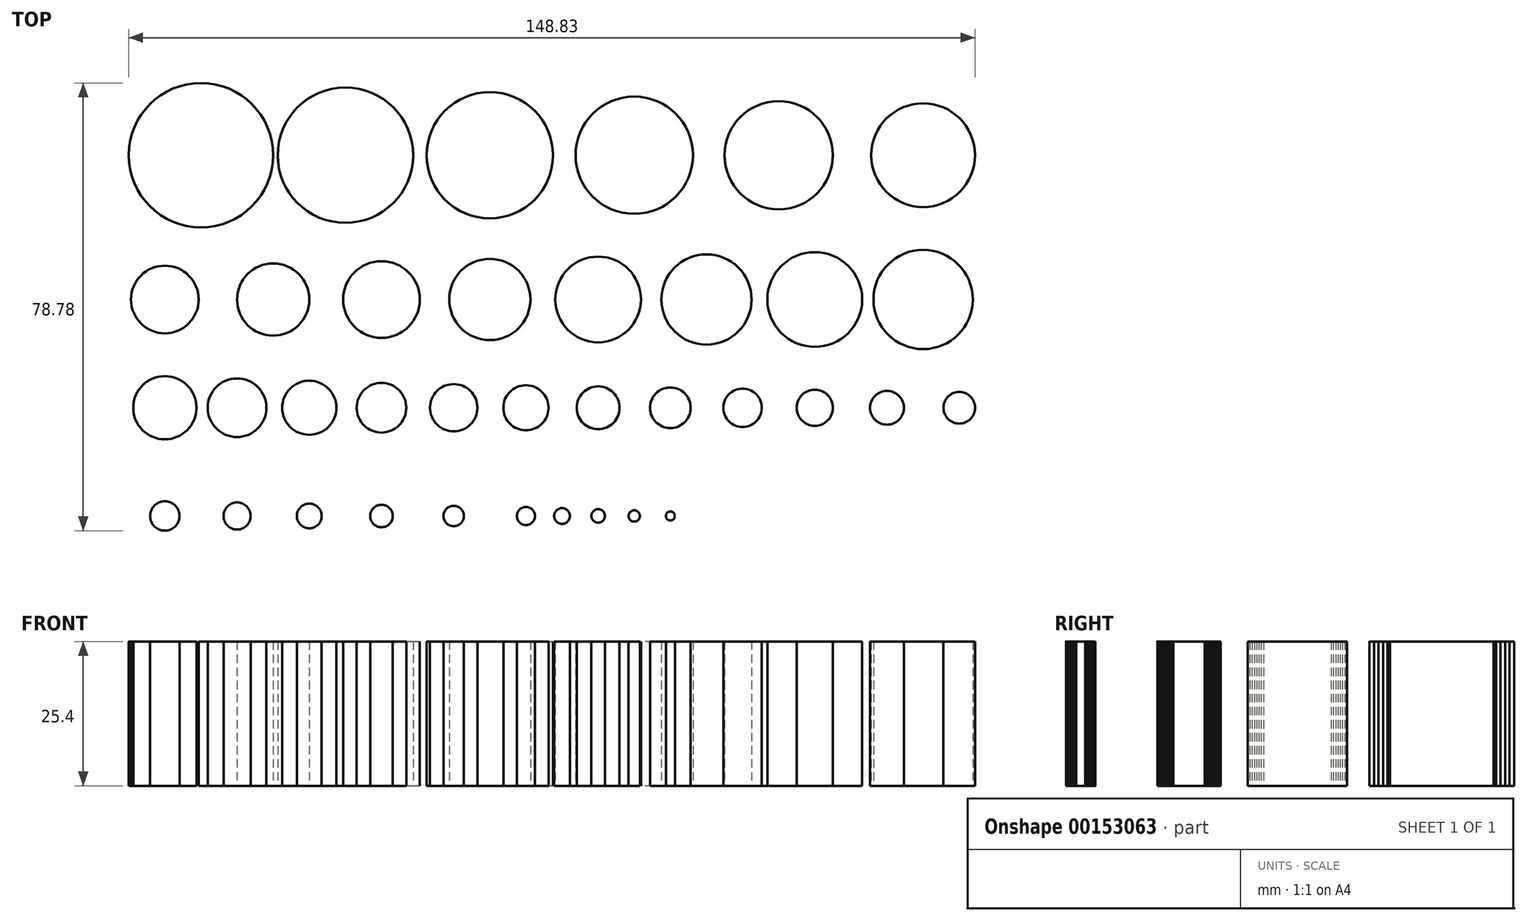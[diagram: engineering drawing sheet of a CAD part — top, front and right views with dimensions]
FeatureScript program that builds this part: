
annotation { "Feature Type Name" : "Feature", "Feature Type Description" : "" }
export const myFeature = defineFeature(function(context is Context, id is Id, definition is map)
    precondition{}
    {
        {
            var Q0;
            Q0=qCreatedBy(makeId("Top.planeOp"),FACE);
            var sketch = newSketch(context, id + "F0", { "sketchPlane" : qUnion([Q0])});
            skLineSegment(sketch, "E0", {"start": v(0, 82.73) * mm, "end": v(0, -103.9) * mm});
            skLineSegment(sketch, "E1.1.0.0", {"start": v(6.35, 82.73) * mm, "end": v(6.35, -103.9) * mm});
            skLineSegment(sketch, "E1.2.0.0", {"start": v(12.7, 82.73) * mm, "end": v(12.7, -103.9) * mm});
            skLineSegment(sketch, "E1.3.0.0", {"start": v(19.05, 82.73) * mm, "end": v(19.05, -103.9) * mm});
            skLineSegment(sketch, "E1.4.0.0", {"start": v(25.4, 82.73) * mm, "end": v(25.4, -103.9) * mm});
            skLineSegment(sketch, "E1.5.0.0", {"start": v(31.75, 82.73) * mm, "end": v(31.75, -103.9) * mm});
            skLineSegment(sketch, "E1.direction1", {"start": v(0, -103.9) * mm, "end": v(6.35, -103.9) * mm, "construction": true});
            skLineSegment(sketch, "E2.MirrorCS", {"start": v(63.5, 82.73) * mm, "end": v(63.5, -103.9) * mm});
            skLineSegment(sketch, "E3.MirrorCS", {"start": v(57.15, 82.73) * mm, "end": v(57.15, -103.9) * mm});
            skLineSegment(sketch, "E4.MirrorCS", {"start": v(50.8, 82.73) * mm, "end": v(50.8, -103.9) * mm});
            skLineSegment(sketch, "E5.MirrorCS", {"start": v(44.45, 82.73) * mm, "end": v(44.45, -103.9) * mm});
            skLineSegment(sketch, "E6.MirrorCS", {"start": v(38.1, 82.73) * mm, "end": v(38.1, -103.9) * mm});
            skLineSegment(sketch, "E7.MirrorCS", {"start": v(-6.35, 82.73) * mm, "end": v(-6.35, -103.9) * mm});
            skLineSegment(sketch, "E8.MirrorCS", {"start": v(-12.7, 82.73) * mm, "end": v(-12.7, -103.9) * mm});
            skLineSegment(sketch, "E9.MirrorCS", {"start": v(-19.05, 82.73) * mm, "end": v(-19.05, -103.9) * mm});
            skLineSegment(sketch, "E10.MirrorCS", {"start": v(-25.4, 82.73) * mm, "end": v(-25.4, -103.9) * mm});
            skLineSegment(sketch, "E11.MirrorCS", {"start": v(-31.75, 82.73) * mm, "end": v(-31.75, -103.9) * mm});
            skLineSegment(sketch, "E12.MirrorCS", {"start": v(-38.1, 82.73) * mm, "end": v(-38.1, -103.9) * mm});
            skLineSegment(sketch, "E13.MirrorCS", {"start": v(-44.45, 82.73) * mm, "end": v(-44.45, -103.9) * mm});
            skLineSegment(sketch, "E14.MirrorCS", {"start": v(-50.8, 82.73) * mm, "end": v(-50.8, -103.9) * mm});
            skLineSegment(sketch, "E15.MirrorCS", {"start": v(-57.15, 82.73) * mm, "end": v(-57.15, -103.9) * mm});
            skLineSegment(sketch, "E16.MirrorCS", {"start": v(-63.5, 82.73) * mm, "end": v(-63.5, -103.9) * mm});
            skLineSegment(sketch, "E17.MirrorCS", {"start": v(69.85, 82.73) * mm, "end": v(69.85, -103.9) * mm});
            skLineSegment(sketch, "E18.MirrorCS", {"start": v(76.2, 82.73) * mm, "end": v(76.2, -103.9) * mm});
            skLineSegment(sketch, "E19.MirrorCS", {"start": v(-69.85, 82.73) * mm, "end": v(-69.85, -103.9) * mm});
            skLineSegment(sketch, "E20.MirrorCS", {"start": v(-76.2, 82.73) * mm, "end": v(-76.2, -103.9) * mm});
            skLineSegment(sketch, "E21", {"start": v(-128.57, -86.78) * mm, "end": v(191.02, -86.78) * mm});
            skLineSegment(sketch, "E22.0.1.0", {"start": v(-128.57, -80.43) * mm, "end": v(191.02, -80.43) * mm});
            skLineSegment(sketch, "E22.0.2.0", {"start": v(-128.57, -74.08) * mm, "end": v(191.02, -74.08) * mm});
            skLineSegment(sketch, "E22.0.3.0", {"start": v(-128.57, -67.73) * mm, "end": v(191.02, -67.73) * mm});
            skLineSegment(sketch, "E22.0.4.0", {"start": v(-128.57, -61.38) * mm, "end": v(191.02, -61.38) * mm});
            skLineSegment(sketch, "E22.0.5.0", {"start": v(-128.57, -55.03) * mm, "end": v(191.02, -55.03) * mm});
            skLineSegment(sketch, "E22.0.6.0", {"start": v(-128.57, -48.68) * mm, "end": v(191.02, -48.68) * mm});
            skLineSegment(sketch, "E22.0.7.0", {"start": v(-128.57, -42.33) * mm, "end": v(191.02, -42.33) * mm});
            skLineSegment(sketch, "E22.0.8.0", {"start": v(-128.57, -35.98) * mm, "end": v(191.02, -35.98) * mm});
            skLineSegment(sketch, "E22.0.9.0", {"start": v(-128.57, -29.63) * mm, "end": v(191.02, -29.63) * mm});
            skLineSegment(sketch, "E22.0.10.0", {"start": v(-128.57, -23.28) * mm, "end": v(191.02, -23.28) * mm});
            skLineSegment(sketch, "E22.0.11.0", {"start": v(-128.57, -16.93) * mm, "end": v(191.02, -16.93) * mm});
            skLineSegment(sketch, "E22.0.12.0", {"start": v(-128.57, -10.58) * mm, "end": v(191.02, -10.58) * mm});
            skLineSegment(sketch, "E22.0.13.0", {"start": v(-128.57, -4.23) * mm, "end": v(191.02, -4.23) * mm});
            skLineSegment(sketch, "E22.0.14.0", {"start": v(-128.57, 2.12) * mm, "end": v(191.02, 2.12) * mm});
            skLineSegment(sketch, "E22.direction1", {"start": v(-128.57, -86.78) * mm, "end": v(-103.17, -86.78) * mm, "construction": true});
            skLineSegment(sketch, "E22.direction2", {"start": v(-128.57, -86.78) * mm, "end": v(-128.57, -80.43) * mm, "construction": true});
            skLineSegment(sketch, "E23.MirrorCS", {"start": v(-128.57, 27.52) * mm, "end": v(191.02, 27.52) * mm});
            skLineSegment(sketch, "E24.MirrorCS", {"start": v(-128.57, 21.17) * mm, "end": v(191.02, 21.17) * mm});
            skLineSegment(sketch, "E25.MirrorCS", {"start": v(-128.57, 78.32) * mm, "end": v(191.02, 78.32) * mm});
            skLineSegment(sketch, "E26.MirrorCS", {"start": v(-128.57, 71.97) * mm, "end": v(191.02, 71.97) * mm});
            skLineSegment(sketch, "E27.MirrorCS", {"start": v(-128.57, 65.62) * mm, "end": v(191.02, 65.62) * mm});
            skLineSegment(sketch, "E28.MirrorCS", {"start": v(-128.57, 59.27) * mm, "end": v(191.02, 59.27) * mm});
            skLineSegment(sketch, "E29.MirrorCS", {"start": v(-128.57, 52.92) * mm, "end": v(191.02, 52.92) * mm});
            skLineSegment(sketch, "E30.MirrorCS", {"start": v(-128.57, 46.57) * mm, "end": v(191.02, 46.57) * mm});
            skLineSegment(sketch, "E31.MirrorCS", {"start": v(-128.57, 40.22) * mm, "end": v(191.02, 40.22) * mm});
            skLineSegment(sketch, "E32.MirrorCS", {"start": v(-128.57, 33.87) * mm, "end": v(191.02, 33.87) * mm});
            skLineSegment(sketch, "E33.MirrorCS", {"start": v(-128.57, 8.47) * mm, "end": v(191.02, 8.47) * mm});
            skLineSegment(sketch, "E34.MirrorCS", {"start": v(-128.57, 14.82) * mm, "end": v(191.02, 14.82) * mm});
            skSolve(sketch);
        }
        {
            var Q0;
            Q0=qCreatedBy(makeId("Top.planeOp"),FACE);
            var sketch = newSketch(context, id + "F1", { "sketchPlane" : qUnion([Q0])});
            skPoint(sketch, "E35", {"position": v(-57.15, 71.97) * mm});
            skPoint(sketch, "E36.1.0.0", {"position": v(-50.8, 71.97) * mm});
            skPoint(sketch, "E36.2.0.0", {"position": v(-44.45, 71.97) * mm});
            skPoint(sketch, "E36.3.0.0", {"position": v(-38.1, 71.97) * mm});
            skPoint(sketch, "E36.4.0.0", {"position": v(-31.75, 71.97) * mm});
            skPoint(sketch, "E36.5.0.0", {"position": v(-25.4, 71.97) * mm});
            skPoint(sketch, "E36.6.0.0", {"position": v(-19.05, 71.97) * mm});
            skPoint(sketch, "E36.7.0.0", {"position": v(-12.7, 71.97) * mm});
            skPoint(sketch, "E36.8.0.0", {"position": v(-6.35, 71.97) * mm});
            skPoint(sketch, "E36.9.0.0", {"position": v(0, 71.97) * mm});
            skPoint(sketch, "E37.1.0.0", {"position": v(-63.5, 71.97) * mm});
            skPoint(sketch, "E37.2.0.0", {"position": v(-69.85, 71.97) * mm});
            skPoint(sketch, "E37.3.0.0", {"position": v(-76.2, 71.97) * mm});
            skLineSegment(sketch, "E37.direction1", {"start": v(-57.15, 71.97) * mm, "end": v(-63.5, 71.97) * mm, "construction": true});
            skPoint(sketch, "E38.0.1.0", {"position": v(-76.2, 65.62) * mm});
            skPoint(sketch, "E38.0.2.0", {"position": v(-76.2, 59.27) * mm});
            skPoint(sketch, "E38.0.3.0", {"position": v(-76.2, 52.92) * mm});
            skPoint(sketch, "E38.0.4.0", {"position": v(-76.2, 46.57) * mm});
            skPoint(sketch, "E38.0.5.0", {"position": v(-76.2, 40.22) * mm});
            skPoint(sketch, "E38.0.6.0", {"position": v(-76.2, 33.87) * mm});
            skPoint(sketch, "E38.0.7.0", {"position": v(-76.2, 27.52) * mm});
            skPoint(sketch, "E38.0.8.0", {"position": v(-76.2, 21.17) * mm});
            skPoint(sketch, "E38.0.9.0", {"position": v(-76.2, 14.82) * mm});
            skPoint(sketch, "E38.0.10.0", {"position": v(-76.2, 8.47) * mm});
            skPoint(sketch, "E38.0.11.0", {"position": v(-76.2, 2.12) * mm});
            skPoint(sketch, "E38.0.12.0", {"position": v(-76.2, -4.23) * mm});
            skPoint(sketch, "E38.0.13.0", {"position": v(-76.2, -10.58) * mm});
            skPoint(sketch, "E38.0.14.0", {"position": v(-76.2, -16.93) * mm});
            skPoint(sketch, "E38.0.15.0", {"position": v(-76.2, -23.28) * mm});
            skPoint(sketch, "E38.0.16.0", {"position": v(-76.2, -29.63) * mm});
            skPoint(sketch, "E38.0.17.0", {"position": v(-76.2, -35.98) * mm});
            skPoint(sketch, "E38.0.18.0", {"position": v(-76.2, -42.33) * mm});
            skPoint(sketch, "E38.0.19.0", {"position": v(-76.2, -48.68) * mm});
            skPoint(sketch, "E38.0.20.0", {"position": v(-76.2, -55.03) * mm});
            skPoint(sketch, "E38.0.21.0", {"position": v(-76.2, -61.38) * mm});
            skPoint(sketch, "E38.0.22.0", {"position": v(-76.2, -67.73) * mm});
            skPoint(sketch, "E38.0.23.0", {"position": v(-76.2, -74.08) * mm});
            skPoint(sketch, "E38.0.24.0", {"position": v(-76.2, -80.43) * mm});
            skPoint(sketch, "E38.0.25.0", {"position": v(-76.2, -86.78) * mm});
            skPoint(sketch, "E38.0.26.0", {"position": v(-76.2, -93.13) * mm});
            skPoint(sketch, "E38.0.27.0", {"position": v(-76.2, -99.48) * mm});
            skPoint(sketch, "E38.0.28.0", {"position": v(-76.2, -105.83) * mm});
            skPoint(sketch, "E38.0.29.0", {"position": v(-76.2, -112.18) * mm});
            skPoint(sketch, "E38.0.30.0", {"position": v(-76.2, -118.53) * mm});
            skPoint(sketch, "E38.0.31.0", {"position": v(-76.2, -124.88) * mm});
            skPoint(sketch, "E38.0.32.0", {"position": v(-76.2, -131.23) * mm});
            skPoint(sketch, "E38.0.33.0", {"position": v(-76.2, -137.58) * mm});
            skPoint(sketch, "E38.0.34.0", {"position": v(-76.2, -143.93) * mm});
            skPoint(sketch, "E38.0.35.0", {"position": v(-76.2, -150.28) * mm});
            skPoint(sketch, "E38.0.36.0", {"position": v(-76.2, -156.63) * mm});
            skPoint(sketch, "E38.0.37.0", {"position": v(-76.2, -162.98) * mm});
            skPoint(sketch, "E38.0.38.0", {"position": v(-76.2, -169.33) * mm});
            skPoint(sketch, "E38.0.39.0", {"position": v(-76.2, -175.68) * mm});
            skPoint(sketch, "E38.0.40.0", {"position": v(-76.2, -182.03) * mm});
            skPoint(sketch, "E38.0.41.0", {"position": v(-76.2, -188.38) * mm});
            skPoint(sketch, "E38.0.42.0", {"position": v(-76.2, -194.73) * mm});
            skPoint(sketch, "E38.0.43.0", {"position": v(-76.2, -201.08) * mm});
            skPoint(sketch, "E38.0.44.0", {"position": v(-76.2, -207.43) * mm});
            skPoint(sketch, "E38.0.45.0", {"position": v(-76.2, -213.78) * mm});
            skPoint(sketch, "E38.0.46.0", {"position": v(-76.2, -220.13) * mm});
            skPoint(sketch, "E38.0.47.0", {"position": v(-76.2, -226.48) * mm});
            skPoint(sketch, "E38.0.48.0", {"position": v(-76.2, -232.83) * mm});
            skPoint(sketch, "E38.0.49.0", {"position": v(-76.2, -239.18) * mm});
            skPoint(sketch, "E38.0.50.0", {"position": v(-76.2, -245.53) * mm});
            skPoint(sketch, "E38.0.51.0", {"position": v(-76.2, -251.88) * mm});
            skPoint(sketch, "E38.0.52.0", {"position": v(-76.2, -258.23) * mm});
            skPoint(sketch, "E38.0.53.0", {"position": v(-76.2, -264.58) * mm});
            skPoint(sketch, "E38.0.54.0", {"position": v(-76.2, -270.93) * mm});
            skPoint(sketch, "E38.0.55.0", {"position": v(-76.2, -277.28) * mm});
            skPoint(sketch, "E38.0.56.0", {"position": v(-76.2, -283.63) * mm});
            skPoint(sketch, "E38.0.57.0", {"position": v(-76.2, -289.98) * mm});
            skPoint(sketch, "E38.0.58.0", {"position": v(-76.2, -296.33) * mm});
            skPoint(sketch, "E38.0.59.0", {"position": v(-76.2, -302.68) * mm});
            skPoint(sketch, "E38.0.60.0", {"position": v(-76.2, -309.03) * mm});
            skPoint(sketch, "E38.0.61.0", {"position": v(-76.2, -315.38) * mm});
            skPoint(sketch, "E38.0.62.0", {"position": v(-76.2, -321.73) * mm});
            skPoint(sketch, "E38.0.63.0", {"position": v(-76.2, -328.08) * mm});
            skPoint(sketch, "E38.0.64.0", {"position": v(-76.2, -334.43) * mm});
            skPoint(sketch, "E38.0.65.0", {"position": v(-76.2, -340.78) * mm});
            skPoint(sketch, "E38.0.66.0", {"position": v(-76.2, -347.13) * mm});
            skPoint(sketch, "E38.0.67.0", {"position": v(-76.2, -353.48) * mm});
            skPoint(sketch, "E38.0.68.0", {"position": v(-76.2, -359.83) * mm});
            skPoint(sketch, "E38.0.69.0", {"position": v(-76.2, -366.18) * mm});
            skPoint(sketch, "E38.0.70.0", {"position": v(-76.2, -372.53) * mm});
            skPoint(sketch, "E38.0.71.0", {"position": v(-76.2, -378.88) * mm});
            skPoint(sketch, "E38.0.72.0", {"position": v(-76.2, -385.23) * mm});
            skPoint(sketch, "E38.0.73.0", {"position": v(-76.2, -391.58) * mm});
            skPoint(sketch, "E38.0.74.0", {"position": v(-76.2, -397.93) * mm});
            skPoint(sketch, "E38.0.75.0", {"position": v(-76.2, -404.28) * mm});
            skPoint(sketch, "E38.0.76.0", {"position": v(-76.2, -410.63) * mm});
            skPoint(sketch, "E38.0.77.0", {"position": v(-76.2, -416.98) * mm});
            skPoint(sketch, "E38.0.78.0", {"position": v(-76.2, -423.33) * mm});
            skPoint(sketch, "E38.0.79.0", {"position": v(-76.2, -429.68) * mm});
            skPoint(sketch, "E38.0.80.0", {"position": v(-76.2, -436.03) * mm});
            skPoint(sketch, "E38.0.81.0", {"position": v(-76.2, -442.38) * mm});
            skPoint(sketch, "E38.0.82.0", {"position": v(-76.2, -448.73) * mm});
            skPoint(sketch, "E38.0.83.0", {"position": v(-76.2, -455.08) * mm});
            skPoint(sketch, "E38.0.84.0", {"position": v(-76.2, -461.43) * mm});
            skPoint(sketch, "E38.0.85.0", {"position": v(-76.2, -467.78) * mm});
            skPoint(sketch, "E38.0.86.0", {"position": v(-76.2, -474.13) * mm});
            skPoint(sketch, "E38.0.87.0", {"position": v(-76.2, -480.48) * mm});
            skPoint(sketch, "E38.0.88.0", {"position": v(-76.2, -486.83) * mm});
            skPoint(sketch, "E38.0.89.0", {"position": v(-76.2, -493.18) * mm});
            skPoint(sketch, "E38.0.90.0", {"position": v(-76.2, -499.53) * mm});
            skPoint(sketch, "E38.0.91.0", {"position": v(-76.2, -505.88) * mm});
            skPoint(sketch, "E38.0.92.0", {"position": v(-76.2, -512.23) * mm});
            skPoint(sketch, "E38.0.93.0", {"position": v(-76.2, -518.58) * mm});
            skPoint(sketch, "E38.0.94.0", {"position": v(-76.2, -524.93) * mm});
            skPoint(sketch, "E38.0.95.0", {"position": v(-76.2, -531.28) * mm});
            skPoint(sketch, "E38.0.96.0", {"position": v(-76.2, -537.63) * mm});
            skPoint(sketch, "E38.0.97.0", {"position": v(-76.2, -543.98) * mm});
            skPoint(sketch, "E38.0.98.0", {"position": v(-76.2, -550.33) * mm});
            skPoint(sketch, "E38.0.99.0", {"position": v(-76.2, -556.68) * mm});
            skPoint(sketch, "E38.1.1.0", {"position": v(-69.85, 65.62) * mm});
            skPoint(sketch, "E38.1.2.0", {"position": v(-69.85, 59.27) * mm});
            skPoint(sketch, "E38.1.3.0", {"position": v(-69.85, 52.92) * mm});
            skPoint(sketch, "E38.1.4.0", {"position": v(-69.85, 46.57) * mm});
            skPoint(sketch, "E38.1.5.0", {"position": v(-69.85, 40.22) * mm});
            skPoint(sketch, "E38.1.6.0", {"position": v(-69.85, 33.87) * mm});
            skPoint(sketch, "E38.1.7.0", {"position": v(-69.85, 27.52) * mm});
            skPoint(sketch, "E38.1.8.0", {"position": v(-69.85, 21.17) * mm});
            skPoint(sketch, "E38.1.9.0", {"position": v(-69.85, 14.82) * mm});
            skPoint(sketch, "E38.1.10.0", {"position": v(-69.85, 8.47) * mm});
            skPoint(sketch, "E38.1.11.0", {"position": v(-69.85, 2.12) * mm});
            skPoint(sketch, "E38.1.12.0", {"position": v(-69.85, -4.23) * mm});
            skPoint(sketch, "E38.1.13.0", {"position": v(-69.85, -10.58) * mm});
            skPoint(sketch, "E38.1.14.0", {"position": v(-69.85, -16.93) * mm});
            skPoint(sketch, "E38.1.15.0", {"position": v(-69.85, -23.28) * mm});
            skPoint(sketch, "E38.1.16.0", {"position": v(-69.85, -29.63) * mm});
            skPoint(sketch, "E38.1.17.0", {"position": v(-69.85, -35.98) * mm});
            skPoint(sketch, "E38.1.18.0", {"position": v(-69.85, -42.33) * mm});
            skPoint(sketch, "E38.1.19.0", {"position": v(-69.85, -48.68) * mm});
            skPoint(sketch, "E38.1.20.0", {"position": v(-69.85, -55.03) * mm});
            skPoint(sketch, "E38.1.21.0", {"position": v(-69.85, -61.38) * mm});
            skPoint(sketch, "E38.1.22.0", {"position": v(-69.85, -67.73) * mm});
            skPoint(sketch, "E38.1.23.0", {"position": v(-69.85, -74.08) * mm});
            skPoint(sketch, "E38.1.24.0", {"position": v(-69.85, -80.43) * mm});
            skPoint(sketch, "E38.1.25.0", {"position": v(-69.85, -86.78) * mm});
            skPoint(sketch, "E38.1.26.0", {"position": v(-69.85, -93.13) * mm});
            skPoint(sketch, "E38.1.27.0", {"position": v(-69.85, -99.48) * mm});
            skPoint(sketch, "E38.1.28.0", {"position": v(-69.85, -105.83) * mm});
            skPoint(sketch, "E38.1.29.0", {"position": v(-69.85, -112.18) * mm});
            skPoint(sketch, "E38.1.30.0", {"position": v(-69.85, -118.53) * mm});
            skPoint(sketch, "E38.1.31.0", {"position": v(-69.85, -124.88) * mm});
            skPoint(sketch, "E38.1.32.0", {"position": v(-69.85, -131.23) * mm});
            skPoint(sketch, "E38.1.33.0", {"position": v(-69.85, -137.58) * mm});
            skPoint(sketch, "E38.1.34.0", {"position": v(-69.85, -143.93) * mm});
            skPoint(sketch, "E38.1.35.0", {"position": v(-69.85, -150.28) * mm});
            skPoint(sketch, "E38.1.36.0", {"position": v(-69.85, -156.63) * mm});
            skPoint(sketch, "E38.1.37.0", {"position": v(-69.85, -162.98) * mm});
            skPoint(sketch, "E38.1.38.0", {"position": v(-69.85, -169.33) * mm});
            skPoint(sketch, "E38.1.39.0", {"position": v(-69.85, -175.68) * mm});
            skPoint(sketch, "E38.1.40.0", {"position": v(-69.85, -182.03) * mm});
            skPoint(sketch, "E38.1.41.0", {"position": v(-69.85, -188.38) * mm});
            skPoint(sketch, "E38.1.42.0", {"position": v(-69.85, -194.73) * mm});
            skPoint(sketch, "E38.1.43.0", {"position": v(-69.85, -201.08) * mm});
            skPoint(sketch, "E38.1.44.0", {"position": v(-69.85, -207.43) * mm});
            skPoint(sketch, "E38.1.45.0", {"position": v(-69.85, -213.78) * mm});
            skPoint(sketch, "E38.1.46.0", {"position": v(-69.85, -220.13) * mm});
            skPoint(sketch, "E38.1.47.0", {"position": v(-69.85, -226.48) * mm});
            skPoint(sketch, "E38.1.48.0", {"position": v(-69.85, -232.83) * mm});
            skPoint(sketch, "E38.1.49.0", {"position": v(-69.85, -239.18) * mm});
            skPoint(sketch, "E38.1.50.0", {"position": v(-69.85, -245.53) * mm});
            skPoint(sketch, "E38.1.51.0", {"position": v(-69.85, -251.88) * mm});
            skPoint(sketch, "E38.1.52.0", {"position": v(-69.85, -258.23) * mm});
            skPoint(sketch, "E38.1.53.0", {"position": v(-69.85, -264.58) * mm});
            skPoint(sketch, "E38.1.54.0", {"position": v(-69.85, -270.93) * mm});
            skPoint(sketch, "E38.1.55.0", {"position": v(-69.85, -277.28) * mm});
            skPoint(sketch, "E38.1.56.0", {"position": v(-69.85, -283.63) * mm});
            skPoint(sketch, "E38.1.57.0", {"position": v(-69.85, -289.98) * mm});
            skPoint(sketch, "E38.1.58.0", {"position": v(-69.85, -296.33) * mm});
            skPoint(sketch, "E38.1.59.0", {"position": v(-69.85, -302.68) * mm});
            skPoint(sketch, "E38.1.60.0", {"position": v(-69.85, -309.03) * mm});
            skPoint(sketch, "E38.1.61.0", {"position": v(-69.85, -315.38) * mm});
            skPoint(sketch, "E38.1.62.0", {"position": v(-69.85, -321.73) * mm});
            skPoint(sketch, "E38.1.63.0", {"position": v(-69.85, -328.08) * mm});
            skPoint(sketch, "E38.1.64.0", {"position": v(-69.85, -334.43) * mm});
            skPoint(sketch, "E38.1.65.0", {"position": v(-69.85, -340.78) * mm});
            skPoint(sketch, "E38.1.66.0", {"position": v(-69.85, -347.13) * mm});
            skPoint(sketch, "E38.1.67.0", {"position": v(-69.85, -353.48) * mm});
            skPoint(sketch, "E38.1.68.0", {"position": v(-69.85, -359.83) * mm});
            skPoint(sketch, "E38.1.69.0", {"position": v(-69.85, -366.18) * mm});
            skPoint(sketch, "E38.1.70.0", {"position": v(-69.85, -372.53) * mm});
            skPoint(sketch, "E38.1.71.0", {"position": v(-69.85, -378.88) * mm});
            skPoint(sketch, "E38.1.72.0", {"position": v(-69.85, -385.23) * mm});
            skPoint(sketch, "E38.1.73.0", {"position": v(-69.85, -391.58) * mm});
            skPoint(sketch, "E38.1.74.0", {"position": v(-69.85, -397.93) * mm});
            skPoint(sketch, "E38.1.75.0", {"position": v(-69.85, -404.28) * mm});
            skPoint(sketch, "E38.1.76.0", {"position": v(-69.85, -410.63) * mm});
            skPoint(sketch, "E38.1.77.0", {"position": v(-69.85, -416.98) * mm});
            skPoint(sketch, "E38.1.78.0", {"position": v(-69.85, -423.33) * mm});
            skPoint(sketch, "E38.1.79.0", {"position": v(-69.85, -429.68) * mm});
            skPoint(sketch, "E38.1.80.0", {"position": v(-69.85, -436.03) * mm});
            skPoint(sketch, "E38.1.81.0", {"position": v(-69.85, -442.38) * mm});
            skPoint(sketch, "E38.1.82.0", {"position": v(-69.85, -448.73) * mm});
            skPoint(sketch, "E38.1.83.0", {"position": v(-69.85, -455.08) * mm});
            skPoint(sketch, "E38.1.84.0", {"position": v(-69.85, -461.43) * mm});
            skPoint(sketch, "E38.1.85.0", {"position": v(-69.85, -467.78) * mm});
            skPoint(sketch, "E38.1.86.0", {"position": v(-69.85, -474.13) * mm});
            skPoint(sketch, "E38.1.87.0", {"position": v(-69.85, -480.48) * mm});
            skPoint(sketch, "E38.1.88.0", {"position": v(-69.85, -486.83) * mm});
            skPoint(sketch, "E38.1.89.0", {"position": v(-69.85, -493.18) * mm});
            skPoint(sketch, "E38.1.90.0", {"position": v(-69.85, -499.53) * mm});
            skPoint(sketch, "E38.1.91.0", {"position": v(-69.85, -505.88) * mm});
            skPoint(sketch, "E38.1.92.0", {"position": v(-69.85, -512.23) * mm});
            skPoint(sketch, "E38.1.93.0", {"position": v(-69.85, -518.58) * mm});
            skPoint(sketch, "E38.1.94.0", {"position": v(-69.85, -524.93) * mm});
            skPoint(sketch, "E38.1.95.0", {"position": v(-69.85, -531.28) * mm});
            skPoint(sketch, "E38.1.96.0", {"position": v(-69.85, -537.63) * mm});
            skPoint(sketch, "E38.1.97.0", {"position": v(-69.85, -543.98) * mm});
            skPoint(sketch, "E38.1.98.0", {"position": v(-69.85, -550.33) * mm});
            skPoint(sketch, "E38.1.99.0", {"position": v(-69.85, -556.68) * mm});
            skPoint(sketch, "E38.2.1.0", {"position": v(-63.5, 65.62) * mm});
            skPoint(sketch, "E38.2.2.0", {"position": v(-63.5, 59.27) * mm});
            skPoint(sketch, "E38.2.3.0", {"position": v(-63.5, 52.92) * mm});
            skPoint(sketch, "E38.2.4.0", {"position": v(-63.5, 46.57) * mm});
            skPoint(sketch, "E38.2.5.0", {"position": v(-63.5, 40.22) * mm});
            skPoint(sketch, "E38.2.6.0", {"position": v(-63.5, 33.87) * mm});
            skPoint(sketch, "E38.2.7.0", {"position": v(-63.5, 27.52) * mm});
            skPoint(sketch, "E38.2.8.0", {"position": v(-63.5, 21.17) * mm});
            skPoint(sketch, "E38.2.9.0", {"position": v(-63.5, 14.82) * mm});
            skPoint(sketch, "E38.2.10.0", {"position": v(-63.5, 8.47) * mm});
            skPoint(sketch, "E38.2.11.0", {"position": v(-63.5, 2.12) * mm});
            skPoint(sketch, "E38.2.12.0", {"position": v(-63.5, -4.23) * mm});
            skPoint(sketch, "E38.2.13.0", {"position": v(-63.5, -10.58) * mm});
            skPoint(sketch, "E38.2.14.0", {"position": v(-63.5, -16.93) * mm});
            skPoint(sketch, "E38.2.15.0", {"position": v(-63.5, -23.28) * mm});
            skPoint(sketch, "E38.2.16.0", {"position": v(-63.5, -29.63) * mm});
            skPoint(sketch, "E38.2.17.0", {"position": v(-63.5, -35.98) * mm});
            skPoint(sketch, "E38.2.18.0", {"position": v(-63.5, -42.33) * mm});
            skPoint(sketch, "E38.2.19.0", {"position": v(-63.5, -48.68) * mm});
            skPoint(sketch, "E38.2.20.0", {"position": v(-63.5, -55.03) * mm});
            skPoint(sketch, "E38.2.21.0", {"position": v(-63.5, -61.38) * mm});
            skPoint(sketch, "E38.2.22.0", {"position": v(-63.5, -67.73) * mm});
            skPoint(sketch, "E38.2.23.0", {"position": v(-63.5, -74.08) * mm});
            skPoint(sketch, "E38.2.24.0", {"position": v(-63.5, -80.43) * mm});
            skPoint(sketch, "E38.2.25.0", {"position": v(-63.5, -86.78) * mm});
            skPoint(sketch, "E38.2.26.0", {"position": v(-63.5, -93.13) * mm});
            skPoint(sketch, "E38.2.27.0", {"position": v(-63.5, -99.48) * mm});
            skPoint(sketch, "E38.2.28.0", {"position": v(-63.5, -105.83) * mm});
            skPoint(sketch, "E38.2.29.0", {"position": v(-63.5, -112.18) * mm});
            skPoint(sketch, "E38.2.30.0", {"position": v(-63.5, -118.53) * mm});
            skPoint(sketch, "E38.2.31.0", {"position": v(-63.5, -124.88) * mm});
            skPoint(sketch, "E38.2.32.0", {"position": v(-63.5, -131.23) * mm});
            skPoint(sketch, "E38.2.33.0", {"position": v(-63.5, -137.58) * mm});
            skPoint(sketch, "E38.2.34.0", {"position": v(-63.5, -143.93) * mm});
            skPoint(sketch, "E38.2.35.0", {"position": v(-63.5, -150.28) * mm});
            skPoint(sketch, "E38.2.36.0", {"position": v(-63.5, -156.63) * mm});
            skPoint(sketch, "E38.2.37.0", {"position": v(-63.5, -162.98) * mm});
            skPoint(sketch, "E38.2.38.0", {"position": v(-63.5, -169.33) * mm});
            skPoint(sketch, "E38.2.39.0", {"position": v(-63.5, -175.68) * mm});
            skPoint(sketch, "E38.2.40.0", {"position": v(-63.5, -182.03) * mm});
            skPoint(sketch, "E38.2.41.0", {"position": v(-63.5, -188.38) * mm});
            skPoint(sketch, "E38.2.42.0", {"position": v(-63.5, -194.73) * mm});
            skPoint(sketch, "E38.2.43.0", {"position": v(-63.5, -201.08) * mm});
            skPoint(sketch, "E38.2.44.0", {"position": v(-63.5, -207.43) * mm});
            skPoint(sketch, "E38.2.45.0", {"position": v(-63.5, -213.78) * mm});
            skPoint(sketch, "E38.2.46.0", {"position": v(-63.5, -220.13) * mm});
            skPoint(sketch, "E38.2.47.0", {"position": v(-63.5, -226.48) * mm});
            skPoint(sketch, "E38.2.48.0", {"position": v(-63.5, -232.83) * mm});
            skPoint(sketch, "E38.2.49.0", {"position": v(-63.5, -239.18) * mm});
            skPoint(sketch, "E38.2.50.0", {"position": v(-63.5, -245.53) * mm});
            skPoint(sketch, "E38.2.51.0", {"position": v(-63.5, -251.88) * mm});
            skPoint(sketch, "E38.2.52.0", {"position": v(-63.5, -258.23) * mm});
            skPoint(sketch, "E38.2.53.0", {"position": v(-63.5, -264.58) * mm});
            skPoint(sketch, "E38.2.54.0", {"position": v(-63.5, -270.93) * mm});
            skPoint(sketch, "E38.2.55.0", {"position": v(-63.5, -277.28) * mm});
            skPoint(sketch, "E38.2.56.0", {"position": v(-63.5, -283.63) * mm});
            skPoint(sketch, "E38.2.57.0", {"position": v(-63.5, -289.98) * mm});
            skPoint(sketch, "E38.2.58.0", {"position": v(-63.5, -296.33) * mm});
            skPoint(sketch, "E38.2.59.0", {"position": v(-63.5, -302.68) * mm});
            skPoint(sketch, "E38.2.60.0", {"position": v(-63.5, -309.03) * mm});
            skPoint(sketch, "E38.2.61.0", {"position": v(-63.5, -315.38) * mm});
            skPoint(sketch, "E38.2.62.0", {"position": v(-63.5, -321.73) * mm});
            skPoint(sketch, "E38.2.63.0", {"position": v(-63.5, -328.08) * mm});
            skPoint(sketch, "E38.2.64.0", {"position": v(-63.5, -334.43) * mm});
            skPoint(sketch, "E38.2.65.0", {"position": v(-63.5, -340.78) * mm});
            skPoint(sketch, "E38.2.66.0", {"position": v(-63.5, -347.13) * mm});
            skPoint(sketch, "E38.2.67.0", {"position": v(-63.5, -353.48) * mm});
            skPoint(sketch, "E38.2.68.0", {"position": v(-63.5, -359.83) * mm});
            skPoint(sketch, "E38.2.69.0", {"position": v(-63.5, -366.18) * mm});
            skPoint(sketch, "E38.2.70.0", {"position": v(-63.5, -372.53) * mm});
            skPoint(sketch, "E38.2.71.0", {"position": v(-63.5, -378.88) * mm});
            skPoint(sketch, "E38.2.72.0", {"position": v(-63.5, -385.23) * mm});
            skPoint(sketch, "E38.2.73.0", {"position": v(-63.5, -391.58) * mm});
            skPoint(sketch, "E38.2.74.0", {"position": v(-63.5, -397.93) * mm});
            skPoint(sketch, "E38.2.75.0", {"position": v(-63.5, -404.28) * mm});
            skPoint(sketch, "E38.2.76.0", {"position": v(-63.5, -410.63) * mm});
            skPoint(sketch, "E38.2.77.0", {"position": v(-63.5, -416.98) * mm});
            skPoint(sketch, "E38.2.78.0", {"position": v(-63.5, -423.33) * mm});
            skPoint(sketch, "E38.2.79.0", {"position": v(-63.5, -429.68) * mm});
            skPoint(sketch, "E38.2.80.0", {"position": v(-63.5, -436.03) * mm});
            skPoint(sketch, "E38.2.81.0", {"position": v(-63.5, -442.38) * mm});
            skPoint(sketch, "E38.2.82.0", {"position": v(-63.5, -448.73) * mm});
            skPoint(sketch, "E38.2.83.0", {"position": v(-63.5, -455.08) * mm});
            skPoint(sketch, "E38.2.84.0", {"position": v(-63.5, -461.43) * mm});
            skPoint(sketch, "E38.2.85.0", {"position": v(-63.5, -467.78) * mm});
            skPoint(sketch, "E38.2.86.0", {"position": v(-63.5, -474.13) * mm});
            skPoint(sketch, "E38.2.87.0", {"position": v(-63.5, -480.48) * mm});
            skPoint(sketch, "E38.2.88.0", {"position": v(-63.5, -486.83) * mm});
            skPoint(sketch, "E38.2.89.0", {"position": v(-63.5, -493.18) * mm});
            skPoint(sketch, "E38.2.90.0", {"position": v(-63.5, -499.53) * mm});
            skPoint(sketch, "E38.2.91.0", {"position": v(-63.5, -505.88) * mm});
            skPoint(sketch, "E38.2.92.0", {"position": v(-63.5, -512.23) * mm});
            skPoint(sketch, "E38.2.93.0", {"position": v(-63.5, -518.58) * mm});
            skPoint(sketch, "E38.2.94.0", {"position": v(-63.5, -524.93) * mm});
            skPoint(sketch, "E38.2.95.0", {"position": v(-63.5, -531.28) * mm});
            skPoint(sketch, "E38.2.96.0", {"position": v(-63.5, -537.63) * mm});
            skPoint(sketch, "E38.2.97.0", {"position": v(-63.5, -543.98) * mm});
            skPoint(sketch, "E38.2.98.0", {"position": v(-63.5, -550.33) * mm});
            skPoint(sketch, "E38.2.99.0", {"position": v(-63.5, -556.68) * mm});
            skPoint(sketch, "E38.3.1.0", {"position": v(-57.15, 65.62) * mm});
            skPoint(sketch, "E38.3.2.0", {"position": v(-57.15, 59.27) * mm});
            skPoint(sketch, "E38.3.3.0", {"position": v(-57.15, 52.92) * mm});
            skPoint(sketch, "E38.3.4.0", {"position": v(-57.15, 46.57) * mm});
            skPoint(sketch, "E38.3.5.0", {"position": v(-57.15, 40.22) * mm});
            skPoint(sketch, "E38.3.6.0", {"position": v(-57.15, 33.87) * mm});
            skPoint(sketch, "E38.3.7.0", {"position": v(-57.15, 27.52) * mm});
            skPoint(sketch, "E38.3.8.0", {"position": v(-57.15, 21.17) * mm});
            skPoint(sketch, "E38.3.9.0", {"position": v(-57.15, 14.82) * mm});
            skPoint(sketch, "E38.3.10.0", {"position": v(-57.15, 8.47) * mm});
            skPoint(sketch, "E38.3.11.0", {"position": v(-57.15, 2.12) * mm});
            skPoint(sketch, "E38.3.12.0", {"position": v(-57.15, -4.23) * mm});
            skPoint(sketch, "E38.3.13.0", {"position": v(-57.15, -10.58) * mm});
            skPoint(sketch, "E38.3.14.0", {"position": v(-57.15, -16.93) * mm});
            skPoint(sketch, "E38.3.15.0", {"position": v(-57.15, -23.28) * mm});
            skPoint(sketch, "E38.3.16.0", {"position": v(-57.15, -29.63) * mm});
            skPoint(sketch, "E38.3.17.0", {"position": v(-57.15, -35.98) * mm});
            skPoint(sketch, "E38.3.18.0", {"position": v(-57.15, -42.33) * mm});
            skPoint(sketch, "E38.3.19.0", {"position": v(-57.15, -48.68) * mm});
            skPoint(sketch, "E38.3.20.0", {"position": v(-57.15, -55.03) * mm});
            skPoint(sketch, "E38.3.21.0", {"position": v(-57.15, -61.38) * mm});
            skPoint(sketch, "E38.3.22.0", {"position": v(-57.15, -67.73) * mm});
            skPoint(sketch, "E38.3.23.0", {"position": v(-57.15, -74.08) * mm});
            skPoint(sketch, "E38.3.24.0", {"position": v(-57.15, -80.43) * mm});
            skPoint(sketch, "E38.3.25.0", {"position": v(-57.15, -86.78) * mm});
            skPoint(sketch, "E38.3.26.0", {"position": v(-57.15, -93.13) * mm});
            skPoint(sketch, "E38.3.27.0", {"position": v(-57.15, -99.48) * mm});
            skPoint(sketch, "E38.3.28.0", {"position": v(-57.15, -105.83) * mm});
            skPoint(sketch, "E38.3.29.0", {"position": v(-57.15, -112.18) * mm});
            skPoint(sketch, "E38.3.30.0", {"position": v(-57.15, -118.53) * mm});
            skPoint(sketch, "E38.3.31.0", {"position": v(-57.15, -124.88) * mm});
            skPoint(sketch, "E38.3.32.0", {"position": v(-57.15, -131.23) * mm});
            skPoint(sketch, "E38.3.33.0", {"position": v(-57.15, -137.58) * mm});
            skPoint(sketch, "E38.3.34.0", {"position": v(-57.15, -143.93) * mm});
            skPoint(sketch, "E38.3.35.0", {"position": v(-57.15, -150.28) * mm});
            skPoint(sketch, "E38.3.36.0", {"position": v(-57.15, -156.63) * mm});
            skPoint(sketch, "E38.3.37.0", {"position": v(-57.15, -162.98) * mm});
            skPoint(sketch, "E38.3.38.0", {"position": v(-57.15, -169.33) * mm});
            skPoint(sketch, "E38.3.39.0", {"position": v(-57.15, -175.68) * mm});
            skPoint(sketch, "E38.3.40.0", {"position": v(-57.15, -182.03) * mm});
            skPoint(sketch, "E38.3.41.0", {"position": v(-57.15, -188.38) * mm});
            skPoint(sketch, "E38.3.42.0", {"position": v(-57.15, -194.73) * mm});
            skPoint(sketch, "E38.3.43.0", {"position": v(-57.15, -201.08) * mm});
            skPoint(sketch, "E38.3.44.0", {"position": v(-57.15, -207.43) * mm});
            skPoint(sketch, "E38.3.45.0", {"position": v(-57.15, -213.78) * mm});
            skPoint(sketch, "E38.3.46.0", {"position": v(-57.15, -220.13) * mm});
            skPoint(sketch, "E38.3.47.0", {"position": v(-57.15, -226.48) * mm});
            skPoint(sketch, "E38.3.48.0", {"position": v(-57.15, -232.83) * mm});
            skPoint(sketch, "E38.3.49.0", {"position": v(-57.15, -239.18) * mm});
            skPoint(sketch, "E38.3.50.0", {"position": v(-57.15, -245.53) * mm});
            skPoint(sketch, "E38.3.51.0", {"position": v(-57.15, -251.88) * mm});
            skPoint(sketch, "E38.3.52.0", {"position": v(-57.15, -258.23) * mm});
            skPoint(sketch, "E38.3.53.0", {"position": v(-57.15, -264.58) * mm});
            skPoint(sketch, "E38.3.54.0", {"position": v(-57.15, -270.93) * mm});
            skPoint(sketch, "E38.3.55.0", {"position": v(-57.15, -277.28) * mm});
            skPoint(sketch, "E38.3.56.0", {"position": v(-57.15, -283.63) * mm});
            skPoint(sketch, "E38.3.57.0", {"position": v(-57.15, -289.98) * mm});
            skPoint(sketch, "E38.3.58.0", {"position": v(-57.15, -296.33) * mm});
            skPoint(sketch, "E38.3.59.0", {"position": v(-57.15, -302.68) * mm});
            skPoint(sketch, "E38.3.60.0", {"position": v(-57.15, -309.03) * mm});
            skPoint(sketch, "E38.3.61.0", {"position": v(-57.15, -315.38) * mm});
            skPoint(sketch, "E38.3.62.0", {"position": v(-57.15, -321.73) * mm});
            skPoint(sketch, "E38.3.63.0", {"position": v(-57.15, -328.08) * mm});
            skPoint(sketch, "E38.3.64.0", {"position": v(-57.15, -334.43) * mm});
            skPoint(sketch, "E38.3.65.0", {"position": v(-57.15, -340.78) * mm});
            skPoint(sketch, "E38.3.66.0", {"position": v(-57.15, -347.13) * mm});
            skPoint(sketch, "E38.3.67.0", {"position": v(-57.15, -353.48) * mm});
            skPoint(sketch, "E38.3.68.0", {"position": v(-57.15, -359.83) * mm});
            skPoint(sketch, "E38.3.69.0", {"position": v(-57.15, -366.18) * mm});
            skPoint(sketch, "E38.3.70.0", {"position": v(-57.15, -372.53) * mm});
            skPoint(sketch, "E38.3.71.0", {"position": v(-57.15, -378.88) * mm});
            skPoint(sketch, "E38.3.72.0", {"position": v(-57.15, -385.23) * mm});
            skPoint(sketch, "E38.3.73.0", {"position": v(-57.15, -391.58) * mm});
            skPoint(sketch, "E38.3.74.0", {"position": v(-57.15, -397.93) * mm});
            skPoint(sketch, "E38.3.75.0", {"position": v(-57.15, -404.28) * mm});
            skPoint(sketch, "E38.3.76.0", {"position": v(-57.15, -410.63) * mm});
            skPoint(sketch, "E38.3.77.0", {"position": v(-57.15, -416.98) * mm});
            skPoint(sketch, "E38.3.78.0", {"position": v(-57.15, -423.33) * mm});
            skPoint(sketch, "E38.3.79.0", {"position": v(-57.15, -429.68) * mm});
            skPoint(sketch, "E38.3.80.0", {"position": v(-57.15, -436.03) * mm});
            skPoint(sketch, "E38.3.81.0", {"position": v(-57.15, -442.38) * mm});
            skPoint(sketch, "E38.3.82.0", {"position": v(-57.15, -448.73) * mm});
            skPoint(sketch, "E38.3.83.0", {"position": v(-57.15, -455.08) * mm});
            skPoint(sketch, "E38.3.84.0", {"position": v(-57.15, -461.43) * mm});
            skPoint(sketch, "E38.3.85.0", {"position": v(-57.15, -467.78) * mm});
            skPoint(sketch, "E38.3.86.0", {"position": v(-57.15, -474.13) * mm});
            skPoint(sketch, "E38.3.87.0", {"position": v(-57.15, -480.48) * mm});
            skPoint(sketch, "E38.3.88.0", {"position": v(-57.15, -486.83) * mm});
            skPoint(sketch, "E38.3.89.0", {"position": v(-57.15, -493.18) * mm});
            skPoint(sketch, "E38.3.90.0", {"position": v(-57.15, -499.53) * mm});
            skPoint(sketch, "E38.3.91.0", {"position": v(-57.15, -505.88) * mm});
            skPoint(sketch, "E38.3.92.0", {"position": v(-57.15, -512.23) * mm});
            skPoint(sketch, "E38.3.93.0", {"position": v(-57.15, -518.58) * mm});
            skPoint(sketch, "E38.3.94.0", {"position": v(-57.15, -524.93) * mm});
            skPoint(sketch, "E38.3.95.0", {"position": v(-57.15, -531.28) * mm});
            skPoint(sketch, "E38.3.96.0", {"position": v(-57.15, -537.63) * mm});
            skPoint(sketch, "E38.3.97.0", {"position": v(-57.15, -543.98) * mm});
            skPoint(sketch, "E38.3.98.0", {"position": v(-57.15, -550.33) * mm});
            skPoint(sketch, "E38.3.99.0", {"position": v(-57.15, -556.68) * mm});
            skPoint(sketch, "E38.4.1.0", {"position": v(-50.8, 65.62) * mm});
            skPoint(sketch, "E38.4.2.0", {"position": v(-50.8, 59.27) * mm});
            skPoint(sketch, "E38.4.3.0", {"position": v(-50.8, 52.92) * mm});
            skPoint(sketch, "E38.4.4.0", {"position": v(-50.8, 46.57) * mm});
            skPoint(sketch, "E38.4.5.0", {"position": v(-50.8, 40.22) * mm});
            skPoint(sketch, "E38.4.6.0", {"position": v(-50.8, 33.87) * mm});
            skPoint(sketch, "E38.4.7.0", {"position": v(-50.8, 27.52) * mm});
            skPoint(sketch, "E38.4.8.0", {"position": v(-50.8, 21.17) * mm});
            skPoint(sketch, "E38.4.9.0", {"position": v(-50.8, 14.82) * mm});
            skPoint(sketch, "E38.4.10.0", {"position": v(-50.8, 8.47) * mm});
            skPoint(sketch, "E38.4.11.0", {"position": v(-50.8, 2.12) * mm});
            skPoint(sketch, "E38.4.12.0", {"position": v(-50.8, -4.23) * mm});
            skPoint(sketch, "E38.4.13.0", {"position": v(-50.8, -10.58) * mm});
            skPoint(sketch, "E38.4.14.0", {"position": v(-50.8, -16.93) * mm});
            skPoint(sketch, "E38.4.15.0", {"position": v(-50.8, -23.28) * mm});
            skPoint(sketch, "E38.4.16.0", {"position": v(-50.8, -29.63) * mm});
            skPoint(sketch, "E38.4.17.0", {"position": v(-50.8, -35.98) * mm});
            skPoint(sketch, "E38.4.18.0", {"position": v(-50.8, -42.33) * mm});
            skPoint(sketch, "E38.4.19.0", {"position": v(-50.8, -48.68) * mm});
            skPoint(sketch, "E38.4.20.0", {"position": v(-50.8, -55.03) * mm});
            skPoint(sketch, "E38.4.21.0", {"position": v(-50.8, -61.38) * mm});
            skPoint(sketch, "E38.4.22.0", {"position": v(-50.8, -67.73) * mm});
            skPoint(sketch, "E38.4.23.0", {"position": v(-50.8, -74.08) * mm});
            skPoint(sketch, "E38.4.24.0", {"position": v(-50.8, -80.43) * mm});
            skPoint(sketch, "E38.4.25.0", {"position": v(-50.8, -86.78) * mm});
            skPoint(sketch, "E38.4.26.0", {"position": v(-50.8, -93.13) * mm});
            skPoint(sketch, "E38.4.27.0", {"position": v(-50.8, -99.48) * mm});
            skPoint(sketch, "E38.4.28.0", {"position": v(-50.8, -105.83) * mm});
            skPoint(sketch, "E38.4.29.0", {"position": v(-50.8, -112.18) * mm});
            skPoint(sketch, "E38.4.30.0", {"position": v(-50.8, -118.53) * mm});
            skPoint(sketch, "E38.4.31.0", {"position": v(-50.8, -124.88) * mm});
            skPoint(sketch, "E38.4.32.0", {"position": v(-50.8, -131.23) * mm});
            skPoint(sketch, "E38.4.33.0", {"position": v(-50.8, -137.58) * mm});
            skPoint(sketch, "E38.4.34.0", {"position": v(-50.8, -143.93) * mm});
            skPoint(sketch, "E38.4.35.0", {"position": v(-50.8, -150.28) * mm});
            skPoint(sketch, "E38.4.36.0", {"position": v(-50.8, -156.63) * mm});
            skPoint(sketch, "E38.4.37.0", {"position": v(-50.8, -162.98) * mm});
            skPoint(sketch, "E38.4.38.0", {"position": v(-50.8, -169.33) * mm});
            skPoint(sketch, "E38.4.39.0", {"position": v(-50.8, -175.68) * mm});
            skPoint(sketch, "E38.4.40.0", {"position": v(-50.8, -182.03) * mm});
            skPoint(sketch, "E38.4.41.0", {"position": v(-50.8, -188.38) * mm});
            skPoint(sketch, "E38.4.42.0", {"position": v(-50.8, -194.73) * mm});
            skPoint(sketch, "E38.4.43.0", {"position": v(-50.8, -201.08) * mm});
            skPoint(sketch, "E38.4.44.0", {"position": v(-50.8, -207.43) * mm});
            skPoint(sketch, "E38.4.45.0", {"position": v(-50.8, -213.78) * mm});
            skPoint(sketch, "E38.4.46.0", {"position": v(-50.8, -220.13) * mm});
            skPoint(sketch, "E38.4.47.0", {"position": v(-50.8, -226.48) * mm});
            skPoint(sketch, "E38.4.48.0", {"position": v(-50.8, -232.83) * mm});
            skPoint(sketch, "E38.4.49.0", {"position": v(-50.8, -239.18) * mm});
            skPoint(sketch, "E38.4.50.0", {"position": v(-50.8, -245.53) * mm});
            skPoint(sketch, "E38.4.51.0", {"position": v(-50.8, -251.88) * mm});
            skPoint(sketch, "E38.4.52.0", {"position": v(-50.8, -258.23) * mm});
            skPoint(sketch, "E38.4.53.0", {"position": v(-50.8, -264.58) * mm});
            skPoint(sketch, "E38.4.54.0", {"position": v(-50.8, -270.93) * mm});
            skPoint(sketch, "E38.4.55.0", {"position": v(-50.8, -277.28) * mm});
            skPoint(sketch, "E38.4.56.0", {"position": v(-50.8, -283.63) * mm});
            skPoint(sketch, "E38.4.57.0", {"position": v(-50.8, -289.98) * mm});
            skPoint(sketch, "E38.4.58.0", {"position": v(-50.8, -296.33) * mm});
            skPoint(sketch, "E38.4.59.0", {"position": v(-50.8, -302.68) * mm});
            skPoint(sketch, "E38.4.60.0", {"position": v(-50.8, -309.03) * mm});
            skPoint(sketch, "E38.4.61.0", {"position": v(-50.8, -315.38) * mm});
            skPoint(sketch, "E38.4.62.0", {"position": v(-50.8, -321.73) * mm});
            skPoint(sketch, "E38.4.63.0", {"position": v(-50.8, -328.08) * mm});
            skPoint(sketch, "E38.4.64.0", {"position": v(-50.8, -334.43) * mm});
            skPoint(sketch, "E38.4.65.0", {"position": v(-50.8, -340.78) * mm});
            skPoint(sketch, "E38.4.66.0", {"position": v(-50.8, -347.13) * mm});
            skPoint(sketch, "E38.4.67.0", {"position": v(-50.8, -353.48) * mm});
            skPoint(sketch, "E38.4.68.0", {"position": v(-50.8, -359.83) * mm});
            skPoint(sketch, "E38.4.69.0", {"position": v(-50.8, -366.18) * mm});
            skPoint(sketch, "E38.4.70.0", {"position": v(-50.8, -372.53) * mm});
            skPoint(sketch, "E38.4.71.0", {"position": v(-50.8, -378.88) * mm});
            skPoint(sketch, "E38.4.72.0", {"position": v(-50.8, -385.23) * mm});
            skPoint(sketch, "E38.4.73.0", {"position": v(-50.8, -391.58) * mm});
            skPoint(sketch, "E38.4.74.0", {"position": v(-50.8, -397.93) * mm});
            skPoint(sketch, "E38.4.75.0", {"position": v(-50.8, -404.28) * mm});
            skPoint(sketch, "E38.4.76.0", {"position": v(-50.8, -410.63) * mm});
            skPoint(sketch, "E38.4.77.0", {"position": v(-50.8, -416.98) * mm});
            skPoint(sketch, "E38.4.78.0", {"position": v(-50.8, -423.33) * mm});
            skPoint(sketch, "E38.4.79.0", {"position": v(-50.8, -429.68) * mm});
            skPoint(sketch, "E38.4.80.0", {"position": v(-50.8, -436.03) * mm});
            skPoint(sketch, "E38.4.81.0", {"position": v(-50.8, -442.38) * mm});
            skPoint(sketch, "E38.4.82.0", {"position": v(-50.8, -448.73) * mm});
            skPoint(sketch, "E38.4.83.0", {"position": v(-50.8, -455.08) * mm});
            skPoint(sketch, "E38.4.84.0", {"position": v(-50.8, -461.43) * mm});
            skPoint(sketch, "E38.4.85.0", {"position": v(-50.8, -467.78) * mm});
            skPoint(sketch, "E38.4.86.0", {"position": v(-50.8, -474.13) * mm});
            skPoint(sketch, "E38.4.87.0", {"position": v(-50.8, -480.48) * mm});
            skPoint(sketch, "E38.4.88.0", {"position": v(-50.8, -486.83) * mm});
            skPoint(sketch, "E38.4.89.0", {"position": v(-50.8, -493.18) * mm});
            skPoint(sketch, "E38.4.90.0", {"position": v(-50.8, -499.53) * mm});
            skPoint(sketch, "E38.4.91.0", {"position": v(-50.8, -505.88) * mm});
            skPoint(sketch, "E38.4.92.0", {"position": v(-50.8, -512.23) * mm});
            skPoint(sketch, "E38.4.93.0", {"position": v(-50.8, -518.58) * mm});
            skPoint(sketch, "E38.4.94.0", {"position": v(-50.8, -524.93) * mm});
            skPoint(sketch, "E38.4.95.0", {"position": v(-50.8, -531.28) * mm});
            skPoint(sketch, "E38.4.96.0", {"position": v(-50.8, -537.63) * mm});
            skPoint(sketch, "E38.4.97.0", {"position": v(-50.8, -543.98) * mm});
            skPoint(sketch, "E38.4.98.0", {"position": v(-50.8, -550.33) * mm});
            skPoint(sketch, "E38.4.99.0", {"position": v(-50.8, -556.68) * mm});
            skPoint(sketch, "E38.5.1.0", {"position": v(-44.45, 65.62) * mm});
            skPoint(sketch, "E38.5.2.0", {"position": v(-44.45, 59.27) * mm});
            skPoint(sketch, "E38.5.3.0", {"position": v(-44.45, 52.92) * mm});
            skPoint(sketch, "E38.5.4.0", {"position": v(-44.45, 46.57) * mm});
            skPoint(sketch, "E38.5.5.0", {"position": v(-44.45, 40.22) * mm});
            skPoint(sketch, "E38.5.6.0", {"position": v(-44.45, 33.87) * mm});
            skPoint(sketch, "E38.5.7.0", {"position": v(-44.45, 27.52) * mm});
            skPoint(sketch, "E38.5.8.0", {"position": v(-44.45, 21.17) * mm});
            skPoint(sketch, "E38.5.9.0", {"position": v(-44.45, 14.82) * mm});
            skPoint(sketch, "E38.5.10.0", {"position": v(-44.45, 8.47) * mm});
            skPoint(sketch, "E38.5.11.0", {"position": v(-44.45, 2.12) * mm});
            skPoint(sketch, "E38.5.12.0", {"position": v(-44.45, -4.23) * mm});
            skPoint(sketch, "E38.5.13.0", {"position": v(-44.45, -10.58) * mm});
            skPoint(sketch, "E38.5.14.0", {"position": v(-44.45, -16.93) * mm});
            skPoint(sketch, "E38.5.15.0", {"position": v(-44.45, -23.28) * mm});
            skPoint(sketch, "E38.5.16.0", {"position": v(-44.45, -29.63) * mm});
            skPoint(sketch, "E38.5.17.0", {"position": v(-44.45, -35.98) * mm});
            skPoint(sketch, "E38.5.18.0", {"position": v(-44.45, -42.33) * mm});
            skPoint(sketch, "E38.5.19.0", {"position": v(-44.45, -48.68) * mm});
            skPoint(sketch, "E38.5.20.0", {"position": v(-44.45, -55.03) * mm});
            skPoint(sketch, "E38.5.21.0", {"position": v(-44.45, -61.38) * mm});
            skPoint(sketch, "E38.5.22.0", {"position": v(-44.45, -67.73) * mm});
            skPoint(sketch, "E38.5.23.0", {"position": v(-44.45, -74.08) * mm});
            skPoint(sketch, "E38.5.24.0", {"position": v(-44.45, -80.43) * mm});
            skPoint(sketch, "E38.5.25.0", {"position": v(-44.45, -86.78) * mm});
            skPoint(sketch, "E38.5.26.0", {"position": v(-44.45, -93.13) * mm});
            skPoint(sketch, "E38.5.27.0", {"position": v(-44.45, -99.48) * mm});
            skPoint(sketch, "E38.5.28.0", {"position": v(-44.45, -105.83) * mm});
            skPoint(sketch, "E38.5.29.0", {"position": v(-44.45, -112.18) * mm});
            skPoint(sketch, "E38.5.30.0", {"position": v(-44.45, -118.53) * mm});
            skPoint(sketch, "E38.5.31.0", {"position": v(-44.45, -124.88) * mm});
            skPoint(sketch, "E38.5.32.0", {"position": v(-44.45, -131.23) * mm});
            skPoint(sketch, "E38.5.33.0", {"position": v(-44.45, -137.58) * mm});
            skPoint(sketch, "E38.5.34.0", {"position": v(-44.45, -143.93) * mm});
            skPoint(sketch, "E38.5.35.0", {"position": v(-44.45, -150.28) * mm});
            skPoint(sketch, "E38.5.36.0", {"position": v(-44.45, -156.63) * mm});
            skPoint(sketch, "E38.5.37.0", {"position": v(-44.45, -162.98) * mm});
            skPoint(sketch, "E38.5.38.0", {"position": v(-44.45, -169.33) * mm});
            skPoint(sketch, "E38.5.39.0", {"position": v(-44.45, -175.68) * mm});
            skPoint(sketch, "E38.5.40.0", {"position": v(-44.45, -182.03) * mm});
            skPoint(sketch, "E38.5.41.0", {"position": v(-44.45, -188.38) * mm});
            skPoint(sketch, "E38.5.42.0", {"position": v(-44.45, -194.73) * mm});
            skPoint(sketch, "E38.5.43.0", {"position": v(-44.45, -201.08) * mm});
            skPoint(sketch, "E38.5.44.0", {"position": v(-44.45, -207.43) * mm});
            skPoint(sketch, "E38.5.45.0", {"position": v(-44.45, -213.78) * mm});
            skPoint(sketch, "E38.5.46.0", {"position": v(-44.45, -220.13) * mm});
            skPoint(sketch, "E38.5.47.0", {"position": v(-44.45, -226.48) * mm});
            skPoint(sketch, "E38.5.48.0", {"position": v(-44.45, -232.83) * mm});
            skPoint(sketch, "E38.5.49.0", {"position": v(-44.45, -239.18) * mm});
            skPoint(sketch, "E38.5.50.0", {"position": v(-44.45, -245.53) * mm});
            skPoint(sketch, "E38.5.51.0", {"position": v(-44.45, -251.88) * mm});
            skPoint(sketch, "E38.5.52.0", {"position": v(-44.45, -258.23) * mm});
            skPoint(sketch, "E38.5.53.0", {"position": v(-44.45, -264.58) * mm});
            skPoint(sketch, "E38.5.54.0", {"position": v(-44.45, -270.93) * mm});
            skPoint(sketch, "E38.5.55.0", {"position": v(-44.45, -277.28) * mm});
            skPoint(sketch, "E38.5.56.0", {"position": v(-44.45, -283.63) * mm});
            skPoint(sketch, "E38.5.57.0", {"position": v(-44.45, -289.98) * mm});
            skPoint(sketch, "E38.5.58.0", {"position": v(-44.45, -296.33) * mm});
            skPoint(sketch, "E38.5.59.0", {"position": v(-44.45, -302.68) * mm});
            skPoint(sketch, "E38.5.60.0", {"position": v(-44.45, -309.03) * mm});
            skPoint(sketch, "E38.5.61.0", {"position": v(-44.45, -315.38) * mm});
            skPoint(sketch, "E38.5.62.0", {"position": v(-44.45, -321.73) * mm});
            skPoint(sketch, "E38.5.63.0", {"position": v(-44.45, -328.08) * mm});
            skPoint(sketch, "E38.5.64.0", {"position": v(-44.45, -334.43) * mm});
            skPoint(sketch, "E38.5.65.0", {"position": v(-44.45, -340.78) * mm});
            skPoint(sketch, "E38.5.66.0", {"position": v(-44.45, -347.13) * mm});
            skPoint(sketch, "E38.5.67.0", {"position": v(-44.45, -353.48) * mm});
            skPoint(sketch, "E38.5.68.0", {"position": v(-44.45, -359.83) * mm});
            skPoint(sketch, "E38.5.69.0", {"position": v(-44.45, -366.18) * mm});
            skPoint(sketch, "E38.5.70.0", {"position": v(-44.45, -372.53) * mm});
            skPoint(sketch, "E38.5.71.0", {"position": v(-44.45, -378.88) * mm});
            skPoint(sketch, "E38.5.72.0", {"position": v(-44.45, -385.23) * mm});
            skPoint(sketch, "E38.5.73.0", {"position": v(-44.45, -391.58) * mm});
            skPoint(sketch, "E38.5.74.0", {"position": v(-44.45, -397.93) * mm});
            skPoint(sketch, "E38.5.75.0", {"position": v(-44.45, -404.28) * mm});
            skPoint(sketch, "E38.5.76.0", {"position": v(-44.45, -410.63) * mm});
            skPoint(sketch, "E38.5.77.0", {"position": v(-44.45, -416.98) * mm});
            skPoint(sketch, "E38.5.78.0", {"position": v(-44.45, -423.33) * mm});
            skPoint(sketch, "E38.5.79.0", {"position": v(-44.45, -429.68) * mm});
            skPoint(sketch, "E38.5.80.0", {"position": v(-44.45, -436.03) * mm});
            skPoint(sketch, "E38.5.81.0", {"position": v(-44.45, -442.38) * mm});
            skPoint(sketch, "E38.5.82.0", {"position": v(-44.45, -448.73) * mm});
            skPoint(sketch, "E38.5.83.0", {"position": v(-44.45, -455.08) * mm});
            skPoint(sketch, "E38.5.84.0", {"position": v(-44.45, -461.43) * mm});
            skPoint(sketch, "E38.5.85.0", {"position": v(-44.45, -467.78) * mm});
            skPoint(sketch, "E38.5.86.0", {"position": v(-44.45, -474.13) * mm});
            skPoint(sketch, "E38.5.87.0", {"position": v(-44.45, -480.48) * mm});
            skPoint(sketch, "E38.5.88.0", {"position": v(-44.45, -486.83) * mm});
            skPoint(sketch, "E38.5.89.0", {"position": v(-44.45, -493.18) * mm});
            skPoint(sketch, "E38.5.90.0", {"position": v(-44.45, -499.53) * mm});
            skPoint(sketch, "E38.5.91.0", {"position": v(-44.45, -505.88) * mm});
            skPoint(sketch, "E38.5.92.0", {"position": v(-44.45, -512.23) * mm});
            skPoint(sketch, "E38.5.93.0", {"position": v(-44.45, -518.58) * mm});
            skPoint(sketch, "E38.5.94.0", {"position": v(-44.45, -524.93) * mm});
            skPoint(sketch, "E38.5.95.0", {"position": v(-44.45, -531.28) * mm});
            skPoint(sketch, "E38.5.96.0", {"position": v(-44.45, -537.63) * mm});
            skPoint(sketch, "E38.5.97.0", {"position": v(-44.45, -543.98) * mm});
            skPoint(sketch, "E38.5.98.0", {"position": v(-44.45, -550.33) * mm});
            skPoint(sketch, "E38.5.99.0", {"position": v(-44.45, -556.68) * mm});
            skPoint(sketch, "E38.6.1.0", {"position": v(-38.1, 65.62) * mm});
            skPoint(sketch, "E38.6.2.0", {"position": v(-38.1, 59.27) * mm});
            skPoint(sketch, "E38.6.3.0", {"position": v(-38.1, 52.92) * mm});
            skPoint(sketch, "E38.6.4.0", {"position": v(-38.1, 46.57) * mm});
            skPoint(sketch, "E38.6.5.0", {"position": v(-38.1, 40.22) * mm});
            skPoint(sketch, "E38.6.6.0", {"position": v(-38.1, 33.87) * mm});
            skPoint(sketch, "E38.6.7.0", {"position": v(-38.1, 27.52) * mm});
            skPoint(sketch, "E38.6.8.0", {"position": v(-38.1, 21.17) * mm});
            skPoint(sketch, "E38.6.9.0", {"position": v(-38.1, 14.82) * mm});
            skPoint(sketch, "E38.6.10.0", {"position": v(-38.1, 8.47) * mm});
            skPoint(sketch, "E38.6.11.0", {"position": v(-38.1, 2.12) * mm});
            skPoint(sketch, "E38.6.12.0", {"position": v(-38.1, -4.23) * mm});
            skPoint(sketch, "E38.6.13.0", {"position": v(-38.1, -10.58) * mm});
            skPoint(sketch, "E38.6.14.0", {"position": v(-38.1, -16.93) * mm});
            skPoint(sketch, "E38.6.15.0", {"position": v(-38.1, -23.28) * mm});
            skPoint(sketch, "E38.6.16.0", {"position": v(-38.1, -29.63) * mm});
            skPoint(sketch, "E38.6.17.0", {"position": v(-38.1, -35.98) * mm});
            skPoint(sketch, "E38.6.18.0", {"position": v(-38.1, -42.33) * mm});
            skPoint(sketch, "E38.6.19.0", {"position": v(-38.1, -48.68) * mm});
            skPoint(sketch, "E38.6.20.0", {"position": v(-38.1, -55.03) * mm});
            skPoint(sketch, "E38.6.21.0", {"position": v(-38.1, -61.38) * mm});
            skPoint(sketch, "E38.6.22.0", {"position": v(-38.1, -67.73) * mm});
            skPoint(sketch, "E38.6.23.0", {"position": v(-38.1, -74.08) * mm});
            skPoint(sketch, "E38.6.24.0", {"position": v(-38.1, -80.43) * mm});
            skPoint(sketch, "E38.6.25.0", {"position": v(-38.1, -86.78) * mm});
            skPoint(sketch, "E38.6.26.0", {"position": v(-38.1, -93.13) * mm});
            skPoint(sketch, "E38.6.27.0", {"position": v(-38.1, -99.48) * mm});
            skPoint(sketch, "E38.6.28.0", {"position": v(-38.1, -105.83) * mm});
            skPoint(sketch, "E38.6.29.0", {"position": v(-38.1, -112.18) * mm});
            skPoint(sketch, "E38.6.30.0", {"position": v(-38.1, -118.53) * mm});
            skPoint(sketch, "E38.6.31.0", {"position": v(-38.1, -124.88) * mm});
            skPoint(sketch, "E38.6.32.0", {"position": v(-38.1, -131.23) * mm});
            skPoint(sketch, "E38.6.33.0", {"position": v(-38.1, -137.58) * mm});
            skPoint(sketch, "E38.6.34.0", {"position": v(-38.1, -143.93) * mm});
            skPoint(sketch, "E38.6.35.0", {"position": v(-38.1, -150.28) * mm});
            skPoint(sketch, "E38.6.36.0", {"position": v(-38.1, -156.63) * mm});
            skPoint(sketch, "E38.6.37.0", {"position": v(-38.1, -162.98) * mm});
            skPoint(sketch, "E38.6.38.0", {"position": v(-38.1, -169.33) * mm});
            skPoint(sketch, "E38.6.39.0", {"position": v(-38.1, -175.68) * mm});
            skPoint(sketch, "E38.6.40.0", {"position": v(-38.1, -182.03) * mm});
            skPoint(sketch, "E38.6.41.0", {"position": v(-38.1, -188.38) * mm});
            skPoint(sketch, "E38.6.42.0", {"position": v(-38.1, -194.73) * mm});
            skPoint(sketch, "E38.6.43.0", {"position": v(-38.1, -201.08) * mm});
            skPoint(sketch, "E38.6.44.0", {"position": v(-38.1, -207.43) * mm});
            skPoint(sketch, "E38.6.45.0", {"position": v(-38.1, -213.78) * mm});
            skPoint(sketch, "E38.6.46.0", {"position": v(-38.1, -220.13) * mm});
            skPoint(sketch, "E38.6.47.0", {"position": v(-38.1, -226.48) * mm});
            skPoint(sketch, "E38.6.48.0", {"position": v(-38.1, -232.83) * mm});
            skPoint(sketch, "E38.6.49.0", {"position": v(-38.1, -239.18) * mm});
            skPoint(sketch, "E38.6.50.0", {"position": v(-38.1, -245.53) * mm});
            skPoint(sketch, "E38.6.51.0", {"position": v(-38.1, -251.88) * mm});
            skPoint(sketch, "E38.6.52.0", {"position": v(-38.1, -258.23) * mm});
            skPoint(sketch, "E38.6.53.0", {"position": v(-38.1, -264.58) * mm});
            skPoint(sketch, "E38.6.54.0", {"position": v(-38.1, -270.93) * mm});
            skPoint(sketch, "E38.6.55.0", {"position": v(-38.1, -277.28) * mm});
            skPoint(sketch, "E38.6.56.0", {"position": v(-38.1, -283.63) * mm});
            skPoint(sketch, "E38.6.57.0", {"position": v(-38.1, -289.98) * mm});
            skPoint(sketch, "E38.6.58.0", {"position": v(-38.1, -296.33) * mm});
            skPoint(sketch, "E38.6.59.0", {"position": v(-38.1, -302.68) * mm});
            skPoint(sketch, "E38.6.60.0", {"position": v(-38.1, -309.03) * mm});
            skPoint(sketch, "E38.6.61.0", {"position": v(-38.1, -315.38) * mm});
            skPoint(sketch, "E38.6.62.0", {"position": v(-38.1, -321.73) * mm});
            skPoint(sketch, "E38.6.63.0", {"position": v(-38.1, -328.08) * mm});
            skPoint(sketch, "E38.6.64.0", {"position": v(-38.1, -334.43) * mm});
            skPoint(sketch, "E38.6.65.0", {"position": v(-38.1, -340.78) * mm});
            skPoint(sketch, "E38.6.66.0", {"position": v(-38.1, -347.13) * mm});
            skPoint(sketch, "E38.6.67.0", {"position": v(-38.1, -353.48) * mm});
            skPoint(sketch, "E38.6.68.0", {"position": v(-38.1, -359.83) * mm});
            skPoint(sketch, "E38.6.69.0", {"position": v(-38.1, -366.18) * mm});
            skPoint(sketch, "E38.6.70.0", {"position": v(-38.1, -372.53) * mm});
            skPoint(sketch, "E38.6.71.0", {"position": v(-38.1, -378.88) * mm});
            skPoint(sketch, "E38.6.72.0", {"position": v(-38.1, -385.23) * mm});
            skPoint(sketch, "E38.6.73.0", {"position": v(-38.1, -391.58) * mm});
            skPoint(sketch, "E38.6.74.0", {"position": v(-38.1, -397.93) * mm});
            skPoint(sketch, "E38.6.75.0", {"position": v(-38.1, -404.28) * mm});
            skPoint(sketch, "E38.6.76.0", {"position": v(-38.1, -410.63) * mm});
            skPoint(sketch, "E38.6.77.0", {"position": v(-38.1, -416.98) * mm});
            skPoint(sketch, "E38.6.78.0", {"position": v(-38.1, -423.33) * mm});
            skPoint(sketch, "E38.6.79.0", {"position": v(-38.1, -429.68) * mm});
            skPoint(sketch, "E38.6.80.0", {"position": v(-38.1, -436.03) * mm});
            skPoint(sketch, "E38.6.81.0", {"position": v(-38.1, -442.38) * mm});
            skPoint(sketch, "E38.6.82.0", {"position": v(-38.1, -448.73) * mm});
            skPoint(sketch, "E38.6.83.0", {"position": v(-38.1, -455.08) * mm});
            skPoint(sketch, "E38.6.84.0", {"position": v(-38.1, -461.43) * mm});
            skPoint(sketch, "E38.6.85.0", {"position": v(-38.1, -467.78) * mm});
            skPoint(sketch, "E38.6.86.0", {"position": v(-38.1, -474.13) * mm});
            skPoint(sketch, "E38.6.87.0", {"position": v(-38.1, -480.48) * mm});
            skPoint(sketch, "E38.6.88.0", {"position": v(-38.1, -486.83) * mm});
            skPoint(sketch, "E38.6.89.0", {"position": v(-38.1, -493.18) * mm});
            skPoint(sketch, "E38.6.90.0", {"position": v(-38.1, -499.53) * mm});
            skPoint(sketch, "E38.6.91.0", {"position": v(-38.1, -505.88) * mm});
            skPoint(sketch, "E38.6.92.0", {"position": v(-38.1, -512.23) * mm});
            skPoint(sketch, "E38.6.93.0", {"position": v(-38.1, -518.58) * mm});
            skPoint(sketch, "E38.6.94.0", {"position": v(-38.1, -524.93) * mm});
            skPoint(sketch, "E38.6.95.0", {"position": v(-38.1, -531.28) * mm});
            skPoint(sketch, "E38.6.96.0", {"position": v(-38.1, -537.63) * mm});
            skPoint(sketch, "E38.6.97.0", {"position": v(-38.1, -543.98) * mm});
            skPoint(sketch, "E38.6.98.0", {"position": v(-38.1, -550.33) * mm});
            skPoint(sketch, "E38.6.99.0", {"position": v(-38.1, -556.68) * mm});
            skPoint(sketch, "E38.7.1.0", {"position": v(-31.75, 65.62) * mm});
            skPoint(sketch, "E38.7.2.0", {"position": v(-31.75, 59.27) * mm});
            skPoint(sketch, "E38.7.3.0", {"position": v(-31.75, 52.92) * mm});
            skPoint(sketch, "E38.7.4.0", {"position": v(-31.75, 46.57) * mm});
            skPoint(sketch, "E38.7.5.0", {"position": v(-31.75, 40.22) * mm});
            skPoint(sketch, "E38.7.6.0", {"position": v(-31.75, 33.87) * mm});
            skPoint(sketch, "E38.7.7.0", {"position": v(-31.75, 27.52) * mm});
            skPoint(sketch, "E38.7.8.0", {"position": v(-31.75, 21.17) * mm});
            skPoint(sketch, "E38.7.9.0", {"position": v(-31.75, 14.82) * mm});
            skPoint(sketch, "E38.7.10.0", {"position": v(-31.75, 8.47) * mm});
            skPoint(sketch, "E38.7.11.0", {"position": v(-31.75, 2.12) * mm});
            skPoint(sketch, "E38.7.12.0", {"position": v(-31.75, -4.23) * mm});
            skPoint(sketch, "E38.7.13.0", {"position": v(-31.75, -10.58) * mm});
            skPoint(sketch, "E38.7.14.0", {"position": v(-31.75, -16.93) * mm});
            skPoint(sketch, "E38.7.15.0", {"position": v(-31.75, -23.28) * mm});
            skPoint(sketch, "E38.7.16.0", {"position": v(-31.75, -29.63) * mm});
            skPoint(sketch, "E38.7.17.0", {"position": v(-31.75, -35.98) * mm});
            skPoint(sketch, "E38.7.18.0", {"position": v(-31.75, -42.33) * mm});
            skPoint(sketch, "E38.7.19.0", {"position": v(-31.75, -48.68) * mm});
            skPoint(sketch, "E38.7.20.0", {"position": v(-31.75, -55.03) * mm});
            skPoint(sketch, "E38.7.21.0", {"position": v(-31.75, -61.38) * mm});
            skPoint(sketch, "E38.7.22.0", {"position": v(-31.75, -67.73) * mm});
            skPoint(sketch, "E38.7.23.0", {"position": v(-31.75, -74.08) * mm});
            skPoint(sketch, "E38.7.24.0", {"position": v(-31.75, -80.43) * mm});
            skPoint(sketch, "E38.7.25.0", {"position": v(-31.75, -86.78) * mm});
            skPoint(sketch, "E38.7.26.0", {"position": v(-31.75, -93.13) * mm});
            skPoint(sketch, "E38.7.27.0", {"position": v(-31.75, -99.48) * mm});
            skPoint(sketch, "E38.7.28.0", {"position": v(-31.75, -105.83) * mm});
            skPoint(sketch, "E38.7.29.0", {"position": v(-31.75, -112.18) * mm});
            skPoint(sketch, "E38.7.30.0", {"position": v(-31.75, -118.53) * mm});
            skPoint(sketch, "E38.7.31.0", {"position": v(-31.75, -124.88) * mm});
            skPoint(sketch, "E38.7.32.0", {"position": v(-31.75, -131.23) * mm});
            skPoint(sketch, "E38.7.33.0", {"position": v(-31.75, -137.58) * mm});
            skPoint(sketch, "E38.7.34.0", {"position": v(-31.75, -143.93) * mm});
            skPoint(sketch, "E38.7.35.0", {"position": v(-31.75, -150.28) * mm});
            skPoint(sketch, "E38.7.36.0", {"position": v(-31.75, -156.63) * mm});
            skPoint(sketch, "E38.7.37.0", {"position": v(-31.75, -162.98) * mm});
            skPoint(sketch, "E38.7.38.0", {"position": v(-31.75, -169.33) * mm});
            skPoint(sketch, "E38.7.39.0", {"position": v(-31.75, -175.68) * mm});
            skPoint(sketch, "E38.7.40.0", {"position": v(-31.75, -182.03) * mm});
            skPoint(sketch, "E38.7.41.0", {"position": v(-31.75, -188.38) * mm});
            skPoint(sketch, "E38.7.42.0", {"position": v(-31.75, -194.73) * mm});
            skPoint(sketch, "E38.7.43.0", {"position": v(-31.75, -201.08) * mm});
            skPoint(sketch, "E38.7.44.0", {"position": v(-31.75, -207.43) * mm});
            skPoint(sketch, "E38.7.45.0", {"position": v(-31.75, -213.78) * mm});
            skPoint(sketch, "E38.7.46.0", {"position": v(-31.75, -220.13) * mm});
            skPoint(sketch, "E38.7.47.0", {"position": v(-31.75, -226.48) * mm});
            skPoint(sketch, "E38.7.48.0", {"position": v(-31.75, -232.83) * mm});
            skPoint(sketch, "E38.7.49.0", {"position": v(-31.75, -239.18) * mm});
            skPoint(sketch, "E38.7.50.0", {"position": v(-31.75, -245.53) * mm});
            skPoint(sketch, "E38.7.51.0", {"position": v(-31.75, -251.88) * mm});
            skPoint(sketch, "E38.7.52.0", {"position": v(-31.75, -258.23) * mm});
            skPoint(sketch, "E38.7.53.0", {"position": v(-31.75, -264.58) * mm});
            skPoint(sketch, "E38.7.54.0", {"position": v(-31.75, -270.93) * mm});
            skPoint(sketch, "E38.7.55.0", {"position": v(-31.75, -277.28) * mm});
            skPoint(sketch, "E38.7.56.0", {"position": v(-31.75, -283.63) * mm});
            skPoint(sketch, "E38.7.57.0", {"position": v(-31.75, -289.98) * mm});
            skPoint(sketch, "E38.7.58.0", {"position": v(-31.75, -296.33) * mm});
            skPoint(sketch, "E38.7.59.0", {"position": v(-31.75, -302.68) * mm});
            skPoint(sketch, "E38.7.60.0", {"position": v(-31.75, -309.03) * mm});
            skPoint(sketch, "E38.7.61.0", {"position": v(-31.75, -315.38) * mm});
            skPoint(sketch, "E38.7.62.0", {"position": v(-31.75, -321.73) * mm});
            skPoint(sketch, "E38.7.63.0", {"position": v(-31.75, -328.08) * mm});
            skPoint(sketch, "E38.7.64.0", {"position": v(-31.75, -334.43) * mm});
            skPoint(sketch, "E38.7.65.0", {"position": v(-31.75, -340.78) * mm});
            skPoint(sketch, "E38.7.66.0", {"position": v(-31.75, -347.13) * mm});
            skPoint(sketch, "E38.7.67.0", {"position": v(-31.75, -353.48) * mm});
            skPoint(sketch, "E38.7.68.0", {"position": v(-31.75, -359.83) * mm});
            skPoint(sketch, "E38.7.69.0", {"position": v(-31.75, -366.18) * mm});
            skPoint(sketch, "E38.7.70.0", {"position": v(-31.75, -372.53) * mm});
            skPoint(sketch, "E38.7.71.0", {"position": v(-31.75, -378.88) * mm});
            skPoint(sketch, "E38.7.72.0", {"position": v(-31.75, -385.23) * mm});
            skPoint(sketch, "E38.7.73.0", {"position": v(-31.75, -391.58) * mm});
            skPoint(sketch, "E38.7.74.0", {"position": v(-31.75, -397.93) * mm});
            skPoint(sketch, "E38.7.75.0", {"position": v(-31.75, -404.28) * mm});
            skPoint(sketch, "E38.7.76.0", {"position": v(-31.75, -410.63) * mm});
            skPoint(sketch, "E38.7.77.0", {"position": v(-31.75, -416.98) * mm});
            skPoint(sketch, "E38.7.78.0", {"position": v(-31.75, -423.33) * mm});
            skPoint(sketch, "E38.7.79.0", {"position": v(-31.75, -429.68) * mm});
            skPoint(sketch, "E38.7.80.0", {"position": v(-31.75, -436.03) * mm});
            skPoint(sketch, "E38.7.81.0", {"position": v(-31.75, -442.38) * mm});
            skPoint(sketch, "E38.7.82.0", {"position": v(-31.75, -448.73) * mm});
            skPoint(sketch, "E38.7.83.0", {"position": v(-31.75, -455.08) * mm});
            skPoint(sketch, "E38.7.84.0", {"position": v(-31.75, -461.43) * mm});
            skPoint(sketch, "E38.7.85.0", {"position": v(-31.75, -467.78) * mm});
            skPoint(sketch, "E38.7.86.0", {"position": v(-31.75, -474.13) * mm});
            skPoint(sketch, "E38.7.87.0", {"position": v(-31.75, -480.48) * mm});
            skPoint(sketch, "E38.7.88.0", {"position": v(-31.75, -486.83) * mm});
            skPoint(sketch, "E38.7.89.0", {"position": v(-31.75, -493.18) * mm});
            skPoint(sketch, "E38.7.90.0", {"position": v(-31.75, -499.53) * mm});
            skPoint(sketch, "E38.7.91.0", {"position": v(-31.75, -505.88) * mm});
            skPoint(sketch, "E38.7.92.0", {"position": v(-31.75, -512.23) * mm});
            skPoint(sketch, "E38.7.93.0", {"position": v(-31.75, -518.58) * mm});
            skPoint(sketch, "E38.7.94.0", {"position": v(-31.75, -524.93) * mm});
            skPoint(sketch, "E38.7.95.0", {"position": v(-31.75, -531.28) * mm});
            skPoint(sketch, "E38.7.96.0", {"position": v(-31.75, -537.63) * mm});
            skPoint(sketch, "E38.7.97.0", {"position": v(-31.75, -543.98) * mm});
            skPoint(sketch, "E38.7.98.0", {"position": v(-31.75, -550.33) * mm});
            skPoint(sketch, "E38.7.99.0", {"position": v(-31.75, -556.68) * mm});
            skPoint(sketch, "E38.8.1.0", {"position": v(-25.4, 65.62) * mm});
            skPoint(sketch, "E38.8.2.0", {"position": v(-25.4, 59.27) * mm});
            skPoint(sketch, "E38.8.3.0", {"position": v(-25.4, 52.92) * mm});
            skPoint(sketch, "E38.8.4.0", {"position": v(-25.4, 46.57) * mm});
            skPoint(sketch, "E38.8.5.0", {"position": v(-25.4, 40.22) * mm});
            skPoint(sketch, "E38.8.6.0", {"position": v(-25.4, 33.87) * mm});
            skPoint(sketch, "E38.8.7.0", {"position": v(-25.4, 27.52) * mm});
            skPoint(sketch, "E38.8.8.0", {"position": v(-25.4, 21.17) * mm});
            skPoint(sketch, "E38.8.9.0", {"position": v(-25.4, 14.82) * mm});
            skPoint(sketch, "E38.8.10.0", {"position": v(-25.4, 8.47) * mm});
            skPoint(sketch, "E38.8.11.0", {"position": v(-25.4, 2.12) * mm});
            skPoint(sketch, "E38.8.12.0", {"position": v(-25.4, -4.23) * mm});
            skPoint(sketch, "E38.8.13.0", {"position": v(-25.4, -10.58) * mm});
            skPoint(sketch, "E38.8.14.0", {"position": v(-25.4, -16.93) * mm});
            skPoint(sketch, "E38.8.15.0", {"position": v(-25.4, -23.28) * mm});
            skPoint(sketch, "E38.8.16.0", {"position": v(-25.4, -29.63) * mm});
            skPoint(sketch, "E38.8.17.0", {"position": v(-25.4, -35.98) * mm});
            skPoint(sketch, "E38.8.18.0", {"position": v(-25.4, -42.33) * mm});
            skPoint(sketch, "E38.8.19.0", {"position": v(-25.4, -48.68) * mm});
            skPoint(sketch, "E38.8.20.0", {"position": v(-25.4, -55.03) * mm});
            skPoint(sketch, "E38.8.21.0", {"position": v(-25.4, -61.38) * mm});
            skPoint(sketch, "E38.8.22.0", {"position": v(-25.4, -67.73) * mm});
            skPoint(sketch, "E38.8.23.0", {"position": v(-25.4, -74.08) * mm});
            skPoint(sketch, "E38.8.24.0", {"position": v(-25.4, -80.43) * mm});
            skPoint(sketch, "E38.8.25.0", {"position": v(-25.4, -86.78) * mm});
            skPoint(sketch, "E38.8.26.0", {"position": v(-25.4, -93.13) * mm});
            skPoint(sketch, "E38.8.27.0", {"position": v(-25.4, -99.48) * mm});
            skPoint(sketch, "E38.8.28.0", {"position": v(-25.4, -105.83) * mm});
            skPoint(sketch, "E38.8.29.0", {"position": v(-25.4, -112.18) * mm});
            skPoint(sketch, "E38.8.30.0", {"position": v(-25.4, -118.53) * mm});
            skPoint(sketch, "E38.8.31.0", {"position": v(-25.4, -124.88) * mm});
            skPoint(sketch, "E38.8.32.0", {"position": v(-25.4, -131.23) * mm});
            skPoint(sketch, "E38.8.33.0", {"position": v(-25.4, -137.58) * mm});
            skPoint(sketch, "E38.8.34.0", {"position": v(-25.4, -143.93) * mm});
            skPoint(sketch, "E38.8.35.0", {"position": v(-25.4, -150.28) * mm});
            skPoint(sketch, "E38.8.36.0", {"position": v(-25.4, -156.63) * mm});
            skPoint(sketch, "E38.8.37.0", {"position": v(-25.4, -162.98) * mm});
            skPoint(sketch, "E38.8.38.0", {"position": v(-25.4, -169.33) * mm});
            skPoint(sketch, "E38.8.39.0", {"position": v(-25.4, -175.68) * mm});
            skPoint(sketch, "E38.8.40.0", {"position": v(-25.4, -182.03) * mm});
            skPoint(sketch, "E38.8.41.0", {"position": v(-25.4, -188.38) * mm});
            skPoint(sketch, "E38.8.42.0", {"position": v(-25.4, -194.73) * mm});
            skPoint(sketch, "E38.8.43.0", {"position": v(-25.4, -201.08) * mm});
            skPoint(sketch, "E38.8.44.0", {"position": v(-25.4, -207.43) * mm});
            skPoint(sketch, "E38.8.45.0", {"position": v(-25.4, -213.78) * mm});
            skPoint(sketch, "E38.8.46.0", {"position": v(-25.4, -220.13) * mm});
            skPoint(sketch, "E38.8.47.0", {"position": v(-25.4, -226.48) * mm});
            skPoint(sketch, "E38.8.48.0", {"position": v(-25.4, -232.83) * mm});
            skPoint(sketch, "E38.8.49.0", {"position": v(-25.4, -239.18) * mm});
            skPoint(sketch, "E38.8.50.0", {"position": v(-25.4, -245.53) * mm});
            skPoint(sketch, "E38.8.51.0", {"position": v(-25.4, -251.88) * mm});
            skPoint(sketch, "E38.8.52.0", {"position": v(-25.4, -258.23) * mm});
            skPoint(sketch, "E38.8.53.0", {"position": v(-25.4, -264.58) * mm});
            skPoint(sketch, "E38.8.54.0", {"position": v(-25.4, -270.93) * mm});
            skPoint(sketch, "E38.8.55.0", {"position": v(-25.4, -277.28) * mm});
            skPoint(sketch, "E38.8.56.0", {"position": v(-25.4, -283.63) * mm});
            skPoint(sketch, "E38.8.57.0", {"position": v(-25.4, -289.98) * mm});
            skPoint(sketch, "E38.8.58.0", {"position": v(-25.4, -296.33) * mm});
            skPoint(sketch, "E38.8.59.0", {"position": v(-25.4, -302.68) * mm});
            skPoint(sketch, "E38.8.60.0", {"position": v(-25.4, -309.03) * mm});
            skPoint(sketch, "E38.8.61.0", {"position": v(-25.4, -315.38) * mm});
            skPoint(sketch, "E38.8.62.0", {"position": v(-25.4, -321.73) * mm});
            skPoint(sketch, "E38.8.63.0", {"position": v(-25.4, -328.08) * mm});
            skPoint(sketch, "E38.8.64.0", {"position": v(-25.4, -334.43) * mm});
            skPoint(sketch, "E38.8.65.0", {"position": v(-25.4, -340.78) * mm});
            skPoint(sketch, "E38.8.66.0", {"position": v(-25.4, -347.13) * mm});
            skPoint(sketch, "E38.8.67.0", {"position": v(-25.4, -353.48) * mm});
            skPoint(sketch, "E38.8.68.0", {"position": v(-25.4, -359.83) * mm});
            skPoint(sketch, "E38.8.69.0", {"position": v(-25.4, -366.18) * mm});
            skPoint(sketch, "E38.8.70.0", {"position": v(-25.4, -372.53) * mm});
            skPoint(sketch, "E38.8.71.0", {"position": v(-25.4, -378.88) * mm});
            skPoint(sketch, "E38.8.72.0", {"position": v(-25.4, -385.23) * mm});
            skPoint(sketch, "E38.8.73.0", {"position": v(-25.4, -391.58) * mm});
            skPoint(sketch, "E38.8.74.0", {"position": v(-25.4, -397.93) * mm});
            skPoint(sketch, "E38.8.75.0", {"position": v(-25.4, -404.28) * mm});
            skPoint(sketch, "E38.8.76.0", {"position": v(-25.4, -410.63) * mm});
            skPoint(sketch, "E38.8.77.0", {"position": v(-25.4, -416.98) * mm});
            skPoint(sketch, "E38.8.78.0", {"position": v(-25.4, -423.33) * mm});
            skPoint(sketch, "E38.8.79.0", {"position": v(-25.4, -429.68) * mm});
            skPoint(sketch, "E38.8.80.0", {"position": v(-25.4, -436.03) * mm});
            skPoint(sketch, "E38.8.81.0", {"position": v(-25.4, -442.38) * mm});
            skPoint(sketch, "E38.8.82.0", {"position": v(-25.4, -448.73) * mm});
            skPoint(sketch, "E38.8.83.0", {"position": v(-25.4, -455.08) * mm});
            skPoint(sketch, "E38.8.84.0", {"position": v(-25.4, -461.43) * mm});
            skPoint(sketch, "E38.8.85.0", {"position": v(-25.4, -467.78) * mm});
            skPoint(sketch, "E38.8.86.0", {"position": v(-25.4, -474.13) * mm});
            skPoint(sketch, "E38.8.87.0", {"position": v(-25.4, -480.48) * mm});
            skPoint(sketch, "E38.8.88.0", {"position": v(-25.4, -486.83) * mm});
            skPoint(sketch, "E38.8.89.0", {"position": v(-25.4, -493.18) * mm});
            skPoint(sketch, "E38.8.90.0", {"position": v(-25.4, -499.53) * mm});
            skPoint(sketch, "E38.8.91.0", {"position": v(-25.4, -505.88) * mm});
            skPoint(sketch, "E38.8.92.0", {"position": v(-25.4, -512.23) * mm});
            skPoint(sketch, "E38.8.93.0", {"position": v(-25.4, -518.58) * mm});
            skPoint(sketch, "E38.8.94.0", {"position": v(-25.4, -524.93) * mm});
            skPoint(sketch, "E38.8.95.0", {"position": v(-25.4, -531.28) * mm});
            skPoint(sketch, "E38.8.96.0", {"position": v(-25.4, -537.63) * mm});
            skPoint(sketch, "E38.8.97.0", {"position": v(-25.4, -543.98) * mm});
            skPoint(sketch, "E38.8.98.0", {"position": v(-25.4, -550.33) * mm});
            skPoint(sketch, "E38.8.99.0", {"position": v(-25.4, -556.68) * mm});
            skPoint(sketch, "E38.9.1.0", {"position": v(-19.05, 65.62) * mm});
            skPoint(sketch, "E38.9.2.0", {"position": v(-19.05, 59.27) * mm});
            skPoint(sketch, "E38.9.3.0", {"position": v(-19.05, 52.92) * mm});
            skPoint(sketch, "E38.9.4.0", {"position": v(-19.05, 46.57) * mm});
            skPoint(sketch, "E38.9.5.0", {"position": v(-19.05, 40.22) * mm});
            skPoint(sketch, "E38.9.6.0", {"position": v(-19.05, 33.87) * mm});
            skPoint(sketch, "E38.9.7.0", {"position": v(-19.05, 27.52) * mm});
            skPoint(sketch, "E38.9.8.0", {"position": v(-19.05, 21.17) * mm});
            skPoint(sketch, "E38.9.9.0", {"position": v(-19.05, 14.82) * mm});
            skPoint(sketch, "E38.9.10.0", {"position": v(-19.05, 8.47) * mm});
            skPoint(sketch, "E38.9.11.0", {"position": v(-19.05, 2.12) * mm});
            skPoint(sketch, "E38.9.12.0", {"position": v(-19.05, -4.23) * mm});
            skPoint(sketch, "E38.9.13.0", {"position": v(-19.05, -10.58) * mm});
            skPoint(sketch, "E38.9.14.0", {"position": v(-19.05, -16.93) * mm});
            skPoint(sketch, "E38.9.15.0", {"position": v(-19.05, -23.28) * mm});
            skPoint(sketch, "E38.9.16.0", {"position": v(-19.05, -29.63) * mm});
            skPoint(sketch, "E38.9.17.0", {"position": v(-19.05, -35.98) * mm});
            skPoint(sketch, "E38.9.18.0", {"position": v(-19.05, -42.33) * mm});
            skPoint(sketch, "E38.9.19.0", {"position": v(-19.05, -48.68) * mm});
            skPoint(sketch, "E38.9.20.0", {"position": v(-19.05, -55.03) * mm});
            skPoint(sketch, "E38.9.21.0", {"position": v(-19.05, -61.38) * mm});
            skPoint(sketch, "E38.9.22.0", {"position": v(-19.05, -67.73) * mm});
            skPoint(sketch, "E38.9.23.0", {"position": v(-19.05, -74.08) * mm});
            skPoint(sketch, "E38.9.24.0", {"position": v(-19.05, -80.43) * mm});
            skPoint(sketch, "E38.9.25.0", {"position": v(-19.05, -86.78) * mm});
            skPoint(sketch, "E38.9.26.0", {"position": v(-19.05, -93.13) * mm});
            skPoint(sketch, "E38.9.27.0", {"position": v(-19.05, -99.48) * mm});
            skPoint(sketch, "E38.9.28.0", {"position": v(-19.05, -105.83) * mm});
            skPoint(sketch, "E38.9.29.0", {"position": v(-19.05, -112.18) * mm});
            skPoint(sketch, "E38.9.30.0", {"position": v(-19.05, -118.53) * mm});
            skPoint(sketch, "E38.9.31.0", {"position": v(-19.05, -124.88) * mm});
            skPoint(sketch, "E38.9.32.0", {"position": v(-19.05, -131.23) * mm});
            skPoint(sketch, "E38.9.33.0", {"position": v(-19.05, -137.58) * mm});
            skPoint(sketch, "E38.9.34.0", {"position": v(-19.05, -143.93) * mm});
            skPoint(sketch, "E38.9.35.0", {"position": v(-19.05, -150.28) * mm});
            skPoint(sketch, "E38.9.36.0", {"position": v(-19.05, -156.63) * mm});
            skPoint(sketch, "E38.9.37.0", {"position": v(-19.05, -162.98) * mm});
            skPoint(sketch, "E38.9.38.0", {"position": v(-19.05, -169.33) * mm});
            skPoint(sketch, "E38.9.39.0", {"position": v(-19.05, -175.68) * mm});
            skPoint(sketch, "E38.9.40.0", {"position": v(-19.05, -182.03) * mm});
            skPoint(sketch, "E38.9.41.0", {"position": v(-19.05, -188.38) * mm});
            skPoint(sketch, "E38.9.42.0", {"position": v(-19.05, -194.73) * mm});
            skPoint(sketch, "E38.9.43.0", {"position": v(-19.05, -201.08) * mm});
            skPoint(sketch, "E38.9.44.0", {"position": v(-19.05, -207.43) * mm});
            skPoint(sketch, "E38.9.45.0", {"position": v(-19.05, -213.78) * mm});
            skPoint(sketch, "E38.9.46.0", {"position": v(-19.05, -220.13) * mm});
            skPoint(sketch, "E38.9.47.0", {"position": v(-19.05, -226.48) * mm});
            skPoint(sketch, "E38.9.48.0", {"position": v(-19.05, -232.83) * mm});
            skPoint(sketch, "E38.9.49.0", {"position": v(-19.05, -239.18) * mm});
            skPoint(sketch, "E38.9.50.0", {"position": v(-19.05, -245.53) * mm});
            skPoint(sketch, "E38.9.51.0", {"position": v(-19.05, -251.88) * mm});
            skPoint(sketch, "E38.9.52.0", {"position": v(-19.05, -258.23) * mm});
            skPoint(sketch, "E38.9.53.0", {"position": v(-19.05, -264.58) * mm});
            skPoint(sketch, "E38.9.54.0", {"position": v(-19.05, -270.93) * mm});
            skPoint(sketch, "E38.9.55.0", {"position": v(-19.05, -277.28) * mm});
            skPoint(sketch, "E38.9.56.0", {"position": v(-19.05, -283.63) * mm});
            skPoint(sketch, "E38.9.57.0", {"position": v(-19.05, -289.98) * mm});
            skPoint(sketch, "E38.9.58.0", {"position": v(-19.05, -296.33) * mm});
            skPoint(sketch, "E38.9.59.0", {"position": v(-19.05, -302.68) * mm});
            skPoint(sketch, "E38.9.60.0", {"position": v(-19.05, -309.03) * mm});
            skPoint(sketch, "E38.9.61.0", {"position": v(-19.05, -315.38) * mm});
            skPoint(sketch, "E38.9.62.0", {"position": v(-19.05, -321.73) * mm});
            skPoint(sketch, "E38.9.63.0", {"position": v(-19.05, -328.08) * mm});
            skPoint(sketch, "E38.9.64.0", {"position": v(-19.05, -334.43) * mm});
            skPoint(sketch, "E38.9.65.0", {"position": v(-19.05, -340.78) * mm});
            skPoint(sketch, "E38.9.66.0", {"position": v(-19.05, -347.13) * mm});
            skPoint(sketch, "E38.9.67.0", {"position": v(-19.05, -353.48) * mm});
            skPoint(sketch, "E38.9.68.0", {"position": v(-19.05, -359.83) * mm});
            skPoint(sketch, "E38.9.69.0", {"position": v(-19.05, -366.18) * mm});
            skPoint(sketch, "E38.9.70.0", {"position": v(-19.05, -372.53) * mm});
            skPoint(sketch, "E38.9.71.0", {"position": v(-19.05, -378.88) * mm});
            skPoint(sketch, "E38.9.72.0", {"position": v(-19.05, -385.23) * mm});
            skPoint(sketch, "E38.9.73.0", {"position": v(-19.05, -391.58) * mm});
            skPoint(sketch, "E38.9.74.0", {"position": v(-19.05, -397.93) * mm});
            skPoint(sketch, "E38.9.75.0", {"position": v(-19.05, -404.28) * mm});
            skPoint(sketch, "E38.9.76.0", {"position": v(-19.05, -410.63) * mm});
            skPoint(sketch, "E38.9.77.0", {"position": v(-19.05, -416.98) * mm});
            skPoint(sketch, "E38.9.78.0", {"position": v(-19.05, -423.33) * mm});
            skPoint(sketch, "E38.9.79.0", {"position": v(-19.05, -429.68) * mm});
            skPoint(sketch, "E38.9.80.0", {"position": v(-19.05, -436.03) * mm});
            skPoint(sketch, "E38.9.81.0", {"position": v(-19.05, -442.38) * mm});
            skPoint(sketch, "E38.9.82.0", {"position": v(-19.05, -448.73) * mm});
            skPoint(sketch, "E38.9.83.0", {"position": v(-19.05, -455.08) * mm});
            skPoint(sketch, "E38.9.84.0", {"position": v(-19.05, -461.43) * mm});
            skPoint(sketch, "E38.9.85.0", {"position": v(-19.05, -467.78) * mm});
            skPoint(sketch, "E38.9.86.0", {"position": v(-19.05, -474.13) * mm});
            skPoint(sketch, "E38.9.87.0", {"position": v(-19.05, -480.48) * mm});
            skPoint(sketch, "E38.9.88.0", {"position": v(-19.05, -486.83) * mm});
            skPoint(sketch, "E38.9.89.0", {"position": v(-19.05, -493.18) * mm});
            skPoint(sketch, "E38.9.90.0", {"position": v(-19.05, -499.53) * mm});
            skPoint(sketch, "E38.9.91.0", {"position": v(-19.05, -505.88) * mm});
            skPoint(sketch, "E38.9.92.0", {"position": v(-19.05, -512.23) * mm});
            skPoint(sketch, "E38.9.93.0", {"position": v(-19.05, -518.58) * mm});
            skPoint(sketch, "E38.9.94.0", {"position": v(-19.05, -524.93) * mm});
            skPoint(sketch, "E38.9.95.0", {"position": v(-19.05, -531.28) * mm});
            skPoint(sketch, "E38.9.96.0", {"position": v(-19.05, -537.63) * mm});
            skPoint(sketch, "E38.9.97.0", {"position": v(-19.05, -543.98) * mm});
            skPoint(sketch, "E38.9.98.0", {"position": v(-19.05, -550.33) * mm});
            skPoint(sketch, "E38.9.99.0", {"position": v(-19.05, -556.68) * mm});
            skPoint(sketch, "E38.10.1.0", {"position": v(-12.7, 65.62) * mm});
            skPoint(sketch, "E38.10.2.0", {"position": v(-12.7, 59.27) * mm});
            skPoint(sketch, "E38.10.3.0", {"position": v(-12.7, 52.92) * mm});
            skPoint(sketch, "E38.10.4.0", {"position": v(-12.7, 46.57) * mm});
            skPoint(sketch, "E38.10.5.0", {"position": v(-12.7, 40.22) * mm});
            skPoint(sketch, "E38.10.6.0", {"position": v(-12.7, 33.87) * mm});
            skPoint(sketch, "E38.10.7.0", {"position": v(-12.7, 27.52) * mm});
            skPoint(sketch, "E38.10.8.0", {"position": v(-12.7, 21.17) * mm});
            skPoint(sketch, "E38.10.9.0", {"position": v(-12.7, 14.82) * mm});
            skPoint(sketch, "E38.10.10.0", {"position": v(-12.7, 8.47) * mm});
            skPoint(sketch, "E38.10.11.0", {"position": v(-12.7, 2.12) * mm});
            skPoint(sketch, "E38.10.12.0", {"position": v(-12.7, -4.23) * mm});
            skPoint(sketch, "E38.10.13.0", {"position": v(-12.7, -10.58) * mm});
            skPoint(sketch, "E38.10.14.0", {"position": v(-12.7, -16.93) * mm});
            skPoint(sketch, "E38.10.15.0", {"position": v(-12.7, -23.28) * mm});
            skPoint(sketch, "E38.10.16.0", {"position": v(-12.7, -29.63) * mm});
            skPoint(sketch, "E38.10.17.0", {"position": v(-12.7, -35.98) * mm});
            skPoint(sketch, "E38.10.18.0", {"position": v(-12.7, -42.33) * mm});
            skPoint(sketch, "E38.10.19.0", {"position": v(-12.7, -48.68) * mm});
            skPoint(sketch, "E38.10.20.0", {"position": v(-12.7, -55.03) * mm});
            skPoint(sketch, "E38.10.21.0", {"position": v(-12.7, -61.38) * mm});
            skPoint(sketch, "E38.10.22.0", {"position": v(-12.7, -67.73) * mm});
            skPoint(sketch, "E38.10.23.0", {"position": v(-12.7, -74.08) * mm});
            skPoint(sketch, "E38.10.24.0", {"position": v(-12.7, -80.43) * mm});
            skPoint(sketch, "E38.10.25.0", {"position": v(-12.7, -86.78) * mm});
            skPoint(sketch, "E38.10.26.0", {"position": v(-12.7, -93.13) * mm});
            skPoint(sketch, "E38.10.27.0", {"position": v(-12.7, -99.48) * mm});
            skPoint(sketch, "E38.10.28.0", {"position": v(-12.7, -105.83) * mm});
            skPoint(sketch, "E38.10.29.0", {"position": v(-12.7, -112.18) * mm});
            skPoint(sketch, "E38.10.30.0", {"position": v(-12.7, -118.53) * mm});
            skPoint(sketch, "E38.10.31.0", {"position": v(-12.7, -124.88) * mm});
            skPoint(sketch, "E38.10.32.0", {"position": v(-12.7, -131.23) * mm});
            skPoint(sketch, "E38.10.33.0", {"position": v(-12.7, -137.58) * mm});
            skPoint(sketch, "E38.10.34.0", {"position": v(-12.7, -143.93) * mm});
            skPoint(sketch, "E38.10.35.0", {"position": v(-12.7, -150.28) * mm});
            skPoint(sketch, "E38.10.36.0", {"position": v(-12.7, -156.63) * mm});
            skPoint(sketch, "E38.10.37.0", {"position": v(-12.7, -162.98) * mm});
            skPoint(sketch, "E38.10.38.0", {"position": v(-12.7, -169.33) * mm});
            skPoint(sketch, "E38.10.39.0", {"position": v(-12.7, -175.68) * mm});
            skPoint(sketch, "E38.10.40.0", {"position": v(-12.7, -182.03) * mm});
            skPoint(sketch, "E38.10.41.0", {"position": v(-12.7, -188.38) * mm});
            skPoint(sketch, "E38.10.42.0", {"position": v(-12.7, -194.73) * mm});
            skPoint(sketch, "E38.10.43.0", {"position": v(-12.7, -201.08) * mm});
            skPoint(sketch, "E38.10.44.0", {"position": v(-12.7, -207.43) * mm});
            skPoint(sketch, "E38.10.45.0", {"position": v(-12.7, -213.78) * mm});
            skPoint(sketch, "E38.10.46.0", {"position": v(-12.7, -220.13) * mm});
            skPoint(sketch, "E38.10.47.0", {"position": v(-12.7, -226.48) * mm});
            skPoint(sketch, "E38.10.48.0", {"position": v(-12.7, -232.83) * mm});
            skPoint(sketch, "E38.10.49.0", {"position": v(-12.7, -239.18) * mm});
            skPoint(sketch, "E38.10.50.0", {"position": v(-12.7, -245.53) * mm});
            skPoint(sketch, "E38.10.51.0", {"position": v(-12.7, -251.88) * mm});
            skPoint(sketch, "E38.10.52.0", {"position": v(-12.7, -258.23) * mm});
            skPoint(sketch, "E38.10.53.0", {"position": v(-12.7, -264.58) * mm});
            skPoint(sketch, "E38.10.54.0", {"position": v(-12.7, -270.93) * mm});
            skPoint(sketch, "E38.10.55.0", {"position": v(-12.7, -277.28) * mm});
            skPoint(sketch, "E38.10.56.0", {"position": v(-12.7, -283.63) * mm});
            skPoint(sketch, "E38.10.57.0", {"position": v(-12.7, -289.98) * mm});
            skPoint(sketch, "E38.10.58.0", {"position": v(-12.7, -296.33) * mm});
            skPoint(sketch, "E38.10.59.0", {"position": v(-12.7, -302.68) * mm});
            skPoint(sketch, "E38.10.60.0", {"position": v(-12.7, -309.03) * mm});
            skPoint(sketch, "E38.10.61.0", {"position": v(-12.7, -315.38) * mm});
            skPoint(sketch, "E38.10.62.0", {"position": v(-12.7, -321.73) * mm});
            skPoint(sketch, "E38.10.63.0", {"position": v(-12.7, -328.08) * mm});
            skPoint(sketch, "E38.10.64.0", {"position": v(-12.7, -334.43) * mm});
            skPoint(sketch, "E38.10.65.0", {"position": v(-12.7, -340.78) * mm});
            skPoint(sketch, "E38.10.66.0", {"position": v(-12.7, -347.13) * mm});
            skPoint(sketch, "E38.10.67.0", {"position": v(-12.7, -353.48) * mm});
            skPoint(sketch, "E38.10.68.0", {"position": v(-12.7, -359.83) * mm});
            skPoint(sketch, "E38.10.69.0", {"position": v(-12.7, -366.18) * mm});
            skPoint(sketch, "E38.10.70.0", {"position": v(-12.7, -372.53) * mm});
            skPoint(sketch, "E38.10.71.0", {"position": v(-12.7, -378.88) * mm});
            skPoint(sketch, "E38.10.72.0", {"position": v(-12.7, -385.23) * mm});
            skPoint(sketch, "E38.10.73.0", {"position": v(-12.7, -391.58) * mm});
            skPoint(sketch, "E38.10.74.0", {"position": v(-12.7, -397.93) * mm});
            skPoint(sketch, "E38.10.75.0", {"position": v(-12.7, -404.28) * mm});
            skPoint(sketch, "E38.10.76.0", {"position": v(-12.7, -410.63) * mm});
            skPoint(sketch, "E38.10.77.0", {"position": v(-12.7, -416.98) * mm});
            skPoint(sketch, "E38.10.78.0", {"position": v(-12.7, -423.33) * mm});
            skPoint(sketch, "E38.10.79.0", {"position": v(-12.7, -429.68) * mm});
            skPoint(sketch, "E38.10.80.0", {"position": v(-12.7, -436.03) * mm});
            skPoint(sketch, "E38.10.81.0", {"position": v(-12.7, -442.38) * mm});
            skPoint(sketch, "E38.10.82.0", {"position": v(-12.7, -448.73) * mm});
            skPoint(sketch, "E38.10.83.0", {"position": v(-12.7, -455.08) * mm});
            skPoint(sketch, "E38.10.84.0", {"position": v(-12.7, -461.43) * mm});
            skPoint(sketch, "E38.10.85.0", {"position": v(-12.7, -467.78) * mm});
            skPoint(sketch, "E38.10.86.0", {"position": v(-12.7, -474.13) * mm});
            skPoint(sketch, "E38.10.87.0", {"position": v(-12.7, -480.48) * mm});
            skPoint(sketch, "E38.10.88.0", {"position": v(-12.7, -486.83) * mm});
            skPoint(sketch, "E38.10.89.0", {"position": v(-12.7, -493.18) * mm});
            skPoint(sketch, "E38.10.90.0", {"position": v(-12.7, -499.53) * mm});
            skPoint(sketch, "E38.10.91.0", {"position": v(-12.7, -505.88) * mm});
            skPoint(sketch, "E38.10.92.0", {"position": v(-12.7, -512.23) * mm});
            skPoint(sketch, "E38.10.93.0", {"position": v(-12.7, -518.58) * mm});
            skPoint(sketch, "E38.10.94.0", {"position": v(-12.7, -524.93) * mm});
            skPoint(sketch, "E38.10.95.0", {"position": v(-12.7, -531.28) * mm});
            skPoint(sketch, "E38.10.96.0", {"position": v(-12.7, -537.63) * mm});
            skPoint(sketch, "E38.10.97.0", {"position": v(-12.7, -543.98) * mm});
            skPoint(sketch, "E38.10.98.0", {"position": v(-12.7, -550.33) * mm});
            skPoint(sketch, "E38.10.99.0", {"position": v(-12.7, -556.68) * mm});
            skPoint(sketch, "E38.11.1.0", {"position": v(-6.35, 65.62) * mm});
            skPoint(sketch, "E38.11.2.0", {"position": v(-6.35, 59.27) * mm});
            skPoint(sketch, "E38.11.3.0", {"position": v(-6.35, 52.92) * mm});
            skPoint(sketch, "E38.11.4.0", {"position": v(-6.35, 46.57) * mm});
            skPoint(sketch, "E38.11.5.0", {"position": v(-6.35, 40.22) * mm});
            skPoint(sketch, "E38.11.6.0", {"position": v(-6.35, 33.87) * mm});
            skPoint(sketch, "E38.11.7.0", {"position": v(-6.35, 27.52) * mm});
            skPoint(sketch, "E38.11.8.0", {"position": v(-6.35, 21.17) * mm});
            skPoint(sketch, "E38.11.9.0", {"position": v(-6.35, 14.82) * mm});
            skPoint(sketch, "E38.11.10.0", {"position": v(-6.35, 8.47) * mm});
            skPoint(sketch, "E38.11.11.0", {"position": v(-6.35, 2.12) * mm});
            skPoint(sketch, "E38.11.12.0", {"position": v(-6.35, -4.23) * mm});
            skPoint(sketch, "E38.11.13.0", {"position": v(-6.35, -10.58) * mm});
            skPoint(sketch, "E38.11.14.0", {"position": v(-6.35, -16.93) * mm});
            skPoint(sketch, "E38.11.15.0", {"position": v(-6.35, -23.28) * mm});
            skPoint(sketch, "E38.11.16.0", {"position": v(-6.35, -29.63) * mm});
            skPoint(sketch, "E38.11.17.0", {"position": v(-6.35, -35.98) * mm});
            skPoint(sketch, "E38.11.18.0", {"position": v(-6.35, -42.33) * mm});
            skPoint(sketch, "E38.11.19.0", {"position": v(-6.35, -48.68) * mm});
            skPoint(sketch, "E38.11.20.0", {"position": v(-6.35, -55.03) * mm});
            skPoint(sketch, "E38.11.21.0", {"position": v(-6.35, -61.38) * mm});
            skPoint(sketch, "E38.11.22.0", {"position": v(-6.35, -67.73) * mm});
            skPoint(sketch, "E38.11.23.0", {"position": v(-6.35, -74.08) * mm});
            skPoint(sketch, "E38.11.24.0", {"position": v(-6.35, -80.43) * mm});
            skPoint(sketch, "E38.11.25.0", {"position": v(-6.35, -86.78) * mm});
            skPoint(sketch, "E38.11.26.0", {"position": v(-6.35, -93.13) * mm});
            skPoint(sketch, "E38.11.27.0", {"position": v(-6.35, -99.48) * mm});
            skPoint(sketch, "E38.11.28.0", {"position": v(-6.35, -105.83) * mm});
            skPoint(sketch, "E38.11.29.0", {"position": v(-6.35, -112.18) * mm});
            skPoint(sketch, "E38.11.30.0", {"position": v(-6.35, -118.53) * mm});
            skPoint(sketch, "E38.11.31.0", {"position": v(-6.35, -124.88) * mm});
            skPoint(sketch, "E38.11.32.0", {"position": v(-6.35, -131.23) * mm});
            skPoint(sketch, "E38.11.33.0", {"position": v(-6.35, -137.58) * mm});
            skPoint(sketch, "E38.11.34.0", {"position": v(-6.35, -143.93) * mm});
            skPoint(sketch, "E38.11.35.0", {"position": v(-6.35, -150.28) * mm});
            skPoint(sketch, "E38.11.36.0", {"position": v(-6.35, -156.63) * mm});
            skPoint(sketch, "E38.11.37.0", {"position": v(-6.35, -162.98) * mm});
            skPoint(sketch, "E38.11.38.0", {"position": v(-6.35, -169.33) * mm});
            skPoint(sketch, "E38.11.39.0", {"position": v(-6.35, -175.68) * mm});
            skPoint(sketch, "E38.11.40.0", {"position": v(-6.35, -182.03) * mm});
            skPoint(sketch, "E38.11.41.0", {"position": v(-6.35, -188.38) * mm});
            skPoint(sketch, "E38.11.42.0", {"position": v(-6.35, -194.73) * mm});
            skPoint(sketch, "E38.11.43.0", {"position": v(-6.35, -201.08) * mm});
            skPoint(sketch, "E38.11.44.0", {"position": v(-6.35, -207.43) * mm});
            skPoint(sketch, "E38.11.45.0", {"position": v(-6.35, -213.78) * mm});
            skPoint(sketch, "E38.11.46.0", {"position": v(-6.35, -220.13) * mm});
            skPoint(sketch, "E38.11.47.0", {"position": v(-6.35, -226.48) * mm});
            skPoint(sketch, "E38.11.48.0", {"position": v(-6.35, -232.83) * mm});
            skPoint(sketch, "E38.11.49.0", {"position": v(-6.35, -239.18) * mm});
            skPoint(sketch, "E38.11.50.0", {"position": v(-6.35, -245.53) * mm});
            skPoint(sketch, "E38.11.51.0", {"position": v(-6.35, -251.88) * mm});
            skPoint(sketch, "E38.11.52.0", {"position": v(-6.35, -258.23) * mm});
            skPoint(sketch, "E38.11.53.0", {"position": v(-6.35, -264.58) * mm});
            skPoint(sketch, "E38.11.54.0", {"position": v(-6.35, -270.93) * mm});
            skPoint(sketch, "E38.11.55.0", {"position": v(-6.35, -277.28) * mm});
            skPoint(sketch, "E38.11.56.0", {"position": v(-6.35, -283.63) * mm});
            skPoint(sketch, "E38.11.57.0", {"position": v(-6.35, -289.98) * mm});
            skPoint(sketch, "E38.11.58.0", {"position": v(-6.35, -296.33) * mm});
            skPoint(sketch, "E38.11.59.0", {"position": v(-6.35, -302.68) * mm});
            skPoint(sketch, "E38.11.60.0", {"position": v(-6.35, -309.03) * mm});
            skPoint(sketch, "E38.11.61.0", {"position": v(-6.35, -315.38) * mm});
            skPoint(sketch, "E38.11.62.0", {"position": v(-6.35, -321.73) * mm});
            skPoint(sketch, "E38.11.63.0", {"position": v(-6.35, -328.08) * mm});
            skPoint(sketch, "E38.11.64.0", {"position": v(-6.35, -334.43) * mm});
            skPoint(sketch, "E38.11.65.0", {"position": v(-6.35, -340.78) * mm});
            skPoint(sketch, "E38.11.66.0", {"position": v(-6.35, -347.13) * mm});
            skPoint(sketch, "E38.11.67.0", {"position": v(-6.35, -353.48) * mm});
            skPoint(sketch, "E38.11.68.0", {"position": v(-6.35, -359.83) * mm});
            skPoint(sketch, "E38.11.69.0", {"position": v(-6.35, -366.18) * mm});
            skPoint(sketch, "E38.11.70.0", {"position": v(-6.35, -372.53) * mm});
            skPoint(sketch, "E38.11.71.0", {"position": v(-6.35, -378.88) * mm});
            skPoint(sketch, "E38.11.72.0", {"position": v(-6.35, -385.23) * mm});
            skPoint(sketch, "E38.11.73.0", {"position": v(-6.35, -391.58) * mm});
            skPoint(sketch, "E38.11.74.0", {"position": v(-6.35, -397.93) * mm});
            skPoint(sketch, "E38.11.75.0", {"position": v(-6.35, -404.28) * mm});
            skPoint(sketch, "E38.11.76.0", {"position": v(-6.35, -410.63) * mm});
            skPoint(sketch, "E38.11.77.0", {"position": v(-6.35, -416.98) * mm});
            skPoint(sketch, "E38.11.78.0", {"position": v(-6.35, -423.33) * mm});
            skPoint(sketch, "E38.11.79.0", {"position": v(-6.35, -429.68) * mm});
            skPoint(sketch, "E38.11.80.0", {"position": v(-6.35, -436.03) * mm});
            skPoint(sketch, "E38.11.81.0", {"position": v(-6.35, -442.38) * mm});
            skPoint(sketch, "E38.11.82.0", {"position": v(-6.35, -448.73) * mm});
            skPoint(sketch, "E38.11.83.0", {"position": v(-6.35, -455.08) * mm});
            skPoint(sketch, "E38.11.84.0", {"position": v(-6.35, -461.43) * mm});
            skPoint(sketch, "E38.11.85.0", {"position": v(-6.35, -467.78) * mm});
            skPoint(sketch, "E38.11.86.0", {"position": v(-6.35, -474.13) * mm});
            skPoint(sketch, "E38.11.87.0", {"position": v(-6.35, -480.48) * mm});
            skPoint(sketch, "E38.11.88.0", {"position": v(-6.35, -486.83) * mm});
            skPoint(sketch, "E38.11.89.0", {"position": v(-6.35, -493.18) * mm});
            skPoint(sketch, "E38.11.90.0", {"position": v(-6.35, -499.53) * mm});
            skPoint(sketch, "E38.11.91.0", {"position": v(-6.35, -505.88) * mm});
            skPoint(sketch, "E38.11.92.0", {"position": v(-6.35, -512.23) * mm});
            skPoint(sketch, "E38.11.93.0", {"position": v(-6.35, -518.58) * mm});
            skPoint(sketch, "E38.11.94.0", {"position": v(-6.35, -524.93) * mm});
            skPoint(sketch, "E38.11.95.0", {"position": v(-6.35, -531.28) * mm});
            skPoint(sketch, "E38.11.96.0", {"position": v(-6.35, -537.63) * mm});
            skPoint(sketch, "E38.11.97.0", {"position": v(-6.35, -543.98) * mm});
            skPoint(sketch, "E38.11.98.0", {"position": v(-6.35, -550.33) * mm});
            skPoint(sketch, "E38.11.99.0", {"position": v(-6.35, -556.68) * mm});
            skPoint(sketch, "E38.12.1.0", {"position": v(0, 65.62) * mm});
            skPoint(sketch, "E38.12.2.0", {"position": v(0, 59.27) * mm});
            skPoint(sketch, "E38.12.3.0", {"position": v(0, 52.92) * mm});
            skPoint(sketch, "E38.12.4.0", {"position": v(0, 46.57) * mm});
            skPoint(sketch, "E38.12.5.0", {"position": v(0, 40.22) * mm});
            skPoint(sketch, "E38.12.6.0", {"position": v(0, 33.87) * mm});
            skPoint(sketch, "E38.12.7.0", {"position": v(0, 27.52) * mm});
            skPoint(sketch, "E38.12.8.0", {"position": v(0, 21.17) * mm});
            skPoint(sketch, "E38.12.9.0", {"position": v(0, 14.82) * mm});
            skPoint(sketch, "E38.12.10.0", {"position": v(0, 8.47) * mm});
            skPoint(sketch, "E38.12.11.0", {"position": v(0, 2.12) * mm});
            skPoint(sketch, "E38.12.12.0", {"position": v(0, -4.23) * mm});
            skPoint(sketch, "E38.12.13.0", {"position": v(0, -10.58) * mm});
            skPoint(sketch, "E38.12.14.0", {"position": v(0, -16.93) * mm});
            skPoint(sketch, "E38.12.15.0", {"position": v(0, -23.28) * mm});
            skPoint(sketch, "E38.12.16.0", {"position": v(0, -29.63) * mm});
            skPoint(sketch, "E38.12.17.0", {"position": v(0, -35.98) * mm});
            skPoint(sketch, "E38.12.18.0", {"position": v(0, -42.33) * mm});
            skPoint(sketch, "E38.12.19.0", {"position": v(0, -48.68) * mm});
            skPoint(sketch, "E38.12.20.0", {"position": v(0, -55.03) * mm});
            skPoint(sketch, "E38.12.21.0", {"position": v(0, -61.38) * mm});
            skPoint(sketch, "E38.12.22.0", {"position": v(0, -67.73) * mm});
            skPoint(sketch, "E38.12.23.0", {"position": v(0, -74.08) * mm});
            skPoint(sketch, "E38.12.24.0", {"position": v(0, -80.43) * mm});
            skPoint(sketch, "E38.12.25.0", {"position": v(0, -86.78) * mm});
            skPoint(sketch, "E38.12.26.0", {"position": v(0, -93.13) * mm});
            skPoint(sketch, "E38.12.27.0", {"position": v(0, -99.48) * mm});
            skPoint(sketch, "E38.12.28.0", {"position": v(0, -105.83) * mm});
            skPoint(sketch, "E38.12.29.0", {"position": v(0, -112.18) * mm});
            skPoint(sketch, "E38.12.30.0", {"position": v(0, -118.53) * mm});
            skPoint(sketch, "E38.12.31.0", {"position": v(0, -124.88) * mm});
            skPoint(sketch, "E38.12.32.0", {"position": v(0, -131.23) * mm});
            skPoint(sketch, "E38.12.33.0", {"position": v(0, -137.58) * mm});
            skPoint(sketch, "E38.12.34.0", {"position": v(0, -143.93) * mm});
            skPoint(sketch, "E38.12.35.0", {"position": v(0, -150.28) * mm});
            skPoint(sketch, "E38.12.36.0", {"position": v(0, -156.63) * mm});
            skPoint(sketch, "E38.12.37.0", {"position": v(0, -162.98) * mm});
            skPoint(sketch, "E38.12.38.0", {"position": v(0, -169.33) * mm});
            skPoint(sketch, "E38.12.39.0", {"position": v(0, -175.68) * mm});
            skPoint(sketch, "E38.12.40.0", {"position": v(0, -182.03) * mm});
            skPoint(sketch, "E38.12.41.0", {"position": v(0, -188.38) * mm});
            skPoint(sketch, "E38.12.42.0", {"position": v(0, -194.73) * mm});
            skPoint(sketch, "E38.12.43.0", {"position": v(0, -201.08) * mm});
            skPoint(sketch, "E38.12.44.0", {"position": v(0, -207.43) * mm});
            skPoint(sketch, "E38.12.45.0", {"position": v(0, -213.78) * mm});
            skPoint(sketch, "E38.12.46.0", {"position": v(0, -220.13) * mm});
            skPoint(sketch, "E38.12.47.0", {"position": v(0, -226.48) * mm});
            skPoint(sketch, "E38.12.48.0", {"position": v(0, -232.83) * mm});
            skPoint(sketch, "E38.12.49.0", {"position": v(0, -239.18) * mm});
            skPoint(sketch, "E38.12.50.0", {"position": v(0, -245.53) * mm});
            skPoint(sketch, "E38.12.51.0", {"position": v(0, -251.88) * mm});
            skPoint(sketch, "E38.12.52.0", {"position": v(0, -258.23) * mm});
            skPoint(sketch, "E38.12.53.0", {"position": v(0, -264.58) * mm});
            skPoint(sketch, "E38.12.54.0", {"position": v(0, -270.93) * mm});
            skPoint(sketch, "E38.12.55.0", {"position": v(0, -277.28) * mm});
            skPoint(sketch, "E38.12.56.0", {"position": v(0, -283.63) * mm});
            skPoint(sketch, "E38.12.57.0", {"position": v(0, -289.98) * mm});
            skPoint(sketch, "E38.12.58.0", {"position": v(0, -296.33) * mm});
            skPoint(sketch, "E38.12.59.0", {"position": v(0, -302.68) * mm});
            skPoint(sketch, "E38.12.60.0", {"position": v(0, -309.03) * mm});
            skPoint(sketch, "E38.12.61.0", {"position": v(0, -315.38) * mm});
            skPoint(sketch, "E38.12.62.0", {"position": v(0, -321.73) * mm});
            skPoint(sketch, "E38.12.63.0", {"position": v(0, -328.08) * mm});
            skPoint(sketch, "E38.12.64.0", {"position": v(0, -334.43) * mm});
            skPoint(sketch, "E38.12.65.0", {"position": v(0, -340.78) * mm});
            skPoint(sketch, "E38.12.66.0", {"position": v(0, -347.13) * mm});
            skPoint(sketch, "E38.12.67.0", {"position": v(0, -353.48) * mm});
            skPoint(sketch, "E38.12.68.0", {"position": v(0, -359.83) * mm});
            skPoint(sketch, "E38.12.69.0", {"position": v(0, -366.18) * mm});
            skPoint(sketch, "E38.12.70.0", {"position": v(0, -372.53) * mm});
            skPoint(sketch, "E38.12.71.0", {"position": v(0, -378.88) * mm});
            skPoint(sketch, "E38.12.72.0", {"position": v(0, -385.23) * mm});
            skPoint(sketch, "E38.12.73.0", {"position": v(0, -391.58) * mm});
            skPoint(sketch, "E38.12.74.0", {"position": v(0, -397.93) * mm});
            skPoint(sketch, "E38.12.75.0", {"position": v(0, -404.28) * mm});
            skPoint(sketch, "E38.12.76.0", {"position": v(0, -410.63) * mm});
            skPoint(sketch, "E38.12.77.0", {"position": v(0, -416.98) * mm});
            skPoint(sketch, "E38.12.78.0", {"position": v(0, -423.33) * mm});
            skPoint(sketch, "E38.12.79.0", {"position": v(0, -429.68) * mm});
            skPoint(sketch, "E38.12.80.0", {"position": v(0, -436.03) * mm});
            skPoint(sketch, "E38.12.81.0", {"position": v(0, -442.38) * mm});
            skPoint(sketch, "E38.12.82.0", {"position": v(0, -448.73) * mm});
            skPoint(sketch, "E38.12.83.0", {"position": v(0, -455.08) * mm});
            skPoint(sketch, "E38.12.84.0", {"position": v(0, -461.43) * mm});
            skPoint(sketch, "E38.12.85.0", {"position": v(0, -467.78) * mm});
            skPoint(sketch, "E38.12.86.0", {"position": v(0, -474.13) * mm});
            skPoint(sketch, "E38.12.87.0", {"position": v(0, -480.48) * mm});
            skPoint(sketch, "E38.12.88.0", {"position": v(0, -486.83) * mm});
            skPoint(sketch, "E38.12.89.0", {"position": v(0, -493.18) * mm});
            skPoint(sketch, "E38.12.90.0", {"position": v(0, -499.53) * mm});
            skPoint(sketch, "E38.12.91.0", {"position": v(0, -505.88) * mm});
            skPoint(sketch, "E38.12.92.0", {"position": v(0, -512.23) * mm});
            skPoint(sketch, "E38.12.93.0", {"position": v(0, -518.58) * mm});
            skPoint(sketch, "E38.12.94.0", {"position": v(0, -524.93) * mm});
            skPoint(sketch, "E38.12.95.0", {"position": v(0, -531.28) * mm});
            skPoint(sketch, "E38.12.96.0", {"position": v(0, -537.63) * mm});
            skPoint(sketch, "E38.12.97.0", {"position": v(0, -543.98) * mm});
            skPoint(sketch, "E38.12.98.0", {"position": v(0, -550.33) * mm});
            skPoint(sketch, "E38.12.99.0", {"position": v(0, -556.68) * mm});
            skPoint(sketch, "E38.13.0.0", {"position": v(6.35, 71.97) * mm});
            skPoint(sketch, "E38.13.1.0", {"position": v(6.35, 65.62) * mm});
            skPoint(sketch, "E38.13.2.0", {"position": v(6.35, 59.27) * mm});
            skPoint(sketch, "E38.13.3.0", {"position": v(6.35, 52.92) * mm});
            skPoint(sketch, "E38.13.4.0", {"position": v(6.35, 46.57) * mm});
            skPoint(sketch, "E38.13.5.0", {"position": v(6.35, 40.22) * mm});
            skPoint(sketch, "E38.13.6.0", {"position": v(6.35, 33.87) * mm});
            skPoint(sketch, "E38.13.7.0", {"position": v(6.35, 27.52) * mm});
            skPoint(sketch, "E38.13.8.0", {"position": v(6.35, 21.17) * mm});
            skPoint(sketch, "E38.13.9.0", {"position": v(6.35, 14.82) * mm});
            skPoint(sketch, "E38.13.10.0", {"position": v(6.35, 8.47) * mm});
            skPoint(sketch, "E38.13.11.0", {"position": v(6.35, 2.12) * mm});
            skPoint(sketch, "E38.13.12.0", {"position": v(6.35, -4.23) * mm});
            skPoint(sketch, "E38.13.13.0", {"position": v(6.35, -10.58) * mm});
            skPoint(sketch, "E38.13.14.0", {"position": v(6.35, -16.93) * mm});
            skPoint(sketch, "E38.13.15.0", {"position": v(6.35, -23.28) * mm});
            skPoint(sketch, "E38.13.16.0", {"position": v(6.35, -29.63) * mm});
            skPoint(sketch, "E38.13.17.0", {"position": v(6.35, -35.98) * mm});
            skPoint(sketch, "E38.13.18.0", {"position": v(6.35, -42.33) * mm});
            skPoint(sketch, "E38.13.19.0", {"position": v(6.35, -48.68) * mm});
            skPoint(sketch, "E38.13.20.0", {"position": v(6.35, -55.03) * mm});
            skPoint(sketch, "E38.13.21.0", {"position": v(6.35, -61.38) * mm});
            skPoint(sketch, "E38.13.22.0", {"position": v(6.35, -67.73) * mm});
            skPoint(sketch, "E38.13.23.0", {"position": v(6.35, -74.08) * mm});
            skPoint(sketch, "E38.13.24.0", {"position": v(6.35, -80.43) * mm});
            skPoint(sketch, "E38.13.25.0", {"position": v(6.35, -86.78) * mm});
            skPoint(sketch, "E38.13.26.0", {"position": v(6.35, -93.13) * mm});
            skPoint(sketch, "E38.13.27.0", {"position": v(6.35, -99.48) * mm});
            skPoint(sketch, "E38.13.28.0", {"position": v(6.35, -105.83) * mm});
            skPoint(sketch, "E38.13.29.0", {"position": v(6.35, -112.18) * mm});
            skPoint(sketch, "E38.13.30.0", {"position": v(6.35, -118.53) * mm});
            skPoint(sketch, "E38.13.31.0", {"position": v(6.35, -124.88) * mm});
            skPoint(sketch, "E38.13.32.0", {"position": v(6.35, -131.23) * mm});
            skPoint(sketch, "E38.13.33.0", {"position": v(6.35, -137.58) * mm});
            skPoint(sketch, "E38.13.34.0", {"position": v(6.35, -143.93) * mm});
            skPoint(sketch, "E38.13.35.0", {"position": v(6.35, -150.28) * mm});
            skPoint(sketch, "E38.13.36.0", {"position": v(6.35, -156.63) * mm});
            skPoint(sketch, "E38.13.37.0", {"position": v(6.35, -162.98) * mm});
            skPoint(sketch, "E38.13.38.0", {"position": v(6.35, -169.33) * mm});
            skPoint(sketch, "E38.13.39.0", {"position": v(6.35, -175.68) * mm});
            skPoint(sketch, "E38.13.40.0", {"position": v(6.35, -182.03) * mm});
            skPoint(sketch, "E38.13.41.0", {"position": v(6.35, -188.38) * mm});
            skPoint(sketch, "E38.13.42.0", {"position": v(6.35, -194.73) * mm});
            skPoint(sketch, "E38.13.43.0", {"position": v(6.35, -201.08) * mm});
            skPoint(sketch, "E38.13.44.0", {"position": v(6.35, -207.43) * mm});
            skPoint(sketch, "E38.13.45.0", {"position": v(6.35, -213.78) * mm});
            skPoint(sketch, "E38.13.46.0", {"position": v(6.35, -220.13) * mm});
            skPoint(sketch, "E38.13.47.0", {"position": v(6.35, -226.48) * mm});
            skPoint(sketch, "E38.13.48.0", {"position": v(6.35, -232.83) * mm});
            skPoint(sketch, "E38.13.49.0", {"position": v(6.35, -239.18) * mm});
            skPoint(sketch, "E38.13.50.0", {"position": v(6.35, -245.53) * mm});
            skPoint(sketch, "E38.13.51.0", {"position": v(6.35, -251.88) * mm});
            skPoint(sketch, "E38.13.52.0", {"position": v(6.35, -258.23) * mm});
            skPoint(sketch, "E38.13.53.0", {"position": v(6.35, -264.58) * mm});
            skPoint(sketch, "E38.13.54.0", {"position": v(6.35, -270.93) * mm});
            skPoint(sketch, "E38.13.55.0", {"position": v(6.35, -277.28) * mm});
            skPoint(sketch, "E38.13.56.0", {"position": v(6.35, -283.63) * mm});
            skPoint(sketch, "E38.13.57.0", {"position": v(6.35, -289.98) * mm});
            skPoint(sketch, "E38.13.58.0", {"position": v(6.35, -296.33) * mm});
            skPoint(sketch, "E38.13.59.0", {"position": v(6.35, -302.68) * mm});
            skPoint(sketch, "E38.13.60.0", {"position": v(6.35, -309.03) * mm});
            skPoint(sketch, "E38.13.61.0", {"position": v(6.35, -315.38) * mm});
            skPoint(sketch, "E38.13.62.0", {"position": v(6.35, -321.73) * mm});
            skPoint(sketch, "E38.13.63.0", {"position": v(6.35, -328.08) * mm});
            skPoint(sketch, "E38.13.64.0", {"position": v(6.35, -334.43) * mm});
            skPoint(sketch, "E38.13.65.0", {"position": v(6.35, -340.78) * mm});
            skPoint(sketch, "E38.13.66.0", {"position": v(6.35, -347.13) * mm});
            skPoint(sketch, "E38.13.67.0", {"position": v(6.35, -353.48) * mm});
            skPoint(sketch, "E38.13.68.0", {"position": v(6.35, -359.83) * mm});
            skPoint(sketch, "E38.13.69.0", {"position": v(6.35, -366.18) * mm});
            skPoint(sketch, "E38.13.70.0", {"position": v(6.35, -372.53) * mm});
            skPoint(sketch, "E38.13.71.0", {"position": v(6.35, -378.88) * mm});
            skPoint(sketch, "E38.13.72.0", {"position": v(6.35, -385.23) * mm});
            skPoint(sketch, "E38.13.73.0", {"position": v(6.35, -391.58) * mm});
            skPoint(sketch, "E38.13.74.0", {"position": v(6.35, -397.93) * mm});
            skPoint(sketch, "E38.13.75.0", {"position": v(6.35, -404.28) * mm});
            skPoint(sketch, "E38.13.76.0", {"position": v(6.35, -410.63) * mm});
            skPoint(sketch, "E38.13.77.0", {"position": v(6.35, -416.98) * mm});
            skPoint(sketch, "E38.13.78.0", {"position": v(6.35, -423.33) * mm});
            skPoint(sketch, "E38.13.79.0", {"position": v(6.35, -429.68) * mm});
            skPoint(sketch, "E38.13.80.0", {"position": v(6.35, -436.03) * mm});
            skPoint(sketch, "E38.13.81.0", {"position": v(6.35, -442.38) * mm});
            skPoint(sketch, "E38.13.82.0", {"position": v(6.35, -448.73) * mm});
            skPoint(sketch, "E38.13.83.0", {"position": v(6.35, -455.08) * mm});
            skPoint(sketch, "E38.13.84.0", {"position": v(6.35, -461.43) * mm});
            skPoint(sketch, "E38.13.85.0", {"position": v(6.35, -467.78) * mm});
            skPoint(sketch, "E38.13.86.0", {"position": v(6.35, -474.13) * mm});
            skPoint(sketch, "E38.13.87.0", {"position": v(6.35, -480.48) * mm});
            skPoint(sketch, "E38.13.88.0", {"position": v(6.35, -486.83) * mm});
            skPoint(sketch, "E38.13.89.0", {"position": v(6.35, -493.18) * mm});
            skPoint(sketch, "E38.13.90.0", {"position": v(6.35, -499.53) * mm});
            skPoint(sketch, "E38.13.91.0", {"position": v(6.35, -505.88) * mm});
            skPoint(sketch, "E38.13.92.0", {"position": v(6.35, -512.23) * mm});
            skPoint(sketch, "E38.13.93.0", {"position": v(6.35, -518.58) * mm});
            skPoint(sketch, "E38.13.94.0", {"position": v(6.35, -524.93) * mm});
            skPoint(sketch, "E38.13.95.0", {"position": v(6.35, -531.28) * mm});
            skPoint(sketch, "E38.13.96.0", {"position": v(6.35, -537.63) * mm});
            skPoint(sketch, "E38.13.97.0", {"position": v(6.35, -543.98) * mm});
            skPoint(sketch, "E38.13.98.0", {"position": v(6.35, -550.33) * mm});
            skPoint(sketch, "E38.13.99.0", {"position": v(6.35, -556.68) * mm});
            skPoint(sketch, "E38.14.0.0", {"position": v(12.7, 71.97) * mm});
            skPoint(sketch, "E38.14.1.0", {"position": v(12.7, 65.62) * mm});
            skPoint(sketch, "E38.14.2.0", {"position": v(12.7, 59.27) * mm});
            skPoint(sketch, "E38.14.3.0", {"position": v(12.7, 52.92) * mm});
            skPoint(sketch, "E38.14.4.0", {"position": v(12.7, 46.57) * mm});
            skPoint(sketch, "E38.14.5.0", {"position": v(12.7, 40.22) * mm});
            skPoint(sketch, "E38.14.6.0", {"position": v(12.7, 33.87) * mm});
            skPoint(sketch, "E38.14.7.0", {"position": v(12.7, 27.52) * mm});
            skPoint(sketch, "E38.14.8.0", {"position": v(12.7, 21.17) * mm});
            skPoint(sketch, "E38.14.9.0", {"position": v(12.7, 14.82) * mm});
            skPoint(sketch, "E38.14.10.0", {"position": v(12.7, 8.47) * mm});
            skPoint(sketch, "E38.14.11.0", {"position": v(12.7, 2.12) * mm});
            skPoint(sketch, "E38.14.12.0", {"position": v(12.7, -4.23) * mm});
            skPoint(sketch, "E38.14.13.0", {"position": v(12.7, -10.58) * mm});
            skPoint(sketch, "E38.14.14.0", {"position": v(12.7, -16.93) * mm});
            skPoint(sketch, "E38.14.15.0", {"position": v(12.7, -23.28) * mm});
            skPoint(sketch, "E38.14.16.0", {"position": v(12.7, -29.63) * mm});
            skPoint(sketch, "E38.14.17.0", {"position": v(12.7, -35.98) * mm});
            skPoint(sketch, "E38.14.18.0", {"position": v(12.7, -42.33) * mm});
            skPoint(sketch, "E38.14.19.0", {"position": v(12.7, -48.68) * mm});
            skPoint(sketch, "E38.14.20.0", {"position": v(12.7, -55.03) * mm});
            skPoint(sketch, "E38.14.21.0", {"position": v(12.7, -61.38) * mm});
            skPoint(sketch, "E38.14.22.0", {"position": v(12.7, -67.73) * mm});
            skPoint(sketch, "E38.14.23.0", {"position": v(12.7, -74.08) * mm});
            skPoint(sketch, "E38.14.24.0", {"position": v(12.7, -80.43) * mm});
            skPoint(sketch, "E38.14.25.0", {"position": v(12.7, -86.78) * mm});
            skPoint(sketch, "E38.14.26.0", {"position": v(12.7, -93.13) * mm});
            skPoint(sketch, "E38.14.27.0", {"position": v(12.7, -99.48) * mm});
            skPoint(sketch, "E38.14.28.0", {"position": v(12.7, -105.83) * mm});
            skPoint(sketch, "E38.14.29.0", {"position": v(12.7, -112.18) * mm});
            skPoint(sketch, "E38.14.30.0", {"position": v(12.7, -118.53) * mm});
            skPoint(sketch, "E38.14.31.0", {"position": v(12.7, -124.88) * mm});
            skPoint(sketch, "E38.14.32.0", {"position": v(12.7, -131.23) * mm});
            skPoint(sketch, "E38.14.33.0", {"position": v(12.7, -137.58) * mm});
            skPoint(sketch, "E38.14.34.0", {"position": v(12.7, -143.93) * mm});
            skPoint(sketch, "E38.14.35.0", {"position": v(12.7, -150.28) * mm});
            skPoint(sketch, "E38.14.36.0", {"position": v(12.7, -156.63) * mm});
            skPoint(sketch, "E38.14.37.0", {"position": v(12.7, -162.98) * mm});
            skPoint(sketch, "E38.14.38.0", {"position": v(12.7, -169.33) * mm});
            skPoint(sketch, "E38.14.39.0", {"position": v(12.7, -175.68) * mm});
            skPoint(sketch, "E38.14.40.0", {"position": v(12.7, -182.03) * mm});
            skPoint(sketch, "E38.14.41.0", {"position": v(12.7, -188.38) * mm});
            skPoint(sketch, "E38.14.42.0", {"position": v(12.7, -194.73) * mm});
            skPoint(sketch, "E38.14.43.0", {"position": v(12.7, -201.08) * mm});
            skPoint(sketch, "E38.14.44.0", {"position": v(12.7, -207.43) * mm});
            skPoint(sketch, "E38.14.45.0", {"position": v(12.7, -213.78) * mm});
            skPoint(sketch, "E38.14.46.0", {"position": v(12.7, -220.13) * mm});
            skPoint(sketch, "E38.14.47.0", {"position": v(12.7, -226.48) * mm});
            skPoint(sketch, "E38.14.48.0", {"position": v(12.7, -232.83) * mm});
            skPoint(sketch, "E38.14.49.0", {"position": v(12.7, -239.18) * mm});
            skPoint(sketch, "E38.14.50.0", {"position": v(12.7, -245.53) * mm});
            skPoint(sketch, "E38.14.51.0", {"position": v(12.7, -251.88) * mm});
            skPoint(sketch, "E38.14.52.0", {"position": v(12.7, -258.23) * mm});
            skPoint(sketch, "E38.14.53.0", {"position": v(12.7, -264.58) * mm});
            skPoint(sketch, "E38.14.54.0", {"position": v(12.7, -270.93) * mm});
            skPoint(sketch, "E38.14.55.0", {"position": v(12.7, -277.28) * mm});
            skPoint(sketch, "E38.14.56.0", {"position": v(12.7, -283.63) * mm});
            skPoint(sketch, "E38.14.57.0", {"position": v(12.7, -289.98) * mm});
            skPoint(sketch, "E38.14.58.0", {"position": v(12.7, -296.33) * mm});
            skPoint(sketch, "E38.14.59.0", {"position": v(12.7, -302.68) * mm});
            skPoint(sketch, "E38.14.60.0", {"position": v(12.7, -309.03) * mm});
            skPoint(sketch, "E38.14.61.0", {"position": v(12.7, -315.38) * mm});
            skPoint(sketch, "E38.14.62.0", {"position": v(12.7, -321.73) * mm});
            skPoint(sketch, "E38.14.63.0", {"position": v(12.7, -328.08) * mm});
            skPoint(sketch, "E38.14.64.0", {"position": v(12.7, -334.43) * mm});
            skPoint(sketch, "E38.14.65.0", {"position": v(12.7, -340.78) * mm});
            skPoint(sketch, "E38.14.66.0", {"position": v(12.7, -347.13) * mm});
            skPoint(sketch, "E38.14.67.0", {"position": v(12.7, -353.48) * mm});
            skPoint(sketch, "E38.14.68.0", {"position": v(12.7, -359.83) * mm});
            skPoint(sketch, "E38.14.69.0", {"position": v(12.7, -366.18) * mm});
            skPoint(sketch, "E38.14.70.0", {"position": v(12.7, -372.53) * mm});
            skPoint(sketch, "E38.14.71.0", {"position": v(12.7, -378.88) * mm});
            skPoint(sketch, "E38.14.72.0", {"position": v(12.7, -385.23) * mm});
            skPoint(sketch, "E38.14.73.0", {"position": v(12.7, -391.58) * mm});
            skPoint(sketch, "E38.14.74.0", {"position": v(12.7, -397.93) * mm});
            skPoint(sketch, "E38.14.75.0", {"position": v(12.7, -404.28) * mm});
            skPoint(sketch, "E38.14.76.0", {"position": v(12.7, -410.63) * mm});
            skPoint(sketch, "E38.14.77.0", {"position": v(12.7, -416.98) * mm});
            skPoint(sketch, "E38.14.78.0", {"position": v(12.7, -423.33) * mm});
            skPoint(sketch, "E38.14.79.0", {"position": v(12.7, -429.68) * mm});
            skPoint(sketch, "E38.14.80.0", {"position": v(12.7, -436.03) * mm});
            skPoint(sketch, "E38.14.81.0", {"position": v(12.7, -442.38) * mm});
            skPoint(sketch, "E38.14.82.0", {"position": v(12.7, -448.73) * mm});
            skPoint(sketch, "E38.14.83.0", {"position": v(12.7, -455.08) * mm});
            skPoint(sketch, "E38.14.84.0", {"position": v(12.7, -461.43) * mm});
            skPoint(sketch, "E38.14.85.0", {"position": v(12.7, -467.78) * mm});
            skPoint(sketch, "E38.14.86.0", {"position": v(12.7, -474.13) * mm});
            skPoint(sketch, "E38.14.87.0", {"position": v(12.7, -480.48) * mm});
            skPoint(sketch, "E38.14.88.0", {"position": v(12.7, -486.83) * mm});
            skPoint(sketch, "E38.14.89.0", {"position": v(12.7, -493.18) * mm});
            skPoint(sketch, "E38.14.90.0", {"position": v(12.7, -499.53) * mm});
            skPoint(sketch, "E38.14.91.0", {"position": v(12.7, -505.88) * mm});
            skPoint(sketch, "E38.14.92.0", {"position": v(12.7, -512.23) * mm});
            skPoint(sketch, "E38.14.93.0", {"position": v(12.7, -518.58) * mm});
            skPoint(sketch, "E38.14.94.0", {"position": v(12.7, -524.93) * mm});
            skPoint(sketch, "E38.14.95.0", {"position": v(12.7, -531.28) * mm});
            skPoint(sketch, "E38.14.96.0", {"position": v(12.7, -537.63) * mm});
            skPoint(sketch, "E38.14.97.0", {"position": v(12.7, -543.98) * mm});
            skPoint(sketch, "E38.14.98.0", {"position": v(12.7, -550.33) * mm});
            skPoint(sketch, "E38.14.99.0", {"position": v(12.7, -556.68) * mm});
            skPoint(sketch, "E38.15.0.0", {"position": v(19.05, 71.97) * mm});
            skPoint(sketch, "E38.15.1.0", {"position": v(19.05, 65.62) * mm});
            skPoint(sketch, "E38.15.2.0", {"position": v(19.05, 59.27) * mm});
            skPoint(sketch, "E38.15.3.0", {"position": v(19.05, 52.92) * mm});
            skPoint(sketch, "E38.15.4.0", {"position": v(19.05, 46.57) * mm});
            skPoint(sketch, "E38.15.5.0", {"position": v(19.05, 40.22) * mm});
            skPoint(sketch, "E38.15.6.0", {"position": v(19.05, 33.87) * mm});
            skPoint(sketch, "E38.15.7.0", {"position": v(19.05, 27.52) * mm});
            skPoint(sketch, "E38.15.8.0", {"position": v(19.05, 21.17) * mm});
            skPoint(sketch, "E38.15.9.0", {"position": v(19.05, 14.82) * mm});
            skPoint(sketch, "E38.15.10.0", {"position": v(19.05, 8.47) * mm});
            skPoint(sketch, "E38.15.11.0", {"position": v(19.05, 2.12) * mm});
            skPoint(sketch, "E38.15.12.0", {"position": v(19.05, -4.23) * mm});
            skPoint(sketch, "E38.15.13.0", {"position": v(19.05, -10.58) * mm});
            skPoint(sketch, "E38.15.14.0", {"position": v(19.05, -16.93) * mm});
            skPoint(sketch, "E38.15.15.0", {"position": v(19.05, -23.28) * mm});
            skPoint(sketch, "E38.15.16.0", {"position": v(19.05, -29.63) * mm});
            skPoint(sketch, "E38.15.17.0", {"position": v(19.05, -35.98) * mm});
            skPoint(sketch, "E38.15.18.0", {"position": v(19.05, -42.33) * mm});
            skPoint(sketch, "E38.15.19.0", {"position": v(19.05, -48.68) * mm});
            skPoint(sketch, "E38.15.20.0", {"position": v(19.05, -55.03) * mm});
            skPoint(sketch, "E38.15.21.0", {"position": v(19.05, -61.38) * mm});
            skPoint(sketch, "E38.15.22.0", {"position": v(19.05, -67.73) * mm});
            skPoint(sketch, "E38.15.23.0", {"position": v(19.05, -74.08) * mm});
            skPoint(sketch, "E38.15.24.0", {"position": v(19.05, -80.43) * mm});
            skPoint(sketch, "E38.15.25.0", {"position": v(19.05, -86.78) * mm});
            skPoint(sketch, "E38.15.26.0", {"position": v(19.05, -93.13) * mm});
            skPoint(sketch, "E38.15.27.0", {"position": v(19.05, -99.48) * mm});
            skPoint(sketch, "E38.15.28.0", {"position": v(19.05, -105.83) * mm});
            skPoint(sketch, "E38.15.29.0", {"position": v(19.05, -112.18) * mm});
            skPoint(sketch, "E38.15.30.0", {"position": v(19.05, -118.53) * mm});
            skPoint(sketch, "E38.15.31.0", {"position": v(19.05, -124.88) * mm});
            skPoint(sketch, "E38.15.32.0", {"position": v(19.05, -131.23) * mm});
            skPoint(sketch, "E38.15.33.0", {"position": v(19.05, -137.58) * mm});
            skPoint(sketch, "E38.15.34.0", {"position": v(19.05, -143.93) * mm});
            skPoint(sketch, "E38.15.35.0", {"position": v(19.05, -150.28) * mm});
            skPoint(sketch, "E38.15.36.0", {"position": v(19.05, -156.63) * mm});
            skPoint(sketch, "E38.15.37.0", {"position": v(19.05, -162.98) * mm});
            skPoint(sketch, "E38.15.38.0", {"position": v(19.05, -169.33) * mm});
            skPoint(sketch, "E38.15.39.0", {"position": v(19.05, -175.68) * mm});
            skPoint(sketch, "E38.15.40.0", {"position": v(19.05, -182.03) * mm});
            skPoint(sketch, "E38.15.41.0", {"position": v(19.05, -188.38) * mm});
            skPoint(sketch, "E38.15.42.0", {"position": v(19.05, -194.73) * mm});
            skPoint(sketch, "E38.15.43.0", {"position": v(19.05, -201.08) * mm});
            skPoint(sketch, "E38.15.44.0", {"position": v(19.05, -207.43) * mm});
            skPoint(sketch, "E38.15.45.0", {"position": v(19.05, -213.78) * mm});
            skPoint(sketch, "E38.15.46.0", {"position": v(19.05, -220.13) * mm});
            skPoint(sketch, "E38.15.47.0", {"position": v(19.05, -226.48) * mm});
            skPoint(sketch, "E38.15.48.0", {"position": v(19.05, -232.83) * mm});
            skPoint(sketch, "E38.15.49.0", {"position": v(19.05, -239.18) * mm});
            skPoint(sketch, "E38.15.50.0", {"position": v(19.05, -245.53) * mm});
            skPoint(sketch, "E38.15.51.0", {"position": v(19.05, -251.88) * mm});
            skPoint(sketch, "E38.15.52.0", {"position": v(19.05, -258.23) * mm});
            skPoint(sketch, "E38.15.53.0", {"position": v(19.05, -264.58) * mm});
            skPoint(sketch, "E38.15.54.0", {"position": v(19.05, -270.93) * mm});
            skPoint(sketch, "E38.15.55.0", {"position": v(19.05, -277.28) * mm});
            skPoint(sketch, "E38.15.56.0", {"position": v(19.05, -283.63) * mm});
            skPoint(sketch, "E38.15.57.0", {"position": v(19.05, -289.98) * mm});
            skPoint(sketch, "E38.15.58.0", {"position": v(19.05, -296.33) * mm});
            skPoint(sketch, "E38.15.59.0", {"position": v(19.05, -302.68) * mm});
            skPoint(sketch, "E38.15.60.0", {"position": v(19.05, -309.03) * mm});
            skPoint(sketch, "E38.15.61.0", {"position": v(19.05, -315.38) * mm});
            skPoint(sketch, "E38.15.62.0", {"position": v(19.05, -321.73) * mm});
            skPoint(sketch, "E38.15.63.0", {"position": v(19.05, -328.08) * mm});
            skPoint(sketch, "E38.15.64.0", {"position": v(19.05, -334.43) * mm});
            skPoint(sketch, "E38.15.65.0", {"position": v(19.05, -340.78) * mm});
            skPoint(sketch, "E38.15.66.0", {"position": v(19.05, -347.13) * mm});
            skPoint(sketch, "E38.15.67.0", {"position": v(19.05, -353.48) * mm});
            skPoint(sketch, "E38.15.68.0", {"position": v(19.05, -359.83) * mm});
            skPoint(sketch, "E38.15.69.0", {"position": v(19.05, -366.18) * mm});
            skPoint(sketch, "E38.15.70.0", {"position": v(19.05, -372.53) * mm});
            skPoint(sketch, "E38.15.71.0", {"position": v(19.05, -378.88) * mm});
            skPoint(sketch, "E38.15.72.0", {"position": v(19.05, -385.23) * mm});
            skPoint(sketch, "E38.15.73.0", {"position": v(19.05, -391.58) * mm});
            skPoint(sketch, "E38.15.74.0", {"position": v(19.05, -397.93) * mm});
            skPoint(sketch, "E38.15.75.0", {"position": v(19.05, -404.28) * mm});
            skPoint(sketch, "E38.15.76.0", {"position": v(19.05, -410.63) * mm});
            skPoint(sketch, "E38.15.77.0", {"position": v(19.05, -416.98) * mm});
            skPoint(sketch, "E38.15.78.0", {"position": v(19.05, -423.33) * mm});
            skPoint(sketch, "E38.15.79.0", {"position": v(19.05, -429.68) * mm});
            skPoint(sketch, "E38.15.80.0", {"position": v(19.05, -436.03) * mm});
            skPoint(sketch, "E38.15.81.0", {"position": v(19.05, -442.38) * mm});
            skPoint(sketch, "E38.15.82.0", {"position": v(19.05, -448.73) * mm});
            skPoint(sketch, "E38.15.83.0", {"position": v(19.05, -455.08) * mm});
            skPoint(sketch, "E38.15.84.0", {"position": v(19.05, -461.43) * mm});
            skPoint(sketch, "E38.15.85.0", {"position": v(19.05, -467.78) * mm});
            skPoint(sketch, "E38.15.86.0", {"position": v(19.05, -474.13) * mm});
            skPoint(sketch, "E38.15.87.0", {"position": v(19.05, -480.48) * mm});
            skPoint(sketch, "E38.15.88.0", {"position": v(19.05, -486.83) * mm});
            skPoint(sketch, "E38.15.89.0", {"position": v(19.05, -493.18) * mm});
            skPoint(sketch, "E38.15.90.0", {"position": v(19.05, -499.53) * mm});
            skPoint(sketch, "E38.15.91.0", {"position": v(19.05, -505.88) * mm});
            skPoint(sketch, "E38.15.92.0", {"position": v(19.05, -512.23) * mm});
            skPoint(sketch, "E38.15.93.0", {"position": v(19.05, -518.58) * mm});
            skPoint(sketch, "E38.15.94.0", {"position": v(19.05, -524.93) * mm});
            skPoint(sketch, "E38.15.95.0", {"position": v(19.05, -531.28) * mm});
            skPoint(sketch, "E38.15.96.0", {"position": v(19.05, -537.63) * mm});
            skPoint(sketch, "E38.15.97.0", {"position": v(19.05, -543.98) * mm});
            skPoint(sketch, "E38.15.98.0", {"position": v(19.05, -550.33) * mm});
            skPoint(sketch, "E38.15.99.0", {"position": v(19.05, -556.68) * mm});
            skPoint(sketch, "E38.16.0.0", {"position": v(25.4, 71.97) * mm});
            skPoint(sketch, "E38.16.1.0", {"position": v(25.4, 65.62) * mm});
            skPoint(sketch, "E38.16.2.0", {"position": v(25.4, 59.27) * mm});
            skPoint(sketch, "E38.16.3.0", {"position": v(25.4, 52.92) * mm});
            skPoint(sketch, "E38.16.4.0", {"position": v(25.4, 46.57) * mm});
            skPoint(sketch, "E38.16.5.0", {"position": v(25.4, 40.22) * mm});
            skPoint(sketch, "E38.16.6.0", {"position": v(25.4, 33.87) * mm});
            skPoint(sketch, "E38.16.7.0", {"position": v(25.4, 27.52) * mm});
            skPoint(sketch, "E38.16.8.0", {"position": v(25.4, 21.17) * mm});
            skPoint(sketch, "E38.16.9.0", {"position": v(25.4, 14.82) * mm});
            skPoint(sketch, "E38.16.10.0", {"position": v(25.4, 8.47) * mm});
            skPoint(sketch, "E38.16.11.0", {"position": v(25.4, 2.12) * mm});
            skPoint(sketch, "E38.16.12.0", {"position": v(25.4, -4.23) * mm});
            skPoint(sketch, "E38.16.13.0", {"position": v(25.4, -10.58) * mm});
            skPoint(sketch, "E38.16.14.0", {"position": v(25.4, -16.93) * mm});
            skPoint(sketch, "E38.16.15.0", {"position": v(25.4, -23.28) * mm});
            skPoint(sketch, "E38.16.16.0", {"position": v(25.4, -29.63) * mm});
            skPoint(sketch, "E38.16.17.0", {"position": v(25.4, -35.98) * mm});
            skPoint(sketch, "E38.16.18.0", {"position": v(25.4, -42.33) * mm});
            skPoint(sketch, "E38.16.19.0", {"position": v(25.4, -48.68) * mm});
            skPoint(sketch, "E38.16.20.0", {"position": v(25.4, -55.03) * mm});
            skPoint(sketch, "E38.16.21.0", {"position": v(25.4, -61.38) * mm});
            skPoint(sketch, "E38.16.22.0", {"position": v(25.4, -67.73) * mm});
            skPoint(sketch, "E38.16.23.0", {"position": v(25.4, -74.08) * mm});
            skPoint(sketch, "E38.16.24.0", {"position": v(25.4, -80.43) * mm});
            skPoint(sketch, "E38.16.25.0", {"position": v(25.4, -86.78) * mm});
            skPoint(sketch, "E38.16.26.0", {"position": v(25.4, -93.13) * mm});
            skPoint(sketch, "E38.16.27.0", {"position": v(25.4, -99.48) * mm});
            skPoint(sketch, "E38.16.28.0", {"position": v(25.4, -105.83) * mm});
            skPoint(sketch, "E38.16.29.0", {"position": v(25.4, -112.18) * mm});
            skPoint(sketch, "E38.16.30.0", {"position": v(25.4, -118.53) * mm});
            skPoint(sketch, "E38.16.31.0", {"position": v(25.4, -124.88) * mm});
            skPoint(sketch, "E38.16.32.0", {"position": v(25.4, -131.23) * mm});
            skPoint(sketch, "E38.16.33.0", {"position": v(25.4, -137.58) * mm});
            skPoint(sketch, "E38.16.34.0", {"position": v(25.4, -143.93) * mm});
            skPoint(sketch, "E38.16.35.0", {"position": v(25.4, -150.28) * mm});
            skPoint(sketch, "E38.16.36.0", {"position": v(25.4, -156.63) * mm});
            skPoint(sketch, "E38.16.37.0", {"position": v(25.4, -162.98) * mm});
            skPoint(sketch, "E38.16.38.0", {"position": v(25.4, -169.33) * mm});
            skPoint(sketch, "E38.16.39.0", {"position": v(25.4, -175.68) * mm});
            skPoint(sketch, "E38.16.40.0", {"position": v(25.4, -182.03) * mm});
            skPoint(sketch, "E38.16.41.0", {"position": v(25.4, -188.38) * mm});
            skPoint(sketch, "E38.16.42.0", {"position": v(25.4, -194.73) * mm});
            skPoint(sketch, "E38.16.43.0", {"position": v(25.4, -201.08) * mm});
            skPoint(sketch, "E38.16.44.0", {"position": v(25.4, -207.43) * mm});
            skPoint(sketch, "E38.16.45.0", {"position": v(25.4, -213.78) * mm});
            skPoint(sketch, "E38.16.46.0", {"position": v(25.4, -220.13) * mm});
            skPoint(sketch, "E38.16.47.0", {"position": v(25.4, -226.48) * mm});
            skPoint(sketch, "E38.16.48.0", {"position": v(25.4, -232.83) * mm});
            skPoint(sketch, "E38.16.49.0", {"position": v(25.4, -239.18) * mm});
            skPoint(sketch, "E38.16.50.0", {"position": v(25.4, -245.53) * mm});
            skPoint(sketch, "E38.16.51.0", {"position": v(25.4, -251.88) * mm});
            skPoint(sketch, "E38.16.52.0", {"position": v(25.4, -258.23) * mm});
            skPoint(sketch, "E38.16.53.0", {"position": v(25.4, -264.58) * mm});
            skPoint(sketch, "E38.16.54.0", {"position": v(25.4, -270.93) * mm});
            skPoint(sketch, "E38.16.55.0", {"position": v(25.4, -277.28) * mm});
            skPoint(sketch, "E38.16.56.0", {"position": v(25.4, -283.63) * mm});
            skPoint(sketch, "E38.16.57.0", {"position": v(25.4, -289.98) * mm});
            skPoint(sketch, "E38.16.58.0", {"position": v(25.4, -296.33) * mm});
            skPoint(sketch, "E38.16.59.0", {"position": v(25.4, -302.68) * mm});
            skPoint(sketch, "E38.16.60.0", {"position": v(25.4, -309.03) * mm});
            skPoint(sketch, "E38.16.61.0", {"position": v(25.4, -315.38) * mm});
            skPoint(sketch, "E38.16.62.0", {"position": v(25.4, -321.73) * mm});
            skPoint(sketch, "E38.16.63.0", {"position": v(25.4, -328.08) * mm});
            skPoint(sketch, "E38.16.64.0", {"position": v(25.4, -334.43) * mm});
            skPoint(sketch, "E38.16.65.0", {"position": v(25.4, -340.78) * mm});
            skPoint(sketch, "E38.16.66.0", {"position": v(25.4, -347.13) * mm});
            skPoint(sketch, "E38.16.67.0", {"position": v(25.4, -353.48) * mm});
            skPoint(sketch, "E38.16.68.0", {"position": v(25.4, -359.83) * mm});
            skPoint(sketch, "E38.16.69.0", {"position": v(25.4, -366.18) * mm});
            skPoint(sketch, "E38.16.70.0", {"position": v(25.4, -372.53) * mm});
            skPoint(sketch, "E38.16.71.0", {"position": v(25.4, -378.88) * mm});
            skPoint(sketch, "E38.16.72.0", {"position": v(25.4, -385.23) * mm});
            skPoint(sketch, "E38.16.73.0", {"position": v(25.4, -391.58) * mm});
            skPoint(sketch, "E38.16.74.0", {"position": v(25.4, -397.93) * mm});
            skPoint(sketch, "E38.16.75.0", {"position": v(25.4, -404.28) * mm});
            skPoint(sketch, "E38.16.76.0", {"position": v(25.4, -410.63) * mm});
            skPoint(sketch, "E38.16.77.0", {"position": v(25.4, -416.98) * mm});
            skPoint(sketch, "E38.16.78.0", {"position": v(25.4, -423.33) * mm});
            skPoint(sketch, "E38.16.79.0", {"position": v(25.4, -429.68) * mm});
            skPoint(sketch, "E38.16.80.0", {"position": v(25.4, -436.03) * mm});
            skPoint(sketch, "E38.16.81.0", {"position": v(25.4, -442.38) * mm});
            skPoint(sketch, "E38.16.82.0", {"position": v(25.4, -448.73) * mm});
            skPoint(sketch, "E38.16.83.0", {"position": v(25.4, -455.08) * mm});
            skPoint(sketch, "E38.16.84.0", {"position": v(25.4, -461.43) * mm});
            skPoint(sketch, "E38.16.85.0", {"position": v(25.4, -467.78) * mm});
            skPoint(sketch, "E38.16.86.0", {"position": v(25.4, -474.13) * mm});
            skPoint(sketch, "E38.16.87.0", {"position": v(25.4, -480.48) * mm});
            skPoint(sketch, "E38.16.88.0", {"position": v(25.4, -486.83) * mm});
            skPoint(sketch, "E38.16.89.0", {"position": v(25.4, -493.18) * mm});
            skPoint(sketch, "E38.16.90.0", {"position": v(25.4, -499.53) * mm});
            skPoint(sketch, "E38.16.91.0", {"position": v(25.4, -505.88) * mm});
            skPoint(sketch, "E38.16.92.0", {"position": v(25.4, -512.23) * mm});
            skPoint(sketch, "E38.16.93.0", {"position": v(25.4, -518.58) * mm});
            skPoint(sketch, "E38.16.94.0", {"position": v(25.4, -524.93) * mm});
            skPoint(sketch, "E38.16.95.0", {"position": v(25.4, -531.28) * mm});
            skPoint(sketch, "E38.16.96.0", {"position": v(25.4, -537.63) * mm});
            skPoint(sketch, "E38.16.97.0", {"position": v(25.4, -543.98) * mm});
            skPoint(sketch, "E38.16.98.0", {"position": v(25.4, -550.33) * mm});
            skPoint(sketch, "E38.16.99.0", {"position": v(25.4, -556.68) * mm});
            skPoint(sketch, "E38.17.0.0", {"position": v(31.75, 71.97) * mm});
            skPoint(sketch, "E38.17.1.0", {"position": v(31.75, 65.62) * mm});
            skPoint(sketch, "E38.17.2.0", {"position": v(31.75, 59.27) * mm});
            skPoint(sketch, "E38.17.3.0", {"position": v(31.75, 52.92) * mm});
            skPoint(sketch, "E38.17.4.0", {"position": v(31.75, 46.57) * mm});
            skPoint(sketch, "E38.17.5.0", {"position": v(31.75, 40.22) * mm});
            skPoint(sketch, "E38.17.6.0", {"position": v(31.75, 33.87) * mm});
            skPoint(sketch, "E38.17.7.0", {"position": v(31.75, 27.52) * mm});
            skPoint(sketch, "E38.17.8.0", {"position": v(31.75, 21.17) * mm});
            skPoint(sketch, "E38.17.9.0", {"position": v(31.75, 14.82) * mm});
            skPoint(sketch, "E38.17.10.0", {"position": v(31.75, 8.47) * mm});
            skPoint(sketch, "E38.17.11.0", {"position": v(31.75, 2.12) * mm});
            skPoint(sketch, "E38.17.12.0", {"position": v(31.75, -4.23) * mm});
            skPoint(sketch, "E38.17.13.0", {"position": v(31.75, -10.58) * mm});
            skPoint(sketch, "E38.17.14.0", {"position": v(31.75, -16.93) * mm});
            skPoint(sketch, "E38.17.15.0", {"position": v(31.75, -23.28) * mm});
            skPoint(sketch, "E38.17.16.0", {"position": v(31.75, -29.63) * mm});
            skPoint(sketch, "E38.17.17.0", {"position": v(31.75, -35.98) * mm});
            skPoint(sketch, "E38.17.18.0", {"position": v(31.75, -42.33) * mm});
            skPoint(sketch, "E38.17.19.0", {"position": v(31.75, -48.68) * mm});
            skPoint(sketch, "E38.17.20.0", {"position": v(31.75, -55.03) * mm});
            skPoint(sketch, "E38.17.21.0", {"position": v(31.75, -61.38) * mm});
            skPoint(sketch, "E38.17.22.0", {"position": v(31.75, -67.73) * mm});
            skPoint(sketch, "E38.17.23.0", {"position": v(31.75, -74.08) * mm});
            skPoint(sketch, "E38.17.24.0", {"position": v(31.75, -80.43) * mm});
            skPoint(sketch, "E38.17.25.0", {"position": v(31.75, -86.78) * mm});
            skPoint(sketch, "E38.17.26.0", {"position": v(31.75, -93.13) * mm});
            skPoint(sketch, "E38.17.27.0", {"position": v(31.75, -99.48) * mm});
            skPoint(sketch, "E38.17.28.0", {"position": v(31.75, -105.83) * mm});
            skPoint(sketch, "E38.17.29.0", {"position": v(31.75, -112.18) * mm});
            skPoint(sketch, "E38.17.30.0", {"position": v(31.75, -118.53) * mm});
            skPoint(sketch, "E38.17.31.0", {"position": v(31.75, -124.88) * mm});
            skPoint(sketch, "E38.17.32.0", {"position": v(31.75, -131.23) * mm});
            skPoint(sketch, "E38.17.33.0", {"position": v(31.75, -137.58) * mm});
            skPoint(sketch, "E38.17.34.0", {"position": v(31.75, -143.93) * mm});
            skPoint(sketch, "E38.17.35.0", {"position": v(31.75, -150.28) * mm});
            skPoint(sketch, "E38.17.36.0", {"position": v(31.75, -156.63) * mm});
            skPoint(sketch, "E38.17.37.0", {"position": v(31.75, -162.98) * mm});
            skPoint(sketch, "E38.17.38.0", {"position": v(31.75, -169.33) * mm});
            skPoint(sketch, "E38.17.39.0", {"position": v(31.75, -175.68) * mm});
            skPoint(sketch, "E38.17.40.0", {"position": v(31.75, -182.03) * mm});
            skPoint(sketch, "E38.17.41.0", {"position": v(31.75, -188.38) * mm});
            skPoint(sketch, "E38.17.42.0", {"position": v(31.75, -194.73) * mm});
            skPoint(sketch, "E38.17.43.0", {"position": v(31.75, -201.08) * mm});
            skPoint(sketch, "E38.17.44.0", {"position": v(31.75, -207.43) * mm});
            skPoint(sketch, "E38.17.45.0", {"position": v(31.75, -213.78) * mm});
            skPoint(sketch, "E38.17.46.0", {"position": v(31.75, -220.13) * mm});
            skPoint(sketch, "E38.17.47.0", {"position": v(31.75, -226.48) * mm});
            skPoint(sketch, "E38.17.48.0", {"position": v(31.75, -232.83) * mm});
            skPoint(sketch, "E38.17.49.0", {"position": v(31.75, -239.18) * mm});
            skPoint(sketch, "E38.17.50.0", {"position": v(31.75, -245.53) * mm});
            skPoint(sketch, "E38.17.51.0", {"position": v(31.75, -251.88) * mm});
            skPoint(sketch, "E38.17.52.0", {"position": v(31.75, -258.23) * mm});
            skPoint(sketch, "E38.17.53.0", {"position": v(31.75, -264.58) * mm});
            skPoint(sketch, "E38.17.54.0", {"position": v(31.75, -270.93) * mm});
            skPoint(sketch, "E38.17.55.0", {"position": v(31.75, -277.28) * mm});
            skPoint(sketch, "E38.17.56.0", {"position": v(31.75, -283.63) * mm});
            skPoint(sketch, "E38.17.57.0", {"position": v(31.75, -289.98) * mm});
            skPoint(sketch, "E38.17.58.0", {"position": v(31.75, -296.33) * mm});
            skPoint(sketch, "E38.17.59.0", {"position": v(31.75, -302.68) * mm});
            skPoint(sketch, "E38.17.60.0", {"position": v(31.75, -309.03) * mm});
            skPoint(sketch, "E38.17.61.0", {"position": v(31.75, -315.38) * mm});
            skPoint(sketch, "E38.17.62.0", {"position": v(31.75, -321.73) * mm});
            skPoint(sketch, "E38.17.63.0", {"position": v(31.75, -328.08) * mm});
            skPoint(sketch, "E38.17.64.0", {"position": v(31.75, -334.43) * mm});
            skPoint(sketch, "E38.17.65.0", {"position": v(31.75, -340.78) * mm});
            skPoint(sketch, "E38.17.66.0", {"position": v(31.75, -347.13) * mm});
            skPoint(sketch, "E38.17.67.0", {"position": v(31.75, -353.48) * mm});
            skPoint(sketch, "E38.17.68.0", {"position": v(31.75, -359.83) * mm});
            skPoint(sketch, "E38.17.69.0", {"position": v(31.75, -366.18) * mm});
            skPoint(sketch, "E38.17.70.0", {"position": v(31.75, -372.53) * mm});
            skPoint(sketch, "E38.17.71.0", {"position": v(31.75, -378.88) * mm});
            skPoint(sketch, "E38.17.72.0", {"position": v(31.75, -385.23) * mm});
            skPoint(sketch, "E38.17.73.0", {"position": v(31.75, -391.58) * mm});
            skPoint(sketch, "E38.17.74.0", {"position": v(31.75, -397.93) * mm});
            skPoint(sketch, "E38.17.75.0", {"position": v(31.75, -404.28) * mm});
            skPoint(sketch, "E38.17.76.0", {"position": v(31.75, -410.63) * mm});
            skPoint(sketch, "E38.17.77.0", {"position": v(31.75, -416.98) * mm});
            skPoint(sketch, "E38.17.78.0", {"position": v(31.75, -423.33) * mm});
            skPoint(sketch, "E38.17.79.0", {"position": v(31.75, -429.68) * mm});
            skPoint(sketch, "E38.17.80.0", {"position": v(31.75, -436.03) * mm});
            skPoint(sketch, "E38.17.81.0", {"position": v(31.75, -442.38) * mm});
            skPoint(sketch, "E38.17.82.0", {"position": v(31.75, -448.73) * mm});
            skPoint(sketch, "E38.17.83.0", {"position": v(31.75, -455.08) * mm});
            skPoint(sketch, "E38.17.84.0", {"position": v(31.75, -461.43) * mm});
            skPoint(sketch, "E38.17.85.0", {"position": v(31.75, -467.78) * mm});
            skPoint(sketch, "E38.17.86.0", {"position": v(31.75, -474.13) * mm});
            skPoint(sketch, "E38.17.87.0", {"position": v(31.75, -480.48) * mm});
            skPoint(sketch, "E38.17.88.0", {"position": v(31.75, -486.83) * mm});
            skPoint(sketch, "E38.17.89.0", {"position": v(31.75, -493.18) * mm});
            skPoint(sketch, "E38.17.90.0", {"position": v(31.75, -499.53) * mm});
            skPoint(sketch, "E38.17.91.0", {"position": v(31.75, -505.88) * mm});
            skPoint(sketch, "E38.17.92.0", {"position": v(31.75, -512.23) * mm});
            skPoint(sketch, "E38.17.93.0", {"position": v(31.75, -518.58) * mm});
            skPoint(sketch, "E38.17.94.0", {"position": v(31.75, -524.93) * mm});
            skPoint(sketch, "E38.17.95.0", {"position": v(31.75, -531.28) * mm});
            skPoint(sketch, "E38.17.96.0", {"position": v(31.75, -537.63) * mm});
            skPoint(sketch, "E38.17.97.0", {"position": v(31.75, -543.98) * mm});
            skPoint(sketch, "E38.17.98.0", {"position": v(31.75, -550.33) * mm});
            skPoint(sketch, "E38.17.99.0", {"position": v(31.75, -556.68) * mm});
            skPoint(sketch, "E38.18.0.0", {"position": v(38.1, 71.97) * mm});
            skPoint(sketch, "E38.18.1.0", {"position": v(38.1, 65.62) * mm});
            skPoint(sketch, "E38.18.2.0", {"position": v(38.1, 59.27) * mm});
            skPoint(sketch, "E38.18.3.0", {"position": v(38.1, 52.92) * mm});
            skPoint(sketch, "E38.18.4.0", {"position": v(38.1, 46.57) * mm});
            skPoint(sketch, "E38.18.5.0", {"position": v(38.1, 40.22) * mm});
            skPoint(sketch, "E38.18.6.0", {"position": v(38.1, 33.87) * mm});
            skPoint(sketch, "E38.18.7.0", {"position": v(38.1, 27.52) * mm});
            skPoint(sketch, "E38.18.8.0", {"position": v(38.1, 21.17) * mm});
            skPoint(sketch, "E38.18.9.0", {"position": v(38.1, 14.82) * mm});
            skPoint(sketch, "E38.18.10.0", {"position": v(38.1, 8.47) * mm});
            skPoint(sketch, "E38.18.11.0", {"position": v(38.1, 2.12) * mm});
            skPoint(sketch, "E38.18.12.0", {"position": v(38.1, -4.23) * mm});
            skPoint(sketch, "E38.18.13.0", {"position": v(38.1, -10.58) * mm});
            skPoint(sketch, "E38.18.14.0", {"position": v(38.1, -16.93) * mm});
            skPoint(sketch, "E38.18.15.0", {"position": v(38.1, -23.28) * mm});
            skPoint(sketch, "E38.18.16.0", {"position": v(38.1, -29.63) * mm});
            skPoint(sketch, "E38.18.17.0", {"position": v(38.1, -35.98) * mm});
            skPoint(sketch, "E38.18.18.0", {"position": v(38.1, -42.33) * mm});
            skPoint(sketch, "E38.18.19.0", {"position": v(38.1, -48.68) * mm});
            skPoint(sketch, "E38.18.20.0", {"position": v(38.1, -55.03) * mm});
            skPoint(sketch, "E38.18.21.0", {"position": v(38.1, -61.38) * mm});
            skPoint(sketch, "E38.18.22.0", {"position": v(38.1, -67.73) * mm});
            skPoint(sketch, "E38.18.23.0", {"position": v(38.1, -74.08) * mm});
            skPoint(sketch, "E38.18.24.0", {"position": v(38.1, -80.43) * mm});
            skPoint(sketch, "E38.18.25.0", {"position": v(38.1, -86.78) * mm});
            skPoint(sketch, "E38.18.26.0", {"position": v(38.1, -93.13) * mm});
            skPoint(sketch, "E38.18.27.0", {"position": v(38.1, -99.48) * mm});
            skPoint(sketch, "E38.18.28.0", {"position": v(38.1, -105.83) * mm});
            skPoint(sketch, "E38.18.29.0", {"position": v(38.1, -112.18) * mm});
            skPoint(sketch, "E38.18.30.0", {"position": v(38.1, -118.53) * mm});
            skPoint(sketch, "E38.18.31.0", {"position": v(38.1, -124.88) * mm});
            skPoint(sketch, "E38.18.32.0", {"position": v(38.1, -131.23) * mm});
            skPoint(sketch, "E38.18.33.0", {"position": v(38.1, -137.58) * mm});
            skPoint(sketch, "E38.18.34.0", {"position": v(38.1, -143.93) * mm});
            skPoint(sketch, "E38.18.35.0", {"position": v(38.1, -150.28) * mm});
            skPoint(sketch, "E38.18.36.0", {"position": v(38.1, -156.63) * mm});
            skPoint(sketch, "E38.18.37.0", {"position": v(38.1, -162.98) * mm});
            skPoint(sketch, "E38.18.38.0", {"position": v(38.1, -169.33) * mm});
            skPoint(sketch, "E38.18.39.0", {"position": v(38.1, -175.68) * mm});
            skPoint(sketch, "E38.18.40.0", {"position": v(38.1, -182.03) * mm});
            skPoint(sketch, "E38.18.41.0", {"position": v(38.1, -188.38) * mm});
            skPoint(sketch, "E38.18.42.0", {"position": v(38.1, -194.73) * mm});
            skPoint(sketch, "E38.18.43.0", {"position": v(38.1, -201.08) * mm});
            skPoint(sketch, "E38.18.44.0", {"position": v(38.1, -207.43) * mm});
            skPoint(sketch, "E38.18.45.0", {"position": v(38.1, -213.78) * mm});
            skPoint(sketch, "E38.18.46.0", {"position": v(38.1, -220.13) * mm});
            skPoint(sketch, "E38.18.47.0", {"position": v(38.1, -226.48) * mm});
            skPoint(sketch, "E38.18.48.0", {"position": v(38.1, -232.83) * mm});
            skPoint(sketch, "E38.18.49.0", {"position": v(38.1, -239.18) * mm});
            skPoint(sketch, "E38.18.50.0", {"position": v(38.1, -245.53) * mm});
            skPoint(sketch, "E38.18.51.0", {"position": v(38.1, -251.88) * mm});
            skPoint(sketch, "E38.18.52.0", {"position": v(38.1, -258.23) * mm});
            skPoint(sketch, "E38.18.53.0", {"position": v(38.1, -264.58) * mm});
            skPoint(sketch, "E38.18.54.0", {"position": v(38.1, -270.93) * mm});
            skPoint(sketch, "E38.18.55.0", {"position": v(38.1, -277.28) * mm});
            skPoint(sketch, "E38.18.56.0", {"position": v(38.1, -283.63) * mm});
            skPoint(sketch, "E38.18.57.0", {"position": v(38.1, -289.98) * mm});
            skPoint(sketch, "E38.18.58.0", {"position": v(38.1, -296.33) * mm});
            skPoint(sketch, "E38.18.59.0", {"position": v(38.1, -302.68) * mm});
            skPoint(sketch, "E38.18.60.0", {"position": v(38.1, -309.03) * mm});
            skPoint(sketch, "E38.18.61.0", {"position": v(38.1, -315.38) * mm});
            skPoint(sketch, "E38.18.62.0", {"position": v(38.1, -321.73) * mm});
            skPoint(sketch, "E38.18.63.0", {"position": v(38.1, -328.08) * mm});
            skPoint(sketch, "E38.18.64.0", {"position": v(38.1, -334.43) * mm});
            skPoint(sketch, "E38.18.65.0", {"position": v(38.1, -340.78) * mm});
            skPoint(sketch, "E38.18.66.0", {"position": v(38.1, -347.13) * mm});
            skPoint(sketch, "E38.18.67.0", {"position": v(38.1, -353.48) * mm});
            skPoint(sketch, "E38.18.68.0", {"position": v(38.1, -359.83) * mm});
            skPoint(sketch, "E38.18.69.0", {"position": v(38.1, -366.18) * mm});
            skPoint(sketch, "E38.18.70.0", {"position": v(38.1, -372.53) * mm});
            skPoint(sketch, "E38.18.71.0", {"position": v(38.1, -378.88) * mm});
            skPoint(sketch, "E38.18.72.0", {"position": v(38.1, -385.23) * mm});
            skPoint(sketch, "E38.18.73.0", {"position": v(38.1, -391.58) * mm});
            skPoint(sketch, "E38.18.74.0", {"position": v(38.1, -397.93) * mm});
            skPoint(sketch, "E38.18.75.0", {"position": v(38.1, -404.28) * mm});
            skPoint(sketch, "E38.18.76.0", {"position": v(38.1, -410.63) * mm});
            skPoint(sketch, "E38.18.77.0", {"position": v(38.1, -416.98) * mm});
            skPoint(sketch, "E38.18.78.0", {"position": v(38.1, -423.33) * mm});
            skPoint(sketch, "E38.18.79.0", {"position": v(38.1, -429.68) * mm});
            skPoint(sketch, "E38.18.80.0", {"position": v(38.1, -436.03) * mm});
            skPoint(sketch, "E38.18.81.0", {"position": v(38.1, -442.38) * mm});
            skPoint(sketch, "E38.18.82.0", {"position": v(38.1, -448.73) * mm});
            skPoint(sketch, "E38.18.83.0", {"position": v(38.1, -455.08) * mm});
            skPoint(sketch, "E38.18.84.0", {"position": v(38.1, -461.43) * mm});
            skPoint(sketch, "E38.18.85.0", {"position": v(38.1, -467.78) * mm});
            skPoint(sketch, "E38.18.86.0", {"position": v(38.1, -474.13) * mm});
            skPoint(sketch, "E38.18.87.0", {"position": v(38.1, -480.48) * mm});
            skPoint(sketch, "E38.18.88.0", {"position": v(38.1, -486.83) * mm});
            skPoint(sketch, "E38.18.89.0", {"position": v(38.1, -493.18) * mm});
            skPoint(sketch, "E38.18.90.0", {"position": v(38.1, -499.53) * mm});
            skPoint(sketch, "E38.18.91.0", {"position": v(38.1, -505.88) * mm});
            skPoint(sketch, "E38.18.92.0", {"position": v(38.1, -512.23) * mm});
            skPoint(sketch, "E38.18.93.0", {"position": v(38.1, -518.58) * mm});
            skPoint(sketch, "E38.18.94.0", {"position": v(38.1, -524.93) * mm});
            skPoint(sketch, "E38.18.95.0", {"position": v(38.1, -531.28) * mm});
            skPoint(sketch, "E38.18.96.0", {"position": v(38.1, -537.63) * mm});
            skPoint(sketch, "E38.18.97.0", {"position": v(38.1, -543.98) * mm});
            skPoint(sketch, "E38.18.98.0", {"position": v(38.1, -550.33) * mm});
            skPoint(sketch, "E38.18.99.0", {"position": v(38.1, -556.68) * mm});
            skPoint(sketch, "E38.19.0.0", {"position": v(44.45, 71.97) * mm});
            skPoint(sketch, "E38.19.1.0", {"position": v(44.45, 65.62) * mm});
            skPoint(sketch, "E38.19.2.0", {"position": v(44.45, 59.27) * mm});
            skPoint(sketch, "E38.19.3.0", {"position": v(44.45, 52.92) * mm});
            skPoint(sketch, "E38.19.4.0", {"position": v(44.45, 46.57) * mm});
            skPoint(sketch, "E38.19.5.0", {"position": v(44.45, 40.22) * mm});
            skPoint(sketch, "E38.19.6.0", {"position": v(44.45, 33.87) * mm});
            skPoint(sketch, "E38.19.7.0", {"position": v(44.45, 27.52) * mm});
            skPoint(sketch, "E38.19.8.0", {"position": v(44.45, 21.17) * mm});
            skPoint(sketch, "E38.19.9.0", {"position": v(44.45, 14.82) * mm});
            skPoint(sketch, "E38.19.10.0", {"position": v(44.45, 8.47) * mm});
            skPoint(sketch, "E38.19.11.0", {"position": v(44.45, 2.12) * mm});
            skPoint(sketch, "E38.19.12.0", {"position": v(44.45, -4.23) * mm});
            skPoint(sketch, "E38.19.13.0", {"position": v(44.45, -10.58) * mm});
            skPoint(sketch, "E38.19.14.0", {"position": v(44.45, -16.93) * mm});
            skPoint(sketch, "E38.19.15.0", {"position": v(44.45, -23.28) * mm});
            skPoint(sketch, "E38.19.16.0", {"position": v(44.45, -29.63) * mm});
            skPoint(sketch, "E38.19.17.0", {"position": v(44.45, -35.98) * mm});
            skPoint(sketch, "E38.19.18.0", {"position": v(44.45, -42.33) * mm});
            skPoint(sketch, "E38.19.19.0", {"position": v(44.45, -48.68) * mm});
            skPoint(sketch, "E38.19.20.0", {"position": v(44.45, -55.03) * mm});
            skPoint(sketch, "E38.19.21.0", {"position": v(44.45, -61.38) * mm});
            skPoint(sketch, "E38.19.22.0", {"position": v(44.45, -67.73) * mm});
            skPoint(sketch, "E38.19.23.0", {"position": v(44.45, -74.08) * mm});
            skPoint(sketch, "E38.19.24.0", {"position": v(44.45, -80.43) * mm});
            skPoint(sketch, "E38.19.25.0", {"position": v(44.45, -86.78) * mm});
            skPoint(sketch, "E38.19.26.0", {"position": v(44.45, -93.13) * mm});
            skPoint(sketch, "E38.19.27.0", {"position": v(44.45, -99.48) * mm});
            skPoint(sketch, "E38.19.28.0", {"position": v(44.45, -105.83) * mm});
            skPoint(sketch, "E38.19.29.0", {"position": v(44.45, -112.18) * mm});
            skPoint(sketch, "E38.19.30.0", {"position": v(44.45, -118.53) * mm});
            skPoint(sketch, "E38.19.31.0", {"position": v(44.45, -124.88) * mm});
            skPoint(sketch, "E38.19.32.0", {"position": v(44.45, -131.23) * mm});
            skPoint(sketch, "E38.19.33.0", {"position": v(44.45, -137.58) * mm});
            skPoint(sketch, "E38.19.34.0", {"position": v(44.45, -143.93) * mm});
            skPoint(sketch, "E38.19.35.0", {"position": v(44.45, -150.28) * mm});
            skPoint(sketch, "E38.19.36.0", {"position": v(44.45, -156.63) * mm});
            skPoint(sketch, "E38.19.37.0", {"position": v(44.45, -162.98) * mm});
            skPoint(sketch, "E38.19.38.0", {"position": v(44.45, -169.33) * mm});
            skPoint(sketch, "E38.19.39.0", {"position": v(44.45, -175.68) * mm});
            skPoint(sketch, "E38.19.40.0", {"position": v(44.45, -182.03) * mm});
            skPoint(sketch, "E38.19.41.0", {"position": v(44.45, -188.38) * mm});
            skPoint(sketch, "E38.19.42.0", {"position": v(44.45, -194.73) * mm});
            skPoint(sketch, "E38.19.43.0", {"position": v(44.45, -201.08) * mm});
            skPoint(sketch, "E38.19.44.0", {"position": v(44.45, -207.43) * mm});
            skPoint(sketch, "E38.19.45.0", {"position": v(44.45, -213.78) * mm});
            skPoint(sketch, "E38.19.46.0", {"position": v(44.45, -220.13) * mm});
            skPoint(sketch, "E38.19.47.0", {"position": v(44.45, -226.48) * mm});
            skPoint(sketch, "E38.19.48.0", {"position": v(44.45, -232.83) * mm});
            skPoint(sketch, "E38.19.49.0", {"position": v(44.45, -239.18) * mm});
            skPoint(sketch, "E38.19.50.0", {"position": v(44.45, -245.53) * mm});
            skPoint(sketch, "E38.19.51.0", {"position": v(44.45, -251.88) * mm});
            skPoint(sketch, "E38.19.52.0", {"position": v(44.45, -258.23) * mm});
            skPoint(sketch, "E38.19.53.0", {"position": v(44.45, -264.58) * mm});
            skPoint(sketch, "E38.19.54.0", {"position": v(44.45, -270.93) * mm});
            skPoint(sketch, "E38.19.55.0", {"position": v(44.45, -277.28) * mm});
            skPoint(sketch, "E38.19.56.0", {"position": v(44.45, -283.63) * mm});
            skPoint(sketch, "E38.19.57.0", {"position": v(44.45, -289.98) * mm});
            skPoint(sketch, "E38.19.58.0", {"position": v(44.45, -296.33) * mm});
            skPoint(sketch, "E38.19.59.0", {"position": v(44.45, -302.68) * mm});
            skPoint(sketch, "E38.19.60.0", {"position": v(44.45, -309.03) * mm});
            skPoint(sketch, "E38.19.61.0", {"position": v(44.45, -315.38) * mm});
            skPoint(sketch, "E38.19.62.0", {"position": v(44.45, -321.73) * mm});
            skPoint(sketch, "E38.19.63.0", {"position": v(44.45, -328.08) * mm});
            skPoint(sketch, "E38.19.64.0", {"position": v(44.45, -334.43) * mm});
            skPoint(sketch, "E38.19.65.0", {"position": v(44.45, -340.78) * mm});
            skPoint(sketch, "E38.19.66.0", {"position": v(44.45, -347.13) * mm});
            skPoint(sketch, "E38.19.67.0", {"position": v(44.45, -353.48) * mm});
            skPoint(sketch, "E38.19.68.0", {"position": v(44.45, -359.83) * mm});
            skPoint(sketch, "E38.19.69.0", {"position": v(44.45, -366.18) * mm});
            skPoint(sketch, "E38.19.70.0", {"position": v(44.45, -372.53) * mm});
            skPoint(sketch, "E38.19.71.0", {"position": v(44.45, -378.88) * mm});
            skPoint(sketch, "E38.19.72.0", {"position": v(44.45, -385.23) * mm});
            skPoint(sketch, "E38.19.73.0", {"position": v(44.45, -391.58) * mm});
            skPoint(sketch, "E38.19.74.0", {"position": v(44.45, -397.93) * mm});
            skPoint(sketch, "E38.19.75.0", {"position": v(44.45, -404.28) * mm});
            skPoint(sketch, "E38.19.76.0", {"position": v(44.45, -410.63) * mm});
            skPoint(sketch, "E38.19.77.0", {"position": v(44.45, -416.98) * mm});
            skPoint(sketch, "E38.19.78.0", {"position": v(44.45, -423.33) * mm});
            skPoint(sketch, "E38.19.79.0", {"position": v(44.45, -429.68) * mm});
            skPoint(sketch, "E38.19.80.0", {"position": v(44.45, -436.03) * mm});
            skPoint(sketch, "E38.19.81.0", {"position": v(44.45, -442.38) * mm});
            skPoint(sketch, "E38.19.82.0", {"position": v(44.45, -448.73) * mm});
            skPoint(sketch, "E38.19.83.0", {"position": v(44.45, -455.08) * mm});
            skPoint(sketch, "E38.19.84.0", {"position": v(44.45, -461.43) * mm});
            skPoint(sketch, "E38.19.85.0", {"position": v(44.45, -467.78) * mm});
            skPoint(sketch, "E38.19.86.0", {"position": v(44.45, -474.13) * mm});
            skPoint(sketch, "E38.19.87.0", {"position": v(44.45, -480.48) * mm});
            skPoint(sketch, "E38.19.88.0", {"position": v(44.45, -486.83) * mm});
            skPoint(sketch, "E38.19.89.0", {"position": v(44.45, -493.18) * mm});
            skPoint(sketch, "E38.19.90.0", {"position": v(44.45, -499.53) * mm});
            skPoint(sketch, "E38.19.91.0", {"position": v(44.45, -505.88) * mm});
            skPoint(sketch, "E38.19.92.0", {"position": v(44.45, -512.23) * mm});
            skPoint(sketch, "E38.19.93.0", {"position": v(44.45, -518.58) * mm});
            skPoint(sketch, "E38.19.94.0", {"position": v(44.45, -524.93) * mm});
            skPoint(sketch, "E38.19.95.0", {"position": v(44.45, -531.28) * mm});
            skPoint(sketch, "E38.19.96.0", {"position": v(44.45, -537.63) * mm});
            skPoint(sketch, "E38.19.97.0", {"position": v(44.45, -543.98) * mm});
            skPoint(sketch, "E38.19.98.0", {"position": v(44.45, -550.33) * mm});
            skPoint(sketch, "E38.19.99.0", {"position": v(44.45, -556.68) * mm});
            skPoint(sketch, "E38.20.0.0", {"position": v(50.8, 71.97) * mm});
            skPoint(sketch, "E38.20.1.0", {"position": v(50.8, 65.62) * mm});
            skPoint(sketch, "E38.20.2.0", {"position": v(50.8, 59.27) * mm});
            skPoint(sketch, "E38.20.3.0", {"position": v(50.8, 52.92) * mm});
            skPoint(sketch, "E38.20.4.0", {"position": v(50.8, 46.57) * mm});
            skPoint(sketch, "E38.20.5.0", {"position": v(50.8, 40.22) * mm});
            skPoint(sketch, "E38.20.6.0", {"position": v(50.8, 33.87) * mm});
            skPoint(sketch, "E38.20.7.0", {"position": v(50.8, 27.52) * mm});
            skPoint(sketch, "E38.20.8.0", {"position": v(50.8, 21.17) * mm});
            skPoint(sketch, "E38.20.9.0", {"position": v(50.8, 14.82) * mm});
            skPoint(sketch, "E38.20.10.0", {"position": v(50.8, 8.47) * mm});
            skPoint(sketch, "E38.20.11.0", {"position": v(50.8, 2.12) * mm});
            skPoint(sketch, "E38.20.12.0", {"position": v(50.8, -4.23) * mm});
            skPoint(sketch, "E38.20.13.0", {"position": v(50.8, -10.58) * mm});
            skPoint(sketch, "E38.20.14.0", {"position": v(50.8, -16.93) * mm});
            skPoint(sketch, "E38.20.15.0", {"position": v(50.8, -23.28) * mm});
            skPoint(sketch, "E38.20.16.0", {"position": v(50.8, -29.63) * mm});
            skPoint(sketch, "E38.20.17.0", {"position": v(50.8, -35.98) * mm});
            skPoint(sketch, "E38.20.18.0", {"position": v(50.8, -42.33) * mm});
            skPoint(sketch, "E38.20.19.0", {"position": v(50.8, -48.68) * mm});
            skPoint(sketch, "E38.20.20.0", {"position": v(50.8, -55.03) * mm});
            skPoint(sketch, "E38.20.21.0", {"position": v(50.8, -61.38) * mm});
            skPoint(sketch, "E38.20.22.0", {"position": v(50.8, -67.73) * mm});
            skPoint(sketch, "E38.20.23.0", {"position": v(50.8, -74.08) * mm});
            skPoint(sketch, "E38.20.24.0", {"position": v(50.8, -80.43) * mm});
            skPoint(sketch, "E38.20.25.0", {"position": v(50.8, -86.78) * mm});
            skPoint(sketch, "E38.20.26.0", {"position": v(50.8, -93.13) * mm});
            skPoint(sketch, "E38.20.27.0", {"position": v(50.8, -99.48) * mm});
            skPoint(sketch, "E38.20.28.0", {"position": v(50.8, -105.83) * mm});
            skPoint(sketch, "E38.20.29.0", {"position": v(50.8, -112.18) * mm});
            skPoint(sketch, "E38.20.30.0", {"position": v(50.8, -118.53) * mm});
            skPoint(sketch, "E38.20.31.0", {"position": v(50.8, -124.88) * mm});
            skPoint(sketch, "E38.20.32.0", {"position": v(50.8, -131.23) * mm});
            skPoint(sketch, "E38.20.33.0", {"position": v(50.8, -137.58) * mm});
            skPoint(sketch, "E38.20.34.0", {"position": v(50.8, -143.93) * mm});
            skPoint(sketch, "E38.20.35.0", {"position": v(50.8, -150.28) * mm});
            skPoint(sketch, "E38.20.36.0", {"position": v(50.8, -156.63) * mm});
            skPoint(sketch, "E38.20.37.0", {"position": v(50.8, -162.98) * mm});
            skPoint(sketch, "E38.20.38.0", {"position": v(50.8, -169.33) * mm});
            skPoint(sketch, "E38.20.39.0", {"position": v(50.8, -175.68) * mm});
            skPoint(sketch, "E38.20.40.0", {"position": v(50.8, -182.03) * mm});
            skPoint(sketch, "E38.20.41.0", {"position": v(50.8, -188.38) * mm});
            skPoint(sketch, "E38.20.42.0", {"position": v(50.8, -194.73) * mm});
            skPoint(sketch, "E38.20.43.0", {"position": v(50.8, -201.08) * mm});
            skPoint(sketch, "E38.20.44.0", {"position": v(50.8, -207.43) * mm});
            skPoint(sketch, "E38.20.45.0", {"position": v(50.8, -213.78) * mm});
            skPoint(sketch, "E38.20.46.0", {"position": v(50.8, -220.13) * mm});
            skPoint(sketch, "E38.20.47.0", {"position": v(50.8, -226.48) * mm});
            skPoint(sketch, "E38.20.48.0", {"position": v(50.8, -232.83) * mm});
            skPoint(sketch, "E38.20.49.0", {"position": v(50.8, -239.18) * mm});
            skPoint(sketch, "E38.20.50.0", {"position": v(50.8, -245.53) * mm});
            skPoint(sketch, "E38.20.51.0", {"position": v(50.8, -251.88) * mm});
            skPoint(sketch, "E38.20.52.0", {"position": v(50.8, -258.23) * mm});
            skPoint(sketch, "E38.20.53.0", {"position": v(50.8, -264.58) * mm});
            skPoint(sketch, "E38.20.54.0", {"position": v(50.8, -270.93) * mm});
            skPoint(sketch, "E38.20.55.0", {"position": v(50.8, -277.28) * mm});
            skPoint(sketch, "E38.20.56.0", {"position": v(50.8, -283.63) * mm});
            skPoint(sketch, "E38.20.57.0", {"position": v(50.8, -289.98) * mm});
            skPoint(sketch, "E38.20.58.0", {"position": v(50.8, -296.33) * mm});
            skPoint(sketch, "E38.20.59.0", {"position": v(50.8, -302.68) * mm});
            skPoint(sketch, "E38.20.60.0", {"position": v(50.8, -309.03) * mm});
            skPoint(sketch, "E38.20.61.0", {"position": v(50.8, -315.38) * mm});
            skPoint(sketch, "E38.20.62.0", {"position": v(50.8, -321.73) * mm});
            skPoint(sketch, "E38.20.63.0", {"position": v(50.8, -328.08) * mm});
            skPoint(sketch, "E38.20.64.0", {"position": v(50.8, -334.43) * mm});
            skPoint(sketch, "E38.20.65.0", {"position": v(50.8, -340.78) * mm});
            skPoint(sketch, "E38.20.66.0", {"position": v(50.8, -347.13) * mm});
            skPoint(sketch, "E38.20.67.0", {"position": v(50.8, -353.48) * mm});
            skPoint(sketch, "E38.20.68.0", {"position": v(50.8, -359.83) * mm});
            skPoint(sketch, "E38.20.69.0", {"position": v(50.8, -366.18) * mm});
            skPoint(sketch, "E38.20.70.0", {"position": v(50.8, -372.53) * mm});
            skPoint(sketch, "E38.20.71.0", {"position": v(50.8, -378.88) * mm});
            skPoint(sketch, "E38.20.72.0", {"position": v(50.8, -385.23) * mm});
            skPoint(sketch, "E38.20.73.0", {"position": v(50.8, -391.58) * mm});
            skPoint(sketch, "E38.20.74.0", {"position": v(50.8, -397.93) * mm});
            skPoint(sketch, "E38.20.75.0", {"position": v(50.8, -404.28) * mm});
            skPoint(sketch, "E38.20.76.0", {"position": v(50.8, -410.63) * mm});
            skPoint(sketch, "E38.20.77.0", {"position": v(50.8, -416.98) * mm});
            skPoint(sketch, "E38.20.78.0", {"position": v(50.8, -423.33) * mm});
            skPoint(sketch, "E38.20.79.0", {"position": v(50.8, -429.68) * mm});
            skPoint(sketch, "E38.20.80.0", {"position": v(50.8, -436.03) * mm});
            skPoint(sketch, "E38.20.81.0", {"position": v(50.8, -442.38) * mm});
            skPoint(sketch, "E38.20.82.0", {"position": v(50.8, -448.73) * mm});
            skPoint(sketch, "E38.20.83.0", {"position": v(50.8, -455.08) * mm});
            skPoint(sketch, "E38.20.84.0", {"position": v(50.8, -461.43) * mm});
            skPoint(sketch, "E38.20.85.0", {"position": v(50.8, -467.78) * mm});
            skPoint(sketch, "E38.20.86.0", {"position": v(50.8, -474.13) * mm});
            skPoint(sketch, "E38.20.87.0", {"position": v(50.8, -480.48) * mm});
            skPoint(sketch, "E38.20.88.0", {"position": v(50.8, -486.83) * mm});
            skPoint(sketch, "E38.20.89.0", {"position": v(50.8, -493.18) * mm});
            skPoint(sketch, "E38.20.90.0", {"position": v(50.8, -499.53) * mm});
            skPoint(sketch, "E38.20.91.0", {"position": v(50.8, -505.88) * mm});
            skPoint(sketch, "E38.20.92.0", {"position": v(50.8, -512.23) * mm});
            skPoint(sketch, "E38.20.93.0", {"position": v(50.8, -518.58) * mm});
            skPoint(sketch, "E38.20.94.0", {"position": v(50.8, -524.93) * mm});
            skPoint(sketch, "E38.20.95.0", {"position": v(50.8, -531.28) * mm});
            skPoint(sketch, "E38.20.96.0", {"position": v(50.8, -537.63) * mm});
            skPoint(sketch, "E38.20.97.0", {"position": v(50.8, -543.98) * mm});
            skPoint(sketch, "E38.20.98.0", {"position": v(50.8, -550.33) * mm});
            skPoint(sketch, "E38.20.99.0", {"position": v(50.8, -556.68) * mm});
            skPoint(sketch, "E38.21.0.0", {"position": v(57.15, 71.97) * mm});
            skPoint(sketch, "E38.21.1.0", {"position": v(57.15, 65.62) * mm});
            skPoint(sketch, "E38.21.2.0", {"position": v(57.15, 59.27) * mm});
            skPoint(sketch, "E38.21.3.0", {"position": v(57.15, 52.92) * mm});
            skPoint(sketch, "E38.21.4.0", {"position": v(57.15, 46.57) * mm});
            skPoint(sketch, "E38.21.5.0", {"position": v(57.15, 40.22) * mm});
            skPoint(sketch, "E38.21.6.0", {"position": v(57.15, 33.87) * mm});
            skPoint(sketch, "E38.21.7.0", {"position": v(57.15, 27.52) * mm});
            skPoint(sketch, "E38.21.8.0", {"position": v(57.15, 21.17) * mm});
            skPoint(sketch, "E38.21.9.0", {"position": v(57.15, 14.82) * mm});
            skPoint(sketch, "E38.21.10.0", {"position": v(57.15, 8.47) * mm});
            skPoint(sketch, "E38.21.11.0", {"position": v(57.15, 2.12) * mm});
            skPoint(sketch, "E38.21.12.0", {"position": v(57.15, -4.23) * mm});
            skPoint(sketch, "E38.21.13.0", {"position": v(57.15, -10.58) * mm});
            skPoint(sketch, "E38.21.14.0", {"position": v(57.15, -16.93) * mm});
            skPoint(sketch, "E38.21.15.0", {"position": v(57.15, -23.28) * mm});
            skPoint(sketch, "E38.21.16.0", {"position": v(57.15, -29.63) * mm});
            skPoint(sketch, "E38.21.17.0", {"position": v(57.15, -35.98) * mm});
            skPoint(sketch, "E38.21.18.0", {"position": v(57.15, -42.33) * mm});
            skPoint(sketch, "E38.21.19.0", {"position": v(57.15, -48.68) * mm});
            skPoint(sketch, "E38.21.20.0", {"position": v(57.15, -55.03) * mm});
            skPoint(sketch, "E38.21.21.0", {"position": v(57.15, -61.38) * mm});
            skPoint(sketch, "E38.21.22.0", {"position": v(57.15, -67.73) * mm});
            skPoint(sketch, "E38.21.23.0", {"position": v(57.15, -74.08) * mm});
            skPoint(sketch, "E38.21.24.0", {"position": v(57.15, -80.43) * mm});
            skPoint(sketch, "E38.21.25.0", {"position": v(57.15, -86.78) * mm});
            skPoint(sketch, "E38.21.26.0", {"position": v(57.15, -93.13) * mm});
            skPoint(sketch, "E38.21.27.0", {"position": v(57.15, -99.48) * mm});
            skPoint(sketch, "E38.21.28.0", {"position": v(57.15, -105.83) * mm});
            skPoint(sketch, "E38.21.29.0", {"position": v(57.15, -112.18) * mm});
            skPoint(sketch, "E38.21.30.0", {"position": v(57.15, -118.53) * mm});
            skPoint(sketch, "E38.21.31.0", {"position": v(57.15, -124.88) * mm});
            skPoint(sketch, "E38.21.32.0", {"position": v(57.15, -131.23) * mm});
            skPoint(sketch, "E38.21.33.0", {"position": v(57.15, -137.58) * mm});
            skPoint(sketch, "E38.21.34.0", {"position": v(57.15, -143.93) * mm});
            skPoint(sketch, "E38.21.35.0", {"position": v(57.15, -150.28) * mm});
            skPoint(sketch, "E38.21.36.0", {"position": v(57.15, -156.63) * mm});
            skPoint(sketch, "E38.21.37.0", {"position": v(57.15, -162.98) * mm});
            skPoint(sketch, "E38.21.38.0", {"position": v(57.15, -169.33) * mm});
            skPoint(sketch, "E38.21.39.0", {"position": v(57.15, -175.68) * mm});
            skPoint(sketch, "E38.21.40.0", {"position": v(57.15, -182.03) * mm});
            skPoint(sketch, "E38.21.41.0", {"position": v(57.15, -188.38) * mm});
            skPoint(sketch, "E38.21.42.0", {"position": v(57.15, -194.73) * mm});
            skPoint(sketch, "E38.21.43.0", {"position": v(57.15, -201.08) * mm});
            skPoint(sketch, "E38.21.44.0", {"position": v(57.15, -207.43) * mm});
            skPoint(sketch, "E38.21.45.0", {"position": v(57.15, -213.78) * mm});
            skPoint(sketch, "E38.21.46.0", {"position": v(57.15, -220.13) * mm});
            skPoint(sketch, "E38.21.47.0", {"position": v(57.15, -226.48) * mm});
            skPoint(sketch, "E38.21.48.0", {"position": v(57.15, -232.83) * mm});
            skPoint(sketch, "E38.21.49.0", {"position": v(57.15, -239.18) * mm});
            skPoint(sketch, "E38.21.50.0", {"position": v(57.15, -245.53) * mm});
            skPoint(sketch, "E38.21.51.0", {"position": v(57.15, -251.88) * mm});
            skPoint(sketch, "E38.21.52.0", {"position": v(57.15, -258.23) * mm});
            skPoint(sketch, "E38.21.53.0", {"position": v(57.15, -264.58) * mm});
            skPoint(sketch, "E38.21.54.0", {"position": v(57.15, -270.93) * mm});
            skPoint(sketch, "E38.21.55.0", {"position": v(57.15, -277.28) * mm});
            skPoint(sketch, "E38.21.56.0", {"position": v(57.15, -283.63) * mm});
            skPoint(sketch, "E38.21.57.0", {"position": v(57.15, -289.98) * mm});
            skPoint(sketch, "E38.21.58.0", {"position": v(57.15, -296.33) * mm});
            skPoint(sketch, "E38.21.59.0", {"position": v(57.15, -302.68) * mm});
            skPoint(sketch, "E38.21.60.0", {"position": v(57.15, -309.03) * mm});
            skPoint(sketch, "E38.21.61.0", {"position": v(57.15, -315.38) * mm});
            skPoint(sketch, "E38.21.62.0", {"position": v(57.15, -321.73) * mm});
            skPoint(sketch, "E38.21.63.0", {"position": v(57.15, -328.08) * mm});
            skPoint(sketch, "E38.21.64.0", {"position": v(57.15, -334.43) * mm});
            skPoint(sketch, "E38.21.65.0", {"position": v(57.15, -340.78) * mm});
            skPoint(sketch, "E38.21.66.0", {"position": v(57.15, -347.13) * mm});
            skPoint(sketch, "E38.21.67.0", {"position": v(57.15, -353.48) * mm});
            skPoint(sketch, "E38.21.68.0", {"position": v(57.15, -359.83) * mm});
            skPoint(sketch, "E38.21.69.0", {"position": v(57.15, -366.18) * mm});
            skPoint(sketch, "E38.21.70.0", {"position": v(57.15, -372.53) * mm});
            skPoint(sketch, "E38.21.71.0", {"position": v(57.15, -378.88) * mm});
            skPoint(sketch, "E38.21.72.0", {"position": v(57.15, -385.23) * mm});
            skPoint(sketch, "E38.21.73.0", {"position": v(57.15, -391.58) * mm});
            skPoint(sketch, "E38.21.74.0", {"position": v(57.15, -397.93) * mm});
            skPoint(sketch, "E38.21.75.0", {"position": v(57.15, -404.28) * mm});
            skPoint(sketch, "E38.21.76.0", {"position": v(57.15, -410.63) * mm});
            skPoint(sketch, "E38.21.77.0", {"position": v(57.15, -416.98) * mm});
            skPoint(sketch, "E38.21.78.0", {"position": v(57.15, -423.33) * mm});
            skPoint(sketch, "E38.21.79.0", {"position": v(57.15, -429.68) * mm});
            skPoint(sketch, "E38.21.80.0", {"position": v(57.15, -436.03) * mm});
            skPoint(sketch, "E38.21.81.0", {"position": v(57.15, -442.38) * mm});
            skPoint(sketch, "E38.21.82.0", {"position": v(57.15, -448.73) * mm});
            skPoint(sketch, "E38.21.83.0", {"position": v(57.15, -455.08) * mm});
            skPoint(sketch, "E38.21.84.0", {"position": v(57.15, -461.43) * mm});
            skPoint(sketch, "E38.21.85.0", {"position": v(57.15, -467.78) * mm});
            skPoint(sketch, "E38.21.86.0", {"position": v(57.15, -474.13) * mm});
            skPoint(sketch, "E38.21.87.0", {"position": v(57.15, -480.48) * mm});
            skPoint(sketch, "E38.21.88.0", {"position": v(57.15, -486.83) * mm});
            skPoint(sketch, "E38.21.89.0", {"position": v(57.15, -493.18) * mm});
            skPoint(sketch, "E38.21.90.0", {"position": v(57.15, -499.53) * mm});
            skPoint(sketch, "E38.21.91.0", {"position": v(57.15, -505.88) * mm});
            skPoint(sketch, "E38.21.92.0", {"position": v(57.15, -512.23) * mm});
            skPoint(sketch, "E38.21.93.0", {"position": v(57.15, -518.58) * mm});
            skPoint(sketch, "E38.21.94.0", {"position": v(57.15, -524.93) * mm});
            skPoint(sketch, "E38.21.95.0", {"position": v(57.15, -531.28) * mm});
            skPoint(sketch, "E38.21.96.0", {"position": v(57.15, -537.63) * mm});
            skPoint(sketch, "E38.21.97.0", {"position": v(57.15, -543.98) * mm});
            skPoint(sketch, "E38.21.98.0", {"position": v(57.15, -550.33) * mm});
            skPoint(sketch, "E38.21.99.0", {"position": v(57.15, -556.68) * mm});
            skPoint(sketch, "E38.22.0.0", {"position": v(63.5, 71.97) * mm});
            skPoint(sketch, "E38.22.1.0", {"position": v(63.5, 65.62) * mm});
            skPoint(sketch, "E38.22.2.0", {"position": v(63.5, 59.27) * mm});
            skPoint(sketch, "E38.22.3.0", {"position": v(63.5, 52.92) * mm});
            skPoint(sketch, "E38.22.4.0", {"position": v(63.5, 46.57) * mm});
            skPoint(sketch, "E38.22.5.0", {"position": v(63.5, 40.22) * mm});
            skPoint(sketch, "E38.22.6.0", {"position": v(63.5, 33.87) * mm});
            skPoint(sketch, "E38.22.7.0", {"position": v(63.5, 27.52) * mm});
            skPoint(sketch, "E38.22.8.0", {"position": v(63.5, 21.17) * mm});
            skPoint(sketch, "E38.22.9.0", {"position": v(63.5, 14.82) * mm});
            skPoint(sketch, "E38.22.10.0", {"position": v(63.5, 8.47) * mm});
            skPoint(sketch, "E38.22.11.0", {"position": v(63.5, 2.12) * mm});
            skPoint(sketch, "E38.22.12.0", {"position": v(63.5, -4.23) * mm});
            skPoint(sketch, "E38.22.13.0", {"position": v(63.5, -10.58) * mm});
            skPoint(sketch, "E38.22.14.0", {"position": v(63.5, -16.93) * mm});
            skPoint(sketch, "E38.22.15.0", {"position": v(63.5, -23.28) * mm});
            skPoint(sketch, "E38.22.16.0", {"position": v(63.5, -29.63) * mm});
            skPoint(sketch, "E38.22.17.0", {"position": v(63.5, -35.98) * mm});
            skPoint(sketch, "E38.22.18.0", {"position": v(63.5, -42.33) * mm});
            skPoint(sketch, "E38.22.19.0", {"position": v(63.5, -48.68) * mm});
            skPoint(sketch, "E38.22.20.0", {"position": v(63.5, -55.03) * mm});
            skPoint(sketch, "E38.22.21.0", {"position": v(63.5, -61.38) * mm});
            skPoint(sketch, "E38.22.22.0", {"position": v(63.5, -67.73) * mm});
            skPoint(sketch, "E38.22.23.0", {"position": v(63.5, -74.08) * mm});
            skPoint(sketch, "E38.22.24.0", {"position": v(63.5, -80.43) * mm});
            skPoint(sketch, "E38.22.25.0", {"position": v(63.5, -86.78) * mm});
            skPoint(sketch, "E38.22.26.0", {"position": v(63.5, -93.13) * mm});
            skPoint(sketch, "E38.22.27.0", {"position": v(63.5, -99.48) * mm});
            skPoint(sketch, "E38.22.28.0", {"position": v(63.5, -105.83) * mm});
            skPoint(sketch, "E38.22.29.0", {"position": v(63.5, -112.18) * mm});
            skPoint(sketch, "E38.22.30.0", {"position": v(63.5, -118.53) * mm});
            skPoint(sketch, "E38.22.31.0", {"position": v(63.5, -124.88) * mm});
            skPoint(sketch, "E38.22.32.0", {"position": v(63.5, -131.23) * mm});
            skPoint(sketch, "E38.22.33.0", {"position": v(63.5, -137.58) * mm});
            skPoint(sketch, "E38.22.34.0", {"position": v(63.5, -143.93) * mm});
            skPoint(sketch, "E38.22.35.0", {"position": v(63.5, -150.28) * mm});
            skPoint(sketch, "E38.22.36.0", {"position": v(63.5, -156.63) * mm});
            skPoint(sketch, "E38.22.37.0", {"position": v(63.5, -162.98) * mm});
            skPoint(sketch, "E38.22.38.0", {"position": v(63.5, -169.33) * mm});
            skPoint(sketch, "E38.22.39.0", {"position": v(63.5, -175.68) * mm});
            skPoint(sketch, "E38.22.40.0", {"position": v(63.5, -182.03) * mm});
            skPoint(sketch, "E38.22.41.0", {"position": v(63.5, -188.38) * mm});
            skPoint(sketch, "E38.22.42.0", {"position": v(63.5, -194.73) * mm});
            skPoint(sketch, "E38.22.43.0", {"position": v(63.5, -201.08) * mm});
            skPoint(sketch, "E38.22.44.0", {"position": v(63.5, -207.43) * mm});
            skPoint(sketch, "E38.22.45.0", {"position": v(63.5, -213.78) * mm});
            skPoint(sketch, "E38.22.46.0", {"position": v(63.5, -220.13) * mm});
            skPoint(sketch, "E38.22.47.0", {"position": v(63.5, -226.48) * mm});
            skPoint(sketch, "E38.22.48.0", {"position": v(63.5, -232.83) * mm});
            skPoint(sketch, "E38.22.49.0", {"position": v(63.5, -239.18) * mm});
            skPoint(sketch, "E38.22.50.0", {"position": v(63.5, -245.53) * mm});
            skPoint(sketch, "E38.22.51.0", {"position": v(63.5, -251.88) * mm});
            skPoint(sketch, "E38.22.52.0", {"position": v(63.5, -258.23) * mm});
            skPoint(sketch, "E38.22.53.0", {"position": v(63.5, -264.58) * mm});
            skPoint(sketch, "E38.22.54.0", {"position": v(63.5, -270.93) * mm});
            skPoint(sketch, "E38.22.55.0", {"position": v(63.5, -277.28) * mm});
            skPoint(sketch, "E38.22.56.0", {"position": v(63.5, -283.63) * mm});
            skPoint(sketch, "E38.22.57.0", {"position": v(63.5, -289.98) * mm});
            skPoint(sketch, "E38.22.58.0", {"position": v(63.5, -296.33) * mm});
            skPoint(sketch, "E38.22.59.0", {"position": v(63.5, -302.68) * mm});
            skPoint(sketch, "E38.22.60.0", {"position": v(63.5, -309.03) * mm});
            skPoint(sketch, "E38.22.61.0", {"position": v(63.5, -315.38) * mm});
            skPoint(sketch, "E38.22.62.0", {"position": v(63.5, -321.73) * mm});
            skPoint(sketch, "E38.22.63.0", {"position": v(63.5, -328.08) * mm});
            skPoint(sketch, "E38.22.64.0", {"position": v(63.5, -334.43) * mm});
            skPoint(sketch, "E38.22.65.0", {"position": v(63.5, -340.78) * mm});
            skPoint(sketch, "E38.22.66.0", {"position": v(63.5, -347.13) * mm});
            skPoint(sketch, "E38.22.67.0", {"position": v(63.5, -353.48) * mm});
            skPoint(sketch, "E38.22.68.0", {"position": v(63.5, -359.83) * mm});
            skPoint(sketch, "E38.22.69.0", {"position": v(63.5, -366.18) * mm});
            skPoint(sketch, "E38.22.70.0", {"position": v(63.5, -372.53) * mm});
            skPoint(sketch, "E38.22.71.0", {"position": v(63.5, -378.88) * mm});
            skPoint(sketch, "E38.22.72.0", {"position": v(63.5, -385.23) * mm});
            skPoint(sketch, "E38.22.73.0", {"position": v(63.5, -391.58) * mm});
            skPoint(sketch, "E38.22.74.0", {"position": v(63.5, -397.93) * mm});
            skPoint(sketch, "E38.22.75.0", {"position": v(63.5, -404.28) * mm});
            skPoint(sketch, "E38.22.76.0", {"position": v(63.5, -410.63) * mm});
            skPoint(sketch, "E38.22.77.0", {"position": v(63.5, -416.98) * mm});
            skPoint(sketch, "E38.22.78.0", {"position": v(63.5, -423.33) * mm});
            skPoint(sketch, "E38.22.79.0", {"position": v(63.5, -429.68) * mm});
            skPoint(sketch, "E38.22.80.0", {"position": v(63.5, -436.03) * mm});
            skPoint(sketch, "E38.22.81.0", {"position": v(63.5, -442.38) * mm});
            skPoint(sketch, "E38.22.82.0", {"position": v(63.5, -448.73) * mm});
            skPoint(sketch, "E38.22.83.0", {"position": v(63.5, -455.08) * mm});
            skPoint(sketch, "E38.22.84.0", {"position": v(63.5, -461.43) * mm});
            skPoint(sketch, "E38.22.85.0", {"position": v(63.5, -467.78) * mm});
            skPoint(sketch, "E38.22.86.0", {"position": v(63.5, -474.13) * mm});
            skPoint(sketch, "E38.22.87.0", {"position": v(63.5, -480.48) * mm});
            skPoint(sketch, "E38.22.88.0", {"position": v(63.5, -486.83) * mm});
            skPoint(sketch, "E38.22.89.0", {"position": v(63.5, -493.18) * mm});
            skPoint(sketch, "E38.22.90.0", {"position": v(63.5, -499.53) * mm});
            skPoint(sketch, "E38.22.91.0", {"position": v(63.5, -505.88) * mm});
            skPoint(sketch, "E38.22.92.0", {"position": v(63.5, -512.23) * mm});
            skPoint(sketch, "E38.22.93.0", {"position": v(63.5, -518.58) * mm});
            skPoint(sketch, "E38.22.94.0", {"position": v(63.5, -524.93) * mm});
            skPoint(sketch, "E38.22.95.0", {"position": v(63.5, -531.28) * mm});
            skPoint(sketch, "E38.22.96.0", {"position": v(63.5, -537.63) * mm});
            skPoint(sketch, "E38.22.97.0", {"position": v(63.5, -543.98) * mm});
            skPoint(sketch, "E38.22.98.0", {"position": v(63.5, -550.33) * mm});
            skPoint(sketch, "E38.22.99.0", {"position": v(63.5, -556.68) * mm});
            skPoint(sketch, "E38.23.0.0", {"position": v(69.85, 71.97) * mm});
            skPoint(sketch, "E38.23.1.0", {"position": v(69.85, 65.62) * mm});
            skPoint(sketch, "E38.23.2.0", {"position": v(69.85, 59.27) * mm});
            skPoint(sketch, "E38.23.3.0", {"position": v(69.85, 52.92) * mm});
            skPoint(sketch, "E38.23.4.0", {"position": v(69.85, 46.57) * mm});
            skPoint(sketch, "E38.23.5.0", {"position": v(69.85, 40.22) * mm});
            skPoint(sketch, "E38.23.6.0", {"position": v(69.85, 33.87) * mm});
            skPoint(sketch, "E38.23.7.0", {"position": v(69.85, 27.52) * mm});
            skPoint(sketch, "E38.23.8.0", {"position": v(69.85, 21.17) * mm});
            skPoint(sketch, "E38.23.9.0", {"position": v(69.85, 14.82) * mm});
            skPoint(sketch, "E38.23.10.0", {"position": v(69.85, 8.47) * mm});
            skPoint(sketch, "E38.23.11.0", {"position": v(69.85, 2.12) * mm});
            skPoint(sketch, "E38.23.12.0", {"position": v(69.85, -4.23) * mm});
            skPoint(sketch, "E38.23.13.0", {"position": v(69.85, -10.58) * mm});
            skPoint(sketch, "E38.23.14.0", {"position": v(69.85, -16.93) * mm});
            skPoint(sketch, "E38.23.15.0", {"position": v(69.85, -23.28) * mm});
            skPoint(sketch, "E38.23.16.0", {"position": v(69.85, -29.63) * mm});
            skPoint(sketch, "E38.23.17.0", {"position": v(69.85, -35.98) * mm});
            skPoint(sketch, "E38.23.18.0", {"position": v(69.85, -42.33) * mm});
            skPoint(sketch, "E38.23.19.0", {"position": v(69.85, -48.68) * mm});
            skPoint(sketch, "E38.23.20.0", {"position": v(69.85, -55.03) * mm});
            skPoint(sketch, "E38.23.21.0", {"position": v(69.85, -61.38) * mm});
            skPoint(sketch, "E38.23.22.0", {"position": v(69.85, -67.73) * mm});
            skPoint(sketch, "E38.23.23.0", {"position": v(69.85, -74.08) * mm});
            skPoint(sketch, "E38.23.24.0", {"position": v(69.85, -80.43) * mm});
            skPoint(sketch, "E38.23.25.0", {"position": v(69.85, -86.78) * mm});
            skPoint(sketch, "E38.23.26.0", {"position": v(69.85, -93.13) * mm});
            skPoint(sketch, "E38.23.27.0", {"position": v(69.85, -99.48) * mm});
            skPoint(sketch, "E38.23.28.0", {"position": v(69.85, -105.83) * mm});
            skPoint(sketch, "E38.23.29.0", {"position": v(69.85, -112.18) * mm});
            skPoint(sketch, "E38.23.30.0", {"position": v(69.85, -118.53) * mm});
            skPoint(sketch, "E38.23.31.0", {"position": v(69.85, -124.88) * mm});
            skPoint(sketch, "E38.23.32.0", {"position": v(69.85, -131.23) * mm});
            skPoint(sketch, "E38.23.33.0", {"position": v(69.85, -137.58) * mm});
            skPoint(sketch, "E38.23.34.0", {"position": v(69.85, -143.93) * mm});
            skPoint(sketch, "E38.23.35.0", {"position": v(69.85, -150.28) * mm});
            skPoint(sketch, "E38.23.36.0", {"position": v(69.85, -156.63) * mm});
            skPoint(sketch, "E38.23.37.0", {"position": v(69.85, -162.98) * mm});
            skPoint(sketch, "E38.23.38.0", {"position": v(69.85, -169.33) * mm});
            skPoint(sketch, "E38.23.39.0", {"position": v(69.85, -175.68) * mm});
            skPoint(sketch, "E38.23.40.0", {"position": v(69.85, -182.03) * mm});
            skPoint(sketch, "E38.23.41.0", {"position": v(69.85, -188.38) * mm});
            skPoint(sketch, "E38.23.42.0", {"position": v(69.85, -194.73) * mm});
            skPoint(sketch, "E38.23.43.0", {"position": v(69.85, -201.08) * mm});
            skPoint(sketch, "E38.23.44.0", {"position": v(69.85, -207.43) * mm});
            skPoint(sketch, "E38.23.45.0", {"position": v(69.85, -213.78) * mm});
            skPoint(sketch, "E38.23.46.0", {"position": v(69.85, -220.13) * mm});
            skPoint(sketch, "E38.23.47.0", {"position": v(69.85, -226.48) * mm});
            skPoint(sketch, "E38.23.48.0", {"position": v(69.85, -232.83) * mm});
            skPoint(sketch, "E38.23.49.0", {"position": v(69.85, -239.18) * mm});
            skPoint(sketch, "E38.23.50.0", {"position": v(69.85, -245.53) * mm});
            skPoint(sketch, "E38.23.51.0", {"position": v(69.85, -251.88) * mm});
            skPoint(sketch, "E38.23.52.0", {"position": v(69.85, -258.23) * mm});
            skPoint(sketch, "E38.23.53.0", {"position": v(69.85, -264.58) * mm});
            skPoint(sketch, "E38.23.54.0", {"position": v(69.85, -270.93) * mm});
            skPoint(sketch, "E38.23.55.0", {"position": v(69.85, -277.28) * mm});
            skPoint(sketch, "E38.23.56.0", {"position": v(69.85, -283.63) * mm});
            skPoint(sketch, "E38.23.57.0", {"position": v(69.85, -289.98) * mm});
            skPoint(sketch, "E38.23.58.0", {"position": v(69.85, -296.33) * mm});
            skPoint(sketch, "E38.23.59.0", {"position": v(69.85, -302.68) * mm});
            skPoint(sketch, "E38.23.60.0", {"position": v(69.85, -309.03) * mm});
            skPoint(sketch, "E38.23.61.0", {"position": v(69.85, -315.38) * mm});
            skPoint(sketch, "E38.23.62.0", {"position": v(69.85, -321.73) * mm});
            skPoint(sketch, "E38.23.63.0", {"position": v(69.85, -328.08) * mm});
            skPoint(sketch, "E38.23.64.0", {"position": v(69.85, -334.43) * mm});
            skPoint(sketch, "E38.23.65.0", {"position": v(69.85, -340.78) * mm});
            skPoint(sketch, "E38.23.66.0", {"position": v(69.85, -347.13) * mm});
            skPoint(sketch, "E38.23.67.0", {"position": v(69.85, -353.48) * mm});
            skPoint(sketch, "E38.23.68.0", {"position": v(69.85, -359.83) * mm});
            skPoint(sketch, "E38.23.69.0", {"position": v(69.85, -366.18) * mm});
            skPoint(sketch, "E38.23.70.0", {"position": v(69.85, -372.53) * mm});
            skPoint(sketch, "E38.23.71.0", {"position": v(69.85, -378.88) * mm});
            skPoint(sketch, "E38.23.72.0", {"position": v(69.85, -385.23) * mm});
            skPoint(sketch, "E38.23.73.0", {"position": v(69.85, -391.58) * mm});
            skPoint(sketch, "E38.23.74.0", {"position": v(69.85, -397.93) * mm});
            skPoint(sketch, "E38.23.75.0", {"position": v(69.85, -404.28) * mm});
            skPoint(sketch, "E38.23.76.0", {"position": v(69.85, -410.63) * mm});
            skPoint(sketch, "E38.23.77.0", {"position": v(69.85, -416.98) * mm});
            skPoint(sketch, "E38.23.78.0", {"position": v(69.85, -423.33) * mm});
            skPoint(sketch, "E38.23.79.0", {"position": v(69.85, -429.68) * mm});
            skPoint(sketch, "E38.23.80.0", {"position": v(69.85, -436.03) * mm});
            skPoint(sketch, "E38.23.81.0", {"position": v(69.85, -442.38) * mm});
            skPoint(sketch, "E38.23.82.0", {"position": v(69.85, -448.73) * mm});
            skPoint(sketch, "E38.23.83.0", {"position": v(69.85, -455.08) * mm});
            skPoint(sketch, "E38.23.84.0", {"position": v(69.85, -461.43) * mm});
            skPoint(sketch, "E38.23.85.0", {"position": v(69.85, -467.78) * mm});
            skPoint(sketch, "E38.23.86.0", {"position": v(69.85, -474.13) * mm});
            skPoint(sketch, "E38.23.87.0", {"position": v(69.85, -480.48) * mm});
            skPoint(sketch, "E38.23.88.0", {"position": v(69.85, -486.83) * mm});
            skPoint(sketch, "E38.23.89.0", {"position": v(69.85, -493.18) * mm});
            skPoint(sketch, "E38.23.90.0", {"position": v(69.85, -499.53) * mm});
            skPoint(sketch, "E38.23.91.0", {"position": v(69.85, -505.88) * mm});
            skPoint(sketch, "E38.23.92.0", {"position": v(69.85, -512.23) * mm});
            skPoint(sketch, "E38.23.93.0", {"position": v(69.85, -518.58) * mm});
            skPoint(sketch, "E38.23.94.0", {"position": v(69.85, -524.93) * mm});
            skPoint(sketch, "E38.23.95.0", {"position": v(69.85, -531.28) * mm});
            skPoint(sketch, "E38.23.96.0", {"position": v(69.85, -537.63) * mm});
            skPoint(sketch, "E38.23.97.0", {"position": v(69.85, -543.98) * mm});
            skPoint(sketch, "E38.23.98.0", {"position": v(69.85, -550.33) * mm});
            skPoint(sketch, "E38.23.99.0", {"position": v(69.85, -556.68) * mm});
            skPoint(sketch, "E38.24.0.0", {"position": v(76.2, 71.97) * mm});
            skPoint(sketch, "E38.24.1.0", {"position": v(76.2, 65.62) * mm});
            skPoint(sketch, "E38.24.2.0", {"position": v(76.2, 59.27) * mm});
            skPoint(sketch, "E38.24.3.0", {"position": v(76.2, 52.92) * mm});
            skPoint(sketch, "E38.24.4.0", {"position": v(76.2, 46.57) * mm});
            skPoint(sketch, "E38.24.5.0", {"position": v(76.2, 40.22) * mm});
            skPoint(sketch, "E38.24.6.0", {"position": v(76.2, 33.87) * mm});
            skPoint(sketch, "E38.24.7.0", {"position": v(76.2, 27.52) * mm});
            skPoint(sketch, "E38.24.8.0", {"position": v(76.2, 21.17) * mm});
            skPoint(sketch, "E38.24.9.0", {"position": v(76.2, 14.82) * mm});
            skPoint(sketch, "E38.24.10.0", {"position": v(76.2, 8.47) * mm});
            skPoint(sketch, "E38.24.11.0", {"position": v(76.2, 2.12) * mm});
            skPoint(sketch, "E38.24.12.0", {"position": v(76.2, -4.23) * mm});
            skPoint(sketch, "E38.24.13.0", {"position": v(76.2, -10.58) * mm});
            skPoint(sketch, "E38.24.14.0", {"position": v(76.2, -16.93) * mm});
            skPoint(sketch, "E38.24.15.0", {"position": v(76.2, -23.28) * mm});
            skPoint(sketch, "E38.24.16.0", {"position": v(76.2, -29.63) * mm});
            skPoint(sketch, "E38.24.17.0", {"position": v(76.2, -35.98) * mm});
            skPoint(sketch, "E38.24.18.0", {"position": v(76.2, -42.33) * mm});
            skPoint(sketch, "E38.24.19.0", {"position": v(76.2, -48.68) * mm});
            skPoint(sketch, "E38.24.20.0", {"position": v(76.2, -55.03) * mm});
            skPoint(sketch, "E38.24.21.0", {"position": v(76.2, -61.38) * mm});
            skPoint(sketch, "E38.24.22.0", {"position": v(76.2, -67.73) * mm});
            skPoint(sketch, "E38.24.23.0", {"position": v(76.2, -74.08) * mm});
            skPoint(sketch, "E38.24.24.0", {"position": v(76.2, -80.43) * mm});
            skPoint(sketch, "E38.24.25.0", {"position": v(76.2, -86.78) * mm});
            skPoint(sketch, "E38.24.26.0", {"position": v(76.2, -93.13) * mm});
            skPoint(sketch, "E38.24.27.0", {"position": v(76.2, -99.48) * mm});
            skPoint(sketch, "E38.24.28.0", {"position": v(76.2, -105.83) * mm});
            skPoint(sketch, "E38.24.29.0", {"position": v(76.2, -112.18) * mm});
            skPoint(sketch, "E38.24.30.0", {"position": v(76.2, -118.53) * mm});
            skPoint(sketch, "E38.24.31.0", {"position": v(76.2, -124.88) * mm});
            skPoint(sketch, "E38.24.32.0", {"position": v(76.2, -131.23) * mm});
            skPoint(sketch, "E38.24.33.0", {"position": v(76.2, -137.58) * mm});
            skPoint(sketch, "E38.24.34.0", {"position": v(76.2, -143.93) * mm});
            skPoint(sketch, "E38.24.35.0", {"position": v(76.2, -150.28) * mm});
            skPoint(sketch, "E38.24.36.0", {"position": v(76.2, -156.63) * mm});
            skPoint(sketch, "E38.24.37.0", {"position": v(76.2, -162.98) * mm});
            skPoint(sketch, "E38.24.38.0", {"position": v(76.2, -169.33) * mm});
            skPoint(sketch, "E38.24.39.0", {"position": v(76.2, -175.68) * mm});
            skPoint(sketch, "E38.24.40.0", {"position": v(76.2, -182.03) * mm});
            skPoint(sketch, "E38.24.41.0", {"position": v(76.2, -188.38) * mm});
            skPoint(sketch, "E38.24.42.0", {"position": v(76.2, -194.73) * mm});
            skPoint(sketch, "E38.24.43.0", {"position": v(76.2, -201.08) * mm});
            skPoint(sketch, "E38.24.44.0", {"position": v(76.2, -207.43) * mm});
            skPoint(sketch, "E38.24.45.0", {"position": v(76.2, -213.78) * mm});
            skPoint(sketch, "E38.24.46.0", {"position": v(76.2, -220.13) * mm});
            skPoint(sketch, "E38.24.47.0", {"position": v(76.2, -226.48) * mm});
            skPoint(sketch, "E38.24.48.0", {"position": v(76.2, -232.83) * mm});
            skPoint(sketch, "E38.24.49.0", {"position": v(76.2, -239.18) * mm});
            skPoint(sketch, "E38.24.50.0", {"position": v(76.2, -245.53) * mm});
            skPoint(sketch, "E38.24.51.0", {"position": v(76.2, -251.88) * mm});
            skPoint(sketch, "E38.24.52.0", {"position": v(76.2, -258.23) * mm});
            skPoint(sketch, "E38.24.53.0", {"position": v(76.2, -264.58) * mm});
            skPoint(sketch, "E38.24.54.0", {"position": v(76.2, -270.93) * mm});
            skPoint(sketch, "E38.24.55.0", {"position": v(76.2, -277.28) * mm});
            skPoint(sketch, "E38.24.56.0", {"position": v(76.2, -283.63) * mm});
            skPoint(sketch, "E38.24.57.0", {"position": v(76.2, -289.98) * mm});
            skPoint(sketch, "E38.24.58.0", {"position": v(76.2, -296.33) * mm});
            skPoint(sketch, "E38.24.59.0", {"position": v(76.2, -302.68) * mm});
            skPoint(sketch, "E38.24.60.0", {"position": v(76.2, -309.03) * mm});
            skPoint(sketch, "E38.24.61.0", {"position": v(76.2, -315.38) * mm});
            skPoint(sketch, "E38.24.62.0", {"position": v(76.2, -321.73) * mm});
            skPoint(sketch, "E38.24.63.0", {"position": v(76.2, -328.08) * mm});
            skPoint(sketch, "E38.24.64.0", {"position": v(76.2, -334.43) * mm});
            skPoint(sketch, "E38.24.65.0", {"position": v(76.2, -340.78) * mm});
            skPoint(sketch, "E38.24.66.0", {"position": v(76.2, -347.13) * mm});
            skPoint(sketch, "E38.24.67.0", {"position": v(76.2, -353.48) * mm});
            skPoint(sketch, "E38.24.68.0", {"position": v(76.2, -359.83) * mm});
            skPoint(sketch, "E38.24.69.0", {"position": v(76.2, -366.18) * mm});
            skPoint(sketch, "E38.24.70.0", {"position": v(76.2, -372.53) * mm});
            skPoint(sketch, "E38.24.71.0", {"position": v(76.2, -378.88) * mm});
            skPoint(sketch, "E38.24.72.0", {"position": v(76.2, -385.23) * mm});
            skPoint(sketch, "E38.24.73.0", {"position": v(76.2, -391.58) * mm});
            skPoint(sketch, "E38.24.74.0", {"position": v(76.2, -397.93) * mm});
            skPoint(sketch, "E38.24.75.0", {"position": v(76.2, -404.28) * mm});
            skPoint(sketch, "E38.24.76.0", {"position": v(76.2, -410.63) * mm});
            skPoint(sketch, "E38.24.77.0", {"position": v(76.2, -416.98) * mm});
            skPoint(sketch, "E38.24.78.0", {"position": v(76.2, -423.33) * mm});
            skPoint(sketch, "E38.24.79.0", {"position": v(76.2, -429.68) * mm});
            skPoint(sketch, "E38.24.80.0", {"position": v(76.2, -436.03) * mm});
            skPoint(sketch, "E38.24.81.0", {"position": v(76.2, -442.38) * mm});
            skPoint(sketch, "E38.24.82.0", {"position": v(76.2, -448.73) * mm});
            skPoint(sketch, "E38.24.83.0", {"position": v(76.2, -455.08) * mm});
            skPoint(sketch, "E38.24.84.0", {"position": v(76.2, -461.43) * mm});
            skPoint(sketch, "E38.24.85.0", {"position": v(76.2, -467.78) * mm});
            skPoint(sketch, "E38.24.86.0", {"position": v(76.2, -474.13) * mm});
            skPoint(sketch, "E38.24.87.0", {"position": v(76.2, -480.48) * mm});
            skPoint(sketch, "E38.24.88.0", {"position": v(76.2, -486.83) * mm});
            skPoint(sketch, "E38.24.89.0", {"position": v(76.2, -493.18) * mm});
            skPoint(sketch, "E38.24.90.0", {"position": v(76.2, -499.53) * mm});
            skPoint(sketch, "E38.24.91.0", {"position": v(76.2, -505.88) * mm});
            skPoint(sketch, "E38.24.92.0", {"position": v(76.2, -512.23) * mm});
            skPoint(sketch, "E38.24.93.0", {"position": v(76.2, -518.58) * mm});
            skPoint(sketch, "E38.24.94.0", {"position": v(76.2, -524.93) * mm});
            skPoint(sketch, "E38.24.95.0", {"position": v(76.2, -531.28) * mm});
            skPoint(sketch, "E38.24.96.0", {"position": v(76.2, -537.63) * mm});
            skPoint(sketch, "E38.24.97.0", {"position": v(76.2, -543.98) * mm});
            skPoint(sketch, "E38.24.98.0", {"position": v(76.2, -550.33) * mm});
            skPoint(sketch, "E38.24.99.0", {"position": v(76.2, -556.68) * mm});
            skPoint(sketch, "E38.25.0.0", {"position": v(82.55, 71.97) * mm});
            skPoint(sketch, "E38.25.1.0", {"position": v(82.55, 65.62) * mm});
            skPoint(sketch, "E38.25.2.0", {"position": v(82.55, 59.27) * mm});
            skPoint(sketch, "E38.25.3.0", {"position": v(82.55, 52.92) * mm});
            skPoint(sketch, "E38.25.4.0", {"position": v(82.55, 46.57) * mm});
            skPoint(sketch, "E38.25.5.0", {"position": v(82.55, 40.22) * mm});
            skPoint(sketch, "E38.25.6.0", {"position": v(82.55, 33.87) * mm});
            skPoint(sketch, "E38.25.7.0", {"position": v(82.55, 27.52) * mm});
            skPoint(sketch, "E38.25.8.0", {"position": v(82.55, 21.17) * mm});
            skPoint(sketch, "E38.25.9.0", {"position": v(82.55, 14.82) * mm});
            skPoint(sketch, "E38.25.10.0", {"position": v(82.55, 8.47) * mm});
            skPoint(sketch, "E38.25.11.0", {"position": v(82.55, 2.12) * mm});
            skPoint(sketch, "E38.25.12.0", {"position": v(82.55, -4.23) * mm});
            skPoint(sketch, "E38.25.13.0", {"position": v(82.55, -10.58) * mm});
            skPoint(sketch, "E38.25.14.0", {"position": v(82.55, -16.93) * mm});
            skPoint(sketch, "E38.25.15.0", {"position": v(82.55, -23.28) * mm});
            skPoint(sketch, "E38.25.16.0", {"position": v(82.55, -29.63) * mm});
            skPoint(sketch, "E38.25.17.0", {"position": v(82.55, -35.98) * mm});
            skPoint(sketch, "E38.25.18.0", {"position": v(82.55, -42.33) * mm});
            skPoint(sketch, "E38.25.19.0", {"position": v(82.55, -48.68) * mm});
            skPoint(sketch, "E38.25.20.0", {"position": v(82.55, -55.03) * mm});
            skPoint(sketch, "E38.25.21.0", {"position": v(82.55, -61.38) * mm});
            skPoint(sketch, "E38.25.22.0", {"position": v(82.55, -67.73) * mm});
            skPoint(sketch, "E38.25.23.0", {"position": v(82.55, -74.08) * mm});
            skPoint(sketch, "E38.25.24.0", {"position": v(82.55, -80.43) * mm});
            skPoint(sketch, "E38.25.25.0", {"position": v(82.55, -86.78) * mm});
            skPoint(sketch, "E38.25.26.0", {"position": v(82.55, -93.13) * mm});
            skPoint(sketch, "E38.25.27.0", {"position": v(82.55, -99.48) * mm});
            skPoint(sketch, "E38.25.28.0", {"position": v(82.55, -105.83) * mm});
            skPoint(sketch, "E38.25.29.0", {"position": v(82.55, -112.18) * mm});
            skPoint(sketch, "E38.25.30.0", {"position": v(82.55, -118.53) * mm});
            skPoint(sketch, "E38.25.31.0", {"position": v(82.55, -124.88) * mm});
            skPoint(sketch, "E38.25.32.0", {"position": v(82.55, -131.23) * mm});
            skPoint(sketch, "E38.25.33.0", {"position": v(82.55, -137.58) * mm});
            skPoint(sketch, "E38.25.34.0", {"position": v(82.55, -143.93) * mm});
            skPoint(sketch, "E38.25.35.0", {"position": v(82.55, -150.28) * mm});
            skPoint(sketch, "E38.25.36.0", {"position": v(82.55, -156.63) * mm});
            skPoint(sketch, "E38.25.37.0", {"position": v(82.55, -162.98) * mm});
            skPoint(sketch, "E38.25.38.0", {"position": v(82.55, -169.33) * mm});
            skPoint(sketch, "E38.25.39.0", {"position": v(82.55, -175.68) * mm});
            skPoint(sketch, "E38.25.40.0", {"position": v(82.55, -182.03) * mm});
            skPoint(sketch, "E38.25.41.0", {"position": v(82.55, -188.38) * mm});
            skPoint(sketch, "E38.25.42.0", {"position": v(82.55, -194.73) * mm});
            skPoint(sketch, "E38.25.43.0", {"position": v(82.55, -201.08) * mm});
            skPoint(sketch, "E38.25.44.0", {"position": v(82.55, -207.43) * mm});
            skPoint(sketch, "E38.25.45.0", {"position": v(82.55, -213.78) * mm});
            skPoint(sketch, "E38.25.46.0", {"position": v(82.55, -220.13) * mm});
            skPoint(sketch, "E38.25.47.0", {"position": v(82.55, -226.48) * mm});
            skPoint(sketch, "E38.25.48.0", {"position": v(82.55, -232.83) * mm});
            skPoint(sketch, "E38.25.49.0", {"position": v(82.55, -239.18) * mm});
            skPoint(sketch, "E38.25.50.0", {"position": v(82.55, -245.53) * mm});
            skPoint(sketch, "E38.25.51.0", {"position": v(82.55, -251.88) * mm});
            skPoint(sketch, "E38.25.52.0", {"position": v(82.55, -258.23) * mm});
            skPoint(sketch, "E38.25.53.0", {"position": v(82.55, -264.58) * mm});
            skPoint(sketch, "E38.25.54.0", {"position": v(82.55, -270.93) * mm});
            skPoint(sketch, "E38.25.55.0", {"position": v(82.55, -277.28) * mm});
            skPoint(sketch, "E38.25.56.0", {"position": v(82.55, -283.63) * mm});
            skPoint(sketch, "E38.25.57.0", {"position": v(82.55, -289.98) * mm});
            skPoint(sketch, "E38.25.58.0", {"position": v(82.55, -296.33) * mm});
            skPoint(sketch, "E38.25.59.0", {"position": v(82.55, -302.68) * mm});
            skPoint(sketch, "E38.25.60.0", {"position": v(82.55, -309.03) * mm});
            skPoint(sketch, "E38.25.61.0", {"position": v(82.55, -315.38) * mm});
            skPoint(sketch, "E38.25.62.0", {"position": v(82.55, -321.73) * mm});
            skPoint(sketch, "E38.25.63.0", {"position": v(82.55, -328.08) * mm});
            skPoint(sketch, "E38.25.64.0", {"position": v(82.55, -334.43) * mm});
            skPoint(sketch, "E38.25.65.0", {"position": v(82.55, -340.78) * mm});
            skPoint(sketch, "E38.25.66.0", {"position": v(82.55, -347.13) * mm});
            skPoint(sketch, "E38.25.67.0", {"position": v(82.55, -353.48) * mm});
            skPoint(sketch, "E38.25.68.0", {"position": v(82.55, -359.83) * mm});
            skPoint(sketch, "E38.25.69.0", {"position": v(82.55, -366.18) * mm});
            skPoint(sketch, "E38.25.70.0", {"position": v(82.55, -372.53) * mm});
            skPoint(sketch, "E38.25.71.0", {"position": v(82.55, -378.88) * mm});
            skPoint(sketch, "E38.25.72.0", {"position": v(82.55, -385.23) * mm});
            skPoint(sketch, "E38.25.73.0", {"position": v(82.55, -391.58) * mm});
            skPoint(sketch, "E38.25.74.0", {"position": v(82.55, -397.93) * mm});
            skPoint(sketch, "E38.25.75.0", {"position": v(82.55, -404.28) * mm});
            skPoint(sketch, "E38.25.76.0", {"position": v(82.55, -410.63) * mm});
            skPoint(sketch, "E38.25.77.0", {"position": v(82.55, -416.98) * mm});
            skPoint(sketch, "E38.25.78.0", {"position": v(82.55, -423.33) * mm});
            skPoint(sketch, "E38.25.79.0", {"position": v(82.55, -429.68) * mm});
            skPoint(sketch, "E38.25.80.0", {"position": v(82.55, -436.03) * mm});
            skPoint(sketch, "E38.25.81.0", {"position": v(82.55, -442.38) * mm});
            skPoint(sketch, "E38.25.82.0", {"position": v(82.55, -448.73) * mm});
            skPoint(sketch, "E38.25.83.0", {"position": v(82.55, -455.08) * mm});
            skPoint(sketch, "E38.25.84.0", {"position": v(82.55, -461.43) * mm});
            skPoint(sketch, "E38.25.85.0", {"position": v(82.55, -467.78) * mm});
            skPoint(sketch, "E38.25.86.0", {"position": v(82.55, -474.13) * mm});
            skPoint(sketch, "E38.25.87.0", {"position": v(82.55, -480.48) * mm});
            skPoint(sketch, "E38.25.88.0", {"position": v(82.55, -486.83) * mm});
            skPoint(sketch, "E38.25.89.0", {"position": v(82.55, -493.18) * mm});
            skPoint(sketch, "E38.25.90.0", {"position": v(82.55, -499.53) * mm});
            skPoint(sketch, "E38.25.91.0", {"position": v(82.55, -505.88) * mm});
            skPoint(sketch, "E38.25.92.0", {"position": v(82.55, -512.23) * mm});
            skPoint(sketch, "E38.25.93.0", {"position": v(82.55, -518.58) * mm});
            skPoint(sketch, "E38.25.94.0", {"position": v(82.55, -524.93) * mm});
            skPoint(sketch, "E38.25.95.0", {"position": v(82.55, -531.28) * mm});
            skPoint(sketch, "E38.25.96.0", {"position": v(82.55, -537.63) * mm});
            skPoint(sketch, "E38.25.97.0", {"position": v(82.55, -543.98) * mm});
            skPoint(sketch, "E38.25.98.0", {"position": v(82.55, -550.33) * mm});
            skPoint(sketch, "E38.25.99.0", {"position": v(82.55, -556.68) * mm});
            skPoint(sketch, "E38.26.0.0", {"position": v(88.9, 71.97) * mm});
            skPoint(sketch, "E38.26.1.0", {"position": v(88.9, 65.62) * mm});
            skPoint(sketch, "E38.26.2.0", {"position": v(88.9, 59.27) * mm});
            skPoint(sketch, "E38.26.3.0", {"position": v(88.9, 52.92) * mm});
            skPoint(sketch, "E38.26.4.0", {"position": v(88.9, 46.57) * mm});
            skPoint(sketch, "E38.26.5.0", {"position": v(88.9, 40.22) * mm});
            skPoint(sketch, "E38.26.6.0", {"position": v(88.9, 33.87) * mm});
            skPoint(sketch, "E38.26.7.0", {"position": v(88.9, 27.52) * mm});
            skPoint(sketch, "E38.26.8.0", {"position": v(88.9, 21.17) * mm});
            skPoint(sketch, "E38.26.9.0", {"position": v(88.9, 14.82) * mm});
            skPoint(sketch, "E38.26.10.0", {"position": v(88.9, 8.47) * mm});
            skPoint(sketch, "E38.26.11.0", {"position": v(88.9, 2.12) * mm});
            skPoint(sketch, "E38.26.12.0", {"position": v(88.9, -4.23) * mm});
            skPoint(sketch, "E38.26.13.0", {"position": v(88.9, -10.58) * mm});
            skPoint(sketch, "E38.26.14.0", {"position": v(88.9, -16.93) * mm});
            skPoint(sketch, "E38.26.15.0", {"position": v(88.9, -23.28) * mm});
            skPoint(sketch, "E38.26.16.0", {"position": v(88.9, -29.63) * mm});
            skPoint(sketch, "E38.26.17.0", {"position": v(88.9, -35.98) * mm});
            skPoint(sketch, "E38.26.18.0", {"position": v(88.9, -42.33) * mm});
            skPoint(sketch, "E38.26.19.0", {"position": v(88.9, -48.68) * mm});
            skPoint(sketch, "E38.26.20.0", {"position": v(88.9, -55.03) * mm});
            skPoint(sketch, "E38.26.21.0", {"position": v(88.9, -61.38) * mm});
            skPoint(sketch, "E38.26.22.0", {"position": v(88.9, -67.73) * mm});
            skPoint(sketch, "E38.26.23.0", {"position": v(88.9, -74.08) * mm});
            skPoint(sketch, "E38.26.24.0", {"position": v(88.9, -80.43) * mm});
            skPoint(sketch, "E38.26.25.0", {"position": v(88.9, -86.78) * mm});
            skPoint(sketch, "E38.26.26.0", {"position": v(88.9, -93.13) * mm});
            skPoint(sketch, "E38.26.27.0", {"position": v(88.9, -99.48) * mm});
            skPoint(sketch, "E38.26.28.0", {"position": v(88.9, -105.83) * mm});
            skPoint(sketch, "E38.26.29.0", {"position": v(88.9, -112.18) * mm});
            skPoint(sketch, "E38.26.30.0", {"position": v(88.9, -118.53) * mm});
            skPoint(sketch, "E38.26.31.0", {"position": v(88.9, -124.88) * mm});
            skPoint(sketch, "E38.26.32.0", {"position": v(88.9, -131.23) * mm});
            skPoint(sketch, "E38.26.33.0", {"position": v(88.9, -137.58) * mm});
            skPoint(sketch, "E38.26.34.0", {"position": v(88.9, -143.93) * mm});
            skPoint(sketch, "E38.26.35.0", {"position": v(88.9, -150.28) * mm});
            skPoint(sketch, "E38.26.36.0", {"position": v(88.9, -156.63) * mm});
            skPoint(sketch, "E38.26.37.0", {"position": v(88.9, -162.98) * mm});
            skPoint(sketch, "E38.26.38.0", {"position": v(88.9, -169.33) * mm});
            skPoint(sketch, "E38.26.39.0", {"position": v(88.9, -175.68) * mm});
            skPoint(sketch, "E38.26.40.0", {"position": v(88.9, -182.03) * mm});
            skPoint(sketch, "E38.26.41.0", {"position": v(88.9, -188.38) * mm});
            skPoint(sketch, "E38.26.42.0", {"position": v(88.9, -194.73) * mm});
            skPoint(sketch, "E38.26.43.0", {"position": v(88.9, -201.08) * mm});
            skPoint(sketch, "E38.26.44.0", {"position": v(88.9, -207.43) * mm});
            skPoint(sketch, "E38.26.45.0", {"position": v(88.9, -213.78) * mm});
            skPoint(sketch, "E38.26.46.0", {"position": v(88.9, -220.13) * mm});
            skPoint(sketch, "E38.26.47.0", {"position": v(88.9, -226.48) * mm});
            skPoint(sketch, "E38.26.48.0", {"position": v(88.9, -232.83) * mm});
            skPoint(sketch, "E38.26.49.0", {"position": v(88.9, -239.18) * mm});
            skPoint(sketch, "E38.26.50.0", {"position": v(88.9, -245.53) * mm});
            skPoint(sketch, "E38.26.51.0", {"position": v(88.9, -251.88) * mm});
            skPoint(sketch, "E38.26.52.0", {"position": v(88.9, -258.23) * mm});
            skPoint(sketch, "E38.26.53.0", {"position": v(88.9, -264.58) * mm});
            skPoint(sketch, "E38.26.54.0", {"position": v(88.9, -270.93) * mm});
            skPoint(sketch, "E38.26.55.0", {"position": v(88.9, -277.28) * mm});
            skPoint(sketch, "E38.26.56.0", {"position": v(88.9, -283.63) * mm});
            skPoint(sketch, "E38.26.57.0", {"position": v(88.9, -289.98) * mm});
            skPoint(sketch, "E38.26.58.0", {"position": v(88.9, -296.33) * mm});
            skPoint(sketch, "E38.26.59.0", {"position": v(88.9, -302.68) * mm});
            skPoint(sketch, "E38.26.60.0", {"position": v(88.9, -309.03) * mm});
            skPoint(sketch, "E38.26.61.0", {"position": v(88.9, -315.38) * mm});
            skPoint(sketch, "E38.26.62.0", {"position": v(88.9, -321.73) * mm});
            skPoint(sketch, "E38.26.63.0", {"position": v(88.9, -328.08) * mm});
            skPoint(sketch, "E38.26.64.0", {"position": v(88.9, -334.43) * mm});
            skPoint(sketch, "E38.26.65.0", {"position": v(88.9, -340.78) * mm});
            skPoint(sketch, "E38.26.66.0", {"position": v(88.9, -347.13) * mm});
            skPoint(sketch, "E38.26.67.0", {"position": v(88.9, -353.48) * mm});
            skPoint(sketch, "E38.26.68.0", {"position": v(88.9, -359.83) * mm});
            skPoint(sketch, "E38.26.69.0", {"position": v(88.9, -366.18) * mm});
            skPoint(sketch, "E38.26.70.0", {"position": v(88.9, -372.53) * mm});
            skPoint(sketch, "E38.26.71.0", {"position": v(88.9, -378.88) * mm});
            skPoint(sketch, "E38.26.72.0", {"position": v(88.9, -385.23) * mm});
            skPoint(sketch, "E38.26.73.0", {"position": v(88.9, -391.58) * mm});
            skPoint(sketch, "E38.26.74.0", {"position": v(88.9, -397.93) * mm});
            skPoint(sketch, "E38.26.75.0", {"position": v(88.9, -404.28) * mm});
            skPoint(sketch, "E38.26.76.0", {"position": v(88.9, -410.63) * mm});
            skPoint(sketch, "E38.26.77.0", {"position": v(88.9, -416.98) * mm});
            skPoint(sketch, "E38.26.78.0", {"position": v(88.9, -423.33) * mm});
            skPoint(sketch, "E38.26.79.0", {"position": v(88.9, -429.68) * mm});
            skPoint(sketch, "E38.26.80.0", {"position": v(88.9, -436.03) * mm});
            skPoint(sketch, "E38.26.81.0", {"position": v(88.9, -442.38) * mm});
            skPoint(sketch, "E38.26.82.0", {"position": v(88.9, -448.73) * mm});
            skPoint(sketch, "E38.26.83.0", {"position": v(88.9, -455.08) * mm});
            skPoint(sketch, "E38.26.84.0", {"position": v(88.9, -461.43) * mm});
            skPoint(sketch, "E38.26.85.0", {"position": v(88.9, -467.78) * mm});
            skPoint(sketch, "E38.26.86.0", {"position": v(88.9, -474.13) * mm});
            skPoint(sketch, "E38.26.87.0", {"position": v(88.9, -480.48) * mm});
            skPoint(sketch, "E38.26.88.0", {"position": v(88.9, -486.83) * mm});
            skPoint(sketch, "E38.26.89.0", {"position": v(88.9, -493.18) * mm});
            skPoint(sketch, "E38.26.90.0", {"position": v(88.9, -499.53) * mm});
            skPoint(sketch, "E38.26.91.0", {"position": v(88.9, -505.88) * mm});
            skPoint(sketch, "E38.26.92.0", {"position": v(88.9, -512.23) * mm});
            skPoint(sketch, "E38.26.93.0", {"position": v(88.9, -518.58) * mm});
            skPoint(sketch, "E38.26.94.0", {"position": v(88.9, -524.93) * mm});
            skPoint(sketch, "E38.26.95.0", {"position": v(88.9, -531.28) * mm});
            skPoint(sketch, "E38.26.96.0", {"position": v(88.9, -537.63) * mm});
            skPoint(sketch, "E38.26.97.0", {"position": v(88.9, -543.98) * mm});
            skPoint(sketch, "E38.26.98.0", {"position": v(88.9, -550.33) * mm});
            skPoint(sketch, "E38.26.99.0", {"position": v(88.9, -556.68) * mm});
            skPoint(sketch, "E38.27.0.0", {"position": v(95.25, 71.97) * mm});
            skPoint(sketch, "E38.27.1.0", {"position": v(95.25, 65.62) * mm});
            skPoint(sketch, "E38.27.2.0", {"position": v(95.25, 59.27) * mm});
            skPoint(sketch, "E38.27.3.0", {"position": v(95.25, 52.92) * mm});
            skPoint(sketch, "E38.27.4.0", {"position": v(95.25, 46.57) * mm});
            skPoint(sketch, "E38.27.5.0", {"position": v(95.25, 40.22) * mm});
            skPoint(sketch, "E38.27.6.0", {"position": v(95.25, 33.87) * mm});
            skPoint(sketch, "E38.27.7.0", {"position": v(95.25, 27.52) * mm});
            skPoint(sketch, "E38.27.8.0", {"position": v(95.25, 21.17) * mm});
            skPoint(sketch, "E38.27.9.0", {"position": v(95.25, 14.82) * mm});
            skPoint(sketch, "E38.27.10.0", {"position": v(95.25, 8.47) * mm});
            skPoint(sketch, "E38.27.11.0", {"position": v(95.25, 2.12) * mm});
            skPoint(sketch, "E38.27.12.0", {"position": v(95.25, -4.23) * mm});
            skPoint(sketch, "E38.27.13.0", {"position": v(95.25, -10.58) * mm});
            skPoint(sketch, "E38.27.14.0", {"position": v(95.25, -16.93) * mm});
            skPoint(sketch, "E38.27.15.0", {"position": v(95.25, -23.28) * mm});
            skPoint(sketch, "E38.27.16.0", {"position": v(95.25, -29.63) * mm});
            skPoint(sketch, "E38.27.17.0", {"position": v(95.25, -35.98) * mm});
            skPoint(sketch, "E38.27.18.0", {"position": v(95.25, -42.33) * mm});
            skPoint(sketch, "E38.27.19.0", {"position": v(95.25, -48.68) * mm});
            skPoint(sketch, "E38.27.20.0", {"position": v(95.25, -55.03) * mm});
            skPoint(sketch, "E38.27.21.0", {"position": v(95.25, -61.38) * mm});
            skPoint(sketch, "E38.27.22.0", {"position": v(95.25, -67.73) * mm});
            skPoint(sketch, "E38.27.23.0", {"position": v(95.25, -74.08) * mm});
            skPoint(sketch, "E38.27.24.0", {"position": v(95.25, -80.43) * mm});
            skPoint(sketch, "E38.27.25.0", {"position": v(95.25, -86.78) * mm});
            skPoint(sketch, "E38.27.26.0", {"position": v(95.25, -93.13) * mm});
            skPoint(sketch, "E38.27.27.0", {"position": v(95.25, -99.48) * mm});
            skPoint(sketch, "E38.27.28.0", {"position": v(95.25, -105.83) * mm});
            skPoint(sketch, "E38.27.29.0", {"position": v(95.25, -112.18) * mm});
            skPoint(sketch, "E38.27.30.0", {"position": v(95.25, -118.53) * mm});
            skPoint(sketch, "E38.27.31.0", {"position": v(95.25, -124.88) * mm});
            skPoint(sketch, "E38.27.32.0", {"position": v(95.25, -131.23) * mm});
            skPoint(sketch, "E38.27.33.0", {"position": v(95.25, -137.58) * mm});
            skPoint(sketch, "E38.27.34.0", {"position": v(95.25, -143.93) * mm});
            skPoint(sketch, "E38.27.35.0", {"position": v(95.25, -150.28) * mm});
            skPoint(sketch, "E38.27.36.0", {"position": v(95.25, -156.63) * mm});
            skPoint(sketch, "E38.27.37.0", {"position": v(95.25, -162.98) * mm});
            skPoint(sketch, "E38.27.38.0", {"position": v(95.25, -169.33) * mm});
            skPoint(sketch, "E38.27.39.0", {"position": v(95.25, -175.68) * mm});
            skPoint(sketch, "E38.27.40.0", {"position": v(95.25, -182.03) * mm});
            skPoint(sketch, "E38.27.41.0", {"position": v(95.25, -188.38) * mm});
            skPoint(sketch, "E38.27.42.0", {"position": v(95.25, -194.73) * mm});
            skPoint(sketch, "E38.27.43.0", {"position": v(95.25, -201.08) * mm});
            skPoint(sketch, "E38.27.44.0", {"position": v(95.25, -207.43) * mm});
            skPoint(sketch, "E38.27.45.0", {"position": v(95.25, -213.78) * mm});
            skPoint(sketch, "E38.27.46.0", {"position": v(95.25, -220.13) * mm});
            skPoint(sketch, "E38.27.47.0", {"position": v(95.25, -226.48) * mm});
            skPoint(sketch, "E38.27.48.0", {"position": v(95.25, -232.83) * mm});
            skPoint(sketch, "E38.27.49.0", {"position": v(95.25, -239.18) * mm});
            skPoint(sketch, "E38.27.50.0", {"position": v(95.25, -245.53) * mm});
            skPoint(sketch, "E38.27.51.0", {"position": v(95.25, -251.88) * mm});
            skPoint(sketch, "E38.27.52.0", {"position": v(95.25, -258.23) * mm});
            skPoint(sketch, "E38.27.53.0", {"position": v(95.25, -264.58) * mm});
            skPoint(sketch, "E38.27.54.0", {"position": v(95.25, -270.93) * mm});
            skPoint(sketch, "E38.27.55.0", {"position": v(95.25, -277.28) * mm});
            skPoint(sketch, "E38.27.56.0", {"position": v(95.25, -283.63) * mm});
            skPoint(sketch, "E38.27.57.0", {"position": v(95.25, -289.98) * mm});
            skPoint(sketch, "E38.27.58.0", {"position": v(95.25, -296.33) * mm});
            skPoint(sketch, "E38.27.59.0", {"position": v(95.25, -302.68) * mm});
            skPoint(sketch, "E38.27.60.0", {"position": v(95.25, -309.03) * mm});
            skPoint(sketch, "E38.27.61.0", {"position": v(95.25, -315.38) * mm});
            skPoint(sketch, "E38.27.62.0", {"position": v(95.25, -321.73) * mm});
            skPoint(sketch, "E38.27.63.0", {"position": v(95.25, -328.08) * mm});
            skPoint(sketch, "E38.27.64.0", {"position": v(95.25, -334.43) * mm});
            skPoint(sketch, "E38.27.65.0", {"position": v(95.25, -340.78) * mm});
            skPoint(sketch, "E38.27.66.0", {"position": v(95.25, -347.13) * mm});
            skPoint(sketch, "E38.27.67.0", {"position": v(95.25, -353.48) * mm});
            skPoint(sketch, "E38.27.68.0", {"position": v(95.25, -359.83) * mm});
            skPoint(sketch, "E38.27.69.0", {"position": v(95.25, -366.18) * mm});
            skPoint(sketch, "E38.27.70.0", {"position": v(95.25, -372.53) * mm});
            skPoint(sketch, "E38.27.71.0", {"position": v(95.25, -378.88) * mm});
            skPoint(sketch, "E38.27.72.0", {"position": v(95.25, -385.23) * mm});
            skPoint(sketch, "E38.27.73.0", {"position": v(95.25, -391.58) * mm});
            skPoint(sketch, "E38.27.74.0", {"position": v(95.25, -397.93) * mm});
            skPoint(sketch, "E38.27.75.0", {"position": v(95.25, -404.28) * mm});
            skPoint(sketch, "E38.27.76.0", {"position": v(95.25, -410.63) * mm});
            skPoint(sketch, "E38.27.77.0", {"position": v(95.25, -416.98) * mm});
            skPoint(sketch, "E38.27.78.0", {"position": v(95.25, -423.33) * mm});
            skPoint(sketch, "E38.27.79.0", {"position": v(95.25, -429.68) * mm});
            skPoint(sketch, "E38.27.80.0", {"position": v(95.25, -436.03) * mm});
            skPoint(sketch, "E38.27.81.0", {"position": v(95.25, -442.38) * mm});
            skPoint(sketch, "E38.27.82.0", {"position": v(95.25, -448.73) * mm});
            skPoint(sketch, "E38.27.83.0", {"position": v(95.25, -455.08) * mm});
            skPoint(sketch, "E38.27.84.0", {"position": v(95.25, -461.43) * mm});
            skPoint(sketch, "E38.27.85.0", {"position": v(95.25, -467.78) * mm});
            skPoint(sketch, "E38.27.86.0", {"position": v(95.25, -474.13) * mm});
            skPoint(sketch, "E38.27.87.0", {"position": v(95.25, -480.48) * mm});
            skPoint(sketch, "E38.27.88.0", {"position": v(95.25, -486.83) * mm});
            skPoint(sketch, "E38.27.89.0", {"position": v(95.25, -493.18) * mm});
            skPoint(sketch, "E38.27.90.0", {"position": v(95.25, -499.53) * mm});
            skPoint(sketch, "E38.27.91.0", {"position": v(95.25, -505.88) * mm});
            skPoint(sketch, "E38.27.92.0", {"position": v(95.25, -512.23) * mm});
            skPoint(sketch, "E38.27.93.0", {"position": v(95.25, -518.58) * mm});
            skPoint(sketch, "E38.27.94.0", {"position": v(95.25, -524.93) * mm});
            skPoint(sketch, "E38.27.95.0", {"position": v(95.25, -531.28) * mm});
            skPoint(sketch, "E38.27.96.0", {"position": v(95.25, -537.63) * mm});
            skPoint(sketch, "E38.27.97.0", {"position": v(95.25, -543.98) * mm});
            skPoint(sketch, "E38.27.98.0", {"position": v(95.25, -550.33) * mm});
            skPoint(sketch, "E38.27.99.0", {"position": v(95.25, -556.68) * mm});
            skPoint(sketch, "E38.28.0.0", {"position": v(101.6, 71.97) * mm});
            skPoint(sketch, "E38.28.1.0", {"position": v(101.6, 65.62) * mm});
            skPoint(sketch, "E38.28.2.0", {"position": v(101.6, 59.27) * mm});
            skPoint(sketch, "E38.28.3.0", {"position": v(101.6, 52.92) * mm});
            skPoint(sketch, "E38.28.4.0", {"position": v(101.6, 46.57) * mm});
            skPoint(sketch, "E38.28.5.0", {"position": v(101.6, 40.22) * mm});
            skPoint(sketch, "E38.28.6.0", {"position": v(101.6, 33.87) * mm});
            skPoint(sketch, "E38.28.7.0", {"position": v(101.6, 27.52) * mm});
            skPoint(sketch, "E38.28.8.0", {"position": v(101.6, 21.17) * mm});
            skPoint(sketch, "E38.28.9.0", {"position": v(101.6, 14.82) * mm});
            skPoint(sketch, "E38.28.10.0", {"position": v(101.6, 8.47) * mm});
            skPoint(sketch, "E38.28.11.0", {"position": v(101.6, 2.12) * mm});
            skPoint(sketch, "E38.28.12.0", {"position": v(101.6, -4.23) * mm});
            skPoint(sketch, "E38.28.13.0", {"position": v(101.6, -10.58) * mm});
            skPoint(sketch, "E38.28.14.0", {"position": v(101.6, -16.93) * mm});
            skPoint(sketch, "E38.28.15.0", {"position": v(101.6, -23.28) * mm});
            skPoint(sketch, "E38.28.16.0", {"position": v(101.6, -29.63) * mm});
            skPoint(sketch, "E38.28.17.0", {"position": v(101.6, -35.98) * mm});
            skPoint(sketch, "E38.28.18.0", {"position": v(101.6, -42.33) * mm});
            skPoint(sketch, "E38.28.19.0", {"position": v(101.6, -48.68) * mm});
            skPoint(sketch, "E38.28.20.0", {"position": v(101.6, -55.03) * mm});
            skPoint(sketch, "E38.28.21.0", {"position": v(101.6, -61.38) * mm});
            skPoint(sketch, "E38.28.22.0", {"position": v(101.6, -67.73) * mm});
            skPoint(sketch, "E38.28.23.0", {"position": v(101.6, -74.08) * mm});
            skPoint(sketch, "E38.28.24.0", {"position": v(101.6, -80.43) * mm});
            skPoint(sketch, "E38.28.25.0", {"position": v(101.6, -86.78) * mm});
            skPoint(sketch, "E38.28.26.0", {"position": v(101.6, -93.13) * mm});
            skPoint(sketch, "E38.28.27.0", {"position": v(101.6, -99.48) * mm});
            skPoint(sketch, "E38.28.28.0", {"position": v(101.6, -105.83) * mm});
            skPoint(sketch, "E38.28.29.0", {"position": v(101.6, -112.18) * mm});
            skPoint(sketch, "E38.28.30.0", {"position": v(101.6, -118.53) * mm});
            skPoint(sketch, "E38.28.31.0", {"position": v(101.6, -124.88) * mm});
            skPoint(sketch, "E38.28.32.0", {"position": v(101.6, -131.23) * mm});
            skPoint(sketch, "E38.28.33.0", {"position": v(101.6, -137.58) * mm});
            skPoint(sketch, "E38.28.34.0", {"position": v(101.6, -143.93) * mm});
            skPoint(sketch, "E38.28.35.0", {"position": v(101.6, -150.28) * mm});
            skPoint(sketch, "E38.28.36.0", {"position": v(101.6, -156.63) * mm});
            skPoint(sketch, "E38.28.37.0", {"position": v(101.6, -162.98) * mm});
            skPoint(sketch, "E38.28.38.0", {"position": v(101.6, -169.33) * mm});
            skPoint(sketch, "E38.28.39.0", {"position": v(101.6, -175.68) * mm});
            skPoint(sketch, "E38.28.40.0", {"position": v(101.6, -182.03) * mm});
            skPoint(sketch, "E38.28.41.0", {"position": v(101.6, -188.38) * mm});
            skPoint(sketch, "E38.28.42.0", {"position": v(101.6, -194.73) * mm});
            skPoint(sketch, "E38.28.43.0", {"position": v(101.6, -201.08) * mm});
            skPoint(sketch, "E38.28.44.0", {"position": v(101.6, -207.43) * mm});
            skPoint(sketch, "E38.28.45.0", {"position": v(101.6, -213.78) * mm});
            skPoint(sketch, "E38.28.46.0", {"position": v(101.6, -220.13) * mm});
            skPoint(sketch, "E38.28.47.0", {"position": v(101.6, -226.48) * mm});
            skPoint(sketch, "E38.28.48.0", {"position": v(101.6, -232.83) * mm});
            skPoint(sketch, "E38.28.49.0", {"position": v(101.6, -239.18) * mm});
            skPoint(sketch, "E38.28.50.0", {"position": v(101.6, -245.53) * mm});
            skPoint(sketch, "E38.28.51.0", {"position": v(101.6, -251.88) * mm});
            skPoint(sketch, "E38.28.52.0", {"position": v(101.6, -258.23) * mm});
            skPoint(sketch, "E38.28.53.0", {"position": v(101.6, -264.58) * mm});
            skPoint(sketch, "E38.28.54.0", {"position": v(101.6, -270.93) * mm});
            skPoint(sketch, "E38.28.55.0", {"position": v(101.6, -277.28) * mm});
            skPoint(sketch, "E38.28.56.0", {"position": v(101.6, -283.63) * mm});
            skPoint(sketch, "E38.28.57.0", {"position": v(101.6, -289.98) * mm});
            skPoint(sketch, "E38.28.58.0", {"position": v(101.6, -296.33) * mm});
            skPoint(sketch, "E38.28.59.0", {"position": v(101.6, -302.68) * mm});
            skPoint(sketch, "E38.28.60.0", {"position": v(101.6, -309.03) * mm});
            skPoint(sketch, "E38.28.61.0", {"position": v(101.6, -315.38) * mm});
            skPoint(sketch, "E38.28.62.0", {"position": v(101.6, -321.73) * mm});
            skPoint(sketch, "E38.28.63.0", {"position": v(101.6, -328.08) * mm});
            skPoint(sketch, "E38.28.64.0", {"position": v(101.6, -334.43) * mm});
            skPoint(sketch, "E38.28.65.0", {"position": v(101.6, -340.78) * mm});
            skPoint(sketch, "E38.28.66.0", {"position": v(101.6, -347.13) * mm});
            skPoint(sketch, "E38.28.67.0", {"position": v(101.6, -353.48) * mm});
            skPoint(sketch, "E38.28.68.0", {"position": v(101.6, -359.83) * mm});
            skPoint(sketch, "E38.28.69.0", {"position": v(101.6, -366.18) * mm});
            skPoint(sketch, "E38.28.70.0", {"position": v(101.6, -372.53) * mm});
            skPoint(sketch, "E38.28.71.0", {"position": v(101.6, -378.88) * mm});
            skPoint(sketch, "E38.28.72.0", {"position": v(101.6, -385.23) * mm});
            skPoint(sketch, "E38.28.73.0", {"position": v(101.6, -391.58) * mm});
            skPoint(sketch, "E38.28.74.0", {"position": v(101.6, -397.93) * mm});
            skPoint(sketch, "E38.28.75.0", {"position": v(101.6, -404.28) * mm});
            skPoint(sketch, "E38.28.76.0", {"position": v(101.6, -410.63) * mm});
            skPoint(sketch, "E38.28.77.0", {"position": v(101.6, -416.98) * mm});
            skPoint(sketch, "E38.28.78.0", {"position": v(101.6, -423.33) * mm});
            skPoint(sketch, "E38.28.79.0", {"position": v(101.6, -429.68) * mm});
            skPoint(sketch, "E38.28.80.0", {"position": v(101.6, -436.03) * mm});
            skPoint(sketch, "E38.28.81.0", {"position": v(101.6, -442.38) * mm});
            skPoint(sketch, "E38.28.82.0", {"position": v(101.6, -448.73) * mm});
            skPoint(sketch, "E38.28.83.0", {"position": v(101.6, -455.08) * mm});
            skPoint(sketch, "E38.28.84.0", {"position": v(101.6, -461.43) * mm});
            skPoint(sketch, "E38.28.85.0", {"position": v(101.6, -467.78) * mm});
            skPoint(sketch, "E38.28.86.0", {"position": v(101.6, -474.13) * mm});
            skPoint(sketch, "E38.28.87.0", {"position": v(101.6, -480.48) * mm});
            skPoint(sketch, "E38.28.88.0", {"position": v(101.6, -486.83) * mm});
            skPoint(sketch, "E38.28.89.0", {"position": v(101.6, -493.18) * mm});
            skPoint(sketch, "E38.28.90.0", {"position": v(101.6, -499.53) * mm});
            skPoint(sketch, "E38.28.91.0", {"position": v(101.6, -505.88) * mm});
            skPoint(sketch, "E38.28.92.0", {"position": v(101.6, -512.23) * mm});
            skPoint(sketch, "E38.28.93.0", {"position": v(101.6, -518.58) * mm});
            skPoint(sketch, "E38.28.94.0", {"position": v(101.6, -524.93) * mm});
            skPoint(sketch, "E38.28.95.0", {"position": v(101.6, -531.28) * mm});
            skPoint(sketch, "E38.28.96.0", {"position": v(101.6, -537.63) * mm});
            skPoint(sketch, "E38.28.97.0", {"position": v(101.6, -543.98) * mm});
            skPoint(sketch, "E38.28.98.0", {"position": v(101.6, -550.33) * mm});
            skPoint(sketch, "E38.28.99.0", {"position": v(101.6, -556.68) * mm});
            skPoint(sketch, "E38.29.0.0", {"position": v(107.95, 71.97) * mm});
            skPoint(sketch, "E38.29.1.0", {"position": v(107.95, 65.62) * mm});
            skPoint(sketch, "E38.29.2.0", {"position": v(107.95, 59.27) * mm});
            skPoint(sketch, "E38.29.3.0", {"position": v(107.95, 52.92) * mm});
            skPoint(sketch, "E38.29.4.0", {"position": v(107.95, 46.57) * mm});
            skPoint(sketch, "E38.29.5.0", {"position": v(107.95, 40.22) * mm});
            skPoint(sketch, "E38.29.6.0", {"position": v(107.95, 33.87) * mm});
            skPoint(sketch, "E38.29.7.0", {"position": v(107.95, 27.52) * mm});
            skPoint(sketch, "E38.29.8.0", {"position": v(107.95, 21.17) * mm});
            skPoint(sketch, "E38.29.9.0", {"position": v(107.95, 14.82) * mm});
            skPoint(sketch, "E38.29.10.0", {"position": v(107.95, 8.47) * mm});
            skPoint(sketch, "E38.29.11.0", {"position": v(107.95, 2.12) * mm});
            skPoint(sketch, "E38.29.12.0", {"position": v(107.95, -4.23) * mm});
            skPoint(sketch, "E38.29.13.0", {"position": v(107.95, -10.58) * mm});
            skPoint(sketch, "E38.29.14.0", {"position": v(107.95, -16.93) * mm});
            skPoint(sketch, "E38.29.15.0", {"position": v(107.95, -23.28) * mm});
            skPoint(sketch, "E38.29.16.0", {"position": v(107.95, -29.63) * mm});
            skPoint(sketch, "E38.29.17.0", {"position": v(107.95, -35.98) * mm});
            skPoint(sketch, "E38.29.18.0", {"position": v(107.95, -42.33) * mm});
            skPoint(sketch, "E38.29.19.0", {"position": v(107.95, -48.68) * mm});
            skPoint(sketch, "E38.29.20.0", {"position": v(107.95, -55.03) * mm});
            skPoint(sketch, "E38.29.21.0", {"position": v(107.95, -61.38) * mm});
            skPoint(sketch, "E38.29.22.0", {"position": v(107.95, -67.73) * mm});
            skPoint(sketch, "E38.29.23.0", {"position": v(107.95, -74.08) * mm});
            skPoint(sketch, "E38.29.24.0", {"position": v(107.95, -80.43) * mm});
            skPoint(sketch, "E38.29.25.0", {"position": v(107.95, -86.78) * mm});
            skPoint(sketch, "E38.29.26.0", {"position": v(107.95, -93.13) * mm});
            skPoint(sketch, "E38.29.27.0", {"position": v(107.95, -99.48) * mm});
            skPoint(sketch, "E38.29.28.0", {"position": v(107.95, -105.83) * mm});
            skPoint(sketch, "E38.29.29.0", {"position": v(107.95, -112.18) * mm});
            skPoint(sketch, "E38.29.30.0", {"position": v(107.95, -118.53) * mm});
            skPoint(sketch, "E38.29.31.0", {"position": v(107.95, -124.88) * mm});
            skPoint(sketch, "E38.29.32.0", {"position": v(107.95, -131.23) * mm});
            skPoint(sketch, "E38.29.33.0", {"position": v(107.95, -137.58) * mm});
            skPoint(sketch, "E38.29.34.0", {"position": v(107.95, -143.93) * mm});
            skPoint(sketch, "E38.29.35.0", {"position": v(107.95, -150.28) * mm});
            skPoint(sketch, "E38.29.36.0", {"position": v(107.95, -156.63) * mm});
            skPoint(sketch, "E38.29.37.0", {"position": v(107.95, -162.98) * mm});
            skPoint(sketch, "E38.29.38.0", {"position": v(107.95, -169.33) * mm});
            skPoint(sketch, "E38.29.39.0", {"position": v(107.95, -175.68) * mm});
            skPoint(sketch, "E38.29.40.0", {"position": v(107.95, -182.03) * mm});
            skPoint(sketch, "E38.29.41.0", {"position": v(107.95, -188.38) * mm});
            skPoint(sketch, "E38.29.42.0", {"position": v(107.95, -194.73) * mm});
            skPoint(sketch, "E38.29.43.0", {"position": v(107.95, -201.08) * mm});
            skPoint(sketch, "E38.29.44.0", {"position": v(107.95, -207.43) * mm});
            skPoint(sketch, "E38.29.45.0", {"position": v(107.95, -213.78) * mm});
            skPoint(sketch, "E38.29.46.0", {"position": v(107.95, -220.13) * mm});
            skPoint(sketch, "E38.29.47.0", {"position": v(107.95, -226.48) * mm});
            skPoint(sketch, "E38.29.48.0", {"position": v(107.95, -232.83) * mm});
            skPoint(sketch, "E38.29.49.0", {"position": v(107.95, -239.18) * mm});
            skPoint(sketch, "E38.29.50.0", {"position": v(107.95, -245.53) * mm});
            skPoint(sketch, "E38.29.51.0", {"position": v(107.95, -251.88) * mm});
            skPoint(sketch, "E38.29.52.0", {"position": v(107.95, -258.23) * mm});
            skPoint(sketch, "E38.29.53.0", {"position": v(107.95, -264.58) * mm});
            skPoint(sketch, "E38.29.54.0", {"position": v(107.95, -270.93) * mm});
            skPoint(sketch, "E38.29.55.0", {"position": v(107.95, -277.28) * mm});
            skPoint(sketch, "E38.29.56.0", {"position": v(107.95, -283.63) * mm});
            skPoint(sketch, "E38.29.57.0", {"position": v(107.95, -289.98) * mm});
            skPoint(sketch, "E38.29.58.0", {"position": v(107.95, -296.33) * mm});
            skPoint(sketch, "E38.29.59.0", {"position": v(107.95, -302.68) * mm});
            skPoint(sketch, "E38.29.60.0", {"position": v(107.95, -309.03) * mm});
            skPoint(sketch, "E38.29.61.0", {"position": v(107.95, -315.38) * mm});
            skPoint(sketch, "E38.29.62.0", {"position": v(107.95, -321.73) * mm});
            skPoint(sketch, "E38.29.63.0", {"position": v(107.95, -328.08) * mm});
            skPoint(sketch, "E38.29.64.0", {"position": v(107.95, -334.43) * mm});
            skPoint(sketch, "E38.29.65.0", {"position": v(107.95, -340.78) * mm});
            skPoint(sketch, "E38.29.66.0", {"position": v(107.95, -347.13) * mm});
            skPoint(sketch, "E38.29.67.0", {"position": v(107.95, -353.48) * mm});
            skPoint(sketch, "E38.29.68.0", {"position": v(107.95, -359.83) * mm});
            skPoint(sketch, "E38.29.69.0", {"position": v(107.95, -366.18) * mm});
            skPoint(sketch, "E38.29.70.0", {"position": v(107.95, -372.53) * mm});
            skPoint(sketch, "E38.29.71.0", {"position": v(107.95, -378.88) * mm});
            skPoint(sketch, "E38.29.72.0", {"position": v(107.95, -385.23) * mm});
            skPoint(sketch, "E38.29.73.0", {"position": v(107.95, -391.58) * mm});
            skPoint(sketch, "E38.29.74.0", {"position": v(107.95, -397.93) * mm});
            skPoint(sketch, "E38.29.75.0", {"position": v(107.95, -404.28) * mm});
            skPoint(sketch, "E38.29.76.0", {"position": v(107.95, -410.63) * mm});
            skPoint(sketch, "E38.29.77.0", {"position": v(107.95, -416.98) * mm});
            skPoint(sketch, "E38.29.78.0", {"position": v(107.95, -423.33) * mm});
            skPoint(sketch, "E38.29.79.0", {"position": v(107.95, -429.68) * mm});
            skPoint(sketch, "E38.29.80.0", {"position": v(107.95, -436.03) * mm});
            skPoint(sketch, "E38.29.81.0", {"position": v(107.95, -442.38) * mm});
            skPoint(sketch, "E38.29.82.0", {"position": v(107.95, -448.73) * mm});
            skPoint(sketch, "E38.29.83.0", {"position": v(107.95, -455.08) * mm});
            skPoint(sketch, "E38.29.84.0", {"position": v(107.95, -461.43) * mm});
            skPoint(sketch, "E38.29.85.0", {"position": v(107.95, -467.78) * mm});
            skPoint(sketch, "E38.29.86.0", {"position": v(107.95, -474.13) * mm});
            skPoint(sketch, "E38.29.87.0", {"position": v(107.95, -480.48) * mm});
            skPoint(sketch, "E38.29.88.0", {"position": v(107.95, -486.83) * mm});
            skPoint(sketch, "E38.29.89.0", {"position": v(107.95, -493.18) * mm});
            skPoint(sketch, "E38.29.90.0", {"position": v(107.95, -499.53) * mm});
            skPoint(sketch, "E38.29.91.0", {"position": v(107.95, -505.88) * mm});
            skPoint(sketch, "E38.29.92.0", {"position": v(107.95, -512.23) * mm});
            skPoint(sketch, "E38.29.93.0", {"position": v(107.95, -518.58) * mm});
            skPoint(sketch, "E38.29.94.0", {"position": v(107.95, -524.93) * mm});
            skPoint(sketch, "E38.29.95.0", {"position": v(107.95, -531.28) * mm});
            skPoint(sketch, "E38.29.96.0", {"position": v(107.95, -537.63) * mm});
            skPoint(sketch, "E38.29.97.0", {"position": v(107.95, -543.98) * mm});
            skPoint(sketch, "E38.29.98.0", {"position": v(107.95, -550.33) * mm});
            skPoint(sketch, "E38.29.99.0", {"position": v(107.95, -556.68) * mm});
            skPoint(sketch, "E38.30.0.0", {"position": v(114.3, 71.97) * mm});
            skPoint(sketch, "E38.30.1.0", {"position": v(114.3, 65.62) * mm});
            skPoint(sketch, "E38.30.2.0", {"position": v(114.3, 59.27) * mm});
            skPoint(sketch, "E38.30.3.0", {"position": v(114.3, 52.92) * mm});
            skPoint(sketch, "E38.30.4.0", {"position": v(114.3, 46.57) * mm});
            skPoint(sketch, "E38.30.5.0", {"position": v(114.3, 40.22) * mm});
            skPoint(sketch, "E38.30.6.0", {"position": v(114.3, 33.87) * mm});
            skPoint(sketch, "E38.30.7.0", {"position": v(114.3, 27.52) * mm});
            skPoint(sketch, "E38.30.8.0", {"position": v(114.3, 21.17) * mm});
            skPoint(sketch, "E38.30.9.0", {"position": v(114.3, 14.82) * mm});
            skPoint(sketch, "E38.30.10.0", {"position": v(114.3, 8.47) * mm});
            skPoint(sketch, "E38.30.11.0", {"position": v(114.3, 2.12) * mm});
            skPoint(sketch, "E38.30.12.0", {"position": v(114.3, -4.23) * mm});
            skPoint(sketch, "E38.30.13.0", {"position": v(114.3, -10.58) * mm});
            skPoint(sketch, "E38.30.14.0", {"position": v(114.3, -16.93) * mm});
            skPoint(sketch, "E38.30.15.0", {"position": v(114.3, -23.28) * mm});
            skPoint(sketch, "E38.30.16.0", {"position": v(114.3, -29.63) * mm});
            skPoint(sketch, "E38.30.17.0", {"position": v(114.3, -35.98) * mm});
            skPoint(sketch, "E38.30.18.0", {"position": v(114.3, -42.33) * mm});
            skPoint(sketch, "E38.30.19.0", {"position": v(114.3, -48.68) * mm});
            skPoint(sketch, "E38.30.20.0", {"position": v(114.3, -55.03) * mm});
            skPoint(sketch, "E38.30.21.0", {"position": v(114.3, -61.38) * mm});
            skPoint(sketch, "E38.30.22.0", {"position": v(114.3, -67.73) * mm});
            skPoint(sketch, "E38.30.23.0", {"position": v(114.3, -74.08) * mm});
            skPoint(sketch, "E38.30.24.0", {"position": v(114.3, -80.43) * mm});
            skPoint(sketch, "E38.30.25.0", {"position": v(114.3, -86.78) * mm});
            skPoint(sketch, "E38.30.26.0", {"position": v(114.3, -93.13) * mm});
            skPoint(sketch, "E38.30.27.0", {"position": v(114.3, -99.48) * mm});
            skPoint(sketch, "E38.30.28.0", {"position": v(114.3, -105.83) * mm});
            skPoint(sketch, "E38.30.29.0", {"position": v(114.3, -112.18) * mm});
            skPoint(sketch, "E38.30.30.0", {"position": v(114.3, -118.53) * mm});
            skPoint(sketch, "E38.30.31.0", {"position": v(114.3, -124.88) * mm});
            skPoint(sketch, "E38.30.32.0", {"position": v(114.3, -131.23) * mm});
            skPoint(sketch, "E38.30.33.0", {"position": v(114.3, -137.58) * mm});
            skPoint(sketch, "E38.30.34.0", {"position": v(114.3, -143.93) * mm});
            skPoint(sketch, "E38.30.35.0", {"position": v(114.3, -150.28) * mm});
            skPoint(sketch, "E38.30.36.0", {"position": v(114.3, -156.63) * mm});
            skPoint(sketch, "E38.30.37.0", {"position": v(114.3, -162.98) * mm});
            skPoint(sketch, "E38.30.38.0", {"position": v(114.3, -169.33) * mm});
            skPoint(sketch, "E38.30.39.0", {"position": v(114.3, -175.68) * mm});
            skPoint(sketch, "E38.30.40.0", {"position": v(114.3, -182.03) * mm});
            skPoint(sketch, "E38.30.41.0", {"position": v(114.3, -188.38) * mm});
            skPoint(sketch, "E38.30.42.0", {"position": v(114.3, -194.73) * mm});
            skPoint(sketch, "E38.30.43.0", {"position": v(114.3, -201.08) * mm});
            skPoint(sketch, "E38.30.44.0", {"position": v(114.3, -207.43) * mm});
            skPoint(sketch, "E38.30.45.0", {"position": v(114.3, -213.78) * mm});
            skPoint(sketch, "E38.30.46.0", {"position": v(114.3, -220.13) * mm});
            skPoint(sketch, "E38.30.47.0", {"position": v(114.3, -226.48) * mm});
            skPoint(sketch, "E38.30.48.0", {"position": v(114.3, -232.83) * mm});
            skPoint(sketch, "E38.30.49.0", {"position": v(114.3, -239.18) * mm});
            skPoint(sketch, "E38.30.50.0", {"position": v(114.3, -245.53) * mm});
            skPoint(sketch, "E38.30.51.0", {"position": v(114.3, -251.88) * mm});
            skPoint(sketch, "E38.30.52.0", {"position": v(114.3, -258.23) * mm});
            skPoint(sketch, "E38.30.53.0", {"position": v(114.3, -264.58) * mm});
            skPoint(sketch, "E38.30.54.0", {"position": v(114.3, -270.93) * mm});
            skPoint(sketch, "E38.30.55.0", {"position": v(114.3, -277.28) * mm});
            skPoint(sketch, "E38.30.56.0", {"position": v(114.3, -283.63) * mm});
            skPoint(sketch, "E38.30.57.0", {"position": v(114.3, -289.98) * mm});
            skPoint(sketch, "E38.30.58.0", {"position": v(114.3, -296.33) * mm});
            skPoint(sketch, "E38.30.59.0", {"position": v(114.3, -302.68) * mm});
            skPoint(sketch, "E38.30.60.0", {"position": v(114.3, -309.03) * mm});
            skPoint(sketch, "E38.30.61.0", {"position": v(114.3, -315.38) * mm});
            skPoint(sketch, "E38.30.62.0", {"position": v(114.3, -321.73) * mm});
            skPoint(sketch, "E38.30.63.0", {"position": v(114.3, -328.08) * mm});
            skPoint(sketch, "E38.30.64.0", {"position": v(114.3, -334.43) * mm});
            skPoint(sketch, "E38.30.65.0", {"position": v(114.3, -340.78) * mm});
            skPoint(sketch, "E38.30.66.0", {"position": v(114.3, -347.13) * mm});
            skPoint(sketch, "E38.30.67.0", {"position": v(114.3, -353.48) * mm});
            skPoint(sketch, "E38.30.68.0", {"position": v(114.3, -359.83) * mm});
            skPoint(sketch, "E38.30.69.0", {"position": v(114.3, -366.18) * mm});
            skPoint(sketch, "E38.30.70.0", {"position": v(114.3, -372.53) * mm});
            skPoint(sketch, "E38.30.71.0", {"position": v(114.3, -378.88) * mm});
            skPoint(sketch, "E38.30.72.0", {"position": v(114.3, -385.23) * mm});
            skPoint(sketch, "E38.30.73.0", {"position": v(114.3, -391.58) * mm});
            skPoint(sketch, "E38.30.74.0", {"position": v(114.3, -397.93) * mm});
            skPoint(sketch, "E38.30.75.0", {"position": v(114.3, -404.28) * mm});
            skPoint(sketch, "E38.30.76.0", {"position": v(114.3, -410.63) * mm});
            skPoint(sketch, "E38.30.77.0", {"position": v(114.3, -416.98) * mm});
            skPoint(sketch, "E38.30.78.0", {"position": v(114.3, -423.33) * mm});
            skPoint(sketch, "E38.30.79.0", {"position": v(114.3, -429.68) * mm});
            skPoint(sketch, "E38.30.80.0", {"position": v(114.3, -436.03) * mm});
            skPoint(sketch, "E38.30.81.0", {"position": v(114.3, -442.38) * mm});
            skPoint(sketch, "E38.30.82.0", {"position": v(114.3, -448.73) * mm});
            skPoint(sketch, "E38.30.83.0", {"position": v(114.3, -455.08) * mm});
            skPoint(sketch, "E38.30.84.0", {"position": v(114.3, -461.43) * mm});
            skPoint(sketch, "E38.30.85.0", {"position": v(114.3, -467.78) * mm});
            skPoint(sketch, "E38.30.86.0", {"position": v(114.3, -474.13) * mm});
            skPoint(sketch, "E38.30.87.0", {"position": v(114.3, -480.48) * mm});
            skPoint(sketch, "E38.30.88.0", {"position": v(114.3, -486.83) * mm});
            skPoint(sketch, "E38.30.89.0", {"position": v(114.3, -493.18) * mm});
            skPoint(sketch, "E38.30.90.0", {"position": v(114.3, -499.53) * mm});
            skPoint(sketch, "E38.30.91.0", {"position": v(114.3, -505.88) * mm});
            skPoint(sketch, "E38.30.92.0", {"position": v(114.3, -512.23) * mm});
            skPoint(sketch, "E38.30.93.0", {"position": v(114.3, -518.58) * mm});
            skPoint(sketch, "E38.30.94.0", {"position": v(114.3, -524.93) * mm});
            skPoint(sketch, "E38.30.95.0", {"position": v(114.3, -531.28) * mm});
            skPoint(sketch, "E38.30.96.0", {"position": v(114.3, -537.63) * mm});
            skPoint(sketch, "E38.30.97.0", {"position": v(114.3, -543.98) * mm});
            skPoint(sketch, "E38.30.98.0", {"position": v(114.3, -550.33) * mm});
            skPoint(sketch, "E38.30.99.0", {"position": v(114.3, -556.68) * mm});
            skPoint(sketch, "E38.31.0.0", {"position": v(120.65, 71.97) * mm});
            skPoint(sketch, "E38.31.1.0", {"position": v(120.65, 65.62) * mm});
            skPoint(sketch, "E38.31.2.0", {"position": v(120.65, 59.27) * mm});
            skPoint(sketch, "E38.31.3.0", {"position": v(120.65, 52.92) * mm});
            skPoint(sketch, "E38.31.4.0", {"position": v(120.65, 46.57) * mm});
            skPoint(sketch, "E38.31.5.0", {"position": v(120.65, 40.22) * mm});
            skPoint(sketch, "E38.31.6.0", {"position": v(120.65, 33.87) * mm});
            skPoint(sketch, "E38.31.7.0", {"position": v(120.65, 27.52) * mm});
            skPoint(sketch, "E38.31.8.0", {"position": v(120.65, 21.17) * mm});
            skPoint(sketch, "E38.31.9.0", {"position": v(120.65, 14.82) * mm});
            skPoint(sketch, "E38.31.10.0", {"position": v(120.65, 8.47) * mm});
            skPoint(sketch, "E38.31.11.0", {"position": v(120.65, 2.12) * mm});
            skPoint(sketch, "E38.31.12.0", {"position": v(120.65, -4.23) * mm});
            skPoint(sketch, "E38.31.13.0", {"position": v(120.65, -10.58) * mm});
            skPoint(sketch, "E38.31.14.0", {"position": v(120.65, -16.93) * mm});
            skPoint(sketch, "E38.31.15.0", {"position": v(120.65, -23.28) * mm});
            skPoint(sketch, "E38.31.16.0", {"position": v(120.65, -29.63) * mm});
            skPoint(sketch, "E38.31.17.0", {"position": v(120.65, -35.98) * mm});
            skPoint(sketch, "E38.31.18.0", {"position": v(120.65, -42.33) * mm});
            skPoint(sketch, "E38.31.19.0", {"position": v(120.65, -48.68) * mm});
            skPoint(sketch, "E38.31.20.0", {"position": v(120.65, -55.03) * mm});
            skPoint(sketch, "E38.31.21.0", {"position": v(120.65, -61.38) * mm});
            skPoint(sketch, "E38.31.22.0", {"position": v(120.65, -67.73) * mm});
            skPoint(sketch, "E38.31.23.0", {"position": v(120.65, -74.08) * mm});
            skPoint(sketch, "E38.31.24.0", {"position": v(120.65, -80.43) * mm});
            skPoint(sketch, "E38.31.25.0", {"position": v(120.65, -86.78) * mm});
            skPoint(sketch, "E38.31.26.0", {"position": v(120.65, -93.13) * mm});
            skPoint(sketch, "E38.31.27.0", {"position": v(120.65, -99.48) * mm});
            skPoint(sketch, "E38.31.28.0", {"position": v(120.65, -105.83) * mm});
            skPoint(sketch, "E38.31.29.0", {"position": v(120.65, -112.18) * mm});
            skPoint(sketch, "E38.31.30.0", {"position": v(120.65, -118.53) * mm});
            skPoint(sketch, "E38.31.31.0", {"position": v(120.65, -124.88) * mm});
            skPoint(sketch, "E38.31.32.0", {"position": v(120.65, -131.23) * mm});
            skPoint(sketch, "E38.31.33.0", {"position": v(120.65, -137.58) * mm});
            skPoint(sketch, "E38.31.34.0", {"position": v(120.65, -143.93) * mm});
            skPoint(sketch, "E38.31.35.0", {"position": v(120.65, -150.28) * mm});
            skPoint(sketch, "E38.31.36.0", {"position": v(120.65, -156.63) * mm});
            skPoint(sketch, "E38.31.37.0", {"position": v(120.65, -162.98) * mm});
            skPoint(sketch, "E38.31.38.0", {"position": v(120.65, -169.33) * mm});
            skPoint(sketch, "E38.31.39.0", {"position": v(120.65, -175.68) * mm});
            skPoint(sketch, "E38.31.40.0", {"position": v(120.65, -182.03) * mm});
            skPoint(sketch, "E38.31.41.0", {"position": v(120.65, -188.38) * mm});
            skPoint(sketch, "E38.31.42.0", {"position": v(120.65, -194.73) * mm});
            skPoint(sketch, "E38.31.43.0", {"position": v(120.65, -201.08) * mm});
            skPoint(sketch, "E38.31.44.0", {"position": v(120.65, -207.43) * mm});
            skPoint(sketch, "E38.31.45.0", {"position": v(120.65, -213.78) * mm});
            skPoint(sketch, "E38.31.46.0", {"position": v(120.65, -220.13) * mm});
            skPoint(sketch, "E38.31.47.0", {"position": v(120.65, -226.48) * mm});
            skPoint(sketch, "E38.31.48.0", {"position": v(120.65, -232.83) * mm});
            skPoint(sketch, "E38.31.49.0", {"position": v(120.65, -239.18) * mm});
            skPoint(sketch, "E38.31.50.0", {"position": v(120.65, -245.53) * mm});
            skPoint(sketch, "E38.31.51.0", {"position": v(120.65, -251.88) * mm});
            skPoint(sketch, "E38.31.52.0", {"position": v(120.65, -258.23) * mm});
            skPoint(sketch, "E38.31.53.0", {"position": v(120.65, -264.58) * mm});
            skPoint(sketch, "E38.31.54.0", {"position": v(120.65, -270.93) * mm});
            skPoint(sketch, "E38.31.55.0", {"position": v(120.65, -277.28) * mm});
            skPoint(sketch, "E38.31.56.0", {"position": v(120.65, -283.63) * mm});
            skPoint(sketch, "E38.31.57.0", {"position": v(120.65, -289.98) * mm});
            skPoint(sketch, "E38.31.58.0", {"position": v(120.65, -296.33) * mm});
            skPoint(sketch, "E38.31.59.0", {"position": v(120.65, -302.68) * mm});
            skPoint(sketch, "E38.31.60.0", {"position": v(120.65, -309.03) * mm});
            skPoint(sketch, "E38.31.61.0", {"position": v(120.65, -315.38) * mm});
            skPoint(sketch, "E38.31.62.0", {"position": v(120.65, -321.73) * mm});
            skPoint(sketch, "E38.31.63.0", {"position": v(120.65, -328.08) * mm});
            skPoint(sketch, "E38.31.64.0", {"position": v(120.65, -334.43) * mm});
            skPoint(sketch, "E38.31.65.0", {"position": v(120.65, -340.78) * mm});
            skPoint(sketch, "E38.31.66.0", {"position": v(120.65, -347.13) * mm});
            skPoint(sketch, "E38.31.67.0", {"position": v(120.65, -353.48) * mm});
            skPoint(sketch, "E38.31.68.0", {"position": v(120.65, -359.83) * mm});
            skPoint(sketch, "E38.31.69.0", {"position": v(120.65, -366.18) * mm});
            skPoint(sketch, "E38.31.70.0", {"position": v(120.65, -372.53) * mm});
            skPoint(sketch, "E38.31.71.0", {"position": v(120.65, -378.88) * mm});
            skPoint(sketch, "E38.31.72.0", {"position": v(120.65, -385.23) * mm});
            skPoint(sketch, "E38.31.73.0", {"position": v(120.65, -391.58) * mm});
            skPoint(sketch, "E38.31.74.0", {"position": v(120.65, -397.93) * mm});
            skPoint(sketch, "E38.31.75.0", {"position": v(120.65, -404.28) * mm});
            skPoint(sketch, "E38.31.76.0", {"position": v(120.65, -410.63) * mm});
            skPoint(sketch, "E38.31.77.0", {"position": v(120.65, -416.98) * mm});
            skPoint(sketch, "E38.31.78.0", {"position": v(120.65, -423.33) * mm});
            skPoint(sketch, "E38.31.79.0", {"position": v(120.65, -429.68) * mm});
            skPoint(sketch, "E38.31.80.0", {"position": v(120.65, -436.03) * mm});
            skPoint(sketch, "E38.31.81.0", {"position": v(120.65, -442.38) * mm});
            skPoint(sketch, "E38.31.82.0", {"position": v(120.65, -448.73) * mm});
            skPoint(sketch, "E38.31.83.0", {"position": v(120.65, -455.08) * mm});
            skPoint(sketch, "E38.31.84.0", {"position": v(120.65, -461.43) * mm});
            skPoint(sketch, "E38.31.85.0", {"position": v(120.65, -467.78) * mm});
            skPoint(sketch, "E38.31.86.0", {"position": v(120.65, -474.13) * mm});
            skPoint(sketch, "E38.31.87.0", {"position": v(120.65, -480.48) * mm});
            skPoint(sketch, "E38.31.88.0", {"position": v(120.65, -486.83) * mm});
            skPoint(sketch, "E38.31.89.0", {"position": v(120.65, -493.18) * mm});
            skPoint(sketch, "E38.31.90.0", {"position": v(120.65, -499.53) * mm});
            skPoint(sketch, "E38.31.91.0", {"position": v(120.65, -505.88) * mm});
            skPoint(sketch, "E38.31.92.0", {"position": v(120.65, -512.23) * mm});
            skPoint(sketch, "E38.31.93.0", {"position": v(120.65, -518.58) * mm});
            skPoint(sketch, "E38.31.94.0", {"position": v(120.65, -524.93) * mm});
            skPoint(sketch, "E38.31.95.0", {"position": v(120.65, -531.28) * mm});
            skPoint(sketch, "E38.31.96.0", {"position": v(120.65, -537.63) * mm});
            skPoint(sketch, "E38.31.97.0", {"position": v(120.65, -543.98) * mm});
            skPoint(sketch, "E38.31.98.0", {"position": v(120.65, -550.33) * mm});
            skPoint(sketch, "E38.31.99.0", {"position": v(120.65, -556.68) * mm});
            skPoint(sketch, "E38.32.0.0", {"position": v(127, 71.97) * mm});
            skPoint(sketch, "E38.32.1.0", {"position": v(127, 65.62) * mm});
            skPoint(sketch, "E38.32.2.0", {"position": v(127, 59.27) * mm});
            skPoint(sketch, "E38.32.3.0", {"position": v(127, 52.92) * mm});
            skPoint(sketch, "E38.32.4.0", {"position": v(127, 46.57) * mm});
            skPoint(sketch, "E38.32.5.0", {"position": v(127, 40.22) * mm});
            skPoint(sketch, "E38.32.6.0", {"position": v(127, 33.87) * mm});
            skPoint(sketch, "E38.32.7.0", {"position": v(127, 27.52) * mm});
            skPoint(sketch, "E38.32.8.0", {"position": v(127, 21.17) * mm});
            skPoint(sketch, "E38.32.9.0", {"position": v(127, 14.82) * mm});
            skPoint(sketch, "E38.32.10.0", {"position": v(127, 8.47) * mm});
            skPoint(sketch, "E38.32.11.0", {"position": v(127, 2.12) * mm});
            skPoint(sketch, "E38.32.12.0", {"position": v(127, -4.23) * mm});
            skPoint(sketch, "E38.32.13.0", {"position": v(127, -10.58) * mm});
            skPoint(sketch, "E38.32.14.0", {"position": v(127, -16.93) * mm});
            skPoint(sketch, "E38.32.15.0", {"position": v(127, -23.28) * mm});
            skPoint(sketch, "E38.32.16.0", {"position": v(127, -29.63) * mm});
            skPoint(sketch, "E38.32.17.0", {"position": v(127, -35.98) * mm});
            skPoint(sketch, "E38.32.18.0", {"position": v(127, -42.33) * mm});
            skPoint(sketch, "E38.32.19.0", {"position": v(127, -48.68) * mm});
            skPoint(sketch, "E38.32.20.0", {"position": v(127, -55.03) * mm});
            skPoint(sketch, "E38.32.21.0", {"position": v(127, -61.38) * mm});
            skPoint(sketch, "E38.32.22.0", {"position": v(127, -67.73) * mm});
            skPoint(sketch, "E38.32.23.0", {"position": v(127, -74.08) * mm});
            skPoint(sketch, "E38.32.24.0", {"position": v(127, -80.43) * mm});
            skPoint(sketch, "E38.32.25.0", {"position": v(127, -86.78) * mm});
            skPoint(sketch, "E38.32.26.0", {"position": v(127, -93.13) * mm});
            skPoint(sketch, "E38.32.27.0", {"position": v(127, -99.48) * mm});
            skPoint(sketch, "E38.32.28.0", {"position": v(127, -105.83) * mm});
            skPoint(sketch, "E38.32.29.0", {"position": v(127, -112.18) * mm});
            skPoint(sketch, "E38.32.30.0", {"position": v(127, -118.53) * mm});
            skPoint(sketch, "E38.32.31.0", {"position": v(127, -124.88) * mm});
            skPoint(sketch, "E38.32.32.0", {"position": v(127, -131.23) * mm});
            skPoint(sketch, "E38.32.33.0", {"position": v(127, -137.58) * mm});
            skPoint(sketch, "E38.32.34.0", {"position": v(127, -143.93) * mm});
            skPoint(sketch, "E38.32.35.0", {"position": v(127, -150.28) * mm});
            skPoint(sketch, "E38.32.36.0", {"position": v(127, -156.63) * mm});
            skPoint(sketch, "E38.32.37.0", {"position": v(127, -162.98) * mm});
            skPoint(sketch, "E38.32.38.0", {"position": v(127, -169.33) * mm});
            skPoint(sketch, "E38.32.39.0", {"position": v(127, -175.68) * mm});
            skPoint(sketch, "E38.32.40.0", {"position": v(127, -182.03) * mm});
            skPoint(sketch, "E38.32.41.0", {"position": v(127, -188.38) * mm});
            skPoint(sketch, "E38.32.42.0", {"position": v(127, -194.73) * mm});
            skPoint(sketch, "E38.32.43.0", {"position": v(127, -201.08) * mm});
            skPoint(sketch, "E38.32.44.0", {"position": v(127, -207.43) * mm});
            skPoint(sketch, "E38.32.45.0", {"position": v(127, -213.78) * mm});
            skPoint(sketch, "E38.32.46.0", {"position": v(127, -220.13) * mm});
            skPoint(sketch, "E38.32.47.0", {"position": v(127, -226.48) * mm});
            skPoint(sketch, "E38.32.48.0", {"position": v(127, -232.83) * mm});
            skPoint(sketch, "E38.32.49.0", {"position": v(127, -239.18) * mm});
            skPoint(sketch, "E38.32.50.0", {"position": v(127, -245.53) * mm});
            skPoint(sketch, "E38.32.51.0", {"position": v(127, -251.88) * mm});
            skPoint(sketch, "E38.32.52.0", {"position": v(127, -258.23) * mm});
            skPoint(sketch, "E38.32.53.0", {"position": v(127, -264.58) * mm});
            skPoint(sketch, "E38.32.54.0", {"position": v(127, -270.93) * mm});
            skPoint(sketch, "E38.32.55.0", {"position": v(127, -277.28) * mm});
            skPoint(sketch, "E38.32.56.0", {"position": v(127, -283.63) * mm});
            skPoint(sketch, "E38.32.57.0", {"position": v(127, -289.98) * mm});
            skPoint(sketch, "E38.32.58.0", {"position": v(127, -296.33) * mm});
            skPoint(sketch, "E38.32.59.0", {"position": v(127, -302.68) * mm});
            skPoint(sketch, "E38.32.60.0", {"position": v(127, -309.03) * mm});
            skPoint(sketch, "E38.32.61.0", {"position": v(127, -315.38) * mm});
            skPoint(sketch, "E38.32.62.0", {"position": v(127, -321.73) * mm});
            skPoint(sketch, "E38.32.63.0", {"position": v(127, -328.08) * mm});
            skPoint(sketch, "E38.32.64.0", {"position": v(127, -334.43) * mm});
            skPoint(sketch, "E38.32.65.0", {"position": v(127, -340.78) * mm});
            skPoint(sketch, "E38.32.66.0", {"position": v(127, -347.13) * mm});
            skPoint(sketch, "E38.32.67.0", {"position": v(127, -353.48) * mm});
            skPoint(sketch, "E38.32.68.0", {"position": v(127, -359.83) * mm});
            skPoint(sketch, "E38.32.69.0", {"position": v(127, -366.18) * mm});
            skPoint(sketch, "E38.32.70.0", {"position": v(127, -372.53) * mm});
            skPoint(sketch, "E38.32.71.0", {"position": v(127, -378.88) * mm});
            skPoint(sketch, "E38.32.72.0", {"position": v(127, -385.23) * mm});
            skPoint(sketch, "E38.32.73.0", {"position": v(127, -391.58) * mm});
            skPoint(sketch, "E38.32.74.0", {"position": v(127, -397.93) * mm});
            skPoint(sketch, "E38.32.75.0", {"position": v(127, -404.28) * mm});
            skPoint(sketch, "E38.32.76.0", {"position": v(127, -410.63) * mm});
            skPoint(sketch, "E38.32.77.0", {"position": v(127, -416.98) * mm});
            skPoint(sketch, "E38.32.78.0", {"position": v(127, -423.33) * mm});
            skPoint(sketch, "E38.32.79.0", {"position": v(127, -429.68) * mm});
            skPoint(sketch, "E38.32.80.0", {"position": v(127, -436.03) * mm});
            skPoint(sketch, "E38.32.81.0", {"position": v(127, -442.38) * mm});
            skPoint(sketch, "E38.32.82.0", {"position": v(127, -448.73) * mm});
            skPoint(sketch, "E38.32.83.0", {"position": v(127, -455.08) * mm});
            skPoint(sketch, "E38.32.84.0", {"position": v(127, -461.43) * mm});
            skPoint(sketch, "E38.32.85.0", {"position": v(127, -467.78) * mm});
            skPoint(sketch, "E38.32.86.0", {"position": v(127, -474.13) * mm});
            skPoint(sketch, "E38.32.87.0", {"position": v(127, -480.48) * mm});
            skPoint(sketch, "E38.32.88.0", {"position": v(127, -486.83) * mm});
            skPoint(sketch, "E38.32.89.0", {"position": v(127, -493.18) * mm});
            skPoint(sketch, "E38.32.90.0", {"position": v(127, -499.53) * mm});
            skPoint(sketch, "E38.32.91.0", {"position": v(127, -505.88) * mm});
            skPoint(sketch, "E38.32.92.0", {"position": v(127, -512.23) * mm});
            skPoint(sketch, "E38.32.93.0", {"position": v(127, -518.58) * mm});
            skPoint(sketch, "E38.32.94.0", {"position": v(127, -524.93) * mm});
            skPoint(sketch, "E38.32.95.0", {"position": v(127, -531.28) * mm});
            skPoint(sketch, "E38.32.96.0", {"position": v(127, -537.63) * mm});
            skPoint(sketch, "E38.32.97.0", {"position": v(127, -543.98) * mm});
            skPoint(sketch, "E38.32.98.0", {"position": v(127, -550.33) * mm});
            skPoint(sketch, "E38.32.99.0", {"position": v(127, -556.68) * mm});
            skPoint(sketch, "E38.33.0.0", {"position": v(133.35, 71.97) * mm});
            skPoint(sketch, "E38.33.1.0", {"position": v(133.35, 65.62) * mm});
            skPoint(sketch, "E38.33.2.0", {"position": v(133.35, 59.27) * mm});
            skPoint(sketch, "E38.33.3.0", {"position": v(133.35, 52.92) * mm});
            skPoint(sketch, "E38.33.4.0", {"position": v(133.35, 46.57) * mm});
            skPoint(sketch, "E38.33.5.0", {"position": v(133.35, 40.22) * mm});
            skPoint(sketch, "E38.33.6.0", {"position": v(133.35, 33.87) * mm});
            skPoint(sketch, "E38.33.7.0", {"position": v(133.35, 27.52) * mm});
            skPoint(sketch, "E38.33.8.0", {"position": v(133.35, 21.17) * mm});
            skPoint(sketch, "E38.33.9.0", {"position": v(133.35, 14.82) * mm});
            skPoint(sketch, "E38.33.10.0", {"position": v(133.35, 8.47) * mm});
            skPoint(sketch, "E38.33.11.0", {"position": v(133.35, 2.12) * mm});
            skPoint(sketch, "E38.33.12.0", {"position": v(133.35, -4.23) * mm});
            skPoint(sketch, "E38.33.13.0", {"position": v(133.35, -10.58) * mm});
            skPoint(sketch, "E38.33.14.0", {"position": v(133.35, -16.93) * mm});
            skPoint(sketch, "E38.33.15.0", {"position": v(133.35, -23.28) * mm});
            skPoint(sketch, "E38.33.16.0", {"position": v(133.35, -29.63) * mm});
            skPoint(sketch, "E38.33.17.0", {"position": v(133.35, -35.98) * mm});
            skPoint(sketch, "E38.33.18.0", {"position": v(133.35, -42.33) * mm});
            skPoint(sketch, "E38.33.19.0", {"position": v(133.35, -48.68) * mm});
            skPoint(sketch, "E38.33.20.0", {"position": v(133.35, -55.03) * mm});
            skPoint(sketch, "E38.33.21.0", {"position": v(133.35, -61.38) * mm});
            skPoint(sketch, "E38.33.22.0", {"position": v(133.35, -67.73) * mm});
            skPoint(sketch, "E38.33.23.0", {"position": v(133.35, -74.08) * mm});
            skPoint(sketch, "E38.33.24.0", {"position": v(133.35, -80.43) * mm});
            skPoint(sketch, "E38.33.25.0", {"position": v(133.35, -86.78) * mm});
            skPoint(sketch, "E38.33.26.0", {"position": v(133.35, -93.13) * mm});
            skPoint(sketch, "E38.33.27.0", {"position": v(133.35, -99.48) * mm});
            skPoint(sketch, "E38.33.28.0", {"position": v(133.35, -105.83) * mm});
            skPoint(sketch, "E38.33.29.0", {"position": v(133.35, -112.18) * mm});
            skPoint(sketch, "E38.33.30.0", {"position": v(133.35, -118.53) * mm});
            skPoint(sketch, "E38.33.31.0", {"position": v(133.35, -124.88) * mm});
            skPoint(sketch, "E38.33.32.0", {"position": v(133.35, -131.23) * mm});
            skPoint(sketch, "E38.33.33.0", {"position": v(133.35, -137.58) * mm});
            skPoint(sketch, "E38.33.34.0", {"position": v(133.35, -143.93) * mm});
            skPoint(sketch, "E38.33.35.0", {"position": v(133.35, -150.28) * mm});
            skPoint(sketch, "E38.33.36.0", {"position": v(133.35, -156.63) * mm});
            skPoint(sketch, "E38.33.37.0", {"position": v(133.35, -162.98) * mm});
            skPoint(sketch, "E38.33.38.0", {"position": v(133.35, -169.33) * mm});
            skPoint(sketch, "E38.33.39.0", {"position": v(133.35, -175.68) * mm});
            skPoint(sketch, "E38.33.40.0", {"position": v(133.35, -182.03) * mm});
            skPoint(sketch, "E38.33.41.0", {"position": v(133.35, -188.38) * mm});
            skPoint(sketch, "E38.33.42.0", {"position": v(133.35, -194.73) * mm});
            skPoint(sketch, "E38.33.43.0", {"position": v(133.35, -201.08) * mm});
            skPoint(sketch, "E38.33.44.0", {"position": v(133.35, -207.43) * mm});
            skPoint(sketch, "E38.33.45.0", {"position": v(133.35, -213.78) * mm});
            skPoint(sketch, "E38.33.46.0", {"position": v(133.35, -220.13) * mm});
            skPoint(sketch, "E38.33.47.0", {"position": v(133.35, -226.48) * mm});
            skPoint(sketch, "E38.33.48.0", {"position": v(133.35, -232.83) * mm});
            skPoint(sketch, "E38.33.49.0", {"position": v(133.35, -239.18) * mm});
            skPoint(sketch, "E38.33.50.0", {"position": v(133.35, -245.53) * mm});
            skPoint(sketch, "E38.33.51.0", {"position": v(133.35, -251.88) * mm});
            skPoint(sketch, "E38.33.52.0", {"position": v(133.35, -258.23) * mm});
            skPoint(sketch, "E38.33.53.0", {"position": v(133.35, -264.58) * mm});
            skPoint(sketch, "E38.33.54.0", {"position": v(133.35, -270.93) * mm});
            skPoint(sketch, "E38.33.55.0", {"position": v(133.35, -277.28) * mm});
            skPoint(sketch, "E38.33.56.0", {"position": v(133.35, -283.63) * mm});
            skPoint(sketch, "E38.33.57.0", {"position": v(133.35, -289.98) * mm});
            skPoint(sketch, "E38.33.58.0", {"position": v(133.35, -296.33) * mm});
            skPoint(sketch, "E38.33.59.0", {"position": v(133.35, -302.68) * mm});
            skPoint(sketch, "E38.33.60.0", {"position": v(133.35, -309.03) * mm});
            skPoint(sketch, "E38.33.61.0", {"position": v(133.35, -315.38) * mm});
            skPoint(sketch, "E38.33.62.0", {"position": v(133.35, -321.73) * mm});
            skPoint(sketch, "E38.33.63.0", {"position": v(133.35, -328.08) * mm});
            skPoint(sketch, "E38.33.64.0", {"position": v(133.35, -334.43) * mm});
            skPoint(sketch, "E38.33.65.0", {"position": v(133.35, -340.78) * mm});
            skPoint(sketch, "E38.33.66.0", {"position": v(133.35, -347.13) * mm});
            skPoint(sketch, "E38.33.67.0", {"position": v(133.35, -353.48) * mm});
            skPoint(sketch, "E38.33.68.0", {"position": v(133.35, -359.83) * mm});
            skPoint(sketch, "E38.33.69.0", {"position": v(133.35, -366.18) * mm});
            skPoint(sketch, "E38.33.70.0", {"position": v(133.35, -372.53) * mm});
            skPoint(sketch, "E38.33.71.0", {"position": v(133.35, -378.88) * mm});
            skPoint(sketch, "E38.33.72.0", {"position": v(133.35, -385.23) * mm});
            skPoint(sketch, "E38.33.73.0", {"position": v(133.35, -391.58) * mm});
            skPoint(sketch, "E38.33.74.0", {"position": v(133.35, -397.93) * mm});
            skPoint(sketch, "E38.33.75.0", {"position": v(133.35, -404.28) * mm});
            skPoint(sketch, "E38.33.76.0", {"position": v(133.35, -410.63) * mm});
            skPoint(sketch, "E38.33.77.0", {"position": v(133.35, -416.98) * mm});
            skPoint(sketch, "E38.33.78.0", {"position": v(133.35, -423.33) * mm});
            skPoint(sketch, "E38.33.79.0", {"position": v(133.35, -429.68) * mm});
            skPoint(sketch, "E38.33.80.0", {"position": v(133.35, -436.03) * mm});
            skPoint(sketch, "E38.33.81.0", {"position": v(133.35, -442.38) * mm});
            skPoint(sketch, "E38.33.82.0", {"position": v(133.35, -448.73) * mm});
            skPoint(sketch, "E38.33.83.0", {"position": v(133.35, -455.08) * mm});
            skPoint(sketch, "E38.33.84.0", {"position": v(133.35, -461.43) * mm});
            skPoint(sketch, "E38.33.85.0", {"position": v(133.35, -467.78) * mm});
            skPoint(sketch, "E38.33.86.0", {"position": v(133.35, -474.13) * mm});
            skPoint(sketch, "E38.33.87.0", {"position": v(133.35, -480.48) * mm});
            skPoint(sketch, "E38.33.88.0", {"position": v(133.35, -486.83) * mm});
            skPoint(sketch, "E38.33.89.0", {"position": v(133.35, -493.18) * mm});
            skPoint(sketch, "E38.33.90.0", {"position": v(133.35, -499.53) * mm});
            skPoint(sketch, "E38.33.91.0", {"position": v(133.35, -505.88) * mm});
            skPoint(sketch, "E38.33.92.0", {"position": v(133.35, -512.23) * mm});
            skPoint(sketch, "E38.33.93.0", {"position": v(133.35, -518.58) * mm});
            skPoint(sketch, "E38.33.94.0", {"position": v(133.35, -524.93) * mm});
            skPoint(sketch, "E38.33.95.0", {"position": v(133.35, -531.28) * mm});
            skPoint(sketch, "E38.33.96.0", {"position": v(133.35, -537.63) * mm});
            skPoint(sketch, "E38.33.97.0", {"position": v(133.35, -543.98) * mm});
            skPoint(sketch, "E38.33.98.0", {"position": v(133.35, -550.33) * mm});
            skPoint(sketch, "E38.33.99.0", {"position": v(133.35, -556.68) * mm});
            skPoint(sketch, "E38.34.0.0", {"position": v(139.7, 71.97) * mm});
            skPoint(sketch, "E38.34.1.0", {"position": v(139.7, 65.62) * mm});
            skPoint(sketch, "E38.34.2.0", {"position": v(139.7, 59.27) * mm});
            skPoint(sketch, "E38.34.3.0", {"position": v(139.7, 52.92) * mm});
            skPoint(sketch, "E38.34.4.0", {"position": v(139.7, 46.57) * mm});
            skPoint(sketch, "E38.34.5.0", {"position": v(139.7, 40.22) * mm});
            skPoint(sketch, "E38.34.6.0", {"position": v(139.7, 33.87) * mm});
            skPoint(sketch, "E38.34.7.0", {"position": v(139.7, 27.52) * mm});
            skPoint(sketch, "E38.34.8.0", {"position": v(139.7, 21.17) * mm});
            skPoint(sketch, "E38.34.9.0", {"position": v(139.7, 14.82) * mm});
            skPoint(sketch, "E38.34.10.0", {"position": v(139.7, 8.47) * mm});
            skPoint(sketch, "E38.34.11.0", {"position": v(139.7, 2.12) * mm});
            skPoint(sketch, "E38.34.12.0", {"position": v(139.7, -4.23) * mm});
            skPoint(sketch, "E38.34.13.0", {"position": v(139.7, -10.58) * mm});
            skPoint(sketch, "E38.34.14.0", {"position": v(139.7, -16.93) * mm});
            skPoint(sketch, "E38.34.15.0", {"position": v(139.7, -23.28) * mm});
            skPoint(sketch, "E38.34.16.0", {"position": v(139.7, -29.63) * mm});
            skPoint(sketch, "E38.34.17.0", {"position": v(139.7, -35.98) * mm});
            skPoint(sketch, "E38.34.18.0", {"position": v(139.7, -42.33) * mm});
            skPoint(sketch, "E38.34.19.0", {"position": v(139.7, -48.68) * mm});
            skPoint(sketch, "E38.34.20.0", {"position": v(139.7, -55.03) * mm});
            skPoint(sketch, "E38.34.21.0", {"position": v(139.7, -61.38) * mm});
            skPoint(sketch, "E38.34.22.0", {"position": v(139.7, -67.73) * mm});
            skPoint(sketch, "E38.34.23.0", {"position": v(139.7, -74.08) * mm});
            skPoint(sketch, "E38.34.24.0", {"position": v(139.7, -80.43) * mm});
            skPoint(sketch, "E38.34.25.0", {"position": v(139.7, -86.78) * mm});
            skPoint(sketch, "E38.34.26.0", {"position": v(139.7, -93.13) * mm});
            skPoint(sketch, "E38.34.27.0", {"position": v(139.7, -99.48) * mm});
            skPoint(sketch, "E38.34.28.0", {"position": v(139.7, -105.83) * mm});
            skPoint(sketch, "E38.34.29.0", {"position": v(139.7, -112.18) * mm});
            skPoint(sketch, "E38.34.30.0", {"position": v(139.7, -118.53) * mm});
            skPoint(sketch, "E38.34.31.0", {"position": v(139.7, -124.88) * mm});
            skPoint(sketch, "E38.34.32.0", {"position": v(139.7, -131.23) * mm});
            skPoint(sketch, "E38.34.33.0", {"position": v(139.7, -137.58) * mm});
            skPoint(sketch, "E38.34.34.0", {"position": v(139.7, -143.93) * mm});
            skPoint(sketch, "E38.34.35.0", {"position": v(139.7, -150.28) * mm});
            skPoint(sketch, "E38.34.36.0", {"position": v(139.7, -156.63) * mm});
            skPoint(sketch, "E38.34.37.0", {"position": v(139.7, -162.98) * mm});
            skPoint(sketch, "E38.34.38.0", {"position": v(139.7, -169.33) * mm});
            skPoint(sketch, "E38.34.39.0", {"position": v(139.7, -175.68) * mm});
            skPoint(sketch, "E38.34.40.0", {"position": v(139.7, -182.03) * mm});
            skPoint(sketch, "E38.34.41.0", {"position": v(139.7, -188.38) * mm});
            skPoint(sketch, "E38.34.42.0", {"position": v(139.7, -194.73) * mm});
            skPoint(sketch, "E38.34.43.0", {"position": v(139.7, -201.08) * mm});
            skPoint(sketch, "E38.34.44.0", {"position": v(139.7, -207.43) * mm});
            skPoint(sketch, "E38.34.45.0", {"position": v(139.7, -213.78) * mm});
            skPoint(sketch, "E38.34.46.0", {"position": v(139.7, -220.13) * mm});
            skPoint(sketch, "E38.34.47.0", {"position": v(139.7, -226.48) * mm});
            skPoint(sketch, "E38.34.48.0", {"position": v(139.7, -232.83) * mm});
            skPoint(sketch, "E38.34.49.0", {"position": v(139.7, -239.18) * mm});
            skPoint(sketch, "E38.34.50.0", {"position": v(139.7, -245.53) * mm});
            skPoint(sketch, "E38.34.51.0", {"position": v(139.7, -251.88) * mm});
            skPoint(sketch, "E38.34.52.0", {"position": v(139.7, -258.23) * mm});
            skPoint(sketch, "E38.34.53.0", {"position": v(139.7, -264.58) * mm});
            skPoint(sketch, "E38.34.54.0", {"position": v(139.7, -270.93) * mm});
            skPoint(sketch, "E38.34.55.0", {"position": v(139.7, -277.28) * mm});
            skPoint(sketch, "E38.34.56.0", {"position": v(139.7, -283.63) * mm});
            skPoint(sketch, "E38.34.57.0", {"position": v(139.7, -289.98) * mm});
            skPoint(sketch, "E38.34.58.0", {"position": v(139.7, -296.33) * mm});
            skPoint(sketch, "E38.34.59.0", {"position": v(139.7, -302.68) * mm});
            skPoint(sketch, "E38.34.60.0", {"position": v(139.7, -309.03) * mm});
            skPoint(sketch, "E38.34.61.0", {"position": v(139.7, -315.38) * mm});
            skPoint(sketch, "E38.34.62.0", {"position": v(139.7, -321.73) * mm});
            skPoint(sketch, "E38.34.63.0", {"position": v(139.7, -328.08) * mm});
            skPoint(sketch, "E38.34.64.0", {"position": v(139.7, -334.43) * mm});
            skPoint(sketch, "E38.34.65.0", {"position": v(139.7, -340.78) * mm});
            skPoint(sketch, "E38.34.66.0", {"position": v(139.7, -347.13) * mm});
            skPoint(sketch, "E38.34.67.0", {"position": v(139.7, -353.48) * mm});
            skPoint(sketch, "E38.34.68.0", {"position": v(139.7, -359.83) * mm});
            skPoint(sketch, "E38.34.69.0", {"position": v(139.7, -366.18) * mm});
            skPoint(sketch, "E38.34.70.0", {"position": v(139.7, -372.53) * mm});
            skPoint(sketch, "E38.34.71.0", {"position": v(139.7, -378.88) * mm});
            skPoint(sketch, "E38.34.72.0", {"position": v(139.7, -385.23) * mm});
            skPoint(sketch, "E38.34.73.0", {"position": v(139.7, -391.58) * mm});
            skPoint(sketch, "E38.34.74.0", {"position": v(139.7, -397.93) * mm});
            skPoint(sketch, "E38.34.75.0", {"position": v(139.7, -404.28) * mm});
            skPoint(sketch, "E38.34.76.0", {"position": v(139.7, -410.63) * mm});
            skPoint(sketch, "E38.34.77.0", {"position": v(139.7, -416.98) * mm});
            skPoint(sketch, "E38.34.78.0", {"position": v(139.7, -423.33) * mm});
            skPoint(sketch, "E38.34.79.0", {"position": v(139.7, -429.68) * mm});
            skPoint(sketch, "E38.34.80.0", {"position": v(139.7, -436.03) * mm});
            skPoint(sketch, "E38.34.81.0", {"position": v(139.7, -442.38) * mm});
            skPoint(sketch, "E38.34.82.0", {"position": v(139.7, -448.73) * mm});
            skPoint(sketch, "E38.34.83.0", {"position": v(139.7, -455.08) * mm});
            skPoint(sketch, "E38.34.84.0", {"position": v(139.7, -461.43) * mm});
            skPoint(sketch, "E38.34.85.0", {"position": v(139.7, -467.78) * mm});
            skPoint(sketch, "E38.34.86.0", {"position": v(139.7, -474.13) * mm});
            skPoint(sketch, "E38.34.87.0", {"position": v(139.7, -480.48) * mm});
            skPoint(sketch, "E38.34.88.0", {"position": v(139.7, -486.83) * mm});
            skPoint(sketch, "E38.34.89.0", {"position": v(139.7, -493.18) * mm});
            skPoint(sketch, "E38.34.90.0", {"position": v(139.7, -499.53) * mm});
            skPoint(sketch, "E38.34.91.0", {"position": v(139.7, -505.88) * mm});
            skPoint(sketch, "E38.34.92.0", {"position": v(139.7, -512.23) * mm});
            skPoint(sketch, "E38.34.93.0", {"position": v(139.7, -518.58) * mm});
            skPoint(sketch, "E38.34.94.0", {"position": v(139.7, -524.93) * mm});
            skPoint(sketch, "E38.34.95.0", {"position": v(139.7, -531.28) * mm});
            skPoint(sketch, "E38.34.96.0", {"position": v(139.7, -537.63) * mm});
            skPoint(sketch, "E38.34.97.0", {"position": v(139.7, -543.98) * mm});
            skPoint(sketch, "E38.34.98.0", {"position": v(139.7, -550.33) * mm});
            skPoint(sketch, "E38.34.99.0", {"position": v(139.7, -556.68) * mm});
            skPoint(sketch, "E38.35.0.0", {"position": v(146.05, 71.97) * mm});
            skPoint(sketch, "E38.35.1.0", {"position": v(146.05, 65.62) * mm});
            skPoint(sketch, "E38.35.2.0", {"position": v(146.05, 59.27) * mm});
            skPoint(sketch, "E38.35.3.0", {"position": v(146.05, 52.92) * mm});
            skPoint(sketch, "E38.35.4.0", {"position": v(146.05, 46.57) * mm});
            skPoint(sketch, "E38.35.5.0", {"position": v(146.05, 40.22) * mm});
            skPoint(sketch, "E38.35.6.0", {"position": v(146.05, 33.87) * mm});
            skPoint(sketch, "E38.35.7.0", {"position": v(146.05, 27.52) * mm});
            skPoint(sketch, "E38.35.8.0", {"position": v(146.05, 21.17) * mm});
            skPoint(sketch, "E38.35.9.0", {"position": v(146.05, 14.82) * mm});
            skPoint(sketch, "E38.35.10.0", {"position": v(146.05, 8.47) * mm});
            skPoint(sketch, "E38.35.11.0", {"position": v(146.05, 2.12) * mm});
            skPoint(sketch, "E38.35.12.0", {"position": v(146.05, -4.23) * mm});
            skPoint(sketch, "E38.35.13.0", {"position": v(146.05, -10.58) * mm});
            skPoint(sketch, "E38.35.14.0", {"position": v(146.05, -16.93) * mm});
            skPoint(sketch, "E38.35.15.0", {"position": v(146.05, -23.28) * mm});
            skPoint(sketch, "E38.35.16.0", {"position": v(146.05, -29.63) * mm});
            skPoint(sketch, "E38.35.17.0", {"position": v(146.05, -35.98) * mm});
            skPoint(sketch, "E38.35.18.0", {"position": v(146.05, -42.33) * mm});
            skPoint(sketch, "E38.35.19.0", {"position": v(146.05, -48.68) * mm});
            skPoint(sketch, "E38.35.20.0", {"position": v(146.05, -55.03) * mm});
            skPoint(sketch, "E38.35.21.0", {"position": v(146.05, -61.38) * mm});
            skPoint(sketch, "E38.35.22.0", {"position": v(146.05, -67.73) * mm});
            skPoint(sketch, "E38.35.23.0", {"position": v(146.05, -74.08) * mm});
            skPoint(sketch, "E38.35.24.0", {"position": v(146.05, -80.43) * mm});
            skPoint(sketch, "E38.35.25.0", {"position": v(146.05, -86.78) * mm});
            skPoint(sketch, "E38.35.26.0", {"position": v(146.05, -93.13) * mm});
            skPoint(sketch, "E38.35.27.0", {"position": v(146.05, -99.48) * mm});
            skPoint(sketch, "E38.35.28.0", {"position": v(146.05, -105.83) * mm});
            skPoint(sketch, "E38.35.29.0", {"position": v(146.05, -112.18) * mm});
            skPoint(sketch, "E38.35.30.0", {"position": v(146.05, -118.53) * mm});
            skPoint(sketch, "E38.35.31.0", {"position": v(146.05, -124.88) * mm});
            skPoint(sketch, "E38.35.32.0", {"position": v(146.05, -131.23) * mm});
            skPoint(sketch, "E38.35.33.0", {"position": v(146.05, -137.58) * mm});
            skPoint(sketch, "E38.35.34.0", {"position": v(146.05, -143.93) * mm});
            skPoint(sketch, "E38.35.35.0", {"position": v(146.05, -150.28) * mm});
            skPoint(sketch, "E38.35.36.0", {"position": v(146.05, -156.63) * mm});
            skPoint(sketch, "E38.35.37.0", {"position": v(146.05, -162.98) * mm});
            skPoint(sketch, "E38.35.38.0", {"position": v(146.05, -169.33) * mm});
            skPoint(sketch, "E38.35.39.0", {"position": v(146.05, -175.68) * mm});
            skPoint(sketch, "E38.35.40.0", {"position": v(146.05, -182.03) * mm});
            skPoint(sketch, "E38.35.41.0", {"position": v(146.05, -188.38) * mm});
            skPoint(sketch, "E38.35.42.0", {"position": v(146.05, -194.73) * mm});
            skPoint(sketch, "E38.35.43.0", {"position": v(146.05, -201.08) * mm});
            skPoint(sketch, "E38.35.44.0", {"position": v(146.05, -207.43) * mm});
            skPoint(sketch, "E38.35.45.0", {"position": v(146.05, -213.78) * mm});
            skPoint(sketch, "E38.35.46.0", {"position": v(146.05, -220.13) * mm});
            skPoint(sketch, "E38.35.47.0", {"position": v(146.05, -226.48) * mm});
            skPoint(sketch, "E38.35.48.0", {"position": v(146.05, -232.83) * mm});
            skPoint(sketch, "E38.35.49.0", {"position": v(146.05, -239.18) * mm});
            skPoint(sketch, "E38.35.50.0", {"position": v(146.05, -245.53) * mm});
            skPoint(sketch, "E38.35.51.0", {"position": v(146.05, -251.88) * mm});
            skPoint(sketch, "E38.35.52.0", {"position": v(146.05, -258.23) * mm});
            skPoint(sketch, "E38.35.53.0", {"position": v(146.05, -264.58) * mm});
            skPoint(sketch, "E38.35.54.0", {"position": v(146.05, -270.93) * mm});
            skPoint(sketch, "E38.35.55.0", {"position": v(146.05, -277.28) * mm});
            skPoint(sketch, "E38.35.56.0", {"position": v(146.05, -283.63) * mm});
            skPoint(sketch, "E38.35.57.0", {"position": v(146.05, -289.98) * mm});
            skPoint(sketch, "E38.35.58.0", {"position": v(146.05, -296.33) * mm});
            skPoint(sketch, "E38.35.59.0", {"position": v(146.05, -302.68) * mm});
            skPoint(sketch, "E38.35.60.0", {"position": v(146.05, -309.03) * mm});
            skPoint(sketch, "E38.35.61.0", {"position": v(146.05, -315.38) * mm});
            skPoint(sketch, "E38.35.62.0", {"position": v(146.05, -321.73) * mm});
            skPoint(sketch, "E38.35.63.0", {"position": v(146.05, -328.08) * mm});
            skPoint(sketch, "E38.35.64.0", {"position": v(146.05, -334.43) * mm});
            skPoint(sketch, "E38.35.65.0", {"position": v(146.05, -340.78) * mm});
            skPoint(sketch, "E38.35.66.0", {"position": v(146.05, -347.13) * mm});
            skPoint(sketch, "E38.35.67.0", {"position": v(146.05, -353.48) * mm});
            skPoint(sketch, "E38.35.68.0", {"position": v(146.05, -359.83) * mm});
            skPoint(sketch, "E38.35.69.0", {"position": v(146.05, -366.18) * mm});
            skPoint(sketch, "E38.35.70.0", {"position": v(146.05, -372.53) * mm});
            skPoint(sketch, "E38.35.71.0", {"position": v(146.05, -378.88) * mm});
            skPoint(sketch, "E38.35.72.0", {"position": v(146.05, -385.23) * mm});
            skPoint(sketch, "E38.35.73.0", {"position": v(146.05, -391.58) * mm});
            skPoint(sketch, "E38.35.74.0", {"position": v(146.05, -397.93) * mm});
            skPoint(sketch, "E38.35.75.0", {"position": v(146.05, -404.28) * mm});
            skPoint(sketch, "E38.35.76.0", {"position": v(146.05, -410.63) * mm});
            skPoint(sketch, "E38.35.77.0", {"position": v(146.05, -416.98) * mm});
            skPoint(sketch, "E38.35.78.0", {"position": v(146.05, -423.33) * mm});
            skPoint(sketch, "E38.35.79.0", {"position": v(146.05, -429.68) * mm});
            skPoint(sketch, "E38.35.80.0", {"position": v(146.05, -436.03) * mm});
            skPoint(sketch, "E38.35.81.0", {"position": v(146.05, -442.38) * mm});
            skPoint(sketch, "E38.35.82.0", {"position": v(146.05, -448.73) * mm});
            skPoint(sketch, "E38.35.83.0", {"position": v(146.05, -455.08) * mm});
            skPoint(sketch, "E38.35.84.0", {"position": v(146.05, -461.43) * mm});
            skPoint(sketch, "E38.35.85.0", {"position": v(146.05, -467.78) * mm});
            skPoint(sketch, "E38.35.86.0", {"position": v(146.05, -474.13) * mm});
            skPoint(sketch, "E38.35.87.0", {"position": v(146.05, -480.48) * mm});
            skPoint(sketch, "E38.35.88.0", {"position": v(146.05, -486.83) * mm});
            skPoint(sketch, "E38.35.89.0", {"position": v(146.05, -493.18) * mm});
            skPoint(sketch, "E38.35.90.0", {"position": v(146.05, -499.53) * mm});
            skPoint(sketch, "E38.35.91.0", {"position": v(146.05, -505.88) * mm});
            skPoint(sketch, "E38.35.92.0", {"position": v(146.05, -512.23) * mm});
            skPoint(sketch, "E38.35.93.0", {"position": v(146.05, -518.58) * mm});
            skPoint(sketch, "E38.35.94.0", {"position": v(146.05, -524.93) * mm});
            skPoint(sketch, "E38.35.95.0", {"position": v(146.05, -531.28) * mm});
            skPoint(sketch, "E38.35.96.0", {"position": v(146.05, -537.63) * mm});
            skPoint(sketch, "E38.35.97.0", {"position": v(146.05, -543.98) * mm});
            skPoint(sketch, "E38.35.98.0", {"position": v(146.05, -550.33) * mm});
            skPoint(sketch, "E38.35.99.0", {"position": v(146.05, -556.68) * mm});
            skPoint(sketch, "E38.36.0.0", {"position": v(152.4, 71.97) * mm});
            skPoint(sketch, "E38.36.1.0", {"position": v(152.4, 65.62) * mm});
            skPoint(sketch, "E38.36.2.0", {"position": v(152.4, 59.27) * mm});
            skPoint(sketch, "E38.36.3.0", {"position": v(152.4, 52.92) * mm});
            skPoint(sketch, "E38.36.4.0", {"position": v(152.4, 46.57) * mm});
            skPoint(sketch, "E38.36.5.0", {"position": v(152.4, 40.22) * mm});
            skPoint(sketch, "E38.36.6.0", {"position": v(152.4, 33.87) * mm});
            skPoint(sketch, "E38.36.7.0", {"position": v(152.4, 27.52) * mm});
            skPoint(sketch, "E38.36.8.0", {"position": v(152.4, 21.17) * mm});
            skPoint(sketch, "E38.36.9.0", {"position": v(152.4, 14.82) * mm});
            skPoint(sketch, "E38.36.10.0", {"position": v(152.4, 8.47) * mm});
            skPoint(sketch, "E38.36.11.0", {"position": v(152.4, 2.12) * mm});
            skPoint(sketch, "E38.36.12.0", {"position": v(152.4, -4.23) * mm});
            skPoint(sketch, "E38.36.13.0", {"position": v(152.4, -10.58) * mm});
            skPoint(sketch, "E38.36.14.0", {"position": v(152.4, -16.93) * mm});
            skPoint(sketch, "E38.36.15.0", {"position": v(152.4, -23.28) * mm});
            skPoint(sketch, "E38.36.16.0", {"position": v(152.4, -29.63) * mm});
            skPoint(sketch, "E38.36.17.0", {"position": v(152.4, -35.98) * mm});
            skPoint(sketch, "E38.36.18.0", {"position": v(152.4, -42.33) * mm});
            skPoint(sketch, "E38.36.19.0", {"position": v(152.4, -48.68) * mm});
            skPoint(sketch, "E38.36.20.0", {"position": v(152.4, -55.03) * mm});
            skPoint(sketch, "E38.36.21.0", {"position": v(152.4, -61.38) * mm});
            skPoint(sketch, "E38.36.22.0", {"position": v(152.4, -67.73) * mm});
            skPoint(sketch, "E38.36.23.0", {"position": v(152.4, -74.08) * mm});
            skPoint(sketch, "E38.36.24.0", {"position": v(152.4, -80.43) * mm});
            skPoint(sketch, "E38.36.25.0", {"position": v(152.4, -86.78) * mm});
            skPoint(sketch, "E38.36.26.0", {"position": v(152.4, -93.13) * mm});
            skPoint(sketch, "E38.36.27.0", {"position": v(152.4, -99.48) * mm});
            skPoint(sketch, "E38.36.28.0", {"position": v(152.4, -105.83) * mm});
            skPoint(sketch, "E38.36.29.0", {"position": v(152.4, -112.18) * mm});
            skPoint(sketch, "E38.36.30.0", {"position": v(152.4, -118.53) * mm});
            skPoint(sketch, "E38.36.31.0", {"position": v(152.4, -124.88) * mm});
            skPoint(sketch, "E38.36.32.0", {"position": v(152.4, -131.23) * mm});
            skPoint(sketch, "E38.36.33.0", {"position": v(152.4, -137.58) * mm});
            skPoint(sketch, "E38.36.34.0", {"position": v(152.4, -143.93) * mm});
            skPoint(sketch, "E38.36.35.0", {"position": v(152.4, -150.28) * mm});
            skPoint(sketch, "E38.36.36.0", {"position": v(152.4, -156.63) * mm});
            skPoint(sketch, "E38.36.37.0", {"position": v(152.4, -162.98) * mm});
            skPoint(sketch, "E38.36.38.0", {"position": v(152.4, -169.33) * mm});
            skPoint(sketch, "E38.36.39.0", {"position": v(152.4, -175.68) * mm});
            skPoint(sketch, "E38.36.40.0", {"position": v(152.4, -182.03) * mm});
            skPoint(sketch, "E38.36.41.0", {"position": v(152.4, -188.38) * mm});
            skPoint(sketch, "E38.36.42.0", {"position": v(152.4, -194.73) * mm});
            skPoint(sketch, "E38.36.43.0", {"position": v(152.4, -201.08) * mm});
            skPoint(sketch, "E38.36.44.0", {"position": v(152.4, -207.43) * mm});
            skPoint(sketch, "E38.36.45.0", {"position": v(152.4, -213.78) * mm});
            skPoint(sketch, "E38.36.46.0", {"position": v(152.4, -220.13) * mm});
            skPoint(sketch, "E38.36.47.0", {"position": v(152.4, -226.48) * mm});
            skPoint(sketch, "E38.36.48.0", {"position": v(152.4, -232.83) * mm});
            skPoint(sketch, "E38.36.49.0", {"position": v(152.4, -239.18) * mm});
            skPoint(sketch, "E38.36.50.0", {"position": v(152.4, -245.53) * mm});
            skPoint(sketch, "E38.36.51.0", {"position": v(152.4, -251.88) * mm});
            skPoint(sketch, "E38.36.52.0", {"position": v(152.4, -258.23) * mm});
            skPoint(sketch, "E38.36.53.0", {"position": v(152.4, -264.58) * mm});
            skPoint(sketch, "E38.36.54.0", {"position": v(152.4, -270.93) * mm});
            skPoint(sketch, "E38.36.55.0", {"position": v(152.4, -277.28) * mm});
            skPoint(sketch, "E38.36.56.0", {"position": v(152.4, -283.63) * mm});
            skPoint(sketch, "E38.36.57.0", {"position": v(152.4, -289.98) * mm});
            skPoint(sketch, "E38.36.58.0", {"position": v(152.4, -296.33) * mm});
            skPoint(sketch, "E38.36.59.0", {"position": v(152.4, -302.68) * mm});
            skPoint(sketch, "E38.36.60.0", {"position": v(152.4, -309.03) * mm});
            skPoint(sketch, "E38.36.61.0", {"position": v(152.4, -315.38) * mm});
            skPoint(sketch, "E38.36.62.0", {"position": v(152.4, -321.73) * mm});
            skPoint(sketch, "E38.36.63.0", {"position": v(152.4, -328.08) * mm});
            skPoint(sketch, "E38.36.64.0", {"position": v(152.4, -334.43) * mm});
            skPoint(sketch, "E38.36.65.0", {"position": v(152.4, -340.78) * mm});
            skPoint(sketch, "E38.36.66.0", {"position": v(152.4, -347.13) * mm});
            skPoint(sketch, "E38.36.67.0", {"position": v(152.4, -353.48) * mm});
            skPoint(sketch, "E38.36.68.0", {"position": v(152.4, -359.83) * mm});
            skPoint(sketch, "E38.36.69.0", {"position": v(152.4, -366.18) * mm});
            skPoint(sketch, "E38.36.70.0", {"position": v(152.4, -372.53) * mm});
            skPoint(sketch, "E38.36.71.0", {"position": v(152.4, -378.88) * mm});
            skPoint(sketch, "E38.36.72.0", {"position": v(152.4, -385.23) * mm});
            skPoint(sketch, "E38.36.73.0", {"position": v(152.4, -391.58) * mm});
            skPoint(sketch, "E38.36.74.0", {"position": v(152.4, -397.93) * mm});
            skPoint(sketch, "E38.36.75.0", {"position": v(152.4, -404.28) * mm});
            skPoint(sketch, "E38.36.76.0", {"position": v(152.4, -410.63) * mm});
            skPoint(sketch, "E38.36.77.0", {"position": v(152.4, -416.98) * mm});
            skPoint(sketch, "E38.36.78.0", {"position": v(152.4, -423.33) * mm});
            skPoint(sketch, "E38.36.79.0", {"position": v(152.4, -429.68) * mm});
            skPoint(sketch, "E38.36.80.0", {"position": v(152.4, -436.03) * mm});
            skPoint(sketch, "E38.36.81.0", {"position": v(152.4, -442.38) * mm});
            skPoint(sketch, "E38.36.82.0", {"position": v(152.4, -448.73) * mm});
            skPoint(sketch, "E38.36.83.0", {"position": v(152.4, -455.08) * mm});
            skPoint(sketch, "E38.36.84.0", {"position": v(152.4, -461.43) * mm});
            skPoint(sketch, "E38.36.85.0", {"position": v(152.4, -467.78) * mm});
            skPoint(sketch, "E38.36.86.0", {"position": v(152.4, -474.13) * mm});
            skPoint(sketch, "E38.36.87.0", {"position": v(152.4, -480.48) * mm});
            skPoint(sketch, "E38.36.88.0", {"position": v(152.4, -486.83) * mm});
            skPoint(sketch, "E38.36.89.0", {"position": v(152.4, -493.18) * mm});
            skPoint(sketch, "E38.36.90.0", {"position": v(152.4, -499.53) * mm});
            skPoint(sketch, "E38.36.91.0", {"position": v(152.4, -505.88) * mm});
            skPoint(sketch, "E38.36.92.0", {"position": v(152.4, -512.23) * mm});
            skPoint(sketch, "E38.36.93.0", {"position": v(152.4, -518.58) * mm});
            skPoint(sketch, "E38.36.94.0", {"position": v(152.4, -524.93) * mm});
            skPoint(sketch, "E38.36.95.0", {"position": v(152.4, -531.28) * mm});
            skPoint(sketch, "E38.36.96.0", {"position": v(152.4, -537.63) * mm});
            skPoint(sketch, "E38.36.97.0", {"position": v(152.4, -543.98) * mm});
            skPoint(sketch, "E38.36.98.0", {"position": v(152.4, -550.33) * mm});
            skPoint(sketch, "E38.36.99.0", {"position": v(152.4, -556.68) * mm});
            skPoint(sketch, "E38.37.0.0", {"position": v(158.75, 71.97) * mm});
            skPoint(sketch, "E38.37.1.0", {"position": v(158.75, 65.62) * mm});
            skPoint(sketch, "E38.37.2.0", {"position": v(158.75, 59.27) * mm});
            skPoint(sketch, "E38.37.3.0", {"position": v(158.75, 52.92) * mm});
            skPoint(sketch, "E38.37.4.0", {"position": v(158.75, 46.57) * mm});
            skPoint(sketch, "E38.37.5.0", {"position": v(158.75, 40.22) * mm});
            skPoint(sketch, "E38.37.6.0", {"position": v(158.75, 33.87) * mm});
            skPoint(sketch, "E38.37.7.0", {"position": v(158.75, 27.52) * mm});
            skPoint(sketch, "E38.37.8.0", {"position": v(158.75, 21.17) * mm});
            skPoint(sketch, "E38.37.9.0", {"position": v(158.75, 14.82) * mm});
            skPoint(sketch, "E38.37.10.0", {"position": v(158.75, 8.47) * mm});
            skPoint(sketch, "E38.37.11.0", {"position": v(158.75, 2.12) * mm});
            skPoint(sketch, "E38.37.12.0", {"position": v(158.75, -4.23) * mm});
            skPoint(sketch, "E38.37.13.0", {"position": v(158.75, -10.58) * mm});
            skPoint(sketch, "E38.37.14.0", {"position": v(158.75, -16.93) * mm});
            skPoint(sketch, "E38.37.15.0", {"position": v(158.75, -23.28) * mm});
            skPoint(sketch, "E38.37.16.0", {"position": v(158.75, -29.63) * mm});
            skPoint(sketch, "E38.37.17.0", {"position": v(158.75, -35.98) * mm});
            skPoint(sketch, "E38.37.18.0", {"position": v(158.75, -42.33) * mm});
            skPoint(sketch, "E38.37.19.0", {"position": v(158.75, -48.68) * mm});
            skPoint(sketch, "E38.37.20.0", {"position": v(158.75, -55.03) * mm});
            skPoint(sketch, "E38.37.21.0", {"position": v(158.75, -61.38) * mm});
            skPoint(sketch, "E38.37.22.0", {"position": v(158.75, -67.73) * mm});
            skPoint(sketch, "E38.37.23.0", {"position": v(158.75, -74.08) * mm});
            skPoint(sketch, "E38.37.24.0", {"position": v(158.75, -80.43) * mm});
            skPoint(sketch, "E38.37.25.0", {"position": v(158.75, -86.78) * mm});
            skPoint(sketch, "E38.37.26.0", {"position": v(158.75, -93.13) * mm});
            skPoint(sketch, "E38.37.27.0", {"position": v(158.75, -99.48) * mm});
            skPoint(sketch, "E38.37.28.0", {"position": v(158.75, -105.83) * mm});
            skPoint(sketch, "E38.37.29.0", {"position": v(158.75, -112.18) * mm});
            skPoint(sketch, "E38.37.30.0", {"position": v(158.75, -118.53) * mm});
            skPoint(sketch, "E38.37.31.0", {"position": v(158.75, -124.88) * mm});
            skPoint(sketch, "E38.37.32.0", {"position": v(158.75, -131.23) * mm});
            skPoint(sketch, "E38.37.33.0", {"position": v(158.75, -137.58) * mm});
            skPoint(sketch, "E38.37.34.0", {"position": v(158.75, -143.93) * mm});
            skPoint(sketch, "E38.37.35.0", {"position": v(158.75, -150.28) * mm});
            skPoint(sketch, "E38.37.36.0", {"position": v(158.75, -156.63) * mm});
            skPoint(sketch, "E38.37.37.0", {"position": v(158.75, -162.98) * mm});
            skPoint(sketch, "E38.37.38.0", {"position": v(158.75, -169.33) * mm});
            skPoint(sketch, "E38.37.39.0", {"position": v(158.75, -175.68) * mm});
            skPoint(sketch, "E38.37.40.0", {"position": v(158.75, -182.03) * mm});
            skPoint(sketch, "E38.37.41.0", {"position": v(158.75, -188.38) * mm});
            skPoint(sketch, "E38.37.42.0", {"position": v(158.75, -194.73) * mm});
            skPoint(sketch, "E38.37.43.0", {"position": v(158.75, -201.08) * mm});
            skPoint(sketch, "E38.37.44.0", {"position": v(158.75, -207.43) * mm});
            skPoint(sketch, "E38.37.45.0", {"position": v(158.75, -213.78) * mm});
            skPoint(sketch, "E38.37.46.0", {"position": v(158.75, -220.13) * mm});
            skPoint(sketch, "E38.37.47.0", {"position": v(158.75, -226.48) * mm});
            skPoint(sketch, "E38.37.48.0", {"position": v(158.75, -232.83) * mm});
            skPoint(sketch, "E38.37.49.0", {"position": v(158.75, -239.18) * mm});
            skPoint(sketch, "E38.37.50.0", {"position": v(158.75, -245.53) * mm});
            skPoint(sketch, "E38.37.51.0", {"position": v(158.75, -251.88) * mm});
            skPoint(sketch, "E38.37.52.0", {"position": v(158.75, -258.23) * mm});
            skPoint(sketch, "E38.37.53.0", {"position": v(158.75, -264.58) * mm});
            skPoint(sketch, "E38.37.54.0", {"position": v(158.75, -270.93) * mm});
            skPoint(sketch, "E38.37.55.0", {"position": v(158.75, -277.28) * mm});
            skPoint(sketch, "E38.37.56.0", {"position": v(158.75, -283.63) * mm});
            skPoint(sketch, "E38.37.57.0", {"position": v(158.75, -289.98) * mm});
            skPoint(sketch, "E38.37.58.0", {"position": v(158.75, -296.33) * mm});
            skPoint(sketch, "E38.37.59.0", {"position": v(158.75, -302.68) * mm});
            skPoint(sketch, "E38.37.60.0", {"position": v(158.75, -309.03) * mm});
            skPoint(sketch, "E38.37.61.0", {"position": v(158.75, -315.38) * mm});
            skPoint(sketch, "E38.37.62.0", {"position": v(158.75, -321.73) * mm});
            skPoint(sketch, "E38.37.63.0", {"position": v(158.75, -328.08) * mm});
            skPoint(sketch, "E38.37.64.0", {"position": v(158.75, -334.43) * mm});
            skPoint(sketch, "E38.37.65.0", {"position": v(158.75, -340.78) * mm});
            skPoint(sketch, "E38.37.66.0", {"position": v(158.75, -347.13) * mm});
            skPoint(sketch, "E38.37.67.0", {"position": v(158.75, -353.48) * mm});
            skPoint(sketch, "E38.37.68.0", {"position": v(158.75, -359.83) * mm});
            skPoint(sketch, "E38.37.69.0", {"position": v(158.75, -366.18) * mm});
            skPoint(sketch, "E38.37.70.0", {"position": v(158.75, -372.53) * mm});
            skPoint(sketch, "E38.37.71.0", {"position": v(158.75, -378.88) * mm});
            skPoint(sketch, "E38.37.72.0", {"position": v(158.75, -385.23) * mm});
            skPoint(sketch, "E38.37.73.0", {"position": v(158.75, -391.58) * mm});
            skPoint(sketch, "E38.37.74.0", {"position": v(158.75, -397.93) * mm});
            skPoint(sketch, "E38.37.75.0", {"position": v(158.75, -404.28) * mm});
            skPoint(sketch, "E38.37.76.0", {"position": v(158.75, -410.63) * mm});
            skPoint(sketch, "E38.37.77.0", {"position": v(158.75, -416.98) * mm});
            skPoint(sketch, "E38.37.78.0", {"position": v(158.75, -423.33) * mm});
            skPoint(sketch, "E38.37.79.0", {"position": v(158.75, -429.68) * mm});
            skPoint(sketch, "E38.37.80.0", {"position": v(158.75, -436.03) * mm});
            skPoint(sketch, "E38.37.81.0", {"position": v(158.75, -442.38) * mm});
            skPoint(sketch, "E38.37.82.0", {"position": v(158.75, -448.73) * mm});
            skPoint(sketch, "E38.37.83.0", {"position": v(158.75, -455.08) * mm});
            skPoint(sketch, "E38.37.84.0", {"position": v(158.75, -461.43) * mm});
            skPoint(sketch, "E38.37.85.0", {"position": v(158.75, -467.78) * mm});
            skPoint(sketch, "E38.37.86.0", {"position": v(158.75, -474.13) * mm});
            skPoint(sketch, "E38.37.87.0", {"position": v(158.75, -480.48) * mm});
            skPoint(sketch, "E38.37.88.0", {"position": v(158.75, -486.83) * mm});
            skPoint(sketch, "E38.37.89.0", {"position": v(158.75, -493.18) * mm});
            skPoint(sketch, "E38.37.90.0", {"position": v(158.75, -499.53) * mm});
            skPoint(sketch, "E38.37.91.0", {"position": v(158.75, -505.88) * mm});
            skPoint(sketch, "E38.37.92.0", {"position": v(158.75, -512.23) * mm});
            skPoint(sketch, "E38.37.93.0", {"position": v(158.75, -518.58) * mm});
            skPoint(sketch, "E38.37.94.0", {"position": v(158.75, -524.93) * mm});
            skPoint(sketch, "E38.37.95.0", {"position": v(158.75, -531.28) * mm});
            skPoint(sketch, "E38.37.96.0", {"position": v(158.75, -537.63) * mm});
            skPoint(sketch, "E38.37.97.0", {"position": v(158.75, -543.98) * mm});
            skPoint(sketch, "E38.37.98.0", {"position": v(158.75, -550.33) * mm});
            skPoint(sketch, "E38.37.99.0", {"position": v(158.75, -556.68) * mm});
            skPoint(sketch, "E38.38.0.0", {"position": v(165.1, 71.97) * mm});
            skPoint(sketch, "E38.38.1.0", {"position": v(165.1, 65.62) * mm});
            skPoint(sketch, "E38.38.2.0", {"position": v(165.1, 59.27) * mm});
            skPoint(sketch, "E38.38.3.0", {"position": v(165.1, 52.92) * mm});
            skPoint(sketch, "E38.38.4.0", {"position": v(165.1, 46.57) * mm});
            skPoint(sketch, "E38.38.5.0", {"position": v(165.1, 40.22) * mm});
            skPoint(sketch, "E38.38.6.0", {"position": v(165.1, 33.87) * mm});
            skPoint(sketch, "E38.38.7.0", {"position": v(165.1, 27.52) * mm});
            skPoint(sketch, "E38.38.8.0", {"position": v(165.1, 21.17) * mm});
            skPoint(sketch, "E38.38.9.0", {"position": v(165.1, 14.82) * mm});
            skPoint(sketch, "E38.38.10.0", {"position": v(165.1, 8.47) * mm});
            skPoint(sketch, "E38.38.11.0", {"position": v(165.1, 2.12) * mm});
            skPoint(sketch, "E38.38.12.0", {"position": v(165.1, -4.23) * mm});
            skPoint(sketch, "E38.38.13.0", {"position": v(165.1, -10.58) * mm});
            skPoint(sketch, "E38.38.14.0", {"position": v(165.1, -16.93) * mm});
            skPoint(sketch, "E38.38.15.0", {"position": v(165.1, -23.28) * mm});
            skPoint(sketch, "E38.38.16.0", {"position": v(165.1, -29.63) * mm});
            skPoint(sketch, "E38.38.17.0", {"position": v(165.1, -35.98) * mm});
            skPoint(sketch, "E38.38.18.0", {"position": v(165.1, -42.33) * mm});
            skPoint(sketch, "E38.38.19.0", {"position": v(165.1, -48.68) * mm});
            skPoint(sketch, "E38.38.20.0", {"position": v(165.1, -55.03) * mm});
            skPoint(sketch, "E38.38.21.0", {"position": v(165.1, -61.38) * mm});
            skPoint(sketch, "E38.38.22.0", {"position": v(165.1, -67.73) * mm});
            skPoint(sketch, "E38.38.23.0", {"position": v(165.1, -74.08) * mm});
            skPoint(sketch, "E38.38.24.0", {"position": v(165.1, -80.43) * mm});
            skPoint(sketch, "E38.38.25.0", {"position": v(165.1, -86.78) * mm});
            skPoint(sketch, "E38.38.26.0", {"position": v(165.1, -93.13) * mm});
            skPoint(sketch, "E38.38.27.0", {"position": v(165.1, -99.48) * mm});
            skPoint(sketch, "E38.38.28.0", {"position": v(165.1, -105.83) * mm});
            skPoint(sketch, "E38.38.29.0", {"position": v(165.1, -112.18) * mm});
            skPoint(sketch, "E38.38.30.0", {"position": v(165.1, -118.53) * mm});
            skPoint(sketch, "E38.38.31.0", {"position": v(165.1, -124.88) * mm});
            skPoint(sketch, "E38.38.32.0", {"position": v(165.1, -131.23) * mm});
            skPoint(sketch, "E38.38.33.0", {"position": v(165.1, -137.58) * mm});
            skPoint(sketch, "E38.38.34.0", {"position": v(165.1, -143.93) * mm});
            skPoint(sketch, "E38.38.35.0", {"position": v(165.1, -150.28) * mm});
            skPoint(sketch, "E38.38.36.0", {"position": v(165.1, -156.63) * mm});
            skPoint(sketch, "E38.38.37.0", {"position": v(165.1, -162.98) * mm});
            skPoint(sketch, "E38.38.38.0", {"position": v(165.1, -169.33) * mm});
            skPoint(sketch, "E38.38.39.0", {"position": v(165.1, -175.68) * mm});
            skPoint(sketch, "E38.38.40.0", {"position": v(165.1, -182.03) * mm});
            skPoint(sketch, "E38.38.41.0", {"position": v(165.1, -188.38) * mm});
            skPoint(sketch, "E38.38.42.0", {"position": v(165.1, -194.73) * mm});
            skPoint(sketch, "E38.38.43.0", {"position": v(165.1, -201.08) * mm});
            skPoint(sketch, "E38.38.44.0", {"position": v(165.1, -207.43) * mm});
            skPoint(sketch, "E38.38.45.0", {"position": v(165.1, -213.78) * mm});
            skPoint(sketch, "E38.38.46.0", {"position": v(165.1, -220.13) * mm});
            skPoint(sketch, "E38.38.47.0", {"position": v(165.1, -226.48) * mm});
            skPoint(sketch, "E38.38.48.0", {"position": v(165.1, -232.83) * mm});
            skPoint(sketch, "E38.38.49.0", {"position": v(165.1, -239.18) * mm});
            skPoint(sketch, "E38.38.50.0", {"position": v(165.1, -245.53) * mm});
            skPoint(sketch, "E38.38.51.0", {"position": v(165.1, -251.88) * mm});
            skPoint(sketch, "E38.38.52.0", {"position": v(165.1, -258.23) * mm});
            skPoint(sketch, "E38.38.53.0", {"position": v(165.1, -264.58) * mm});
            skPoint(sketch, "E38.38.54.0", {"position": v(165.1, -270.93) * mm});
            skPoint(sketch, "E38.38.55.0", {"position": v(165.1, -277.28) * mm});
            skPoint(sketch, "E38.38.56.0", {"position": v(165.1, -283.63) * mm});
            skPoint(sketch, "E38.38.57.0", {"position": v(165.1, -289.98) * mm});
            skPoint(sketch, "E38.38.58.0", {"position": v(165.1, -296.33) * mm});
            skPoint(sketch, "E38.38.59.0", {"position": v(165.1, -302.68) * mm});
            skPoint(sketch, "E38.38.60.0", {"position": v(165.1, -309.03) * mm});
            skPoint(sketch, "E38.38.61.0", {"position": v(165.1, -315.38) * mm});
            skPoint(sketch, "E38.38.62.0", {"position": v(165.1, -321.73) * mm});
            skPoint(sketch, "E38.38.63.0", {"position": v(165.1, -328.08) * mm});
            skPoint(sketch, "E38.38.64.0", {"position": v(165.1, -334.43) * mm});
            skPoint(sketch, "E38.38.65.0", {"position": v(165.1, -340.78) * mm});
            skPoint(sketch, "E38.38.66.0", {"position": v(165.1, -347.13) * mm});
            skPoint(sketch, "E38.38.67.0", {"position": v(165.1, -353.48) * mm});
            skPoint(sketch, "E38.38.68.0", {"position": v(165.1, -359.83) * mm});
            skPoint(sketch, "E38.38.69.0", {"position": v(165.1, -366.18) * mm});
            skPoint(sketch, "E38.38.70.0", {"position": v(165.1, -372.53) * mm});
            skPoint(sketch, "E38.38.71.0", {"position": v(165.1, -378.88) * mm});
            skPoint(sketch, "E38.38.72.0", {"position": v(165.1, -385.23) * mm});
            skPoint(sketch, "E38.38.73.0", {"position": v(165.1, -391.58) * mm});
            skPoint(sketch, "E38.38.74.0", {"position": v(165.1, -397.93) * mm});
            skPoint(sketch, "E38.38.75.0", {"position": v(165.1, -404.28) * mm});
            skPoint(sketch, "E38.38.76.0", {"position": v(165.1, -410.63) * mm});
            skPoint(sketch, "E38.38.77.0", {"position": v(165.1, -416.98) * mm});
            skPoint(sketch, "E38.38.78.0", {"position": v(165.1, -423.33) * mm});
            skPoint(sketch, "E38.38.79.0", {"position": v(165.1, -429.68) * mm});
            skPoint(sketch, "E38.38.80.0", {"position": v(165.1, -436.03) * mm});
            skPoint(sketch, "E38.38.81.0", {"position": v(165.1, -442.38) * mm});
            skPoint(sketch, "E38.38.82.0", {"position": v(165.1, -448.73) * mm});
            skPoint(sketch, "E38.38.83.0", {"position": v(165.1, -455.08) * mm});
            skPoint(sketch, "E38.38.84.0", {"position": v(165.1, -461.43) * mm});
            skPoint(sketch, "E38.38.85.0", {"position": v(165.1, -467.78) * mm});
            skPoint(sketch, "E38.38.86.0", {"position": v(165.1, -474.13) * mm});
            skPoint(sketch, "E38.38.87.0", {"position": v(165.1, -480.48) * mm});
            skPoint(sketch, "E38.38.88.0", {"position": v(165.1, -486.83) * mm});
            skPoint(sketch, "E38.38.89.0", {"position": v(165.1, -493.18) * mm});
            skPoint(sketch, "E38.38.90.0", {"position": v(165.1, -499.53) * mm});
            skPoint(sketch, "E38.38.91.0", {"position": v(165.1, -505.88) * mm});
            skPoint(sketch, "E38.38.92.0", {"position": v(165.1, -512.23) * mm});
            skPoint(sketch, "E38.38.93.0", {"position": v(165.1, -518.58) * mm});
            skPoint(sketch, "E38.38.94.0", {"position": v(165.1, -524.93) * mm});
            skPoint(sketch, "E38.38.95.0", {"position": v(165.1, -531.28) * mm});
            skPoint(sketch, "E38.38.96.0", {"position": v(165.1, -537.63) * mm});
            skPoint(sketch, "E38.38.97.0", {"position": v(165.1, -543.98) * mm});
            skPoint(sketch, "E38.38.98.0", {"position": v(165.1, -550.33) * mm});
            skPoint(sketch, "E38.38.99.0", {"position": v(165.1, -556.68) * mm});
            skPoint(sketch, "E38.39.0.0", {"position": v(171.45, 71.97) * mm});
            skPoint(sketch, "E38.39.1.0", {"position": v(171.45, 65.62) * mm});
            skPoint(sketch, "E38.39.2.0", {"position": v(171.45, 59.27) * mm});
            skPoint(sketch, "E38.39.3.0", {"position": v(171.45, 52.92) * mm});
            skPoint(sketch, "E38.39.4.0", {"position": v(171.45, 46.57) * mm});
            skPoint(sketch, "E38.39.5.0", {"position": v(171.45, 40.22) * mm});
            skPoint(sketch, "E38.39.6.0", {"position": v(171.45, 33.87) * mm});
            skPoint(sketch, "E38.39.7.0", {"position": v(171.45, 27.52) * mm});
            skPoint(sketch, "E38.39.8.0", {"position": v(171.45, 21.17) * mm});
            skPoint(sketch, "E38.39.9.0", {"position": v(171.45, 14.82) * mm});
            skPoint(sketch, "E38.39.10.0", {"position": v(171.45, 8.47) * mm});
            skPoint(sketch, "E38.39.11.0", {"position": v(171.45, 2.12) * mm});
            skPoint(sketch, "E38.39.12.0", {"position": v(171.45, -4.23) * mm});
            skPoint(sketch, "E38.39.13.0", {"position": v(171.45, -10.58) * mm});
            skPoint(sketch, "E38.39.14.0", {"position": v(171.45, -16.93) * mm});
            skPoint(sketch, "E38.39.15.0", {"position": v(171.45, -23.28) * mm});
            skPoint(sketch, "E38.39.16.0", {"position": v(171.45, -29.63) * mm});
            skPoint(sketch, "E38.39.17.0", {"position": v(171.45, -35.98) * mm});
            skPoint(sketch, "E38.39.18.0", {"position": v(171.45, -42.33) * mm});
            skPoint(sketch, "E38.39.19.0", {"position": v(171.45, -48.68) * mm});
            skPoint(sketch, "E38.39.20.0", {"position": v(171.45, -55.03) * mm});
            skPoint(sketch, "E38.39.21.0", {"position": v(171.45, -61.38) * mm});
            skPoint(sketch, "E38.39.22.0", {"position": v(171.45, -67.73) * mm});
            skPoint(sketch, "E38.39.23.0", {"position": v(171.45, -74.08) * mm});
            skPoint(sketch, "E38.39.24.0", {"position": v(171.45, -80.43) * mm});
            skPoint(sketch, "E38.39.25.0", {"position": v(171.45, -86.78) * mm});
            skPoint(sketch, "E38.39.26.0", {"position": v(171.45, -93.13) * mm});
            skPoint(sketch, "E38.39.27.0", {"position": v(171.45, -99.48) * mm});
            skPoint(sketch, "E38.39.28.0", {"position": v(171.45, -105.83) * mm});
            skPoint(sketch, "E38.39.29.0", {"position": v(171.45, -112.18) * mm});
            skPoint(sketch, "E38.39.30.0", {"position": v(171.45, -118.53) * mm});
            skPoint(sketch, "E38.39.31.0", {"position": v(171.45, -124.88) * mm});
            skPoint(sketch, "E38.39.32.0", {"position": v(171.45, -131.23) * mm});
            skPoint(sketch, "E38.39.33.0", {"position": v(171.45, -137.58) * mm});
            skPoint(sketch, "E38.39.34.0", {"position": v(171.45, -143.93) * mm});
            skPoint(sketch, "E38.39.35.0", {"position": v(171.45, -150.28) * mm});
            skPoint(sketch, "E38.39.36.0", {"position": v(171.45, -156.63) * mm});
            skPoint(sketch, "E38.39.37.0", {"position": v(171.45, -162.98) * mm});
            skPoint(sketch, "E38.39.38.0", {"position": v(171.45, -169.33) * mm});
            skPoint(sketch, "E38.39.39.0", {"position": v(171.45, -175.68) * mm});
            skPoint(sketch, "E38.39.40.0", {"position": v(171.45, -182.03) * mm});
            skPoint(sketch, "E38.39.41.0", {"position": v(171.45, -188.38) * mm});
            skPoint(sketch, "E38.39.42.0", {"position": v(171.45, -194.73) * mm});
            skPoint(sketch, "E38.39.43.0", {"position": v(171.45, -201.08) * mm});
            skPoint(sketch, "E38.39.44.0", {"position": v(171.45, -207.43) * mm});
            skPoint(sketch, "E38.39.45.0", {"position": v(171.45, -213.78) * mm});
            skPoint(sketch, "E38.39.46.0", {"position": v(171.45, -220.13) * mm});
            skPoint(sketch, "E38.39.47.0", {"position": v(171.45, -226.48) * mm});
            skPoint(sketch, "E38.39.48.0", {"position": v(171.45, -232.83) * mm});
            skPoint(sketch, "E38.39.49.0", {"position": v(171.45, -239.18) * mm});
            skPoint(sketch, "E38.39.50.0", {"position": v(171.45, -245.53) * mm});
            skPoint(sketch, "E38.39.51.0", {"position": v(171.45, -251.88) * mm});
            skPoint(sketch, "E38.39.52.0", {"position": v(171.45, -258.23) * mm});
            skPoint(sketch, "E38.39.53.0", {"position": v(171.45, -264.58) * mm});
            skPoint(sketch, "E38.39.54.0", {"position": v(171.45, -270.93) * mm});
            skPoint(sketch, "E38.39.55.0", {"position": v(171.45, -277.28) * mm});
            skPoint(sketch, "E38.39.56.0", {"position": v(171.45, -283.63) * mm});
            skPoint(sketch, "E38.39.57.0", {"position": v(171.45, -289.98) * mm});
            skPoint(sketch, "E38.39.58.0", {"position": v(171.45, -296.33) * mm});
            skPoint(sketch, "E38.39.59.0", {"position": v(171.45, -302.68) * mm});
            skPoint(sketch, "E38.39.60.0", {"position": v(171.45, -309.03) * mm});
            skPoint(sketch, "E38.39.61.0", {"position": v(171.45, -315.38) * mm});
            skPoint(sketch, "E38.39.62.0", {"position": v(171.45, -321.73) * mm});
            skPoint(sketch, "E38.39.63.0", {"position": v(171.45, -328.08) * mm});
            skPoint(sketch, "E38.39.64.0", {"position": v(171.45, -334.43) * mm});
            skPoint(sketch, "E38.39.65.0", {"position": v(171.45, -340.78) * mm});
            skPoint(sketch, "E38.39.66.0", {"position": v(171.45, -347.13) * mm});
            skPoint(sketch, "E38.39.67.0", {"position": v(171.45, -353.48) * mm});
            skPoint(sketch, "E38.39.68.0", {"position": v(171.45, -359.83) * mm});
            skPoint(sketch, "E38.39.69.0", {"position": v(171.45, -366.18) * mm});
            skPoint(sketch, "E38.39.70.0", {"position": v(171.45, -372.53) * mm});
            skPoint(sketch, "E38.39.71.0", {"position": v(171.45, -378.88) * mm});
            skPoint(sketch, "E38.39.72.0", {"position": v(171.45, -385.23) * mm});
            skPoint(sketch, "E38.39.73.0", {"position": v(171.45, -391.58) * mm});
            skPoint(sketch, "E38.39.74.0", {"position": v(171.45, -397.93) * mm});
            skPoint(sketch, "E38.39.75.0", {"position": v(171.45, -404.28) * mm});
            skPoint(sketch, "E38.39.76.0", {"position": v(171.45, -410.63) * mm});
            skPoint(sketch, "E38.39.77.0", {"position": v(171.45, -416.98) * mm});
            skPoint(sketch, "E38.39.78.0", {"position": v(171.45, -423.33) * mm});
            skPoint(sketch, "E38.39.79.0", {"position": v(171.45, -429.68) * mm});
            skPoint(sketch, "E38.39.80.0", {"position": v(171.45, -436.03) * mm});
            skPoint(sketch, "E38.39.81.0", {"position": v(171.45, -442.38) * mm});
            skPoint(sketch, "E38.39.82.0", {"position": v(171.45, -448.73) * mm});
            skPoint(sketch, "E38.39.83.0", {"position": v(171.45, -455.08) * mm});
            skPoint(sketch, "E38.39.84.0", {"position": v(171.45, -461.43) * mm});
            skPoint(sketch, "E38.39.85.0", {"position": v(171.45, -467.78) * mm});
            skPoint(sketch, "E38.39.86.0", {"position": v(171.45, -474.13) * mm});
            skPoint(sketch, "E38.39.87.0", {"position": v(171.45, -480.48) * mm});
            skPoint(sketch, "E38.39.88.0", {"position": v(171.45, -486.83) * mm});
            skPoint(sketch, "E38.39.89.0", {"position": v(171.45, -493.18) * mm});
            skPoint(sketch, "E38.39.90.0", {"position": v(171.45, -499.53) * mm});
            skPoint(sketch, "E38.39.91.0", {"position": v(171.45, -505.88) * mm});
            skPoint(sketch, "E38.39.92.0", {"position": v(171.45, -512.23) * mm});
            skPoint(sketch, "E38.39.93.0", {"position": v(171.45, -518.58) * mm});
            skPoint(sketch, "E38.39.94.0", {"position": v(171.45, -524.93) * mm});
            skPoint(sketch, "E38.39.95.0", {"position": v(171.45, -531.28) * mm});
            skPoint(sketch, "E38.39.96.0", {"position": v(171.45, -537.63) * mm});
            skPoint(sketch, "E38.39.97.0", {"position": v(171.45, -543.98) * mm});
            skPoint(sketch, "E38.39.98.0", {"position": v(171.45, -550.33) * mm});
            skPoint(sketch, "E38.39.99.0", {"position": v(171.45, -556.68) * mm});
            skPoint(sketch, "E38.40.0.0", {"position": v(177.8, 71.97) * mm});
            skPoint(sketch, "E38.40.1.0", {"position": v(177.8, 65.62) * mm});
            skPoint(sketch, "E38.40.2.0", {"position": v(177.8, 59.27) * mm});
            skPoint(sketch, "E38.40.3.0", {"position": v(177.8, 52.92) * mm});
            skPoint(sketch, "E38.40.4.0", {"position": v(177.8, 46.57) * mm});
            skPoint(sketch, "E38.40.5.0", {"position": v(177.8, 40.22) * mm});
            skPoint(sketch, "E38.40.6.0", {"position": v(177.8, 33.87) * mm});
            skPoint(sketch, "E38.40.7.0", {"position": v(177.8, 27.52) * mm});
            skPoint(sketch, "E38.40.8.0", {"position": v(177.8, 21.17) * mm});
            skPoint(sketch, "E38.40.9.0", {"position": v(177.8, 14.82) * mm});
            skPoint(sketch, "E38.40.10.0", {"position": v(177.8, 8.47) * mm});
            skPoint(sketch, "E38.40.11.0", {"position": v(177.8, 2.12) * mm});
            skPoint(sketch, "E38.40.12.0", {"position": v(177.8, -4.23) * mm});
            skPoint(sketch, "E38.40.13.0", {"position": v(177.8, -10.58) * mm});
            skPoint(sketch, "E38.40.14.0", {"position": v(177.8, -16.93) * mm});
            skPoint(sketch, "E38.40.15.0", {"position": v(177.8, -23.28) * mm});
            skPoint(sketch, "E38.40.16.0", {"position": v(177.8, -29.63) * mm});
            skPoint(sketch, "E38.40.17.0", {"position": v(177.8, -35.98) * mm});
            skPoint(sketch, "E38.40.18.0", {"position": v(177.8, -42.33) * mm});
            skPoint(sketch, "E38.40.19.0", {"position": v(177.8, -48.68) * mm});
            skPoint(sketch, "E38.40.20.0", {"position": v(177.8, -55.03) * mm});
            skPoint(sketch, "E38.40.21.0", {"position": v(177.8, -61.38) * mm});
            skPoint(sketch, "E38.40.22.0", {"position": v(177.8, -67.73) * mm});
            skPoint(sketch, "E38.40.23.0", {"position": v(177.8, -74.08) * mm});
            skPoint(sketch, "E38.40.24.0", {"position": v(177.8, -80.43) * mm});
            skPoint(sketch, "E38.40.25.0", {"position": v(177.8, -86.78) * mm});
            skPoint(sketch, "E38.40.26.0", {"position": v(177.8, -93.13) * mm});
            skPoint(sketch, "E38.40.27.0", {"position": v(177.8, -99.48) * mm});
            skPoint(sketch, "E38.40.28.0", {"position": v(177.8, -105.83) * mm});
            skPoint(sketch, "E38.40.29.0", {"position": v(177.8, -112.18) * mm});
            skPoint(sketch, "E38.40.30.0", {"position": v(177.8, -118.53) * mm});
            skPoint(sketch, "E38.40.31.0", {"position": v(177.8, -124.88) * mm});
            skPoint(sketch, "E38.40.32.0", {"position": v(177.8, -131.23) * mm});
            skPoint(sketch, "E38.40.33.0", {"position": v(177.8, -137.58) * mm});
            skPoint(sketch, "E38.40.34.0", {"position": v(177.8, -143.93) * mm});
            skPoint(sketch, "E38.40.35.0", {"position": v(177.8, -150.28) * mm});
            skPoint(sketch, "E38.40.36.0", {"position": v(177.8, -156.63) * mm});
            skPoint(sketch, "E38.40.37.0", {"position": v(177.8, -162.98) * mm});
            skPoint(sketch, "E38.40.38.0", {"position": v(177.8, -169.33) * mm});
            skPoint(sketch, "E38.40.39.0", {"position": v(177.8, -175.68) * mm});
            skPoint(sketch, "E38.40.40.0", {"position": v(177.8, -182.03) * mm});
            skPoint(sketch, "E38.40.41.0", {"position": v(177.8, -188.38) * mm});
            skPoint(sketch, "E38.40.42.0", {"position": v(177.8, -194.73) * mm});
            skPoint(sketch, "E38.40.43.0", {"position": v(177.8, -201.08) * mm});
            skPoint(sketch, "E38.40.44.0", {"position": v(177.8, -207.43) * mm});
            skPoint(sketch, "E38.40.45.0", {"position": v(177.8, -213.78) * mm});
            skPoint(sketch, "E38.40.46.0", {"position": v(177.8, -220.13) * mm});
            skPoint(sketch, "E38.40.47.0", {"position": v(177.8, -226.48) * mm});
            skPoint(sketch, "E38.40.48.0", {"position": v(177.8, -232.83) * mm});
            skPoint(sketch, "E38.40.49.0", {"position": v(177.8, -239.18) * mm});
            skPoint(sketch, "E38.40.50.0", {"position": v(177.8, -245.53) * mm});
            skPoint(sketch, "E38.40.51.0", {"position": v(177.8, -251.88) * mm});
            skPoint(sketch, "E38.40.52.0", {"position": v(177.8, -258.23) * mm});
            skPoint(sketch, "E38.40.53.0", {"position": v(177.8, -264.58) * mm});
            skPoint(sketch, "E38.40.54.0", {"position": v(177.8, -270.93) * mm});
            skPoint(sketch, "E38.40.55.0", {"position": v(177.8, -277.28) * mm});
            skPoint(sketch, "E38.40.56.0", {"position": v(177.8, -283.63) * mm});
            skPoint(sketch, "E38.40.57.0", {"position": v(177.8, -289.98) * mm});
            skPoint(sketch, "E38.40.58.0", {"position": v(177.8, -296.33) * mm});
            skPoint(sketch, "E38.40.59.0", {"position": v(177.8, -302.68) * mm});
            skPoint(sketch, "E38.40.60.0", {"position": v(177.8, -309.03) * mm});
            skPoint(sketch, "E38.40.61.0", {"position": v(177.8, -315.38) * mm});
            skPoint(sketch, "E38.40.62.0", {"position": v(177.8, -321.73) * mm});
            skPoint(sketch, "E38.40.63.0", {"position": v(177.8, -328.08) * mm});
            skPoint(sketch, "E38.40.64.0", {"position": v(177.8, -334.43) * mm});
            skPoint(sketch, "E38.40.65.0", {"position": v(177.8, -340.78) * mm});
            skPoint(sketch, "E38.40.66.0", {"position": v(177.8, -347.13) * mm});
            skPoint(sketch, "E38.40.67.0", {"position": v(177.8, -353.48) * mm});
            skPoint(sketch, "E38.40.68.0", {"position": v(177.8, -359.83) * mm});
            skPoint(sketch, "E38.40.69.0", {"position": v(177.8, -366.18) * mm});
            skPoint(sketch, "E38.40.70.0", {"position": v(177.8, -372.53) * mm});
            skPoint(sketch, "E38.40.71.0", {"position": v(177.8, -378.88) * mm});
            skPoint(sketch, "E38.40.72.0", {"position": v(177.8, -385.23) * mm});
            skPoint(sketch, "E38.40.73.0", {"position": v(177.8, -391.58) * mm});
            skPoint(sketch, "E38.40.74.0", {"position": v(177.8, -397.93) * mm});
            skPoint(sketch, "E38.40.75.0", {"position": v(177.8, -404.28) * mm});
            skPoint(sketch, "E38.40.76.0", {"position": v(177.8, -410.63) * mm});
            skPoint(sketch, "E38.40.77.0", {"position": v(177.8, -416.98) * mm});
            skPoint(sketch, "E38.40.78.0", {"position": v(177.8, -423.33) * mm});
            skPoint(sketch, "E38.40.79.0", {"position": v(177.8, -429.68) * mm});
            skPoint(sketch, "E38.40.80.0", {"position": v(177.8, -436.03) * mm});
            skPoint(sketch, "E38.40.81.0", {"position": v(177.8, -442.38) * mm});
            skPoint(sketch, "E38.40.82.0", {"position": v(177.8, -448.73) * mm});
            skPoint(sketch, "E38.40.83.0", {"position": v(177.8, -455.08) * mm});
            skPoint(sketch, "E38.40.84.0", {"position": v(177.8, -461.43) * mm});
            skPoint(sketch, "E38.40.85.0", {"position": v(177.8, -467.78) * mm});
            skPoint(sketch, "E38.40.86.0", {"position": v(177.8, -474.13) * mm});
            skPoint(sketch, "E38.40.87.0", {"position": v(177.8, -480.48) * mm});
            skPoint(sketch, "E38.40.88.0", {"position": v(177.8, -486.83) * mm});
            skPoint(sketch, "E38.40.89.0", {"position": v(177.8, -493.18) * mm});
            skPoint(sketch, "E38.40.90.0", {"position": v(177.8, -499.53) * mm});
            skPoint(sketch, "E38.40.91.0", {"position": v(177.8, -505.88) * mm});
            skPoint(sketch, "E38.40.92.0", {"position": v(177.8, -512.23) * mm});
            skPoint(sketch, "E38.40.93.0", {"position": v(177.8, -518.58) * mm});
            skPoint(sketch, "E38.40.94.0", {"position": v(177.8, -524.93) * mm});
            skPoint(sketch, "E38.40.95.0", {"position": v(177.8, -531.28) * mm});
            skPoint(sketch, "E38.40.96.0", {"position": v(177.8, -537.63) * mm});
            skPoint(sketch, "E38.40.97.0", {"position": v(177.8, -543.98) * mm});
            skPoint(sketch, "E38.40.98.0", {"position": v(177.8, -550.33) * mm});
            skPoint(sketch, "E38.40.99.0", {"position": v(177.8, -556.68) * mm});
            skPoint(sketch, "E38.41.0.0", {"position": v(184.15, 71.97) * mm});
            skPoint(sketch, "E38.41.1.0", {"position": v(184.15, 65.62) * mm});
            skPoint(sketch, "E38.41.2.0", {"position": v(184.15, 59.27) * mm});
            skPoint(sketch, "E38.41.3.0", {"position": v(184.15, 52.92) * mm});
            skPoint(sketch, "E38.41.4.0", {"position": v(184.15, 46.57) * mm});
            skPoint(sketch, "E38.41.5.0", {"position": v(184.15, 40.22) * mm});
            skPoint(sketch, "E38.41.6.0", {"position": v(184.15, 33.87) * mm});
            skPoint(sketch, "E38.41.7.0", {"position": v(184.15, 27.52) * mm});
            skPoint(sketch, "E38.41.8.0", {"position": v(184.15, 21.17) * mm});
            skPoint(sketch, "E38.41.9.0", {"position": v(184.15, 14.82) * mm});
            skPoint(sketch, "E38.41.10.0", {"position": v(184.15, 8.47) * mm});
            skPoint(sketch, "E38.41.11.0", {"position": v(184.15, 2.12) * mm});
            skPoint(sketch, "E38.41.12.0", {"position": v(184.15, -4.23) * mm});
            skPoint(sketch, "E38.41.13.0", {"position": v(184.15, -10.58) * mm});
            skPoint(sketch, "E38.41.14.0", {"position": v(184.15, -16.93) * mm});
            skPoint(sketch, "E38.41.15.0", {"position": v(184.15, -23.28) * mm});
            skPoint(sketch, "E38.41.16.0", {"position": v(184.15, -29.63) * mm});
            skPoint(sketch, "E38.41.17.0", {"position": v(184.15, -35.98) * mm});
            skPoint(sketch, "E38.41.18.0", {"position": v(184.15, -42.33) * mm});
            skPoint(sketch, "E38.41.19.0", {"position": v(184.15, -48.68) * mm});
            skPoint(sketch, "E38.41.20.0", {"position": v(184.15, -55.03) * mm});
            skPoint(sketch, "E38.41.21.0", {"position": v(184.15, -61.38) * mm});
            skPoint(sketch, "E38.41.22.0", {"position": v(184.15, -67.73) * mm});
            skPoint(sketch, "E38.41.23.0", {"position": v(184.15, -74.08) * mm});
            skPoint(sketch, "E38.41.24.0", {"position": v(184.15, -80.43) * mm});
            skPoint(sketch, "E38.41.25.0", {"position": v(184.15, -86.78) * mm});
            skPoint(sketch, "E38.41.26.0", {"position": v(184.15, -93.13) * mm});
            skPoint(sketch, "E38.41.27.0", {"position": v(184.15, -99.48) * mm});
            skPoint(sketch, "E38.41.28.0", {"position": v(184.15, -105.83) * mm});
            skPoint(sketch, "E38.41.29.0", {"position": v(184.15, -112.18) * mm});
            skPoint(sketch, "E38.41.30.0", {"position": v(184.15, -118.53) * mm});
            skPoint(sketch, "E38.41.31.0", {"position": v(184.15, -124.88) * mm});
            skPoint(sketch, "E38.41.32.0", {"position": v(184.15, -131.23) * mm});
            skPoint(sketch, "E38.41.33.0", {"position": v(184.15, -137.58) * mm});
            skPoint(sketch, "E38.41.34.0", {"position": v(184.15, -143.93) * mm});
            skPoint(sketch, "E38.41.35.0", {"position": v(184.15, -150.28) * mm});
            skPoint(sketch, "E38.41.36.0", {"position": v(184.15, -156.63) * mm});
            skPoint(sketch, "E38.41.37.0", {"position": v(184.15, -162.98) * mm});
            skPoint(sketch, "E38.41.38.0", {"position": v(184.15, -169.33) * mm});
            skPoint(sketch, "E38.41.39.0", {"position": v(184.15, -175.68) * mm});
            skPoint(sketch, "E38.41.40.0", {"position": v(184.15, -182.03) * mm});
            skPoint(sketch, "E38.41.41.0", {"position": v(184.15, -188.38) * mm});
            skPoint(sketch, "E38.41.42.0", {"position": v(184.15, -194.73) * mm});
            skPoint(sketch, "E38.41.43.0", {"position": v(184.15, -201.08) * mm});
            skPoint(sketch, "E38.41.44.0", {"position": v(184.15, -207.43) * mm});
            skPoint(sketch, "E38.41.45.0", {"position": v(184.15, -213.78) * mm});
            skPoint(sketch, "E38.41.46.0", {"position": v(184.15, -220.13) * mm});
            skPoint(sketch, "E38.41.47.0", {"position": v(184.15, -226.48) * mm});
            skPoint(sketch, "E38.41.48.0", {"position": v(184.15, -232.83) * mm});
            skPoint(sketch, "E38.41.49.0", {"position": v(184.15, -239.18) * mm});
            skPoint(sketch, "E38.41.50.0", {"position": v(184.15, -245.53) * mm});
            skPoint(sketch, "E38.41.51.0", {"position": v(184.15, -251.88) * mm});
            skPoint(sketch, "E38.41.52.0", {"position": v(184.15, -258.23) * mm});
            skPoint(sketch, "E38.41.53.0", {"position": v(184.15, -264.58) * mm});
            skPoint(sketch, "E38.41.54.0", {"position": v(184.15, -270.93) * mm});
            skPoint(sketch, "E38.41.55.0", {"position": v(184.15, -277.28) * mm});
            skPoint(sketch, "E38.41.56.0", {"position": v(184.15, -283.63) * mm});
            skPoint(sketch, "E38.41.57.0", {"position": v(184.15, -289.98) * mm});
            skPoint(sketch, "E38.41.58.0", {"position": v(184.15, -296.33) * mm});
            skPoint(sketch, "E38.41.59.0", {"position": v(184.15, -302.68) * mm});
            skPoint(sketch, "E38.41.60.0", {"position": v(184.15, -309.03) * mm});
            skPoint(sketch, "E38.41.61.0", {"position": v(184.15, -315.38) * mm});
            skPoint(sketch, "E38.41.62.0", {"position": v(184.15, -321.73) * mm});
            skPoint(sketch, "E38.41.63.0", {"position": v(184.15, -328.08) * mm});
            skPoint(sketch, "E38.41.64.0", {"position": v(184.15, -334.43) * mm});
            skPoint(sketch, "E38.41.65.0", {"position": v(184.15, -340.78) * mm});
            skPoint(sketch, "E38.41.66.0", {"position": v(184.15, -347.13) * mm});
            skPoint(sketch, "E38.41.67.0", {"position": v(184.15, -353.48) * mm});
            skPoint(sketch, "E38.41.68.0", {"position": v(184.15, -359.83) * mm});
            skPoint(sketch, "E38.41.69.0", {"position": v(184.15, -366.18) * mm});
            skPoint(sketch, "E38.41.70.0", {"position": v(184.15, -372.53) * mm});
            skPoint(sketch, "E38.41.71.0", {"position": v(184.15, -378.88) * mm});
            skPoint(sketch, "E38.41.72.0", {"position": v(184.15, -385.23) * mm});
            skPoint(sketch, "E38.41.73.0", {"position": v(184.15, -391.58) * mm});
            skPoint(sketch, "E38.41.74.0", {"position": v(184.15, -397.93) * mm});
            skPoint(sketch, "E38.41.75.0", {"position": v(184.15, -404.28) * mm});
            skPoint(sketch, "E38.41.76.0", {"position": v(184.15, -410.63) * mm});
            skPoint(sketch, "E38.41.77.0", {"position": v(184.15, -416.98) * mm});
            skPoint(sketch, "E38.41.78.0", {"position": v(184.15, -423.33) * mm});
            skPoint(sketch, "E38.41.79.0", {"position": v(184.15, -429.68) * mm});
            skPoint(sketch, "E38.41.80.0", {"position": v(184.15, -436.03) * mm});
            skPoint(sketch, "E38.41.81.0", {"position": v(184.15, -442.38) * mm});
            skPoint(sketch, "E38.41.82.0", {"position": v(184.15, -448.73) * mm});
            skPoint(sketch, "E38.41.83.0", {"position": v(184.15, -455.08) * mm});
            skPoint(sketch, "E38.41.84.0", {"position": v(184.15, -461.43) * mm});
            skPoint(sketch, "E38.41.85.0", {"position": v(184.15, -467.78) * mm});
            skPoint(sketch, "E38.41.86.0", {"position": v(184.15, -474.13) * mm});
            skPoint(sketch, "E38.41.87.0", {"position": v(184.15, -480.48) * mm});
            skPoint(sketch, "E38.41.88.0", {"position": v(184.15, -486.83) * mm});
            skPoint(sketch, "E38.41.89.0", {"position": v(184.15, -493.18) * mm});
            skPoint(sketch, "E38.41.90.0", {"position": v(184.15, -499.53) * mm});
            skPoint(sketch, "E38.41.91.0", {"position": v(184.15, -505.88) * mm});
            skPoint(sketch, "E38.41.92.0", {"position": v(184.15, -512.23) * mm});
            skPoint(sketch, "E38.41.93.0", {"position": v(184.15, -518.58) * mm});
            skPoint(sketch, "E38.41.94.0", {"position": v(184.15, -524.93) * mm});
            skPoint(sketch, "E38.41.95.0", {"position": v(184.15, -531.28) * mm});
            skPoint(sketch, "E38.41.96.0", {"position": v(184.15, -537.63) * mm});
            skPoint(sketch, "E38.41.97.0", {"position": v(184.15, -543.98) * mm});
            skPoint(sketch, "E38.41.98.0", {"position": v(184.15, -550.33) * mm});
            skPoint(sketch, "E38.41.99.0", {"position": v(184.15, -556.68) * mm});
            skPoint(sketch, "E38.42.0.0", {"position": v(190.5, 71.97) * mm});
            skPoint(sketch, "E38.42.1.0", {"position": v(190.5, 65.62) * mm});
            skPoint(sketch, "E38.42.2.0", {"position": v(190.5, 59.27) * mm});
            skPoint(sketch, "E38.42.3.0", {"position": v(190.5, 52.92) * mm});
            skPoint(sketch, "E38.42.4.0", {"position": v(190.5, 46.57) * mm});
            skPoint(sketch, "E38.42.5.0", {"position": v(190.5, 40.22) * mm});
            skPoint(sketch, "E38.42.6.0", {"position": v(190.5, 33.87) * mm});
            skPoint(sketch, "E38.42.7.0", {"position": v(190.5, 27.52) * mm});
            skPoint(sketch, "E38.42.8.0", {"position": v(190.5, 21.17) * mm});
            skPoint(sketch, "E38.42.9.0", {"position": v(190.5, 14.82) * mm});
            skPoint(sketch, "E38.42.10.0", {"position": v(190.5, 8.47) * mm});
            skPoint(sketch, "E38.42.11.0", {"position": v(190.5, 2.12) * mm});
            skPoint(sketch, "E38.42.12.0", {"position": v(190.5, -4.23) * mm});
            skPoint(sketch, "E38.42.13.0", {"position": v(190.5, -10.58) * mm});
            skPoint(sketch, "E38.42.14.0", {"position": v(190.5, -16.93) * mm});
            skPoint(sketch, "E38.42.15.0", {"position": v(190.5, -23.28) * mm});
            skPoint(sketch, "E38.42.16.0", {"position": v(190.5, -29.63) * mm});
            skPoint(sketch, "E38.42.17.0", {"position": v(190.5, -35.98) * mm});
            skPoint(sketch, "E38.42.18.0", {"position": v(190.5, -42.33) * mm});
            skPoint(sketch, "E38.42.19.0", {"position": v(190.5, -48.68) * mm});
            skPoint(sketch, "E38.42.20.0", {"position": v(190.5, -55.03) * mm});
            skPoint(sketch, "E38.42.21.0", {"position": v(190.5, -61.38) * mm});
            skPoint(sketch, "E38.42.22.0", {"position": v(190.5, -67.73) * mm});
            skPoint(sketch, "E38.42.23.0", {"position": v(190.5, -74.08) * mm});
            skPoint(sketch, "E38.42.24.0", {"position": v(190.5, -80.43) * mm});
            skPoint(sketch, "E38.42.25.0", {"position": v(190.5, -86.78) * mm});
            skPoint(sketch, "E38.42.26.0", {"position": v(190.5, -93.13) * mm});
            skPoint(sketch, "E38.42.27.0", {"position": v(190.5, -99.48) * mm});
            skPoint(sketch, "E38.42.28.0", {"position": v(190.5, -105.83) * mm});
            skPoint(sketch, "E38.42.29.0", {"position": v(190.5, -112.18) * mm});
            skPoint(sketch, "E38.42.30.0", {"position": v(190.5, -118.53) * mm});
            skPoint(sketch, "E38.42.31.0", {"position": v(190.5, -124.88) * mm});
            skPoint(sketch, "E38.42.32.0", {"position": v(190.5, -131.23) * mm});
            skPoint(sketch, "E38.42.33.0", {"position": v(190.5, -137.58) * mm});
            skPoint(sketch, "E38.42.34.0", {"position": v(190.5, -143.93) * mm});
            skPoint(sketch, "E38.42.35.0", {"position": v(190.5, -150.28) * mm});
            skPoint(sketch, "E38.42.36.0", {"position": v(190.5, -156.63) * mm});
            skPoint(sketch, "E38.42.37.0", {"position": v(190.5, -162.98) * mm});
            skPoint(sketch, "E38.42.38.0", {"position": v(190.5, -169.33) * mm});
            skPoint(sketch, "E38.42.39.0", {"position": v(190.5, -175.68) * mm});
            skPoint(sketch, "E38.42.40.0", {"position": v(190.5, -182.03) * mm});
            skPoint(sketch, "E38.42.41.0", {"position": v(190.5, -188.38) * mm});
            skPoint(sketch, "E38.42.42.0", {"position": v(190.5, -194.73) * mm});
            skPoint(sketch, "E38.42.43.0", {"position": v(190.5, -201.08) * mm});
            skPoint(sketch, "E38.42.44.0", {"position": v(190.5, -207.43) * mm});
            skPoint(sketch, "E38.42.45.0", {"position": v(190.5, -213.78) * mm});
            skPoint(sketch, "E38.42.46.0", {"position": v(190.5, -220.13) * mm});
            skPoint(sketch, "E38.42.47.0", {"position": v(190.5, -226.48) * mm});
            skPoint(sketch, "E38.42.48.0", {"position": v(190.5, -232.83) * mm});
            skPoint(sketch, "E38.42.49.0", {"position": v(190.5, -239.18) * mm});
            skPoint(sketch, "E38.42.50.0", {"position": v(190.5, -245.53) * mm});
            skPoint(sketch, "E38.42.51.0", {"position": v(190.5, -251.88) * mm});
            skPoint(sketch, "E38.42.52.0", {"position": v(190.5, -258.23) * mm});
            skPoint(sketch, "E38.42.53.0", {"position": v(190.5, -264.58) * mm});
            skPoint(sketch, "E38.42.54.0", {"position": v(190.5, -270.93) * mm});
            skPoint(sketch, "E38.42.55.0", {"position": v(190.5, -277.28) * mm});
            skPoint(sketch, "E38.42.56.0", {"position": v(190.5, -283.63) * mm});
            skPoint(sketch, "E38.42.57.0", {"position": v(190.5, -289.98) * mm});
            skPoint(sketch, "E38.42.58.0", {"position": v(190.5, -296.33) * mm});
            skPoint(sketch, "E38.42.59.0", {"position": v(190.5, -302.68) * mm});
            skPoint(sketch, "E38.42.60.0", {"position": v(190.5, -309.03) * mm});
            skPoint(sketch, "E38.42.61.0", {"position": v(190.5, -315.38) * mm});
            skPoint(sketch, "E38.42.62.0", {"position": v(190.5, -321.73) * mm});
            skPoint(sketch, "E38.42.63.0", {"position": v(190.5, -328.08) * mm});
            skPoint(sketch, "E38.42.64.0", {"position": v(190.5, -334.43) * mm});
            skPoint(sketch, "E38.42.65.0", {"position": v(190.5, -340.78) * mm});
            skPoint(sketch, "E38.42.66.0", {"position": v(190.5, -347.13) * mm});
            skPoint(sketch, "E38.42.67.0", {"position": v(190.5, -353.48) * mm});
            skPoint(sketch, "E38.42.68.0", {"position": v(190.5, -359.83) * mm});
            skPoint(sketch, "E38.42.69.0", {"position": v(190.5, -366.18) * mm});
            skPoint(sketch, "E38.42.70.0", {"position": v(190.5, -372.53) * mm});
            skPoint(sketch, "E38.42.71.0", {"position": v(190.5, -378.88) * mm});
            skPoint(sketch, "E38.42.72.0", {"position": v(190.5, -385.23) * mm});
            skPoint(sketch, "E38.42.73.0", {"position": v(190.5, -391.58) * mm});
            skPoint(sketch, "E38.42.74.0", {"position": v(190.5, -397.93) * mm});
            skPoint(sketch, "E38.42.75.0", {"position": v(190.5, -404.28) * mm});
            skPoint(sketch, "E38.42.76.0", {"position": v(190.5, -410.63) * mm});
            skPoint(sketch, "E38.42.77.0", {"position": v(190.5, -416.98) * mm});
            skPoint(sketch, "E38.42.78.0", {"position": v(190.5, -423.33) * mm});
            skPoint(sketch, "E38.42.79.0", {"position": v(190.5, -429.68) * mm});
            skPoint(sketch, "E38.42.80.0", {"position": v(190.5, -436.03) * mm});
            skPoint(sketch, "E38.42.81.0", {"position": v(190.5, -442.38) * mm});
            skPoint(sketch, "E38.42.82.0", {"position": v(190.5, -448.73) * mm});
            skPoint(sketch, "E38.42.83.0", {"position": v(190.5, -455.08) * mm});
            skPoint(sketch, "E38.42.84.0", {"position": v(190.5, -461.43) * mm});
            skPoint(sketch, "E38.42.85.0", {"position": v(190.5, -467.78) * mm});
            skPoint(sketch, "E38.42.86.0", {"position": v(190.5, -474.13) * mm});
            skPoint(sketch, "E38.42.87.0", {"position": v(190.5, -480.48) * mm});
            skPoint(sketch, "E38.42.88.0", {"position": v(190.5, -486.83) * mm});
            skPoint(sketch, "E38.42.89.0", {"position": v(190.5, -493.18) * mm});
            skPoint(sketch, "E38.42.90.0", {"position": v(190.5, -499.53) * mm});
            skPoint(sketch, "E38.42.91.0", {"position": v(190.5, -505.88) * mm});
            skPoint(sketch, "E38.42.92.0", {"position": v(190.5, -512.23) * mm});
            skPoint(sketch, "E38.42.93.0", {"position": v(190.5, -518.58) * mm});
            skPoint(sketch, "E38.42.94.0", {"position": v(190.5, -524.93) * mm});
            skPoint(sketch, "E38.42.95.0", {"position": v(190.5, -531.28) * mm});
            skPoint(sketch, "E38.42.96.0", {"position": v(190.5, -537.63) * mm});
            skPoint(sketch, "E38.42.97.0", {"position": v(190.5, -543.98) * mm});
            skPoint(sketch, "E38.42.98.0", {"position": v(190.5, -550.33) * mm});
            skPoint(sketch, "E38.42.99.0", {"position": v(190.5, -556.68) * mm});
            skPoint(sketch, "E38.43.0.0", {"position": v(196.85, 71.97) * mm});
            skPoint(sketch, "E38.43.1.0", {"position": v(196.85, 65.62) * mm});
            skPoint(sketch, "E38.43.2.0", {"position": v(196.85, 59.27) * mm});
            skPoint(sketch, "E38.43.3.0", {"position": v(196.85, 52.92) * mm});
            skPoint(sketch, "E38.43.4.0", {"position": v(196.85, 46.57) * mm});
            skPoint(sketch, "E38.43.5.0", {"position": v(196.85, 40.22) * mm});
            skPoint(sketch, "E38.43.6.0", {"position": v(196.85, 33.87) * mm});
            skPoint(sketch, "E38.43.7.0", {"position": v(196.85, 27.52) * mm});
            skPoint(sketch, "E38.43.8.0", {"position": v(196.85, 21.17) * mm});
            skPoint(sketch, "E38.43.9.0", {"position": v(196.85, 14.82) * mm});
            skPoint(sketch, "E38.43.10.0", {"position": v(196.85, 8.47) * mm});
            skPoint(sketch, "E38.43.11.0", {"position": v(196.85, 2.12) * mm});
            skPoint(sketch, "E38.43.12.0", {"position": v(196.85, -4.23) * mm});
            skPoint(sketch, "E38.43.13.0", {"position": v(196.85, -10.58) * mm});
            skPoint(sketch, "E38.43.14.0", {"position": v(196.85, -16.93) * mm});
            skPoint(sketch, "E38.43.15.0", {"position": v(196.85, -23.28) * mm});
            skPoint(sketch, "E38.43.16.0", {"position": v(196.85, -29.63) * mm});
            skPoint(sketch, "E38.43.17.0", {"position": v(196.85, -35.98) * mm});
            skPoint(sketch, "E38.43.18.0", {"position": v(196.85, -42.33) * mm});
            skPoint(sketch, "E38.43.19.0", {"position": v(196.85, -48.68) * mm});
            skPoint(sketch, "E38.43.20.0", {"position": v(196.85, -55.03) * mm});
            skPoint(sketch, "E38.43.21.0", {"position": v(196.85, -61.38) * mm});
            skPoint(sketch, "E38.43.22.0", {"position": v(196.85, -67.73) * mm});
            skPoint(sketch, "E38.43.23.0", {"position": v(196.85, -74.08) * mm});
            skPoint(sketch, "E38.43.24.0", {"position": v(196.85, -80.43) * mm});
            skPoint(sketch, "E38.43.25.0", {"position": v(196.85, -86.78) * mm});
            skPoint(sketch, "E38.43.26.0", {"position": v(196.85, -93.13) * mm});
            skPoint(sketch, "E38.43.27.0", {"position": v(196.85, -99.48) * mm});
            skPoint(sketch, "E38.43.28.0", {"position": v(196.85, -105.83) * mm});
            skPoint(sketch, "E38.43.29.0", {"position": v(196.85, -112.18) * mm});
            skPoint(sketch, "E38.43.30.0", {"position": v(196.85, -118.53) * mm});
            skPoint(sketch, "E38.43.31.0", {"position": v(196.85, -124.88) * mm});
            skPoint(sketch, "E38.43.32.0", {"position": v(196.85, -131.23) * mm});
            skPoint(sketch, "E38.43.33.0", {"position": v(196.85, -137.58) * mm});
            skPoint(sketch, "E38.43.34.0", {"position": v(196.85, -143.93) * mm});
            skPoint(sketch, "E38.43.35.0", {"position": v(196.85, -150.28) * mm});
            skPoint(sketch, "E38.43.36.0", {"position": v(196.85, -156.63) * mm});
            skPoint(sketch, "E38.43.37.0", {"position": v(196.85, -162.98) * mm});
            skPoint(sketch, "E38.43.38.0", {"position": v(196.85, -169.33) * mm});
            skPoint(sketch, "E38.43.39.0", {"position": v(196.85, -175.68) * mm});
            skPoint(sketch, "E38.43.40.0", {"position": v(196.85, -182.03) * mm});
            skPoint(sketch, "E38.43.41.0", {"position": v(196.85, -188.38) * mm});
            skPoint(sketch, "E38.43.42.0", {"position": v(196.85, -194.73) * mm});
            skPoint(sketch, "E38.43.43.0", {"position": v(196.85, -201.08) * mm});
            skPoint(sketch, "E38.43.44.0", {"position": v(196.85, -207.43) * mm});
            skPoint(sketch, "E38.43.45.0", {"position": v(196.85, -213.78) * mm});
            skPoint(sketch, "E38.43.46.0", {"position": v(196.85, -220.13) * mm});
            skPoint(sketch, "E38.43.47.0", {"position": v(196.85, -226.48) * mm});
            skPoint(sketch, "E38.43.48.0", {"position": v(196.85, -232.83) * mm});
            skPoint(sketch, "E38.43.49.0", {"position": v(196.85, -239.18) * mm});
            skPoint(sketch, "E38.43.50.0", {"position": v(196.85, -245.53) * mm});
            skPoint(sketch, "E38.43.51.0", {"position": v(196.85, -251.88) * mm});
            skPoint(sketch, "E38.43.52.0", {"position": v(196.85, -258.23) * mm});
            skPoint(sketch, "E38.43.53.0", {"position": v(196.85, -264.58) * mm});
            skPoint(sketch, "E38.43.54.0", {"position": v(196.85, -270.93) * mm});
            skPoint(sketch, "E38.43.55.0", {"position": v(196.85, -277.28) * mm});
            skPoint(sketch, "E38.43.56.0", {"position": v(196.85, -283.63) * mm});
            skPoint(sketch, "E38.43.57.0", {"position": v(196.85, -289.98) * mm});
            skPoint(sketch, "E38.43.58.0", {"position": v(196.85, -296.33) * mm});
            skPoint(sketch, "E38.43.59.0", {"position": v(196.85, -302.68) * mm});
            skPoint(sketch, "E38.43.60.0", {"position": v(196.85, -309.03) * mm});
            skPoint(sketch, "E38.43.61.0", {"position": v(196.85, -315.38) * mm});
            skPoint(sketch, "E38.43.62.0", {"position": v(196.85, -321.73) * mm});
            skPoint(sketch, "E38.43.63.0", {"position": v(196.85, -328.08) * mm});
            skPoint(sketch, "E38.43.64.0", {"position": v(196.85, -334.43) * mm});
            skPoint(sketch, "E38.43.65.0", {"position": v(196.85, -340.78) * mm});
            skPoint(sketch, "E38.43.66.0", {"position": v(196.85, -347.13) * mm});
            skPoint(sketch, "E38.43.67.0", {"position": v(196.85, -353.48) * mm});
            skPoint(sketch, "E38.43.68.0", {"position": v(196.85, -359.83) * mm});
            skPoint(sketch, "E38.43.69.0", {"position": v(196.85, -366.18) * mm});
            skPoint(sketch, "E38.43.70.0", {"position": v(196.85, -372.53) * mm});
            skPoint(sketch, "E38.43.71.0", {"position": v(196.85, -378.88) * mm});
            skPoint(sketch, "E38.43.72.0", {"position": v(196.85, -385.23) * mm});
            skPoint(sketch, "E38.43.73.0", {"position": v(196.85, -391.58) * mm});
            skPoint(sketch, "E38.43.74.0", {"position": v(196.85, -397.93) * mm});
            skPoint(sketch, "E38.43.75.0", {"position": v(196.85, -404.28) * mm});
            skPoint(sketch, "E38.43.76.0", {"position": v(196.85, -410.63) * mm});
            skPoint(sketch, "E38.43.77.0", {"position": v(196.85, -416.98) * mm});
            skPoint(sketch, "E38.43.78.0", {"position": v(196.85, -423.33) * mm});
            skPoint(sketch, "E38.43.79.0", {"position": v(196.85, -429.68) * mm});
            skPoint(sketch, "E38.43.80.0", {"position": v(196.85, -436.03) * mm});
            skPoint(sketch, "E38.43.81.0", {"position": v(196.85, -442.38) * mm});
            skPoint(sketch, "E38.43.82.0", {"position": v(196.85, -448.73) * mm});
            skPoint(sketch, "E38.43.83.0", {"position": v(196.85, -455.08) * mm});
            skPoint(sketch, "E38.43.84.0", {"position": v(196.85, -461.43) * mm});
            skPoint(sketch, "E38.43.85.0", {"position": v(196.85, -467.78) * mm});
            skPoint(sketch, "E38.43.86.0", {"position": v(196.85, -474.13) * mm});
            skPoint(sketch, "E38.43.87.0", {"position": v(196.85, -480.48) * mm});
            skPoint(sketch, "E38.43.88.0", {"position": v(196.85, -486.83) * mm});
            skPoint(sketch, "E38.43.89.0", {"position": v(196.85, -493.18) * mm});
            skPoint(sketch, "E38.43.90.0", {"position": v(196.85, -499.53) * mm});
            skPoint(sketch, "E38.43.91.0", {"position": v(196.85, -505.88) * mm});
            skPoint(sketch, "E38.43.92.0", {"position": v(196.85, -512.23) * mm});
            skPoint(sketch, "E38.43.93.0", {"position": v(196.85, -518.58) * mm});
            skPoint(sketch, "E38.43.94.0", {"position": v(196.85, -524.93) * mm});
            skPoint(sketch, "E38.43.95.0", {"position": v(196.85, -531.28) * mm});
            skPoint(sketch, "E38.43.96.0", {"position": v(196.85, -537.63) * mm});
            skPoint(sketch, "E38.43.97.0", {"position": v(196.85, -543.98) * mm});
            skPoint(sketch, "E38.43.98.0", {"position": v(196.85, -550.33) * mm});
            skPoint(sketch, "E38.43.99.0", {"position": v(196.85, -556.68) * mm});
            skPoint(sketch, "E38.44.0.0", {"position": v(203.2, 71.97) * mm});
            skPoint(sketch, "E38.44.1.0", {"position": v(203.2, 65.62) * mm});
            skPoint(sketch, "E38.44.2.0", {"position": v(203.2, 59.27) * mm});
            skPoint(sketch, "E38.44.3.0", {"position": v(203.2, 52.92) * mm});
            skPoint(sketch, "E38.44.4.0", {"position": v(203.2, 46.57) * mm});
            skPoint(sketch, "E38.44.5.0", {"position": v(203.2, 40.22) * mm});
            skPoint(sketch, "E38.44.6.0", {"position": v(203.2, 33.87) * mm});
            skPoint(sketch, "E38.44.7.0", {"position": v(203.2, 27.52) * mm});
            skPoint(sketch, "E38.44.8.0", {"position": v(203.2, 21.17) * mm});
            skPoint(sketch, "E38.44.9.0", {"position": v(203.2, 14.82) * mm});
            skPoint(sketch, "E38.44.10.0", {"position": v(203.2, 8.47) * mm});
            skPoint(sketch, "E38.44.11.0", {"position": v(203.2, 2.12) * mm});
            skPoint(sketch, "E38.44.12.0", {"position": v(203.2, -4.23) * mm});
            skPoint(sketch, "E38.44.13.0", {"position": v(203.2, -10.58) * mm});
            skPoint(sketch, "E38.44.14.0", {"position": v(203.2, -16.93) * mm});
            skPoint(sketch, "E38.44.15.0", {"position": v(203.2, -23.28) * mm});
            skPoint(sketch, "E38.44.16.0", {"position": v(203.2, -29.63) * mm});
            skPoint(sketch, "E38.44.17.0", {"position": v(203.2, -35.98) * mm});
            skPoint(sketch, "E38.44.18.0", {"position": v(203.2, -42.33) * mm});
            skPoint(sketch, "E38.44.19.0", {"position": v(203.2, -48.68) * mm});
            skPoint(sketch, "E38.44.20.0", {"position": v(203.2, -55.03) * mm});
            skPoint(sketch, "E38.44.21.0", {"position": v(203.2, -61.38) * mm});
            skPoint(sketch, "E38.44.22.0", {"position": v(203.2, -67.73) * mm});
            skPoint(sketch, "E38.44.23.0", {"position": v(203.2, -74.08) * mm});
            skPoint(sketch, "E38.44.24.0", {"position": v(203.2, -80.43) * mm});
            skPoint(sketch, "E38.44.25.0", {"position": v(203.2, -86.78) * mm});
            skPoint(sketch, "E38.44.26.0", {"position": v(203.2, -93.13) * mm});
            skPoint(sketch, "E38.44.27.0", {"position": v(203.2, -99.48) * mm});
            skPoint(sketch, "E38.44.28.0", {"position": v(203.2, -105.83) * mm});
            skPoint(sketch, "E38.44.29.0", {"position": v(203.2, -112.18) * mm});
            skPoint(sketch, "E38.44.30.0", {"position": v(203.2, -118.53) * mm});
            skPoint(sketch, "E38.44.31.0", {"position": v(203.2, -124.88) * mm});
            skPoint(sketch, "E38.44.32.0", {"position": v(203.2, -131.23) * mm});
            skPoint(sketch, "E38.44.33.0", {"position": v(203.2, -137.58) * mm});
            skPoint(sketch, "E38.44.34.0", {"position": v(203.2, -143.93) * mm});
            skPoint(sketch, "E38.44.35.0", {"position": v(203.2, -150.28) * mm});
            skPoint(sketch, "E38.44.36.0", {"position": v(203.2, -156.63) * mm});
            skPoint(sketch, "E38.44.37.0", {"position": v(203.2, -162.98) * mm});
            skPoint(sketch, "E38.44.38.0", {"position": v(203.2, -169.33) * mm});
            skPoint(sketch, "E38.44.39.0", {"position": v(203.2, -175.68) * mm});
            skPoint(sketch, "E38.44.40.0", {"position": v(203.2, -182.03) * mm});
            skPoint(sketch, "E38.44.41.0", {"position": v(203.2, -188.38) * mm});
            skPoint(sketch, "E38.44.42.0", {"position": v(203.2, -194.73) * mm});
            skPoint(sketch, "E38.44.43.0", {"position": v(203.2, -201.08) * mm});
            skPoint(sketch, "E38.44.44.0", {"position": v(203.2, -207.43) * mm});
            skPoint(sketch, "E38.44.45.0", {"position": v(203.2, -213.78) * mm});
            skPoint(sketch, "E38.44.46.0", {"position": v(203.2, -220.13) * mm});
            skPoint(sketch, "E38.44.47.0", {"position": v(203.2, -226.48) * mm});
            skPoint(sketch, "E38.44.48.0", {"position": v(203.2, -232.83) * mm});
            skPoint(sketch, "E38.44.49.0", {"position": v(203.2, -239.18) * mm});
            skPoint(sketch, "E38.44.50.0", {"position": v(203.2, -245.53) * mm});
            skPoint(sketch, "E38.44.51.0", {"position": v(203.2, -251.88) * mm});
            skPoint(sketch, "E38.44.52.0", {"position": v(203.2, -258.23) * mm});
            skPoint(sketch, "E38.44.53.0", {"position": v(203.2, -264.58) * mm});
            skPoint(sketch, "E38.44.54.0", {"position": v(203.2, -270.93) * mm});
            skPoint(sketch, "E38.44.55.0", {"position": v(203.2, -277.28) * mm});
            skPoint(sketch, "E38.44.56.0", {"position": v(203.2, -283.63) * mm});
            skPoint(sketch, "E38.44.57.0", {"position": v(203.2, -289.98) * mm});
            skPoint(sketch, "E38.44.58.0", {"position": v(203.2, -296.33) * mm});
            skPoint(sketch, "E38.44.59.0", {"position": v(203.2, -302.68) * mm});
            skPoint(sketch, "E38.44.60.0", {"position": v(203.2, -309.03) * mm});
            skPoint(sketch, "E38.44.61.0", {"position": v(203.2, -315.38) * mm});
            skPoint(sketch, "E38.44.62.0", {"position": v(203.2, -321.73) * mm});
            skPoint(sketch, "E38.44.63.0", {"position": v(203.2, -328.08) * mm});
            skPoint(sketch, "E38.44.64.0", {"position": v(203.2, -334.43) * mm});
            skPoint(sketch, "E38.44.65.0", {"position": v(203.2, -340.78) * mm});
            skPoint(sketch, "E38.44.66.0", {"position": v(203.2, -347.13) * mm});
            skPoint(sketch, "E38.44.67.0", {"position": v(203.2, -353.48) * mm});
            skPoint(sketch, "E38.44.68.0", {"position": v(203.2, -359.83) * mm});
            skPoint(sketch, "E38.44.69.0", {"position": v(203.2, -366.18) * mm});
            skPoint(sketch, "E38.44.70.0", {"position": v(203.2, -372.53) * mm});
            skPoint(sketch, "E38.44.71.0", {"position": v(203.2, -378.88) * mm});
            skPoint(sketch, "E38.44.72.0", {"position": v(203.2, -385.23) * mm});
            skPoint(sketch, "E38.44.73.0", {"position": v(203.2, -391.58) * mm});
            skPoint(sketch, "E38.44.74.0", {"position": v(203.2, -397.93) * mm});
            skPoint(sketch, "E38.44.75.0", {"position": v(203.2, -404.28) * mm});
            skPoint(sketch, "E38.44.76.0", {"position": v(203.2, -410.63) * mm});
            skPoint(sketch, "E38.44.77.0", {"position": v(203.2, -416.98) * mm});
            skPoint(sketch, "E38.44.78.0", {"position": v(203.2, -423.33) * mm});
            skPoint(sketch, "E38.44.79.0", {"position": v(203.2, -429.68) * mm});
            skPoint(sketch, "E38.44.80.0", {"position": v(203.2, -436.03) * mm});
            skPoint(sketch, "E38.44.81.0", {"position": v(203.2, -442.38) * mm});
            skPoint(sketch, "E38.44.82.0", {"position": v(203.2, -448.73) * mm});
            skPoint(sketch, "E38.44.83.0", {"position": v(203.2, -455.08) * mm});
            skPoint(sketch, "E38.44.84.0", {"position": v(203.2, -461.43) * mm});
            skPoint(sketch, "E38.44.85.0", {"position": v(203.2, -467.78) * mm});
            skPoint(sketch, "E38.44.86.0", {"position": v(203.2, -474.13) * mm});
            skPoint(sketch, "E38.44.87.0", {"position": v(203.2, -480.48) * mm});
            skPoint(sketch, "E38.44.88.0", {"position": v(203.2, -486.83) * mm});
            skPoint(sketch, "E38.44.89.0", {"position": v(203.2, -493.18) * mm});
            skPoint(sketch, "E38.44.90.0", {"position": v(203.2, -499.53) * mm});
            skPoint(sketch, "E38.44.91.0", {"position": v(203.2, -505.88) * mm});
            skPoint(sketch, "E38.44.92.0", {"position": v(203.2, -512.23) * mm});
            skPoint(sketch, "E38.44.93.0", {"position": v(203.2, -518.58) * mm});
            skPoint(sketch, "E38.44.94.0", {"position": v(203.2, -524.93) * mm});
            skPoint(sketch, "E38.44.95.0", {"position": v(203.2, -531.28) * mm});
            skPoint(sketch, "E38.44.96.0", {"position": v(203.2, -537.63) * mm});
            skPoint(sketch, "E38.44.97.0", {"position": v(203.2, -543.98) * mm});
            skPoint(sketch, "E38.44.98.0", {"position": v(203.2, -550.33) * mm});
            skPoint(sketch, "E38.44.99.0", {"position": v(203.2, -556.68) * mm});
            skPoint(sketch, "E38.45.0.0", {"position": v(209.55, 71.97) * mm});
            skPoint(sketch, "E38.45.1.0", {"position": v(209.55, 65.62) * mm});
            skPoint(sketch, "E38.45.2.0", {"position": v(209.55, 59.27) * mm});
            skPoint(sketch, "E38.45.3.0", {"position": v(209.55, 52.92) * mm});
            skPoint(sketch, "E38.45.4.0", {"position": v(209.55, 46.57) * mm});
            skPoint(sketch, "E38.45.5.0", {"position": v(209.55, 40.22) * mm});
            skPoint(sketch, "E38.45.6.0", {"position": v(209.55, 33.87) * mm});
            skPoint(sketch, "E38.45.7.0", {"position": v(209.55, 27.52) * mm});
            skPoint(sketch, "E38.45.8.0", {"position": v(209.55, 21.17) * mm});
            skPoint(sketch, "E38.45.9.0", {"position": v(209.55, 14.82) * mm});
            skPoint(sketch, "E38.45.10.0", {"position": v(209.55, 8.47) * mm});
            skPoint(sketch, "E38.45.11.0", {"position": v(209.55, 2.12) * mm});
            skPoint(sketch, "E38.45.12.0", {"position": v(209.55, -4.23) * mm});
            skPoint(sketch, "E38.45.13.0", {"position": v(209.55, -10.58) * mm});
            skPoint(sketch, "E38.45.14.0", {"position": v(209.55, -16.93) * mm});
            skPoint(sketch, "E38.45.15.0", {"position": v(209.55, -23.28) * mm});
            skPoint(sketch, "E38.45.16.0", {"position": v(209.55, -29.63) * mm});
            skPoint(sketch, "E38.45.17.0", {"position": v(209.55, -35.98) * mm});
            skPoint(sketch, "E38.45.18.0", {"position": v(209.55, -42.33) * mm});
            skPoint(sketch, "E38.45.19.0", {"position": v(209.55, -48.68) * mm});
            skPoint(sketch, "E38.45.20.0", {"position": v(209.55, -55.03) * mm});
            skPoint(sketch, "E38.45.21.0", {"position": v(209.55, -61.38) * mm});
            skPoint(sketch, "E38.45.22.0", {"position": v(209.55, -67.73) * mm});
            skPoint(sketch, "E38.45.23.0", {"position": v(209.55, -74.08) * mm});
            skPoint(sketch, "E38.45.24.0", {"position": v(209.55, -80.43) * mm});
            skPoint(sketch, "E38.45.25.0", {"position": v(209.55, -86.78) * mm});
            skPoint(sketch, "E38.45.26.0", {"position": v(209.55, -93.13) * mm});
            skPoint(sketch, "E38.45.27.0", {"position": v(209.55, -99.48) * mm});
            skPoint(sketch, "E38.45.28.0", {"position": v(209.55, -105.83) * mm});
            skPoint(sketch, "E38.45.29.0", {"position": v(209.55, -112.18) * mm});
            skPoint(sketch, "E38.45.30.0", {"position": v(209.55, -118.53) * mm});
            skPoint(sketch, "E38.45.31.0", {"position": v(209.55, -124.88) * mm});
            skPoint(sketch, "E38.45.32.0", {"position": v(209.55, -131.23) * mm});
            skPoint(sketch, "E38.45.33.0", {"position": v(209.55, -137.58) * mm});
            skPoint(sketch, "E38.45.34.0", {"position": v(209.55, -143.93) * mm});
            skPoint(sketch, "E38.45.35.0", {"position": v(209.55, -150.28) * mm});
            skPoint(sketch, "E38.45.36.0", {"position": v(209.55, -156.63) * mm});
            skPoint(sketch, "E38.45.37.0", {"position": v(209.55, -162.98) * mm});
            skPoint(sketch, "E38.45.38.0", {"position": v(209.55, -169.33) * mm});
            skPoint(sketch, "E38.45.39.0", {"position": v(209.55, -175.68) * mm});
            skPoint(sketch, "E38.45.40.0", {"position": v(209.55, -182.03) * mm});
            skPoint(sketch, "E38.45.41.0", {"position": v(209.55, -188.38) * mm});
            skPoint(sketch, "E38.45.42.0", {"position": v(209.55, -194.73) * mm});
            skPoint(sketch, "E38.45.43.0", {"position": v(209.55, -201.08) * mm});
            skPoint(sketch, "E38.45.44.0", {"position": v(209.55, -207.43) * mm});
            skPoint(sketch, "E38.45.45.0", {"position": v(209.55, -213.78) * mm});
            skPoint(sketch, "E38.45.46.0", {"position": v(209.55, -220.13) * mm});
            skPoint(sketch, "E38.45.47.0", {"position": v(209.55, -226.48) * mm});
            skPoint(sketch, "E38.45.48.0", {"position": v(209.55, -232.83) * mm});
            skPoint(sketch, "E38.45.49.0", {"position": v(209.55, -239.18) * mm});
            skPoint(sketch, "E38.45.50.0", {"position": v(209.55, -245.53) * mm});
            skPoint(sketch, "E38.45.51.0", {"position": v(209.55, -251.88) * mm});
            skPoint(sketch, "E38.45.52.0", {"position": v(209.55, -258.23) * mm});
            skPoint(sketch, "E38.45.53.0", {"position": v(209.55, -264.58) * mm});
            skPoint(sketch, "E38.45.54.0", {"position": v(209.55, -270.93) * mm});
            skPoint(sketch, "E38.45.55.0", {"position": v(209.55, -277.28) * mm});
            skPoint(sketch, "E38.45.56.0", {"position": v(209.55, -283.63) * mm});
            skPoint(sketch, "E38.45.57.0", {"position": v(209.55, -289.98) * mm});
            skPoint(sketch, "E38.45.58.0", {"position": v(209.55, -296.33) * mm});
            skPoint(sketch, "E38.45.59.0", {"position": v(209.55, -302.68) * mm});
            skPoint(sketch, "E38.45.60.0", {"position": v(209.55, -309.03) * mm});
            skPoint(sketch, "E38.45.61.0", {"position": v(209.55, -315.38) * mm});
            skPoint(sketch, "E38.45.62.0", {"position": v(209.55, -321.73) * mm});
            skPoint(sketch, "E38.45.63.0", {"position": v(209.55, -328.08) * mm});
            skPoint(sketch, "E38.45.64.0", {"position": v(209.55, -334.43) * mm});
            skPoint(sketch, "E38.45.65.0", {"position": v(209.55, -340.78) * mm});
            skPoint(sketch, "E38.45.66.0", {"position": v(209.55, -347.13) * mm});
            skPoint(sketch, "E38.45.67.0", {"position": v(209.55, -353.48) * mm});
            skPoint(sketch, "E38.45.68.0", {"position": v(209.55, -359.83) * mm});
            skPoint(sketch, "E38.45.69.0", {"position": v(209.55, -366.18) * mm});
            skPoint(sketch, "E38.45.70.0", {"position": v(209.55, -372.53) * mm});
            skPoint(sketch, "E38.45.71.0", {"position": v(209.55, -378.88) * mm});
            skPoint(sketch, "E38.45.72.0", {"position": v(209.55, -385.23) * mm});
            skPoint(sketch, "E38.45.73.0", {"position": v(209.55, -391.58) * mm});
            skPoint(sketch, "E38.45.74.0", {"position": v(209.55, -397.93) * mm});
            skPoint(sketch, "E38.45.75.0", {"position": v(209.55, -404.28) * mm});
            skPoint(sketch, "E38.45.76.0", {"position": v(209.55, -410.63) * mm});
            skPoint(sketch, "E38.45.77.0", {"position": v(209.55, -416.98) * mm});
            skPoint(sketch, "E38.45.78.0", {"position": v(209.55, -423.33) * mm});
            skPoint(sketch, "E38.45.79.0", {"position": v(209.55, -429.68) * mm});
            skPoint(sketch, "E38.45.80.0", {"position": v(209.55, -436.03) * mm});
            skPoint(sketch, "E38.45.81.0", {"position": v(209.55, -442.38) * mm});
            skPoint(sketch, "E38.45.82.0", {"position": v(209.55, -448.73) * mm});
            skPoint(sketch, "E38.45.83.0", {"position": v(209.55, -455.08) * mm});
            skPoint(sketch, "E38.45.84.0", {"position": v(209.55, -461.43) * mm});
            skPoint(sketch, "E38.45.85.0", {"position": v(209.55, -467.78) * mm});
            skPoint(sketch, "E38.45.86.0", {"position": v(209.55, -474.13) * mm});
            skPoint(sketch, "E38.45.87.0", {"position": v(209.55, -480.48) * mm});
            skPoint(sketch, "E38.45.88.0", {"position": v(209.55, -486.83) * mm});
            skPoint(sketch, "E38.45.89.0", {"position": v(209.55, -493.18) * mm});
            skPoint(sketch, "E38.45.90.0", {"position": v(209.55, -499.53) * mm});
            skPoint(sketch, "E38.45.91.0", {"position": v(209.55, -505.88) * mm});
            skPoint(sketch, "E38.45.92.0", {"position": v(209.55, -512.23) * mm});
            skPoint(sketch, "E38.45.93.0", {"position": v(209.55, -518.58) * mm});
            skPoint(sketch, "E38.45.94.0", {"position": v(209.55, -524.93) * mm});
            skPoint(sketch, "E38.45.95.0", {"position": v(209.55, -531.28) * mm});
            skPoint(sketch, "E38.45.96.0", {"position": v(209.55, -537.63) * mm});
            skPoint(sketch, "E38.45.97.0", {"position": v(209.55, -543.98) * mm});
            skPoint(sketch, "E38.45.98.0", {"position": v(209.55, -550.33) * mm});
            skPoint(sketch, "E38.45.99.0", {"position": v(209.55, -556.68) * mm});
            skPoint(sketch, "E38.46.0.0", {"position": v(215.9, 71.97) * mm});
            skPoint(sketch, "E38.46.1.0", {"position": v(215.9, 65.62) * mm});
            skPoint(sketch, "E38.46.2.0", {"position": v(215.9, 59.27) * mm});
            skPoint(sketch, "E38.46.3.0", {"position": v(215.9, 52.92) * mm});
            skPoint(sketch, "E38.46.4.0", {"position": v(215.9, 46.57) * mm});
            skPoint(sketch, "E38.46.5.0", {"position": v(215.9, 40.22) * mm});
            skPoint(sketch, "E38.46.6.0", {"position": v(215.9, 33.87) * mm});
            skPoint(sketch, "E38.46.7.0", {"position": v(215.9, 27.52) * mm});
            skPoint(sketch, "E38.46.8.0", {"position": v(215.9, 21.17) * mm});
            skPoint(sketch, "E38.46.9.0", {"position": v(215.9, 14.82) * mm});
            skPoint(sketch, "E38.46.10.0", {"position": v(215.9, 8.47) * mm});
            skPoint(sketch, "E38.46.11.0", {"position": v(215.9, 2.12) * mm});
            skPoint(sketch, "E38.46.12.0", {"position": v(215.9, -4.23) * mm});
            skPoint(sketch, "E38.46.13.0", {"position": v(215.9, -10.58) * mm});
            skPoint(sketch, "E38.46.14.0", {"position": v(215.9, -16.93) * mm});
            skPoint(sketch, "E38.46.15.0", {"position": v(215.9, -23.28) * mm});
            skPoint(sketch, "E38.46.16.0", {"position": v(215.9, -29.63) * mm});
            skPoint(sketch, "E38.46.17.0", {"position": v(215.9, -35.98) * mm});
            skPoint(sketch, "E38.46.18.0", {"position": v(215.9, -42.33) * mm});
            skPoint(sketch, "E38.46.19.0", {"position": v(215.9, -48.68) * mm});
            skPoint(sketch, "E38.46.20.0", {"position": v(215.9, -55.03) * mm});
            skPoint(sketch, "E38.46.21.0", {"position": v(215.9, -61.38) * mm});
            skPoint(sketch, "E38.46.22.0", {"position": v(215.9, -67.73) * mm});
            skPoint(sketch, "E38.46.23.0", {"position": v(215.9, -74.08) * mm});
            skPoint(sketch, "E38.46.24.0", {"position": v(215.9, -80.43) * mm});
            skPoint(sketch, "E38.46.25.0", {"position": v(215.9, -86.78) * mm});
            skPoint(sketch, "E38.46.26.0", {"position": v(215.9, -93.13) * mm});
            skPoint(sketch, "E38.46.27.0", {"position": v(215.9, -99.48) * mm});
            skPoint(sketch, "E38.46.28.0", {"position": v(215.9, -105.83) * mm});
            skPoint(sketch, "E38.46.29.0", {"position": v(215.9, -112.18) * mm});
            skPoint(sketch, "E38.46.30.0", {"position": v(215.9, -118.53) * mm});
            skPoint(sketch, "E38.46.31.0", {"position": v(215.9, -124.88) * mm});
            skPoint(sketch, "E38.46.32.0", {"position": v(215.9, -131.23) * mm});
            skPoint(sketch, "E38.46.33.0", {"position": v(215.9, -137.58) * mm});
            skPoint(sketch, "E38.46.34.0", {"position": v(215.9, -143.93) * mm});
            skPoint(sketch, "E38.46.35.0", {"position": v(215.9, -150.28) * mm});
            skPoint(sketch, "E38.46.36.0", {"position": v(215.9, -156.63) * mm});
            skPoint(sketch, "E38.46.37.0", {"position": v(215.9, -162.98) * mm});
            skPoint(sketch, "E38.46.38.0", {"position": v(215.9, -169.33) * mm});
            skPoint(sketch, "E38.46.39.0", {"position": v(215.9, -175.68) * mm});
            skPoint(sketch, "E38.46.40.0", {"position": v(215.9, -182.03) * mm});
            skPoint(sketch, "E38.46.41.0", {"position": v(215.9, -188.38) * mm});
            skPoint(sketch, "E38.46.42.0", {"position": v(215.9, -194.73) * mm});
            skPoint(sketch, "E38.46.43.0", {"position": v(215.9, -201.08) * mm});
            skPoint(sketch, "E38.46.44.0", {"position": v(215.9, -207.43) * mm});
            skPoint(sketch, "E38.46.45.0", {"position": v(215.9, -213.78) * mm});
            skPoint(sketch, "E38.46.46.0", {"position": v(215.9, -220.13) * mm});
            skPoint(sketch, "E38.46.47.0", {"position": v(215.9, -226.48) * mm});
            skPoint(sketch, "E38.46.48.0", {"position": v(215.9, -232.83) * mm});
            skPoint(sketch, "E38.46.49.0", {"position": v(215.9, -239.18) * mm});
            skPoint(sketch, "E38.46.50.0", {"position": v(215.9, -245.53) * mm});
            skPoint(sketch, "E38.46.51.0", {"position": v(215.9, -251.88) * mm});
            skPoint(sketch, "E38.46.52.0", {"position": v(215.9, -258.23) * mm});
            skPoint(sketch, "E38.46.53.0", {"position": v(215.9, -264.58) * mm});
            skPoint(sketch, "E38.46.54.0", {"position": v(215.9, -270.93) * mm});
            skPoint(sketch, "E38.46.55.0", {"position": v(215.9, -277.28) * mm});
            skPoint(sketch, "E38.46.56.0", {"position": v(215.9, -283.63) * mm});
            skPoint(sketch, "E38.46.57.0", {"position": v(215.9, -289.98) * mm});
            skPoint(sketch, "E38.46.58.0", {"position": v(215.9, -296.33) * mm});
            skPoint(sketch, "E38.46.59.0", {"position": v(215.9, -302.68) * mm});
            skPoint(sketch, "E38.46.60.0", {"position": v(215.9, -309.03) * mm});
            skPoint(sketch, "E38.46.61.0", {"position": v(215.9, -315.38) * mm});
            skPoint(sketch, "E38.46.62.0", {"position": v(215.9, -321.73) * mm});
            skPoint(sketch, "E38.46.63.0", {"position": v(215.9, -328.08) * mm});
            skPoint(sketch, "E38.46.64.0", {"position": v(215.9, -334.43) * mm});
            skPoint(sketch, "E38.46.65.0", {"position": v(215.9, -340.78) * mm});
            skPoint(sketch, "E38.46.66.0", {"position": v(215.9, -347.13) * mm});
            skPoint(sketch, "E38.46.67.0", {"position": v(215.9, -353.48) * mm});
            skPoint(sketch, "E38.46.68.0", {"position": v(215.9, -359.83) * mm});
            skPoint(sketch, "E38.46.69.0", {"position": v(215.9, -366.18) * mm});
            skPoint(sketch, "E38.46.70.0", {"position": v(215.9, -372.53) * mm});
            skPoint(sketch, "E38.46.71.0", {"position": v(215.9, -378.88) * mm});
            skPoint(sketch, "E38.46.72.0", {"position": v(215.9, -385.23) * mm});
            skPoint(sketch, "E38.46.73.0", {"position": v(215.9, -391.58) * mm});
            skPoint(sketch, "E38.46.74.0", {"position": v(215.9, -397.93) * mm});
            skPoint(sketch, "E38.46.75.0", {"position": v(215.9, -404.28) * mm});
            skPoint(sketch, "E38.46.76.0", {"position": v(215.9, -410.63) * mm});
            skPoint(sketch, "E38.46.77.0", {"position": v(215.9, -416.98) * mm});
            skPoint(sketch, "E38.46.78.0", {"position": v(215.9, -423.33) * mm});
            skPoint(sketch, "E38.46.79.0", {"position": v(215.9, -429.68) * mm});
            skPoint(sketch, "E38.46.80.0", {"position": v(215.9, -436.03) * mm});
            skPoint(sketch, "E38.46.81.0", {"position": v(215.9, -442.38) * mm});
            skPoint(sketch, "E38.46.82.0", {"position": v(215.9, -448.73) * mm});
            skPoint(sketch, "E38.46.83.0", {"position": v(215.9, -455.08) * mm});
            skPoint(sketch, "E38.46.84.0", {"position": v(215.9, -461.43) * mm});
            skPoint(sketch, "E38.46.85.0", {"position": v(215.9, -467.78) * mm});
            skPoint(sketch, "E38.46.86.0", {"position": v(215.9, -474.13) * mm});
            skPoint(sketch, "E38.46.87.0", {"position": v(215.9, -480.48) * mm});
            skPoint(sketch, "E38.46.88.0", {"position": v(215.9, -486.83) * mm});
            skPoint(sketch, "E38.46.89.0", {"position": v(215.9, -493.18) * mm});
            skPoint(sketch, "E38.46.90.0", {"position": v(215.9, -499.53) * mm});
            skPoint(sketch, "E38.46.91.0", {"position": v(215.9, -505.88) * mm});
            skPoint(sketch, "E38.46.92.0", {"position": v(215.9, -512.23) * mm});
            skPoint(sketch, "E38.46.93.0", {"position": v(215.9, -518.58) * mm});
            skPoint(sketch, "E38.46.94.0", {"position": v(215.9, -524.93) * mm});
            skPoint(sketch, "E38.46.95.0", {"position": v(215.9, -531.28) * mm});
            skPoint(sketch, "E38.46.96.0", {"position": v(215.9, -537.63) * mm});
            skPoint(sketch, "E38.46.97.0", {"position": v(215.9, -543.98) * mm});
            skPoint(sketch, "E38.46.98.0", {"position": v(215.9, -550.33) * mm});
            skPoint(sketch, "E38.46.99.0", {"position": v(215.9, -556.68) * mm});
            skPoint(sketch, "E38.47.0.0", {"position": v(222.25, 71.97) * mm});
            skPoint(sketch, "E38.47.1.0", {"position": v(222.25, 65.62) * mm});
            skPoint(sketch, "E38.47.2.0", {"position": v(222.25, 59.27) * mm});
            skPoint(sketch, "E38.47.3.0", {"position": v(222.25, 52.92) * mm});
            skPoint(sketch, "E38.47.4.0", {"position": v(222.25, 46.57) * mm});
            skPoint(sketch, "E38.47.5.0", {"position": v(222.25, 40.22) * mm});
            skPoint(sketch, "E38.47.6.0", {"position": v(222.25, 33.87) * mm});
            skPoint(sketch, "E38.47.7.0", {"position": v(222.25, 27.52) * mm});
            skPoint(sketch, "E38.47.8.0", {"position": v(222.25, 21.17) * mm});
            skPoint(sketch, "E38.47.9.0", {"position": v(222.25, 14.82) * mm});
            skPoint(sketch, "E38.47.10.0", {"position": v(222.25, 8.47) * mm});
            skPoint(sketch, "E38.47.11.0", {"position": v(222.25, 2.12) * mm});
            skPoint(sketch, "E38.47.12.0", {"position": v(222.25, -4.23) * mm});
            skPoint(sketch, "E38.47.13.0", {"position": v(222.25, -10.58) * mm});
            skPoint(sketch, "E38.47.14.0", {"position": v(222.25, -16.93) * mm});
            skPoint(sketch, "E38.47.15.0", {"position": v(222.25, -23.28) * mm});
            skPoint(sketch, "E38.47.16.0", {"position": v(222.25, -29.63) * mm});
            skPoint(sketch, "E38.47.17.0", {"position": v(222.25, -35.98) * mm});
            skPoint(sketch, "E38.47.18.0", {"position": v(222.25, -42.33) * mm});
            skPoint(sketch, "E38.47.19.0", {"position": v(222.25, -48.68) * mm});
            skPoint(sketch, "E38.47.20.0", {"position": v(222.25, -55.03) * mm});
            skPoint(sketch, "E38.47.21.0", {"position": v(222.25, -61.38) * mm});
            skPoint(sketch, "E38.47.22.0", {"position": v(222.25, -67.73) * mm});
            skPoint(sketch, "E38.47.23.0", {"position": v(222.25, -74.08) * mm});
            skPoint(sketch, "E38.47.24.0", {"position": v(222.25, -80.43) * mm});
            skPoint(sketch, "E38.47.25.0", {"position": v(222.25, -86.78) * mm});
            skPoint(sketch, "E38.47.26.0", {"position": v(222.25, -93.13) * mm});
            skPoint(sketch, "E38.47.27.0", {"position": v(222.25, -99.48) * mm});
            skPoint(sketch, "E38.47.28.0", {"position": v(222.25, -105.83) * mm});
            skPoint(sketch, "E38.47.29.0", {"position": v(222.25, -112.18) * mm});
            skPoint(sketch, "E38.47.30.0", {"position": v(222.25, -118.53) * mm});
            skPoint(sketch, "E38.47.31.0", {"position": v(222.25, -124.88) * mm});
            skPoint(sketch, "E38.47.32.0", {"position": v(222.25, -131.23) * mm});
            skPoint(sketch, "E38.47.33.0", {"position": v(222.25, -137.58) * mm});
            skPoint(sketch, "E38.47.34.0", {"position": v(222.25, -143.93) * mm});
            skPoint(sketch, "E38.47.35.0", {"position": v(222.25, -150.28) * mm});
            skPoint(sketch, "E38.47.36.0", {"position": v(222.25, -156.63) * mm});
            skPoint(sketch, "E38.47.37.0", {"position": v(222.25, -162.98) * mm});
            skPoint(sketch, "E38.47.38.0", {"position": v(222.25, -169.33) * mm});
            skPoint(sketch, "E38.47.39.0", {"position": v(222.25, -175.68) * mm});
            skPoint(sketch, "E38.47.40.0", {"position": v(222.25, -182.03) * mm});
            skPoint(sketch, "E38.47.41.0", {"position": v(222.25, -188.38) * mm});
            skPoint(sketch, "E38.47.42.0", {"position": v(222.25, -194.73) * mm});
            skPoint(sketch, "E38.47.43.0", {"position": v(222.25, -201.08) * mm});
            skPoint(sketch, "E38.47.44.0", {"position": v(222.25, -207.43) * mm});
            skPoint(sketch, "E38.47.45.0", {"position": v(222.25, -213.78) * mm});
            skPoint(sketch, "E38.47.46.0", {"position": v(222.25, -220.13) * mm});
            skPoint(sketch, "E38.47.47.0", {"position": v(222.25, -226.48) * mm});
            skPoint(sketch, "E38.47.48.0", {"position": v(222.25, -232.83) * mm});
            skPoint(sketch, "E38.47.49.0", {"position": v(222.25, -239.18) * mm});
            skPoint(sketch, "E38.47.50.0", {"position": v(222.25, -245.53) * mm});
            skPoint(sketch, "E38.47.51.0", {"position": v(222.25, -251.88) * mm});
            skPoint(sketch, "E38.47.52.0", {"position": v(222.25, -258.23) * mm});
            skPoint(sketch, "E38.47.53.0", {"position": v(222.25, -264.58) * mm});
            skPoint(sketch, "E38.47.54.0", {"position": v(222.25, -270.93) * mm});
            skPoint(sketch, "E38.47.55.0", {"position": v(222.25, -277.28) * mm});
            skPoint(sketch, "E38.47.56.0", {"position": v(222.25, -283.63) * mm});
            skPoint(sketch, "E38.47.57.0", {"position": v(222.25, -289.98) * mm});
            skPoint(sketch, "E38.47.58.0", {"position": v(222.25, -296.33) * mm});
            skPoint(sketch, "E38.47.59.0", {"position": v(222.25, -302.68) * mm});
            skPoint(sketch, "E38.47.60.0", {"position": v(222.25, -309.03) * mm});
            skPoint(sketch, "E38.47.61.0", {"position": v(222.25, -315.38) * mm});
            skPoint(sketch, "E38.47.62.0", {"position": v(222.25, -321.73) * mm});
            skPoint(sketch, "E38.47.63.0", {"position": v(222.25, -328.08) * mm});
            skPoint(sketch, "E38.47.64.0", {"position": v(222.25, -334.43) * mm});
            skPoint(sketch, "E38.47.65.0", {"position": v(222.25, -340.78) * mm});
            skPoint(sketch, "E38.47.66.0", {"position": v(222.25, -347.13) * mm});
            skPoint(sketch, "E38.47.67.0", {"position": v(222.25, -353.48) * mm});
            skPoint(sketch, "E38.47.68.0", {"position": v(222.25, -359.83) * mm});
            skPoint(sketch, "E38.47.69.0", {"position": v(222.25, -366.18) * mm});
            skPoint(sketch, "E38.47.70.0", {"position": v(222.25, -372.53) * mm});
            skPoint(sketch, "E38.47.71.0", {"position": v(222.25, -378.88) * mm});
            skPoint(sketch, "E38.47.72.0", {"position": v(222.25, -385.23) * mm});
            skPoint(sketch, "E38.47.73.0", {"position": v(222.25, -391.58) * mm});
            skPoint(sketch, "E38.47.74.0", {"position": v(222.25, -397.93) * mm});
            skPoint(sketch, "E38.47.75.0", {"position": v(222.25, -404.28) * mm});
            skPoint(sketch, "E38.47.76.0", {"position": v(222.25, -410.63) * mm});
            skPoint(sketch, "E38.47.77.0", {"position": v(222.25, -416.98) * mm});
            skPoint(sketch, "E38.47.78.0", {"position": v(222.25, -423.33) * mm});
            skPoint(sketch, "E38.47.79.0", {"position": v(222.25, -429.68) * mm});
            skPoint(sketch, "E38.47.80.0", {"position": v(222.25, -436.03) * mm});
            skPoint(sketch, "E38.47.81.0", {"position": v(222.25, -442.38) * mm});
            skPoint(sketch, "E38.47.82.0", {"position": v(222.25, -448.73) * mm});
            skPoint(sketch, "E38.47.83.0", {"position": v(222.25, -455.08) * mm});
            skPoint(sketch, "E38.47.84.0", {"position": v(222.25, -461.43) * mm});
            skPoint(sketch, "E38.47.85.0", {"position": v(222.25, -467.78) * mm});
            skPoint(sketch, "E38.47.86.0", {"position": v(222.25, -474.13) * mm});
            skPoint(sketch, "E38.47.87.0", {"position": v(222.25, -480.48) * mm});
            skPoint(sketch, "E38.47.88.0", {"position": v(222.25, -486.83) * mm});
            skPoint(sketch, "E38.47.89.0", {"position": v(222.25, -493.18) * mm});
            skPoint(sketch, "E38.47.90.0", {"position": v(222.25, -499.53) * mm});
            skPoint(sketch, "E38.47.91.0", {"position": v(222.25, -505.88) * mm});
            skPoint(sketch, "E38.47.92.0", {"position": v(222.25, -512.23) * mm});
            skPoint(sketch, "E38.47.93.0", {"position": v(222.25, -518.58) * mm});
            skPoint(sketch, "E38.47.94.0", {"position": v(222.25, -524.93) * mm});
            skPoint(sketch, "E38.47.95.0", {"position": v(222.25, -531.28) * mm});
            skPoint(sketch, "E38.47.96.0", {"position": v(222.25, -537.63) * mm});
            skPoint(sketch, "E38.47.97.0", {"position": v(222.25, -543.98) * mm});
            skPoint(sketch, "E38.47.98.0", {"position": v(222.25, -550.33) * mm});
            skPoint(sketch, "E38.47.99.0", {"position": v(222.25, -556.68) * mm});
            skPoint(sketch, "E38.48.0.0", {"position": v(228.6, 71.97) * mm});
            skPoint(sketch, "E38.48.1.0", {"position": v(228.6, 65.62) * mm});
            skPoint(sketch, "E38.48.2.0", {"position": v(228.6, 59.27) * mm});
            skPoint(sketch, "E38.48.3.0", {"position": v(228.6, 52.92) * mm});
            skPoint(sketch, "E38.48.4.0", {"position": v(228.6, 46.57) * mm});
            skPoint(sketch, "E38.48.5.0", {"position": v(228.6, 40.22) * mm});
            skPoint(sketch, "E38.48.6.0", {"position": v(228.6, 33.87) * mm});
            skPoint(sketch, "E38.48.7.0", {"position": v(228.6, 27.52) * mm});
            skPoint(sketch, "E38.48.8.0", {"position": v(228.6, 21.17) * mm});
            skPoint(sketch, "E38.48.9.0", {"position": v(228.6, 14.82) * mm});
            skPoint(sketch, "E38.48.10.0", {"position": v(228.6, 8.47) * mm});
            skPoint(sketch, "E38.48.11.0", {"position": v(228.6, 2.12) * mm});
            skPoint(sketch, "E38.48.12.0", {"position": v(228.6, -4.23) * mm});
            skPoint(sketch, "E38.48.13.0", {"position": v(228.6, -10.58) * mm});
            skPoint(sketch, "E38.48.14.0", {"position": v(228.6, -16.93) * mm});
            skPoint(sketch, "E38.48.15.0", {"position": v(228.6, -23.28) * mm});
            skPoint(sketch, "E38.48.16.0", {"position": v(228.6, -29.63) * mm});
            skPoint(sketch, "E38.48.17.0", {"position": v(228.6, -35.98) * mm});
            skPoint(sketch, "E38.48.18.0", {"position": v(228.6, -42.33) * mm});
            skPoint(sketch, "E38.48.19.0", {"position": v(228.6, -48.68) * mm});
            skPoint(sketch, "E38.48.20.0", {"position": v(228.6, -55.03) * mm});
            skPoint(sketch, "E38.48.21.0", {"position": v(228.6, -61.38) * mm});
            skPoint(sketch, "E38.48.22.0", {"position": v(228.6, -67.73) * mm});
            skPoint(sketch, "E38.48.23.0", {"position": v(228.6, -74.08) * mm});
            skPoint(sketch, "E38.48.24.0", {"position": v(228.6, -80.43) * mm});
            skPoint(sketch, "E38.48.25.0", {"position": v(228.6, -86.78) * mm});
            skPoint(sketch, "E38.48.26.0", {"position": v(228.6, -93.13) * mm});
            skPoint(sketch, "E38.48.27.0", {"position": v(228.6, -99.48) * mm});
            skPoint(sketch, "E38.48.28.0", {"position": v(228.6, -105.83) * mm});
            skPoint(sketch, "E38.48.29.0", {"position": v(228.6, -112.18) * mm});
            skPoint(sketch, "E38.48.30.0", {"position": v(228.6, -118.53) * mm});
            skPoint(sketch, "E38.48.31.0", {"position": v(228.6, -124.88) * mm});
            skPoint(sketch, "E38.48.32.0", {"position": v(228.6, -131.23) * mm});
            skPoint(sketch, "E38.48.33.0", {"position": v(228.6, -137.58) * mm});
            skPoint(sketch, "E38.48.34.0", {"position": v(228.6, -143.93) * mm});
            skPoint(sketch, "E38.48.35.0", {"position": v(228.6, -150.28) * mm});
            skPoint(sketch, "E38.48.36.0", {"position": v(228.6, -156.63) * mm});
            skPoint(sketch, "E38.48.37.0", {"position": v(228.6, -162.98) * mm});
            skPoint(sketch, "E38.48.38.0", {"position": v(228.6, -169.33) * mm});
            skPoint(sketch, "E38.48.39.0", {"position": v(228.6, -175.68) * mm});
            skPoint(sketch, "E38.48.40.0", {"position": v(228.6, -182.03) * mm});
            skPoint(sketch, "E38.48.41.0", {"position": v(228.6, -188.38) * mm});
            skPoint(sketch, "E38.48.42.0", {"position": v(228.6, -194.73) * mm});
            skPoint(sketch, "E38.48.43.0", {"position": v(228.6, -201.08) * mm});
            skPoint(sketch, "E38.48.44.0", {"position": v(228.6, -207.43) * mm});
            skPoint(sketch, "E38.48.45.0", {"position": v(228.6, -213.78) * mm});
            skPoint(sketch, "E38.48.46.0", {"position": v(228.6, -220.13) * mm});
            skPoint(sketch, "E38.48.47.0", {"position": v(228.6, -226.48) * mm});
            skPoint(sketch, "E38.48.48.0", {"position": v(228.6, -232.83) * mm});
            skPoint(sketch, "E38.48.49.0", {"position": v(228.6, -239.18) * mm});
            skPoint(sketch, "E38.48.50.0", {"position": v(228.6, -245.53) * mm});
            skPoint(sketch, "E38.48.51.0", {"position": v(228.6, -251.88) * mm});
            skPoint(sketch, "E38.48.52.0", {"position": v(228.6, -258.23) * mm});
            skPoint(sketch, "E38.48.53.0", {"position": v(228.6, -264.58) * mm});
            skPoint(sketch, "E38.48.54.0", {"position": v(228.6, -270.93) * mm});
            skPoint(sketch, "E38.48.55.0", {"position": v(228.6, -277.28) * mm});
            skPoint(sketch, "E38.48.56.0", {"position": v(228.6, -283.63) * mm});
            skPoint(sketch, "E38.48.57.0", {"position": v(228.6, -289.98) * mm});
            skPoint(sketch, "E38.48.58.0", {"position": v(228.6, -296.33) * mm});
            skPoint(sketch, "E38.48.59.0", {"position": v(228.6, -302.68) * mm});
            skPoint(sketch, "E38.48.60.0", {"position": v(228.6, -309.03) * mm});
            skPoint(sketch, "E38.48.61.0", {"position": v(228.6, -315.38) * mm});
            skPoint(sketch, "E38.48.62.0", {"position": v(228.6, -321.73) * mm});
            skPoint(sketch, "E38.48.63.0", {"position": v(228.6, -328.08) * mm});
            skPoint(sketch, "E38.48.64.0", {"position": v(228.6, -334.43) * mm});
            skPoint(sketch, "E38.48.65.0", {"position": v(228.6, -340.78) * mm});
            skPoint(sketch, "E38.48.66.0", {"position": v(228.6, -347.13) * mm});
            skPoint(sketch, "E38.48.67.0", {"position": v(228.6, -353.48) * mm});
            skPoint(sketch, "E38.48.68.0", {"position": v(228.6, -359.83) * mm});
            skPoint(sketch, "E38.48.69.0", {"position": v(228.6, -366.18) * mm});
            skPoint(sketch, "E38.48.70.0", {"position": v(228.6, -372.53) * mm});
            skPoint(sketch, "E38.48.71.0", {"position": v(228.6, -378.88) * mm});
            skPoint(sketch, "E38.48.72.0", {"position": v(228.6, -385.23) * mm});
            skPoint(sketch, "E38.48.73.0", {"position": v(228.6, -391.58) * mm});
            skPoint(sketch, "E38.48.74.0", {"position": v(228.6, -397.93) * mm});
            skPoint(sketch, "E38.48.75.0", {"position": v(228.6, -404.28) * mm});
            skPoint(sketch, "E38.48.76.0", {"position": v(228.6, -410.63) * mm});
            skPoint(sketch, "E38.48.77.0", {"position": v(228.6, -416.98) * mm});
            skPoint(sketch, "E38.48.78.0", {"position": v(228.6, -423.33) * mm});
            skPoint(sketch, "E38.48.79.0", {"position": v(228.6, -429.68) * mm});
            skPoint(sketch, "E38.48.80.0", {"position": v(228.6, -436.03) * mm});
            skPoint(sketch, "E38.48.81.0", {"position": v(228.6, -442.38) * mm});
            skPoint(sketch, "E38.48.82.0", {"position": v(228.6, -448.73) * mm});
            skPoint(sketch, "E38.48.83.0", {"position": v(228.6, -455.08) * mm});
            skPoint(sketch, "E38.48.84.0", {"position": v(228.6, -461.43) * mm});
            skPoint(sketch, "E38.48.85.0", {"position": v(228.6, -467.78) * mm});
            skPoint(sketch, "E38.48.86.0", {"position": v(228.6, -474.13) * mm});
            skPoint(sketch, "E38.48.87.0", {"position": v(228.6, -480.48) * mm});
            skPoint(sketch, "E38.48.88.0", {"position": v(228.6, -486.83) * mm});
            skPoint(sketch, "E38.48.89.0", {"position": v(228.6, -493.18) * mm});
            skPoint(sketch, "E38.48.90.0", {"position": v(228.6, -499.53) * mm});
            skPoint(sketch, "E38.48.91.0", {"position": v(228.6, -505.88) * mm});
            skPoint(sketch, "E38.48.92.0", {"position": v(228.6, -512.23) * mm});
            skPoint(sketch, "E38.48.93.0", {"position": v(228.6, -518.58) * mm});
            skPoint(sketch, "E38.48.94.0", {"position": v(228.6, -524.93) * mm});
            skPoint(sketch, "E38.48.95.0", {"position": v(228.6, -531.28) * mm});
            skPoint(sketch, "E38.48.96.0", {"position": v(228.6, -537.63) * mm});
            skPoint(sketch, "E38.48.97.0", {"position": v(228.6, -543.98) * mm});
            skPoint(sketch, "E38.48.98.0", {"position": v(228.6, -550.33) * mm});
            skPoint(sketch, "E38.48.99.0", {"position": v(228.6, -556.68) * mm});
            skPoint(sketch, "E38.49.0.0", {"position": v(234.95, 71.97) * mm});
            skPoint(sketch, "E38.49.1.0", {"position": v(234.95, 65.62) * mm});
            skPoint(sketch, "E38.49.2.0", {"position": v(234.95, 59.27) * mm});
            skPoint(sketch, "E38.49.3.0", {"position": v(234.95, 52.92) * mm});
            skPoint(sketch, "E38.49.4.0", {"position": v(234.95, 46.57) * mm});
            skPoint(sketch, "E38.49.5.0", {"position": v(234.95, 40.22) * mm});
            skPoint(sketch, "E38.49.6.0", {"position": v(234.95, 33.87) * mm});
            skPoint(sketch, "E38.49.7.0", {"position": v(234.95, 27.52) * mm});
            skPoint(sketch, "E38.49.8.0", {"position": v(234.95, 21.17) * mm});
            skPoint(sketch, "E38.49.9.0", {"position": v(234.95, 14.82) * mm});
            skPoint(sketch, "E38.49.10.0", {"position": v(234.95, 8.47) * mm});
            skPoint(sketch, "E38.49.11.0", {"position": v(234.95, 2.12) * mm});
            skPoint(sketch, "E38.49.12.0", {"position": v(234.95, -4.23) * mm});
            skPoint(sketch, "E38.49.13.0", {"position": v(234.95, -10.58) * mm});
            skPoint(sketch, "E38.49.14.0", {"position": v(234.95, -16.93) * mm});
            skPoint(sketch, "E38.49.15.0", {"position": v(234.95, -23.28) * mm});
            skPoint(sketch, "E38.49.16.0", {"position": v(234.95, -29.63) * mm});
            skPoint(sketch, "E38.49.17.0", {"position": v(234.95, -35.98) * mm});
            skPoint(sketch, "E38.49.18.0", {"position": v(234.95, -42.33) * mm});
            skPoint(sketch, "E38.49.19.0", {"position": v(234.95, -48.68) * mm});
            skPoint(sketch, "E38.49.20.0", {"position": v(234.95, -55.03) * mm});
            skPoint(sketch, "E38.49.21.0", {"position": v(234.95, -61.38) * mm});
            skPoint(sketch, "E38.49.22.0", {"position": v(234.95, -67.73) * mm});
            skPoint(sketch, "E38.49.23.0", {"position": v(234.95, -74.08) * mm});
            skPoint(sketch, "E38.49.24.0", {"position": v(234.95, -80.43) * mm});
            skPoint(sketch, "E38.49.25.0", {"position": v(234.95, -86.78) * mm});
            skPoint(sketch, "E38.49.26.0", {"position": v(234.95, -93.13) * mm});
            skPoint(sketch, "E38.49.27.0", {"position": v(234.95, -99.48) * mm});
            skPoint(sketch, "E38.49.28.0", {"position": v(234.95, -105.83) * mm});
            skPoint(sketch, "E38.49.29.0", {"position": v(234.95, -112.18) * mm});
            skPoint(sketch, "E38.49.30.0", {"position": v(234.95, -118.53) * mm});
            skPoint(sketch, "E38.49.31.0", {"position": v(234.95, -124.88) * mm});
            skPoint(sketch, "E38.49.32.0", {"position": v(234.95, -131.23) * mm});
            skPoint(sketch, "E38.49.33.0", {"position": v(234.95, -137.58) * mm});
            skPoint(sketch, "E38.49.34.0", {"position": v(234.95, -143.93) * mm});
            skPoint(sketch, "E38.49.35.0", {"position": v(234.95, -150.28) * mm});
            skPoint(sketch, "E38.49.36.0", {"position": v(234.95, -156.63) * mm});
            skPoint(sketch, "E38.49.37.0", {"position": v(234.95, -162.98) * mm});
            skPoint(sketch, "E38.49.38.0", {"position": v(234.95, -169.33) * mm});
            skPoint(sketch, "E38.49.39.0", {"position": v(234.95, -175.68) * mm});
            skPoint(sketch, "E38.49.40.0", {"position": v(234.95, -182.03) * mm});
            skPoint(sketch, "E38.49.41.0", {"position": v(234.95, -188.38) * mm});
            skPoint(sketch, "E38.49.42.0", {"position": v(234.95, -194.73) * mm});
            skPoint(sketch, "E38.49.43.0", {"position": v(234.95, -201.08) * mm});
            skPoint(sketch, "E38.49.44.0", {"position": v(234.95, -207.43) * mm});
            skPoint(sketch, "E38.49.45.0", {"position": v(234.95, -213.78) * mm});
            skPoint(sketch, "E38.49.46.0", {"position": v(234.95, -220.13) * mm});
            skPoint(sketch, "E38.49.47.0", {"position": v(234.95, -226.48) * mm});
            skPoint(sketch, "E38.49.48.0", {"position": v(234.95, -232.83) * mm});
            skPoint(sketch, "E38.49.49.0", {"position": v(234.95, -239.18) * mm});
            skPoint(sketch, "E38.49.50.0", {"position": v(234.95, -245.53) * mm});
            skPoint(sketch, "E38.49.51.0", {"position": v(234.95, -251.88) * mm});
            skPoint(sketch, "E38.49.52.0", {"position": v(234.95, -258.23) * mm});
            skPoint(sketch, "E38.49.53.0", {"position": v(234.95, -264.58) * mm});
            skPoint(sketch, "E38.49.54.0", {"position": v(234.95, -270.93) * mm});
            skPoint(sketch, "E38.49.55.0", {"position": v(234.95, -277.28) * mm});
            skPoint(sketch, "E38.49.56.0", {"position": v(234.95, -283.63) * mm});
            skPoint(sketch, "E38.49.57.0", {"position": v(234.95, -289.98) * mm});
            skPoint(sketch, "E38.49.58.0", {"position": v(234.95, -296.33) * mm});
            skPoint(sketch, "E38.49.59.0", {"position": v(234.95, -302.68) * mm});
            skPoint(sketch, "E38.49.60.0", {"position": v(234.95, -309.03) * mm});
            skPoint(sketch, "E38.49.61.0", {"position": v(234.95, -315.38) * mm});
            skPoint(sketch, "E38.49.62.0", {"position": v(234.95, -321.73) * mm});
            skPoint(sketch, "E38.49.63.0", {"position": v(234.95, -328.08) * mm});
            skPoint(sketch, "E38.49.64.0", {"position": v(234.95, -334.43) * mm});
            skPoint(sketch, "E38.49.65.0", {"position": v(234.95, -340.78) * mm});
            skPoint(sketch, "E38.49.66.0", {"position": v(234.95, -347.13) * mm});
            skPoint(sketch, "E38.49.67.0", {"position": v(234.95, -353.48) * mm});
            skPoint(sketch, "E38.49.68.0", {"position": v(234.95, -359.83) * mm});
            skPoint(sketch, "E38.49.69.0", {"position": v(234.95, -366.18) * mm});
            skPoint(sketch, "E38.49.70.0", {"position": v(234.95, -372.53) * mm});
            skPoint(sketch, "E38.49.71.0", {"position": v(234.95, -378.88) * mm});
            skPoint(sketch, "E38.49.72.0", {"position": v(234.95, -385.23) * mm});
            skPoint(sketch, "E38.49.73.0", {"position": v(234.95, -391.58) * mm});
            skPoint(sketch, "E38.49.74.0", {"position": v(234.95, -397.93) * mm});
            skPoint(sketch, "E38.49.75.0", {"position": v(234.95, -404.28) * mm});
            skPoint(sketch, "E38.49.76.0", {"position": v(234.95, -410.63) * mm});
            skPoint(sketch, "E38.49.77.0", {"position": v(234.95, -416.98) * mm});
            skPoint(sketch, "E38.49.78.0", {"position": v(234.95, -423.33) * mm});
            skPoint(sketch, "E38.49.79.0", {"position": v(234.95, -429.68) * mm});
            skPoint(sketch, "E38.49.80.0", {"position": v(234.95, -436.03) * mm});
            skPoint(sketch, "E38.49.81.0", {"position": v(234.95, -442.38) * mm});
            skPoint(sketch, "E38.49.82.0", {"position": v(234.95, -448.73) * mm});
            skPoint(sketch, "E38.49.83.0", {"position": v(234.95, -455.08) * mm});
            skPoint(sketch, "E38.49.84.0", {"position": v(234.95, -461.43) * mm});
            skPoint(sketch, "E38.49.85.0", {"position": v(234.95, -467.78) * mm});
            skPoint(sketch, "E38.49.86.0", {"position": v(234.95, -474.13) * mm});
            skPoint(sketch, "E38.49.87.0", {"position": v(234.95, -480.48) * mm});
            skPoint(sketch, "E38.49.88.0", {"position": v(234.95, -486.83) * mm});
            skPoint(sketch, "E38.49.89.0", {"position": v(234.95, -493.18) * mm});
            skPoint(sketch, "E38.49.90.0", {"position": v(234.95, -499.53) * mm});
            skPoint(sketch, "E38.49.91.0", {"position": v(234.95, -505.88) * mm});
            skPoint(sketch, "E38.49.92.0", {"position": v(234.95, -512.23) * mm});
            skPoint(sketch, "E38.49.93.0", {"position": v(234.95, -518.58) * mm});
            skPoint(sketch, "E38.49.94.0", {"position": v(234.95, -524.93) * mm});
            skPoint(sketch, "E38.49.95.0", {"position": v(234.95, -531.28) * mm});
            skPoint(sketch, "E38.49.96.0", {"position": v(234.95, -537.63) * mm});
            skPoint(sketch, "E38.49.97.0", {"position": v(234.95, -543.98) * mm});
            skPoint(sketch, "E38.49.98.0", {"position": v(234.95, -550.33) * mm});
            skPoint(sketch, "E38.49.99.0", {"position": v(234.95, -556.68) * mm});
            skPoint(sketch, "E38.50.0.0", {"position": v(241.3, 71.97) * mm});
            skPoint(sketch, "E38.50.1.0", {"position": v(241.3, 65.62) * mm});
            skPoint(sketch, "E38.50.2.0", {"position": v(241.3, 59.27) * mm});
            skPoint(sketch, "E38.50.3.0", {"position": v(241.3, 52.92) * mm});
            skPoint(sketch, "E38.50.4.0", {"position": v(241.3, 46.57) * mm});
            skPoint(sketch, "E38.50.5.0", {"position": v(241.3, 40.22) * mm});
            skPoint(sketch, "E38.50.6.0", {"position": v(241.3, 33.87) * mm});
            skPoint(sketch, "E38.50.7.0", {"position": v(241.3, 27.52) * mm});
            skPoint(sketch, "E38.50.8.0", {"position": v(241.3, 21.17) * mm});
            skPoint(sketch, "E38.50.9.0", {"position": v(241.3, 14.82) * mm});
            skPoint(sketch, "E38.50.10.0", {"position": v(241.3, 8.47) * mm});
            skPoint(sketch, "E38.50.11.0", {"position": v(241.3, 2.12) * mm});
            skPoint(sketch, "E38.50.12.0", {"position": v(241.3, -4.23) * mm});
            skPoint(sketch, "E38.50.13.0", {"position": v(241.3, -10.58) * mm});
            skPoint(sketch, "E38.50.14.0", {"position": v(241.3, -16.93) * mm});
            skPoint(sketch, "E38.50.15.0", {"position": v(241.3, -23.28) * mm});
            skPoint(sketch, "E38.50.16.0", {"position": v(241.3, -29.63) * mm});
            skPoint(sketch, "E38.50.17.0", {"position": v(241.3, -35.98) * mm});
            skPoint(sketch, "E38.50.18.0", {"position": v(241.3, -42.33) * mm});
            skPoint(sketch, "E38.50.19.0", {"position": v(241.3, -48.68) * mm});
            skPoint(sketch, "E38.50.20.0", {"position": v(241.3, -55.03) * mm});
            skPoint(sketch, "E38.50.21.0", {"position": v(241.3, -61.38) * mm});
            skPoint(sketch, "E38.50.22.0", {"position": v(241.3, -67.73) * mm});
            skPoint(sketch, "E38.50.23.0", {"position": v(241.3, -74.08) * mm});
            skPoint(sketch, "E38.50.24.0", {"position": v(241.3, -80.43) * mm});
            skPoint(sketch, "E38.50.25.0", {"position": v(241.3, -86.78) * mm});
            skPoint(sketch, "E38.50.26.0", {"position": v(241.3, -93.13) * mm});
            skPoint(sketch, "E38.50.27.0", {"position": v(241.3, -99.48) * mm});
            skPoint(sketch, "E38.50.28.0", {"position": v(241.3, -105.83) * mm});
            skPoint(sketch, "E38.50.29.0", {"position": v(241.3, -112.18) * mm});
            skPoint(sketch, "E38.50.30.0", {"position": v(241.3, -118.53) * mm});
            skPoint(sketch, "E38.50.31.0", {"position": v(241.3, -124.88) * mm});
            skPoint(sketch, "E38.50.32.0", {"position": v(241.3, -131.23) * mm});
            skPoint(sketch, "E38.50.33.0", {"position": v(241.3, -137.58) * mm});
            skPoint(sketch, "E38.50.34.0", {"position": v(241.3, -143.93) * mm});
            skPoint(sketch, "E38.50.35.0", {"position": v(241.3, -150.28) * mm});
            skPoint(sketch, "E38.50.36.0", {"position": v(241.3, -156.63) * mm});
            skPoint(sketch, "E38.50.37.0", {"position": v(241.3, -162.98) * mm});
            skPoint(sketch, "E38.50.38.0", {"position": v(241.3, -169.33) * mm});
            skPoint(sketch, "E38.50.39.0", {"position": v(241.3, -175.68) * mm});
            skPoint(sketch, "E38.50.40.0", {"position": v(241.3, -182.03) * mm});
            skPoint(sketch, "E38.50.41.0", {"position": v(241.3, -188.38) * mm});
            skPoint(sketch, "E38.50.42.0", {"position": v(241.3, -194.73) * mm});
            skPoint(sketch, "E38.50.43.0", {"position": v(241.3, -201.08) * mm});
            skPoint(sketch, "E38.50.44.0", {"position": v(241.3, -207.43) * mm});
            skPoint(sketch, "E38.50.45.0", {"position": v(241.3, -213.78) * mm});
            skPoint(sketch, "E38.50.46.0", {"position": v(241.3, -220.13) * mm});
            skPoint(sketch, "E38.50.47.0", {"position": v(241.3, -226.48) * mm});
            skPoint(sketch, "E38.50.48.0", {"position": v(241.3, -232.83) * mm});
            skPoint(sketch, "E38.50.49.0", {"position": v(241.3, -239.18) * mm});
            skPoint(sketch, "E38.50.50.0", {"position": v(241.3, -245.53) * mm});
            skPoint(sketch, "E38.50.51.0", {"position": v(241.3, -251.88) * mm});
            skPoint(sketch, "E38.50.52.0", {"position": v(241.3, -258.23) * mm});
            skPoint(sketch, "E38.50.53.0", {"position": v(241.3, -264.58) * mm});
            skPoint(sketch, "E38.50.54.0", {"position": v(241.3, -270.93) * mm});
            skPoint(sketch, "E38.50.55.0", {"position": v(241.3, -277.28) * mm});
            skPoint(sketch, "E38.50.56.0", {"position": v(241.3, -283.63) * mm});
            skPoint(sketch, "E38.50.57.0", {"position": v(241.3, -289.98) * mm});
            skPoint(sketch, "E38.50.58.0", {"position": v(241.3, -296.33) * mm});
            skPoint(sketch, "E38.50.59.0", {"position": v(241.3, -302.68) * mm});
            skPoint(sketch, "E38.50.60.0", {"position": v(241.3, -309.03) * mm});
            skPoint(sketch, "E38.50.61.0", {"position": v(241.3, -315.38) * mm});
            skPoint(sketch, "E38.50.62.0", {"position": v(241.3, -321.73) * mm});
            skPoint(sketch, "E38.50.63.0", {"position": v(241.3, -328.08) * mm});
            skPoint(sketch, "E38.50.64.0", {"position": v(241.3, -334.43) * mm});
            skPoint(sketch, "E38.50.65.0", {"position": v(241.3, -340.78) * mm});
            skPoint(sketch, "E38.50.66.0", {"position": v(241.3, -347.13) * mm});
            skPoint(sketch, "E38.50.67.0", {"position": v(241.3, -353.48) * mm});
            skPoint(sketch, "E38.50.68.0", {"position": v(241.3, -359.83) * mm});
            skPoint(sketch, "E38.50.69.0", {"position": v(241.3, -366.18) * mm});
            skPoint(sketch, "E38.50.70.0", {"position": v(241.3, -372.53) * mm});
            skPoint(sketch, "E38.50.71.0", {"position": v(241.3, -378.88) * mm});
            skPoint(sketch, "E38.50.72.0", {"position": v(241.3, -385.23) * mm});
            skPoint(sketch, "E38.50.73.0", {"position": v(241.3, -391.58) * mm});
            skPoint(sketch, "E38.50.74.0", {"position": v(241.3, -397.93) * mm});
            skPoint(sketch, "E38.50.75.0", {"position": v(241.3, -404.28) * mm});
            skPoint(sketch, "E38.50.76.0", {"position": v(241.3, -410.63) * mm});
            skPoint(sketch, "E38.50.77.0", {"position": v(241.3, -416.98) * mm});
            skPoint(sketch, "E38.50.78.0", {"position": v(241.3, -423.33) * mm});
            skPoint(sketch, "E38.50.79.0", {"position": v(241.3, -429.68) * mm});
            skPoint(sketch, "E38.50.80.0", {"position": v(241.3, -436.03) * mm});
            skPoint(sketch, "E38.50.81.0", {"position": v(241.3, -442.38) * mm});
            skPoint(sketch, "E38.50.82.0", {"position": v(241.3, -448.73) * mm});
            skPoint(sketch, "E38.50.83.0", {"position": v(241.3, -455.08) * mm});
            skPoint(sketch, "E38.50.84.0", {"position": v(241.3, -461.43) * mm});
            skPoint(sketch, "E38.50.85.0", {"position": v(241.3, -467.78) * mm});
            skPoint(sketch, "E38.50.86.0", {"position": v(241.3, -474.13) * mm});
            skPoint(sketch, "E38.50.87.0", {"position": v(241.3, -480.48) * mm});
            skPoint(sketch, "E38.50.88.0", {"position": v(241.3, -486.83) * mm});
            skPoint(sketch, "E38.50.89.0", {"position": v(241.3, -493.18) * mm});
            skPoint(sketch, "E38.50.90.0", {"position": v(241.3, -499.53) * mm});
            skPoint(sketch, "E38.50.91.0", {"position": v(241.3, -505.88) * mm});
            skPoint(sketch, "E38.50.92.0", {"position": v(241.3, -512.23) * mm});
            skPoint(sketch, "E38.50.93.0", {"position": v(241.3, -518.58) * mm});
            skPoint(sketch, "E38.50.94.0", {"position": v(241.3, -524.93) * mm});
            skPoint(sketch, "E38.50.95.0", {"position": v(241.3, -531.28) * mm});
            skPoint(sketch, "E38.50.96.0", {"position": v(241.3, -537.63) * mm});
            skPoint(sketch, "E38.50.97.0", {"position": v(241.3, -543.98) * mm});
            skPoint(sketch, "E38.50.98.0", {"position": v(241.3, -550.33) * mm});
            skPoint(sketch, "E38.50.99.0", {"position": v(241.3, -556.68) * mm});
            skPoint(sketch, "E38.51.0.0", {"position": v(247.65, 71.97) * mm});
            skPoint(sketch, "E38.51.1.0", {"position": v(247.65, 65.62) * mm});
            skPoint(sketch, "E38.51.2.0", {"position": v(247.65, 59.27) * mm});
            skPoint(sketch, "E38.51.3.0", {"position": v(247.65, 52.92) * mm});
            skPoint(sketch, "E38.51.4.0", {"position": v(247.65, 46.57) * mm});
            skPoint(sketch, "E38.51.5.0", {"position": v(247.65, 40.22) * mm});
            skPoint(sketch, "E38.51.6.0", {"position": v(247.65, 33.87) * mm});
            skPoint(sketch, "E38.51.7.0", {"position": v(247.65, 27.52) * mm});
            skPoint(sketch, "E38.51.8.0", {"position": v(247.65, 21.17) * mm});
            skPoint(sketch, "E38.51.9.0", {"position": v(247.65, 14.82) * mm});
            skPoint(sketch, "E38.51.10.0", {"position": v(247.65, 8.47) * mm});
            skPoint(sketch, "E38.51.11.0", {"position": v(247.65, 2.12) * mm});
            skPoint(sketch, "E38.51.12.0", {"position": v(247.65, -4.23) * mm});
            skPoint(sketch, "E38.51.13.0", {"position": v(247.65, -10.58) * mm});
            skPoint(sketch, "E38.51.14.0", {"position": v(247.65, -16.93) * mm});
            skPoint(sketch, "E38.51.15.0", {"position": v(247.65, -23.28) * mm});
            skPoint(sketch, "E38.51.16.0", {"position": v(247.65, -29.63) * mm});
            skPoint(sketch, "E38.51.17.0", {"position": v(247.65, -35.98) * mm});
            skPoint(sketch, "E38.51.18.0", {"position": v(247.65, -42.33) * mm});
            skPoint(sketch, "E38.51.19.0", {"position": v(247.65, -48.68) * mm});
            skPoint(sketch, "E38.51.20.0", {"position": v(247.65, -55.03) * mm});
            skPoint(sketch, "E38.51.21.0", {"position": v(247.65, -61.38) * mm});
            skPoint(sketch, "E38.51.22.0", {"position": v(247.65, -67.73) * mm});
            skPoint(sketch, "E38.51.23.0", {"position": v(247.65, -74.08) * mm});
            skPoint(sketch, "E38.51.24.0", {"position": v(247.65, -80.43) * mm});
            skPoint(sketch, "E38.51.25.0", {"position": v(247.65, -86.78) * mm});
            skPoint(sketch, "E38.51.26.0", {"position": v(247.65, -93.13) * mm});
            skPoint(sketch, "E38.51.27.0", {"position": v(247.65, -99.48) * mm});
            skPoint(sketch, "E38.51.28.0", {"position": v(247.65, -105.83) * mm});
            skPoint(sketch, "E38.51.29.0", {"position": v(247.65, -112.18) * mm});
            skPoint(sketch, "E38.51.30.0", {"position": v(247.65, -118.53) * mm});
            skPoint(sketch, "E38.51.31.0", {"position": v(247.65, -124.88) * mm});
            skPoint(sketch, "E38.51.32.0", {"position": v(247.65, -131.23) * mm});
            skPoint(sketch, "E38.51.33.0", {"position": v(247.65, -137.58) * mm});
            skPoint(sketch, "E38.51.34.0", {"position": v(247.65, -143.93) * mm});
            skPoint(sketch, "E38.51.35.0", {"position": v(247.65, -150.28) * mm});
            skPoint(sketch, "E38.51.36.0", {"position": v(247.65, -156.63) * mm});
            skPoint(sketch, "E38.51.37.0", {"position": v(247.65, -162.98) * mm});
            skPoint(sketch, "E38.51.38.0", {"position": v(247.65, -169.33) * mm});
            skPoint(sketch, "E38.51.39.0", {"position": v(247.65, -175.68) * mm});
            skPoint(sketch, "E38.51.40.0", {"position": v(247.65, -182.03) * mm});
            skPoint(sketch, "E38.51.41.0", {"position": v(247.65, -188.38) * mm});
            skPoint(sketch, "E38.51.42.0", {"position": v(247.65, -194.73) * mm});
            skPoint(sketch, "E38.51.43.0", {"position": v(247.65, -201.08) * mm});
            skPoint(sketch, "E38.51.44.0", {"position": v(247.65, -207.43) * mm});
            skPoint(sketch, "E38.51.45.0", {"position": v(247.65, -213.78) * mm});
            skPoint(sketch, "E38.51.46.0", {"position": v(247.65, -220.13) * mm});
            skPoint(sketch, "E38.51.47.0", {"position": v(247.65, -226.48) * mm});
            skPoint(sketch, "E38.51.48.0", {"position": v(247.65, -232.83) * mm});
            skPoint(sketch, "E38.51.49.0", {"position": v(247.65, -239.18) * mm});
            skPoint(sketch, "E38.51.50.0", {"position": v(247.65, -245.53) * mm});
            skPoint(sketch, "E38.51.51.0", {"position": v(247.65, -251.88) * mm});
            skPoint(sketch, "E38.51.52.0", {"position": v(247.65, -258.23) * mm});
            skPoint(sketch, "E38.51.53.0", {"position": v(247.65, -264.58) * mm});
            skPoint(sketch, "E38.51.54.0", {"position": v(247.65, -270.93) * mm});
            skPoint(sketch, "E38.51.55.0", {"position": v(247.65, -277.28) * mm});
            skPoint(sketch, "E38.51.56.0", {"position": v(247.65, -283.63) * mm});
            skPoint(sketch, "E38.51.57.0", {"position": v(247.65, -289.98) * mm});
            skPoint(sketch, "E38.51.58.0", {"position": v(247.65, -296.33) * mm});
            skPoint(sketch, "E38.51.59.0", {"position": v(247.65, -302.68) * mm});
            skPoint(sketch, "E38.51.60.0", {"position": v(247.65, -309.03) * mm});
            skPoint(sketch, "E38.51.61.0", {"position": v(247.65, -315.38) * mm});
            skPoint(sketch, "E38.51.62.0", {"position": v(247.65, -321.73) * mm});
            skPoint(sketch, "E38.51.63.0", {"position": v(247.65, -328.08) * mm});
            skPoint(sketch, "E38.51.64.0", {"position": v(247.65, -334.43) * mm});
            skPoint(sketch, "E38.51.65.0", {"position": v(247.65, -340.78) * mm});
            skPoint(sketch, "E38.51.66.0", {"position": v(247.65, -347.13) * mm});
            skPoint(sketch, "E38.51.67.0", {"position": v(247.65, -353.48) * mm});
            skPoint(sketch, "E38.51.68.0", {"position": v(247.65, -359.83) * mm});
            skPoint(sketch, "E38.51.69.0", {"position": v(247.65, -366.18) * mm});
            skPoint(sketch, "E38.51.70.0", {"position": v(247.65, -372.53) * mm});
            skPoint(sketch, "E38.51.71.0", {"position": v(247.65, -378.88) * mm});
            skPoint(sketch, "E38.51.72.0", {"position": v(247.65, -385.23) * mm});
            skPoint(sketch, "E38.51.73.0", {"position": v(247.65, -391.58) * mm});
            skPoint(sketch, "E38.51.74.0", {"position": v(247.65, -397.93) * mm});
            skPoint(sketch, "E38.51.75.0", {"position": v(247.65, -404.28) * mm});
            skPoint(sketch, "E38.51.76.0", {"position": v(247.65, -410.63) * mm});
            skPoint(sketch, "E38.51.77.0", {"position": v(247.65, -416.98) * mm});
            skPoint(sketch, "E38.51.78.0", {"position": v(247.65, -423.33) * mm});
            skPoint(sketch, "E38.51.79.0", {"position": v(247.65, -429.68) * mm});
            skPoint(sketch, "E38.51.80.0", {"position": v(247.65, -436.03) * mm});
            skPoint(sketch, "E38.51.81.0", {"position": v(247.65, -442.38) * mm});
            skPoint(sketch, "E38.51.82.0", {"position": v(247.65, -448.73) * mm});
            skPoint(sketch, "E38.51.83.0", {"position": v(247.65, -455.08) * mm});
            skPoint(sketch, "E38.51.84.0", {"position": v(247.65, -461.43) * mm});
            skPoint(sketch, "E38.51.85.0", {"position": v(247.65, -467.78) * mm});
            skPoint(sketch, "E38.51.86.0", {"position": v(247.65, -474.13) * mm});
            skPoint(sketch, "E38.51.87.0", {"position": v(247.65, -480.48) * mm});
            skPoint(sketch, "E38.51.88.0", {"position": v(247.65, -486.83) * mm});
            skPoint(sketch, "E38.51.89.0", {"position": v(247.65, -493.18) * mm});
            skPoint(sketch, "E38.51.90.0", {"position": v(247.65, -499.53) * mm});
            skPoint(sketch, "E38.51.91.0", {"position": v(247.65, -505.88) * mm});
            skPoint(sketch, "E38.51.92.0", {"position": v(247.65, -512.23) * mm});
            skPoint(sketch, "E38.51.93.0", {"position": v(247.65, -518.58) * mm});
            skPoint(sketch, "E38.51.94.0", {"position": v(247.65, -524.93) * mm});
            skPoint(sketch, "E38.51.95.0", {"position": v(247.65, -531.28) * mm});
            skPoint(sketch, "E38.51.96.0", {"position": v(247.65, -537.63) * mm});
            skPoint(sketch, "E38.51.97.0", {"position": v(247.65, -543.98) * mm});
            skPoint(sketch, "E38.51.98.0", {"position": v(247.65, -550.33) * mm});
            skPoint(sketch, "E38.51.99.0", {"position": v(247.65, -556.68) * mm});
            skPoint(sketch, "E38.52.0.0", {"position": v(254, 71.97) * mm});
            skPoint(sketch, "E38.52.1.0", {"position": v(254, 65.62) * mm});
            skPoint(sketch, "E38.52.2.0", {"position": v(254, 59.27) * mm});
            skPoint(sketch, "E38.52.3.0", {"position": v(254, 52.92) * mm});
            skPoint(sketch, "E38.52.4.0", {"position": v(254, 46.57) * mm});
            skPoint(sketch, "E38.52.5.0", {"position": v(254, 40.22) * mm});
            skPoint(sketch, "E38.52.6.0", {"position": v(254, 33.87) * mm});
            skPoint(sketch, "E38.52.7.0", {"position": v(254, 27.52) * mm});
            skPoint(sketch, "E38.52.8.0", {"position": v(254, 21.17) * mm});
            skPoint(sketch, "E38.52.9.0", {"position": v(254, 14.82) * mm});
            skPoint(sketch, "E38.52.10.0", {"position": v(254, 8.47) * mm});
            skPoint(sketch, "E38.52.11.0", {"position": v(254, 2.12) * mm});
            skPoint(sketch, "E38.52.12.0", {"position": v(254, -4.23) * mm});
            skPoint(sketch, "E38.52.13.0", {"position": v(254, -10.58) * mm});
            skPoint(sketch, "E38.52.14.0", {"position": v(254, -16.93) * mm});
            skPoint(sketch, "E38.52.15.0", {"position": v(254, -23.28) * mm});
            skPoint(sketch, "E38.52.16.0", {"position": v(254, -29.63) * mm});
            skPoint(sketch, "E38.52.17.0", {"position": v(254, -35.98) * mm});
            skPoint(sketch, "E38.52.18.0", {"position": v(254, -42.33) * mm});
            skPoint(sketch, "E38.52.19.0", {"position": v(254, -48.68) * mm});
            skPoint(sketch, "E38.52.20.0", {"position": v(254, -55.03) * mm});
            skPoint(sketch, "E38.52.21.0", {"position": v(254, -61.38) * mm});
            skPoint(sketch, "E38.52.22.0", {"position": v(254, -67.73) * mm});
            skPoint(sketch, "E38.52.23.0", {"position": v(254, -74.08) * mm});
            skPoint(sketch, "E38.52.24.0", {"position": v(254, -80.43) * mm});
            skPoint(sketch, "E38.52.25.0", {"position": v(254, -86.78) * mm});
            skPoint(sketch, "E38.52.26.0", {"position": v(254, -93.13) * mm});
            skPoint(sketch, "E38.52.27.0", {"position": v(254, -99.48) * mm});
            skPoint(sketch, "E38.52.28.0", {"position": v(254, -105.83) * mm});
            skPoint(sketch, "E38.52.29.0", {"position": v(254, -112.18) * mm});
            skPoint(sketch, "E38.52.30.0", {"position": v(254, -118.53) * mm});
            skPoint(sketch, "E38.52.31.0", {"position": v(254, -124.88) * mm});
            skPoint(sketch, "E38.52.32.0", {"position": v(254, -131.23) * mm});
            skPoint(sketch, "E38.52.33.0", {"position": v(254, -137.58) * mm});
            skPoint(sketch, "E38.52.34.0", {"position": v(254, -143.93) * mm});
            skPoint(sketch, "E38.52.35.0", {"position": v(254, -150.28) * mm});
            skPoint(sketch, "E38.52.36.0", {"position": v(254, -156.63) * mm});
            skPoint(sketch, "E38.52.37.0", {"position": v(254, -162.98) * mm});
            skPoint(sketch, "E38.52.38.0", {"position": v(254, -169.33) * mm});
            skPoint(sketch, "E38.52.39.0", {"position": v(254, -175.68) * mm});
            skPoint(sketch, "E38.52.40.0", {"position": v(254, -182.03) * mm});
            skPoint(sketch, "E38.52.41.0", {"position": v(254, -188.38) * mm});
            skPoint(sketch, "E38.52.42.0", {"position": v(254, -194.73) * mm});
            skPoint(sketch, "E38.52.43.0", {"position": v(254, -201.08) * mm});
            skPoint(sketch, "E38.52.44.0", {"position": v(254, -207.43) * mm});
            skPoint(sketch, "E38.52.45.0", {"position": v(254, -213.78) * mm});
            skPoint(sketch, "E38.52.46.0", {"position": v(254, -220.13) * mm});
            skPoint(sketch, "E38.52.47.0", {"position": v(254, -226.48) * mm});
            skPoint(sketch, "E38.52.48.0", {"position": v(254, -232.83) * mm});
            skPoint(sketch, "E38.52.49.0", {"position": v(254, -239.18) * mm});
            skPoint(sketch, "E38.52.50.0", {"position": v(254, -245.53) * mm});
            skPoint(sketch, "E38.52.51.0", {"position": v(254, -251.88) * mm});
            skPoint(sketch, "E38.52.52.0", {"position": v(254, -258.23) * mm});
            skPoint(sketch, "E38.52.53.0", {"position": v(254, -264.58) * mm});
            skPoint(sketch, "E38.52.54.0", {"position": v(254, -270.93) * mm});
            skPoint(sketch, "E38.52.55.0", {"position": v(254, -277.28) * mm});
            skPoint(sketch, "E38.52.56.0", {"position": v(254, -283.63) * mm});
            skPoint(sketch, "E38.52.57.0", {"position": v(254, -289.98) * mm});
            skPoint(sketch, "E38.52.58.0", {"position": v(254, -296.33) * mm});
            skPoint(sketch, "E38.52.59.0", {"position": v(254, -302.68) * mm});
            skPoint(sketch, "E38.52.60.0", {"position": v(254, -309.03) * mm});
            skPoint(sketch, "E38.52.61.0", {"position": v(254, -315.38) * mm});
            skPoint(sketch, "E38.52.62.0", {"position": v(254, -321.73) * mm});
            skPoint(sketch, "E38.52.63.0", {"position": v(254, -328.08) * mm});
            skPoint(sketch, "E38.52.64.0", {"position": v(254, -334.43) * mm});
            skPoint(sketch, "E38.52.65.0", {"position": v(254, -340.78) * mm});
            skPoint(sketch, "E38.52.66.0", {"position": v(254, -347.13) * mm});
            skPoint(sketch, "E38.52.67.0", {"position": v(254, -353.48) * mm});
            skPoint(sketch, "E38.52.68.0", {"position": v(254, -359.83) * mm});
            skPoint(sketch, "E38.52.69.0", {"position": v(254, -366.18) * mm});
            skPoint(sketch, "E38.52.70.0", {"position": v(254, -372.53) * mm});
            skPoint(sketch, "E38.52.71.0", {"position": v(254, -378.88) * mm});
            skPoint(sketch, "E38.52.72.0", {"position": v(254, -385.23) * mm});
            skPoint(sketch, "E38.52.73.0", {"position": v(254, -391.58) * mm});
            skPoint(sketch, "E38.52.74.0", {"position": v(254, -397.93) * mm});
            skPoint(sketch, "E38.52.75.0", {"position": v(254, -404.28) * mm});
            skPoint(sketch, "E38.52.76.0", {"position": v(254, -410.63) * mm});
            skPoint(sketch, "E38.52.77.0", {"position": v(254, -416.98) * mm});
            skPoint(sketch, "E38.52.78.0", {"position": v(254, -423.33) * mm});
            skPoint(sketch, "E38.52.79.0", {"position": v(254, -429.68) * mm});
            skPoint(sketch, "E38.52.80.0", {"position": v(254, -436.03) * mm});
            skPoint(sketch, "E38.52.81.0", {"position": v(254, -442.38) * mm});
            skPoint(sketch, "E38.52.82.0", {"position": v(254, -448.73) * mm});
            skPoint(sketch, "E38.52.83.0", {"position": v(254, -455.08) * mm});
            skPoint(sketch, "E38.52.84.0", {"position": v(254, -461.43) * mm});
            skPoint(sketch, "E38.52.85.0", {"position": v(254, -467.78) * mm});
            skPoint(sketch, "E38.52.86.0", {"position": v(254, -474.13) * mm});
            skPoint(sketch, "E38.52.87.0", {"position": v(254, -480.48) * mm});
            skPoint(sketch, "E38.52.88.0", {"position": v(254, -486.83) * mm});
            skPoint(sketch, "E38.52.89.0", {"position": v(254, -493.18) * mm});
            skPoint(sketch, "E38.52.90.0", {"position": v(254, -499.53) * mm});
            skPoint(sketch, "E38.52.91.0", {"position": v(254, -505.88) * mm});
            skPoint(sketch, "E38.52.92.0", {"position": v(254, -512.23) * mm});
            skPoint(sketch, "E38.52.93.0", {"position": v(254, -518.58) * mm});
            skPoint(sketch, "E38.52.94.0", {"position": v(254, -524.93) * mm});
            skPoint(sketch, "E38.52.95.0", {"position": v(254, -531.28) * mm});
            skPoint(sketch, "E38.52.96.0", {"position": v(254, -537.63) * mm});
            skPoint(sketch, "E38.52.97.0", {"position": v(254, -543.98) * mm});
            skPoint(sketch, "E38.52.98.0", {"position": v(254, -550.33) * mm});
            skPoint(sketch, "E38.52.99.0", {"position": v(254, -556.68) * mm});
            skPoint(sketch, "E38.53.0.0", {"position": v(260.35, 71.97) * mm});
            skPoint(sketch, "E38.53.1.0", {"position": v(260.35, 65.62) * mm});
            skPoint(sketch, "E38.53.2.0", {"position": v(260.35, 59.27) * mm});
            skPoint(sketch, "E38.53.3.0", {"position": v(260.35, 52.92) * mm});
            skPoint(sketch, "E38.53.4.0", {"position": v(260.35, 46.57) * mm});
            skPoint(sketch, "E38.53.5.0", {"position": v(260.35, 40.22) * mm});
            skPoint(sketch, "E38.53.6.0", {"position": v(260.35, 33.87) * mm});
            skPoint(sketch, "E38.53.7.0", {"position": v(260.35, 27.52) * mm});
            skPoint(sketch, "E38.53.8.0", {"position": v(260.35, 21.17) * mm});
            skPoint(sketch, "E38.53.9.0", {"position": v(260.35, 14.82) * mm});
            skPoint(sketch, "E38.53.10.0", {"position": v(260.35, 8.47) * mm});
            skPoint(sketch, "E38.53.11.0", {"position": v(260.35, 2.12) * mm});
            skPoint(sketch, "E38.53.12.0", {"position": v(260.35, -4.23) * mm});
            skPoint(sketch, "E38.53.13.0", {"position": v(260.35, -10.58) * mm});
            skPoint(sketch, "E38.53.14.0", {"position": v(260.35, -16.93) * mm});
            skPoint(sketch, "E38.53.15.0", {"position": v(260.35, -23.28) * mm});
            skPoint(sketch, "E38.53.16.0", {"position": v(260.35, -29.63) * mm});
            skPoint(sketch, "E38.53.17.0", {"position": v(260.35, -35.98) * mm});
            skPoint(sketch, "E38.53.18.0", {"position": v(260.35, -42.33) * mm});
            skPoint(sketch, "E38.53.19.0", {"position": v(260.35, -48.68) * mm});
            skPoint(sketch, "E38.53.20.0", {"position": v(260.35, -55.03) * mm});
            skPoint(sketch, "E38.53.21.0", {"position": v(260.35, -61.38) * mm});
            skPoint(sketch, "E38.53.22.0", {"position": v(260.35, -67.73) * mm});
            skPoint(sketch, "E38.53.23.0", {"position": v(260.35, -74.08) * mm});
            skPoint(sketch, "E38.53.24.0", {"position": v(260.35, -80.43) * mm});
            skPoint(sketch, "E38.53.25.0", {"position": v(260.35, -86.78) * mm});
            skPoint(sketch, "E38.53.26.0", {"position": v(260.35, -93.13) * mm});
            skPoint(sketch, "E38.53.27.0", {"position": v(260.35, -99.48) * mm});
            skPoint(sketch, "E38.53.28.0", {"position": v(260.35, -105.83) * mm});
            skPoint(sketch, "E38.53.29.0", {"position": v(260.35, -112.18) * mm});
            skPoint(sketch, "E38.53.30.0", {"position": v(260.35, -118.53) * mm});
            skPoint(sketch, "E38.53.31.0", {"position": v(260.35, -124.88) * mm});
            skPoint(sketch, "E38.53.32.0", {"position": v(260.35, -131.23) * mm});
            skPoint(sketch, "E38.53.33.0", {"position": v(260.35, -137.58) * mm});
            skPoint(sketch, "E38.53.34.0", {"position": v(260.35, -143.93) * mm});
            skPoint(sketch, "E38.53.35.0", {"position": v(260.35, -150.28) * mm});
            skPoint(sketch, "E38.53.36.0", {"position": v(260.35, -156.63) * mm});
            skPoint(sketch, "E38.53.37.0", {"position": v(260.35, -162.98) * mm});
            skPoint(sketch, "E38.53.38.0", {"position": v(260.35, -169.33) * mm});
            skPoint(sketch, "E38.53.39.0", {"position": v(260.35, -175.68) * mm});
            skPoint(sketch, "E38.53.40.0", {"position": v(260.35, -182.03) * mm});
            skPoint(sketch, "E38.53.41.0", {"position": v(260.35, -188.38) * mm});
            skPoint(sketch, "E38.53.42.0", {"position": v(260.35, -194.73) * mm});
            skPoint(sketch, "E38.53.43.0", {"position": v(260.35, -201.08) * mm});
            skPoint(sketch, "E38.53.44.0", {"position": v(260.35, -207.43) * mm});
            skPoint(sketch, "E38.53.45.0", {"position": v(260.35, -213.78) * mm});
            skPoint(sketch, "E38.53.46.0", {"position": v(260.35, -220.13) * mm});
            skPoint(sketch, "E38.53.47.0", {"position": v(260.35, -226.48) * mm});
            skPoint(sketch, "E38.53.48.0", {"position": v(260.35, -232.83) * mm});
            skPoint(sketch, "E38.53.49.0", {"position": v(260.35, -239.18) * mm});
            skPoint(sketch, "E38.53.50.0", {"position": v(260.35, -245.53) * mm});
            skPoint(sketch, "E38.53.51.0", {"position": v(260.35, -251.88) * mm});
            skPoint(sketch, "E38.53.52.0", {"position": v(260.35, -258.23) * mm});
            skPoint(sketch, "E38.53.53.0", {"position": v(260.35, -264.58) * mm});
            skPoint(sketch, "E38.53.54.0", {"position": v(260.35, -270.93) * mm});
            skPoint(sketch, "E38.53.55.0", {"position": v(260.35, -277.28) * mm});
            skPoint(sketch, "E38.53.56.0", {"position": v(260.35, -283.63) * mm});
            skPoint(sketch, "E38.53.57.0", {"position": v(260.35, -289.98) * mm});
            skPoint(sketch, "E38.53.58.0", {"position": v(260.35, -296.33) * mm});
            skPoint(sketch, "E38.53.59.0", {"position": v(260.35, -302.68) * mm});
            skPoint(sketch, "E38.53.60.0", {"position": v(260.35, -309.03) * mm});
            skPoint(sketch, "E38.53.61.0", {"position": v(260.35, -315.38) * mm});
            skPoint(sketch, "E38.53.62.0", {"position": v(260.35, -321.73) * mm});
            skPoint(sketch, "E38.53.63.0", {"position": v(260.35, -328.08) * mm});
            skPoint(sketch, "E38.53.64.0", {"position": v(260.35, -334.43) * mm});
            skPoint(sketch, "E38.53.65.0", {"position": v(260.35, -340.78) * mm});
            skPoint(sketch, "E38.53.66.0", {"position": v(260.35, -347.13) * mm});
            skPoint(sketch, "E38.53.67.0", {"position": v(260.35, -353.48) * mm});
            skPoint(sketch, "E38.53.68.0", {"position": v(260.35, -359.83) * mm});
            skPoint(sketch, "E38.53.69.0", {"position": v(260.35, -366.18) * mm});
            skPoint(sketch, "E38.53.70.0", {"position": v(260.35, -372.53) * mm});
            skPoint(sketch, "E38.53.71.0", {"position": v(260.35, -378.88) * mm});
            skPoint(sketch, "E38.53.72.0", {"position": v(260.35, -385.23) * mm});
            skPoint(sketch, "E38.53.73.0", {"position": v(260.35, -391.58) * mm});
            skPoint(sketch, "E38.53.74.0", {"position": v(260.35, -397.93) * mm});
            skPoint(sketch, "E38.53.75.0", {"position": v(260.35, -404.28) * mm});
            skPoint(sketch, "E38.53.76.0", {"position": v(260.35, -410.63) * mm});
            skPoint(sketch, "E38.53.77.0", {"position": v(260.35, -416.98) * mm});
            skPoint(sketch, "E38.53.78.0", {"position": v(260.35, -423.33) * mm});
            skPoint(sketch, "E38.53.79.0", {"position": v(260.35, -429.68) * mm});
            skPoint(sketch, "E38.53.80.0", {"position": v(260.35, -436.03) * mm});
            skPoint(sketch, "E38.53.81.0", {"position": v(260.35, -442.38) * mm});
            skPoint(sketch, "E38.53.82.0", {"position": v(260.35, -448.73) * mm});
            skPoint(sketch, "E38.53.83.0", {"position": v(260.35, -455.08) * mm});
            skPoint(sketch, "E38.53.84.0", {"position": v(260.35, -461.43) * mm});
            skPoint(sketch, "E38.53.85.0", {"position": v(260.35, -467.78) * mm});
            skPoint(sketch, "E38.53.86.0", {"position": v(260.35, -474.13) * mm});
            skPoint(sketch, "E38.53.87.0", {"position": v(260.35, -480.48) * mm});
            skPoint(sketch, "E38.53.88.0", {"position": v(260.35, -486.83) * mm});
            skPoint(sketch, "E38.53.89.0", {"position": v(260.35, -493.18) * mm});
            skPoint(sketch, "E38.53.90.0", {"position": v(260.35, -499.53) * mm});
            skPoint(sketch, "E38.53.91.0", {"position": v(260.35, -505.88) * mm});
            skPoint(sketch, "E38.53.92.0", {"position": v(260.35, -512.23) * mm});
            skPoint(sketch, "E38.53.93.0", {"position": v(260.35, -518.58) * mm});
            skPoint(sketch, "E38.53.94.0", {"position": v(260.35, -524.93) * mm});
            skPoint(sketch, "E38.53.95.0", {"position": v(260.35, -531.28) * mm});
            skPoint(sketch, "E38.53.96.0", {"position": v(260.35, -537.63) * mm});
            skPoint(sketch, "E38.53.97.0", {"position": v(260.35, -543.98) * mm});
            skPoint(sketch, "E38.53.98.0", {"position": v(260.35, -550.33) * mm});
            skPoint(sketch, "E38.53.99.0", {"position": v(260.35, -556.68) * mm});
            skPoint(sketch, "E38.54.0.0", {"position": v(266.7, 71.97) * mm});
            skPoint(sketch, "E38.54.1.0", {"position": v(266.7, 65.62) * mm});
            skPoint(sketch, "E38.54.2.0", {"position": v(266.7, 59.27) * mm});
            skPoint(sketch, "E38.54.3.0", {"position": v(266.7, 52.92) * mm});
            skPoint(sketch, "E38.54.4.0", {"position": v(266.7, 46.57) * mm});
            skPoint(sketch, "E38.54.5.0", {"position": v(266.7, 40.22) * mm});
            skPoint(sketch, "E38.54.6.0", {"position": v(266.7, 33.87) * mm});
            skPoint(sketch, "E38.54.7.0", {"position": v(266.7, 27.52) * mm});
            skPoint(sketch, "E38.54.8.0", {"position": v(266.7, 21.17) * mm});
            skPoint(sketch, "E38.54.9.0", {"position": v(266.7, 14.82) * mm});
            skPoint(sketch, "E38.54.10.0", {"position": v(266.7, 8.47) * mm});
            skPoint(sketch, "E38.54.11.0", {"position": v(266.7, 2.12) * mm});
            skPoint(sketch, "E38.54.12.0", {"position": v(266.7, -4.23) * mm});
            skPoint(sketch, "E38.54.13.0", {"position": v(266.7, -10.58) * mm});
            skPoint(sketch, "E38.54.14.0", {"position": v(266.7, -16.93) * mm});
            skPoint(sketch, "E38.54.15.0", {"position": v(266.7, -23.28) * mm});
            skPoint(sketch, "E38.54.16.0", {"position": v(266.7, -29.63) * mm});
            skPoint(sketch, "E38.54.17.0", {"position": v(266.7, -35.98) * mm});
            skPoint(sketch, "E38.54.18.0", {"position": v(266.7, -42.33) * mm});
            skPoint(sketch, "E38.54.19.0", {"position": v(266.7, -48.68) * mm});
            skPoint(sketch, "E38.54.20.0", {"position": v(266.7, -55.03) * mm});
            skPoint(sketch, "E38.54.21.0", {"position": v(266.7, -61.38) * mm});
            skPoint(sketch, "E38.54.22.0", {"position": v(266.7, -67.73) * mm});
            skPoint(sketch, "E38.54.23.0", {"position": v(266.7, -74.08) * mm});
            skPoint(sketch, "E38.54.24.0", {"position": v(266.7, -80.43) * mm});
            skPoint(sketch, "E38.54.25.0", {"position": v(266.7, -86.78) * mm});
            skPoint(sketch, "E38.54.26.0", {"position": v(266.7, -93.13) * mm});
            skPoint(sketch, "E38.54.27.0", {"position": v(266.7, -99.48) * mm});
            skPoint(sketch, "E38.54.28.0", {"position": v(266.7, -105.83) * mm});
            skPoint(sketch, "E38.54.29.0", {"position": v(266.7, -112.18) * mm});
            skPoint(sketch, "E38.54.30.0", {"position": v(266.7, -118.53) * mm});
            skPoint(sketch, "E38.54.31.0", {"position": v(266.7, -124.88) * mm});
            skPoint(sketch, "E38.54.32.0", {"position": v(266.7, -131.23) * mm});
            skPoint(sketch, "E38.54.33.0", {"position": v(266.7, -137.58) * mm});
            skPoint(sketch, "E38.54.34.0", {"position": v(266.7, -143.93) * mm});
            skPoint(sketch, "E38.54.35.0", {"position": v(266.7, -150.28) * mm});
            skPoint(sketch, "E38.54.36.0", {"position": v(266.7, -156.63) * mm});
            skPoint(sketch, "E38.54.37.0", {"position": v(266.7, -162.98) * mm});
            skPoint(sketch, "E38.54.38.0", {"position": v(266.7, -169.33) * mm});
            skPoint(sketch, "E38.54.39.0", {"position": v(266.7, -175.68) * mm});
            skPoint(sketch, "E38.54.40.0", {"position": v(266.7, -182.03) * mm});
            skPoint(sketch, "E38.54.41.0", {"position": v(266.7, -188.38) * mm});
            skPoint(sketch, "E38.54.42.0", {"position": v(266.7, -194.73) * mm});
            skPoint(sketch, "E38.54.43.0", {"position": v(266.7, -201.08) * mm});
            skPoint(sketch, "E38.54.44.0", {"position": v(266.7, -207.43) * mm});
            skPoint(sketch, "E38.54.45.0", {"position": v(266.7, -213.78) * mm});
            skPoint(sketch, "E38.54.46.0", {"position": v(266.7, -220.13) * mm});
            skPoint(sketch, "E38.54.47.0", {"position": v(266.7, -226.48) * mm});
            skPoint(sketch, "E38.54.48.0", {"position": v(266.7, -232.83) * mm});
            skPoint(sketch, "E38.54.49.0", {"position": v(266.7, -239.18) * mm});
            skPoint(sketch, "E38.54.50.0", {"position": v(266.7, -245.53) * mm});
            skPoint(sketch, "E38.54.51.0", {"position": v(266.7, -251.88) * mm});
            skPoint(sketch, "E38.54.52.0", {"position": v(266.7, -258.23) * mm});
            skPoint(sketch, "E38.54.53.0", {"position": v(266.7, -264.58) * mm});
            skPoint(sketch, "E38.54.54.0", {"position": v(266.7, -270.93) * mm});
            skPoint(sketch, "E38.54.55.0", {"position": v(266.7, -277.28) * mm});
            skPoint(sketch, "E38.54.56.0", {"position": v(266.7, -283.63) * mm});
            skPoint(sketch, "E38.54.57.0", {"position": v(266.7, -289.98) * mm});
            skPoint(sketch, "E38.54.58.0", {"position": v(266.7, -296.33) * mm});
            skPoint(sketch, "E38.54.59.0", {"position": v(266.7, -302.68) * mm});
            skPoint(sketch, "E38.54.60.0", {"position": v(266.7, -309.03) * mm});
            skPoint(sketch, "E38.54.61.0", {"position": v(266.7, -315.38) * mm});
            skPoint(sketch, "E38.54.62.0", {"position": v(266.7, -321.73) * mm});
            skPoint(sketch, "E38.54.63.0", {"position": v(266.7, -328.08) * mm});
            skPoint(sketch, "E38.54.64.0", {"position": v(266.7, -334.43) * mm});
            skPoint(sketch, "E38.54.65.0", {"position": v(266.7, -340.78) * mm});
            skPoint(sketch, "E38.54.66.0", {"position": v(266.7, -347.13) * mm});
            skPoint(sketch, "E38.54.67.0", {"position": v(266.7, -353.48) * mm});
            skPoint(sketch, "E38.54.68.0", {"position": v(266.7, -359.83) * mm});
            skPoint(sketch, "E38.54.69.0", {"position": v(266.7, -366.18) * mm});
            skPoint(sketch, "E38.54.70.0", {"position": v(266.7, -372.53) * mm});
            skPoint(sketch, "E38.54.71.0", {"position": v(266.7, -378.88) * mm});
            skPoint(sketch, "E38.54.72.0", {"position": v(266.7, -385.23) * mm});
            skPoint(sketch, "E38.54.73.0", {"position": v(266.7, -391.58) * mm});
            skPoint(sketch, "E38.54.74.0", {"position": v(266.7, -397.93) * mm});
            skPoint(sketch, "E38.54.75.0", {"position": v(266.7, -404.28) * mm});
            skPoint(sketch, "E38.54.76.0", {"position": v(266.7, -410.63) * mm});
            skPoint(sketch, "E38.54.77.0", {"position": v(266.7, -416.98) * mm});
            skPoint(sketch, "E38.54.78.0", {"position": v(266.7, -423.33) * mm});
            skPoint(sketch, "E38.54.79.0", {"position": v(266.7, -429.68) * mm});
            skPoint(sketch, "E38.54.80.0", {"position": v(266.7, -436.03) * mm});
            skPoint(sketch, "E38.54.81.0", {"position": v(266.7, -442.38) * mm});
            skPoint(sketch, "E38.54.82.0", {"position": v(266.7, -448.73) * mm});
            skPoint(sketch, "E38.54.83.0", {"position": v(266.7, -455.08) * mm});
            skPoint(sketch, "E38.54.84.0", {"position": v(266.7, -461.43) * mm});
            skPoint(sketch, "E38.54.85.0", {"position": v(266.7, -467.78) * mm});
            skPoint(sketch, "E38.54.86.0", {"position": v(266.7, -474.13) * mm});
            skPoint(sketch, "E38.54.87.0", {"position": v(266.7, -480.48) * mm});
            skPoint(sketch, "E38.54.88.0", {"position": v(266.7, -486.83) * mm});
            skPoint(sketch, "E38.54.89.0", {"position": v(266.7, -493.18) * mm});
            skPoint(sketch, "E38.54.90.0", {"position": v(266.7, -499.53) * mm});
            skPoint(sketch, "E38.54.91.0", {"position": v(266.7, -505.88) * mm});
            skPoint(sketch, "E38.54.92.0", {"position": v(266.7, -512.23) * mm});
            skPoint(sketch, "E38.54.93.0", {"position": v(266.7, -518.58) * mm});
            skPoint(sketch, "E38.54.94.0", {"position": v(266.7, -524.93) * mm});
            skPoint(sketch, "E38.54.95.0", {"position": v(266.7, -531.28) * mm});
            skPoint(sketch, "E38.54.96.0", {"position": v(266.7, -537.63) * mm});
            skPoint(sketch, "E38.54.97.0", {"position": v(266.7, -543.98) * mm});
            skPoint(sketch, "E38.54.98.0", {"position": v(266.7, -550.33) * mm});
            skPoint(sketch, "E38.54.99.0", {"position": v(266.7, -556.68) * mm});
            skPoint(sketch, "E38.55.0.0", {"position": v(273.05, 71.97) * mm});
            skPoint(sketch, "E38.55.1.0", {"position": v(273.05, 65.62) * mm});
            skPoint(sketch, "E38.55.2.0", {"position": v(273.05, 59.27) * mm});
            skPoint(sketch, "E38.55.3.0", {"position": v(273.05, 52.92) * mm});
            skPoint(sketch, "E38.55.4.0", {"position": v(273.05, 46.57) * mm});
            skPoint(sketch, "E38.55.5.0", {"position": v(273.05, 40.22) * mm});
            skPoint(sketch, "E38.55.6.0", {"position": v(273.05, 33.87) * mm});
            skPoint(sketch, "E38.55.7.0", {"position": v(273.05, 27.52) * mm});
            skPoint(sketch, "E38.55.8.0", {"position": v(273.05, 21.17) * mm});
            skPoint(sketch, "E38.55.9.0", {"position": v(273.05, 14.82) * mm});
            skPoint(sketch, "E38.55.10.0", {"position": v(273.05, 8.47) * mm});
            skPoint(sketch, "E38.55.11.0", {"position": v(273.05, 2.12) * mm});
            skPoint(sketch, "E38.55.12.0", {"position": v(273.05, -4.23) * mm});
            skPoint(sketch, "E38.55.13.0", {"position": v(273.05, -10.58) * mm});
            skPoint(sketch, "E38.55.14.0", {"position": v(273.05, -16.93) * mm});
            skPoint(sketch, "E38.55.15.0", {"position": v(273.05, -23.28) * mm});
            skPoint(sketch, "E38.55.16.0", {"position": v(273.05, -29.63) * mm});
            skPoint(sketch, "E38.55.17.0", {"position": v(273.05, -35.98) * mm});
            skPoint(sketch, "E38.55.18.0", {"position": v(273.05, -42.33) * mm});
            skPoint(sketch, "E38.55.19.0", {"position": v(273.05, -48.68) * mm});
            skPoint(sketch, "E38.55.20.0", {"position": v(273.05, -55.03) * mm});
            skPoint(sketch, "E38.55.21.0", {"position": v(273.05, -61.38) * mm});
            skPoint(sketch, "E38.55.22.0", {"position": v(273.05, -67.73) * mm});
            skPoint(sketch, "E38.55.23.0", {"position": v(273.05, -74.08) * mm});
            skPoint(sketch, "E38.55.24.0", {"position": v(273.05, -80.43) * mm});
            skPoint(sketch, "E38.55.25.0", {"position": v(273.05, -86.78) * mm});
            skPoint(sketch, "E38.55.26.0", {"position": v(273.05, -93.13) * mm});
            skPoint(sketch, "E38.55.27.0", {"position": v(273.05, -99.48) * mm});
            skPoint(sketch, "E38.55.28.0", {"position": v(273.05, -105.83) * mm});
            skPoint(sketch, "E38.55.29.0", {"position": v(273.05, -112.18) * mm});
            skPoint(sketch, "E38.55.30.0", {"position": v(273.05, -118.53) * mm});
            skPoint(sketch, "E38.55.31.0", {"position": v(273.05, -124.88) * mm});
            skPoint(sketch, "E38.55.32.0", {"position": v(273.05, -131.23) * mm});
            skPoint(sketch, "E38.55.33.0", {"position": v(273.05, -137.58) * mm});
            skPoint(sketch, "E38.55.34.0", {"position": v(273.05, -143.93) * mm});
            skPoint(sketch, "E38.55.35.0", {"position": v(273.05, -150.28) * mm});
            skPoint(sketch, "E38.55.36.0", {"position": v(273.05, -156.63) * mm});
            skPoint(sketch, "E38.55.37.0", {"position": v(273.05, -162.98) * mm});
            skPoint(sketch, "E38.55.38.0", {"position": v(273.05, -169.33) * mm});
            skPoint(sketch, "E38.55.39.0", {"position": v(273.05, -175.68) * mm});
            skPoint(sketch, "E38.55.40.0", {"position": v(273.05, -182.03) * mm});
            skPoint(sketch, "E38.55.41.0", {"position": v(273.05, -188.38) * mm});
            skPoint(sketch, "E38.55.42.0", {"position": v(273.05, -194.73) * mm});
            skPoint(sketch, "E38.55.43.0", {"position": v(273.05, -201.08) * mm});
            skPoint(sketch, "E38.55.44.0", {"position": v(273.05, -207.43) * mm});
            skPoint(sketch, "E38.55.45.0", {"position": v(273.05, -213.78) * mm});
            skPoint(sketch, "E38.55.46.0", {"position": v(273.05, -220.13) * mm});
            skPoint(sketch, "E38.55.47.0", {"position": v(273.05, -226.48) * mm});
            skPoint(sketch, "E38.55.48.0", {"position": v(273.05, -232.83) * mm});
            skPoint(sketch, "E38.55.49.0", {"position": v(273.05, -239.18) * mm});
            skPoint(sketch, "E38.55.50.0", {"position": v(273.05, -245.53) * mm});
            skPoint(sketch, "E38.55.51.0", {"position": v(273.05, -251.88) * mm});
            skPoint(sketch, "E38.55.52.0", {"position": v(273.05, -258.23) * mm});
            skPoint(sketch, "E38.55.53.0", {"position": v(273.05, -264.58) * mm});
            skPoint(sketch, "E38.55.54.0", {"position": v(273.05, -270.93) * mm});
            skPoint(sketch, "E38.55.55.0", {"position": v(273.05, -277.28) * mm});
            skPoint(sketch, "E38.55.56.0", {"position": v(273.05, -283.63) * mm});
            skPoint(sketch, "E38.55.57.0", {"position": v(273.05, -289.98) * mm});
            skPoint(sketch, "E38.55.58.0", {"position": v(273.05, -296.33) * mm});
            skPoint(sketch, "E38.55.59.0", {"position": v(273.05, -302.68) * mm});
            skPoint(sketch, "E38.55.60.0", {"position": v(273.05, -309.03) * mm});
            skPoint(sketch, "E38.55.61.0", {"position": v(273.05, -315.38) * mm});
            skPoint(sketch, "E38.55.62.0", {"position": v(273.05, -321.73) * mm});
            skPoint(sketch, "E38.55.63.0", {"position": v(273.05, -328.08) * mm});
            skPoint(sketch, "E38.55.64.0", {"position": v(273.05, -334.43) * mm});
            skPoint(sketch, "E38.55.65.0", {"position": v(273.05, -340.78) * mm});
            skPoint(sketch, "E38.55.66.0", {"position": v(273.05, -347.13) * mm});
            skPoint(sketch, "E38.55.67.0", {"position": v(273.05, -353.48) * mm});
            skPoint(sketch, "E38.55.68.0", {"position": v(273.05, -359.83) * mm});
            skPoint(sketch, "E38.55.69.0", {"position": v(273.05, -366.18) * mm});
            skPoint(sketch, "E38.55.70.0", {"position": v(273.05, -372.53) * mm});
            skPoint(sketch, "E38.55.71.0", {"position": v(273.05, -378.88) * mm});
            skPoint(sketch, "E38.55.72.0", {"position": v(273.05, -385.23) * mm});
            skPoint(sketch, "E38.55.73.0", {"position": v(273.05, -391.58) * mm});
            skPoint(sketch, "E38.55.74.0", {"position": v(273.05, -397.93) * mm});
            skPoint(sketch, "E38.55.75.0", {"position": v(273.05, -404.28) * mm});
            skPoint(sketch, "E38.55.76.0", {"position": v(273.05, -410.63) * mm});
            skPoint(sketch, "E38.55.77.0", {"position": v(273.05, -416.98) * mm});
            skPoint(sketch, "E38.55.78.0", {"position": v(273.05, -423.33) * mm});
            skPoint(sketch, "E38.55.79.0", {"position": v(273.05, -429.68) * mm});
            skPoint(sketch, "E38.55.80.0", {"position": v(273.05, -436.03) * mm});
            skPoint(sketch, "E38.55.81.0", {"position": v(273.05, -442.38) * mm});
            skPoint(sketch, "E38.55.82.0", {"position": v(273.05, -448.73) * mm});
            skPoint(sketch, "E38.55.83.0", {"position": v(273.05, -455.08) * mm});
            skPoint(sketch, "E38.55.84.0", {"position": v(273.05, -461.43) * mm});
            skPoint(sketch, "E38.55.85.0", {"position": v(273.05, -467.78) * mm});
            skPoint(sketch, "E38.55.86.0", {"position": v(273.05, -474.13) * mm});
            skPoint(sketch, "E38.55.87.0", {"position": v(273.05, -480.48) * mm});
            skPoint(sketch, "E38.55.88.0", {"position": v(273.05, -486.83) * mm});
            skPoint(sketch, "E38.55.89.0", {"position": v(273.05, -493.18) * mm});
            skPoint(sketch, "E38.55.90.0", {"position": v(273.05, -499.53) * mm});
            skPoint(sketch, "E38.55.91.0", {"position": v(273.05, -505.88) * mm});
            skPoint(sketch, "E38.55.92.0", {"position": v(273.05, -512.23) * mm});
            skPoint(sketch, "E38.55.93.0", {"position": v(273.05, -518.58) * mm});
            skPoint(sketch, "E38.55.94.0", {"position": v(273.05, -524.93) * mm});
            skPoint(sketch, "E38.55.95.0", {"position": v(273.05, -531.28) * mm});
            skPoint(sketch, "E38.55.96.0", {"position": v(273.05, -537.63) * mm});
            skPoint(sketch, "E38.55.97.0", {"position": v(273.05, -543.98) * mm});
            skPoint(sketch, "E38.55.98.0", {"position": v(273.05, -550.33) * mm});
            skPoint(sketch, "E38.55.99.0", {"position": v(273.05, -556.68) * mm});
            skPoint(sketch, "E38.56.0.0", {"position": v(279.4, 71.97) * mm});
            skPoint(sketch, "E38.56.1.0", {"position": v(279.4, 65.62) * mm});
            skPoint(sketch, "E38.56.2.0", {"position": v(279.4, 59.27) * mm});
            skPoint(sketch, "E38.56.3.0", {"position": v(279.4, 52.92) * mm});
            skPoint(sketch, "E38.56.4.0", {"position": v(279.4, 46.57) * mm});
            skPoint(sketch, "E38.56.5.0", {"position": v(279.4, 40.22) * mm});
            skPoint(sketch, "E38.56.6.0", {"position": v(279.4, 33.87) * mm});
            skPoint(sketch, "E38.56.7.0", {"position": v(279.4, 27.52) * mm});
            skPoint(sketch, "E38.56.8.0", {"position": v(279.4, 21.17) * mm});
            skPoint(sketch, "E38.56.9.0", {"position": v(279.4, 14.82) * mm});
            skPoint(sketch, "E38.56.10.0", {"position": v(279.4, 8.47) * mm});
            skPoint(sketch, "E38.56.11.0", {"position": v(279.4, 2.12) * mm});
            skPoint(sketch, "E38.56.12.0", {"position": v(279.4, -4.23) * mm});
            skPoint(sketch, "E38.56.13.0", {"position": v(279.4, -10.58) * mm});
            skPoint(sketch, "E38.56.14.0", {"position": v(279.4, -16.93) * mm});
            skPoint(sketch, "E38.56.15.0", {"position": v(279.4, -23.28) * mm});
            skPoint(sketch, "E38.56.16.0", {"position": v(279.4, -29.63) * mm});
            skPoint(sketch, "E38.56.17.0", {"position": v(279.4, -35.98) * mm});
            skPoint(sketch, "E38.56.18.0", {"position": v(279.4, -42.33) * mm});
            skPoint(sketch, "E38.56.19.0", {"position": v(279.4, -48.68) * mm});
            skPoint(sketch, "E38.56.20.0", {"position": v(279.4, -55.03) * mm});
            skPoint(sketch, "E38.56.21.0", {"position": v(279.4, -61.38) * mm});
            skPoint(sketch, "E38.56.22.0", {"position": v(279.4, -67.73) * mm});
            skPoint(sketch, "E38.56.23.0", {"position": v(279.4, -74.08) * mm});
            skPoint(sketch, "E38.56.24.0", {"position": v(279.4, -80.43) * mm});
            skPoint(sketch, "E38.56.25.0", {"position": v(279.4, -86.78) * mm});
            skPoint(sketch, "E38.56.26.0", {"position": v(279.4, -93.13) * mm});
            skPoint(sketch, "E38.56.27.0", {"position": v(279.4, -99.48) * mm});
            skPoint(sketch, "E38.56.28.0", {"position": v(279.4, -105.83) * mm});
            skPoint(sketch, "E38.56.29.0", {"position": v(279.4, -112.18) * mm});
            skPoint(sketch, "E38.56.30.0", {"position": v(279.4, -118.53) * mm});
            skPoint(sketch, "E38.56.31.0", {"position": v(279.4, -124.88) * mm});
            skPoint(sketch, "E38.56.32.0", {"position": v(279.4, -131.23) * mm});
            skPoint(sketch, "E38.56.33.0", {"position": v(279.4, -137.58) * mm});
            skPoint(sketch, "E38.56.34.0", {"position": v(279.4, -143.93) * mm});
            skPoint(sketch, "E38.56.35.0", {"position": v(279.4, -150.28) * mm});
            skPoint(sketch, "E38.56.36.0", {"position": v(279.4, -156.63) * mm});
            skPoint(sketch, "E38.56.37.0", {"position": v(279.4, -162.98) * mm});
            skPoint(sketch, "E38.56.38.0", {"position": v(279.4, -169.33) * mm});
            skPoint(sketch, "E38.56.39.0", {"position": v(279.4, -175.68) * mm});
            skPoint(sketch, "E38.56.40.0", {"position": v(279.4, -182.03) * mm});
            skPoint(sketch, "E38.56.41.0", {"position": v(279.4, -188.38) * mm});
            skPoint(sketch, "E38.56.42.0", {"position": v(279.4, -194.73) * mm});
            skPoint(sketch, "E38.56.43.0", {"position": v(279.4, -201.08) * mm});
            skPoint(sketch, "E38.56.44.0", {"position": v(279.4, -207.43) * mm});
            skPoint(sketch, "E38.56.45.0", {"position": v(279.4, -213.78) * mm});
            skPoint(sketch, "E38.56.46.0", {"position": v(279.4, -220.13) * mm});
            skPoint(sketch, "E38.56.47.0", {"position": v(279.4, -226.48) * mm});
            skPoint(sketch, "E38.56.48.0", {"position": v(279.4, -232.83) * mm});
            skPoint(sketch, "E38.56.49.0", {"position": v(279.4, -239.18) * mm});
            skPoint(sketch, "E38.56.50.0", {"position": v(279.4, -245.53) * mm});
            skPoint(sketch, "E38.56.51.0", {"position": v(279.4, -251.88) * mm});
            skPoint(sketch, "E38.56.52.0", {"position": v(279.4, -258.23) * mm});
            skPoint(sketch, "E38.56.53.0", {"position": v(279.4, -264.58) * mm});
            skPoint(sketch, "E38.56.54.0", {"position": v(279.4, -270.93) * mm});
            skPoint(sketch, "E38.56.55.0", {"position": v(279.4, -277.28) * mm});
            skPoint(sketch, "E38.56.56.0", {"position": v(279.4, -283.63) * mm});
            skPoint(sketch, "E38.56.57.0", {"position": v(279.4, -289.98) * mm});
            skPoint(sketch, "E38.56.58.0", {"position": v(279.4, -296.33) * mm});
            skPoint(sketch, "E38.56.59.0", {"position": v(279.4, -302.68) * mm});
            skPoint(sketch, "E38.56.60.0", {"position": v(279.4, -309.03) * mm});
            skPoint(sketch, "E38.56.61.0", {"position": v(279.4, -315.38) * mm});
            skPoint(sketch, "E38.56.62.0", {"position": v(279.4, -321.73) * mm});
            skPoint(sketch, "E38.56.63.0", {"position": v(279.4, -328.08) * mm});
            skPoint(sketch, "E38.56.64.0", {"position": v(279.4, -334.43) * mm});
            skPoint(sketch, "E38.56.65.0", {"position": v(279.4, -340.78) * mm});
            skPoint(sketch, "E38.56.66.0", {"position": v(279.4, -347.13) * mm});
            skPoint(sketch, "E38.56.67.0", {"position": v(279.4, -353.48) * mm});
            skPoint(sketch, "E38.56.68.0", {"position": v(279.4, -359.83) * mm});
            skPoint(sketch, "E38.56.69.0", {"position": v(279.4, -366.18) * mm});
            skPoint(sketch, "E38.56.70.0", {"position": v(279.4, -372.53) * mm});
            skPoint(sketch, "E38.56.71.0", {"position": v(279.4, -378.88) * mm});
            skPoint(sketch, "E38.56.72.0", {"position": v(279.4, -385.23) * mm});
            skPoint(sketch, "E38.56.73.0", {"position": v(279.4, -391.58) * mm});
            skPoint(sketch, "E38.56.74.0", {"position": v(279.4, -397.93) * mm});
            skPoint(sketch, "E38.56.75.0", {"position": v(279.4, -404.28) * mm});
            skPoint(sketch, "E38.56.76.0", {"position": v(279.4, -410.63) * mm});
            skPoint(sketch, "E38.56.77.0", {"position": v(279.4, -416.98) * mm});
            skPoint(sketch, "E38.56.78.0", {"position": v(279.4, -423.33) * mm});
            skPoint(sketch, "E38.56.79.0", {"position": v(279.4, -429.68) * mm});
            skPoint(sketch, "E38.56.80.0", {"position": v(279.4, -436.03) * mm});
            skPoint(sketch, "E38.56.81.0", {"position": v(279.4, -442.38) * mm});
            skPoint(sketch, "E38.56.82.0", {"position": v(279.4, -448.73) * mm});
            skPoint(sketch, "E38.56.83.0", {"position": v(279.4, -455.08) * mm});
            skPoint(sketch, "E38.56.84.0", {"position": v(279.4, -461.43) * mm});
            skPoint(sketch, "E38.56.85.0", {"position": v(279.4, -467.78) * mm});
            skPoint(sketch, "E38.56.86.0", {"position": v(279.4, -474.13) * mm});
            skPoint(sketch, "E38.56.87.0", {"position": v(279.4, -480.48) * mm});
            skPoint(sketch, "E38.56.88.0", {"position": v(279.4, -486.83) * mm});
            skPoint(sketch, "E38.56.89.0", {"position": v(279.4, -493.18) * mm});
            skPoint(sketch, "E38.56.90.0", {"position": v(279.4, -499.53) * mm});
            skPoint(sketch, "E38.56.91.0", {"position": v(279.4, -505.88) * mm});
            skPoint(sketch, "E38.56.92.0", {"position": v(279.4, -512.23) * mm});
            skPoint(sketch, "E38.56.93.0", {"position": v(279.4, -518.58) * mm});
            skPoint(sketch, "E38.56.94.0", {"position": v(279.4, -524.93) * mm});
            skPoint(sketch, "E38.56.95.0", {"position": v(279.4, -531.28) * mm});
            skPoint(sketch, "E38.56.96.0", {"position": v(279.4, -537.63) * mm});
            skPoint(sketch, "E38.56.97.0", {"position": v(279.4, -543.98) * mm});
            skPoint(sketch, "E38.56.98.0", {"position": v(279.4, -550.33) * mm});
            skPoint(sketch, "E38.56.99.0", {"position": v(279.4, -556.68) * mm});
            skPoint(sketch, "E38.57.0.0", {"position": v(285.75, 71.97) * mm});
            skPoint(sketch, "E38.57.1.0", {"position": v(285.75, 65.62) * mm});
            skPoint(sketch, "E38.57.2.0", {"position": v(285.75, 59.27) * mm});
            skPoint(sketch, "E38.57.3.0", {"position": v(285.75, 52.92) * mm});
            skPoint(sketch, "E38.57.4.0", {"position": v(285.75, 46.57) * mm});
            skPoint(sketch, "E38.57.5.0", {"position": v(285.75, 40.22) * mm});
            skPoint(sketch, "E38.57.6.0", {"position": v(285.75, 33.87) * mm});
            skPoint(sketch, "E38.57.7.0", {"position": v(285.75, 27.52) * mm});
            skPoint(sketch, "E38.57.8.0", {"position": v(285.75, 21.17) * mm});
            skPoint(sketch, "E38.57.9.0", {"position": v(285.75, 14.82) * mm});
            skPoint(sketch, "E38.57.10.0", {"position": v(285.75, 8.47) * mm});
            skPoint(sketch, "E38.57.11.0", {"position": v(285.75, 2.12) * mm});
            skPoint(sketch, "E38.57.12.0", {"position": v(285.75, -4.23) * mm});
            skPoint(sketch, "E38.57.13.0", {"position": v(285.75, -10.58) * mm});
            skPoint(sketch, "E38.57.14.0", {"position": v(285.75, -16.93) * mm});
            skPoint(sketch, "E38.57.15.0", {"position": v(285.75, -23.28) * mm});
            skPoint(sketch, "E38.57.16.0", {"position": v(285.75, -29.63) * mm});
            skPoint(sketch, "E38.57.17.0", {"position": v(285.75, -35.98) * mm});
            skPoint(sketch, "E38.57.18.0", {"position": v(285.75, -42.33) * mm});
            skPoint(sketch, "E38.57.19.0", {"position": v(285.75, -48.68) * mm});
            skPoint(sketch, "E38.57.20.0", {"position": v(285.75, -55.03) * mm});
            skPoint(sketch, "E38.57.21.0", {"position": v(285.75, -61.38) * mm});
            skPoint(sketch, "E38.57.22.0", {"position": v(285.75, -67.73) * mm});
            skPoint(sketch, "E38.57.23.0", {"position": v(285.75, -74.08) * mm});
            skPoint(sketch, "E38.57.24.0", {"position": v(285.75, -80.43) * mm});
            skPoint(sketch, "E38.57.25.0", {"position": v(285.75, -86.78) * mm});
            skPoint(sketch, "E38.57.26.0", {"position": v(285.75, -93.13) * mm});
            skPoint(sketch, "E38.57.27.0", {"position": v(285.75, -99.48) * mm});
            skPoint(sketch, "E38.57.28.0", {"position": v(285.75, -105.83) * mm});
            skPoint(sketch, "E38.57.29.0", {"position": v(285.75, -112.18) * mm});
            skPoint(sketch, "E38.57.30.0", {"position": v(285.75, -118.53) * mm});
            skPoint(sketch, "E38.57.31.0", {"position": v(285.75, -124.88) * mm});
            skPoint(sketch, "E38.57.32.0", {"position": v(285.75, -131.23) * mm});
            skPoint(sketch, "E38.57.33.0", {"position": v(285.75, -137.58) * mm});
            skPoint(sketch, "E38.57.34.0", {"position": v(285.75, -143.93) * mm});
            skPoint(sketch, "E38.57.35.0", {"position": v(285.75, -150.28) * mm});
            skPoint(sketch, "E38.57.36.0", {"position": v(285.75, -156.63) * mm});
            skPoint(sketch, "E38.57.37.0", {"position": v(285.75, -162.98) * mm});
            skPoint(sketch, "E38.57.38.0", {"position": v(285.75, -169.33) * mm});
            skPoint(sketch, "E38.57.39.0", {"position": v(285.75, -175.68) * mm});
            skPoint(sketch, "E38.57.40.0", {"position": v(285.75, -182.03) * mm});
            skPoint(sketch, "E38.57.41.0", {"position": v(285.75, -188.38) * mm});
            skPoint(sketch, "E38.57.42.0", {"position": v(285.75, -194.73) * mm});
            skPoint(sketch, "E38.57.43.0", {"position": v(285.75, -201.08) * mm});
            skPoint(sketch, "E38.57.44.0", {"position": v(285.75, -207.43) * mm});
            skPoint(sketch, "E38.57.45.0", {"position": v(285.75, -213.78) * mm});
            skPoint(sketch, "E38.57.46.0", {"position": v(285.75, -220.13) * mm});
            skPoint(sketch, "E38.57.47.0", {"position": v(285.75, -226.48) * mm});
            skPoint(sketch, "E38.57.48.0", {"position": v(285.75, -232.83) * mm});
            skPoint(sketch, "E38.57.49.0", {"position": v(285.75, -239.18) * mm});
            skPoint(sketch, "E38.57.50.0", {"position": v(285.75, -245.53) * mm});
            skPoint(sketch, "E38.57.51.0", {"position": v(285.75, -251.88) * mm});
            skPoint(sketch, "E38.57.52.0", {"position": v(285.75, -258.23) * mm});
            skPoint(sketch, "E38.57.53.0", {"position": v(285.75, -264.58) * mm});
            skPoint(sketch, "E38.57.54.0", {"position": v(285.75, -270.93) * mm});
            skPoint(sketch, "E38.57.55.0", {"position": v(285.75, -277.28) * mm});
            skPoint(sketch, "E38.57.56.0", {"position": v(285.75, -283.63) * mm});
            skPoint(sketch, "E38.57.57.0", {"position": v(285.75, -289.98) * mm});
            skPoint(sketch, "E38.57.58.0", {"position": v(285.75, -296.33) * mm});
            skPoint(sketch, "E38.57.59.0", {"position": v(285.75, -302.68) * mm});
            skPoint(sketch, "E38.57.60.0", {"position": v(285.75, -309.03) * mm});
            skPoint(sketch, "E38.57.61.0", {"position": v(285.75, -315.38) * mm});
            skPoint(sketch, "E38.57.62.0", {"position": v(285.75, -321.73) * mm});
            skPoint(sketch, "E38.57.63.0", {"position": v(285.75, -328.08) * mm});
            skPoint(sketch, "E38.57.64.0", {"position": v(285.75, -334.43) * mm});
            skPoint(sketch, "E38.57.65.0", {"position": v(285.75, -340.78) * mm});
            skPoint(sketch, "E38.57.66.0", {"position": v(285.75, -347.13) * mm});
            skPoint(sketch, "E38.57.67.0", {"position": v(285.75, -353.48) * mm});
            skPoint(sketch, "E38.57.68.0", {"position": v(285.75, -359.83) * mm});
            skPoint(sketch, "E38.57.69.0", {"position": v(285.75, -366.18) * mm});
            skPoint(sketch, "E38.57.70.0", {"position": v(285.75, -372.53) * mm});
            skPoint(sketch, "E38.57.71.0", {"position": v(285.75, -378.88) * mm});
            skPoint(sketch, "E38.57.72.0", {"position": v(285.75, -385.23) * mm});
            skPoint(sketch, "E38.57.73.0", {"position": v(285.75, -391.58) * mm});
            skPoint(sketch, "E38.57.74.0", {"position": v(285.75, -397.93) * mm});
            skPoint(sketch, "E38.57.75.0", {"position": v(285.75, -404.28) * mm});
            skPoint(sketch, "E38.57.76.0", {"position": v(285.75, -410.63) * mm});
            skPoint(sketch, "E38.57.77.0", {"position": v(285.75, -416.98) * mm});
            skPoint(sketch, "E38.57.78.0", {"position": v(285.75, -423.33) * mm});
            skPoint(sketch, "E38.57.79.0", {"position": v(285.75, -429.68) * mm});
            skPoint(sketch, "E38.57.80.0", {"position": v(285.75, -436.03) * mm});
            skPoint(sketch, "E38.57.81.0", {"position": v(285.75, -442.38) * mm});
            skPoint(sketch, "E38.57.82.0", {"position": v(285.75, -448.73) * mm});
            skPoint(sketch, "E38.57.83.0", {"position": v(285.75, -455.08) * mm});
            skPoint(sketch, "E38.57.84.0", {"position": v(285.75, -461.43) * mm});
            skPoint(sketch, "E38.57.85.0", {"position": v(285.75, -467.78) * mm});
            skPoint(sketch, "E38.57.86.0", {"position": v(285.75, -474.13) * mm});
            skPoint(sketch, "E38.57.87.0", {"position": v(285.75, -480.48) * mm});
            skPoint(sketch, "E38.57.88.0", {"position": v(285.75, -486.83) * mm});
            skPoint(sketch, "E38.57.89.0", {"position": v(285.75, -493.18) * mm});
            skPoint(sketch, "E38.57.90.0", {"position": v(285.75, -499.53) * mm});
            skPoint(sketch, "E38.57.91.0", {"position": v(285.75, -505.88) * mm});
            skPoint(sketch, "E38.57.92.0", {"position": v(285.75, -512.23) * mm});
            skPoint(sketch, "E38.57.93.0", {"position": v(285.75, -518.58) * mm});
            skPoint(sketch, "E38.57.94.0", {"position": v(285.75, -524.93) * mm});
            skPoint(sketch, "E38.57.95.0", {"position": v(285.75, -531.28) * mm});
            skPoint(sketch, "E38.57.96.0", {"position": v(285.75, -537.63) * mm});
            skPoint(sketch, "E38.57.97.0", {"position": v(285.75, -543.98) * mm});
            skPoint(sketch, "E38.57.98.0", {"position": v(285.75, -550.33) * mm});
            skPoint(sketch, "E38.57.99.0", {"position": v(285.75, -556.68) * mm});
            skPoint(sketch, "E38.58.0.0", {"position": v(292.1, 71.97) * mm});
            skPoint(sketch, "E38.58.1.0", {"position": v(292.1, 65.62) * mm});
            skPoint(sketch, "E38.58.2.0", {"position": v(292.1, 59.27) * mm});
            skPoint(sketch, "E38.58.3.0", {"position": v(292.1, 52.92) * mm});
            skPoint(sketch, "E38.58.4.0", {"position": v(292.1, 46.57) * mm});
            skPoint(sketch, "E38.58.5.0", {"position": v(292.1, 40.22) * mm});
            skPoint(sketch, "E38.58.6.0", {"position": v(292.1, 33.87) * mm});
            skPoint(sketch, "E38.58.7.0", {"position": v(292.1, 27.52) * mm});
            skPoint(sketch, "E38.58.8.0", {"position": v(292.1, 21.17) * mm});
            skPoint(sketch, "E38.58.9.0", {"position": v(292.1, 14.82) * mm});
            skPoint(sketch, "E38.58.10.0", {"position": v(292.1, 8.47) * mm});
            skPoint(sketch, "E38.58.11.0", {"position": v(292.1, 2.12) * mm});
            skPoint(sketch, "E38.58.12.0", {"position": v(292.1, -4.23) * mm});
            skPoint(sketch, "E38.58.13.0", {"position": v(292.1, -10.58) * mm});
            skPoint(sketch, "E38.58.14.0", {"position": v(292.1, -16.93) * mm});
            skPoint(sketch, "E38.58.15.0", {"position": v(292.1, -23.28) * mm});
            skPoint(sketch, "E38.58.16.0", {"position": v(292.1, -29.63) * mm});
            skPoint(sketch, "E38.58.17.0", {"position": v(292.1, -35.98) * mm});
            skPoint(sketch, "E38.58.18.0", {"position": v(292.1, -42.33) * mm});
            skPoint(sketch, "E38.58.19.0", {"position": v(292.1, -48.68) * mm});
            skPoint(sketch, "E38.58.20.0", {"position": v(292.1, -55.03) * mm});
            skPoint(sketch, "E38.58.21.0", {"position": v(292.1, -61.38) * mm});
            skPoint(sketch, "E38.58.22.0", {"position": v(292.1, -67.73) * mm});
            skPoint(sketch, "E38.58.23.0", {"position": v(292.1, -74.08) * mm});
            skPoint(sketch, "E38.58.24.0", {"position": v(292.1, -80.43) * mm});
            skPoint(sketch, "E38.58.25.0", {"position": v(292.1, -86.78) * mm});
            skPoint(sketch, "E38.58.26.0", {"position": v(292.1, -93.13) * mm});
            skPoint(sketch, "E38.58.27.0", {"position": v(292.1, -99.48) * mm});
            skPoint(sketch, "E38.58.28.0", {"position": v(292.1, -105.83) * mm});
            skPoint(sketch, "E38.58.29.0", {"position": v(292.1, -112.18) * mm});
            skPoint(sketch, "E38.58.30.0", {"position": v(292.1, -118.53) * mm});
            skPoint(sketch, "E38.58.31.0", {"position": v(292.1, -124.88) * mm});
            skPoint(sketch, "E38.58.32.0", {"position": v(292.1, -131.23) * mm});
            skPoint(sketch, "E38.58.33.0", {"position": v(292.1, -137.58) * mm});
            skPoint(sketch, "E38.58.34.0", {"position": v(292.1, -143.93) * mm});
            skPoint(sketch, "E38.58.35.0", {"position": v(292.1, -150.28) * mm});
            skPoint(sketch, "E38.58.36.0", {"position": v(292.1, -156.63) * mm});
            skPoint(sketch, "E38.58.37.0", {"position": v(292.1, -162.98) * mm});
            skPoint(sketch, "E38.58.38.0", {"position": v(292.1, -169.33) * mm});
            skPoint(sketch, "E38.58.39.0", {"position": v(292.1, -175.68) * mm});
            skPoint(sketch, "E38.58.40.0", {"position": v(292.1, -182.03) * mm});
            skPoint(sketch, "E38.58.41.0", {"position": v(292.1, -188.38) * mm});
            skPoint(sketch, "E38.58.42.0", {"position": v(292.1, -194.73) * mm});
            skPoint(sketch, "E38.58.43.0", {"position": v(292.1, -201.08) * mm});
            skPoint(sketch, "E38.58.44.0", {"position": v(292.1, -207.43) * mm});
            skPoint(sketch, "E38.58.45.0", {"position": v(292.1, -213.78) * mm});
            skPoint(sketch, "E38.58.46.0", {"position": v(292.1, -220.13) * mm});
            skPoint(sketch, "E38.58.47.0", {"position": v(292.1, -226.48) * mm});
            skPoint(sketch, "E38.58.48.0", {"position": v(292.1, -232.83) * mm});
            skPoint(sketch, "E38.58.49.0", {"position": v(292.1, -239.18) * mm});
            skPoint(sketch, "E38.58.50.0", {"position": v(292.1, -245.53) * mm});
            skPoint(sketch, "E38.58.51.0", {"position": v(292.1, -251.88) * mm});
            skPoint(sketch, "E38.58.52.0", {"position": v(292.1, -258.23) * mm});
            skPoint(sketch, "E38.58.53.0", {"position": v(292.1, -264.58) * mm});
            skPoint(sketch, "E38.58.54.0", {"position": v(292.1, -270.93) * mm});
            skPoint(sketch, "E38.58.55.0", {"position": v(292.1, -277.28) * mm});
            skPoint(sketch, "E38.58.56.0", {"position": v(292.1, -283.63) * mm});
            skPoint(sketch, "E38.58.57.0", {"position": v(292.1, -289.98) * mm});
            skPoint(sketch, "E38.58.58.0", {"position": v(292.1, -296.33) * mm});
            skPoint(sketch, "E38.58.59.0", {"position": v(292.1, -302.68) * mm});
            skPoint(sketch, "E38.58.60.0", {"position": v(292.1, -309.03) * mm});
            skPoint(sketch, "E38.58.61.0", {"position": v(292.1, -315.38) * mm});
            skPoint(sketch, "E38.58.62.0", {"position": v(292.1, -321.73) * mm});
            skPoint(sketch, "E38.58.63.0", {"position": v(292.1, -328.08) * mm});
            skPoint(sketch, "E38.58.64.0", {"position": v(292.1, -334.43) * mm});
            skPoint(sketch, "E38.58.65.0", {"position": v(292.1, -340.78) * mm});
            skPoint(sketch, "E38.58.66.0", {"position": v(292.1, -347.13) * mm});
            skPoint(sketch, "E38.58.67.0", {"position": v(292.1, -353.48) * mm});
            skPoint(sketch, "E38.58.68.0", {"position": v(292.1, -359.83) * mm});
            skPoint(sketch, "E38.58.69.0", {"position": v(292.1, -366.18) * mm});
            skPoint(sketch, "E38.58.70.0", {"position": v(292.1, -372.53) * mm});
            skPoint(sketch, "E38.58.71.0", {"position": v(292.1, -378.88) * mm});
            skPoint(sketch, "E38.58.72.0", {"position": v(292.1, -385.23) * mm});
            skPoint(sketch, "E38.58.73.0", {"position": v(292.1, -391.58) * mm});
            skPoint(sketch, "E38.58.74.0", {"position": v(292.1, -397.93) * mm});
            skPoint(sketch, "E38.58.75.0", {"position": v(292.1, -404.28) * mm});
            skPoint(sketch, "E38.58.76.0", {"position": v(292.1, -410.63) * mm});
            skPoint(sketch, "E38.58.77.0", {"position": v(292.1, -416.98) * mm});
            skPoint(sketch, "E38.58.78.0", {"position": v(292.1, -423.33) * mm});
            skPoint(sketch, "E38.58.79.0", {"position": v(292.1, -429.68) * mm});
            skPoint(sketch, "E38.58.80.0", {"position": v(292.1, -436.03) * mm});
            skPoint(sketch, "E38.58.81.0", {"position": v(292.1, -442.38) * mm});
            skPoint(sketch, "E38.58.82.0", {"position": v(292.1, -448.73) * mm});
            skPoint(sketch, "E38.58.83.0", {"position": v(292.1, -455.08) * mm});
            skPoint(sketch, "E38.58.84.0", {"position": v(292.1, -461.43) * mm});
            skPoint(sketch, "E38.58.85.0", {"position": v(292.1, -467.78) * mm});
            skPoint(sketch, "E38.58.86.0", {"position": v(292.1, -474.13) * mm});
            skPoint(sketch, "E38.58.87.0", {"position": v(292.1, -480.48) * mm});
            skPoint(sketch, "E38.58.88.0", {"position": v(292.1, -486.83) * mm});
            skPoint(sketch, "E38.58.89.0", {"position": v(292.1, -493.18) * mm});
            skPoint(sketch, "E38.58.90.0", {"position": v(292.1, -499.53) * mm});
            skPoint(sketch, "E38.58.91.0", {"position": v(292.1, -505.88) * mm});
            skPoint(sketch, "E38.58.92.0", {"position": v(292.1, -512.23) * mm});
            skPoint(sketch, "E38.58.93.0", {"position": v(292.1, -518.58) * mm});
            skPoint(sketch, "E38.58.94.0", {"position": v(292.1, -524.93) * mm});
            skPoint(sketch, "E38.58.95.0", {"position": v(292.1, -531.28) * mm});
            skPoint(sketch, "E38.58.96.0", {"position": v(292.1, -537.63) * mm});
            skPoint(sketch, "E38.58.97.0", {"position": v(292.1, -543.98) * mm});
            skPoint(sketch, "E38.58.98.0", {"position": v(292.1, -550.33) * mm});
            skPoint(sketch, "E38.58.99.0", {"position": v(292.1, -556.68) * mm});
            skPoint(sketch, "E38.59.0.0", {"position": v(298.45, 71.97) * mm});
            skPoint(sketch, "E38.59.1.0", {"position": v(298.45, 65.62) * mm});
            skPoint(sketch, "E38.59.2.0", {"position": v(298.45, 59.27) * mm});
            skPoint(sketch, "E38.59.3.0", {"position": v(298.45, 52.92) * mm});
            skPoint(sketch, "E38.59.4.0", {"position": v(298.45, 46.57) * mm});
            skPoint(sketch, "E38.59.5.0", {"position": v(298.45, 40.22) * mm});
            skPoint(sketch, "E38.59.6.0", {"position": v(298.45, 33.87) * mm});
            skPoint(sketch, "E38.59.7.0", {"position": v(298.45, 27.52) * mm});
            skPoint(sketch, "E38.59.8.0", {"position": v(298.45, 21.17) * mm});
            skPoint(sketch, "E38.59.9.0", {"position": v(298.45, 14.82) * mm});
            skPoint(sketch, "E38.59.10.0", {"position": v(298.45, 8.47) * mm});
            skPoint(sketch, "E38.59.11.0", {"position": v(298.45, 2.12) * mm});
            skPoint(sketch, "E38.59.12.0", {"position": v(298.45, -4.23) * mm});
            skPoint(sketch, "E38.59.13.0", {"position": v(298.45, -10.58) * mm});
            skPoint(sketch, "E38.59.14.0", {"position": v(298.45, -16.93) * mm});
            skPoint(sketch, "E38.59.15.0", {"position": v(298.45, -23.28) * mm});
            skPoint(sketch, "E38.59.16.0", {"position": v(298.45, -29.63) * mm});
            skPoint(sketch, "E38.59.17.0", {"position": v(298.45, -35.98) * mm});
            skPoint(sketch, "E38.59.18.0", {"position": v(298.45, -42.33) * mm});
            skPoint(sketch, "E38.59.19.0", {"position": v(298.45, -48.68) * mm});
            skPoint(sketch, "E38.59.20.0", {"position": v(298.45, -55.03) * mm});
            skPoint(sketch, "E38.59.21.0", {"position": v(298.45, -61.38) * mm});
            skPoint(sketch, "E38.59.22.0", {"position": v(298.45, -67.73) * mm});
            skPoint(sketch, "E38.59.23.0", {"position": v(298.45, -74.08) * mm});
            skPoint(sketch, "E38.59.24.0", {"position": v(298.45, -80.43) * mm});
            skPoint(sketch, "E38.59.25.0", {"position": v(298.45, -86.78) * mm});
            skPoint(sketch, "E38.59.26.0", {"position": v(298.45, -93.13) * mm});
            skPoint(sketch, "E38.59.27.0", {"position": v(298.45, -99.48) * mm});
            skPoint(sketch, "E38.59.28.0", {"position": v(298.45, -105.83) * mm});
            skPoint(sketch, "E38.59.29.0", {"position": v(298.45, -112.18) * mm});
            skPoint(sketch, "E38.59.30.0", {"position": v(298.45, -118.53) * mm});
            skPoint(sketch, "E38.59.31.0", {"position": v(298.45, -124.88) * mm});
            skPoint(sketch, "E38.59.32.0", {"position": v(298.45, -131.23) * mm});
            skPoint(sketch, "E38.59.33.0", {"position": v(298.45, -137.58) * mm});
            skPoint(sketch, "E38.59.34.0", {"position": v(298.45, -143.93) * mm});
            skPoint(sketch, "E38.59.35.0", {"position": v(298.45, -150.28) * mm});
            skPoint(sketch, "E38.59.36.0", {"position": v(298.45, -156.63) * mm});
            skPoint(sketch, "E38.59.37.0", {"position": v(298.45, -162.98) * mm});
            skPoint(sketch, "E38.59.38.0", {"position": v(298.45, -169.33) * mm});
            skPoint(sketch, "E38.59.39.0", {"position": v(298.45, -175.68) * mm});
            skPoint(sketch, "E38.59.40.0", {"position": v(298.45, -182.03) * mm});
            skPoint(sketch, "E38.59.41.0", {"position": v(298.45, -188.38) * mm});
            skPoint(sketch, "E38.59.42.0", {"position": v(298.45, -194.73) * mm});
            skPoint(sketch, "E38.59.43.0", {"position": v(298.45, -201.08) * mm});
            skPoint(sketch, "E38.59.44.0", {"position": v(298.45, -207.43) * mm});
            skPoint(sketch, "E38.59.45.0", {"position": v(298.45, -213.78) * mm});
            skPoint(sketch, "E38.59.46.0", {"position": v(298.45, -220.13) * mm});
            skPoint(sketch, "E38.59.47.0", {"position": v(298.45, -226.48) * mm});
            skPoint(sketch, "E38.59.48.0", {"position": v(298.45, -232.83) * mm});
            skPoint(sketch, "E38.59.49.0", {"position": v(298.45, -239.18) * mm});
            skPoint(sketch, "E38.59.50.0", {"position": v(298.45, -245.53) * mm});
            skPoint(sketch, "E38.59.51.0", {"position": v(298.45, -251.88) * mm});
            skPoint(sketch, "E38.59.52.0", {"position": v(298.45, -258.23) * mm});
            skPoint(sketch, "E38.59.53.0", {"position": v(298.45, -264.58) * mm});
            skPoint(sketch, "E38.59.54.0", {"position": v(298.45, -270.93) * mm});
            skPoint(sketch, "E38.59.55.0", {"position": v(298.45, -277.28) * mm});
            skPoint(sketch, "E38.59.56.0", {"position": v(298.45, -283.63) * mm});
            skPoint(sketch, "E38.59.57.0", {"position": v(298.45, -289.98) * mm});
            skPoint(sketch, "E38.59.58.0", {"position": v(298.45, -296.33) * mm});
            skPoint(sketch, "E38.59.59.0", {"position": v(298.45, -302.68) * mm});
            skPoint(sketch, "E38.59.60.0", {"position": v(298.45, -309.03) * mm});
            skPoint(sketch, "E38.59.61.0", {"position": v(298.45, -315.38) * mm});
            skPoint(sketch, "E38.59.62.0", {"position": v(298.45, -321.73) * mm});
            skPoint(sketch, "E38.59.63.0", {"position": v(298.45, -328.08) * mm});
            skPoint(sketch, "E38.59.64.0", {"position": v(298.45, -334.43) * mm});
            skPoint(sketch, "E38.59.65.0", {"position": v(298.45, -340.78) * mm});
            skPoint(sketch, "E38.59.66.0", {"position": v(298.45, -347.13) * mm});
            skPoint(sketch, "E38.59.67.0", {"position": v(298.45, -353.48) * mm});
            skPoint(sketch, "E38.59.68.0", {"position": v(298.45, -359.83) * mm});
            skPoint(sketch, "E38.59.69.0", {"position": v(298.45, -366.18) * mm});
            skPoint(sketch, "E38.59.70.0", {"position": v(298.45, -372.53) * mm});
            skPoint(sketch, "E38.59.71.0", {"position": v(298.45, -378.88) * mm});
            skPoint(sketch, "E38.59.72.0", {"position": v(298.45, -385.23) * mm});
            skPoint(sketch, "E38.59.73.0", {"position": v(298.45, -391.58) * mm});
            skPoint(sketch, "E38.59.74.0", {"position": v(298.45, -397.93) * mm});
            skPoint(sketch, "E38.59.75.0", {"position": v(298.45, -404.28) * mm});
            skPoint(sketch, "E38.59.76.0", {"position": v(298.45, -410.63) * mm});
            skPoint(sketch, "E38.59.77.0", {"position": v(298.45, -416.98) * mm});
            skPoint(sketch, "E38.59.78.0", {"position": v(298.45, -423.33) * mm});
            skPoint(sketch, "E38.59.79.0", {"position": v(298.45, -429.68) * mm});
            skPoint(sketch, "E38.59.80.0", {"position": v(298.45, -436.03) * mm});
            skPoint(sketch, "E38.59.81.0", {"position": v(298.45, -442.38) * mm});
            skPoint(sketch, "E38.59.82.0", {"position": v(298.45, -448.73) * mm});
            skPoint(sketch, "E38.59.83.0", {"position": v(298.45, -455.08) * mm});
            skPoint(sketch, "E38.59.84.0", {"position": v(298.45, -461.43) * mm});
            skPoint(sketch, "E38.59.85.0", {"position": v(298.45, -467.78) * mm});
            skPoint(sketch, "E38.59.86.0", {"position": v(298.45, -474.13) * mm});
            skPoint(sketch, "E38.59.87.0", {"position": v(298.45, -480.48) * mm});
            skPoint(sketch, "E38.59.88.0", {"position": v(298.45, -486.83) * mm});
            skPoint(sketch, "E38.59.89.0", {"position": v(298.45, -493.18) * mm});
            skPoint(sketch, "E38.59.90.0", {"position": v(298.45, -499.53) * mm});
            skPoint(sketch, "E38.59.91.0", {"position": v(298.45, -505.88) * mm});
            skPoint(sketch, "E38.59.92.0", {"position": v(298.45, -512.23) * mm});
            skPoint(sketch, "E38.59.93.0", {"position": v(298.45, -518.58) * mm});
            skPoint(sketch, "E38.59.94.0", {"position": v(298.45, -524.93) * mm});
            skPoint(sketch, "E38.59.95.0", {"position": v(298.45, -531.28) * mm});
            skPoint(sketch, "E38.59.96.0", {"position": v(298.45, -537.63) * mm});
            skPoint(sketch, "E38.59.97.0", {"position": v(298.45, -543.98) * mm});
            skPoint(sketch, "E38.59.98.0", {"position": v(298.45, -550.33) * mm});
            skPoint(sketch, "E38.59.99.0", {"position": v(298.45, -556.68) * mm});
            skPoint(sketch, "E38.60.0.0", {"position": v(304.8, 71.97) * mm});
            skPoint(sketch, "E38.60.1.0", {"position": v(304.8, 65.62) * mm});
            skPoint(sketch, "E38.60.2.0", {"position": v(304.8, 59.27) * mm});
            skPoint(sketch, "E38.60.3.0", {"position": v(304.8, 52.92) * mm});
            skPoint(sketch, "E38.60.4.0", {"position": v(304.8, 46.57) * mm});
            skPoint(sketch, "E38.60.5.0", {"position": v(304.8, 40.22) * mm});
            skPoint(sketch, "E38.60.6.0", {"position": v(304.8, 33.87) * mm});
            skPoint(sketch, "E38.60.7.0", {"position": v(304.8, 27.52) * mm});
            skPoint(sketch, "E38.60.8.0", {"position": v(304.8, 21.17) * mm});
            skPoint(sketch, "E38.60.9.0", {"position": v(304.8, 14.82) * mm});
            skPoint(sketch, "E38.60.10.0", {"position": v(304.8, 8.47) * mm});
            skPoint(sketch, "E38.60.11.0", {"position": v(304.8, 2.12) * mm});
            skPoint(sketch, "E38.60.12.0", {"position": v(304.8, -4.23) * mm});
            skPoint(sketch, "E38.60.13.0", {"position": v(304.8, -10.58) * mm});
            skPoint(sketch, "E38.60.14.0", {"position": v(304.8, -16.93) * mm});
            skPoint(sketch, "E38.60.15.0", {"position": v(304.8, -23.28) * mm});
            skPoint(sketch, "E38.60.16.0", {"position": v(304.8, -29.63) * mm});
            skPoint(sketch, "E38.60.17.0", {"position": v(304.8, -35.98) * mm});
            skPoint(sketch, "E38.60.18.0", {"position": v(304.8, -42.33) * mm});
            skPoint(sketch, "E38.60.19.0", {"position": v(304.8, -48.68) * mm});
            skPoint(sketch, "E38.60.20.0", {"position": v(304.8, -55.03) * mm});
            skPoint(sketch, "E38.60.21.0", {"position": v(304.8, -61.38) * mm});
            skPoint(sketch, "E38.60.22.0", {"position": v(304.8, -67.73) * mm});
            skPoint(sketch, "E38.60.23.0", {"position": v(304.8, -74.08) * mm});
            skPoint(sketch, "E38.60.24.0", {"position": v(304.8, -80.43) * mm});
            skPoint(sketch, "E38.60.25.0", {"position": v(304.8, -86.78) * mm});
            skPoint(sketch, "E38.60.26.0", {"position": v(304.8, -93.13) * mm});
            skPoint(sketch, "E38.60.27.0", {"position": v(304.8, -99.48) * mm});
            skPoint(sketch, "E38.60.28.0", {"position": v(304.8, -105.83) * mm});
            skPoint(sketch, "E38.60.29.0", {"position": v(304.8, -112.18) * mm});
            skPoint(sketch, "E38.60.30.0", {"position": v(304.8, -118.53) * mm});
            skPoint(sketch, "E38.60.31.0", {"position": v(304.8, -124.88) * mm});
            skPoint(sketch, "E38.60.32.0", {"position": v(304.8, -131.23) * mm});
            skPoint(sketch, "E38.60.33.0", {"position": v(304.8, -137.58) * mm});
            skPoint(sketch, "E38.60.34.0", {"position": v(304.8, -143.93) * mm});
            skPoint(sketch, "E38.60.35.0", {"position": v(304.8, -150.28) * mm});
            skPoint(sketch, "E38.60.36.0", {"position": v(304.8, -156.63) * mm});
            skPoint(sketch, "E38.60.37.0", {"position": v(304.8, -162.98) * mm});
            skPoint(sketch, "E38.60.38.0", {"position": v(304.8, -169.33) * mm});
            skPoint(sketch, "E38.60.39.0", {"position": v(304.8, -175.68) * mm});
            skPoint(sketch, "E38.60.40.0", {"position": v(304.8, -182.03) * mm});
            skPoint(sketch, "E38.60.41.0", {"position": v(304.8, -188.38) * mm});
            skPoint(sketch, "E38.60.42.0", {"position": v(304.8, -194.73) * mm});
            skPoint(sketch, "E38.60.43.0", {"position": v(304.8, -201.08) * mm});
            skPoint(sketch, "E38.60.44.0", {"position": v(304.8, -207.43) * mm});
            skPoint(sketch, "E38.60.45.0", {"position": v(304.8, -213.78) * mm});
            skPoint(sketch, "E38.60.46.0", {"position": v(304.8, -220.13) * mm});
            skPoint(sketch, "E38.60.47.0", {"position": v(304.8, -226.48) * mm});
            skPoint(sketch, "E38.60.48.0", {"position": v(304.8, -232.83) * mm});
            skPoint(sketch, "E38.60.49.0", {"position": v(304.8, -239.18) * mm});
            skPoint(sketch, "E38.60.50.0", {"position": v(304.8, -245.53) * mm});
            skPoint(sketch, "E38.60.51.0", {"position": v(304.8, -251.88) * mm});
            skPoint(sketch, "E38.60.52.0", {"position": v(304.8, -258.23) * mm});
            skPoint(sketch, "E38.60.53.0", {"position": v(304.8, -264.58) * mm});
            skPoint(sketch, "E38.60.54.0", {"position": v(304.8, -270.93) * mm});
            skPoint(sketch, "E38.60.55.0", {"position": v(304.8, -277.28) * mm});
            skPoint(sketch, "E38.60.56.0", {"position": v(304.8, -283.63) * mm});
            skPoint(sketch, "E38.60.57.0", {"position": v(304.8, -289.98) * mm});
            skPoint(sketch, "E38.60.58.0", {"position": v(304.8, -296.33) * mm});
            skPoint(sketch, "E38.60.59.0", {"position": v(304.8, -302.68) * mm});
            skPoint(sketch, "E38.60.60.0", {"position": v(304.8, -309.03) * mm});
            skPoint(sketch, "E38.60.61.0", {"position": v(304.8, -315.38) * mm});
            skPoint(sketch, "E38.60.62.0", {"position": v(304.8, -321.73) * mm});
            skPoint(sketch, "E38.60.63.0", {"position": v(304.8, -328.08) * mm});
            skPoint(sketch, "E38.60.64.0", {"position": v(304.8, -334.43) * mm});
            skPoint(sketch, "E38.60.65.0", {"position": v(304.8, -340.78) * mm});
            skPoint(sketch, "E38.60.66.0", {"position": v(304.8, -347.13) * mm});
            skPoint(sketch, "E38.60.67.0", {"position": v(304.8, -353.48) * mm});
            skPoint(sketch, "E38.60.68.0", {"position": v(304.8, -359.83) * mm});
            skPoint(sketch, "E38.60.69.0", {"position": v(304.8, -366.18) * mm});
            skPoint(sketch, "E38.60.70.0", {"position": v(304.8, -372.53) * mm});
            skPoint(sketch, "E38.60.71.0", {"position": v(304.8, -378.88) * mm});
            skPoint(sketch, "E38.60.72.0", {"position": v(304.8, -385.23) * mm});
            skPoint(sketch, "E38.60.73.0", {"position": v(304.8, -391.58) * mm});
            skPoint(sketch, "E38.60.74.0", {"position": v(304.8, -397.93) * mm});
            skPoint(sketch, "E38.60.75.0", {"position": v(304.8, -404.28) * mm});
            skPoint(sketch, "E38.60.76.0", {"position": v(304.8, -410.63) * mm});
            skPoint(sketch, "E38.60.77.0", {"position": v(304.8, -416.98) * mm});
            skPoint(sketch, "E38.60.78.0", {"position": v(304.8, -423.33) * mm});
            skPoint(sketch, "E38.60.79.0", {"position": v(304.8, -429.68) * mm});
            skPoint(sketch, "E38.60.80.0", {"position": v(304.8, -436.03) * mm});
            skPoint(sketch, "E38.60.81.0", {"position": v(304.8, -442.38) * mm});
            skPoint(sketch, "E38.60.82.0", {"position": v(304.8, -448.73) * mm});
            skPoint(sketch, "E38.60.83.0", {"position": v(304.8, -455.08) * mm});
            skPoint(sketch, "E38.60.84.0", {"position": v(304.8, -461.43) * mm});
            skPoint(sketch, "E38.60.85.0", {"position": v(304.8, -467.78) * mm});
            skPoint(sketch, "E38.60.86.0", {"position": v(304.8, -474.13) * mm});
            skPoint(sketch, "E38.60.87.0", {"position": v(304.8, -480.48) * mm});
            skPoint(sketch, "E38.60.88.0", {"position": v(304.8, -486.83) * mm});
            skPoint(sketch, "E38.60.89.0", {"position": v(304.8, -493.18) * mm});
            skPoint(sketch, "E38.60.90.0", {"position": v(304.8, -499.53) * mm});
            skPoint(sketch, "E38.60.91.0", {"position": v(304.8, -505.88) * mm});
            skPoint(sketch, "E38.60.92.0", {"position": v(304.8, -512.23) * mm});
            skPoint(sketch, "E38.60.93.0", {"position": v(304.8, -518.58) * mm});
            skPoint(sketch, "E38.60.94.0", {"position": v(304.8, -524.93) * mm});
            skPoint(sketch, "E38.60.95.0", {"position": v(304.8, -531.28) * mm});
            skPoint(sketch, "E38.60.96.0", {"position": v(304.8, -537.63) * mm});
            skPoint(sketch, "E38.60.97.0", {"position": v(304.8, -543.98) * mm});
            skPoint(sketch, "E38.60.98.0", {"position": v(304.8, -550.33) * mm});
            skPoint(sketch, "E38.60.99.0", {"position": v(304.8, -556.68) * mm});
            skPoint(sketch, "E38.61.0.0", {"position": v(311.15, 71.97) * mm});
            skPoint(sketch, "E38.61.1.0", {"position": v(311.15, 65.62) * mm});
            skPoint(sketch, "E38.61.2.0", {"position": v(311.15, 59.27) * mm});
            skPoint(sketch, "E38.61.3.0", {"position": v(311.15, 52.92) * mm});
            skPoint(sketch, "E38.61.4.0", {"position": v(311.15, 46.57) * mm});
            skPoint(sketch, "E38.61.5.0", {"position": v(311.15, 40.22) * mm});
            skPoint(sketch, "E38.61.6.0", {"position": v(311.15, 33.87) * mm});
            skPoint(sketch, "E38.61.7.0", {"position": v(311.15, 27.52) * mm});
            skPoint(sketch, "E38.61.8.0", {"position": v(311.15, 21.17) * mm});
            skPoint(sketch, "E38.61.9.0", {"position": v(311.15, 14.82) * mm});
            skPoint(sketch, "E38.61.10.0", {"position": v(311.15, 8.47) * mm});
            skPoint(sketch, "E38.61.11.0", {"position": v(311.15, 2.12) * mm});
            skPoint(sketch, "E38.61.12.0", {"position": v(311.15, -4.23) * mm});
            skPoint(sketch, "E38.61.13.0", {"position": v(311.15, -10.58) * mm});
            skPoint(sketch, "E38.61.14.0", {"position": v(311.15, -16.93) * mm});
            skPoint(sketch, "E38.61.15.0", {"position": v(311.15, -23.28) * mm});
            skPoint(sketch, "E38.61.16.0", {"position": v(311.15, -29.63) * mm});
            skPoint(sketch, "E38.61.17.0", {"position": v(311.15, -35.98) * mm});
            skPoint(sketch, "E38.61.18.0", {"position": v(311.15, -42.33) * mm});
            skPoint(sketch, "E38.61.19.0", {"position": v(311.15, -48.68) * mm});
            skPoint(sketch, "E38.61.20.0", {"position": v(311.15, -55.03) * mm});
            skPoint(sketch, "E38.61.21.0", {"position": v(311.15, -61.38) * mm});
            skPoint(sketch, "E38.61.22.0", {"position": v(311.15, -67.73) * mm});
            skPoint(sketch, "E38.61.23.0", {"position": v(311.15, -74.08) * mm});
            skPoint(sketch, "E38.61.24.0", {"position": v(311.15, -80.43) * mm});
            skPoint(sketch, "E38.61.25.0", {"position": v(311.15, -86.78) * mm});
            skPoint(sketch, "E38.61.26.0", {"position": v(311.15, -93.13) * mm});
            skPoint(sketch, "E38.61.27.0", {"position": v(311.15, -99.48) * mm});
            skPoint(sketch, "E38.61.28.0", {"position": v(311.15, -105.83) * mm});
            skPoint(sketch, "E38.61.29.0", {"position": v(311.15, -112.18) * mm});
            skPoint(sketch, "E38.61.30.0", {"position": v(311.15, -118.53) * mm});
            skPoint(sketch, "E38.61.31.0", {"position": v(311.15, -124.88) * mm});
            skPoint(sketch, "E38.61.32.0", {"position": v(311.15, -131.23) * mm});
            skPoint(sketch, "E38.61.33.0", {"position": v(311.15, -137.58) * mm});
            skPoint(sketch, "E38.61.34.0", {"position": v(311.15, -143.93) * mm});
            skPoint(sketch, "E38.61.35.0", {"position": v(311.15, -150.28) * mm});
            skPoint(sketch, "E38.61.36.0", {"position": v(311.15, -156.63) * mm});
            skPoint(sketch, "E38.61.37.0", {"position": v(311.15, -162.98) * mm});
            skPoint(sketch, "E38.61.38.0", {"position": v(311.15, -169.33) * mm});
            skPoint(sketch, "E38.61.39.0", {"position": v(311.15, -175.68) * mm});
            skPoint(sketch, "E38.61.40.0", {"position": v(311.15, -182.03) * mm});
            skPoint(sketch, "E38.61.41.0", {"position": v(311.15, -188.38) * mm});
            skPoint(sketch, "E38.61.42.0", {"position": v(311.15, -194.73) * mm});
            skPoint(sketch, "E38.61.43.0", {"position": v(311.15, -201.08) * mm});
            skPoint(sketch, "E38.61.44.0", {"position": v(311.15, -207.43) * mm});
            skPoint(sketch, "E38.61.45.0", {"position": v(311.15, -213.78) * mm});
            skPoint(sketch, "E38.61.46.0", {"position": v(311.15, -220.13) * mm});
            skPoint(sketch, "E38.61.47.0", {"position": v(311.15, -226.48) * mm});
            skPoint(sketch, "E38.61.48.0", {"position": v(311.15, -232.83) * mm});
            skPoint(sketch, "E38.61.49.0", {"position": v(311.15, -239.18) * mm});
            skPoint(sketch, "E38.61.50.0", {"position": v(311.15, -245.53) * mm});
            skPoint(sketch, "E38.61.51.0", {"position": v(311.15, -251.88) * mm});
            skPoint(sketch, "E38.61.52.0", {"position": v(311.15, -258.23) * mm});
            skPoint(sketch, "E38.61.53.0", {"position": v(311.15, -264.58) * mm});
            skPoint(sketch, "E38.61.54.0", {"position": v(311.15, -270.93) * mm});
            skPoint(sketch, "E38.61.55.0", {"position": v(311.15, -277.28) * mm});
            skPoint(sketch, "E38.61.56.0", {"position": v(311.15, -283.63) * mm});
            skPoint(sketch, "E38.61.57.0", {"position": v(311.15, -289.98) * mm});
            skPoint(sketch, "E38.61.58.0", {"position": v(311.15, -296.33) * mm});
            skPoint(sketch, "E38.61.59.0", {"position": v(311.15, -302.68) * mm});
            skPoint(sketch, "E38.61.60.0", {"position": v(311.15, -309.03) * mm});
            skPoint(sketch, "E38.61.61.0", {"position": v(311.15, -315.38) * mm});
            skPoint(sketch, "E38.61.62.0", {"position": v(311.15, -321.73) * mm});
            skPoint(sketch, "E38.61.63.0", {"position": v(311.15, -328.08) * mm});
            skPoint(sketch, "E38.61.64.0", {"position": v(311.15, -334.43) * mm});
            skPoint(sketch, "E38.61.65.0", {"position": v(311.15, -340.78) * mm});
            skPoint(sketch, "E38.61.66.0", {"position": v(311.15, -347.13) * mm});
            skPoint(sketch, "E38.61.67.0", {"position": v(311.15, -353.48) * mm});
            skPoint(sketch, "E38.61.68.0", {"position": v(311.15, -359.83) * mm});
            skPoint(sketch, "E38.61.69.0", {"position": v(311.15, -366.18) * mm});
            skPoint(sketch, "E38.61.70.0", {"position": v(311.15, -372.53) * mm});
            skPoint(sketch, "E38.61.71.0", {"position": v(311.15, -378.88) * mm});
            skPoint(sketch, "E38.61.72.0", {"position": v(311.15, -385.23) * mm});
            skPoint(sketch, "E38.61.73.0", {"position": v(311.15, -391.58) * mm});
            skPoint(sketch, "E38.61.74.0", {"position": v(311.15, -397.93) * mm});
            skPoint(sketch, "E38.61.75.0", {"position": v(311.15, -404.28) * mm});
            skPoint(sketch, "E38.61.76.0", {"position": v(311.15, -410.63) * mm});
            skPoint(sketch, "E38.61.77.0", {"position": v(311.15, -416.98) * mm});
            skPoint(sketch, "E38.61.78.0", {"position": v(311.15, -423.33) * mm});
            skPoint(sketch, "E38.61.79.0", {"position": v(311.15, -429.68) * mm});
            skPoint(sketch, "E38.61.80.0", {"position": v(311.15, -436.03) * mm});
            skPoint(sketch, "E38.61.81.0", {"position": v(311.15, -442.38) * mm});
            skPoint(sketch, "E38.61.82.0", {"position": v(311.15, -448.73) * mm});
            skPoint(sketch, "E38.61.83.0", {"position": v(311.15, -455.08) * mm});
            skPoint(sketch, "E38.61.84.0", {"position": v(311.15, -461.43) * mm});
            skPoint(sketch, "E38.61.85.0", {"position": v(311.15, -467.78) * mm});
            skPoint(sketch, "E38.61.86.0", {"position": v(311.15, -474.13) * mm});
            skPoint(sketch, "E38.61.87.0", {"position": v(311.15, -480.48) * mm});
            skPoint(sketch, "E38.61.88.0", {"position": v(311.15, -486.83) * mm});
            skPoint(sketch, "E38.61.89.0", {"position": v(311.15, -493.18) * mm});
            skPoint(sketch, "E38.61.90.0", {"position": v(311.15, -499.53) * mm});
            skPoint(sketch, "E38.61.91.0", {"position": v(311.15, -505.88) * mm});
            skPoint(sketch, "E38.61.92.0", {"position": v(311.15, -512.23) * mm});
            skPoint(sketch, "E38.61.93.0", {"position": v(311.15, -518.58) * mm});
            skPoint(sketch, "E38.61.94.0", {"position": v(311.15, -524.93) * mm});
            skPoint(sketch, "E38.61.95.0", {"position": v(311.15, -531.28) * mm});
            skPoint(sketch, "E38.61.96.0", {"position": v(311.15, -537.63) * mm});
            skPoint(sketch, "E38.61.97.0", {"position": v(311.15, -543.98) * mm});
            skPoint(sketch, "E38.61.98.0", {"position": v(311.15, -550.33) * mm});
            skPoint(sketch, "E38.61.99.0", {"position": v(311.15, -556.68) * mm});
            skPoint(sketch, "E38.62.0.0", {"position": v(317.5, 71.97) * mm});
            skPoint(sketch, "E38.62.1.0", {"position": v(317.5, 65.62) * mm});
            skPoint(sketch, "E38.62.2.0", {"position": v(317.5, 59.27) * mm});
            skPoint(sketch, "E38.62.3.0", {"position": v(317.5, 52.92) * mm});
            skPoint(sketch, "E38.62.4.0", {"position": v(317.5, 46.57) * mm});
            skPoint(sketch, "E38.62.5.0", {"position": v(317.5, 40.22) * mm});
            skPoint(sketch, "E38.62.6.0", {"position": v(317.5, 33.87) * mm});
            skPoint(sketch, "E38.62.7.0", {"position": v(317.5, 27.52) * mm});
            skPoint(sketch, "E38.62.8.0", {"position": v(317.5, 21.17) * mm});
            skPoint(sketch, "E38.62.9.0", {"position": v(317.5, 14.82) * mm});
            skPoint(sketch, "E38.62.10.0", {"position": v(317.5, 8.47) * mm});
            skPoint(sketch, "E38.62.11.0", {"position": v(317.5, 2.12) * mm});
            skPoint(sketch, "E38.62.12.0", {"position": v(317.5, -4.23) * mm});
            skPoint(sketch, "E38.62.13.0", {"position": v(317.5, -10.58) * mm});
            skPoint(sketch, "E38.62.14.0", {"position": v(317.5, -16.93) * mm});
            skPoint(sketch, "E38.62.15.0", {"position": v(317.5, -23.28) * mm});
            skPoint(sketch, "E38.62.16.0", {"position": v(317.5, -29.63) * mm});
            skPoint(sketch, "E38.62.17.0", {"position": v(317.5, -35.98) * mm});
            skPoint(sketch, "E38.62.18.0", {"position": v(317.5, -42.33) * mm});
            skPoint(sketch, "E38.62.19.0", {"position": v(317.5, -48.68) * mm});
            skPoint(sketch, "E38.62.20.0", {"position": v(317.5, -55.03) * mm});
            skPoint(sketch, "E38.62.21.0", {"position": v(317.5, -61.38) * mm});
            skPoint(sketch, "E38.62.22.0", {"position": v(317.5, -67.73) * mm});
            skPoint(sketch, "E38.62.23.0", {"position": v(317.5, -74.08) * mm});
            skPoint(sketch, "E38.62.24.0", {"position": v(317.5, -80.43) * mm});
            skPoint(sketch, "E38.62.25.0", {"position": v(317.5, -86.78) * mm});
            skPoint(sketch, "E38.62.26.0", {"position": v(317.5, -93.13) * mm});
            skPoint(sketch, "E38.62.27.0", {"position": v(317.5, -99.48) * mm});
            skPoint(sketch, "E38.62.28.0", {"position": v(317.5, -105.83) * mm});
            skPoint(sketch, "E38.62.29.0", {"position": v(317.5, -112.18) * mm});
            skPoint(sketch, "E38.62.30.0", {"position": v(317.5, -118.53) * mm});
            skPoint(sketch, "E38.62.31.0", {"position": v(317.5, -124.88) * mm});
            skPoint(sketch, "E38.62.32.0", {"position": v(317.5, -131.23) * mm});
            skPoint(sketch, "E38.62.33.0", {"position": v(317.5, -137.58) * mm});
            skPoint(sketch, "E38.62.34.0", {"position": v(317.5, -143.93) * mm});
            skPoint(sketch, "E38.62.35.0", {"position": v(317.5, -150.28) * mm});
            skPoint(sketch, "E38.62.36.0", {"position": v(317.5, -156.63) * mm});
            skPoint(sketch, "E38.62.37.0", {"position": v(317.5, -162.98) * mm});
            skPoint(sketch, "E38.62.38.0", {"position": v(317.5, -169.33) * mm});
            skPoint(sketch, "E38.62.39.0", {"position": v(317.5, -175.68) * mm});
            skPoint(sketch, "E38.62.40.0", {"position": v(317.5, -182.03) * mm});
            skPoint(sketch, "E38.62.41.0", {"position": v(317.5, -188.38) * mm});
            skPoint(sketch, "E38.62.42.0", {"position": v(317.5, -194.73) * mm});
            skPoint(sketch, "E38.62.43.0", {"position": v(317.5, -201.08) * mm});
            skPoint(sketch, "E38.62.44.0", {"position": v(317.5, -207.43) * mm});
            skPoint(sketch, "E38.62.45.0", {"position": v(317.5, -213.78) * mm});
            skPoint(sketch, "E38.62.46.0", {"position": v(317.5, -220.13) * mm});
            skPoint(sketch, "E38.62.47.0", {"position": v(317.5, -226.48) * mm});
            skPoint(sketch, "E38.62.48.0", {"position": v(317.5, -232.83) * mm});
            skPoint(sketch, "E38.62.49.0", {"position": v(317.5, -239.18) * mm});
            skPoint(sketch, "E38.62.50.0", {"position": v(317.5, -245.53) * mm});
            skPoint(sketch, "E38.62.51.0", {"position": v(317.5, -251.88) * mm});
            skPoint(sketch, "E38.62.52.0", {"position": v(317.5, -258.23) * mm});
            skPoint(sketch, "E38.62.53.0", {"position": v(317.5, -264.58) * mm});
            skPoint(sketch, "E38.62.54.0", {"position": v(317.5, -270.93) * mm});
            skPoint(sketch, "E38.62.55.0", {"position": v(317.5, -277.28) * mm});
            skPoint(sketch, "E38.62.56.0", {"position": v(317.5, -283.63) * mm});
            skPoint(sketch, "E38.62.57.0", {"position": v(317.5, -289.98) * mm});
            skPoint(sketch, "E38.62.58.0", {"position": v(317.5, -296.33) * mm});
            skPoint(sketch, "E38.62.59.0", {"position": v(317.5, -302.68) * mm});
            skPoint(sketch, "E38.62.60.0", {"position": v(317.5, -309.03) * mm});
            skPoint(sketch, "E38.62.61.0", {"position": v(317.5, -315.38) * mm});
            skPoint(sketch, "E38.62.62.0", {"position": v(317.5, -321.73) * mm});
            skPoint(sketch, "E38.62.63.0", {"position": v(317.5, -328.08) * mm});
            skPoint(sketch, "E38.62.64.0", {"position": v(317.5, -334.43) * mm});
            skPoint(sketch, "E38.62.65.0", {"position": v(317.5, -340.78) * mm});
            skPoint(sketch, "E38.62.66.0", {"position": v(317.5, -347.13) * mm});
            skPoint(sketch, "E38.62.67.0", {"position": v(317.5, -353.48) * mm});
            skPoint(sketch, "E38.62.68.0", {"position": v(317.5, -359.83) * mm});
            skPoint(sketch, "E38.62.69.0", {"position": v(317.5, -366.18) * mm});
            skPoint(sketch, "E38.62.70.0", {"position": v(317.5, -372.53) * mm});
            skPoint(sketch, "E38.62.71.0", {"position": v(317.5, -378.88) * mm});
            skPoint(sketch, "E38.62.72.0", {"position": v(317.5, -385.23) * mm});
            skPoint(sketch, "E38.62.73.0", {"position": v(317.5, -391.58) * mm});
            skPoint(sketch, "E38.62.74.0", {"position": v(317.5, -397.93) * mm});
            skPoint(sketch, "E38.62.75.0", {"position": v(317.5, -404.28) * mm});
            skPoint(sketch, "E38.62.76.0", {"position": v(317.5, -410.63) * mm});
            skPoint(sketch, "E38.62.77.0", {"position": v(317.5, -416.98) * mm});
            skPoint(sketch, "E38.62.78.0", {"position": v(317.5, -423.33) * mm});
            skPoint(sketch, "E38.62.79.0", {"position": v(317.5, -429.68) * mm});
            skPoint(sketch, "E38.62.80.0", {"position": v(317.5, -436.03) * mm});
            skPoint(sketch, "E38.62.81.0", {"position": v(317.5, -442.38) * mm});
            skPoint(sketch, "E38.62.82.0", {"position": v(317.5, -448.73) * mm});
            skPoint(sketch, "E38.62.83.0", {"position": v(317.5, -455.08) * mm});
            skPoint(sketch, "E38.62.84.0", {"position": v(317.5, -461.43) * mm});
            skPoint(sketch, "E38.62.85.0", {"position": v(317.5, -467.78) * mm});
            skPoint(sketch, "E38.62.86.0", {"position": v(317.5, -474.13) * mm});
            skPoint(sketch, "E38.62.87.0", {"position": v(317.5, -480.48) * mm});
            skPoint(sketch, "E38.62.88.0", {"position": v(317.5, -486.83) * mm});
            skPoint(sketch, "E38.62.89.0", {"position": v(317.5, -493.18) * mm});
            skPoint(sketch, "E38.62.90.0", {"position": v(317.5, -499.53) * mm});
            skPoint(sketch, "E38.62.91.0", {"position": v(317.5, -505.88) * mm});
            skPoint(sketch, "E38.62.92.0", {"position": v(317.5, -512.23) * mm});
            skPoint(sketch, "E38.62.93.0", {"position": v(317.5, -518.58) * mm});
            skPoint(sketch, "E38.62.94.0", {"position": v(317.5, -524.93) * mm});
            skPoint(sketch, "E38.62.95.0", {"position": v(317.5, -531.28) * mm});
            skPoint(sketch, "E38.62.96.0", {"position": v(317.5, -537.63) * mm});
            skPoint(sketch, "E38.62.97.0", {"position": v(317.5, -543.98) * mm});
            skPoint(sketch, "E38.62.98.0", {"position": v(317.5, -550.33) * mm});
            skPoint(sketch, "E38.62.99.0", {"position": v(317.5, -556.68) * mm});
            skPoint(sketch, "E38.63.0.0", {"position": v(323.85, 71.97) * mm});
            skPoint(sketch, "E38.63.1.0", {"position": v(323.85, 65.62) * mm});
            skPoint(sketch, "E38.63.2.0", {"position": v(323.85, 59.27) * mm});
            skPoint(sketch, "E38.63.3.0", {"position": v(323.85, 52.92) * mm});
            skPoint(sketch, "E38.63.4.0", {"position": v(323.85, 46.57) * mm});
            skPoint(sketch, "E38.63.5.0", {"position": v(323.85, 40.22) * mm});
            skPoint(sketch, "E38.63.6.0", {"position": v(323.85, 33.87) * mm});
            skPoint(sketch, "E38.63.7.0", {"position": v(323.85, 27.52) * mm});
            skPoint(sketch, "E38.63.8.0", {"position": v(323.85, 21.17) * mm});
            skPoint(sketch, "E38.63.9.0", {"position": v(323.85, 14.82) * mm});
            skPoint(sketch, "E38.63.10.0", {"position": v(323.85, 8.47) * mm});
            skPoint(sketch, "E38.63.11.0", {"position": v(323.85, 2.12) * mm});
            skPoint(sketch, "E38.63.12.0", {"position": v(323.85, -4.23) * mm});
            skPoint(sketch, "E38.63.13.0", {"position": v(323.85, -10.58) * mm});
            skPoint(sketch, "E38.63.14.0", {"position": v(323.85, -16.93) * mm});
            skPoint(sketch, "E38.63.15.0", {"position": v(323.85, -23.28) * mm});
            skPoint(sketch, "E38.63.16.0", {"position": v(323.85, -29.63) * mm});
            skPoint(sketch, "E38.63.17.0", {"position": v(323.85, -35.98) * mm});
            skPoint(sketch, "E38.63.18.0", {"position": v(323.85, -42.33) * mm});
            skPoint(sketch, "E38.63.19.0", {"position": v(323.85, -48.68) * mm});
            skPoint(sketch, "E38.63.20.0", {"position": v(323.85, -55.03) * mm});
            skPoint(sketch, "E38.63.21.0", {"position": v(323.85, -61.38) * mm});
            skPoint(sketch, "E38.63.22.0", {"position": v(323.85, -67.73) * mm});
            skPoint(sketch, "E38.63.23.0", {"position": v(323.85, -74.08) * mm});
            skPoint(sketch, "E38.63.24.0", {"position": v(323.85, -80.43) * mm});
            skPoint(sketch, "E38.63.25.0", {"position": v(323.85, -86.78) * mm});
            skPoint(sketch, "E38.63.26.0", {"position": v(323.85, -93.13) * mm});
            skPoint(sketch, "E38.63.27.0", {"position": v(323.85, -99.48) * mm});
            skPoint(sketch, "E38.63.28.0", {"position": v(323.85, -105.83) * mm});
            skPoint(sketch, "E38.63.29.0", {"position": v(323.85, -112.18) * mm});
            skPoint(sketch, "E38.63.30.0", {"position": v(323.85, -118.53) * mm});
            skPoint(sketch, "E38.63.31.0", {"position": v(323.85, -124.88) * mm});
            skPoint(sketch, "E38.63.32.0", {"position": v(323.85, -131.23) * mm});
            skPoint(sketch, "E38.63.33.0", {"position": v(323.85, -137.58) * mm});
            skPoint(sketch, "E38.63.34.0", {"position": v(323.85, -143.93) * mm});
            skPoint(sketch, "E38.63.35.0", {"position": v(323.85, -150.28) * mm});
            skPoint(sketch, "E38.63.36.0", {"position": v(323.85, -156.63) * mm});
            skPoint(sketch, "E38.63.37.0", {"position": v(323.85, -162.98) * mm});
            skPoint(sketch, "E38.63.38.0", {"position": v(323.85, -169.33) * mm});
            skPoint(sketch, "E38.63.39.0", {"position": v(323.85, -175.68) * mm});
            skPoint(sketch, "E38.63.40.0", {"position": v(323.85, -182.03) * mm});
            skPoint(sketch, "E38.63.41.0", {"position": v(323.85, -188.38) * mm});
            skPoint(sketch, "E38.63.42.0", {"position": v(323.85, -194.73) * mm});
            skPoint(sketch, "E38.63.43.0", {"position": v(323.85, -201.08) * mm});
            skPoint(sketch, "E38.63.44.0", {"position": v(323.85, -207.43) * mm});
            skPoint(sketch, "E38.63.45.0", {"position": v(323.85, -213.78) * mm});
            skPoint(sketch, "E38.63.46.0", {"position": v(323.85, -220.13) * mm});
            skPoint(sketch, "E38.63.47.0", {"position": v(323.85, -226.48) * mm});
            skPoint(sketch, "E38.63.48.0", {"position": v(323.85, -232.83) * mm});
            skPoint(sketch, "E38.63.49.0", {"position": v(323.85, -239.18) * mm});
            skPoint(sketch, "E38.63.50.0", {"position": v(323.85, -245.53) * mm});
            skPoint(sketch, "E38.63.51.0", {"position": v(323.85, -251.88) * mm});
            skPoint(sketch, "E38.63.52.0", {"position": v(323.85, -258.23) * mm});
            skPoint(sketch, "E38.63.53.0", {"position": v(323.85, -264.58) * mm});
            skPoint(sketch, "E38.63.54.0", {"position": v(323.85, -270.93) * mm});
            skPoint(sketch, "E38.63.55.0", {"position": v(323.85, -277.28) * mm});
            skPoint(sketch, "E38.63.56.0", {"position": v(323.85, -283.63) * mm});
            skPoint(sketch, "E38.63.57.0", {"position": v(323.85, -289.98) * mm});
            skPoint(sketch, "E38.63.58.0", {"position": v(323.85, -296.33) * mm});
            skPoint(sketch, "E38.63.59.0", {"position": v(323.85, -302.68) * mm});
            skPoint(sketch, "E38.63.60.0", {"position": v(323.85, -309.03) * mm});
            skPoint(sketch, "E38.63.61.0", {"position": v(323.85, -315.38) * mm});
            skPoint(sketch, "E38.63.62.0", {"position": v(323.85, -321.73) * mm});
            skPoint(sketch, "E38.63.63.0", {"position": v(323.85, -328.08) * mm});
            skPoint(sketch, "E38.63.64.0", {"position": v(323.85, -334.43) * mm});
            skPoint(sketch, "E38.63.65.0", {"position": v(323.85, -340.78) * mm});
            skPoint(sketch, "E38.63.66.0", {"position": v(323.85, -347.13) * mm});
            skPoint(sketch, "E38.63.67.0", {"position": v(323.85, -353.48) * mm});
            skPoint(sketch, "E38.63.68.0", {"position": v(323.85, -359.83) * mm});
            skPoint(sketch, "E38.63.69.0", {"position": v(323.85, -366.18) * mm});
            skPoint(sketch, "E38.63.70.0", {"position": v(323.85, -372.53) * mm});
            skPoint(sketch, "E38.63.71.0", {"position": v(323.85, -378.88) * mm});
            skPoint(sketch, "E38.63.72.0", {"position": v(323.85, -385.23) * mm});
            skPoint(sketch, "E38.63.73.0", {"position": v(323.85, -391.58) * mm});
            skPoint(sketch, "E38.63.74.0", {"position": v(323.85, -397.93) * mm});
            skPoint(sketch, "E38.63.75.0", {"position": v(323.85, -404.28) * mm});
            skPoint(sketch, "E38.63.76.0", {"position": v(323.85, -410.63) * mm});
            skPoint(sketch, "E38.63.77.0", {"position": v(323.85, -416.98) * mm});
            skPoint(sketch, "E38.63.78.0", {"position": v(323.85, -423.33) * mm});
            skPoint(sketch, "E38.63.79.0", {"position": v(323.85, -429.68) * mm});
            skPoint(sketch, "E38.63.80.0", {"position": v(323.85, -436.03) * mm});
            skPoint(sketch, "E38.63.81.0", {"position": v(323.85, -442.38) * mm});
            skPoint(sketch, "E38.63.82.0", {"position": v(323.85, -448.73) * mm});
            skPoint(sketch, "E38.63.83.0", {"position": v(323.85, -455.08) * mm});
            skPoint(sketch, "E38.63.84.0", {"position": v(323.85, -461.43) * mm});
            skPoint(sketch, "E38.63.85.0", {"position": v(323.85, -467.78) * mm});
            skPoint(sketch, "E38.63.86.0", {"position": v(323.85, -474.13) * mm});
            skPoint(sketch, "E38.63.87.0", {"position": v(323.85, -480.48) * mm});
            skPoint(sketch, "E38.63.88.0", {"position": v(323.85, -486.83) * mm});
            skPoint(sketch, "E38.63.89.0", {"position": v(323.85, -493.18) * mm});
            skPoint(sketch, "E38.63.90.0", {"position": v(323.85, -499.53) * mm});
            skPoint(sketch, "E38.63.91.0", {"position": v(323.85, -505.88) * mm});
            skPoint(sketch, "E38.63.92.0", {"position": v(323.85, -512.23) * mm});
            skPoint(sketch, "E38.63.93.0", {"position": v(323.85, -518.58) * mm});
            skPoint(sketch, "E38.63.94.0", {"position": v(323.85, -524.93) * mm});
            skPoint(sketch, "E38.63.95.0", {"position": v(323.85, -531.28) * mm});
            skPoint(sketch, "E38.63.96.0", {"position": v(323.85, -537.63) * mm});
            skPoint(sketch, "E38.63.97.0", {"position": v(323.85, -543.98) * mm});
            skPoint(sketch, "E38.63.98.0", {"position": v(323.85, -550.33) * mm});
            skPoint(sketch, "E38.63.99.0", {"position": v(323.85, -556.68) * mm});
            skPoint(sketch, "E38.64.0.0", {"position": v(330.2, 71.97) * mm});
            skPoint(sketch, "E38.64.1.0", {"position": v(330.2, 65.62) * mm});
            skPoint(sketch, "E38.64.2.0", {"position": v(330.2, 59.27) * mm});
            skPoint(sketch, "E38.64.3.0", {"position": v(330.2, 52.92) * mm});
            skPoint(sketch, "E38.64.4.0", {"position": v(330.2, 46.57) * mm});
            skPoint(sketch, "E38.64.5.0", {"position": v(330.2, 40.22) * mm});
            skPoint(sketch, "E38.64.6.0", {"position": v(330.2, 33.87) * mm});
            skPoint(sketch, "E38.64.7.0", {"position": v(330.2, 27.52) * mm});
            skPoint(sketch, "E38.64.8.0", {"position": v(330.2, 21.17) * mm});
            skPoint(sketch, "E38.64.9.0", {"position": v(330.2, 14.82) * mm});
            skPoint(sketch, "E38.64.10.0", {"position": v(330.2, 8.47) * mm});
            skPoint(sketch, "E38.64.11.0", {"position": v(330.2, 2.12) * mm});
            skPoint(sketch, "E38.64.12.0", {"position": v(330.2, -4.23) * mm});
            skPoint(sketch, "E38.64.13.0", {"position": v(330.2, -10.58) * mm});
            skPoint(sketch, "E38.64.14.0", {"position": v(330.2, -16.93) * mm});
            skPoint(sketch, "E38.64.15.0", {"position": v(330.2, -23.28) * mm});
            skPoint(sketch, "E38.64.16.0", {"position": v(330.2, -29.63) * mm});
            skPoint(sketch, "E38.64.17.0", {"position": v(330.2, -35.98) * mm});
            skPoint(sketch, "E38.64.18.0", {"position": v(330.2, -42.33) * mm});
            skPoint(sketch, "E38.64.19.0", {"position": v(330.2, -48.68) * mm});
            skPoint(sketch, "E38.64.20.0", {"position": v(330.2, -55.03) * mm});
            skPoint(sketch, "E38.64.21.0", {"position": v(330.2, -61.38) * mm});
            skPoint(sketch, "E38.64.22.0", {"position": v(330.2, -67.73) * mm});
            skPoint(sketch, "E38.64.23.0", {"position": v(330.2, -74.08) * mm});
            skPoint(sketch, "E38.64.24.0", {"position": v(330.2, -80.43) * mm});
            skPoint(sketch, "E38.64.25.0", {"position": v(330.2, -86.78) * mm});
            skPoint(sketch, "E38.64.26.0", {"position": v(330.2, -93.13) * mm});
            skPoint(sketch, "E38.64.27.0", {"position": v(330.2, -99.48) * mm});
            skPoint(sketch, "E38.64.28.0", {"position": v(330.2, -105.83) * mm});
            skPoint(sketch, "E38.64.29.0", {"position": v(330.2, -112.18) * mm});
            skPoint(sketch, "E38.64.30.0", {"position": v(330.2, -118.53) * mm});
            skPoint(sketch, "E38.64.31.0", {"position": v(330.2, -124.88) * mm});
            skPoint(sketch, "E38.64.32.0", {"position": v(330.2, -131.23) * mm});
            skPoint(sketch, "E38.64.33.0", {"position": v(330.2, -137.58) * mm});
            skPoint(sketch, "E38.64.34.0", {"position": v(330.2, -143.93) * mm});
            skPoint(sketch, "E38.64.35.0", {"position": v(330.2, -150.28) * mm});
            skPoint(sketch, "E38.64.36.0", {"position": v(330.2, -156.63) * mm});
            skPoint(sketch, "E38.64.37.0", {"position": v(330.2, -162.98) * mm});
            skPoint(sketch, "E38.64.38.0", {"position": v(330.2, -169.33) * mm});
            skPoint(sketch, "E38.64.39.0", {"position": v(330.2, -175.68) * mm});
            skPoint(sketch, "E38.64.40.0", {"position": v(330.2, -182.03) * mm});
            skPoint(sketch, "E38.64.41.0", {"position": v(330.2, -188.38) * mm});
            skPoint(sketch, "E38.64.42.0", {"position": v(330.2, -194.73) * mm});
            skPoint(sketch, "E38.64.43.0", {"position": v(330.2, -201.08) * mm});
            skPoint(sketch, "E38.64.44.0", {"position": v(330.2, -207.43) * mm});
            skPoint(sketch, "E38.64.45.0", {"position": v(330.2, -213.78) * mm});
            skPoint(sketch, "E38.64.46.0", {"position": v(330.2, -220.13) * mm});
            skPoint(sketch, "E38.64.47.0", {"position": v(330.2, -226.48) * mm});
            skPoint(sketch, "E38.64.48.0", {"position": v(330.2, -232.83) * mm});
            skPoint(sketch, "E38.64.49.0", {"position": v(330.2, -239.18) * mm});
            skPoint(sketch, "E38.64.50.0", {"position": v(330.2, -245.53) * mm});
            skPoint(sketch, "E38.64.51.0", {"position": v(330.2, -251.88) * mm});
            skPoint(sketch, "E38.64.52.0", {"position": v(330.2, -258.23) * mm});
            skPoint(sketch, "E38.64.53.0", {"position": v(330.2, -264.58) * mm});
            skPoint(sketch, "E38.64.54.0", {"position": v(330.2, -270.93) * mm});
            skPoint(sketch, "E38.64.55.0", {"position": v(330.2, -277.28) * mm});
            skPoint(sketch, "E38.64.56.0", {"position": v(330.2, -283.63) * mm});
            skPoint(sketch, "E38.64.57.0", {"position": v(330.2, -289.98) * mm});
            skPoint(sketch, "E38.64.58.0", {"position": v(330.2, -296.33) * mm});
            skPoint(sketch, "E38.64.59.0", {"position": v(330.2, -302.68) * mm});
            skPoint(sketch, "E38.64.60.0", {"position": v(330.2, -309.03) * mm});
            skPoint(sketch, "E38.64.61.0", {"position": v(330.2, -315.38) * mm});
            skPoint(sketch, "E38.64.62.0", {"position": v(330.2, -321.73) * mm});
            skPoint(sketch, "E38.64.63.0", {"position": v(330.2, -328.08) * mm});
            skPoint(sketch, "E38.64.64.0", {"position": v(330.2, -334.43) * mm});
            skPoint(sketch, "E38.64.65.0", {"position": v(330.2, -340.78) * mm});
            skPoint(sketch, "E38.64.66.0", {"position": v(330.2, -347.13) * mm});
            skPoint(sketch, "E38.64.67.0", {"position": v(330.2, -353.48) * mm});
            skPoint(sketch, "E38.64.68.0", {"position": v(330.2, -359.83) * mm});
            skPoint(sketch, "E38.64.69.0", {"position": v(330.2, -366.18) * mm});
            skPoint(sketch, "E38.64.70.0", {"position": v(330.2, -372.53) * mm});
            skPoint(sketch, "E38.64.71.0", {"position": v(330.2, -378.88) * mm});
            skPoint(sketch, "E38.64.72.0", {"position": v(330.2, -385.23) * mm});
            skPoint(sketch, "E38.64.73.0", {"position": v(330.2, -391.58) * mm});
            skPoint(sketch, "E38.64.74.0", {"position": v(330.2, -397.93) * mm});
            skPoint(sketch, "E38.64.75.0", {"position": v(330.2, -404.28) * mm});
            skPoint(sketch, "E38.64.76.0", {"position": v(330.2, -410.63) * mm});
            skPoint(sketch, "E38.64.77.0", {"position": v(330.2, -416.98) * mm});
            skPoint(sketch, "E38.64.78.0", {"position": v(330.2, -423.33) * mm});
            skPoint(sketch, "E38.64.79.0", {"position": v(330.2, -429.68) * mm});
            skPoint(sketch, "E38.64.80.0", {"position": v(330.2, -436.03) * mm});
            skPoint(sketch, "E38.64.81.0", {"position": v(330.2, -442.38) * mm});
            skPoint(sketch, "E38.64.82.0", {"position": v(330.2, -448.73) * mm});
            skPoint(sketch, "E38.64.83.0", {"position": v(330.2, -455.08) * mm});
            skPoint(sketch, "E38.64.84.0", {"position": v(330.2, -461.43) * mm});
            skPoint(sketch, "E38.64.85.0", {"position": v(330.2, -467.78) * mm});
            skPoint(sketch, "E38.64.86.0", {"position": v(330.2, -474.13) * mm});
            skPoint(sketch, "E38.64.87.0", {"position": v(330.2, -480.48) * mm});
            skPoint(sketch, "E38.64.88.0", {"position": v(330.2, -486.83) * mm});
            skPoint(sketch, "E38.64.89.0", {"position": v(330.2, -493.18) * mm});
            skPoint(sketch, "E38.64.90.0", {"position": v(330.2, -499.53) * mm});
            skPoint(sketch, "E38.64.91.0", {"position": v(330.2, -505.88) * mm});
            skPoint(sketch, "E38.64.92.0", {"position": v(330.2, -512.23) * mm});
            skPoint(sketch, "E38.64.93.0", {"position": v(330.2, -518.58) * mm});
            skPoint(sketch, "E38.64.94.0", {"position": v(330.2, -524.93) * mm});
            skPoint(sketch, "E38.64.95.0", {"position": v(330.2, -531.28) * mm});
            skPoint(sketch, "E38.64.96.0", {"position": v(330.2, -537.63) * mm});
            skPoint(sketch, "E38.64.97.0", {"position": v(330.2, -543.98) * mm});
            skPoint(sketch, "E38.64.98.0", {"position": v(330.2, -550.33) * mm});
            skPoint(sketch, "E38.64.99.0", {"position": v(330.2, -556.68) * mm});
            skPoint(sketch, "E38.65.0.0", {"position": v(336.55, 71.97) * mm});
            skPoint(sketch, "E38.65.1.0", {"position": v(336.55, 65.62) * mm});
            skPoint(sketch, "E38.65.2.0", {"position": v(336.55, 59.27) * mm});
            skPoint(sketch, "E38.65.3.0", {"position": v(336.55, 52.92) * mm});
            skPoint(sketch, "E38.65.4.0", {"position": v(336.55, 46.57) * mm});
            skPoint(sketch, "E38.65.5.0", {"position": v(336.55, 40.22) * mm});
            skPoint(sketch, "E38.65.6.0", {"position": v(336.55, 33.87) * mm});
            skPoint(sketch, "E38.65.7.0", {"position": v(336.55, 27.52) * mm});
            skPoint(sketch, "E38.65.8.0", {"position": v(336.55, 21.17) * mm});
            skPoint(sketch, "E38.65.9.0", {"position": v(336.55, 14.82) * mm});
            skPoint(sketch, "E38.65.10.0", {"position": v(336.55, 8.47) * mm});
            skPoint(sketch, "E38.65.11.0", {"position": v(336.55, 2.12) * mm});
            skPoint(sketch, "E38.65.12.0", {"position": v(336.55, -4.23) * mm});
            skPoint(sketch, "E38.65.13.0", {"position": v(336.55, -10.58) * mm});
            skPoint(sketch, "E38.65.14.0", {"position": v(336.55, -16.93) * mm});
            skPoint(sketch, "E38.65.15.0", {"position": v(336.55, -23.28) * mm});
            skPoint(sketch, "E38.65.16.0", {"position": v(336.55, -29.63) * mm});
            skPoint(sketch, "E38.65.17.0", {"position": v(336.55, -35.98) * mm});
            skPoint(sketch, "E38.65.18.0", {"position": v(336.55, -42.33) * mm});
            skPoint(sketch, "E38.65.19.0", {"position": v(336.55, -48.68) * mm});
            skPoint(sketch, "E38.65.20.0", {"position": v(336.55, -55.03) * mm});
            skPoint(sketch, "E38.65.21.0", {"position": v(336.55, -61.38) * mm});
            skPoint(sketch, "E38.65.22.0", {"position": v(336.55, -67.73) * mm});
            skPoint(sketch, "E38.65.23.0", {"position": v(336.55, -74.08) * mm});
            skPoint(sketch, "E38.65.24.0", {"position": v(336.55, -80.43) * mm});
            skPoint(sketch, "E38.65.25.0", {"position": v(336.55, -86.78) * mm});
            skPoint(sketch, "E38.65.26.0", {"position": v(336.55, -93.13) * mm});
            skPoint(sketch, "E38.65.27.0", {"position": v(336.55, -99.48) * mm});
            skPoint(sketch, "E38.65.28.0", {"position": v(336.55, -105.83) * mm});
            skPoint(sketch, "E38.65.29.0", {"position": v(336.55, -112.18) * mm});
            skPoint(sketch, "E38.65.30.0", {"position": v(336.55, -118.53) * mm});
            skPoint(sketch, "E38.65.31.0", {"position": v(336.55, -124.88) * mm});
            skPoint(sketch, "E38.65.32.0", {"position": v(336.55, -131.23) * mm});
            skPoint(sketch, "E38.65.33.0", {"position": v(336.55, -137.58) * mm});
            skPoint(sketch, "E38.65.34.0", {"position": v(336.55, -143.93) * mm});
            skPoint(sketch, "E38.65.35.0", {"position": v(336.55, -150.28) * mm});
            skPoint(sketch, "E38.65.36.0", {"position": v(336.55, -156.63) * mm});
            skPoint(sketch, "E38.65.37.0", {"position": v(336.55, -162.98) * mm});
            skPoint(sketch, "E38.65.38.0", {"position": v(336.55, -169.33) * mm});
            skPoint(sketch, "E38.65.39.0", {"position": v(336.55, -175.68) * mm});
            skPoint(sketch, "E38.65.40.0", {"position": v(336.55, -182.03) * mm});
            skPoint(sketch, "E38.65.41.0", {"position": v(336.55, -188.38) * mm});
            skPoint(sketch, "E38.65.42.0", {"position": v(336.55, -194.73) * mm});
            skPoint(sketch, "E38.65.43.0", {"position": v(336.55, -201.08) * mm});
            skPoint(sketch, "E38.65.44.0", {"position": v(336.55, -207.43) * mm});
            skPoint(sketch, "E38.65.45.0", {"position": v(336.55, -213.78) * mm});
            skPoint(sketch, "E38.65.46.0", {"position": v(336.55, -220.13) * mm});
            skPoint(sketch, "E38.65.47.0", {"position": v(336.55, -226.48) * mm});
            skPoint(sketch, "E38.65.48.0", {"position": v(336.55, -232.83) * mm});
            skPoint(sketch, "E38.65.49.0", {"position": v(336.55, -239.18) * mm});
            skPoint(sketch, "E38.65.50.0", {"position": v(336.55, -245.53) * mm});
            skPoint(sketch, "E38.65.51.0", {"position": v(336.55, -251.88) * mm});
            skPoint(sketch, "E38.65.52.0", {"position": v(336.55, -258.23) * mm});
            skPoint(sketch, "E38.65.53.0", {"position": v(336.55, -264.58) * mm});
            skPoint(sketch, "E38.65.54.0", {"position": v(336.55, -270.93) * mm});
            skPoint(sketch, "E38.65.55.0", {"position": v(336.55, -277.28) * mm});
            skPoint(sketch, "E38.65.56.0", {"position": v(336.55, -283.63) * mm});
            skPoint(sketch, "E38.65.57.0", {"position": v(336.55, -289.98) * mm});
            skPoint(sketch, "E38.65.58.0", {"position": v(336.55, -296.33) * mm});
            skPoint(sketch, "E38.65.59.0", {"position": v(336.55, -302.68) * mm});
            skPoint(sketch, "E38.65.60.0", {"position": v(336.55, -309.03) * mm});
            skPoint(sketch, "E38.65.61.0", {"position": v(336.55, -315.38) * mm});
            skPoint(sketch, "E38.65.62.0", {"position": v(336.55, -321.73) * mm});
            skPoint(sketch, "E38.65.63.0", {"position": v(336.55, -328.08) * mm});
            skPoint(sketch, "E38.65.64.0", {"position": v(336.55, -334.43) * mm});
            skPoint(sketch, "E38.65.65.0", {"position": v(336.55, -340.78) * mm});
            skPoint(sketch, "E38.65.66.0", {"position": v(336.55, -347.13) * mm});
            skPoint(sketch, "E38.65.67.0", {"position": v(336.55, -353.48) * mm});
            skPoint(sketch, "E38.65.68.0", {"position": v(336.55, -359.83) * mm});
            skPoint(sketch, "E38.65.69.0", {"position": v(336.55, -366.18) * mm});
            skPoint(sketch, "E38.65.70.0", {"position": v(336.55, -372.53) * mm});
            skPoint(sketch, "E38.65.71.0", {"position": v(336.55, -378.88) * mm});
            skPoint(sketch, "E38.65.72.0", {"position": v(336.55, -385.23) * mm});
            skPoint(sketch, "E38.65.73.0", {"position": v(336.55, -391.58) * mm});
            skPoint(sketch, "E38.65.74.0", {"position": v(336.55, -397.93) * mm});
            skPoint(sketch, "E38.65.75.0", {"position": v(336.55, -404.28) * mm});
            skPoint(sketch, "E38.65.76.0", {"position": v(336.55, -410.63) * mm});
            skPoint(sketch, "E38.65.77.0", {"position": v(336.55, -416.98) * mm});
            skPoint(sketch, "E38.65.78.0", {"position": v(336.55, -423.33) * mm});
            skPoint(sketch, "E38.65.79.0", {"position": v(336.55, -429.68) * mm});
            skPoint(sketch, "E38.65.80.0", {"position": v(336.55, -436.03) * mm});
            skPoint(sketch, "E38.65.81.0", {"position": v(336.55, -442.38) * mm});
            skPoint(sketch, "E38.65.82.0", {"position": v(336.55, -448.73) * mm});
            skPoint(sketch, "E38.65.83.0", {"position": v(336.55, -455.08) * mm});
            skPoint(sketch, "E38.65.84.0", {"position": v(336.55, -461.43) * mm});
            skPoint(sketch, "E38.65.85.0", {"position": v(336.55, -467.78) * mm});
            skPoint(sketch, "E38.65.86.0", {"position": v(336.55, -474.13) * mm});
            skPoint(sketch, "E38.65.87.0", {"position": v(336.55, -480.48) * mm});
            skPoint(sketch, "E38.65.88.0", {"position": v(336.55, -486.83) * mm});
            skPoint(sketch, "E38.65.89.0", {"position": v(336.55, -493.18) * mm});
            skPoint(sketch, "E38.65.90.0", {"position": v(336.55, -499.53) * mm});
            skPoint(sketch, "E38.65.91.0", {"position": v(336.55, -505.88) * mm});
            skPoint(sketch, "E38.65.92.0", {"position": v(336.55, -512.23) * mm});
            skPoint(sketch, "E38.65.93.0", {"position": v(336.55, -518.58) * mm});
            skPoint(sketch, "E38.65.94.0", {"position": v(336.55, -524.93) * mm});
            skPoint(sketch, "E38.65.95.0", {"position": v(336.55, -531.28) * mm});
            skPoint(sketch, "E38.65.96.0", {"position": v(336.55, -537.63) * mm});
            skPoint(sketch, "E38.65.97.0", {"position": v(336.55, -543.98) * mm});
            skPoint(sketch, "E38.65.98.0", {"position": v(336.55, -550.33) * mm});
            skPoint(sketch, "E38.65.99.0", {"position": v(336.55, -556.68) * mm});
            skPoint(sketch, "E38.66.0.0", {"position": v(342.9, 71.97) * mm});
            skPoint(sketch, "E38.66.1.0", {"position": v(342.9, 65.62) * mm});
            skPoint(sketch, "E38.66.2.0", {"position": v(342.9, 59.27) * mm});
            skPoint(sketch, "E38.66.3.0", {"position": v(342.9, 52.92) * mm});
            skPoint(sketch, "E38.66.4.0", {"position": v(342.9, 46.57) * mm});
            skPoint(sketch, "E38.66.5.0", {"position": v(342.9, 40.22) * mm});
            skPoint(sketch, "E38.66.6.0", {"position": v(342.9, 33.87) * mm});
            skPoint(sketch, "E38.66.7.0", {"position": v(342.9, 27.52) * mm});
            skPoint(sketch, "E38.66.8.0", {"position": v(342.9, 21.17) * mm});
            skPoint(sketch, "E38.66.9.0", {"position": v(342.9, 14.82) * mm});
            skPoint(sketch, "E38.66.10.0", {"position": v(342.9, 8.47) * mm});
            skPoint(sketch, "E38.66.11.0", {"position": v(342.9, 2.12) * mm});
            skPoint(sketch, "E38.66.12.0", {"position": v(342.9, -4.23) * mm});
            skPoint(sketch, "E38.66.13.0", {"position": v(342.9, -10.58) * mm});
            skPoint(sketch, "E38.66.14.0", {"position": v(342.9, -16.93) * mm});
            skPoint(sketch, "E38.66.15.0", {"position": v(342.9, -23.28) * mm});
            skPoint(sketch, "E38.66.16.0", {"position": v(342.9, -29.63) * mm});
            skPoint(sketch, "E38.66.17.0", {"position": v(342.9, -35.98) * mm});
            skPoint(sketch, "E38.66.18.0", {"position": v(342.9, -42.33) * mm});
            skPoint(sketch, "E38.66.19.0", {"position": v(342.9, -48.68) * mm});
            skPoint(sketch, "E38.66.20.0", {"position": v(342.9, -55.03) * mm});
            skPoint(sketch, "E38.66.21.0", {"position": v(342.9, -61.38) * mm});
            skPoint(sketch, "E38.66.22.0", {"position": v(342.9, -67.73) * mm});
            skPoint(sketch, "E38.66.23.0", {"position": v(342.9, -74.08) * mm});
            skPoint(sketch, "E38.66.24.0", {"position": v(342.9, -80.43) * mm});
            skPoint(sketch, "E38.66.25.0", {"position": v(342.9, -86.78) * mm});
            skPoint(sketch, "E38.66.26.0", {"position": v(342.9, -93.13) * mm});
            skPoint(sketch, "E38.66.27.0", {"position": v(342.9, -99.48) * mm});
            skPoint(sketch, "E38.66.28.0", {"position": v(342.9, -105.83) * mm});
            skPoint(sketch, "E38.66.29.0", {"position": v(342.9, -112.18) * mm});
            skPoint(sketch, "E38.66.30.0", {"position": v(342.9, -118.53) * mm});
            skPoint(sketch, "E38.66.31.0", {"position": v(342.9, -124.88) * mm});
            skPoint(sketch, "E38.66.32.0", {"position": v(342.9, -131.23) * mm});
            skPoint(sketch, "E38.66.33.0", {"position": v(342.9, -137.58) * mm});
            skPoint(sketch, "E38.66.34.0", {"position": v(342.9, -143.93) * mm});
            skPoint(sketch, "E38.66.35.0", {"position": v(342.9, -150.28) * mm});
            skPoint(sketch, "E38.66.36.0", {"position": v(342.9, -156.63) * mm});
            skPoint(sketch, "E38.66.37.0", {"position": v(342.9, -162.98) * mm});
            skPoint(sketch, "E38.66.38.0", {"position": v(342.9, -169.33) * mm});
            skPoint(sketch, "E38.66.39.0", {"position": v(342.9, -175.68) * mm});
            skPoint(sketch, "E38.66.40.0", {"position": v(342.9, -182.03) * mm});
            skPoint(sketch, "E38.66.41.0", {"position": v(342.9, -188.38) * mm});
            skPoint(sketch, "E38.66.42.0", {"position": v(342.9, -194.73) * mm});
            skPoint(sketch, "E38.66.43.0", {"position": v(342.9, -201.08) * mm});
            skPoint(sketch, "E38.66.44.0", {"position": v(342.9, -207.43) * mm});
            skPoint(sketch, "E38.66.45.0", {"position": v(342.9, -213.78) * mm});
            skPoint(sketch, "E38.66.46.0", {"position": v(342.9, -220.13) * mm});
            skPoint(sketch, "E38.66.47.0", {"position": v(342.9, -226.48) * mm});
            skPoint(sketch, "E38.66.48.0", {"position": v(342.9, -232.83) * mm});
            skPoint(sketch, "E38.66.49.0", {"position": v(342.9, -239.18) * mm});
            skPoint(sketch, "E38.66.50.0", {"position": v(342.9, -245.53) * mm});
            skPoint(sketch, "E38.66.51.0", {"position": v(342.9, -251.88) * mm});
            skPoint(sketch, "E38.66.52.0", {"position": v(342.9, -258.23) * mm});
            skPoint(sketch, "E38.66.53.0", {"position": v(342.9, -264.58) * mm});
            skPoint(sketch, "E38.66.54.0", {"position": v(342.9, -270.93) * mm});
            skPoint(sketch, "E38.66.55.0", {"position": v(342.9, -277.28) * mm});
            skPoint(sketch, "E38.66.56.0", {"position": v(342.9, -283.63) * mm});
            skPoint(sketch, "E38.66.57.0", {"position": v(342.9, -289.98) * mm});
            skPoint(sketch, "E38.66.58.0", {"position": v(342.9, -296.33) * mm});
            skPoint(sketch, "E38.66.59.0", {"position": v(342.9, -302.68) * mm});
            skPoint(sketch, "E38.66.60.0", {"position": v(342.9, -309.03) * mm});
            skPoint(sketch, "E38.66.61.0", {"position": v(342.9, -315.38) * mm});
            skPoint(sketch, "E38.66.62.0", {"position": v(342.9, -321.73) * mm});
            skPoint(sketch, "E38.66.63.0", {"position": v(342.9, -328.08) * mm});
            skPoint(sketch, "E38.66.64.0", {"position": v(342.9, -334.43) * mm});
            skPoint(sketch, "E38.66.65.0", {"position": v(342.9, -340.78) * mm});
            skPoint(sketch, "E38.66.66.0", {"position": v(342.9, -347.13) * mm});
            skPoint(sketch, "E38.66.67.0", {"position": v(342.9, -353.48) * mm});
            skPoint(sketch, "E38.66.68.0", {"position": v(342.9, -359.83) * mm});
            skPoint(sketch, "E38.66.69.0", {"position": v(342.9, -366.18) * mm});
            skPoint(sketch, "E38.66.70.0", {"position": v(342.9, -372.53) * mm});
            skPoint(sketch, "E38.66.71.0", {"position": v(342.9, -378.88) * mm});
            skPoint(sketch, "E38.66.72.0", {"position": v(342.9, -385.23) * mm});
            skPoint(sketch, "E38.66.73.0", {"position": v(342.9, -391.58) * mm});
            skPoint(sketch, "E38.66.74.0", {"position": v(342.9, -397.93) * mm});
            skPoint(sketch, "E38.66.75.0", {"position": v(342.9, -404.28) * mm});
            skPoint(sketch, "E38.66.76.0", {"position": v(342.9, -410.63) * mm});
            skPoint(sketch, "E38.66.77.0", {"position": v(342.9, -416.98) * mm});
            skPoint(sketch, "E38.66.78.0", {"position": v(342.9, -423.33) * mm});
            skPoint(sketch, "E38.66.79.0", {"position": v(342.9, -429.68) * mm});
            skPoint(sketch, "E38.66.80.0", {"position": v(342.9, -436.03) * mm});
            skPoint(sketch, "E38.66.81.0", {"position": v(342.9, -442.38) * mm});
            skPoint(sketch, "E38.66.82.0", {"position": v(342.9, -448.73) * mm});
            skPoint(sketch, "E38.66.83.0", {"position": v(342.9, -455.08) * mm});
            skPoint(sketch, "E38.66.84.0", {"position": v(342.9, -461.43) * mm});
            skPoint(sketch, "E38.66.85.0", {"position": v(342.9, -467.78) * mm});
            skPoint(sketch, "E38.66.86.0", {"position": v(342.9, -474.13) * mm});
            skPoint(sketch, "E38.66.87.0", {"position": v(342.9, -480.48) * mm});
            skPoint(sketch, "E38.66.88.0", {"position": v(342.9, -486.83) * mm});
            skPoint(sketch, "E38.66.89.0", {"position": v(342.9, -493.18) * mm});
            skPoint(sketch, "E38.66.90.0", {"position": v(342.9, -499.53) * mm});
            skPoint(sketch, "E38.66.91.0", {"position": v(342.9, -505.88) * mm});
            skPoint(sketch, "E38.66.92.0", {"position": v(342.9, -512.23) * mm});
            skPoint(sketch, "E38.66.93.0", {"position": v(342.9, -518.58) * mm});
            skPoint(sketch, "E38.66.94.0", {"position": v(342.9, -524.93) * mm});
            skPoint(sketch, "E38.66.95.0", {"position": v(342.9, -531.28) * mm});
            skPoint(sketch, "E38.66.96.0", {"position": v(342.9, -537.63) * mm});
            skPoint(sketch, "E38.66.97.0", {"position": v(342.9, -543.98) * mm});
            skPoint(sketch, "E38.66.98.0", {"position": v(342.9, -550.33) * mm});
            skPoint(sketch, "E38.66.99.0", {"position": v(342.9, -556.68) * mm});
            skPoint(sketch, "E38.67.0.0", {"position": v(349.25, 71.97) * mm});
            skPoint(sketch, "E38.67.1.0", {"position": v(349.25, 65.62) * mm});
            skPoint(sketch, "E38.67.2.0", {"position": v(349.25, 59.27) * mm});
            skPoint(sketch, "E38.67.3.0", {"position": v(349.25, 52.92) * mm});
            skPoint(sketch, "E38.67.4.0", {"position": v(349.25, 46.57) * mm});
            skPoint(sketch, "E38.67.5.0", {"position": v(349.25, 40.22) * mm});
            skPoint(sketch, "E38.67.6.0", {"position": v(349.25, 33.87) * mm});
            skPoint(sketch, "E38.67.7.0", {"position": v(349.25, 27.52) * mm});
            skPoint(sketch, "E38.67.8.0", {"position": v(349.25, 21.17) * mm});
            skPoint(sketch, "E38.67.9.0", {"position": v(349.25, 14.82) * mm});
            skPoint(sketch, "E38.67.10.0", {"position": v(349.25, 8.47) * mm});
            skPoint(sketch, "E38.67.11.0", {"position": v(349.25, 2.12) * mm});
            skPoint(sketch, "E38.67.12.0", {"position": v(349.25, -4.23) * mm});
            skPoint(sketch, "E38.67.13.0", {"position": v(349.25, -10.58) * mm});
            skPoint(sketch, "E38.67.14.0", {"position": v(349.25, -16.93) * mm});
            skPoint(sketch, "E38.67.15.0", {"position": v(349.25, -23.28) * mm});
            skPoint(sketch, "E38.67.16.0", {"position": v(349.25, -29.63) * mm});
            skPoint(sketch, "E38.67.17.0", {"position": v(349.25, -35.98) * mm});
            skPoint(sketch, "E38.67.18.0", {"position": v(349.25, -42.33) * mm});
            skPoint(sketch, "E38.67.19.0", {"position": v(349.25, -48.68) * mm});
            skPoint(sketch, "E38.67.20.0", {"position": v(349.25, -55.03) * mm});
            skPoint(sketch, "E38.67.21.0", {"position": v(349.25, -61.38) * mm});
            skPoint(sketch, "E38.67.22.0", {"position": v(349.25, -67.73) * mm});
            skPoint(sketch, "E38.67.23.0", {"position": v(349.25, -74.08) * mm});
            skPoint(sketch, "E38.67.24.0", {"position": v(349.25, -80.43) * mm});
            skPoint(sketch, "E38.67.25.0", {"position": v(349.25, -86.78) * mm});
            skPoint(sketch, "E38.67.26.0", {"position": v(349.25, -93.13) * mm});
            skPoint(sketch, "E38.67.27.0", {"position": v(349.25, -99.48) * mm});
            skPoint(sketch, "E38.67.28.0", {"position": v(349.25, -105.83) * mm});
            skPoint(sketch, "E38.67.29.0", {"position": v(349.25, -112.18) * mm});
            skPoint(sketch, "E38.67.30.0", {"position": v(349.25, -118.53) * mm});
            skPoint(sketch, "E38.67.31.0", {"position": v(349.25, -124.88) * mm});
            skPoint(sketch, "E38.67.32.0", {"position": v(349.25, -131.23) * mm});
            skPoint(sketch, "E38.67.33.0", {"position": v(349.25, -137.58) * mm});
            skPoint(sketch, "E38.67.34.0", {"position": v(349.25, -143.93) * mm});
            skPoint(sketch, "E38.67.35.0", {"position": v(349.25, -150.28) * mm});
            skPoint(sketch, "E38.67.36.0", {"position": v(349.25, -156.63) * mm});
            skPoint(sketch, "E38.67.37.0", {"position": v(349.25, -162.98) * mm});
            skPoint(sketch, "E38.67.38.0", {"position": v(349.25, -169.33) * mm});
            skPoint(sketch, "E38.67.39.0", {"position": v(349.25, -175.68) * mm});
            skPoint(sketch, "E38.67.40.0", {"position": v(349.25, -182.03) * mm});
            skPoint(sketch, "E38.67.41.0", {"position": v(349.25, -188.38) * mm});
            skPoint(sketch, "E38.67.42.0", {"position": v(349.25, -194.73) * mm});
            skPoint(sketch, "E38.67.43.0", {"position": v(349.25, -201.08) * mm});
            skPoint(sketch, "E38.67.44.0", {"position": v(349.25, -207.43) * mm});
            skPoint(sketch, "E38.67.45.0", {"position": v(349.25, -213.78) * mm});
            skPoint(sketch, "E38.67.46.0", {"position": v(349.25, -220.13) * mm});
            skPoint(sketch, "E38.67.47.0", {"position": v(349.25, -226.48) * mm});
            skPoint(sketch, "E38.67.48.0", {"position": v(349.25, -232.83) * mm});
            skPoint(sketch, "E38.67.49.0", {"position": v(349.25, -239.18) * mm});
            skPoint(sketch, "E38.67.50.0", {"position": v(349.25, -245.53) * mm});
            skPoint(sketch, "E38.67.51.0", {"position": v(349.25, -251.88) * mm});
            skPoint(sketch, "E38.67.52.0", {"position": v(349.25, -258.23) * mm});
            skPoint(sketch, "E38.67.53.0", {"position": v(349.25, -264.58) * mm});
            skPoint(sketch, "E38.67.54.0", {"position": v(349.25, -270.93) * mm});
            skPoint(sketch, "E38.67.55.0", {"position": v(349.25, -277.28) * mm});
            skPoint(sketch, "E38.67.56.0", {"position": v(349.25, -283.63) * mm});
            skPoint(sketch, "E38.67.57.0", {"position": v(349.25, -289.98) * mm});
            skPoint(sketch, "E38.67.58.0", {"position": v(349.25, -296.33) * mm});
            skPoint(sketch, "E38.67.59.0", {"position": v(349.25, -302.68) * mm});
            skPoint(sketch, "E38.67.60.0", {"position": v(349.25, -309.03) * mm});
            skPoint(sketch, "E38.67.61.0", {"position": v(349.25, -315.38) * mm});
            skPoint(sketch, "E38.67.62.0", {"position": v(349.25, -321.73) * mm});
            skPoint(sketch, "E38.67.63.0", {"position": v(349.25, -328.08) * mm});
            skPoint(sketch, "E38.67.64.0", {"position": v(349.25, -334.43) * mm});
            skPoint(sketch, "E38.67.65.0", {"position": v(349.25, -340.78) * mm});
            skPoint(sketch, "E38.67.66.0", {"position": v(349.25, -347.13) * mm});
            skPoint(sketch, "E38.67.67.0", {"position": v(349.25, -353.48) * mm});
            skPoint(sketch, "E38.67.68.0", {"position": v(349.25, -359.83) * mm});
            skPoint(sketch, "E38.67.69.0", {"position": v(349.25, -366.18) * mm});
            skPoint(sketch, "E38.67.70.0", {"position": v(349.25, -372.53) * mm});
            skPoint(sketch, "E38.67.71.0", {"position": v(349.25, -378.88) * mm});
            skPoint(sketch, "E38.67.72.0", {"position": v(349.25, -385.23) * mm});
            skPoint(sketch, "E38.67.73.0", {"position": v(349.25, -391.58) * mm});
            skPoint(sketch, "E38.67.74.0", {"position": v(349.25, -397.93) * mm});
            skPoint(sketch, "E38.67.75.0", {"position": v(349.25, -404.28) * mm});
            skPoint(sketch, "E38.67.76.0", {"position": v(349.25, -410.63) * mm});
            skPoint(sketch, "E38.67.77.0", {"position": v(349.25, -416.98) * mm});
            skPoint(sketch, "E38.67.78.0", {"position": v(349.25, -423.33) * mm});
            skPoint(sketch, "E38.67.79.0", {"position": v(349.25, -429.68) * mm});
            skPoint(sketch, "E38.67.80.0", {"position": v(349.25, -436.03) * mm});
            skPoint(sketch, "E38.67.81.0", {"position": v(349.25, -442.38) * mm});
            skPoint(sketch, "E38.67.82.0", {"position": v(349.25, -448.73) * mm});
            skPoint(sketch, "E38.67.83.0", {"position": v(349.25, -455.08) * mm});
            skPoint(sketch, "E38.67.84.0", {"position": v(349.25, -461.43) * mm});
            skPoint(sketch, "E38.67.85.0", {"position": v(349.25, -467.78) * mm});
            skPoint(sketch, "E38.67.86.0", {"position": v(349.25, -474.13) * mm});
            skPoint(sketch, "E38.67.87.0", {"position": v(349.25, -480.48) * mm});
            skPoint(sketch, "E38.67.88.0", {"position": v(349.25, -486.83) * mm});
            skPoint(sketch, "E38.67.89.0", {"position": v(349.25, -493.18) * mm});
            skPoint(sketch, "E38.67.90.0", {"position": v(349.25, -499.53) * mm});
            skPoint(sketch, "E38.67.91.0", {"position": v(349.25, -505.88) * mm});
            skPoint(sketch, "E38.67.92.0", {"position": v(349.25, -512.23) * mm});
            skPoint(sketch, "E38.67.93.0", {"position": v(349.25, -518.58) * mm});
            skPoint(sketch, "E38.67.94.0", {"position": v(349.25, -524.93) * mm});
            skPoint(sketch, "E38.67.95.0", {"position": v(349.25, -531.28) * mm});
            skPoint(sketch, "E38.67.96.0", {"position": v(349.25, -537.63) * mm});
            skPoint(sketch, "E38.67.97.0", {"position": v(349.25, -543.98) * mm});
            skPoint(sketch, "E38.67.98.0", {"position": v(349.25, -550.33) * mm});
            skPoint(sketch, "E38.67.99.0", {"position": v(349.25, -556.68) * mm});
            skPoint(sketch, "E38.68.0.0", {"position": v(355.6, 71.97) * mm});
            skPoint(sketch, "E38.68.1.0", {"position": v(355.6, 65.62) * mm});
            skPoint(sketch, "E38.68.2.0", {"position": v(355.6, 59.27) * mm});
            skPoint(sketch, "E38.68.3.0", {"position": v(355.6, 52.92) * mm});
            skPoint(sketch, "E38.68.4.0", {"position": v(355.6, 46.57) * mm});
            skPoint(sketch, "E38.68.5.0", {"position": v(355.6, 40.22) * mm});
            skPoint(sketch, "E38.68.6.0", {"position": v(355.6, 33.87) * mm});
            skPoint(sketch, "E38.68.7.0", {"position": v(355.6, 27.52) * mm});
            skPoint(sketch, "E38.68.8.0", {"position": v(355.6, 21.17) * mm});
            skPoint(sketch, "E38.68.9.0", {"position": v(355.6, 14.82) * mm});
            skPoint(sketch, "E38.68.10.0", {"position": v(355.6, 8.47) * mm});
            skPoint(sketch, "E38.68.11.0", {"position": v(355.6, 2.12) * mm});
            skPoint(sketch, "E38.68.12.0", {"position": v(355.6, -4.23) * mm});
            skPoint(sketch, "E38.68.13.0", {"position": v(355.6, -10.58) * mm});
            skPoint(sketch, "E38.68.14.0", {"position": v(355.6, -16.93) * mm});
            skPoint(sketch, "E38.68.15.0", {"position": v(355.6, -23.28) * mm});
            skPoint(sketch, "E38.68.16.0", {"position": v(355.6, -29.63) * mm});
            skPoint(sketch, "E38.68.17.0", {"position": v(355.6, -35.98) * mm});
            skPoint(sketch, "E38.68.18.0", {"position": v(355.6, -42.33) * mm});
            skPoint(sketch, "E38.68.19.0", {"position": v(355.6, -48.68) * mm});
            skPoint(sketch, "E38.68.20.0", {"position": v(355.6, -55.03) * mm});
            skPoint(sketch, "E38.68.21.0", {"position": v(355.6, -61.38) * mm});
            skPoint(sketch, "E38.68.22.0", {"position": v(355.6, -67.73) * mm});
            skPoint(sketch, "E38.68.23.0", {"position": v(355.6, -74.08) * mm});
            skPoint(sketch, "E38.68.24.0", {"position": v(355.6, -80.43) * mm});
            skPoint(sketch, "E38.68.25.0", {"position": v(355.6, -86.78) * mm});
            skPoint(sketch, "E38.68.26.0", {"position": v(355.6, -93.13) * mm});
            skPoint(sketch, "E38.68.27.0", {"position": v(355.6, -99.48) * mm});
            skPoint(sketch, "E38.68.28.0", {"position": v(355.6, -105.83) * mm});
            skPoint(sketch, "E38.68.29.0", {"position": v(355.6, -112.18) * mm});
            skPoint(sketch, "E38.68.30.0", {"position": v(355.6, -118.53) * mm});
            skPoint(sketch, "E38.68.31.0", {"position": v(355.6, -124.88) * mm});
            skPoint(sketch, "E38.68.32.0", {"position": v(355.6, -131.23) * mm});
            skPoint(sketch, "E38.68.33.0", {"position": v(355.6, -137.58) * mm});
            skPoint(sketch, "E38.68.34.0", {"position": v(355.6, -143.93) * mm});
            skPoint(sketch, "E38.68.35.0", {"position": v(355.6, -150.28) * mm});
            skPoint(sketch, "E38.68.36.0", {"position": v(355.6, -156.63) * mm});
            skPoint(sketch, "E38.68.37.0", {"position": v(355.6, -162.98) * mm});
            skPoint(sketch, "E38.68.38.0", {"position": v(355.6, -169.33) * mm});
            skPoint(sketch, "E38.68.39.0", {"position": v(355.6, -175.68) * mm});
            skPoint(sketch, "E38.68.40.0", {"position": v(355.6, -182.03) * mm});
            skPoint(sketch, "E38.68.41.0", {"position": v(355.6, -188.38) * mm});
            skPoint(sketch, "E38.68.42.0", {"position": v(355.6, -194.73) * mm});
            skPoint(sketch, "E38.68.43.0", {"position": v(355.6, -201.08) * mm});
            skPoint(sketch, "E38.68.44.0", {"position": v(355.6, -207.43) * mm});
            skPoint(sketch, "E38.68.45.0", {"position": v(355.6, -213.78) * mm});
            skPoint(sketch, "E38.68.46.0", {"position": v(355.6, -220.13) * mm});
            skPoint(sketch, "E38.68.47.0", {"position": v(355.6, -226.48) * mm});
            skPoint(sketch, "E38.68.48.0", {"position": v(355.6, -232.83) * mm});
            skPoint(sketch, "E38.68.49.0", {"position": v(355.6, -239.18) * mm});
            skPoint(sketch, "E38.68.50.0", {"position": v(355.6, -245.53) * mm});
            skPoint(sketch, "E38.68.51.0", {"position": v(355.6, -251.88) * mm});
            skPoint(sketch, "E38.68.52.0", {"position": v(355.6, -258.23) * mm});
            skPoint(sketch, "E38.68.53.0", {"position": v(355.6, -264.58) * mm});
            skPoint(sketch, "E38.68.54.0", {"position": v(355.6, -270.93) * mm});
            skPoint(sketch, "E38.68.55.0", {"position": v(355.6, -277.28) * mm});
            skPoint(sketch, "E38.68.56.0", {"position": v(355.6, -283.63) * mm});
            skPoint(sketch, "E38.68.57.0", {"position": v(355.6, -289.98) * mm});
            skPoint(sketch, "E38.68.58.0", {"position": v(355.6, -296.33) * mm});
            skPoint(sketch, "E38.68.59.0", {"position": v(355.6, -302.68) * mm});
            skPoint(sketch, "E38.68.60.0", {"position": v(355.6, -309.03) * mm});
            skPoint(sketch, "E38.68.61.0", {"position": v(355.6, -315.38) * mm});
            skPoint(sketch, "E38.68.62.0", {"position": v(355.6, -321.73) * mm});
            skPoint(sketch, "E38.68.63.0", {"position": v(355.6, -328.08) * mm});
            skPoint(sketch, "E38.68.64.0", {"position": v(355.6, -334.43) * mm});
            skPoint(sketch, "E38.68.65.0", {"position": v(355.6, -340.78) * mm});
            skPoint(sketch, "E38.68.66.0", {"position": v(355.6, -347.13) * mm});
            skPoint(sketch, "E38.68.67.0", {"position": v(355.6, -353.48) * mm});
            skPoint(sketch, "E38.68.68.0", {"position": v(355.6, -359.83) * mm});
            skPoint(sketch, "E38.68.69.0", {"position": v(355.6, -366.18) * mm});
            skPoint(sketch, "E38.68.70.0", {"position": v(355.6, -372.53) * mm});
            skPoint(sketch, "E38.68.71.0", {"position": v(355.6, -378.88) * mm});
            skPoint(sketch, "E38.68.72.0", {"position": v(355.6, -385.23) * mm});
            skPoint(sketch, "E38.68.73.0", {"position": v(355.6, -391.58) * mm});
            skPoint(sketch, "E38.68.74.0", {"position": v(355.6, -397.93) * mm});
            skPoint(sketch, "E38.68.75.0", {"position": v(355.6, -404.28) * mm});
            skPoint(sketch, "E38.68.76.0", {"position": v(355.6, -410.63) * mm});
            skPoint(sketch, "E38.68.77.0", {"position": v(355.6, -416.98) * mm});
            skPoint(sketch, "E38.68.78.0", {"position": v(355.6, -423.33) * mm});
            skPoint(sketch, "E38.68.79.0", {"position": v(355.6, -429.68) * mm});
            skPoint(sketch, "E38.68.80.0", {"position": v(355.6, -436.03) * mm});
            skPoint(sketch, "E38.68.81.0", {"position": v(355.6, -442.38) * mm});
            skPoint(sketch, "E38.68.82.0", {"position": v(355.6, -448.73) * mm});
            skPoint(sketch, "E38.68.83.0", {"position": v(355.6, -455.08) * mm});
            skPoint(sketch, "E38.68.84.0", {"position": v(355.6, -461.43) * mm});
            skPoint(sketch, "E38.68.85.0", {"position": v(355.6, -467.78) * mm});
            skPoint(sketch, "E38.68.86.0", {"position": v(355.6, -474.13) * mm});
            skPoint(sketch, "E38.68.87.0", {"position": v(355.6, -480.48) * mm});
            skPoint(sketch, "E38.68.88.0", {"position": v(355.6, -486.83) * mm});
            skPoint(sketch, "E38.68.89.0", {"position": v(355.6, -493.18) * mm});
            skPoint(sketch, "E38.68.90.0", {"position": v(355.6, -499.53) * mm});
            skPoint(sketch, "E38.68.91.0", {"position": v(355.6, -505.88) * mm});
            skPoint(sketch, "E38.68.92.0", {"position": v(355.6, -512.23) * mm});
            skPoint(sketch, "E38.68.93.0", {"position": v(355.6, -518.58) * mm});
            skPoint(sketch, "E38.68.94.0", {"position": v(355.6, -524.93) * mm});
            skPoint(sketch, "E38.68.95.0", {"position": v(355.6, -531.28) * mm});
            skPoint(sketch, "E38.68.96.0", {"position": v(355.6, -537.63) * mm});
            skPoint(sketch, "E38.68.97.0", {"position": v(355.6, -543.98) * mm});
            skPoint(sketch, "E38.68.98.0", {"position": v(355.6, -550.33) * mm});
            skPoint(sketch, "E38.68.99.0", {"position": v(355.6, -556.68) * mm});
            skPoint(sketch, "E38.69.0.0", {"position": v(361.95, 71.97) * mm});
            skPoint(sketch, "E38.69.1.0", {"position": v(361.95, 65.62) * mm});
            skPoint(sketch, "E38.69.2.0", {"position": v(361.95, 59.27) * mm});
            skPoint(sketch, "E38.69.3.0", {"position": v(361.95, 52.92) * mm});
            skPoint(sketch, "E38.69.4.0", {"position": v(361.95, 46.57) * mm});
            skPoint(sketch, "E38.69.5.0", {"position": v(361.95, 40.22) * mm});
            skPoint(sketch, "E38.69.6.0", {"position": v(361.95, 33.87) * mm});
            skPoint(sketch, "E38.69.7.0", {"position": v(361.95, 27.52) * mm});
            skPoint(sketch, "E38.69.8.0", {"position": v(361.95, 21.17) * mm});
            skPoint(sketch, "E38.69.9.0", {"position": v(361.95, 14.82) * mm});
            skPoint(sketch, "E38.69.10.0", {"position": v(361.95, 8.47) * mm});
            skPoint(sketch, "E38.69.11.0", {"position": v(361.95, 2.12) * mm});
            skPoint(sketch, "E38.69.12.0", {"position": v(361.95, -4.23) * mm});
            skPoint(sketch, "E38.69.13.0", {"position": v(361.95, -10.58) * mm});
            skPoint(sketch, "E38.69.14.0", {"position": v(361.95, -16.93) * mm});
            skPoint(sketch, "E38.69.15.0", {"position": v(361.95, -23.28) * mm});
            skPoint(sketch, "E38.69.16.0", {"position": v(361.95, -29.63) * mm});
            skPoint(sketch, "E38.69.17.0", {"position": v(361.95, -35.98) * mm});
            skPoint(sketch, "E38.69.18.0", {"position": v(361.95, -42.33) * mm});
            skPoint(sketch, "E38.69.19.0", {"position": v(361.95, -48.68) * mm});
            skPoint(sketch, "E38.69.20.0", {"position": v(361.95, -55.03) * mm});
            skPoint(sketch, "E38.69.21.0", {"position": v(361.95, -61.38) * mm});
            skPoint(sketch, "E38.69.22.0", {"position": v(361.95, -67.73) * mm});
            skPoint(sketch, "E38.69.23.0", {"position": v(361.95, -74.08) * mm});
            skPoint(sketch, "E38.69.24.0", {"position": v(361.95, -80.43) * mm});
            skPoint(sketch, "E38.69.25.0", {"position": v(361.95, -86.78) * mm});
            skPoint(sketch, "E38.69.26.0", {"position": v(361.95, -93.13) * mm});
            skPoint(sketch, "E38.69.27.0", {"position": v(361.95, -99.48) * mm});
            skPoint(sketch, "E38.69.28.0", {"position": v(361.95, -105.83) * mm});
            skPoint(sketch, "E38.69.29.0", {"position": v(361.95, -112.18) * mm});
            skPoint(sketch, "E38.69.30.0", {"position": v(361.95, -118.53) * mm});
            skPoint(sketch, "E38.69.31.0", {"position": v(361.95, -124.88) * mm});
            skPoint(sketch, "E38.69.32.0", {"position": v(361.95, -131.23) * mm});
            skPoint(sketch, "E38.69.33.0", {"position": v(361.95, -137.58) * mm});
            skPoint(sketch, "E38.69.34.0", {"position": v(361.95, -143.93) * mm});
            skPoint(sketch, "E38.69.35.0", {"position": v(361.95, -150.28) * mm});
            skPoint(sketch, "E38.69.36.0", {"position": v(361.95, -156.63) * mm});
            skPoint(sketch, "E38.69.37.0", {"position": v(361.95, -162.98) * mm});
            skPoint(sketch, "E38.69.38.0", {"position": v(361.95, -169.33) * mm});
            skPoint(sketch, "E38.69.39.0", {"position": v(361.95, -175.68) * mm});
            skPoint(sketch, "E38.69.40.0", {"position": v(361.95, -182.03) * mm});
            skPoint(sketch, "E38.69.41.0", {"position": v(361.95, -188.38) * mm});
            skPoint(sketch, "E38.69.42.0", {"position": v(361.95, -194.73) * mm});
            skPoint(sketch, "E38.69.43.0", {"position": v(361.95, -201.08) * mm});
            skPoint(sketch, "E38.69.44.0", {"position": v(361.95, -207.43) * mm});
            skPoint(sketch, "E38.69.45.0", {"position": v(361.95, -213.78) * mm});
            skPoint(sketch, "E38.69.46.0", {"position": v(361.95, -220.13) * mm});
            skPoint(sketch, "E38.69.47.0", {"position": v(361.95, -226.48) * mm});
            skPoint(sketch, "E38.69.48.0", {"position": v(361.95, -232.83) * mm});
            skPoint(sketch, "E38.69.49.0", {"position": v(361.95, -239.18) * mm});
            skPoint(sketch, "E38.69.50.0", {"position": v(361.95, -245.53) * mm});
            skPoint(sketch, "E38.69.51.0", {"position": v(361.95, -251.88) * mm});
            skPoint(sketch, "E38.69.52.0", {"position": v(361.95, -258.23) * mm});
            skPoint(sketch, "E38.69.53.0", {"position": v(361.95, -264.58) * mm});
            skPoint(sketch, "E38.69.54.0", {"position": v(361.95, -270.93) * mm});
            skPoint(sketch, "E38.69.55.0", {"position": v(361.95, -277.28) * mm});
            skPoint(sketch, "E38.69.56.0", {"position": v(361.95, -283.63) * mm});
            skPoint(sketch, "E38.69.57.0", {"position": v(361.95, -289.98) * mm});
            skPoint(sketch, "E38.69.58.0", {"position": v(361.95, -296.33) * mm});
            skPoint(sketch, "E38.69.59.0", {"position": v(361.95, -302.68) * mm});
            skPoint(sketch, "E38.69.60.0", {"position": v(361.95, -309.03) * mm});
            skPoint(sketch, "E38.69.61.0", {"position": v(361.95, -315.38) * mm});
            skPoint(sketch, "E38.69.62.0", {"position": v(361.95, -321.73) * mm});
            skPoint(sketch, "E38.69.63.0", {"position": v(361.95, -328.08) * mm});
            skPoint(sketch, "E38.69.64.0", {"position": v(361.95, -334.43) * mm});
            skPoint(sketch, "E38.69.65.0", {"position": v(361.95, -340.78) * mm});
            skPoint(sketch, "E38.69.66.0", {"position": v(361.95, -347.13) * mm});
            skPoint(sketch, "E38.69.67.0", {"position": v(361.95, -353.48) * mm});
            skPoint(sketch, "E38.69.68.0", {"position": v(361.95, -359.83) * mm});
            skPoint(sketch, "E38.69.69.0", {"position": v(361.95, -366.18) * mm});
            skPoint(sketch, "E38.69.70.0", {"position": v(361.95, -372.53) * mm});
            skPoint(sketch, "E38.69.71.0", {"position": v(361.95, -378.88) * mm});
            skPoint(sketch, "E38.69.72.0", {"position": v(361.95, -385.23) * mm});
            skPoint(sketch, "E38.69.73.0", {"position": v(361.95, -391.58) * mm});
            skPoint(sketch, "E38.69.74.0", {"position": v(361.95, -397.93) * mm});
            skPoint(sketch, "E38.69.75.0", {"position": v(361.95, -404.28) * mm});
            skPoint(sketch, "E38.69.76.0", {"position": v(361.95, -410.63) * mm});
            skPoint(sketch, "E38.69.77.0", {"position": v(361.95, -416.98) * mm});
            skPoint(sketch, "E38.69.78.0", {"position": v(361.95, -423.33) * mm});
            skPoint(sketch, "E38.69.79.0", {"position": v(361.95, -429.68) * mm});
            skPoint(sketch, "E38.69.80.0", {"position": v(361.95, -436.03) * mm});
            skPoint(sketch, "E38.69.81.0", {"position": v(361.95, -442.38) * mm});
            skPoint(sketch, "E38.69.82.0", {"position": v(361.95, -448.73) * mm});
            skPoint(sketch, "E38.69.83.0", {"position": v(361.95, -455.08) * mm});
            skPoint(sketch, "E38.69.84.0", {"position": v(361.95, -461.43) * mm});
            skPoint(sketch, "E38.69.85.0", {"position": v(361.95, -467.78) * mm});
            skPoint(sketch, "E38.69.86.0", {"position": v(361.95, -474.13) * mm});
            skPoint(sketch, "E38.69.87.0", {"position": v(361.95, -480.48) * mm});
            skPoint(sketch, "E38.69.88.0", {"position": v(361.95, -486.83) * mm});
            skPoint(sketch, "E38.69.89.0", {"position": v(361.95, -493.18) * mm});
            skPoint(sketch, "E38.69.90.0", {"position": v(361.95, -499.53) * mm});
            skPoint(sketch, "E38.69.91.0", {"position": v(361.95, -505.88) * mm});
            skPoint(sketch, "E38.69.92.0", {"position": v(361.95, -512.23) * mm});
            skPoint(sketch, "E38.69.93.0", {"position": v(361.95, -518.58) * mm});
            skPoint(sketch, "E38.69.94.0", {"position": v(361.95, -524.93) * mm});
            skPoint(sketch, "E38.69.95.0", {"position": v(361.95, -531.28) * mm});
            skPoint(sketch, "E38.69.96.0", {"position": v(361.95, -537.63) * mm});
            skPoint(sketch, "E38.69.97.0", {"position": v(361.95, -543.98) * mm});
            skPoint(sketch, "E38.69.98.0", {"position": v(361.95, -550.33) * mm});
            skPoint(sketch, "E38.69.99.0", {"position": v(361.95, -556.68) * mm});
            skPoint(sketch, "E38.70.0.0", {"position": v(368.3, 71.97) * mm});
            skPoint(sketch, "E38.70.1.0", {"position": v(368.3, 65.62) * mm});
            skPoint(sketch, "E38.70.2.0", {"position": v(368.3, 59.27) * mm});
            skPoint(sketch, "E38.70.3.0", {"position": v(368.3, 52.92) * mm});
            skPoint(sketch, "E38.70.4.0", {"position": v(368.3, 46.57) * mm});
            skPoint(sketch, "E38.70.5.0", {"position": v(368.3, 40.22) * mm});
            skPoint(sketch, "E38.70.6.0", {"position": v(368.3, 33.87) * mm});
            skPoint(sketch, "E38.70.7.0", {"position": v(368.3, 27.52) * mm});
            skPoint(sketch, "E38.70.8.0", {"position": v(368.3, 21.17) * mm});
            skPoint(sketch, "E38.70.9.0", {"position": v(368.3, 14.82) * mm});
            skPoint(sketch, "E38.70.10.0", {"position": v(368.3, 8.47) * mm});
            skPoint(sketch, "E38.70.11.0", {"position": v(368.3, 2.12) * mm});
            skPoint(sketch, "E38.70.12.0", {"position": v(368.3, -4.23) * mm});
            skPoint(sketch, "E38.70.13.0", {"position": v(368.3, -10.58) * mm});
            skPoint(sketch, "E38.70.14.0", {"position": v(368.3, -16.93) * mm});
            skPoint(sketch, "E38.70.15.0", {"position": v(368.3, -23.28) * mm});
            skPoint(sketch, "E38.70.16.0", {"position": v(368.3, -29.63) * mm});
            skPoint(sketch, "E38.70.17.0", {"position": v(368.3, -35.98) * mm});
            skPoint(sketch, "E38.70.18.0", {"position": v(368.3, -42.33) * mm});
            skPoint(sketch, "E38.70.19.0", {"position": v(368.3, -48.68) * mm});
            skPoint(sketch, "E38.70.20.0", {"position": v(368.3, -55.03) * mm});
            skPoint(sketch, "E38.70.21.0", {"position": v(368.3, -61.38) * mm});
            skPoint(sketch, "E38.70.22.0", {"position": v(368.3, -67.73) * mm});
            skPoint(sketch, "E38.70.23.0", {"position": v(368.3, -74.08) * mm});
            skPoint(sketch, "E38.70.24.0", {"position": v(368.3, -80.43) * mm});
            skPoint(sketch, "E38.70.25.0", {"position": v(368.3, -86.78) * mm});
            skPoint(sketch, "E38.70.26.0", {"position": v(368.3, -93.13) * mm});
            skPoint(sketch, "E38.70.27.0", {"position": v(368.3, -99.48) * mm});
            skPoint(sketch, "E38.70.28.0", {"position": v(368.3, -105.83) * mm});
            skPoint(sketch, "E38.70.29.0", {"position": v(368.3, -112.18) * mm});
            skPoint(sketch, "E38.70.30.0", {"position": v(368.3, -118.53) * mm});
            skPoint(sketch, "E38.70.31.0", {"position": v(368.3, -124.88) * mm});
            skPoint(sketch, "E38.70.32.0", {"position": v(368.3, -131.23) * mm});
            skPoint(sketch, "E38.70.33.0", {"position": v(368.3, -137.58) * mm});
            skPoint(sketch, "E38.70.34.0", {"position": v(368.3, -143.93) * mm});
            skPoint(sketch, "E38.70.35.0", {"position": v(368.3, -150.28) * mm});
            skPoint(sketch, "E38.70.36.0", {"position": v(368.3, -156.63) * mm});
            skPoint(sketch, "E38.70.37.0", {"position": v(368.3, -162.98) * mm});
            skPoint(sketch, "E38.70.38.0", {"position": v(368.3, -169.33) * mm});
            skPoint(sketch, "E38.70.39.0", {"position": v(368.3, -175.68) * mm});
            skPoint(sketch, "E38.70.40.0", {"position": v(368.3, -182.03) * mm});
            skPoint(sketch, "E38.70.41.0", {"position": v(368.3, -188.38) * mm});
            skPoint(sketch, "E38.70.42.0", {"position": v(368.3, -194.73) * mm});
            skPoint(sketch, "E38.70.43.0", {"position": v(368.3, -201.08) * mm});
            skPoint(sketch, "E38.70.44.0", {"position": v(368.3, -207.43) * mm});
            skPoint(sketch, "E38.70.45.0", {"position": v(368.3, -213.78) * mm});
            skPoint(sketch, "E38.70.46.0", {"position": v(368.3, -220.13) * mm});
            skPoint(sketch, "E38.70.47.0", {"position": v(368.3, -226.48) * mm});
            skPoint(sketch, "E38.70.48.0", {"position": v(368.3, -232.83) * mm});
            skPoint(sketch, "E38.70.49.0", {"position": v(368.3, -239.18) * mm});
            skPoint(sketch, "E38.70.50.0", {"position": v(368.3, -245.53) * mm});
            skPoint(sketch, "E38.70.51.0", {"position": v(368.3, -251.88) * mm});
            skPoint(sketch, "E38.70.52.0", {"position": v(368.3, -258.23) * mm});
            skPoint(sketch, "E38.70.53.0", {"position": v(368.3, -264.58) * mm});
            skPoint(sketch, "E38.70.54.0", {"position": v(368.3, -270.93) * mm});
            skPoint(sketch, "E38.70.55.0", {"position": v(368.3, -277.28) * mm});
            skPoint(sketch, "E38.70.56.0", {"position": v(368.3, -283.63) * mm});
            skPoint(sketch, "E38.70.57.0", {"position": v(368.3, -289.98) * mm});
            skPoint(sketch, "E38.70.58.0", {"position": v(368.3, -296.33) * mm});
            skPoint(sketch, "E38.70.59.0", {"position": v(368.3, -302.68) * mm});
            skPoint(sketch, "E38.70.60.0", {"position": v(368.3, -309.03) * mm});
            skPoint(sketch, "E38.70.61.0", {"position": v(368.3, -315.38) * mm});
            skPoint(sketch, "E38.70.62.0", {"position": v(368.3, -321.73) * mm});
            skPoint(sketch, "E38.70.63.0", {"position": v(368.3, -328.08) * mm});
            skPoint(sketch, "E38.70.64.0", {"position": v(368.3, -334.43) * mm});
            skPoint(sketch, "E38.70.65.0", {"position": v(368.3, -340.78) * mm});
            skPoint(sketch, "E38.70.66.0", {"position": v(368.3, -347.13) * mm});
            skPoint(sketch, "E38.70.67.0", {"position": v(368.3, -353.48) * mm});
            skPoint(sketch, "E38.70.68.0", {"position": v(368.3, -359.83) * mm});
            skPoint(sketch, "E38.70.69.0", {"position": v(368.3, -366.18) * mm});
            skPoint(sketch, "E38.70.70.0", {"position": v(368.3, -372.53) * mm});
            skPoint(sketch, "E38.70.71.0", {"position": v(368.3, -378.88) * mm});
            skPoint(sketch, "E38.70.72.0", {"position": v(368.3, -385.23) * mm});
            skPoint(sketch, "E38.70.73.0", {"position": v(368.3, -391.58) * mm});
            skPoint(sketch, "E38.70.74.0", {"position": v(368.3, -397.93) * mm});
            skPoint(sketch, "E38.70.75.0", {"position": v(368.3, -404.28) * mm});
            skPoint(sketch, "E38.70.76.0", {"position": v(368.3, -410.63) * mm});
            skPoint(sketch, "E38.70.77.0", {"position": v(368.3, -416.98) * mm});
            skPoint(sketch, "E38.70.78.0", {"position": v(368.3, -423.33) * mm});
            skPoint(sketch, "E38.70.79.0", {"position": v(368.3, -429.68) * mm});
            skPoint(sketch, "E38.70.80.0", {"position": v(368.3, -436.03) * mm});
            skPoint(sketch, "E38.70.81.0", {"position": v(368.3, -442.38) * mm});
            skPoint(sketch, "E38.70.82.0", {"position": v(368.3, -448.73) * mm});
            skPoint(sketch, "E38.70.83.0", {"position": v(368.3, -455.08) * mm});
            skPoint(sketch, "E38.70.84.0", {"position": v(368.3, -461.43) * mm});
            skPoint(sketch, "E38.70.85.0", {"position": v(368.3, -467.78) * mm});
            skPoint(sketch, "E38.70.86.0", {"position": v(368.3, -474.13) * mm});
            skPoint(sketch, "E38.70.87.0", {"position": v(368.3, -480.48) * mm});
            skPoint(sketch, "E38.70.88.0", {"position": v(368.3, -486.83) * mm});
            skPoint(sketch, "E38.70.89.0", {"position": v(368.3, -493.18) * mm});
            skPoint(sketch, "E38.70.90.0", {"position": v(368.3, -499.53) * mm});
            skPoint(sketch, "E38.70.91.0", {"position": v(368.3, -505.88) * mm});
            skPoint(sketch, "E38.70.92.0", {"position": v(368.3, -512.23) * mm});
            skPoint(sketch, "E38.70.93.0", {"position": v(368.3, -518.58) * mm});
            skPoint(sketch, "E38.70.94.0", {"position": v(368.3, -524.93) * mm});
            skPoint(sketch, "E38.70.95.0", {"position": v(368.3, -531.28) * mm});
            skPoint(sketch, "E38.70.96.0", {"position": v(368.3, -537.63) * mm});
            skPoint(sketch, "E38.70.97.0", {"position": v(368.3, -543.98) * mm});
            skPoint(sketch, "E38.70.98.0", {"position": v(368.3, -550.33) * mm});
            skPoint(sketch, "E38.70.99.0", {"position": v(368.3, -556.68) * mm});
            skPoint(sketch, "E38.71.0.0", {"position": v(374.65, 71.97) * mm});
            skPoint(sketch, "E38.71.1.0", {"position": v(374.65, 65.62) * mm});
            skPoint(sketch, "E38.71.2.0", {"position": v(374.65, 59.27) * mm});
            skPoint(sketch, "E38.71.3.0", {"position": v(374.65, 52.92) * mm});
            skPoint(sketch, "E38.71.4.0", {"position": v(374.65, 46.57) * mm});
            skPoint(sketch, "E38.71.5.0", {"position": v(374.65, 40.22) * mm});
            skPoint(sketch, "E38.71.6.0", {"position": v(374.65, 33.87) * mm});
            skPoint(sketch, "E38.71.7.0", {"position": v(374.65, 27.52) * mm});
            skPoint(sketch, "E38.71.8.0", {"position": v(374.65, 21.17) * mm});
            skPoint(sketch, "E38.71.9.0", {"position": v(374.65, 14.82) * mm});
            skPoint(sketch, "E38.71.10.0", {"position": v(374.65, 8.47) * mm});
            skPoint(sketch, "E38.71.11.0", {"position": v(374.65, 2.12) * mm});
            skPoint(sketch, "E38.71.12.0", {"position": v(374.65, -4.23) * mm});
            skPoint(sketch, "E38.71.13.0", {"position": v(374.65, -10.58) * mm});
            skPoint(sketch, "E38.71.14.0", {"position": v(374.65, -16.93) * mm});
            skPoint(sketch, "E38.71.15.0", {"position": v(374.65, -23.28) * mm});
            skPoint(sketch, "E38.71.16.0", {"position": v(374.65, -29.63) * mm});
            skPoint(sketch, "E38.71.17.0", {"position": v(374.65, -35.98) * mm});
            skPoint(sketch, "E38.71.18.0", {"position": v(374.65, -42.33) * mm});
            skPoint(sketch, "E38.71.19.0", {"position": v(374.65, -48.68) * mm});
            skPoint(sketch, "E38.71.20.0", {"position": v(374.65, -55.03) * mm});
            skPoint(sketch, "E38.71.21.0", {"position": v(374.65, -61.38) * mm});
            skPoint(sketch, "E38.71.22.0", {"position": v(374.65, -67.73) * mm});
            skPoint(sketch, "E38.71.23.0", {"position": v(374.65, -74.08) * mm});
            skPoint(sketch, "E38.71.24.0", {"position": v(374.65, -80.43) * mm});
            skPoint(sketch, "E38.71.25.0", {"position": v(374.65, -86.78) * mm});
            skPoint(sketch, "E38.71.26.0", {"position": v(374.65, -93.13) * mm});
            skPoint(sketch, "E38.71.27.0", {"position": v(374.65, -99.48) * mm});
            skPoint(sketch, "E38.71.28.0", {"position": v(374.65, -105.83) * mm});
            skPoint(sketch, "E38.71.29.0", {"position": v(374.65, -112.18) * mm});
            skPoint(sketch, "E38.71.30.0", {"position": v(374.65, -118.53) * mm});
            skPoint(sketch, "E38.71.31.0", {"position": v(374.65, -124.88) * mm});
            skPoint(sketch, "E38.71.32.0", {"position": v(374.65, -131.23) * mm});
            skPoint(sketch, "E38.71.33.0", {"position": v(374.65, -137.58) * mm});
            skPoint(sketch, "E38.71.34.0", {"position": v(374.65, -143.93) * mm});
            skPoint(sketch, "E38.71.35.0", {"position": v(374.65, -150.28) * mm});
            skPoint(sketch, "E38.71.36.0", {"position": v(374.65, -156.63) * mm});
            skPoint(sketch, "E38.71.37.0", {"position": v(374.65, -162.98) * mm});
            skPoint(sketch, "E38.71.38.0", {"position": v(374.65, -169.33) * mm});
            skPoint(sketch, "E38.71.39.0", {"position": v(374.65, -175.68) * mm});
            skPoint(sketch, "E38.71.40.0", {"position": v(374.65, -182.03) * mm});
            skPoint(sketch, "E38.71.41.0", {"position": v(374.65, -188.38) * mm});
            skPoint(sketch, "E38.71.42.0", {"position": v(374.65, -194.73) * mm});
            skPoint(sketch, "E38.71.43.0", {"position": v(374.65, -201.08) * mm});
            skPoint(sketch, "E38.71.44.0", {"position": v(374.65, -207.43) * mm});
            skPoint(sketch, "E38.71.45.0", {"position": v(374.65, -213.78) * mm});
            skPoint(sketch, "E38.71.46.0", {"position": v(374.65, -220.13) * mm});
            skPoint(sketch, "E38.71.47.0", {"position": v(374.65, -226.48) * mm});
            skPoint(sketch, "E38.71.48.0", {"position": v(374.65, -232.83) * mm});
            skPoint(sketch, "E38.71.49.0", {"position": v(374.65, -239.18) * mm});
            skPoint(sketch, "E38.71.50.0", {"position": v(374.65, -245.53) * mm});
            skPoint(sketch, "E38.71.51.0", {"position": v(374.65, -251.88) * mm});
            skPoint(sketch, "E38.71.52.0", {"position": v(374.65, -258.23) * mm});
            skPoint(sketch, "E38.71.53.0", {"position": v(374.65, -264.58) * mm});
            skPoint(sketch, "E38.71.54.0", {"position": v(374.65, -270.93) * mm});
            skPoint(sketch, "E38.71.55.0", {"position": v(374.65, -277.28) * mm});
            skPoint(sketch, "E38.71.56.0", {"position": v(374.65, -283.63) * mm});
            skPoint(sketch, "E38.71.57.0", {"position": v(374.65, -289.98) * mm});
            skPoint(sketch, "E38.71.58.0", {"position": v(374.65, -296.33) * mm});
            skPoint(sketch, "E38.71.59.0", {"position": v(374.65, -302.68) * mm});
            skPoint(sketch, "E38.71.60.0", {"position": v(374.65, -309.03) * mm});
            skPoint(sketch, "E38.71.61.0", {"position": v(374.65, -315.38) * mm});
            skPoint(sketch, "E38.71.62.0", {"position": v(374.65, -321.73) * mm});
            skPoint(sketch, "E38.71.63.0", {"position": v(374.65, -328.08) * mm});
            skPoint(sketch, "E38.71.64.0", {"position": v(374.65, -334.43) * mm});
            skPoint(sketch, "E38.71.65.0", {"position": v(374.65, -340.78) * mm});
            skPoint(sketch, "E38.71.66.0", {"position": v(374.65, -347.13) * mm});
            skPoint(sketch, "E38.71.67.0", {"position": v(374.65, -353.48) * mm});
            skPoint(sketch, "E38.71.68.0", {"position": v(374.65, -359.83) * mm});
            skPoint(sketch, "E38.71.69.0", {"position": v(374.65, -366.18) * mm});
            skPoint(sketch, "E38.71.70.0", {"position": v(374.65, -372.53) * mm});
            skPoint(sketch, "E38.71.71.0", {"position": v(374.65, -378.88) * mm});
            skPoint(sketch, "E38.71.72.0", {"position": v(374.65, -385.23) * mm});
            skPoint(sketch, "E38.71.73.0", {"position": v(374.65, -391.58) * mm});
            skPoint(sketch, "E38.71.74.0", {"position": v(374.65, -397.93) * mm});
            skPoint(sketch, "E38.71.75.0", {"position": v(374.65, -404.28) * mm});
            skPoint(sketch, "E38.71.76.0", {"position": v(374.65, -410.63) * mm});
            skPoint(sketch, "E38.71.77.0", {"position": v(374.65, -416.98) * mm});
            skPoint(sketch, "E38.71.78.0", {"position": v(374.65, -423.33) * mm});
            skPoint(sketch, "E38.71.79.0", {"position": v(374.65, -429.68) * mm});
            skPoint(sketch, "E38.71.80.0", {"position": v(374.65, -436.03) * mm});
            skPoint(sketch, "E38.71.81.0", {"position": v(374.65, -442.38) * mm});
            skPoint(sketch, "E38.71.82.0", {"position": v(374.65, -448.73) * mm});
            skPoint(sketch, "E38.71.83.0", {"position": v(374.65, -455.08) * mm});
            skPoint(sketch, "E38.71.84.0", {"position": v(374.65, -461.43) * mm});
            skPoint(sketch, "E38.71.85.0", {"position": v(374.65, -467.78) * mm});
            skPoint(sketch, "E38.71.86.0", {"position": v(374.65, -474.13) * mm});
            skPoint(sketch, "E38.71.87.0", {"position": v(374.65, -480.48) * mm});
            skPoint(sketch, "E38.71.88.0", {"position": v(374.65, -486.83) * mm});
            skPoint(sketch, "E38.71.89.0", {"position": v(374.65, -493.18) * mm});
            skPoint(sketch, "E38.71.90.0", {"position": v(374.65, -499.53) * mm});
            skPoint(sketch, "E38.71.91.0", {"position": v(374.65, -505.88) * mm});
            skPoint(sketch, "E38.71.92.0", {"position": v(374.65, -512.23) * mm});
            skPoint(sketch, "E38.71.93.0", {"position": v(374.65, -518.58) * mm});
            skPoint(sketch, "E38.71.94.0", {"position": v(374.65, -524.93) * mm});
            skPoint(sketch, "E38.71.95.0", {"position": v(374.65, -531.28) * mm});
            skPoint(sketch, "E38.71.96.0", {"position": v(374.65, -537.63) * mm});
            skPoint(sketch, "E38.71.97.0", {"position": v(374.65, -543.98) * mm});
            skPoint(sketch, "E38.71.98.0", {"position": v(374.65, -550.33) * mm});
            skPoint(sketch, "E38.71.99.0", {"position": v(374.65, -556.68) * mm});
            skPoint(sketch, "E38.72.0.0", {"position": v(381, 71.97) * mm});
            skPoint(sketch, "E38.72.1.0", {"position": v(381, 65.62) * mm});
            skPoint(sketch, "E38.72.2.0", {"position": v(381, 59.27) * mm});
            skPoint(sketch, "E38.72.3.0", {"position": v(381, 52.92) * mm});
            skPoint(sketch, "E38.72.4.0", {"position": v(381, 46.57) * mm});
            skPoint(sketch, "E38.72.5.0", {"position": v(381, 40.22) * mm});
            skPoint(sketch, "E38.72.6.0", {"position": v(381, 33.87) * mm});
            skPoint(sketch, "E38.72.7.0", {"position": v(381, 27.52) * mm});
            skPoint(sketch, "E38.72.8.0", {"position": v(381, 21.17) * mm});
            skPoint(sketch, "E38.72.9.0", {"position": v(381, 14.82) * mm});
            skPoint(sketch, "E38.72.10.0", {"position": v(381, 8.47) * mm});
            skPoint(sketch, "E38.72.11.0", {"position": v(381, 2.12) * mm});
            skPoint(sketch, "E38.72.12.0", {"position": v(381, -4.23) * mm});
            skPoint(sketch, "E38.72.13.0", {"position": v(381, -10.58) * mm});
            skPoint(sketch, "E38.72.14.0", {"position": v(381, -16.93) * mm});
            skPoint(sketch, "E38.72.15.0", {"position": v(381, -23.28) * mm});
            skPoint(sketch, "E38.72.16.0", {"position": v(381, -29.63) * mm});
            skPoint(sketch, "E38.72.17.0", {"position": v(381, -35.98) * mm});
            skPoint(sketch, "E38.72.18.0", {"position": v(381, -42.33) * mm});
            skPoint(sketch, "E38.72.19.0", {"position": v(381, -48.68) * mm});
            skPoint(sketch, "E38.72.20.0", {"position": v(381, -55.03) * mm});
            skPoint(sketch, "E38.72.21.0", {"position": v(381, -61.38) * mm});
            skPoint(sketch, "E38.72.22.0", {"position": v(381, -67.73) * mm});
            skPoint(sketch, "E38.72.23.0", {"position": v(381, -74.08) * mm});
            skPoint(sketch, "E38.72.24.0", {"position": v(381, -80.43) * mm});
            skPoint(sketch, "E38.72.25.0", {"position": v(381, -86.78) * mm});
            skPoint(sketch, "E38.72.26.0", {"position": v(381, -93.13) * mm});
            skPoint(sketch, "E38.72.27.0", {"position": v(381, -99.48) * mm});
            skPoint(sketch, "E38.72.28.0", {"position": v(381, -105.83) * mm});
            skPoint(sketch, "E38.72.29.0", {"position": v(381, -112.18) * mm});
            skPoint(sketch, "E38.72.30.0", {"position": v(381, -118.53) * mm});
            skPoint(sketch, "E38.72.31.0", {"position": v(381, -124.88) * mm});
            skPoint(sketch, "E38.72.32.0", {"position": v(381, -131.23) * mm});
            skPoint(sketch, "E38.72.33.0", {"position": v(381, -137.58) * mm});
            skPoint(sketch, "E38.72.34.0", {"position": v(381, -143.93) * mm});
            skPoint(sketch, "E38.72.35.0", {"position": v(381, -150.28) * mm});
            skPoint(sketch, "E38.72.36.0", {"position": v(381, -156.63) * mm});
            skPoint(sketch, "E38.72.37.0", {"position": v(381, -162.98) * mm});
            skPoint(sketch, "E38.72.38.0", {"position": v(381, -169.33) * mm});
            skPoint(sketch, "E38.72.39.0", {"position": v(381, -175.68) * mm});
            skPoint(sketch, "E38.72.40.0", {"position": v(381, -182.03) * mm});
            skPoint(sketch, "E38.72.41.0", {"position": v(381, -188.38) * mm});
            skPoint(sketch, "E38.72.42.0", {"position": v(381, -194.73) * mm});
            skPoint(sketch, "E38.72.43.0", {"position": v(381, -201.08) * mm});
            skPoint(sketch, "E38.72.44.0", {"position": v(381, -207.43) * mm});
            skPoint(sketch, "E38.72.45.0", {"position": v(381, -213.78) * mm});
            skPoint(sketch, "E38.72.46.0", {"position": v(381, -220.13) * mm});
            skPoint(sketch, "E38.72.47.0", {"position": v(381, -226.48) * mm});
            skPoint(sketch, "E38.72.48.0", {"position": v(381, -232.83) * mm});
            skPoint(sketch, "E38.72.49.0", {"position": v(381, -239.18) * mm});
            skPoint(sketch, "E38.72.50.0", {"position": v(381, -245.53) * mm});
            skPoint(sketch, "E38.72.51.0", {"position": v(381, -251.88) * mm});
            skPoint(sketch, "E38.72.52.0", {"position": v(381, -258.23) * mm});
            skPoint(sketch, "E38.72.53.0", {"position": v(381, -264.58) * mm});
            skPoint(sketch, "E38.72.54.0", {"position": v(381, -270.93) * mm});
            skPoint(sketch, "E38.72.55.0", {"position": v(381, -277.28) * mm});
            skPoint(sketch, "E38.72.56.0", {"position": v(381, -283.63) * mm});
            skPoint(sketch, "E38.72.57.0", {"position": v(381, -289.98) * mm});
            skPoint(sketch, "E38.72.58.0", {"position": v(381, -296.33) * mm});
            skPoint(sketch, "E38.72.59.0", {"position": v(381, -302.68) * mm});
            skPoint(sketch, "E38.72.60.0", {"position": v(381, -309.03) * mm});
            skPoint(sketch, "E38.72.61.0", {"position": v(381, -315.38) * mm});
            skPoint(sketch, "E38.72.62.0", {"position": v(381, -321.73) * mm});
            skPoint(sketch, "E38.72.63.0", {"position": v(381, -328.08) * mm});
            skPoint(sketch, "E38.72.64.0", {"position": v(381, -334.43) * mm});
            skPoint(sketch, "E38.72.65.0", {"position": v(381, -340.78) * mm});
            skPoint(sketch, "E38.72.66.0", {"position": v(381, -347.13) * mm});
            skPoint(sketch, "E38.72.67.0", {"position": v(381, -353.48) * mm});
            skPoint(sketch, "E38.72.68.0", {"position": v(381, -359.83) * mm});
            skPoint(sketch, "E38.72.69.0", {"position": v(381, -366.18) * mm});
            skPoint(sketch, "E38.72.70.0", {"position": v(381, -372.53) * mm});
            skPoint(sketch, "E38.72.71.0", {"position": v(381, -378.88) * mm});
            skPoint(sketch, "E38.72.72.0", {"position": v(381, -385.23) * mm});
            skPoint(sketch, "E38.72.73.0", {"position": v(381, -391.58) * mm});
            skPoint(sketch, "E38.72.74.0", {"position": v(381, -397.93) * mm});
            skPoint(sketch, "E38.72.75.0", {"position": v(381, -404.28) * mm});
            skPoint(sketch, "E38.72.76.0", {"position": v(381, -410.63) * mm});
            skPoint(sketch, "E38.72.77.0", {"position": v(381, -416.98) * mm});
            skPoint(sketch, "E38.72.78.0", {"position": v(381, -423.33) * mm});
            skPoint(sketch, "E38.72.79.0", {"position": v(381, -429.68) * mm});
            skPoint(sketch, "E38.72.80.0", {"position": v(381, -436.03) * mm});
            skPoint(sketch, "E38.72.81.0", {"position": v(381, -442.38) * mm});
            skPoint(sketch, "E38.72.82.0", {"position": v(381, -448.73) * mm});
            skPoint(sketch, "E38.72.83.0", {"position": v(381, -455.08) * mm});
            skPoint(sketch, "E38.72.84.0", {"position": v(381, -461.43) * mm});
            skPoint(sketch, "E38.72.85.0", {"position": v(381, -467.78) * mm});
            skPoint(sketch, "E38.72.86.0", {"position": v(381, -474.13) * mm});
            skPoint(sketch, "E38.72.87.0", {"position": v(381, -480.48) * mm});
            skPoint(sketch, "E38.72.88.0", {"position": v(381, -486.83) * mm});
            skPoint(sketch, "E38.72.89.0", {"position": v(381, -493.18) * mm});
            skPoint(sketch, "E38.72.90.0", {"position": v(381, -499.53) * mm});
            skPoint(sketch, "E38.72.91.0", {"position": v(381, -505.88) * mm});
            skPoint(sketch, "E38.72.92.0", {"position": v(381, -512.23) * mm});
            skPoint(sketch, "E38.72.93.0", {"position": v(381, -518.58) * mm});
            skPoint(sketch, "E38.72.94.0", {"position": v(381, -524.93) * mm});
            skPoint(sketch, "E38.72.95.0", {"position": v(381, -531.28) * mm});
            skPoint(sketch, "E38.72.96.0", {"position": v(381, -537.63) * mm});
            skPoint(sketch, "E38.72.97.0", {"position": v(381, -543.98) * mm});
            skPoint(sketch, "E38.72.98.0", {"position": v(381, -550.33) * mm});
            skPoint(sketch, "E38.72.99.0", {"position": v(381, -556.68) * mm});
            skPoint(sketch, "E38.73.0.0", {"position": v(387.35, 71.97) * mm});
            skPoint(sketch, "E38.73.1.0", {"position": v(387.35, 65.62) * mm});
            skPoint(sketch, "E38.73.2.0", {"position": v(387.35, 59.27) * mm});
            skPoint(sketch, "E38.73.3.0", {"position": v(387.35, 52.92) * mm});
            skPoint(sketch, "E38.73.4.0", {"position": v(387.35, 46.57) * mm});
            skPoint(sketch, "E38.73.5.0", {"position": v(387.35, 40.22) * mm});
            skPoint(sketch, "E38.73.6.0", {"position": v(387.35, 33.87) * mm});
            skPoint(sketch, "E38.73.7.0", {"position": v(387.35, 27.52) * mm});
            skPoint(sketch, "E38.73.8.0", {"position": v(387.35, 21.17) * mm});
            skPoint(sketch, "E38.73.9.0", {"position": v(387.35, 14.82) * mm});
            skPoint(sketch, "E38.73.10.0", {"position": v(387.35, 8.47) * mm});
            skPoint(sketch, "E38.73.11.0", {"position": v(387.35, 2.12) * mm});
            skPoint(sketch, "E38.73.12.0", {"position": v(387.35, -4.23) * mm});
            skPoint(sketch, "E38.73.13.0", {"position": v(387.35, -10.58) * mm});
            skPoint(sketch, "E38.73.14.0", {"position": v(387.35, -16.93) * mm});
            skPoint(sketch, "E38.73.15.0", {"position": v(387.35, -23.28) * mm});
            skPoint(sketch, "E38.73.16.0", {"position": v(387.35, -29.63) * mm});
            skPoint(sketch, "E38.73.17.0", {"position": v(387.35, -35.98) * mm});
            skPoint(sketch, "E38.73.18.0", {"position": v(387.35, -42.33) * mm});
            skPoint(sketch, "E38.73.19.0", {"position": v(387.35, -48.68) * mm});
            skPoint(sketch, "E38.73.20.0", {"position": v(387.35, -55.03) * mm});
            skPoint(sketch, "E38.73.21.0", {"position": v(387.35, -61.38) * mm});
            skPoint(sketch, "E38.73.22.0", {"position": v(387.35, -67.73) * mm});
            skPoint(sketch, "E38.73.23.0", {"position": v(387.35, -74.08) * mm});
            skPoint(sketch, "E38.73.24.0", {"position": v(387.35, -80.43) * mm});
            skPoint(sketch, "E38.73.25.0", {"position": v(387.35, -86.78) * mm});
            skPoint(sketch, "E38.73.26.0", {"position": v(387.35, -93.13) * mm});
            skPoint(sketch, "E38.73.27.0", {"position": v(387.35, -99.48) * mm});
            skPoint(sketch, "E38.73.28.0", {"position": v(387.35, -105.83) * mm});
            skPoint(sketch, "E38.73.29.0", {"position": v(387.35, -112.18) * mm});
            skPoint(sketch, "E38.73.30.0", {"position": v(387.35, -118.53) * mm});
            skPoint(sketch, "E38.73.31.0", {"position": v(387.35, -124.88) * mm});
            skPoint(sketch, "E38.73.32.0", {"position": v(387.35, -131.23) * mm});
            skPoint(sketch, "E38.73.33.0", {"position": v(387.35, -137.58) * mm});
            skPoint(sketch, "E38.73.34.0", {"position": v(387.35, -143.93) * mm});
            skPoint(sketch, "E38.73.35.0", {"position": v(387.35, -150.28) * mm});
            skPoint(sketch, "E38.73.36.0", {"position": v(387.35, -156.63) * mm});
            skPoint(sketch, "E38.73.37.0", {"position": v(387.35, -162.98) * mm});
            skPoint(sketch, "E38.73.38.0", {"position": v(387.35, -169.33) * mm});
            skPoint(sketch, "E38.73.39.0", {"position": v(387.35, -175.68) * mm});
            skPoint(sketch, "E38.73.40.0", {"position": v(387.35, -182.03) * mm});
            skPoint(sketch, "E38.73.41.0", {"position": v(387.35, -188.38) * mm});
            skPoint(sketch, "E38.73.42.0", {"position": v(387.35, -194.73) * mm});
            skPoint(sketch, "E38.73.43.0", {"position": v(387.35, -201.08) * mm});
            skPoint(sketch, "E38.73.44.0", {"position": v(387.35, -207.43) * mm});
            skPoint(sketch, "E38.73.45.0", {"position": v(387.35, -213.78) * mm});
            skPoint(sketch, "E38.73.46.0", {"position": v(387.35, -220.13) * mm});
            skPoint(sketch, "E38.73.47.0", {"position": v(387.35, -226.48) * mm});
            skPoint(sketch, "E38.73.48.0", {"position": v(387.35, -232.83) * mm});
            skPoint(sketch, "E38.73.49.0", {"position": v(387.35, -239.18) * mm});
            skPoint(sketch, "E38.73.50.0", {"position": v(387.35, -245.53) * mm});
            skPoint(sketch, "E38.73.51.0", {"position": v(387.35, -251.88) * mm});
            skPoint(sketch, "E38.73.52.0", {"position": v(387.35, -258.23) * mm});
            skPoint(sketch, "E38.73.53.0", {"position": v(387.35, -264.58) * mm});
            skPoint(sketch, "E38.73.54.0", {"position": v(387.35, -270.93) * mm});
            skPoint(sketch, "E38.73.55.0", {"position": v(387.35, -277.28) * mm});
            skPoint(sketch, "E38.73.56.0", {"position": v(387.35, -283.63) * mm});
            skPoint(sketch, "E38.73.57.0", {"position": v(387.35, -289.98) * mm});
            skPoint(sketch, "E38.73.58.0", {"position": v(387.35, -296.33) * mm});
            skPoint(sketch, "E38.73.59.0", {"position": v(387.35, -302.68) * mm});
            skPoint(sketch, "E38.73.60.0", {"position": v(387.35, -309.03) * mm});
            skPoint(sketch, "E38.73.61.0", {"position": v(387.35, -315.38) * mm});
            skPoint(sketch, "E38.73.62.0", {"position": v(387.35, -321.73) * mm});
            skPoint(sketch, "E38.73.63.0", {"position": v(387.35, -328.08) * mm});
            skPoint(sketch, "E38.73.64.0", {"position": v(387.35, -334.43) * mm});
            skPoint(sketch, "E38.73.65.0", {"position": v(387.35, -340.78) * mm});
            skPoint(sketch, "E38.73.66.0", {"position": v(387.35, -347.13) * mm});
            skPoint(sketch, "E38.73.67.0", {"position": v(387.35, -353.48) * mm});
            skPoint(sketch, "E38.73.68.0", {"position": v(387.35, -359.83) * mm});
            skPoint(sketch, "E38.73.69.0", {"position": v(387.35, -366.18) * mm});
            skPoint(sketch, "E38.73.70.0", {"position": v(387.35, -372.53) * mm});
            skPoint(sketch, "E38.73.71.0", {"position": v(387.35, -378.88) * mm});
            skPoint(sketch, "E38.73.72.0", {"position": v(387.35, -385.23) * mm});
            skPoint(sketch, "E38.73.73.0", {"position": v(387.35, -391.58) * mm});
            skPoint(sketch, "E38.73.74.0", {"position": v(387.35, -397.93) * mm});
            skPoint(sketch, "E38.73.75.0", {"position": v(387.35, -404.28) * mm});
            skPoint(sketch, "E38.73.76.0", {"position": v(387.35, -410.63) * mm});
            skPoint(sketch, "E38.73.77.0", {"position": v(387.35, -416.98) * mm});
            skPoint(sketch, "E38.73.78.0", {"position": v(387.35, -423.33) * mm});
            skPoint(sketch, "E38.73.79.0", {"position": v(387.35, -429.68) * mm});
            skPoint(sketch, "E38.73.80.0", {"position": v(387.35, -436.03) * mm});
            skPoint(sketch, "E38.73.81.0", {"position": v(387.35, -442.38) * mm});
            skPoint(sketch, "E38.73.82.0", {"position": v(387.35, -448.73) * mm});
            skPoint(sketch, "E38.73.83.0", {"position": v(387.35, -455.08) * mm});
            skPoint(sketch, "E38.73.84.0", {"position": v(387.35, -461.43) * mm});
            skPoint(sketch, "E38.73.85.0", {"position": v(387.35, -467.78) * mm});
            skPoint(sketch, "E38.73.86.0", {"position": v(387.35, -474.13) * mm});
            skPoint(sketch, "E38.73.87.0", {"position": v(387.35, -480.48) * mm});
            skPoint(sketch, "E38.73.88.0", {"position": v(387.35, -486.83) * mm});
            skPoint(sketch, "E38.73.89.0", {"position": v(387.35, -493.18) * mm});
            skPoint(sketch, "E38.73.90.0", {"position": v(387.35, -499.53) * mm});
            skPoint(sketch, "E38.73.91.0", {"position": v(387.35, -505.88) * mm});
            skPoint(sketch, "E38.73.92.0", {"position": v(387.35, -512.23) * mm});
            skPoint(sketch, "E38.73.93.0", {"position": v(387.35, -518.58) * mm});
            skPoint(sketch, "E38.73.94.0", {"position": v(387.35, -524.93) * mm});
            skPoint(sketch, "E38.73.95.0", {"position": v(387.35, -531.28) * mm});
            skPoint(sketch, "E38.73.96.0", {"position": v(387.35, -537.63) * mm});
            skPoint(sketch, "E38.73.97.0", {"position": v(387.35, -543.98) * mm});
            skPoint(sketch, "E38.73.98.0", {"position": v(387.35, -550.33) * mm});
            skPoint(sketch, "E38.73.99.0", {"position": v(387.35, -556.68) * mm});
            skPoint(sketch, "E38.74.0.0", {"position": v(393.7, 71.97) * mm});
            skPoint(sketch, "E38.74.1.0", {"position": v(393.7, 65.62) * mm});
            skPoint(sketch, "E38.74.2.0", {"position": v(393.7, 59.27) * mm});
            skPoint(sketch, "E38.74.3.0", {"position": v(393.7, 52.92) * mm});
            skPoint(sketch, "E38.74.4.0", {"position": v(393.7, 46.57) * mm});
            skPoint(sketch, "E38.74.5.0", {"position": v(393.7, 40.22) * mm});
            skPoint(sketch, "E38.74.6.0", {"position": v(393.7, 33.87) * mm});
            skPoint(sketch, "E38.74.7.0", {"position": v(393.7, 27.52) * mm});
            skPoint(sketch, "E38.74.8.0", {"position": v(393.7, 21.17) * mm});
            skPoint(sketch, "E38.74.9.0", {"position": v(393.7, 14.82) * mm});
            skPoint(sketch, "E38.74.10.0", {"position": v(393.7, 8.47) * mm});
            skPoint(sketch, "E38.74.11.0", {"position": v(393.7, 2.12) * mm});
            skPoint(sketch, "E38.74.12.0", {"position": v(393.7, -4.23) * mm});
            skPoint(sketch, "E38.74.13.0", {"position": v(393.7, -10.58) * mm});
            skPoint(sketch, "E38.74.14.0", {"position": v(393.7, -16.93) * mm});
            skPoint(sketch, "E38.74.15.0", {"position": v(393.7, -23.28) * mm});
            skPoint(sketch, "E38.74.16.0", {"position": v(393.7, -29.63) * mm});
            skPoint(sketch, "E38.74.17.0", {"position": v(393.7, -35.98) * mm});
            skPoint(sketch, "E38.74.18.0", {"position": v(393.7, -42.33) * mm});
            skPoint(sketch, "E38.74.19.0", {"position": v(393.7, -48.68) * mm});
            skPoint(sketch, "E38.74.20.0", {"position": v(393.7, -55.03) * mm});
            skPoint(sketch, "E38.74.21.0", {"position": v(393.7, -61.38) * mm});
            skPoint(sketch, "E38.74.22.0", {"position": v(393.7, -67.73) * mm});
            skPoint(sketch, "E38.74.23.0", {"position": v(393.7, -74.08) * mm});
            skPoint(sketch, "E38.74.24.0", {"position": v(393.7, -80.43) * mm});
            skPoint(sketch, "E38.74.25.0", {"position": v(393.7, -86.78) * mm});
            skPoint(sketch, "E38.74.26.0", {"position": v(393.7, -93.13) * mm});
            skPoint(sketch, "E38.74.27.0", {"position": v(393.7, -99.48) * mm});
            skPoint(sketch, "E38.74.28.0", {"position": v(393.7, -105.83) * mm});
            skPoint(sketch, "E38.74.29.0", {"position": v(393.7, -112.18) * mm});
            skPoint(sketch, "E38.74.30.0", {"position": v(393.7, -118.53) * mm});
            skPoint(sketch, "E38.74.31.0", {"position": v(393.7, -124.88) * mm});
            skPoint(sketch, "E38.74.32.0", {"position": v(393.7, -131.23) * mm});
            skPoint(sketch, "E38.74.33.0", {"position": v(393.7, -137.58) * mm});
            skPoint(sketch, "E38.74.34.0", {"position": v(393.7, -143.93) * mm});
            skPoint(sketch, "E38.74.35.0", {"position": v(393.7, -150.28) * mm});
            skPoint(sketch, "E38.74.36.0", {"position": v(393.7, -156.63) * mm});
            skPoint(sketch, "E38.74.37.0", {"position": v(393.7, -162.98) * mm});
            skPoint(sketch, "E38.74.38.0", {"position": v(393.7, -169.33) * mm});
            skPoint(sketch, "E38.74.39.0", {"position": v(393.7, -175.68) * mm});
            skPoint(sketch, "E38.74.40.0", {"position": v(393.7, -182.03) * mm});
            skPoint(sketch, "E38.74.41.0", {"position": v(393.7, -188.38) * mm});
            skPoint(sketch, "E38.74.42.0", {"position": v(393.7, -194.73) * mm});
            skPoint(sketch, "E38.74.43.0", {"position": v(393.7, -201.08) * mm});
            skPoint(sketch, "E38.74.44.0", {"position": v(393.7, -207.43) * mm});
            skPoint(sketch, "E38.74.45.0", {"position": v(393.7, -213.78) * mm});
            skPoint(sketch, "E38.74.46.0", {"position": v(393.7, -220.13) * mm});
            skPoint(sketch, "E38.74.47.0", {"position": v(393.7, -226.48) * mm});
            skPoint(sketch, "E38.74.48.0", {"position": v(393.7, -232.83) * mm});
            skPoint(sketch, "E38.74.49.0", {"position": v(393.7, -239.18) * mm});
            skPoint(sketch, "E38.74.50.0", {"position": v(393.7, -245.53) * mm});
            skPoint(sketch, "E38.74.51.0", {"position": v(393.7, -251.88) * mm});
            skPoint(sketch, "E38.74.52.0", {"position": v(393.7, -258.23) * mm});
            skPoint(sketch, "E38.74.53.0", {"position": v(393.7, -264.58) * mm});
            skPoint(sketch, "E38.74.54.0", {"position": v(393.7, -270.93) * mm});
            skPoint(sketch, "E38.74.55.0", {"position": v(393.7, -277.28) * mm});
            skPoint(sketch, "E38.74.56.0", {"position": v(393.7, -283.63) * mm});
            skPoint(sketch, "E38.74.57.0", {"position": v(393.7, -289.98) * mm});
            skPoint(sketch, "E38.74.58.0", {"position": v(393.7, -296.33) * mm});
            skPoint(sketch, "E38.74.59.0", {"position": v(393.7, -302.68) * mm});
            skPoint(sketch, "E38.74.60.0", {"position": v(393.7, -309.03) * mm});
            skPoint(sketch, "E38.74.61.0", {"position": v(393.7, -315.38) * mm});
            skPoint(sketch, "E38.74.62.0", {"position": v(393.7, -321.73) * mm});
            skPoint(sketch, "E38.74.63.0", {"position": v(393.7, -328.08) * mm});
            skPoint(sketch, "E38.74.64.0", {"position": v(393.7, -334.43) * mm});
            skPoint(sketch, "E38.74.65.0", {"position": v(393.7, -340.78) * mm});
            skPoint(sketch, "E38.74.66.0", {"position": v(393.7, -347.13) * mm});
            skPoint(sketch, "E38.74.67.0", {"position": v(393.7, -353.48) * mm});
            skPoint(sketch, "E38.74.68.0", {"position": v(393.7, -359.83) * mm});
            skPoint(sketch, "E38.74.69.0", {"position": v(393.7, -366.18) * mm});
            skPoint(sketch, "E38.74.70.0", {"position": v(393.7, -372.53) * mm});
            skPoint(sketch, "E38.74.71.0", {"position": v(393.7, -378.88) * mm});
            skPoint(sketch, "E38.74.72.0", {"position": v(393.7, -385.23) * mm});
            skPoint(sketch, "E38.74.73.0", {"position": v(393.7, -391.58) * mm});
            skPoint(sketch, "E38.74.74.0", {"position": v(393.7, -397.93) * mm});
            skPoint(sketch, "E38.74.75.0", {"position": v(393.7, -404.28) * mm});
            skPoint(sketch, "E38.74.76.0", {"position": v(393.7, -410.63) * mm});
            skPoint(sketch, "E38.74.77.0", {"position": v(393.7, -416.98) * mm});
            skPoint(sketch, "E38.74.78.0", {"position": v(393.7, -423.33) * mm});
            skPoint(sketch, "E38.74.79.0", {"position": v(393.7, -429.68) * mm});
            skPoint(sketch, "E38.74.80.0", {"position": v(393.7, -436.03) * mm});
            skPoint(sketch, "E38.74.81.0", {"position": v(393.7, -442.38) * mm});
            skPoint(sketch, "E38.74.82.0", {"position": v(393.7, -448.73) * mm});
            skPoint(sketch, "E38.74.83.0", {"position": v(393.7, -455.08) * mm});
            skPoint(sketch, "E38.74.84.0", {"position": v(393.7, -461.43) * mm});
            skPoint(sketch, "E38.74.85.0", {"position": v(393.7, -467.78) * mm});
            skPoint(sketch, "E38.74.86.0", {"position": v(393.7, -474.13) * mm});
            skPoint(sketch, "E38.74.87.0", {"position": v(393.7, -480.48) * mm});
            skPoint(sketch, "E38.74.88.0", {"position": v(393.7, -486.83) * mm});
            skPoint(sketch, "E38.74.89.0", {"position": v(393.7, -493.18) * mm});
            skPoint(sketch, "E38.74.90.0", {"position": v(393.7, -499.53) * mm});
            skPoint(sketch, "E38.74.91.0", {"position": v(393.7, -505.88) * mm});
            skPoint(sketch, "E38.74.92.0", {"position": v(393.7, -512.23) * mm});
            skPoint(sketch, "E38.74.93.0", {"position": v(393.7, -518.58) * mm});
            skPoint(sketch, "E38.74.94.0", {"position": v(393.7, -524.93) * mm});
            skPoint(sketch, "E38.74.95.0", {"position": v(393.7, -531.28) * mm});
            skPoint(sketch, "E38.74.96.0", {"position": v(393.7, -537.63) * mm});
            skPoint(sketch, "E38.74.97.0", {"position": v(393.7, -543.98) * mm});
            skPoint(sketch, "E38.74.98.0", {"position": v(393.7, -550.33) * mm});
            skPoint(sketch, "E38.74.99.0", {"position": v(393.7, -556.68) * mm});
            skPoint(sketch, "E38.75.0.0", {"position": v(400.05, 71.97) * mm});
            skPoint(sketch, "E38.75.1.0", {"position": v(400.05, 65.62) * mm});
            skPoint(sketch, "E38.75.2.0", {"position": v(400.05, 59.27) * mm});
            skPoint(sketch, "E38.75.3.0", {"position": v(400.05, 52.92) * mm});
            skPoint(sketch, "E38.75.4.0", {"position": v(400.05, 46.57) * mm});
            skPoint(sketch, "E38.75.5.0", {"position": v(400.05, 40.22) * mm});
            skPoint(sketch, "E38.75.6.0", {"position": v(400.05, 33.87) * mm});
            skPoint(sketch, "E38.75.7.0", {"position": v(400.05, 27.52) * mm});
            skPoint(sketch, "E38.75.8.0", {"position": v(400.05, 21.17) * mm});
            skPoint(sketch, "E38.75.9.0", {"position": v(400.05, 14.82) * mm});
            skPoint(sketch, "E38.75.10.0", {"position": v(400.05, 8.47) * mm});
            skPoint(sketch, "E38.75.11.0", {"position": v(400.05, 2.12) * mm});
            skPoint(sketch, "E38.75.12.0", {"position": v(400.05, -4.23) * mm});
            skPoint(sketch, "E38.75.13.0", {"position": v(400.05, -10.58) * mm});
            skPoint(sketch, "E38.75.14.0", {"position": v(400.05, -16.93) * mm});
            skPoint(sketch, "E38.75.15.0", {"position": v(400.05, -23.28) * mm});
            skPoint(sketch, "E38.75.16.0", {"position": v(400.05, -29.63) * mm});
            skPoint(sketch, "E38.75.17.0", {"position": v(400.05, -35.98) * mm});
            skPoint(sketch, "E38.75.18.0", {"position": v(400.05, -42.33) * mm});
            skPoint(sketch, "E38.75.19.0", {"position": v(400.05, -48.68) * mm});
            skPoint(sketch, "E38.75.20.0", {"position": v(400.05, -55.03) * mm});
            skPoint(sketch, "E38.75.21.0", {"position": v(400.05, -61.38) * mm});
            skPoint(sketch, "E38.75.22.0", {"position": v(400.05, -67.73) * mm});
            skPoint(sketch, "E38.75.23.0", {"position": v(400.05, -74.08) * mm});
            skPoint(sketch, "E38.75.24.0", {"position": v(400.05, -80.43) * mm});
            skPoint(sketch, "E38.75.25.0", {"position": v(400.05, -86.78) * mm});
            skPoint(sketch, "E38.75.26.0", {"position": v(400.05, -93.13) * mm});
            skPoint(sketch, "E38.75.27.0", {"position": v(400.05, -99.48) * mm});
            skPoint(sketch, "E38.75.28.0", {"position": v(400.05, -105.83) * mm});
            skPoint(sketch, "E38.75.29.0", {"position": v(400.05, -112.18) * mm});
            skPoint(sketch, "E38.75.30.0", {"position": v(400.05, -118.53) * mm});
            skPoint(sketch, "E38.75.31.0", {"position": v(400.05, -124.88) * mm});
            skPoint(sketch, "E38.75.32.0", {"position": v(400.05, -131.23) * mm});
            skPoint(sketch, "E38.75.33.0", {"position": v(400.05, -137.58) * mm});
            skPoint(sketch, "E38.75.34.0", {"position": v(400.05, -143.93) * mm});
            skPoint(sketch, "E38.75.35.0", {"position": v(400.05, -150.28) * mm});
            skPoint(sketch, "E38.75.36.0", {"position": v(400.05, -156.63) * mm});
            skPoint(sketch, "E38.75.37.0", {"position": v(400.05, -162.98) * mm});
            skPoint(sketch, "E38.75.38.0", {"position": v(400.05, -169.33) * mm});
            skPoint(sketch, "E38.75.39.0", {"position": v(400.05, -175.68) * mm});
            skPoint(sketch, "E38.75.40.0", {"position": v(400.05, -182.03) * mm});
            skPoint(sketch, "E38.75.41.0", {"position": v(400.05, -188.38) * mm});
            skPoint(sketch, "E38.75.42.0", {"position": v(400.05, -194.73) * mm});
            skPoint(sketch, "E38.75.43.0", {"position": v(400.05, -201.08) * mm});
            skPoint(sketch, "E38.75.44.0", {"position": v(400.05, -207.43) * mm});
            skPoint(sketch, "E38.75.45.0", {"position": v(400.05, -213.78) * mm});
            skPoint(sketch, "E38.75.46.0", {"position": v(400.05, -220.13) * mm});
            skPoint(sketch, "E38.75.47.0", {"position": v(400.05, -226.48) * mm});
            skPoint(sketch, "E38.75.48.0", {"position": v(400.05, -232.83) * mm});
            skPoint(sketch, "E38.75.49.0", {"position": v(400.05, -239.18) * mm});
            skPoint(sketch, "E38.75.50.0", {"position": v(400.05, -245.53) * mm});
            skPoint(sketch, "E38.75.51.0", {"position": v(400.05, -251.88) * mm});
            skPoint(sketch, "E38.75.52.0", {"position": v(400.05, -258.23) * mm});
            skPoint(sketch, "E38.75.53.0", {"position": v(400.05, -264.58) * mm});
            skPoint(sketch, "E38.75.54.0", {"position": v(400.05, -270.93) * mm});
            skPoint(sketch, "E38.75.55.0", {"position": v(400.05, -277.28) * mm});
            skPoint(sketch, "E38.75.56.0", {"position": v(400.05, -283.63) * mm});
            skPoint(sketch, "E38.75.57.0", {"position": v(400.05, -289.98) * mm});
            skPoint(sketch, "E38.75.58.0", {"position": v(400.05, -296.33) * mm});
            skPoint(sketch, "E38.75.59.0", {"position": v(400.05, -302.68) * mm});
            skPoint(sketch, "E38.75.60.0", {"position": v(400.05, -309.03) * mm});
            skPoint(sketch, "E38.75.61.0", {"position": v(400.05, -315.38) * mm});
            skPoint(sketch, "E38.75.62.0", {"position": v(400.05, -321.73) * mm});
            skPoint(sketch, "E38.75.63.0", {"position": v(400.05, -328.08) * mm});
            skPoint(sketch, "E38.75.64.0", {"position": v(400.05, -334.43) * mm});
            skPoint(sketch, "E38.75.65.0", {"position": v(400.05, -340.78) * mm});
            skPoint(sketch, "E38.75.66.0", {"position": v(400.05, -347.13) * mm});
            skPoint(sketch, "E38.75.67.0", {"position": v(400.05, -353.48) * mm});
            skPoint(sketch, "E38.75.68.0", {"position": v(400.05, -359.83) * mm});
            skPoint(sketch, "E38.75.69.0", {"position": v(400.05, -366.18) * mm});
            skPoint(sketch, "E38.75.70.0", {"position": v(400.05, -372.53) * mm});
            skPoint(sketch, "E38.75.71.0", {"position": v(400.05, -378.88) * mm});
            skPoint(sketch, "E38.75.72.0", {"position": v(400.05, -385.23) * mm});
            skPoint(sketch, "E38.75.73.0", {"position": v(400.05, -391.58) * mm});
            skPoint(sketch, "E38.75.74.0", {"position": v(400.05, -397.93) * mm});
            skPoint(sketch, "E38.75.75.0", {"position": v(400.05, -404.28) * mm});
            skPoint(sketch, "E38.75.76.0", {"position": v(400.05, -410.63) * mm});
            skPoint(sketch, "E38.75.77.0", {"position": v(400.05, -416.98) * mm});
            skPoint(sketch, "E38.75.78.0", {"position": v(400.05, -423.33) * mm});
            skPoint(sketch, "E38.75.79.0", {"position": v(400.05, -429.68) * mm});
            skPoint(sketch, "E38.75.80.0", {"position": v(400.05, -436.03) * mm});
            skPoint(sketch, "E38.75.81.0", {"position": v(400.05, -442.38) * mm});
            skPoint(sketch, "E38.75.82.0", {"position": v(400.05, -448.73) * mm});
            skPoint(sketch, "E38.75.83.0", {"position": v(400.05, -455.08) * mm});
            skPoint(sketch, "E38.75.84.0", {"position": v(400.05, -461.43) * mm});
            skPoint(sketch, "E38.75.85.0", {"position": v(400.05, -467.78) * mm});
            skPoint(sketch, "E38.75.86.0", {"position": v(400.05, -474.13) * mm});
            skPoint(sketch, "E38.75.87.0", {"position": v(400.05, -480.48) * mm});
            skPoint(sketch, "E38.75.88.0", {"position": v(400.05, -486.83) * mm});
            skPoint(sketch, "E38.75.89.0", {"position": v(400.05, -493.18) * mm});
            skPoint(sketch, "E38.75.90.0", {"position": v(400.05, -499.53) * mm});
            skPoint(sketch, "E38.75.91.0", {"position": v(400.05, -505.88) * mm});
            skPoint(sketch, "E38.75.92.0", {"position": v(400.05, -512.23) * mm});
            skPoint(sketch, "E38.75.93.0", {"position": v(400.05, -518.58) * mm});
            skPoint(sketch, "E38.75.94.0", {"position": v(400.05, -524.93) * mm});
            skPoint(sketch, "E38.75.95.0", {"position": v(400.05, -531.28) * mm});
            skPoint(sketch, "E38.75.96.0", {"position": v(400.05, -537.63) * mm});
            skPoint(sketch, "E38.75.97.0", {"position": v(400.05, -543.98) * mm});
            skPoint(sketch, "E38.75.98.0", {"position": v(400.05, -550.33) * mm});
            skPoint(sketch, "E38.75.99.0", {"position": v(400.05, -556.68) * mm});
            skPoint(sketch, "E38.76.0.0", {"position": v(406.4, 71.97) * mm});
            skPoint(sketch, "E38.76.1.0", {"position": v(406.4, 65.62) * mm});
            skPoint(sketch, "E38.76.2.0", {"position": v(406.4, 59.27) * mm});
            skPoint(sketch, "E38.76.3.0", {"position": v(406.4, 52.92) * mm});
            skPoint(sketch, "E38.76.4.0", {"position": v(406.4, 46.57) * mm});
            skPoint(sketch, "E38.76.5.0", {"position": v(406.4, 40.22) * mm});
            skPoint(sketch, "E38.76.6.0", {"position": v(406.4, 33.87) * mm});
            skPoint(sketch, "E38.76.7.0", {"position": v(406.4, 27.52) * mm});
            skPoint(sketch, "E38.76.8.0", {"position": v(406.4, 21.17) * mm});
            skPoint(sketch, "E38.76.9.0", {"position": v(406.4, 14.82) * mm});
            skPoint(sketch, "E38.76.10.0", {"position": v(406.4, 8.47) * mm});
            skPoint(sketch, "E38.76.11.0", {"position": v(406.4, 2.12) * mm});
            skPoint(sketch, "E38.76.12.0", {"position": v(406.4, -4.23) * mm});
            skPoint(sketch, "E38.76.13.0", {"position": v(406.4, -10.58) * mm});
            skPoint(sketch, "E38.76.14.0", {"position": v(406.4, -16.93) * mm});
            skPoint(sketch, "E38.76.15.0", {"position": v(406.4, -23.28) * mm});
            skPoint(sketch, "E38.76.16.0", {"position": v(406.4, -29.63) * mm});
            skPoint(sketch, "E38.76.17.0", {"position": v(406.4, -35.98) * mm});
            skPoint(sketch, "E38.76.18.0", {"position": v(406.4, -42.33) * mm});
            skPoint(sketch, "E38.76.19.0", {"position": v(406.4, -48.68) * mm});
            skPoint(sketch, "E38.76.20.0", {"position": v(406.4, -55.03) * mm});
            skPoint(sketch, "E38.76.21.0", {"position": v(406.4, -61.38) * mm});
            skPoint(sketch, "E38.76.22.0", {"position": v(406.4, -67.73) * mm});
            skPoint(sketch, "E38.76.23.0", {"position": v(406.4, -74.08) * mm});
            skPoint(sketch, "E38.76.24.0", {"position": v(406.4, -80.43) * mm});
            skPoint(sketch, "E38.76.25.0", {"position": v(406.4, -86.78) * mm});
            skPoint(sketch, "E38.76.26.0", {"position": v(406.4, -93.13) * mm});
            skPoint(sketch, "E38.76.27.0", {"position": v(406.4, -99.48) * mm});
            skPoint(sketch, "E38.76.28.0", {"position": v(406.4, -105.83) * mm});
            skPoint(sketch, "E38.76.29.0", {"position": v(406.4, -112.18) * mm});
            skPoint(sketch, "E38.76.30.0", {"position": v(406.4, -118.53) * mm});
            skPoint(sketch, "E38.76.31.0", {"position": v(406.4, -124.88) * mm});
            skPoint(sketch, "E38.76.32.0", {"position": v(406.4, -131.23) * mm});
            skPoint(sketch, "E38.76.33.0", {"position": v(406.4, -137.58) * mm});
            skPoint(sketch, "E38.76.34.0", {"position": v(406.4, -143.93) * mm});
            skPoint(sketch, "E38.76.35.0", {"position": v(406.4, -150.28) * mm});
            skPoint(sketch, "E38.76.36.0", {"position": v(406.4, -156.63) * mm});
            skPoint(sketch, "E38.76.37.0", {"position": v(406.4, -162.98) * mm});
            skPoint(sketch, "E38.76.38.0", {"position": v(406.4, -169.33) * mm});
            skPoint(sketch, "E38.76.39.0", {"position": v(406.4, -175.68) * mm});
            skPoint(sketch, "E38.76.40.0", {"position": v(406.4, -182.03) * mm});
            skPoint(sketch, "E38.76.41.0", {"position": v(406.4, -188.38) * mm});
            skPoint(sketch, "E38.76.42.0", {"position": v(406.4, -194.73) * mm});
            skPoint(sketch, "E38.76.43.0", {"position": v(406.4, -201.08) * mm});
            skPoint(sketch, "E38.76.44.0", {"position": v(406.4, -207.43) * mm});
            skPoint(sketch, "E38.76.45.0", {"position": v(406.4, -213.78) * mm});
            skPoint(sketch, "E38.76.46.0", {"position": v(406.4, -220.13) * mm});
            skPoint(sketch, "E38.76.47.0", {"position": v(406.4, -226.48) * mm});
            skPoint(sketch, "E38.76.48.0", {"position": v(406.4, -232.83) * mm});
            skPoint(sketch, "E38.76.49.0", {"position": v(406.4, -239.18) * mm});
            skPoint(sketch, "E38.76.50.0", {"position": v(406.4, -245.53) * mm});
            skPoint(sketch, "E38.76.51.0", {"position": v(406.4, -251.88) * mm});
            skPoint(sketch, "E38.76.52.0", {"position": v(406.4, -258.23) * mm});
            skPoint(sketch, "E38.76.53.0", {"position": v(406.4, -264.58) * mm});
            skPoint(sketch, "E38.76.54.0", {"position": v(406.4, -270.93) * mm});
            skPoint(sketch, "E38.76.55.0", {"position": v(406.4, -277.28) * mm});
            skPoint(sketch, "E38.76.56.0", {"position": v(406.4, -283.63) * mm});
            skPoint(sketch, "E38.76.57.0", {"position": v(406.4, -289.98) * mm});
            skPoint(sketch, "E38.76.58.0", {"position": v(406.4, -296.33) * mm});
            skPoint(sketch, "E38.76.59.0", {"position": v(406.4, -302.68) * mm});
            skPoint(sketch, "E38.76.60.0", {"position": v(406.4, -309.03) * mm});
            skPoint(sketch, "E38.76.61.0", {"position": v(406.4, -315.38) * mm});
            skPoint(sketch, "E38.76.62.0", {"position": v(406.4, -321.73) * mm});
            skPoint(sketch, "E38.76.63.0", {"position": v(406.4, -328.08) * mm});
            skPoint(sketch, "E38.76.64.0", {"position": v(406.4, -334.43) * mm});
            skPoint(sketch, "E38.76.65.0", {"position": v(406.4, -340.78) * mm});
            skPoint(sketch, "E38.76.66.0", {"position": v(406.4, -347.13) * mm});
            skPoint(sketch, "E38.76.67.0", {"position": v(406.4, -353.48) * mm});
            skPoint(sketch, "E38.76.68.0", {"position": v(406.4, -359.83) * mm});
            skPoint(sketch, "E38.76.69.0", {"position": v(406.4, -366.18) * mm});
            skPoint(sketch, "E38.76.70.0", {"position": v(406.4, -372.53) * mm});
            skPoint(sketch, "E38.76.71.0", {"position": v(406.4, -378.88) * mm});
            skPoint(sketch, "E38.76.72.0", {"position": v(406.4, -385.23) * mm});
            skPoint(sketch, "E38.76.73.0", {"position": v(406.4, -391.58) * mm});
            skPoint(sketch, "E38.76.74.0", {"position": v(406.4, -397.93) * mm});
            skPoint(sketch, "E38.76.75.0", {"position": v(406.4, -404.28) * mm});
            skPoint(sketch, "E38.76.76.0", {"position": v(406.4, -410.63) * mm});
            skPoint(sketch, "E38.76.77.0", {"position": v(406.4, -416.98) * mm});
            skPoint(sketch, "E38.76.78.0", {"position": v(406.4, -423.33) * mm});
            skPoint(sketch, "E38.76.79.0", {"position": v(406.4, -429.68) * mm});
            skPoint(sketch, "E38.76.80.0", {"position": v(406.4, -436.03) * mm});
            skPoint(sketch, "E38.76.81.0", {"position": v(406.4, -442.38) * mm});
            skPoint(sketch, "E38.76.82.0", {"position": v(406.4, -448.73) * mm});
            skPoint(sketch, "E38.76.83.0", {"position": v(406.4, -455.08) * mm});
            skPoint(sketch, "E38.76.84.0", {"position": v(406.4, -461.43) * mm});
            skPoint(sketch, "E38.76.85.0", {"position": v(406.4, -467.78) * mm});
            skPoint(sketch, "E38.76.86.0", {"position": v(406.4, -474.13) * mm});
            skPoint(sketch, "E38.76.87.0", {"position": v(406.4, -480.48) * mm});
            skPoint(sketch, "E38.76.88.0", {"position": v(406.4, -486.83) * mm});
            skPoint(sketch, "E38.76.89.0", {"position": v(406.4, -493.18) * mm});
            skPoint(sketch, "E38.76.90.0", {"position": v(406.4, -499.53) * mm});
            skPoint(sketch, "E38.76.91.0", {"position": v(406.4, -505.88) * mm});
            skPoint(sketch, "E38.76.92.0", {"position": v(406.4, -512.23) * mm});
            skPoint(sketch, "E38.76.93.0", {"position": v(406.4, -518.58) * mm});
            skPoint(sketch, "E38.76.94.0", {"position": v(406.4, -524.93) * mm});
            skPoint(sketch, "E38.76.95.0", {"position": v(406.4, -531.28) * mm});
            skPoint(sketch, "E38.76.96.0", {"position": v(406.4, -537.63) * mm});
            skPoint(sketch, "E38.76.97.0", {"position": v(406.4, -543.98) * mm});
            skPoint(sketch, "E38.76.98.0", {"position": v(406.4, -550.33) * mm});
            skPoint(sketch, "E38.76.99.0", {"position": v(406.4, -556.68) * mm});
            skPoint(sketch, "E38.77.0.0", {"position": v(412.75, 71.97) * mm});
            skPoint(sketch, "E38.77.1.0", {"position": v(412.75, 65.62) * mm});
            skPoint(sketch, "E38.77.2.0", {"position": v(412.75, 59.27) * mm});
            skPoint(sketch, "E38.77.3.0", {"position": v(412.75, 52.92) * mm});
            skPoint(sketch, "E38.77.4.0", {"position": v(412.75, 46.57) * mm});
            skPoint(sketch, "E38.77.5.0", {"position": v(412.75, 40.22) * mm});
            skPoint(sketch, "E38.77.6.0", {"position": v(412.75, 33.87) * mm});
            skPoint(sketch, "E38.77.7.0", {"position": v(412.75, 27.52) * mm});
            skPoint(sketch, "E38.77.8.0", {"position": v(412.75, 21.17) * mm});
            skPoint(sketch, "E38.77.9.0", {"position": v(412.75, 14.82) * mm});
            skPoint(sketch, "E38.77.10.0", {"position": v(412.75, 8.47) * mm});
            skPoint(sketch, "E38.77.11.0", {"position": v(412.75, 2.12) * mm});
            skPoint(sketch, "E38.77.12.0", {"position": v(412.75, -4.23) * mm});
            skPoint(sketch, "E38.77.13.0", {"position": v(412.75, -10.58) * mm});
            skPoint(sketch, "E38.77.14.0", {"position": v(412.75, -16.93) * mm});
            skPoint(sketch, "E38.77.15.0", {"position": v(412.75, -23.28) * mm});
            skPoint(sketch, "E38.77.16.0", {"position": v(412.75, -29.63) * mm});
            skPoint(sketch, "E38.77.17.0", {"position": v(412.75, -35.98) * mm});
            skPoint(sketch, "E38.77.18.0", {"position": v(412.75, -42.33) * mm});
            skPoint(sketch, "E38.77.19.0", {"position": v(412.75, -48.68) * mm});
            skPoint(sketch, "E38.77.20.0", {"position": v(412.75, -55.03) * mm});
            skPoint(sketch, "E38.77.21.0", {"position": v(412.75, -61.38) * mm});
            skPoint(sketch, "E38.77.22.0", {"position": v(412.75, -67.73) * mm});
            skPoint(sketch, "E38.77.23.0", {"position": v(412.75, -74.08) * mm});
            skPoint(sketch, "E38.77.24.0", {"position": v(412.75, -80.43) * mm});
            skPoint(sketch, "E38.77.25.0", {"position": v(412.75, -86.78) * mm});
            skPoint(sketch, "E38.77.26.0", {"position": v(412.75, -93.13) * mm});
            skPoint(sketch, "E38.77.27.0", {"position": v(412.75, -99.48) * mm});
            skPoint(sketch, "E38.77.28.0", {"position": v(412.75, -105.83) * mm});
            skPoint(sketch, "E38.77.29.0", {"position": v(412.75, -112.18) * mm});
            skPoint(sketch, "E38.77.30.0", {"position": v(412.75, -118.53) * mm});
            skPoint(sketch, "E38.77.31.0", {"position": v(412.75, -124.88) * mm});
            skPoint(sketch, "E38.77.32.0", {"position": v(412.75, -131.23) * mm});
            skPoint(sketch, "E38.77.33.0", {"position": v(412.75, -137.58) * mm});
            skPoint(sketch, "E38.77.34.0", {"position": v(412.75, -143.93) * mm});
            skPoint(sketch, "E38.77.35.0", {"position": v(412.75, -150.28) * mm});
            skPoint(sketch, "E38.77.36.0", {"position": v(412.75, -156.63) * mm});
            skPoint(sketch, "E38.77.37.0", {"position": v(412.75, -162.98) * mm});
            skPoint(sketch, "E38.77.38.0", {"position": v(412.75, -169.33) * mm});
            skPoint(sketch, "E38.77.39.0", {"position": v(412.75, -175.68) * mm});
            skPoint(sketch, "E38.77.40.0", {"position": v(412.75, -182.03) * mm});
            skPoint(sketch, "E38.77.41.0", {"position": v(412.75, -188.38) * mm});
            skPoint(sketch, "E38.77.42.0", {"position": v(412.75, -194.73) * mm});
            skPoint(sketch, "E38.77.43.0", {"position": v(412.75, -201.08) * mm});
            skPoint(sketch, "E38.77.44.0", {"position": v(412.75, -207.43) * mm});
            skPoint(sketch, "E38.77.45.0", {"position": v(412.75, -213.78) * mm});
            skPoint(sketch, "E38.77.46.0", {"position": v(412.75, -220.13) * mm});
            skPoint(sketch, "E38.77.47.0", {"position": v(412.75, -226.48) * mm});
            skPoint(sketch, "E38.77.48.0", {"position": v(412.75, -232.83) * mm});
            skPoint(sketch, "E38.77.49.0", {"position": v(412.75, -239.18) * mm});
            skPoint(sketch, "E38.77.50.0", {"position": v(412.75, -245.53) * mm});
            skPoint(sketch, "E38.77.51.0", {"position": v(412.75, -251.88) * mm});
            skPoint(sketch, "E38.77.52.0", {"position": v(412.75, -258.23) * mm});
            skPoint(sketch, "E38.77.53.0", {"position": v(412.75, -264.58) * mm});
            skPoint(sketch, "E38.77.54.0", {"position": v(412.75, -270.93) * mm});
            skPoint(sketch, "E38.77.55.0", {"position": v(412.75, -277.28) * mm});
            skPoint(sketch, "E38.77.56.0", {"position": v(412.75, -283.63) * mm});
            skPoint(sketch, "E38.77.57.0", {"position": v(412.75, -289.98) * mm});
            skPoint(sketch, "E38.77.58.0", {"position": v(412.75, -296.33) * mm});
            skPoint(sketch, "E38.77.59.0", {"position": v(412.75, -302.68) * mm});
            skPoint(sketch, "E38.77.60.0", {"position": v(412.75, -309.03) * mm});
            skPoint(sketch, "E38.77.61.0", {"position": v(412.75, -315.38) * mm});
            skPoint(sketch, "E38.77.62.0", {"position": v(412.75, -321.73) * mm});
            skPoint(sketch, "E38.77.63.0", {"position": v(412.75, -328.08) * mm});
            skPoint(sketch, "E38.77.64.0", {"position": v(412.75, -334.43) * mm});
            skPoint(sketch, "E38.77.65.0", {"position": v(412.75, -340.78) * mm});
            skPoint(sketch, "E38.77.66.0", {"position": v(412.75, -347.13) * mm});
            skPoint(sketch, "E38.77.67.0", {"position": v(412.75, -353.48) * mm});
            skPoint(sketch, "E38.77.68.0", {"position": v(412.75, -359.83) * mm});
            skPoint(sketch, "E38.77.69.0", {"position": v(412.75, -366.18) * mm});
            skPoint(sketch, "E38.77.70.0", {"position": v(412.75, -372.53) * mm});
            skPoint(sketch, "E38.77.71.0", {"position": v(412.75, -378.88) * mm});
            skPoint(sketch, "E38.77.72.0", {"position": v(412.75, -385.23) * mm});
            skPoint(sketch, "E38.77.73.0", {"position": v(412.75, -391.58) * mm});
            skPoint(sketch, "E38.77.74.0", {"position": v(412.75, -397.93) * mm});
            skPoint(sketch, "E38.77.75.0", {"position": v(412.75, -404.28) * mm});
            skPoint(sketch, "E38.77.76.0", {"position": v(412.75, -410.63) * mm});
            skPoint(sketch, "E38.77.77.0", {"position": v(412.75, -416.98) * mm});
            skPoint(sketch, "E38.77.78.0", {"position": v(412.75, -423.33) * mm});
            skPoint(sketch, "E38.77.79.0", {"position": v(412.75, -429.68) * mm});
            skPoint(sketch, "E38.77.80.0", {"position": v(412.75, -436.03) * mm});
            skPoint(sketch, "E38.77.81.0", {"position": v(412.75, -442.38) * mm});
            skPoint(sketch, "E38.77.82.0", {"position": v(412.75, -448.73) * mm});
            skPoint(sketch, "E38.77.83.0", {"position": v(412.75, -455.08) * mm});
            skPoint(sketch, "E38.77.84.0", {"position": v(412.75, -461.43) * mm});
            skPoint(sketch, "E38.77.85.0", {"position": v(412.75, -467.78) * mm});
            skPoint(sketch, "E38.77.86.0", {"position": v(412.75, -474.13) * mm});
            skPoint(sketch, "E38.77.87.0", {"position": v(412.75, -480.48) * mm});
            skPoint(sketch, "E38.77.88.0", {"position": v(412.75, -486.83) * mm});
            skPoint(sketch, "E38.77.89.0", {"position": v(412.75, -493.18) * mm});
            skPoint(sketch, "E38.77.90.0", {"position": v(412.75, -499.53) * mm});
            skPoint(sketch, "E38.77.91.0", {"position": v(412.75, -505.88) * mm});
            skPoint(sketch, "E38.77.92.0", {"position": v(412.75, -512.23) * mm});
            skPoint(sketch, "E38.77.93.0", {"position": v(412.75, -518.58) * mm});
            skPoint(sketch, "E38.77.94.0", {"position": v(412.75, -524.93) * mm});
            skPoint(sketch, "E38.77.95.0", {"position": v(412.75, -531.28) * mm});
            skPoint(sketch, "E38.77.96.0", {"position": v(412.75, -537.63) * mm});
            skPoint(sketch, "E38.77.97.0", {"position": v(412.75, -543.98) * mm});
            skPoint(sketch, "E38.77.98.0", {"position": v(412.75, -550.33) * mm});
            skPoint(sketch, "E38.77.99.0", {"position": v(412.75, -556.68) * mm});
            skPoint(sketch, "E38.78.0.0", {"position": v(419.1, 71.97) * mm});
            skPoint(sketch, "E38.78.1.0", {"position": v(419.1, 65.62) * mm});
            skPoint(sketch, "E38.78.2.0", {"position": v(419.1, 59.27) * mm});
            skPoint(sketch, "E38.78.3.0", {"position": v(419.1, 52.92) * mm});
            skPoint(sketch, "E38.78.4.0", {"position": v(419.1, 46.57) * mm});
            skPoint(sketch, "E38.78.5.0", {"position": v(419.1, 40.22) * mm});
            skPoint(sketch, "E38.78.6.0", {"position": v(419.1, 33.87) * mm});
            skPoint(sketch, "E38.78.7.0", {"position": v(419.1, 27.52) * mm});
            skPoint(sketch, "E38.78.8.0", {"position": v(419.1, 21.17) * mm});
            skPoint(sketch, "E38.78.9.0", {"position": v(419.1, 14.82) * mm});
            skPoint(sketch, "E38.78.10.0", {"position": v(419.1, 8.47) * mm});
            skPoint(sketch, "E38.78.11.0", {"position": v(419.1, 2.12) * mm});
            skPoint(sketch, "E38.78.12.0", {"position": v(419.1, -4.23) * mm});
            skPoint(sketch, "E38.78.13.0", {"position": v(419.1, -10.58) * mm});
            skPoint(sketch, "E38.78.14.0", {"position": v(419.1, -16.93) * mm});
            skPoint(sketch, "E38.78.15.0", {"position": v(419.1, -23.28) * mm});
            skPoint(sketch, "E38.78.16.0", {"position": v(419.1, -29.63) * mm});
            skPoint(sketch, "E38.78.17.0", {"position": v(419.1, -35.98) * mm});
            skPoint(sketch, "E38.78.18.0", {"position": v(419.1, -42.33) * mm});
            skPoint(sketch, "E38.78.19.0", {"position": v(419.1, -48.68) * mm});
            skPoint(sketch, "E38.78.20.0", {"position": v(419.1, -55.03) * mm});
            skPoint(sketch, "E38.78.21.0", {"position": v(419.1, -61.38) * mm});
            skPoint(sketch, "E38.78.22.0", {"position": v(419.1, -67.73) * mm});
            skPoint(sketch, "E38.78.23.0", {"position": v(419.1, -74.08) * mm});
            skPoint(sketch, "E38.78.24.0", {"position": v(419.1, -80.43) * mm});
            skPoint(sketch, "E38.78.25.0", {"position": v(419.1, -86.78) * mm});
            skPoint(sketch, "E38.78.26.0", {"position": v(419.1, -93.13) * mm});
            skPoint(sketch, "E38.78.27.0", {"position": v(419.1, -99.48) * mm});
            skPoint(sketch, "E38.78.28.0", {"position": v(419.1, -105.83) * mm});
            skPoint(sketch, "E38.78.29.0", {"position": v(419.1, -112.18) * mm});
            skPoint(sketch, "E38.78.30.0", {"position": v(419.1, -118.53) * mm});
            skPoint(sketch, "E38.78.31.0", {"position": v(419.1, -124.88) * mm});
            skPoint(sketch, "E38.78.32.0", {"position": v(419.1, -131.23) * mm});
            skPoint(sketch, "E38.78.33.0", {"position": v(419.1, -137.58) * mm});
            skPoint(sketch, "E38.78.34.0", {"position": v(419.1, -143.93) * mm});
            skPoint(sketch, "E38.78.35.0", {"position": v(419.1, -150.28) * mm});
            skPoint(sketch, "E38.78.36.0", {"position": v(419.1, -156.63) * mm});
            skPoint(sketch, "E38.78.37.0", {"position": v(419.1, -162.98) * mm});
            skPoint(sketch, "E38.78.38.0", {"position": v(419.1, -169.33) * mm});
            skPoint(sketch, "E38.78.39.0", {"position": v(419.1, -175.68) * mm});
            skPoint(sketch, "E38.78.40.0", {"position": v(419.1, -182.03) * mm});
            skPoint(sketch, "E38.78.41.0", {"position": v(419.1, -188.38) * mm});
            skPoint(sketch, "E38.78.42.0", {"position": v(419.1, -194.73) * mm});
            skPoint(sketch, "E38.78.43.0", {"position": v(419.1, -201.08) * mm});
            skPoint(sketch, "E38.78.44.0", {"position": v(419.1, -207.43) * mm});
            skPoint(sketch, "E38.78.45.0", {"position": v(419.1, -213.78) * mm});
            skPoint(sketch, "E38.78.46.0", {"position": v(419.1, -220.13) * mm});
            skPoint(sketch, "E38.78.47.0", {"position": v(419.1, -226.48) * mm});
            skPoint(sketch, "E38.78.48.0", {"position": v(419.1, -232.83) * mm});
            skPoint(sketch, "E38.78.49.0", {"position": v(419.1, -239.18) * mm});
            skPoint(sketch, "E38.78.50.0", {"position": v(419.1, -245.53) * mm});
            skPoint(sketch, "E38.78.51.0", {"position": v(419.1, -251.88) * mm});
            skPoint(sketch, "E38.78.52.0", {"position": v(419.1, -258.23) * mm});
            skPoint(sketch, "E38.78.53.0", {"position": v(419.1, -264.58) * mm});
            skPoint(sketch, "E38.78.54.0", {"position": v(419.1, -270.93) * mm});
            skPoint(sketch, "E38.78.55.0", {"position": v(419.1, -277.28) * mm});
            skPoint(sketch, "E38.78.56.0", {"position": v(419.1, -283.63) * mm});
            skPoint(sketch, "E38.78.57.0", {"position": v(419.1, -289.98) * mm});
            skPoint(sketch, "E38.78.58.0", {"position": v(419.1, -296.33) * mm});
            skPoint(sketch, "E38.78.59.0", {"position": v(419.1, -302.68) * mm});
            skPoint(sketch, "E38.78.60.0", {"position": v(419.1, -309.03) * mm});
            skPoint(sketch, "E38.78.61.0", {"position": v(419.1, -315.38) * mm});
            skPoint(sketch, "E38.78.62.0", {"position": v(419.1, -321.73) * mm});
            skPoint(sketch, "E38.78.63.0", {"position": v(419.1, -328.08) * mm});
            skPoint(sketch, "E38.78.64.0", {"position": v(419.1, -334.43) * mm});
            skPoint(sketch, "E38.78.65.0", {"position": v(419.1, -340.78) * mm});
            skPoint(sketch, "E38.78.66.0", {"position": v(419.1, -347.13) * mm});
            skPoint(sketch, "E38.78.67.0", {"position": v(419.1, -353.48) * mm});
            skPoint(sketch, "E38.78.68.0", {"position": v(419.1, -359.83) * mm});
            skPoint(sketch, "E38.78.69.0", {"position": v(419.1, -366.18) * mm});
            skPoint(sketch, "E38.78.70.0", {"position": v(419.1, -372.53) * mm});
            skPoint(sketch, "E38.78.71.0", {"position": v(419.1, -378.88) * mm});
            skPoint(sketch, "E38.78.72.0", {"position": v(419.1, -385.23) * mm});
            skPoint(sketch, "E38.78.73.0", {"position": v(419.1, -391.58) * mm});
            skPoint(sketch, "E38.78.74.0", {"position": v(419.1, -397.93) * mm});
            skPoint(sketch, "E38.78.75.0", {"position": v(419.1, -404.28) * mm});
            skPoint(sketch, "E38.78.76.0", {"position": v(419.1, -410.63) * mm});
            skPoint(sketch, "E38.78.77.0", {"position": v(419.1, -416.98) * mm});
            skPoint(sketch, "E38.78.78.0", {"position": v(419.1, -423.33) * mm});
            skPoint(sketch, "E38.78.79.0", {"position": v(419.1, -429.68) * mm});
            skPoint(sketch, "E38.78.80.0", {"position": v(419.1, -436.03) * mm});
            skPoint(sketch, "E38.78.81.0", {"position": v(419.1, -442.38) * mm});
            skPoint(sketch, "E38.78.82.0", {"position": v(419.1, -448.73) * mm});
            skPoint(sketch, "E38.78.83.0", {"position": v(419.1, -455.08) * mm});
            skPoint(sketch, "E38.78.84.0", {"position": v(419.1, -461.43) * mm});
            skPoint(sketch, "E38.78.85.0", {"position": v(419.1, -467.78) * mm});
            skPoint(sketch, "E38.78.86.0", {"position": v(419.1, -474.13) * mm});
            skPoint(sketch, "E38.78.87.0", {"position": v(419.1, -480.48) * mm});
            skPoint(sketch, "E38.78.88.0", {"position": v(419.1, -486.83) * mm});
            skPoint(sketch, "E38.78.89.0", {"position": v(419.1, -493.18) * mm});
            skPoint(sketch, "E38.78.90.0", {"position": v(419.1, -499.53) * mm});
            skPoint(sketch, "E38.78.91.0", {"position": v(419.1, -505.88) * mm});
            skPoint(sketch, "E38.78.92.0", {"position": v(419.1, -512.23) * mm});
            skPoint(sketch, "E38.78.93.0", {"position": v(419.1, -518.58) * mm});
            skPoint(sketch, "E38.78.94.0", {"position": v(419.1, -524.93) * mm});
            skPoint(sketch, "E38.78.95.0", {"position": v(419.1, -531.28) * mm});
            skPoint(sketch, "E38.78.96.0", {"position": v(419.1, -537.63) * mm});
            skPoint(sketch, "E38.78.97.0", {"position": v(419.1, -543.98) * mm});
            skPoint(sketch, "E38.78.98.0", {"position": v(419.1, -550.33) * mm});
            skPoint(sketch, "E38.78.99.0", {"position": v(419.1, -556.68) * mm});
            skPoint(sketch, "E38.79.0.0", {"position": v(425.45, 71.97) * mm});
            skPoint(sketch, "E38.79.1.0", {"position": v(425.45, 65.62) * mm});
            skPoint(sketch, "E38.79.2.0", {"position": v(425.45, 59.27) * mm});
            skPoint(sketch, "E38.79.3.0", {"position": v(425.45, 52.92) * mm});
            skPoint(sketch, "E38.79.4.0", {"position": v(425.45, 46.57) * mm});
            skPoint(sketch, "E38.79.5.0", {"position": v(425.45, 40.22) * mm});
            skPoint(sketch, "E38.79.6.0", {"position": v(425.45, 33.87) * mm});
            skPoint(sketch, "E38.79.7.0", {"position": v(425.45, 27.52) * mm});
            skPoint(sketch, "E38.79.8.0", {"position": v(425.45, 21.17) * mm});
            skPoint(sketch, "E38.79.9.0", {"position": v(425.45, 14.82) * mm});
            skPoint(sketch, "E38.79.10.0", {"position": v(425.45, 8.47) * mm});
            skPoint(sketch, "E38.79.11.0", {"position": v(425.45, 2.12) * mm});
            skPoint(sketch, "E38.79.12.0", {"position": v(425.45, -4.23) * mm});
            skPoint(sketch, "E38.79.13.0", {"position": v(425.45, -10.58) * mm});
            skPoint(sketch, "E38.79.14.0", {"position": v(425.45, -16.93) * mm});
            skPoint(sketch, "E38.79.15.0", {"position": v(425.45, -23.28) * mm});
            skPoint(sketch, "E38.79.16.0", {"position": v(425.45, -29.63) * mm});
            skPoint(sketch, "E38.79.17.0", {"position": v(425.45, -35.98) * mm});
            skPoint(sketch, "E38.79.18.0", {"position": v(425.45, -42.33) * mm});
            skPoint(sketch, "E38.79.19.0", {"position": v(425.45, -48.68) * mm});
            skPoint(sketch, "E38.79.20.0", {"position": v(425.45, -55.03) * mm});
            skPoint(sketch, "E38.79.21.0", {"position": v(425.45, -61.38) * mm});
            skPoint(sketch, "E38.79.22.0", {"position": v(425.45, -67.73) * mm});
            skPoint(sketch, "E38.79.23.0", {"position": v(425.45, -74.08) * mm});
            skPoint(sketch, "E38.79.24.0", {"position": v(425.45, -80.43) * mm});
            skPoint(sketch, "E38.79.25.0", {"position": v(425.45, -86.78) * mm});
            skPoint(sketch, "E38.79.26.0", {"position": v(425.45, -93.13) * mm});
            skPoint(sketch, "E38.79.27.0", {"position": v(425.45, -99.48) * mm});
            skPoint(sketch, "E38.79.28.0", {"position": v(425.45, -105.83) * mm});
            skPoint(sketch, "E38.79.29.0", {"position": v(425.45, -112.18) * mm});
            skPoint(sketch, "E38.79.30.0", {"position": v(425.45, -118.53) * mm});
            skPoint(sketch, "E38.79.31.0", {"position": v(425.45, -124.88) * mm});
            skPoint(sketch, "E38.79.32.0", {"position": v(425.45, -131.23) * mm});
            skPoint(sketch, "E38.79.33.0", {"position": v(425.45, -137.58) * mm});
            skPoint(sketch, "E38.79.34.0", {"position": v(425.45, -143.93) * mm});
            skPoint(sketch, "E38.79.35.0", {"position": v(425.45, -150.28) * mm});
            skPoint(sketch, "E38.79.36.0", {"position": v(425.45, -156.63) * mm});
            skPoint(sketch, "E38.79.37.0", {"position": v(425.45, -162.98) * mm});
            skPoint(sketch, "E38.79.38.0", {"position": v(425.45, -169.33) * mm});
            skPoint(sketch, "E38.79.39.0", {"position": v(425.45, -175.68) * mm});
            skPoint(sketch, "E38.79.40.0", {"position": v(425.45, -182.03) * mm});
            skPoint(sketch, "E38.79.41.0", {"position": v(425.45, -188.38) * mm});
            skPoint(sketch, "E38.79.42.0", {"position": v(425.45, -194.73) * mm});
            skPoint(sketch, "E38.79.43.0", {"position": v(425.45, -201.08) * mm});
            skPoint(sketch, "E38.79.44.0", {"position": v(425.45, -207.43) * mm});
            skPoint(sketch, "E38.79.45.0", {"position": v(425.45, -213.78) * mm});
            skPoint(sketch, "E38.79.46.0", {"position": v(425.45, -220.13) * mm});
            skPoint(sketch, "E38.79.47.0", {"position": v(425.45, -226.48) * mm});
            skPoint(sketch, "E38.79.48.0", {"position": v(425.45, -232.83) * mm});
            skPoint(sketch, "E38.79.49.0", {"position": v(425.45, -239.18) * mm});
            skPoint(sketch, "E38.79.50.0", {"position": v(425.45, -245.53) * mm});
            skPoint(sketch, "E38.79.51.0", {"position": v(425.45, -251.88) * mm});
            skPoint(sketch, "E38.79.52.0", {"position": v(425.45, -258.23) * mm});
            skPoint(sketch, "E38.79.53.0", {"position": v(425.45, -264.58) * mm});
            skPoint(sketch, "E38.79.54.0", {"position": v(425.45, -270.93) * mm});
            skPoint(sketch, "E38.79.55.0", {"position": v(425.45, -277.28) * mm});
            skPoint(sketch, "E38.79.56.0", {"position": v(425.45, -283.63) * mm});
            skPoint(sketch, "E38.79.57.0", {"position": v(425.45, -289.98) * mm});
            skPoint(sketch, "E38.79.58.0", {"position": v(425.45, -296.33) * mm});
            skPoint(sketch, "E38.79.59.0", {"position": v(425.45, -302.68) * mm});
            skPoint(sketch, "E38.79.60.0", {"position": v(425.45, -309.03) * mm});
            skPoint(sketch, "E38.79.61.0", {"position": v(425.45, -315.38) * mm});
            skPoint(sketch, "E38.79.62.0", {"position": v(425.45, -321.73) * mm});
            skPoint(sketch, "E38.79.63.0", {"position": v(425.45, -328.08) * mm});
            skPoint(sketch, "E38.79.64.0", {"position": v(425.45, -334.43) * mm});
            skPoint(sketch, "E38.79.65.0", {"position": v(425.45, -340.78) * mm});
            skPoint(sketch, "E38.79.66.0", {"position": v(425.45, -347.13) * mm});
            skPoint(sketch, "E38.79.67.0", {"position": v(425.45, -353.48) * mm});
            skPoint(sketch, "E38.79.68.0", {"position": v(425.45, -359.83) * mm});
            skPoint(sketch, "E38.79.69.0", {"position": v(425.45, -366.18) * mm});
            skPoint(sketch, "E38.79.70.0", {"position": v(425.45, -372.53) * mm});
            skPoint(sketch, "E38.79.71.0", {"position": v(425.45, -378.88) * mm});
            skPoint(sketch, "E38.79.72.0", {"position": v(425.45, -385.23) * mm});
            skPoint(sketch, "E38.79.73.0", {"position": v(425.45, -391.58) * mm});
            skPoint(sketch, "E38.79.74.0", {"position": v(425.45, -397.93) * mm});
            skPoint(sketch, "E38.79.75.0", {"position": v(425.45, -404.28) * mm});
            skPoint(sketch, "E38.79.76.0", {"position": v(425.45, -410.63) * mm});
            skPoint(sketch, "E38.79.77.0", {"position": v(425.45, -416.98) * mm});
            skPoint(sketch, "E38.79.78.0", {"position": v(425.45, -423.33) * mm});
            skPoint(sketch, "E38.79.79.0", {"position": v(425.45, -429.68) * mm});
            skPoint(sketch, "E38.79.80.0", {"position": v(425.45, -436.03) * mm});
            skPoint(sketch, "E38.79.81.0", {"position": v(425.45, -442.38) * mm});
            skPoint(sketch, "E38.79.82.0", {"position": v(425.45, -448.73) * mm});
            skPoint(sketch, "E38.79.83.0", {"position": v(425.45, -455.08) * mm});
            skPoint(sketch, "E38.79.84.0", {"position": v(425.45, -461.43) * mm});
            skPoint(sketch, "E38.79.85.0", {"position": v(425.45, -467.78) * mm});
            skPoint(sketch, "E38.79.86.0", {"position": v(425.45, -474.13) * mm});
            skPoint(sketch, "E38.79.87.0", {"position": v(425.45, -480.48) * mm});
            skPoint(sketch, "E38.79.88.0", {"position": v(425.45, -486.83) * mm});
            skPoint(sketch, "E38.79.89.0", {"position": v(425.45, -493.18) * mm});
            skPoint(sketch, "E38.79.90.0", {"position": v(425.45, -499.53) * mm});
            skPoint(sketch, "E38.79.91.0", {"position": v(425.45, -505.88) * mm});
            skPoint(sketch, "E38.79.92.0", {"position": v(425.45, -512.23) * mm});
            skPoint(sketch, "E38.79.93.0", {"position": v(425.45, -518.58) * mm});
            skPoint(sketch, "E38.79.94.0", {"position": v(425.45, -524.93) * mm});
            skPoint(sketch, "E38.79.95.0", {"position": v(425.45, -531.28) * mm});
            skPoint(sketch, "E38.79.96.0", {"position": v(425.45, -537.63) * mm});
            skPoint(sketch, "E38.79.97.0", {"position": v(425.45, -543.98) * mm});
            skPoint(sketch, "E38.79.98.0", {"position": v(425.45, -550.33) * mm});
            skPoint(sketch, "E38.79.99.0", {"position": v(425.45, -556.68) * mm});
            skPoint(sketch, "E38.80.0.0", {"position": v(431.8, 71.97) * mm});
            skPoint(sketch, "E38.80.1.0", {"position": v(431.8, 65.62) * mm});
            skPoint(sketch, "E38.80.2.0", {"position": v(431.8, 59.27) * mm});
            skPoint(sketch, "E38.80.3.0", {"position": v(431.8, 52.92) * mm});
            skPoint(sketch, "E38.80.4.0", {"position": v(431.8, 46.57) * mm});
            skPoint(sketch, "E38.80.5.0", {"position": v(431.8, 40.22) * mm});
            skPoint(sketch, "E38.80.6.0", {"position": v(431.8, 33.87) * mm});
            skPoint(sketch, "E38.80.7.0", {"position": v(431.8, 27.52) * mm});
            skPoint(sketch, "E38.80.8.0", {"position": v(431.8, 21.17) * mm});
            skPoint(sketch, "E38.80.9.0", {"position": v(431.8, 14.82) * mm});
            skPoint(sketch, "E38.80.10.0", {"position": v(431.8, 8.47) * mm});
            skPoint(sketch, "E38.80.11.0", {"position": v(431.8, 2.12) * mm});
            skPoint(sketch, "E38.80.12.0", {"position": v(431.8, -4.23) * mm});
            skPoint(sketch, "E38.80.13.0", {"position": v(431.8, -10.58) * mm});
            skPoint(sketch, "E38.80.14.0", {"position": v(431.8, -16.93) * mm});
            skPoint(sketch, "E38.80.15.0", {"position": v(431.8, -23.28) * mm});
            skPoint(sketch, "E38.80.16.0", {"position": v(431.8, -29.63) * mm});
            skPoint(sketch, "E38.80.17.0", {"position": v(431.8, -35.98) * mm});
            skPoint(sketch, "E38.80.18.0", {"position": v(431.8, -42.33) * mm});
            skPoint(sketch, "E38.80.19.0", {"position": v(431.8, -48.68) * mm});
            skPoint(sketch, "E38.80.20.0", {"position": v(431.8, -55.03) * mm});
            skPoint(sketch, "E38.80.21.0", {"position": v(431.8, -61.38) * mm});
            skPoint(sketch, "E38.80.22.0", {"position": v(431.8, -67.73) * mm});
            skPoint(sketch, "E38.80.23.0", {"position": v(431.8, -74.08) * mm});
            skPoint(sketch, "E38.80.24.0", {"position": v(431.8, -80.43) * mm});
            skPoint(sketch, "E38.80.25.0", {"position": v(431.8, -86.78) * mm});
            skPoint(sketch, "E38.80.26.0", {"position": v(431.8, -93.13) * mm});
            skPoint(sketch, "E38.80.27.0", {"position": v(431.8, -99.48) * mm});
            skPoint(sketch, "E38.80.28.0", {"position": v(431.8, -105.83) * mm});
            skPoint(sketch, "E38.80.29.0", {"position": v(431.8, -112.18) * mm});
            skPoint(sketch, "E38.80.30.0", {"position": v(431.8, -118.53) * mm});
            skPoint(sketch, "E38.80.31.0", {"position": v(431.8, -124.88) * mm});
            skPoint(sketch, "E38.80.32.0", {"position": v(431.8, -131.23) * mm});
            skPoint(sketch, "E38.80.33.0", {"position": v(431.8, -137.58) * mm});
            skPoint(sketch, "E38.80.34.0", {"position": v(431.8, -143.93) * mm});
            skPoint(sketch, "E38.80.35.0", {"position": v(431.8, -150.28) * mm});
            skPoint(sketch, "E38.80.36.0", {"position": v(431.8, -156.63) * mm});
            skPoint(sketch, "E38.80.37.0", {"position": v(431.8, -162.98) * mm});
            skPoint(sketch, "E38.80.38.0", {"position": v(431.8, -169.33) * mm});
            skPoint(sketch, "E38.80.39.0", {"position": v(431.8, -175.68) * mm});
            skPoint(sketch, "E38.80.40.0", {"position": v(431.8, -182.03) * mm});
            skPoint(sketch, "E38.80.41.0", {"position": v(431.8, -188.38) * mm});
            skPoint(sketch, "E38.80.42.0", {"position": v(431.8, -194.73) * mm});
            skPoint(sketch, "E38.80.43.0", {"position": v(431.8, -201.08) * mm});
            skPoint(sketch, "E38.80.44.0", {"position": v(431.8, -207.43) * mm});
            skPoint(sketch, "E38.80.45.0", {"position": v(431.8, -213.78) * mm});
            skPoint(sketch, "E38.80.46.0", {"position": v(431.8, -220.13) * mm});
            skPoint(sketch, "E38.80.47.0", {"position": v(431.8, -226.48) * mm});
            skPoint(sketch, "E38.80.48.0", {"position": v(431.8, -232.83) * mm});
            skPoint(sketch, "E38.80.49.0", {"position": v(431.8, -239.18) * mm});
            skPoint(sketch, "E38.80.50.0", {"position": v(431.8, -245.53) * mm});
            skPoint(sketch, "E38.80.51.0", {"position": v(431.8, -251.88) * mm});
            skPoint(sketch, "E38.80.52.0", {"position": v(431.8, -258.23) * mm});
            skPoint(sketch, "E38.80.53.0", {"position": v(431.8, -264.58) * mm});
            skPoint(sketch, "E38.80.54.0", {"position": v(431.8, -270.93) * mm});
            skPoint(sketch, "E38.80.55.0", {"position": v(431.8, -277.28) * mm});
            skPoint(sketch, "E38.80.56.0", {"position": v(431.8, -283.63) * mm});
            skPoint(sketch, "E38.80.57.0", {"position": v(431.8, -289.98) * mm});
            skPoint(sketch, "E38.80.58.0", {"position": v(431.8, -296.33) * mm});
            skPoint(sketch, "E38.80.59.0", {"position": v(431.8, -302.68) * mm});
            skPoint(sketch, "E38.80.60.0", {"position": v(431.8, -309.03) * mm});
            skPoint(sketch, "E38.80.61.0", {"position": v(431.8, -315.38) * mm});
            skPoint(sketch, "E38.80.62.0", {"position": v(431.8, -321.73) * mm});
            skPoint(sketch, "E38.80.63.0", {"position": v(431.8, -328.08) * mm});
            skPoint(sketch, "E38.80.64.0", {"position": v(431.8, -334.43) * mm});
            skPoint(sketch, "E38.80.65.0", {"position": v(431.8, -340.78) * mm});
            skPoint(sketch, "E38.80.66.0", {"position": v(431.8, -347.13) * mm});
            skPoint(sketch, "E38.80.67.0", {"position": v(431.8, -353.48) * mm});
            skPoint(sketch, "E38.80.68.0", {"position": v(431.8, -359.83) * mm});
            skPoint(sketch, "E38.80.69.0", {"position": v(431.8, -366.18) * mm});
            skPoint(sketch, "E38.80.70.0", {"position": v(431.8, -372.53) * mm});
            skPoint(sketch, "E38.80.71.0", {"position": v(431.8, -378.88) * mm});
            skPoint(sketch, "E38.80.72.0", {"position": v(431.8, -385.23) * mm});
            skPoint(sketch, "E38.80.73.0", {"position": v(431.8, -391.58) * mm});
            skPoint(sketch, "E38.80.74.0", {"position": v(431.8, -397.93) * mm});
            skPoint(sketch, "E38.80.75.0", {"position": v(431.8, -404.28) * mm});
            skPoint(sketch, "E38.80.76.0", {"position": v(431.8, -410.63) * mm});
            skPoint(sketch, "E38.80.77.0", {"position": v(431.8, -416.98) * mm});
            skPoint(sketch, "E38.80.78.0", {"position": v(431.8, -423.33) * mm});
            skPoint(sketch, "E38.80.79.0", {"position": v(431.8, -429.68) * mm});
            skPoint(sketch, "E38.80.80.0", {"position": v(431.8, -436.03) * mm});
            skPoint(sketch, "E38.80.81.0", {"position": v(431.8, -442.38) * mm});
            skPoint(sketch, "E38.80.82.0", {"position": v(431.8, -448.73) * mm});
            skPoint(sketch, "E38.80.83.0", {"position": v(431.8, -455.08) * mm});
            skPoint(sketch, "E38.80.84.0", {"position": v(431.8, -461.43) * mm});
            skPoint(sketch, "E38.80.85.0", {"position": v(431.8, -467.78) * mm});
            skPoint(sketch, "E38.80.86.0", {"position": v(431.8, -474.13) * mm});
            skPoint(sketch, "E38.80.87.0", {"position": v(431.8, -480.48) * mm});
            skPoint(sketch, "E38.80.88.0", {"position": v(431.8, -486.83) * mm});
            skPoint(sketch, "E38.80.89.0", {"position": v(431.8, -493.18) * mm});
            skPoint(sketch, "E38.80.90.0", {"position": v(431.8, -499.53) * mm});
            skPoint(sketch, "E38.80.91.0", {"position": v(431.8, -505.88) * mm});
            skPoint(sketch, "E38.80.92.0", {"position": v(431.8, -512.23) * mm});
            skPoint(sketch, "E38.80.93.0", {"position": v(431.8, -518.58) * mm});
            skPoint(sketch, "E38.80.94.0", {"position": v(431.8, -524.93) * mm});
            skPoint(sketch, "E38.80.95.0", {"position": v(431.8, -531.28) * mm});
            skPoint(sketch, "E38.80.96.0", {"position": v(431.8, -537.63) * mm});
            skPoint(sketch, "E38.80.97.0", {"position": v(431.8, -543.98) * mm});
            skPoint(sketch, "E38.80.98.0", {"position": v(431.8, -550.33) * mm});
            skPoint(sketch, "E38.80.99.0", {"position": v(431.8, -556.68) * mm});
            skPoint(sketch, "E38.81.0.0", {"position": v(438.15, 71.97) * mm});
            skPoint(sketch, "E38.81.1.0", {"position": v(438.15, 65.62) * mm});
            skPoint(sketch, "E38.81.2.0", {"position": v(438.15, 59.27) * mm});
            skPoint(sketch, "E38.81.3.0", {"position": v(438.15, 52.92) * mm});
            skPoint(sketch, "E38.81.4.0", {"position": v(438.15, 46.57) * mm});
            skPoint(sketch, "E38.81.5.0", {"position": v(438.15, 40.22) * mm});
            skPoint(sketch, "E38.81.6.0", {"position": v(438.15, 33.87) * mm});
            skPoint(sketch, "E38.81.7.0", {"position": v(438.15, 27.52) * mm});
            skPoint(sketch, "E38.81.8.0", {"position": v(438.15, 21.17) * mm});
            skPoint(sketch, "E38.81.9.0", {"position": v(438.15, 14.82) * mm});
            skPoint(sketch, "E38.81.10.0", {"position": v(438.15, 8.47) * mm});
            skPoint(sketch, "E38.81.11.0", {"position": v(438.15, 2.12) * mm});
            skPoint(sketch, "E38.81.12.0", {"position": v(438.15, -4.23) * mm});
            skPoint(sketch, "E38.81.13.0", {"position": v(438.15, -10.58) * mm});
            skPoint(sketch, "E38.81.14.0", {"position": v(438.15, -16.93) * mm});
            skPoint(sketch, "E38.81.15.0", {"position": v(438.15, -23.28) * mm});
            skPoint(sketch, "E38.81.16.0", {"position": v(438.15, -29.63) * mm});
            skPoint(sketch, "E38.81.17.0", {"position": v(438.15, -35.98) * mm});
            skPoint(sketch, "E38.81.18.0", {"position": v(438.15, -42.33) * mm});
            skPoint(sketch, "E38.81.19.0", {"position": v(438.15, -48.68) * mm});
            skPoint(sketch, "E38.81.20.0", {"position": v(438.15, -55.03) * mm});
            skPoint(sketch, "E38.81.21.0", {"position": v(438.15, -61.38) * mm});
            skPoint(sketch, "E38.81.22.0", {"position": v(438.15, -67.73) * mm});
            skPoint(sketch, "E38.81.23.0", {"position": v(438.15, -74.08) * mm});
            skPoint(sketch, "E38.81.24.0", {"position": v(438.15, -80.43) * mm});
            skPoint(sketch, "E38.81.25.0", {"position": v(438.15, -86.78) * mm});
            skPoint(sketch, "E38.81.26.0", {"position": v(438.15, -93.13) * mm});
            skPoint(sketch, "E38.81.27.0", {"position": v(438.15, -99.48) * mm});
            skPoint(sketch, "E38.81.28.0", {"position": v(438.15, -105.83) * mm});
            skPoint(sketch, "E38.81.29.0", {"position": v(438.15, -112.18) * mm});
            skPoint(sketch, "E38.81.30.0", {"position": v(438.15, -118.53) * mm});
            skPoint(sketch, "E38.81.31.0", {"position": v(438.15, -124.88) * mm});
            skPoint(sketch, "E38.81.32.0", {"position": v(438.15, -131.23) * mm});
            skPoint(sketch, "E38.81.33.0", {"position": v(438.15, -137.58) * mm});
            skPoint(sketch, "E38.81.34.0", {"position": v(438.15, -143.93) * mm});
            skPoint(sketch, "E38.81.35.0", {"position": v(438.15, -150.28) * mm});
            skPoint(sketch, "E38.81.36.0", {"position": v(438.15, -156.63) * mm});
            skPoint(sketch, "E38.81.37.0", {"position": v(438.15, -162.98) * mm});
            skPoint(sketch, "E38.81.38.0", {"position": v(438.15, -169.33) * mm});
            skPoint(sketch, "E38.81.39.0", {"position": v(438.15, -175.68) * mm});
            skPoint(sketch, "E38.81.40.0", {"position": v(438.15, -182.03) * mm});
            skPoint(sketch, "E38.81.41.0", {"position": v(438.15, -188.38) * mm});
            skPoint(sketch, "E38.81.42.0", {"position": v(438.15, -194.73) * mm});
            skPoint(sketch, "E38.81.43.0", {"position": v(438.15, -201.08) * mm});
            skPoint(sketch, "E38.81.44.0", {"position": v(438.15, -207.43) * mm});
            skPoint(sketch, "E38.81.45.0", {"position": v(438.15, -213.78) * mm});
            skPoint(sketch, "E38.81.46.0", {"position": v(438.15, -220.13) * mm});
            skPoint(sketch, "E38.81.47.0", {"position": v(438.15, -226.48) * mm});
            skPoint(sketch, "E38.81.48.0", {"position": v(438.15, -232.83) * mm});
            skPoint(sketch, "E38.81.49.0", {"position": v(438.15, -239.18) * mm});
            skPoint(sketch, "E38.81.50.0", {"position": v(438.15, -245.53) * mm});
            skPoint(sketch, "E38.81.51.0", {"position": v(438.15, -251.88) * mm});
            skPoint(sketch, "E38.81.52.0", {"position": v(438.15, -258.23) * mm});
            skPoint(sketch, "E38.81.53.0", {"position": v(438.15, -264.58) * mm});
            skPoint(sketch, "E38.81.54.0", {"position": v(438.15, -270.93) * mm});
            skPoint(sketch, "E38.81.55.0", {"position": v(438.15, -277.28) * mm});
            skPoint(sketch, "E38.81.56.0", {"position": v(438.15, -283.63) * mm});
            skPoint(sketch, "E38.81.57.0", {"position": v(438.15, -289.98) * mm});
            skPoint(sketch, "E38.81.58.0", {"position": v(438.15, -296.33) * mm});
            skPoint(sketch, "E38.81.59.0", {"position": v(438.15, -302.68) * mm});
            skPoint(sketch, "E38.81.60.0", {"position": v(438.15, -309.03) * mm});
            skPoint(sketch, "E38.81.61.0", {"position": v(438.15, -315.38) * mm});
            skPoint(sketch, "E38.81.62.0", {"position": v(438.15, -321.73) * mm});
            skPoint(sketch, "E38.81.63.0", {"position": v(438.15, -328.08) * mm});
            skPoint(sketch, "E38.81.64.0", {"position": v(438.15, -334.43) * mm});
            skPoint(sketch, "E38.81.65.0", {"position": v(438.15, -340.78) * mm});
            skPoint(sketch, "E38.81.66.0", {"position": v(438.15, -347.13) * mm});
            skPoint(sketch, "E38.81.67.0", {"position": v(438.15, -353.48) * mm});
            skPoint(sketch, "E38.81.68.0", {"position": v(438.15, -359.83) * mm});
            skPoint(sketch, "E38.81.69.0", {"position": v(438.15, -366.18) * mm});
            skPoint(sketch, "E38.81.70.0", {"position": v(438.15, -372.53) * mm});
            skPoint(sketch, "E38.81.71.0", {"position": v(438.15, -378.88) * mm});
            skPoint(sketch, "E38.81.72.0", {"position": v(438.15, -385.23) * mm});
            skPoint(sketch, "E38.81.73.0", {"position": v(438.15, -391.58) * mm});
            skPoint(sketch, "E38.81.74.0", {"position": v(438.15, -397.93) * mm});
            skPoint(sketch, "E38.81.75.0", {"position": v(438.15, -404.28) * mm});
            skPoint(sketch, "E38.81.76.0", {"position": v(438.15, -410.63) * mm});
            skPoint(sketch, "E38.81.77.0", {"position": v(438.15, -416.98) * mm});
            skPoint(sketch, "E38.81.78.0", {"position": v(438.15, -423.33) * mm});
            skPoint(sketch, "E38.81.79.0", {"position": v(438.15, -429.68) * mm});
            skPoint(sketch, "E38.81.80.0", {"position": v(438.15, -436.03) * mm});
            skPoint(sketch, "E38.81.81.0", {"position": v(438.15, -442.38) * mm});
            skPoint(sketch, "E38.81.82.0", {"position": v(438.15, -448.73) * mm});
            skPoint(sketch, "E38.81.83.0", {"position": v(438.15, -455.08) * mm});
            skPoint(sketch, "E38.81.84.0", {"position": v(438.15, -461.43) * mm});
            skPoint(sketch, "E38.81.85.0", {"position": v(438.15, -467.78) * mm});
            skPoint(sketch, "E38.81.86.0", {"position": v(438.15, -474.13) * mm});
            skPoint(sketch, "E38.81.87.0", {"position": v(438.15, -480.48) * mm});
            skPoint(sketch, "E38.81.88.0", {"position": v(438.15, -486.83) * mm});
            skPoint(sketch, "E38.81.89.0", {"position": v(438.15, -493.18) * mm});
            skPoint(sketch, "E38.81.90.0", {"position": v(438.15, -499.53) * mm});
            skPoint(sketch, "E38.81.91.0", {"position": v(438.15, -505.88) * mm});
            skPoint(sketch, "E38.81.92.0", {"position": v(438.15, -512.23) * mm});
            skPoint(sketch, "E38.81.93.0", {"position": v(438.15, -518.58) * mm});
            skPoint(sketch, "E38.81.94.0", {"position": v(438.15, -524.93) * mm});
            skPoint(sketch, "E38.81.95.0", {"position": v(438.15, -531.28) * mm});
            skPoint(sketch, "E38.81.96.0", {"position": v(438.15, -537.63) * mm});
            skPoint(sketch, "E38.81.97.0", {"position": v(438.15, -543.98) * mm});
            skPoint(sketch, "E38.81.98.0", {"position": v(438.15, -550.33) * mm});
            skPoint(sketch, "E38.81.99.0", {"position": v(438.15, -556.68) * mm});
            skPoint(sketch, "E38.82.0.0", {"position": v(444.5, 71.97) * mm});
            skPoint(sketch, "E38.82.1.0", {"position": v(444.5, 65.62) * mm});
            skPoint(sketch, "E38.82.2.0", {"position": v(444.5, 59.27) * mm});
            skPoint(sketch, "E38.82.3.0", {"position": v(444.5, 52.92) * mm});
            skPoint(sketch, "E38.82.4.0", {"position": v(444.5, 46.57) * mm});
            skPoint(sketch, "E38.82.5.0", {"position": v(444.5, 40.22) * mm});
            skPoint(sketch, "E38.82.6.0", {"position": v(444.5, 33.87) * mm});
            skPoint(sketch, "E38.82.7.0", {"position": v(444.5, 27.52) * mm});
            skPoint(sketch, "E38.82.8.0", {"position": v(444.5, 21.17) * mm});
            skPoint(sketch, "E38.82.9.0", {"position": v(444.5, 14.82) * mm});
            skPoint(sketch, "E38.82.10.0", {"position": v(444.5, 8.47) * mm});
            skPoint(sketch, "E38.82.11.0", {"position": v(444.5, 2.12) * mm});
            skPoint(sketch, "E38.82.12.0", {"position": v(444.5, -4.23) * mm});
            skPoint(sketch, "E38.82.13.0", {"position": v(444.5, -10.58) * mm});
            skPoint(sketch, "E38.82.14.0", {"position": v(444.5, -16.93) * mm});
            skPoint(sketch, "E38.82.15.0", {"position": v(444.5, -23.28) * mm});
            skPoint(sketch, "E38.82.16.0", {"position": v(444.5, -29.63) * mm});
            skPoint(sketch, "E38.82.17.0", {"position": v(444.5, -35.98) * mm});
            skPoint(sketch, "E38.82.18.0", {"position": v(444.5, -42.33) * mm});
            skPoint(sketch, "E38.82.19.0", {"position": v(444.5, -48.68) * mm});
            skPoint(sketch, "E38.82.20.0", {"position": v(444.5, -55.03) * mm});
            skPoint(sketch, "E38.82.21.0", {"position": v(444.5, -61.38) * mm});
            skPoint(sketch, "E38.82.22.0", {"position": v(444.5, -67.73) * mm});
            skPoint(sketch, "E38.82.23.0", {"position": v(444.5, -74.08) * mm});
            skPoint(sketch, "E38.82.24.0", {"position": v(444.5, -80.43) * mm});
            skPoint(sketch, "E38.82.25.0", {"position": v(444.5, -86.78) * mm});
            skPoint(sketch, "E38.82.26.0", {"position": v(444.5, -93.13) * mm});
            skPoint(sketch, "E38.82.27.0", {"position": v(444.5, -99.48) * mm});
            skPoint(sketch, "E38.82.28.0", {"position": v(444.5, -105.83) * mm});
            skPoint(sketch, "E38.82.29.0", {"position": v(444.5, -112.18) * mm});
            skPoint(sketch, "E38.82.30.0", {"position": v(444.5, -118.53) * mm});
            skPoint(sketch, "E38.82.31.0", {"position": v(444.5, -124.88) * mm});
            skPoint(sketch, "E38.82.32.0", {"position": v(444.5, -131.23) * mm});
            skPoint(sketch, "E38.82.33.0", {"position": v(444.5, -137.58) * mm});
            skPoint(sketch, "E38.82.34.0", {"position": v(444.5, -143.93) * mm});
            skPoint(sketch, "E38.82.35.0", {"position": v(444.5, -150.28) * mm});
            skPoint(sketch, "E38.82.36.0", {"position": v(444.5, -156.63) * mm});
            skPoint(sketch, "E38.82.37.0", {"position": v(444.5, -162.98) * mm});
            skPoint(sketch, "E38.82.38.0", {"position": v(444.5, -169.33) * mm});
            skPoint(sketch, "E38.82.39.0", {"position": v(444.5, -175.68) * mm});
            skPoint(sketch, "E38.82.40.0", {"position": v(444.5, -182.03) * mm});
            skPoint(sketch, "E38.82.41.0", {"position": v(444.5, -188.38) * mm});
            skPoint(sketch, "E38.82.42.0", {"position": v(444.5, -194.73) * mm});
            skPoint(sketch, "E38.82.43.0", {"position": v(444.5, -201.08) * mm});
            skPoint(sketch, "E38.82.44.0", {"position": v(444.5, -207.43) * mm});
            skPoint(sketch, "E38.82.45.0", {"position": v(444.5, -213.78) * mm});
            skPoint(sketch, "E38.82.46.0", {"position": v(444.5, -220.13) * mm});
            skPoint(sketch, "E38.82.47.0", {"position": v(444.5, -226.48) * mm});
            skPoint(sketch, "E38.82.48.0", {"position": v(444.5, -232.83) * mm});
            skPoint(sketch, "E38.82.49.0", {"position": v(444.5, -239.18) * mm});
            skPoint(sketch, "E38.82.50.0", {"position": v(444.5, -245.53) * mm});
            skPoint(sketch, "E38.82.51.0", {"position": v(444.5, -251.88) * mm});
            skPoint(sketch, "E38.82.52.0", {"position": v(444.5, -258.23) * mm});
            skPoint(sketch, "E38.82.53.0", {"position": v(444.5, -264.58) * mm});
            skPoint(sketch, "E38.82.54.0", {"position": v(444.5, -270.93) * mm});
            skPoint(sketch, "E38.82.55.0", {"position": v(444.5, -277.28) * mm});
            skPoint(sketch, "E38.82.56.0", {"position": v(444.5, -283.63) * mm});
            skPoint(sketch, "E38.82.57.0", {"position": v(444.5, -289.98) * mm});
            skPoint(sketch, "E38.82.58.0", {"position": v(444.5, -296.33) * mm});
            skPoint(sketch, "E38.82.59.0", {"position": v(444.5, -302.68) * mm});
            skPoint(sketch, "E38.82.60.0", {"position": v(444.5, -309.03) * mm});
            skPoint(sketch, "E38.82.61.0", {"position": v(444.5, -315.38) * mm});
            skPoint(sketch, "E38.82.62.0", {"position": v(444.5, -321.73) * mm});
            skPoint(sketch, "E38.82.63.0", {"position": v(444.5, -328.08) * mm});
            skPoint(sketch, "E38.82.64.0", {"position": v(444.5, -334.43) * mm});
            skPoint(sketch, "E38.82.65.0", {"position": v(444.5, -340.78) * mm});
            skPoint(sketch, "E38.82.66.0", {"position": v(444.5, -347.13) * mm});
            skPoint(sketch, "E38.82.67.0", {"position": v(444.5, -353.48) * mm});
            skPoint(sketch, "E38.82.68.0", {"position": v(444.5, -359.83) * mm});
            skPoint(sketch, "E38.82.69.0", {"position": v(444.5, -366.18) * mm});
            skPoint(sketch, "E38.82.70.0", {"position": v(444.5, -372.53) * mm});
            skPoint(sketch, "E38.82.71.0", {"position": v(444.5, -378.88) * mm});
            skPoint(sketch, "E38.82.72.0", {"position": v(444.5, -385.23) * mm});
            skPoint(sketch, "E38.82.73.0", {"position": v(444.5, -391.58) * mm});
            skPoint(sketch, "E38.82.74.0", {"position": v(444.5, -397.93) * mm});
            skPoint(sketch, "E38.82.75.0", {"position": v(444.5, -404.28) * mm});
            skPoint(sketch, "E38.82.76.0", {"position": v(444.5, -410.63) * mm});
            skPoint(sketch, "E38.82.77.0", {"position": v(444.5, -416.98) * mm});
            skPoint(sketch, "E38.82.78.0", {"position": v(444.5, -423.33) * mm});
            skPoint(sketch, "E38.82.79.0", {"position": v(444.5, -429.68) * mm});
            skPoint(sketch, "E38.82.80.0", {"position": v(444.5, -436.03) * mm});
            skPoint(sketch, "E38.82.81.0", {"position": v(444.5, -442.38) * mm});
            skPoint(sketch, "E38.82.82.0", {"position": v(444.5, -448.73) * mm});
            skPoint(sketch, "E38.82.83.0", {"position": v(444.5, -455.08) * mm});
            skPoint(sketch, "E38.82.84.0", {"position": v(444.5, -461.43) * mm});
            skPoint(sketch, "E38.82.85.0", {"position": v(444.5, -467.78) * mm});
            skPoint(sketch, "E38.82.86.0", {"position": v(444.5, -474.13) * mm});
            skPoint(sketch, "E38.82.87.0", {"position": v(444.5, -480.48) * mm});
            skPoint(sketch, "E38.82.88.0", {"position": v(444.5, -486.83) * mm});
            skPoint(sketch, "E38.82.89.0", {"position": v(444.5, -493.18) * mm});
            skPoint(sketch, "E38.82.90.0", {"position": v(444.5, -499.53) * mm});
            skPoint(sketch, "E38.82.91.0", {"position": v(444.5, -505.88) * mm});
            skPoint(sketch, "E38.82.92.0", {"position": v(444.5, -512.23) * mm});
            skPoint(sketch, "E38.82.93.0", {"position": v(444.5, -518.58) * mm});
            skPoint(sketch, "E38.82.94.0", {"position": v(444.5, -524.93) * mm});
            skPoint(sketch, "E38.82.95.0", {"position": v(444.5, -531.28) * mm});
            skPoint(sketch, "E38.82.96.0", {"position": v(444.5, -537.63) * mm});
            skPoint(sketch, "E38.82.97.0", {"position": v(444.5, -543.98) * mm});
            skPoint(sketch, "E38.82.98.0", {"position": v(444.5, -550.33) * mm});
            skPoint(sketch, "E38.82.99.0", {"position": v(444.5, -556.68) * mm});
            skPoint(sketch, "E38.83.0.0", {"position": v(450.85, 71.97) * mm});
            skPoint(sketch, "E38.83.1.0", {"position": v(450.85, 65.62) * mm});
            skPoint(sketch, "E38.83.2.0", {"position": v(450.85, 59.27) * mm});
            skPoint(sketch, "E38.83.3.0", {"position": v(450.85, 52.92) * mm});
            skPoint(sketch, "E38.83.4.0", {"position": v(450.85, 46.57) * mm});
            skPoint(sketch, "E38.83.5.0", {"position": v(450.85, 40.22) * mm});
            skPoint(sketch, "E38.83.6.0", {"position": v(450.85, 33.87) * mm});
            skPoint(sketch, "E38.83.7.0", {"position": v(450.85, 27.52) * mm});
            skPoint(sketch, "E38.83.8.0", {"position": v(450.85, 21.17) * mm});
            skPoint(sketch, "E38.83.9.0", {"position": v(450.85, 14.82) * mm});
            skPoint(sketch, "E38.83.10.0", {"position": v(450.85, 8.47) * mm});
            skPoint(sketch, "E38.83.11.0", {"position": v(450.85, 2.12) * mm});
            skPoint(sketch, "E38.83.12.0", {"position": v(450.85, -4.23) * mm});
            skPoint(sketch, "E38.83.13.0", {"position": v(450.85, -10.58) * mm});
            skPoint(sketch, "E38.83.14.0", {"position": v(450.85, -16.93) * mm});
            skPoint(sketch, "E38.83.15.0", {"position": v(450.85, -23.28) * mm});
            skPoint(sketch, "E38.83.16.0", {"position": v(450.85, -29.63) * mm});
            skPoint(sketch, "E38.83.17.0", {"position": v(450.85, -35.98) * mm});
            skPoint(sketch, "E38.83.18.0", {"position": v(450.85, -42.33) * mm});
            skPoint(sketch, "E38.83.19.0", {"position": v(450.85, -48.68) * mm});
            skPoint(sketch, "E38.83.20.0", {"position": v(450.85, -55.03) * mm});
            skPoint(sketch, "E38.83.21.0", {"position": v(450.85, -61.38) * mm});
            skPoint(sketch, "E38.83.22.0", {"position": v(450.85, -67.73) * mm});
            skPoint(sketch, "E38.83.23.0", {"position": v(450.85, -74.08) * mm});
            skPoint(sketch, "E38.83.24.0", {"position": v(450.85, -80.43) * mm});
            skPoint(sketch, "E38.83.25.0", {"position": v(450.85, -86.78) * mm});
            skPoint(sketch, "E38.83.26.0", {"position": v(450.85, -93.13) * mm});
            skPoint(sketch, "E38.83.27.0", {"position": v(450.85, -99.48) * mm});
            skPoint(sketch, "E38.83.28.0", {"position": v(450.85, -105.83) * mm});
            skPoint(sketch, "E38.83.29.0", {"position": v(450.85, -112.18) * mm});
            skPoint(sketch, "E38.83.30.0", {"position": v(450.85, -118.53) * mm});
            skPoint(sketch, "E38.83.31.0", {"position": v(450.85, -124.88) * mm});
            skPoint(sketch, "E38.83.32.0", {"position": v(450.85, -131.23) * mm});
            skPoint(sketch, "E38.83.33.0", {"position": v(450.85, -137.58) * mm});
            skPoint(sketch, "E38.83.34.0", {"position": v(450.85, -143.93) * mm});
            skPoint(sketch, "E38.83.35.0", {"position": v(450.85, -150.28) * mm});
            skPoint(sketch, "E38.83.36.0", {"position": v(450.85, -156.63) * mm});
            skPoint(sketch, "E38.83.37.0", {"position": v(450.85, -162.98) * mm});
            skPoint(sketch, "E38.83.38.0", {"position": v(450.85, -169.33) * mm});
            skPoint(sketch, "E38.83.39.0", {"position": v(450.85, -175.68) * mm});
            skPoint(sketch, "E38.83.40.0", {"position": v(450.85, -182.03) * mm});
            skPoint(sketch, "E38.83.41.0", {"position": v(450.85, -188.38) * mm});
            skPoint(sketch, "E38.83.42.0", {"position": v(450.85, -194.73) * mm});
            skPoint(sketch, "E38.83.43.0", {"position": v(450.85, -201.08) * mm});
            skPoint(sketch, "E38.83.44.0", {"position": v(450.85, -207.43) * mm});
            skPoint(sketch, "E38.83.45.0", {"position": v(450.85, -213.78) * mm});
            skPoint(sketch, "E38.83.46.0", {"position": v(450.85, -220.13) * mm});
            skPoint(sketch, "E38.83.47.0", {"position": v(450.85, -226.48) * mm});
            skPoint(sketch, "E38.83.48.0", {"position": v(450.85, -232.83) * mm});
            skPoint(sketch, "E38.83.49.0", {"position": v(450.85, -239.18) * mm});
            skPoint(sketch, "E38.83.50.0", {"position": v(450.85, -245.53) * mm});
            skPoint(sketch, "E38.83.51.0", {"position": v(450.85, -251.88) * mm});
            skPoint(sketch, "E38.83.52.0", {"position": v(450.85, -258.23) * mm});
            skPoint(sketch, "E38.83.53.0", {"position": v(450.85, -264.58) * mm});
            skPoint(sketch, "E38.83.54.0", {"position": v(450.85, -270.93) * mm});
            skPoint(sketch, "E38.83.55.0", {"position": v(450.85, -277.28) * mm});
            skPoint(sketch, "E38.83.56.0", {"position": v(450.85, -283.63) * mm});
            skPoint(sketch, "E38.83.57.0", {"position": v(450.85, -289.98) * mm});
            skPoint(sketch, "E38.83.58.0", {"position": v(450.85, -296.33) * mm});
            skPoint(sketch, "E38.83.59.0", {"position": v(450.85, -302.68) * mm});
            skPoint(sketch, "E38.83.60.0", {"position": v(450.85, -309.03) * mm});
            skPoint(sketch, "E38.83.61.0", {"position": v(450.85, -315.38) * mm});
            skPoint(sketch, "E38.83.62.0", {"position": v(450.85, -321.73) * mm});
            skPoint(sketch, "E38.83.63.0", {"position": v(450.85, -328.08) * mm});
            skPoint(sketch, "E38.83.64.0", {"position": v(450.85, -334.43) * mm});
            skPoint(sketch, "E38.83.65.0", {"position": v(450.85, -340.78) * mm});
            skPoint(sketch, "E38.83.66.0", {"position": v(450.85, -347.13) * mm});
            skPoint(sketch, "E38.83.67.0", {"position": v(450.85, -353.48) * mm});
            skPoint(sketch, "E38.83.68.0", {"position": v(450.85, -359.83) * mm});
            skPoint(sketch, "E38.83.69.0", {"position": v(450.85, -366.18) * mm});
            skPoint(sketch, "E38.83.70.0", {"position": v(450.85, -372.53) * mm});
            skPoint(sketch, "E38.83.71.0", {"position": v(450.85, -378.88) * mm});
            skPoint(sketch, "E38.83.72.0", {"position": v(450.85, -385.23) * mm});
            skPoint(sketch, "E38.83.73.0", {"position": v(450.85, -391.58) * mm});
            skPoint(sketch, "E38.83.74.0", {"position": v(450.85, -397.93) * mm});
            skPoint(sketch, "E38.83.75.0", {"position": v(450.85, -404.28) * mm});
            skPoint(sketch, "E38.83.76.0", {"position": v(450.85, -410.63) * mm});
            skPoint(sketch, "E38.83.77.0", {"position": v(450.85, -416.98) * mm});
            skPoint(sketch, "E38.83.78.0", {"position": v(450.85, -423.33) * mm});
            skPoint(sketch, "E38.83.79.0", {"position": v(450.85, -429.68) * mm});
            skPoint(sketch, "E38.83.80.0", {"position": v(450.85, -436.03) * mm});
            skPoint(sketch, "E38.83.81.0", {"position": v(450.85, -442.38) * mm});
            skPoint(sketch, "E38.83.82.0", {"position": v(450.85, -448.73) * mm});
            skPoint(sketch, "E38.83.83.0", {"position": v(450.85, -455.08) * mm});
            skPoint(sketch, "E38.83.84.0", {"position": v(450.85, -461.43) * mm});
            skPoint(sketch, "E38.83.85.0", {"position": v(450.85, -467.78) * mm});
            skPoint(sketch, "E38.83.86.0", {"position": v(450.85, -474.13) * mm});
            skPoint(sketch, "E38.83.87.0", {"position": v(450.85, -480.48) * mm});
            skPoint(sketch, "E38.83.88.0", {"position": v(450.85, -486.83) * mm});
            skPoint(sketch, "E38.83.89.0", {"position": v(450.85, -493.18) * mm});
            skPoint(sketch, "E38.83.90.0", {"position": v(450.85, -499.53) * mm});
            skPoint(sketch, "E38.83.91.0", {"position": v(450.85, -505.88) * mm});
            skPoint(sketch, "E38.83.92.0", {"position": v(450.85, -512.23) * mm});
            skPoint(sketch, "E38.83.93.0", {"position": v(450.85, -518.58) * mm});
            skPoint(sketch, "E38.83.94.0", {"position": v(450.85, -524.93) * mm});
            skPoint(sketch, "E38.83.95.0", {"position": v(450.85, -531.28) * mm});
            skPoint(sketch, "E38.83.96.0", {"position": v(450.85, -537.63) * mm});
            skPoint(sketch, "E38.83.97.0", {"position": v(450.85, -543.98) * mm});
            skPoint(sketch, "E38.83.98.0", {"position": v(450.85, -550.33) * mm});
            skPoint(sketch, "E38.83.99.0", {"position": v(450.85, -556.68) * mm});
            skPoint(sketch, "E38.84.0.0", {"position": v(457.2, 71.97) * mm});
            skPoint(sketch, "E38.84.1.0", {"position": v(457.2, 65.62) * mm});
            skPoint(sketch, "E38.84.2.0", {"position": v(457.2, 59.27) * mm});
            skPoint(sketch, "E38.84.3.0", {"position": v(457.2, 52.92) * mm});
            skPoint(sketch, "E38.84.4.0", {"position": v(457.2, 46.57) * mm});
            skPoint(sketch, "E38.84.5.0", {"position": v(457.2, 40.22) * mm});
            skPoint(sketch, "E38.84.6.0", {"position": v(457.2, 33.87) * mm});
            skPoint(sketch, "E38.84.7.0", {"position": v(457.2, 27.52) * mm});
            skPoint(sketch, "E38.84.8.0", {"position": v(457.2, 21.17) * mm});
            skPoint(sketch, "E38.84.9.0", {"position": v(457.2, 14.82) * mm});
            skPoint(sketch, "E38.84.10.0", {"position": v(457.2, 8.47) * mm});
            skPoint(sketch, "E38.84.11.0", {"position": v(457.2, 2.12) * mm});
            skPoint(sketch, "E38.84.12.0", {"position": v(457.2, -4.23) * mm});
            skPoint(sketch, "E38.84.13.0", {"position": v(457.2, -10.58) * mm});
            skPoint(sketch, "E38.84.14.0", {"position": v(457.2, -16.93) * mm});
            skPoint(sketch, "E38.84.15.0", {"position": v(457.2, -23.28) * mm});
            skPoint(sketch, "E38.84.16.0", {"position": v(457.2, -29.63) * mm});
            skPoint(sketch, "E38.84.17.0", {"position": v(457.2, -35.98) * mm});
            skPoint(sketch, "E38.84.18.0", {"position": v(457.2, -42.33) * mm});
            skPoint(sketch, "E38.84.19.0", {"position": v(457.2, -48.68) * mm});
            skPoint(sketch, "E38.84.20.0", {"position": v(457.2, -55.03) * mm});
            skPoint(sketch, "E38.84.21.0", {"position": v(457.2, -61.38) * mm});
            skPoint(sketch, "E38.84.22.0", {"position": v(457.2, -67.73) * mm});
            skPoint(sketch, "E38.84.23.0", {"position": v(457.2, -74.08) * mm});
            skPoint(sketch, "E38.84.24.0", {"position": v(457.2, -80.43) * mm});
            skPoint(sketch, "E38.84.25.0", {"position": v(457.2, -86.78) * mm});
            skPoint(sketch, "E38.84.26.0", {"position": v(457.2, -93.13) * mm});
            skPoint(sketch, "E38.84.27.0", {"position": v(457.2, -99.48) * mm});
            skPoint(sketch, "E38.84.28.0", {"position": v(457.2, -105.83) * mm});
            skPoint(sketch, "E38.84.29.0", {"position": v(457.2, -112.18) * mm});
            skPoint(sketch, "E38.84.30.0", {"position": v(457.2, -118.53) * mm});
            skPoint(sketch, "E38.84.31.0", {"position": v(457.2, -124.88) * mm});
            skPoint(sketch, "E38.84.32.0", {"position": v(457.2, -131.23) * mm});
            skPoint(sketch, "E38.84.33.0", {"position": v(457.2, -137.58) * mm});
            skPoint(sketch, "E38.84.34.0", {"position": v(457.2, -143.93) * mm});
            skPoint(sketch, "E38.84.35.0", {"position": v(457.2, -150.28) * mm});
            skPoint(sketch, "E38.84.36.0", {"position": v(457.2, -156.63) * mm});
            skPoint(sketch, "E38.84.37.0", {"position": v(457.2, -162.98) * mm});
            skPoint(sketch, "E38.84.38.0", {"position": v(457.2, -169.33) * mm});
            skPoint(sketch, "E38.84.39.0", {"position": v(457.2, -175.68) * mm});
            skPoint(sketch, "E38.84.40.0", {"position": v(457.2, -182.03) * mm});
            skPoint(sketch, "E38.84.41.0", {"position": v(457.2, -188.38) * mm});
            skPoint(sketch, "E38.84.42.0", {"position": v(457.2, -194.73) * mm});
            skPoint(sketch, "E38.84.43.0", {"position": v(457.2, -201.08) * mm});
            skPoint(sketch, "E38.84.44.0", {"position": v(457.2, -207.43) * mm});
            skPoint(sketch, "E38.84.45.0", {"position": v(457.2, -213.78) * mm});
            skPoint(sketch, "E38.84.46.0", {"position": v(457.2, -220.13) * mm});
            skPoint(sketch, "E38.84.47.0", {"position": v(457.2, -226.48) * mm});
            skPoint(sketch, "E38.84.48.0", {"position": v(457.2, -232.83) * mm});
            skPoint(sketch, "E38.84.49.0", {"position": v(457.2, -239.18) * mm});
            skPoint(sketch, "E38.84.50.0", {"position": v(457.2, -245.53) * mm});
            skPoint(sketch, "E38.84.51.0", {"position": v(457.2, -251.88) * mm});
            skPoint(sketch, "E38.84.52.0", {"position": v(457.2, -258.23) * mm});
            skPoint(sketch, "E38.84.53.0", {"position": v(457.2, -264.58) * mm});
            skPoint(sketch, "E38.84.54.0", {"position": v(457.2, -270.93) * mm});
            skPoint(sketch, "E38.84.55.0", {"position": v(457.2, -277.28) * mm});
            skPoint(sketch, "E38.84.56.0", {"position": v(457.2, -283.63) * mm});
            skPoint(sketch, "E38.84.57.0", {"position": v(457.2, -289.98) * mm});
            skPoint(sketch, "E38.84.58.0", {"position": v(457.2, -296.33) * mm});
            skPoint(sketch, "E38.84.59.0", {"position": v(457.2, -302.68) * mm});
            skPoint(sketch, "E38.84.60.0", {"position": v(457.2, -309.03) * mm});
            skPoint(sketch, "E38.84.61.0", {"position": v(457.2, -315.38) * mm});
            skPoint(sketch, "E38.84.62.0", {"position": v(457.2, -321.73) * mm});
            skPoint(sketch, "E38.84.63.0", {"position": v(457.2, -328.08) * mm});
            skPoint(sketch, "E38.84.64.0", {"position": v(457.2, -334.43) * mm});
            skPoint(sketch, "E38.84.65.0", {"position": v(457.2, -340.78) * mm});
            skPoint(sketch, "E38.84.66.0", {"position": v(457.2, -347.13) * mm});
            skPoint(sketch, "E38.84.67.0", {"position": v(457.2, -353.48) * mm});
            skPoint(sketch, "E38.84.68.0", {"position": v(457.2, -359.83) * mm});
            skPoint(sketch, "E38.84.69.0", {"position": v(457.2, -366.18) * mm});
            skPoint(sketch, "E38.84.70.0", {"position": v(457.2, -372.53) * mm});
            skPoint(sketch, "E38.84.71.0", {"position": v(457.2, -378.88) * mm});
            skPoint(sketch, "E38.84.72.0", {"position": v(457.2, -385.23) * mm});
            skPoint(sketch, "E38.84.73.0", {"position": v(457.2, -391.58) * mm});
            skPoint(sketch, "E38.84.74.0", {"position": v(457.2, -397.93) * mm});
            skPoint(sketch, "E38.84.75.0", {"position": v(457.2, -404.28) * mm});
            skPoint(sketch, "E38.84.76.0", {"position": v(457.2, -410.63) * mm});
            skPoint(sketch, "E38.84.77.0", {"position": v(457.2, -416.98) * mm});
            skPoint(sketch, "E38.84.78.0", {"position": v(457.2, -423.33) * mm});
            skPoint(sketch, "E38.84.79.0", {"position": v(457.2, -429.68) * mm});
            skPoint(sketch, "E38.84.80.0", {"position": v(457.2, -436.03) * mm});
            skPoint(sketch, "E38.84.81.0", {"position": v(457.2, -442.38) * mm});
            skPoint(sketch, "E38.84.82.0", {"position": v(457.2, -448.73) * mm});
            skPoint(sketch, "E38.84.83.0", {"position": v(457.2, -455.08) * mm});
            skPoint(sketch, "E38.84.84.0", {"position": v(457.2, -461.43) * mm});
            skPoint(sketch, "E38.84.85.0", {"position": v(457.2, -467.78) * mm});
            skPoint(sketch, "E38.84.86.0", {"position": v(457.2, -474.13) * mm});
            skPoint(sketch, "E38.84.87.0", {"position": v(457.2, -480.48) * mm});
            skPoint(sketch, "E38.84.88.0", {"position": v(457.2, -486.83) * mm});
            skPoint(sketch, "E38.84.89.0", {"position": v(457.2, -493.18) * mm});
            skPoint(sketch, "E38.84.90.0", {"position": v(457.2, -499.53) * mm});
            skPoint(sketch, "E38.84.91.0", {"position": v(457.2, -505.88) * mm});
            skPoint(sketch, "E38.84.92.0", {"position": v(457.2, -512.23) * mm});
            skPoint(sketch, "E38.84.93.0", {"position": v(457.2, -518.58) * mm});
            skPoint(sketch, "E38.84.94.0", {"position": v(457.2, -524.93) * mm});
            skPoint(sketch, "E38.84.95.0", {"position": v(457.2, -531.28) * mm});
            skPoint(sketch, "E38.84.96.0", {"position": v(457.2, -537.63) * mm});
            skPoint(sketch, "E38.84.97.0", {"position": v(457.2, -543.98) * mm});
            skPoint(sketch, "E38.84.98.0", {"position": v(457.2, -550.33) * mm});
            skPoint(sketch, "E38.84.99.0", {"position": v(457.2, -556.68) * mm});
            skPoint(sketch, "E38.85.0.0", {"position": v(463.55, 71.97) * mm});
            skPoint(sketch, "E38.85.1.0", {"position": v(463.55, 65.62) * mm});
            skPoint(sketch, "E38.85.2.0", {"position": v(463.55, 59.27) * mm});
            skPoint(sketch, "E38.85.3.0", {"position": v(463.55, 52.92) * mm});
            skPoint(sketch, "E38.85.4.0", {"position": v(463.55, 46.57) * mm});
            skPoint(sketch, "E38.85.5.0", {"position": v(463.55, 40.22) * mm});
            skPoint(sketch, "E38.85.6.0", {"position": v(463.55, 33.87) * mm});
            skPoint(sketch, "E38.85.7.0", {"position": v(463.55, 27.52) * mm});
            skPoint(sketch, "E38.85.8.0", {"position": v(463.55, 21.17) * mm});
            skPoint(sketch, "E38.85.9.0", {"position": v(463.55, 14.82) * mm});
            skPoint(sketch, "E38.85.10.0", {"position": v(463.55, 8.47) * mm});
            skPoint(sketch, "E38.85.11.0", {"position": v(463.55, 2.12) * mm});
            skPoint(sketch, "E38.85.12.0", {"position": v(463.55, -4.23) * mm});
            skPoint(sketch, "E38.85.13.0", {"position": v(463.55, -10.58) * mm});
            skPoint(sketch, "E38.85.14.0", {"position": v(463.55, -16.93) * mm});
            skPoint(sketch, "E38.85.15.0", {"position": v(463.55, -23.28) * mm});
            skPoint(sketch, "E38.85.16.0", {"position": v(463.55, -29.63) * mm});
            skPoint(sketch, "E38.85.17.0", {"position": v(463.55, -35.98) * mm});
            skPoint(sketch, "E38.85.18.0", {"position": v(463.55, -42.33) * mm});
            skPoint(sketch, "E38.85.19.0", {"position": v(463.55, -48.68) * mm});
            skPoint(sketch, "E38.85.20.0", {"position": v(463.55, -55.03) * mm});
            skPoint(sketch, "E38.85.21.0", {"position": v(463.55, -61.38) * mm});
            skPoint(sketch, "E38.85.22.0", {"position": v(463.55, -67.73) * mm});
            skPoint(sketch, "E38.85.23.0", {"position": v(463.55, -74.08) * mm});
            skPoint(sketch, "E38.85.24.0", {"position": v(463.55, -80.43) * mm});
            skPoint(sketch, "E38.85.25.0", {"position": v(463.55, -86.78) * mm});
            skPoint(sketch, "E38.85.26.0", {"position": v(463.55, -93.13) * mm});
            skPoint(sketch, "E38.85.27.0", {"position": v(463.55, -99.48) * mm});
            skPoint(sketch, "E38.85.28.0", {"position": v(463.55, -105.83) * mm});
            skPoint(sketch, "E38.85.29.0", {"position": v(463.55, -112.18) * mm});
            skPoint(sketch, "E38.85.30.0", {"position": v(463.55, -118.53) * mm});
            skPoint(sketch, "E38.85.31.0", {"position": v(463.55, -124.88) * mm});
            skPoint(sketch, "E38.85.32.0", {"position": v(463.55, -131.23) * mm});
            skPoint(sketch, "E38.85.33.0", {"position": v(463.55, -137.58) * mm});
            skPoint(sketch, "E38.85.34.0", {"position": v(463.55, -143.93) * mm});
            skPoint(sketch, "E38.85.35.0", {"position": v(463.55, -150.28) * mm});
            skPoint(sketch, "E38.85.36.0", {"position": v(463.55, -156.63) * mm});
            skPoint(sketch, "E38.85.37.0", {"position": v(463.55, -162.98) * mm});
            skPoint(sketch, "E38.85.38.0", {"position": v(463.55, -169.33) * mm});
            skPoint(sketch, "E38.85.39.0", {"position": v(463.55, -175.68) * mm});
            skPoint(sketch, "E38.85.40.0", {"position": v(463.55, -182.03) * mm});
            skPoint(sketch, "E38.85.41.0", {"position": v(463.55, -188.38) * mm});
            skPoint(sketch, "E38.85.42.0", {"position": v(463.55, -194.73) * mm});
            skPoint(sketch, "E38.85.43.0", {"position": v(463.55, -201.08) * mm});
            skPoint(sketch, "E38.85.44.0", {"position": v(463.55, -207.43) * mm});
            skPoint(sketch, "E38.85.45.0", {"position": v(463.55, -213.78) * mm});
            skPoint(sketch, "E38.85.46.0", {"position": v(463.55, -220.13) * mm});
            skPoint(sketch, "E38.85.47.0", {"position": v(463.55, -226.48) * mm});
            skPoint(sketch, "E38.85.48.0", {"position": v(463.55, -232.83) * mm});
            skPoint(sketch, "E38.85.49.0", {"position": v(463.55, -239.18) * mm});
            skPoint(sketch, "E38.85.50.0", {"position": v(463.55, -245.53) * mm});
            skPoint(sketch, "E38.85.51.0", {"position": v(463.55, -251.88) * mm});
            skPoint(sketch, "E38.85.52.0", {"position": v(463.55, -258.23) * mm});
            skPoint(sketch, "E38.85.53.0", {"position": v(463.55, -264.58) * mm});
            skPoint(sketch, "E38.85.54.0", {"position": v(463.55, -270.93) * mm});
            skPoint(sketch, "E38.85.55.0", {"position": v(463.55, -277.28) * mm});
            skPoint(sketch, "E38.85.56.0", {"position": v(463.55, -283.63) * mm});
            skPoint(sketch, "E38.85.57.0", {"position": v(463.55, -289.98) * mm});
            skPoint(sketch, "E38.85.58.0", {"position": v(463.55, -296.33) * mm});
            skPoint(sketch, "E38.85.59.0", {"position": v(463.55, -302.68) * mm});
            skPoint(sketch, "E38.85.60.0", {"position": v(463.55, -309.03) * mm});
            skPoint(sketch, "E38.85.61.0", {"position": v(463.55, -315.38) * mm});
            skPoint(sketch, "E38.85.62.0", {"position": v(463.55, -321.73) * mm});
            skPoint(sketch, "E38.85.63.0", {"position": v(463.55, -328.08) * mm});
            skPoint(sketch, "E38.85.64.0", {"position": v(463.55, -334.43) * mm});
            skPoint(sketch, "E38.85.65.0", {"position": v(463.55, -340.78) * mm});
            skPoint(sketch, "E38.85.66.0", {"position": v(463.55, -347.13) * mm});
            skPoint(sketch, "E38.85.67.0", {"position": v(463.55, -353.48) * mm});
            skPoint(sketch, "E38.85.68.0", {"position": v(463.55, -359.83) * mm});
            skPoint(sketch, "E38.85.69.0", {"position": v(463.55, -366.18) * mm});
            skPoint(sketch, "E38.85.70.0", {"position": v(463.55, -372.53) * mm});
            skPoint(sketch, "E38.85.71.0", {"position": v(463.55, -378.88) * mm});
            skPoint(sketch, "E38.85.72.0", {"position": v(463.55, -385.23) * mm});
            skPoint(sketch, "E38.85.73.0", {"position": v(463.55, -391.58) * mm});
            skPoint(sketch, "E38.85.74.0", {"position": v(463.55, -397.93) * mm});
            skPoint(sketch, "E38.85.75.0", {"position": v(463.55, -404.28) * mm});
            skPoint(sketch, "E38.85.76.0", {"position": v(463.55, -410.63) * mm});
            skPoint(sketch, "E38.85.77.0", {"position": v(463.55, -416.98) * mm});
            skPoint(sketch, "E38.85.78.0", {"position": v(463.55, -423.33) * mm});
            skPoint(sketch, "E38.85.79.0", {"position": v(463.55, -429.68) * mm});
            skPoint(sketch, "E38.85.80.0", {"position": v(463.55, -436.03) * mm});
            skPoint(sketch, "E38.85.81.0", {"position": v(463.55, -442.38) * mm});
            skPoint(sketch, "E38.85.82.0", {"position": v(463.55, -448.73) * mm});
            skPoint(sketch, "E38.85.83.0", {"position": v(463.55, -455.08) * mm});
            skPoint(sketch, "E38.85.84.0", {"position": v(463.55, -461.43) * mm});
            skPoint(sketch, "E38.85.85.0", {"position": v(463.55, -467.78) * mm});
            skPoint(sketch, "E38.85.86.0", {"position": v(463.55, -474.13) * mm});
            skPoint(sketch, "E38.85.87.0", {"position": v(463.55, -480.48) * mm});
            skPoint(sketch, "E38.85.88.0", {"position": v(463.55, -486.83) * mm});
            skPoint(sketch, "E38.85.89.0", {"position": v(463.55, -493.18) * mm});
            skPoint(sketch, "E38.85.90.0", {"position": v(463.55, -499.53) * mm});
            skPoint(sketch, "E38.85.91.0", {"position": v(463.55, -505.88) * mm});
            skPoint(sketch, "E38.85.92.0", {"position": v(463.55, -512.23) * mm});
            skPoint(sketch, "E38.85.93.0", {"position": v(463.55, -518.58) * mm});
            skPoint(sketch, "E38.85.94.0", {"position": v(463.55, -524.93) * mm});
            skPoint(sketch, "E38.85.95.0", {"position": v(463.55, -531.28) * mm});
            skPoint(sketch, "E38.85.96.0", {"position": v(463.55, -537.63) * mm});
            skPoint(sketch, "E38.85.97.0", {"position": v(463.55, -543.98) * mm});
            skPoint(sketch, "E38.85.98.0", {"position": v(463.55, -550.33) * mm});
            skPoint(sketch, "E38.85.99.0", {"position": v(463.55, -556.68) * mm});
            skPoint(sketch, "E38.86.0.0", {"position": v(469.9, 71.97) * mm});
            skPoint(sketch, "E38.86.1.0", {"position": v(469.9, 65.62) * mm});
            skPoint(sketch, "E38.86.2.0", {"position": v(469.9, 59.27) * mm});
            skPoint(sketch, "E38.86.3.0", {"position": v(469.9, 52.92) * mm});
            skPoint(sketch, "E38.86.4.0", {"position": v(469.9, 46.57) * mm});
            skPoint(sketch, "E38.86.5.0", {"position": v(469.9, 40.22) * mm});
            skPoint(sketch, "E38.86.6.0", {"position": v(469.9, 33.87) * mm});
            skPoint(sketch, "E38.86.7.0", {"position": v(469.9, 27.52) * mm});
            skPoint(sketch, "E38.86.8.0", {"position": v(469.9, 21.17) * mm});
            skPoint(sketch, "E38.86.9.0", {"position": v(469.9, 14.82) * mm});
            skPoint(sketch, "E38.86.10.0", {"position": v(469.9, 8.47) * mm});
            skPoint(sketch, "E38.86.11.0", {"position": v(469.9, 2.12) * mm});
            skPoint(sketch, "E38.86.12.0", {"position": v(469.9, -4.23) * mm});
            skPoint(sketch, "E38.86.13.0", {"position": v(469.9, -10.58) * mm});
            skPoint(sketch, "E38.86.14.0", {"position": v(469.9, -16.93) * mm});
            skPoint(sketch, "E38.86.15.0", {"position": v(469.9, -23.28) * mm});
            skPoint(sketch, "E38.86.16.0", {"position": v(469.9, -29.63) * mm});
            skPoint(sketch, "E38.86.17.0", {"position": v(469.9, -35.98) * mm});
            skPoint(sketch, "E38.86.18.0", {"position": v(469.9, -42.33) * mm});
            skPoint(sketch, "E38.86.19.0", {"position": v(469.9, -48.68) * mm});
            skPoint(sketch, "E38.86.20.0", {"position": v(469.9, -55.03) * mm});
            skPoint(sketch, "E38.86.21.0", {"position": v(469.9, -61.38) * mm});
            skPoint(sketch, "E38.86.22.0", {"position": v(469.9, -67.73) * mm});
            skPoint(sketch, "E38.86.23.0", {"position": v(469.9, -74.08) * mm});
            skPoint(sketch, "E38.86.24.0", {"position": v(469.9, -80.43) * mm});
            skPoint(sketch, "E38.86.25.0", {"position": v(469.9, -86.78) * mm});
            skPoint(sketch, "E38.86.26.0", {"position": v(469.9, -93.13) * mm});
            skPoint(sketch, "E38.86.27.0", {"position": v(469.9, -99.48) * mm});
            skPoint(sketch, "E38.86.28.0", {"position": v(469.9, -105.83) * mm});
            skPoint(sketch, "E38.86.29.0", {"position": v(469.9, -112.18) * mm});
            skPoint(sketch, "E38.86.30.0", {"position": v(469.9, -118.53) * mm});
            skPoint(sketch, "E38.86.31.0", {"position": v(469.9, -124.88) * mm});
            skPoint(sketch, "E38.86.32.0", {"position": v(469.9, -131.23) * mm});
            skPoint(sketch, "E38.86.33.0", {"position": v(469.9, -137.58) * mm});
            skPoint(sketch, "E38.86.34.0", {"position": v(469.9, -143.93) * mm});
            skPoint(sketch, "E38.86.35.0", {"position": v(469.9, -150.28) * mm});
            skPoint(sketch, "E38.86.36.0", {"position": v(469.9, -156.63) * mm});
            skPoint(sketch, "E38.86.37.0", {"position": v(469.9, -162.98) * mm});
            skPoint(sketch, "E38.86.38.0", {"position": v(469.9, -169.33) * mm});
            skPoint(sketch, "E38.86.39.0", {"position": v(469.9, -175.68) * mm});
            skPoint(sketch, "E38.86.40.0", {"position": v(469.9, -182.03) * mm});
            skPoint(sketch, "E38.86.41.0", {"position": v(469.9, -188.38) * mm});
            skPoint(sketch, "E38.86.42.0", {"position": v(469.9, -194.73) * mm});
            skPoint(sketch, "E38.86.43.0", {"position": v(469.9, -201.08) * mm});
            skPoint(sketch, "E38.86.44.0", {"position": v(469.9, -207.43) * mm});
            skPoint(sketch, "E38.86.45.0", {"position": v(469.9, -213.78) * mm});
            skPoint(sketch, "E38.86.46.0", {"position": v(469.9, -220.13) * mm});
            skPoint(sketch, "E38.86.47.0", {"position": v(469.9, -226.48) * mm});
            skPoint(sketch, "E38.86.48.0", {"position": v(469.9, -232.83) * mm});
            skPoint(sketch, "E38.86.49.0", {"position": v(469.9, -239.18) * mm});
            skPoint(sketch, "E38.86.50.0", {"position": v(469.9, -245.53) * mm});
            skPoint(sketch, "E38.86.51.0", {"position": v(469.9, -251.88) * mm});
            skPoint(sketch, "E38.86.52.0", {"position": v(469.9, -258.23) * mm});
            skPoint(sketch, "E38.86.53.0", {"position": v(469.9, -264.58) * mm});
            skPoint(sketch, "E38.86.54.0", {"position": v(469.9, -270.93) * mm});
            skPoint(sketch, "E38.86.55.0", {"position": v(469.9, -277.28) * mm});
            skPoint(sketch, "E38.86.56.0", {"position": v(469.9, -283.63) * mm});
            skPoint(sketch, "E38.86.57.0", {"position": v(469.9, -289.98) * mm});
            skPoint(sketch, "E38.86.58.0", {"position": v(469.9, -296.33) * mm});
            skPoint(sketch, "E38.86.59.0", {"position": v(469.9, -302.68) * mm});
            skPoint(sketch, "E38.86.60.0", {"position": v(469.9, -309.03) * mm});
            skPoint(sketch, "E38.86.61.0", {"position": v(469.9, -315.38) * mm});
            skPoint(sketch, "E38.86.62.0", {"position": v(469.9, -321.73) * mm});
            skPoint(sketch, "E38.86.63.0", {"position": v(469.9, -328.08) * mm});
            skPoint(sketch, "E38.86.64.0", {"position": v(469.9, -334.43) * mm});
            skPoint(sketch, "E38.86.65.0", {"position": v(469.9, -340.78) * mm});
            skPoint(sketch, "E38.86.66.0", {"position": v(469.9, -347.13) * mm});
            skPoint(sketch, "E38.86.67.0", {"position": v(469.9, -353.48) * mm});
            skPoint(sketch, "E38.86.68.0", {"position": v(469.9, -359.83) * mm});
            skPoint(sketch, "E38.86.69.0", {"position": v(469.9, -366.18) * mm});
            skPoint(sketch, "E38.86.70.0", {"position": v(469.9, -372.53) * mm});
            skPoint(sketch, "E38.86.71.0", {"position": v(469.9, -378.88) * mm});
            skPoint(sketch, "E38.86.72.0", {"position": v(469.9, -385.23) * mm});
            skPoint(sketch, "E38.86.73.0", {"position": v(469.9, -391.58) * mm});
            skPoint(sketch, "E38.86.74.0", {"position": v(469.9, -397.93) * mm});
            skPoint(sketch, "E38.86.75.0", {"position": v(469.9, -404.28) * mm});
            skPoint(sketch, "E38.86.76.0", {"position": v(469.9, -410.63) * mm});
            skPoint(sketch, "E38.86.77.0", {"position": v(469.9, -416.98) * mm});
            skPoint(sketch, "E38.86.78.0", {"position": v(469.9, -423.33) * mm});
            skPoint(sketch, "E38.86.79.0", {"position": v(469.9, -429.68) * mm});
            skPoint(sketch, "E38.86.80.0", {"position": v(469.9, -436.03) * mm});
            skPoint(sketch, "E38.86.81.0", {"position": v(469.9, -442.38) * mm});
            skPoint(sketch, "E38.86.82.0", {"position": v(469.9, -448.73) * mm});
            skPoint(sketch, "E38.86.83.0", {"position": v(469.9, -455.08) * mm});
            skPoint(sketch, "E38.86.84.0", {"position": v(469.9, -461.43) * mm});
            skPoint(sketch, "E38.86.85.0", {"position": v(469.9, -467.78) * mm});
            skPoint(sketch, "E38.86.86.0", {"position": v(469.9, -474.13) * mm});
            skPoint(sketch, "E38.86.87.0", {"position": v(469.9, -480.48) * mm});
            skPoint(sketch, "E38.86.88.0", {"position": v(469.9, -486.83) * mm});
            skPoint(sketch, "E38.86.89.0", {"position": v(469.9, -493.18) * mm});
            skPoint(sketch, "E38.86.90.0", {"position": v(469.9, -499.53) * mm});
            skPoint(sketch, "E38.86.91.0", {"position": v(469.9, -505.88) * mm});
            skPoint(sketch, "E38.86.92.0", {"position": v(469.9, -512.23) * mm});
            skPoint(sketch, "E38.86.93.0", {"position": v(469.9, -518.58) * mm});
            skPoint(sketch, "E38.86.94.0", {"position": v(469.9, -524.93) * mm});
            skPoint(sketch, "E38.86.95.0", {"position": v(469.9, -531.28) * mm});
            skPoint(sketch, "E38.86.96.0", {"position": v(469.9, -537.63) * mm});
            skPoint(sketch, "E38.86.97.0", {"position": v(469.9, -543.98) * mm});
            skPoint(sketch, "E38.86.98.0", {"position": v(469.9, -550.33) * mm});
            skPoint(sketch, "E38.86.99.0", {"position": v(469.9, -556.68) * mm});
            skPoint(sketch, "E38.87.0.0", {"position": v(476.25, 71.97) * mm});
            skPoint(sketch, "E38.87.1.0", {"position": v(476.25, 65.62) * mm});
            skPoint(sketch, "E38.87.2.0", {"position": v(476.25, 59.27) * mm});
            skPoint(sketch, "E38.87.3.0", {"position": v(476.25, 52.92) * mm});
            skPoint(sketch, "E38.87.4.0", {"position": v(476.25, 46.57) * mm});
            skPoint(sketch, "E38.87.5.0", {"position": v(476.25, 40.22) * mm});
            skPoint(sketch, "E38.87.6.0", {"position": v(476.25, 33.87) * mm});
            skPoint(sketch, "E38.87.7.0", {"position": v(476.25, 27.52) * mm});
            skPoint(sketch, "E38.87.8.0", {"position": v(476.25, 21.17) * mm});
            skPoint(sketch, "E38.87.9.0", {"position": v(476.25, 14.82) * mm});
            skPoint(sketch, "E38.87.10.0", {"position": v(476.25, 8.47) * mm});
            skPoint(sketch, "E38.87.11.0", {"position": v(476.25, 2.12) * mm});
            skPoint(sketch, "E38.87.12.0", {"position": v(476.25, -4.23) * mm});
            skPoint(sketch, "E38.87.13.0", {"position": v(476.25, -10.58) * mm});
            skPoint(sketch, "E38.87.14.0", {"position": v(476.25, -16.93) * mm});
            skPoint(sketch, "E38.87.15.0", {"position": v(476.25, -23.28) * mm});
            skPoint(sketch, "E38.87.16.0", {"position": v(476.25, -29.63) * mm});
            skPoint(sketch, "E38.87.17.0", {"position": v(476.25, -35.98) * mm});
            skPoint(sketch, "E38.87.18.0", {"position": v(476.25, -42.33) * mm});
            skPoint(sketch, "E38.87.19.0", {"position": v(476.25, -48.68) * mm});
            skPoint(sketch, "E38.87.20.0", {"position": v(476.25, -55.03) * mm});
            skPoint(sketch, "E38.87.21.0", {"position": v(476.25, -61.38) * mm});
            skPoint(sketch, "E38.87.22.0", {"position": v(476.25, -67.73) * mm});
            skPoint(sketch, "E38.87.23.0", {"position": v(476.25, -74.08) * mm});
            skPoint(sketch, "E38.87.24.0", {"position": v(476.25, -80.43) * mm});
            skPoint(sketch, "E38.87.25.0", {"position": v(476.25, -86.78) * mm});
            skPoint(sketch, "E38.87.26.0", {"position": v(476.25, -93.13) * mm});
            skPoint(sketch, "E38.87.27.0", {"position": v(476.25, -99.48) * mm});
            skPoint(sketch, "E38.87.28.0", {"position": v(476.25, -105.83) * mm});
            skPoint(sketch, "E38.87.29.0", {"position": v(476.25, -112.18) * mm});
            skPoint(sketch, "E38.87.30.0", {"position": v(476.25, -118.53) * mm});
            skPoint(sketch, "E38.87.31.0", {"position": v(476.25, -124.88) * mm});
            skPoint(sketch, "E38.87.32.0", {"position": v(476.25, -131.23) * mm});
            skPoint(sketch, "E38.87.33.0", {"position": v(476.25, -137.58) * mm});
            skPoint(sketch, "E38.87.34.0", {"position": v(476.25, -143.93) * mm});
            skPoint(sketch, "E38.87.35.0", {"position": v(476.25, -150.28) * mm});
            skPoint(sketch, "E38.87.36.0", {"position": v(476.25, -156.63) * mm});
            skPoint(sketch, "E38.87.37.0", {"position": v(476.25, -162.98) * mm});
            skPoint(sketch, "E38.87.38.0", {"position": v(476.25, -169.33) * mm});
            skPoint(sketch, "E38.87.39.0", {"position": v(476.25, -175.68) * mm});
            skPoint(sketch, "E38.87.40.0", {"position": v(476.25, -182.03) * mm});
            skPoint(sketch, "E38.87.41.0", {"position": v(476.25, -188.38) * mm});
            skPoint(sketch, "E38.87.42.0", {"position": v(476.25, -194.73) * mm});
            skPoint(sketch, "E38.87.43.0", {"position": v(476.25, -201.08) * mm});
            skPoint(sketch, "E38.87.44.0", {"position": v(476.25, -207.43) * mm});
            skPoint(sketch, "E38.87.45.0", {"position": v(476.25, -213.78) * mm});
            skPoint(sketch, "E38.87.46.0", {"position": v(476.25, -220.13) * mm});
            skPoint(sketch, "E38.87.47.0", {"position": v(476.25, -226.48) * mm});
            skPoint(sketch, "E38.87.48.0", {"position": v(476.25, -232.83) * mm});
            skPoint(sketch, "E38.87.49.0", {"position": v(476.25, -239.18) * mm});
            skPoint(sketch, "E38.87.50.0", {"position": v(476.25, -245.53) * mm});
            skPoint(sketch, "E38.87.51.0", {"position": v(476.25, -251.88) * mm});
            skPoint(sketch, "E38.87.52.0", {"position": v(476.25, -258.23) * mm});
            skPoint(sketch, "E38.87.53.0", {"position": v(476.25, -264.58) * mm});
            skPoint(sketch, "E38.87.54.0", {"position": v(476.25, -270.93) * mm});
            skPoint(sketch, "E38.87.55.0", {"position": v(476.25, -277.28) * mm});
            skPoint(sketch, "E38.87.56.0", {"position": v(476.25, -283.63) * mm});
            skPoint(sketch, "E38.87.57.0", {"position": v(476.25, -289.98) * mm});
            skPoint(sketch, "E38.87.58.0", {"position": v(476.25, -296.33) * mm});
            skPoint(sketch, "E38.87.59.0", {"position": v(476.25, -302.68) * mm});
            skPoint(sketch, "E38.87.60.0", {"position": v(476.25, -309.03) * mm});
            skPoint(sketch, "E38.87.61.0", {"position": v(476.25, -315.38) * mm});
            skPoint(sketch, "E38.87.62.0", {"position": v(476.25, -321.73) * mm});
            skPoint(sketch, "E38.87.63.0", {"position": v(476.25, -328.08) * mm});
            skPoint(sketch, "E38.87.64.0", {"position": v(476.25, -334.43) * mm});
            skPoint(sketch, "E38.87.65.0", {"position": v(476.25, -340.78) * mm});
            skPoint(sketch, "E38.87.66.0", {"position": v(476.25, -347.13) * mm});
            skPoint(sketch, "E38.87.67.0", {"position": v(476.25, -353.48) * mm});
            skPoint(sketch, "E38.87.68.0", {"position": v(476.25, -359.83) * mm});
            skPoint(sketch, "E38.87.69.0", {"position": v(476.25, -366.18) * mm});
            skPoint(sketch, "E38.87.70.0", {"position": v(476.25, -372.53) * mm});
            skPoint(sketch, "E38.87.71.0", {"position": v(476.25, -378.88) * mm});
            skPoint(sketch, "E38.87.72.0", {"position": v(476.25, -385.23) * mm});
            skPoint(sketch, "E38.87.73.0", {"position": v(476.25, -391.58) * mm});
            skPoint(sketch, "E38.87.74.0", {"position": v(476.25, -397.93) * mm});
            skPoint(sketch, "E38.87.75.0", {"position": v(476.25, -404.28) * mm});
            skPoint(sketch, "E38.87.76.0", {"position": v(476.25, -410.63) * mm});
            skPoint(sketch, "E38.87.77.0", {"position": v(476.25, -416.98) * mm});
            skPoint(sketch, "E38.87.78.0", {"position": v(476.25, -423.33) * mm});
            skPoint(sketch, "E38.87.79.0", {"position": v(476.25, -429.68) * mm});
            skPoint(sketch, "E38.87.80.0", {"position": v(476.25, -436.03) * mm});
            skPoint(sketch, "E38.87.81.0", {"position": v(476.25, -442.38) * mm});
            skPoint(sketch, "E38.87.82.0", {"position": v(476.25, -448.73) * mm});
            skPoint(sketch, "E38.87.83.0", {"position": v(476.25, -455.08) * mm});
            skPoint(sketch, "E38.87.84.0", {"position": v(476.25, -461.43) * mm});
            skPoint(sketch, "E38.87.85.0", {"position": v(476.25, -467.78) * mm});
            skPoint(sketch, "E38.87.86.0", {"position": v(476.25, -474.13) * mm});
            skPoint(sketch, "E38.87.87.0", {"position": v(476.25, -480.48) * mm});
            skPoint(sketch, "E38.87.88.0", {"position": v(476.25, -486.83) * mm});
            skPoint(sketch, "E38.87.89.0", {"position": v(476.25, -493.18) * mm});
            skPoint(sketch, "E38.87.90.0", {"position": v(476.25, -499.53) * mm});
            skPoint(sketch, "E38.87.91.0", {"position": v(476.25, -505.88) * mm});
            skPoint(sketch, "E38.87.92.0", {"position": v(476.25, -512.23) * mm});
            skPoint(sketch, "E38.87.93.0", {"position": v(476.25, -518.58) * mm});
            skPoint(sketch, "E38.87.94.0", {"position": v(476.25, -524.93) * mm});
            skPoint(sketch, "E38.87.95.0", {"position": v(476.25, -531.28) * mm});
            skPoint(sketch, "E38.87.96.0", {"position": v(476.25, -537.63) * mm});
            skPoint(sketch, "E38.87.97.0", {"position": v(476.25, -543.98) * mm});
            skPoint(sketch, "E38.87.98.0", {"position": v(476.25, -550.33) * mm});
            skPoint(sketch, "E38.87.99.0", {"position": v(476.25, -556.68) * mm});
            skPoint(sketch, "E38.88.0.0", {"position": v(482.6, 71.97) * mm});
            skPoint(sketch, "E38.88.1.0", {"position": v(482.6, 65.62) * mm});
            skPoint(sketch, "E38.88.2.0", {"position": v(482.6, 59.27) * mm});
            skPoint(sketch, "E38.88.3.0", {"position": v(482.6, 52.92) * mm});
            skPoint(sketch, "E38.88.4.0", {"position": v(482.6, 46.57) * mm});
            skPoint(sketch, "E38.88.5.0", {"position": v(482.6, 40.22) * mm});
            skPoint(sketch, "E38.88.6.0", {"position": v(482.6, 33.87) * mm});
            skPoint(sketch, "E38.88.7.0", {"position": v(482.6, 27.52) * mm});
            skPoint(sketch, "E38.88.8.0", {"position": v(482.6, 21.17) * mm});
            skPoint(sketch, "E38.88.9.0", {"position": v(482.6, 14.82) * mm});
            skPoint(sketch, "E38.88.10.0", {"position": v(482.6, 8.47) * mm});
            skPoint(sketch, "E38.88.11.0", {"position": v(482.6, 2.12) * mm});
            skPoint(sketch, "E38.88.12.0", {"position": v(482.6, -4.23) * mm});
            skPoint(sketch, "E38.88.13.0", {"position": v(482.6, -10.58) * mm});
            skPoint(sketch, "E38.88.14.0", {"position": v(482.6, -16.93) * mm});
            skPoint(sketch, "E38.88.15.0", {"position": v(482.6, -23.28) * mm});
            skPoint(sketch, "E38.88.16.0", {"position": v(482.6, -29.63) * mm});
            skPoint(sketch, "E38.88.17.0", {"position": v(482.6, -35.98) * mm});
            skPoint(sketch, "E38.88.18.0", {"position": v(482.6, -42.33) * mm});
            skPoint(sketch, "E38.88.19.0", {"position": v(482.6, -48.68) * mm});
            skPoint(sketch, "E38.88.20.0", {"position": v(482.6, -55.03) * mm});
            skPoint(sketch, "E38.88.21.0", {"position": v(482.6, -61.38) * mm});
            skPoint(sketch, "E38.88.22.0", {"position": v(482.6, -67.73) * mm});
            skPoint(sketch, "E38.88.23.0", {"position": v(482.6, -74.08) * mm});
            skPoint(sketch, "E38.88.24.0", {"position": v(482.6, -80.43) * mm});
            skPoint(sketch, "E38.88.25.0", {"position": v(482.6, -86.78) * mm});
            skPoint(sketch, "E38.88.26.0", {"position": v(482.6, -93.13) * mm});
            skPoint(sketch, "E38.88.27.0", {"position": v(482.6, -99.48) * mm});
            skPoint(sketch, "E38.88.28.0", {"position": v(482.6, -105.83) * mm});
            skPoint(sketch, "E38.88.29.0", {"position": v(482.6, -112.18) * mm});
            skPoint(sketch, "E38.88.30.0", {"position": v(482.6, -118.53) * mm});
            skPoint(sketch, "E38.88.31.0", {"position": v(482.6, -124.88) * mm});
            skPoint(sketch, "E38.88.32.0", {"position": v(482.6, -131.23) * mm});
            skPoint(sketch, "E38.88.33.0", {"position": v(482.6, -137.58) * mm});
            skPoint(sketch, "E38.88.34.0", {"position": v(482.6, -143.93) * mm});
            skPoint(sketch, "E38.88.35.0", {"position": v(482.6, -150.28) * mm});
            skPoint(sketch, "E38.88.36.0", {"position": v(482.6, -156.63) * mm});
            skPoint(sketch, "E38.88.37.0", {"position": v(482.6, -162.98) * mm});
            skPoint(sketch, "E38.88.38.0", {"position": v(482.6, -169.33) * mm});
            skPoint(sketch, "E38.88.39.0", {"position": v(482.6, -175.68) * mm});
            skPoint(sketch, "E38.88.40.0", {"position": v(482.6, -182.03) * mm});
            skPoint(sketch, "E38.88.41.0", {"position": v(482.6, -188.38) * mm});
            skPoint(sketch, "E38.88.42.0", {"position": v(482.6, -194.73) * mm});
            skPoint(sketch, "E38.88.43.0", {"position": v(482.6, -201.08) * mm});
            skPoint(sketch, "E38.88.44.0", {"position": v(482.6, -207.43) * mm});
            skPoint(sketch, "E38.88.45.0", {"position": v(482.6, -213.78) * mm});
            skPoint(sketch, "E38.88.46.0", {"position": v(482.6, -220.13) * mm});
            skPoint(sketch, "E38.88.47.0", {"position": v(482.6, -226.48) * mm});
            skPoint(sketch, "E38.88.48.0", {"position": v(482.6, -232.83) * mm});
            skPoint(sketch, "E38.88.49.0", {"position": v(482.6, -239.18) * mm});
            skPoint(sketch, "E38.88.50.0", {"position": v(482.6, -245.53) * mm});
            skPoint(sketch, "E38.88.51.0", {"position": v(482.6, -251.88) * mm});
            skPoint(sketch, "E38.88.52.0", {"position": v(482.6, -258.23) * mm});
            skPoint(sketch, "E38.88.53.0", {"position": v(482.6, -264.58) * mm});
            skPoint(sketch, "E38.88.54.0", {"position": v(482.6, -270.93) * mm});
            skPoint(sketch, "E38.88.55.0", {"position": v(482.6, -277.28) * mm});
            skPoint(sketch, "E38.88.56.0", {"position": v(482.6, -283.63) * mm});
            skPoint(sketch, "E38.88.57.0", {"position": v(482.6, -289.98) * mm});
            skPoint(sketch, "E38.88.58.0", {"position": v(482.6, -296.33) * mm});
            skPoint(sketch, "E38.88.59.0", {"position": v(482.6, -302.68) * mm});
            skPoint(sketch, "E38.88.60.0", {"position": v(482.6, -309.03) * mm});
            skPoint(sketch, "E38.88.61.0", {"position": v(482.6, -315.38) * mm});
            skPoint(sketch, "E38.88.62.0", {"position": v(482.6, -321.73) * mm});
            skPoint(sketch, "E38.88.63.0", {"position": v(482.6, -328.08) * mm});
            skPoint(sketch, "E38.88.64.0", {"position": v(482.6, -334.43) * mm});
            skPoint(sketch, "E38.88.65.0", {"position": v(482.6, -340.78) * mm});
            skPoint(sketch, "E38.88.66.0", {"position": v(482.6, -347.13) * mm});
            skPoint(sketch, "E38.88.67.0", {"position": v(482.6, -353.48) * mm});
            skPoint(sketch, "E38.88.68.0", {"position": v(482.6, -359.83) * mm});
            skPoint(sketch, "E38.88.69.0", {"position": v(482.6, -366.18) * mm});
            skPoint(sketch, "E38.88.70.0", {"position": v(482.6, -372.53) * mm});
            skPoint(sketch, "E38.88.71.0", {"position": v(482.6, -378.88) * mm});
            skPoint(sketch, "E38.88.72.0", {"position": v(482.6, -385.23) * mm});
            skPoint(sketch, "E38.88.73.0", {"position": v(482.6, -391.58) * mm});
            skPoint(sketch, "E38.88.74.0", {"position": v(482.6, -397.93) * mm});
            skPoint(sketch, "E38.88.75.0", {"position": v(482.6, -404.28) * mm});
            skPoint(sketch, "E38.88.76.0", {"position": v(482.6, -410.63) * mm});
            skPoint(sketch, "E38.88.77.0", {"position": v(482.6, -416.98) * mm});
            skPoint(sketch, "E38.88.78.0", {"position": v(482.6, -423.33) * mm});
            skPoint(sketch, "E38.88.79.0", {"position": v(482.6, -429.68) * mm});
            skPoint(sketch, "E38.88.80.0", {"position": v(482.6, -436.03) * mm});
            skPoint(sketch, "E38.88.81.0", {"position": v(482.6, -442.38) * mm});
            skPoint(sketch, "E38.88.82.0", {"position": v(482.6, -448.73) * mm});
            skPoint(sketch, "E38.88.83.0", {"position": v(482.6, -455.08) * mm});
            skPoint(sketch, "E38.88.84.0", {"position": v(482.6, -461.43) * mm});
            skPoint(sketch, "E38.88.85.0", {"position": v(482.6, -467.78) * mm});
            skPoint(sketch, "E38.88.86.0", {"position": v(482.6, -474.13) * mm});
            skPoint(sketch, "E38.88.87.0", {"position": v(482.6, -480.48) * mm});
            skPoint(sketch, "E38.88.88.0", {"position": v(482.6, -486.83) * mm});
            skPoint(sketch, "E38.88.89.0", {"position": v(482.6, -493.18) * mm});
            skPoint(sketch, "E38.88.90.0", {"position": v(482.6, -499.53) * mm});
            skPoint(sketch, "E38.88.91.0", {"position": v(482.6, -505.88) * mm});
            skPoint(sketch, "E38.88.92.0", {"position": v(482.6, -512.23) * mm});
            skPoint(sketch, "E38.88.93.0", {"position": v(482.6, -518.58) * mm});
            skPoint(sketch, "E38.88.94.0", {"position": v(482.6, -524.93) * mm});
            skPoint(sketch, "E38.88.95.0", {"position": v(482.6, -531.28) * mm});
            skPoint(sketch, "E38.88.96.0", {"position": v(482.6, -537.63) * mm});
            skPoint(sketch, "E38.88.97.0", {"position": v(482.6, -543.98) * mm});
            skPoint(sketch, "E38.88.98.0", {"position": v(482.6, -550.33) * mm});
            skPoint(sketch, "E38.88.99.0", {"position": v(482.6, -556.68) * mm});
            skPoint(sketch, "E38.89.0.0", {"position": v(488.95, 71.97) * mm});
            skPoint(sketch, "E38.89.1.0", {"position": v(488.95, 65.62) * mm});
            skPoint(sketch, "E38.89.2.0", {"position": v(488.95, 59.27) * mm});
            skPoint(sketch, "E38.89.3.0", {"position": v(488.95, 52.92) * mm});
            skPoint(sketch, "E38.89.4.0", {"position": v(488.95, 46.57) * mm});
            skPoint(sketch, "E38.89.5.0", {"position": v(488.95, 40.22) * mm});
            skPoint(sketch, "E38.89.6.0", {"position": v(488.95, 33.87) * mm});
            skPoint(sketch, "E38.89.7.0", {"position": v(488.95, 27.52) * mm});
            skPoint(sketch, "E38.89.8.0", {"position": v(488.95, 21.17) * mm});
            skPoint(sketch, "E38.89.9.0", {"position": v(488.95, 14.82) * mm});
            skPoint(sketch, "E38.89.10.0", {"position": v(488.95, 8.47) * mm});
            skPoint(sketch, "E38.89.11.0", {"position": v(488.95, 2.12) * mm});
            skPoint(sketch, "E38.89.12.0", {"position": v(488.95, -4.23) * mm});
            skPoint(sketch, "E38.89.13.0", {"position": v(488.95, -10.58) * mm});
            skPoint(sketch, "E38.89.14.0", {"position": v(488.95, -16.93) * mm});
            skPoint(sketch, "E38.89.15.0", {"position": v(488.95, -23.28) * mm});
            skPoint(sketch, "E38.89.16.0", {"position": v(488.95, -29.63) * mm});
            skPoint(sketch, "E38.89.17.0", {"position": v(488.95, -35.98) * mm});
            skPoint(sketch, "E38.89.18.0", {"position": v(488.95, -42.33) * mm});
            skPoint(sketch, "E38.89.19.0", {"position": v(488.95, -48.68) * mm});
            skPoint(sketch, "E38.89.20.0", {"position": v(488.95, -55.03) * mm});
            skPoint(sketch, "E38.89.21.0", {"position": v(488.95, -61.38) * mm});
            skPoint(sketch, "E38.89.22.0", {"position": v(488.95, -67.73) * mm});
            skPoint(sketch, "E38.89.23.0", {"position": v(488.95, -74.08) * mm});
            skPoint(sketch, "E38.89.24.0", {"position": v(488.95, -80.43) * mm});
            skPoint(sketch, "E38.89.25.0", {"position": v(488.95, -86.78) * mm});
            skPoint(sketch, "E38.89.26.0", {"position": v(488.95, -93.13) * mm});
            skPoint(sketch, "E38.89.27.0", {"position": v(488.95, -99.48) * mm});
            skPoint(sketch, "E38.89.28.0", {"position": v(488.95, -105.83) * mm});
            skPoint(sketch, "E38.89.29.0", {"position": v(488.95, -112.18) * mm});
            skPoint(sketch, "E38.89.30.0", {"position": v(488.95, -118.53) * mm});
            skPoint(sketch, "E38.89.31.0", {"position": v(488.95, -124.88) * mm});
            skPoint(sketch, "E38.89.32.0", {"position": v(488.95, -131.23) * mm});
            skPoint(sketch, "E38.89.33.0", {"position": v(488.95, -137.58) * mm});
            skPoint(sketch, "E38.89.34.0", {"position": v(488.95, -143.93) * mm});
            skPoint(sketch, "E38.89.35.0", {"position": v(488.95, -150.28) * mm});
            skPoint(sketch, "E38.89.36.0", {"position": v(488.95, -156.63) * mm});
            skPoint(sketch, "E38.89.37.0", {"position": v(488.95, -162.98) * mm});
            skPoint(sketch, "E38.89.38.0", {"position": v(488.95, -169.33) * mm});
            skPoint(sketch, "E38.89.39.0", {"position": v(488.95, -175.68) * mm});
            skPoint(sketch, "E38.89.40.0", {"position": v(488.95, -182.03) * mm});
            skPoint(sketch, "E38.89.41.0", {"position": v(488.95, -188.38) * mm});
            skPoint(sketch, "E38.89.42.0", {"position": v(488.95, -194.73) * mm});
            skPoint(sketch, "E38.89.43.0", {"position": v(488.95, -201.08) * mm});
            skPoint(sketch, "E38.89.44.0", {"position": v(488.95, -207.43) * mm});
            skPoint(sketch, "E38.89.45.0", {"position": v(488.95, -213.78) * mm});
            skPoint(sketch, "E38.89.46.0", {"position": v(488.95, -220.13) * mm});
            skPoint(sketch, "E38.89.47.0", {"position": v(488.95, -226.48) * mm});
            skPoint(sketch, "E38.89.48.0", {"position": v(488.95, -232.83) * mm});
            skPoint(sketch, "E38.89.49.0", {"position": v(488.95, -239.18) * mm});
            skPoint(sketch, "E38.89.50.0", {"position": v(488.95, -245.53) * mm});
            skPoint(sketch, "E38.89.51.0", {"position": v(488.95, -251.88) * mm});
            skPoint(sketch, "E38.89.52.0", {"position": v(488.95, -258.23) * mm});
            skPoint(sketch, "E38.89.53.0", {"position": v(488.95, -264.58) * mm});
            skPoint(sketch, "E38.89.54.0", {"position": v(488.95, -270.93) * mm});
            skPoint(sketch, "E38.89.55.0", {"position": v(488.95, -277.28) * mm});
            skPoint(sketch, "E38.89.56.0", {"position": v(488.95, -283.63) * mm});
            skPoint(sketch, "E38.89.57.0", {"position": v(488.95, -289.98) * mm});
            skPoint(sketch, "E38.89.58.0", {"position": v(488.95, -296.33) * mm});
            skPoint(sketch, "E38.89.59.0", {"position": v(488.95, -302.68) * mm});
            skPoint(sketch, "E38.89.60.0", {"position": v(488.95, -309.03) * mm});
            skPoint(sketch, "E38.89.61.0", {"position": v(488.95, -315.38) * mm});
            skPoint(sketch, "E38.89.62.0", {"position": v(488.95, -321.73) * mm});
            skPoint(sketch, "E38.89.63.0", {"position": v(488.95, -328.08) * mm});
            skPoint(sketch, "E38.89.64.0", {"position": v(488.95, -334.43) * mm});
            skPoint(sketch, "E38.89.65.0", {"position": v(488.95, -340.78) * mm});
            skPoint(sketch, "E38.89.66.0", {"position": v(488.95, -347.13) * mm});
            skPoint(sketch, "E38.89.67.0", {"position": v(488.95, -353.48) * mm});
            skPoint(sketch, "E38.89.68.0", {"position": v(488.95, -359.83) * mm});
            skPoint(sketch, "E38.89.69.0", {"position": v(488.95, -366.18) * mm});
            skPoint(sketch, "E38.89.70.0", {"position": v(488.95, -372.53) * mm});
            skPoint(sketch, "E38.89.71.0", {"position": v(488.95, -378.88) * mm});
            skPoint(sketch, "E38.89.72.0", {"position": v(488.95, -385.23) * mm});
            skPoint(sketch, "E38.89.73.0", {"position": v(488.95, -391.58) * mm});
            skPoint(sketch, "E38.89.74.0", {"position": v(488.95, -397.93) * mm});
            skPoint(sketch, "E38.89.75.0", {"position": v(488.95, -404.28) * mm});
            skPoint(sketch, "E38.89.76.0", {"position": v(488.95, -410.63) * mm});
            skPoint(sketch, "E38.89.77.0", {"position": v(488.95, -416.98) * mm});
            skPoint(sketch, "E38.89.78.0", {"position": v(488.95, -423.33) * mm});
            skPoint(sketch, "E38.89.79.0", {"position": v(488.95, -429.68) * mm});
            skPoint(sketch, "E38.89.80.0", {"position": v(488.95, -436.03) * mm});
            skPoint(sketch, "E38.89.81.0", {"position": v(488.95, -442.38) * mm});
            skPoint(sketch, "E38.89.82.0", {"position": v(488.95, -448.73) * mm});
            skPoint(sketch, "E38.89.83.0", {"position": v(488.95, -455.08) * mm});
            skPoint(sketch, "E38.89.84.0", {"position": v(488.95, -461.43) * mm});
            skPoint(sketch, "E38.89.85.0", {"position": v(488.95, -467.78) * mm});
            skPoint(sketch, "E38.89.86.0", {"position": v(488.95, -474.13) * mm});
            skPoint(sketch, "E38.89.87.0", {"position": v(488.95, -480.48) * mm});
            skPoint(sketch, "E38.89.88.0", {"position": v(488.95, -486.83) * mm});
            skPoint(sketch, "E38.89.89.0", {"position": v(488.95, -493.18) * mm});
            skPoint(sketch, "E38.89.90.0", {"position": v(488.95, -499.53) * mm});
            skPoint(sketch, "E38.89.91.0", {"position": v(488.95, -505.88) * mm});
            skPoint(sketch, "E38.89.92.0", {"position": v(488.95, -512.23) * mm});
            skPoint(sketch, "E38.89.93.0", {"position": v(488.95, -518.58) * mm});
            skPoint(sketch, "E38.89.94.0", {"position": v(488.95, -524.93) * mm});
            skPoint(sketch, "E38.89.95.0", {"position": v(488.95, -531.28) * mm});
            skPoint(sketch, "E38.89.96.0", {"position": v(488.95, -537.63) * mm});
            skPoint(sketch, "E38.89.97.0", {"position": v(488.95, -543.98) * mm});
            skPoint(sketch, "E38.89.98.0", {"position": v(488.95, -550.33) * mm});
            skPoint(sketch, "E38.89.99.0", {"position": v(488.95, -556.68) * mm});
            skPoint(sketch, "E38.90.0.0", {"position": v(495.3, 71.97) * mm});
            skPoint(sketch, "E38.90.1.0", {"position": v(495.3, 65.62) * mm});
            skPoint(sketch, "E38.90.2.0", {"position": v(495.3, 59.27) * mm});
            skPoint(sketch, "E38.90.3.0", {"position": v(495.3, 52.92) * mm});
            skPoint(sketch, "E38.90.4.0", {"position": v(495.3, 46.57) * mm});
            skPoint(sketch, "E38.90.5.0", {"position": v(495.3, 40.22) * mm});
            skPoint(sketch, "E38.90.6.0", {"position": v(495.3, 33.87) * mm});
            skPoint(sketch, "E38.90.7.0", {"position": v(495.3, 27.52) * mm});
            skPoint(sketch, "E38.90.8.0", {"position": v(495.3, 21.17) * mm});
            skPoint(sketch, "E38.90.9.0", {"position": v(495.3, 14.82) * mm});
            skPoint(sketch, "E38.90.10.0", {"position": v(495.3, 8.47) * mm});
            skPoint(sketch, "E38.90.11.0", {"position": v(495.3, 2.12) * mm});
            skPoint(sketch, "E38.90.12.0", {"position": v(495.3, -4.23) * mm});
            skPoint(sketch, "E38.90.13.0", {"position": v(495.3, -10.58) * mm});
            skPoint(sketch, "E38.90.14.0", {"position": v(495.3, -16.93) * mm});
            skPoint(sketch, "E38.90.15.0", {"position": v(495.3, -23.28) * mm});
            skPoint(sketch, "E38.90.16.0", {"position": v(495.3, -29.63) * mm});
            skPoint(sketch, "E38.90.17.0", {"position": v(495.3, -35.98) * mm});
            skPoint(sketch, "E38.90.18.0", {"position": v(495.3, -42.33) * mm});
            skPoint(sketch, "E38.90.19.0", {"position": v(495.3, -48.68) * mm});
            skPoint(sketch, "E38.90.20.0", {"position": v(495.3, -55.03) * mm});
            skPoint(sketch, "E38.90.21.0", {"position": v(495.3, -61.38) * mm});
            skPoint(sketch, "E38.90.22.0", {"position": v(495.3, -67.73) * mm});
            skPoint(sketch, "E38.90.23.0", {"position": v(495.3, -74.08) * mm});
            skPoint(sketch, "E38.90.24.0", {"position": v(495.3, -80.43) * mm});
            skPoint(sketch, "E38.90.25.0", {"position": v(495.3, -86.78) * mm});
            skPoint(sketch, "E38.90.26.0", {"position": v(495.3, -93.13) * mm});
            skPoint(sketch, "E38.90.27.0", {"position": v(495.3, -99.48) * mm});
            skPoint(sketch, "E38.90.28.0", {"position": v(495.3, -105.83) * mm});
            skPoint(sketch, "E38.90.29.0", {"position": v(495.3, -112.18) * mm});
            skPoint(sketch, "E38.90.30.0", {"position": v(495.3, -118.53) * mm});
            skPoint(sketch, "E38.90.31.0", {"position": v(495.3, -124.88) * mm});
            skPoint(sketch, "E38.90.32.0", {"position": v(495.3, -131.23) * mm});
            skPoint(sketch, "E38.90.33.0", {"position": v(495.3, -137.58) * mm});
            skPoint(sketch, "E38.90.34.0", {"position": v(495.3, -143.93) * mm});
            skPoint(sketch, "E38.90.35.0", {"position": v(495.3, -150.28) * mm});
            skPoint(sketch, "E38.90.36.0", {"position": v(495.3, -156.63) * mm});
            skPoint(sketch, "E38.90.37.0", {"position": v(495.3, -162.98) * mm});
            skPoint(sketch, "E38.90.38.0", {"position": v(495.3, -169.33) * mm});
            skPoint(sketch, "E38.90.39.0", {"position": v(495.3, -175.68) * mm});
            skPoint(sketch, "E38.90.40.0", {"position": v(495.3, -182.03) * mm});
            skPoint(sketch, "E38.90.41.0", {"position": v(495.3, -188.38) * mm});
            skPoint(sketch, "E38.90.42.0", {"position": v(495.3, -194.73) * mm});
            skPoint(sketch, "E38.90.43.0", {"position": v(495.3, -201.08) * mm});
            skPoint(sketch, "E38.90.44.0", {"position": v(495.3, -207.43) * mm});
            skPoint(sketch, "E38.90.45.0", {"position": v(495.3, -213.78) * mm});
            skPoint(sketch, "E38.90.46.0", {"position": v(495.3, -220.13) * mm});
            skPoint(sketch, "E38.90.47.0", {"position": v(495.3, -226.48) * mm});
            skPoint(sketch, "E38.90.48.0", {"position": v(495.3, -232.83) * mm});
            skPoint(sketch, "E38.90.49.0", {"position": v(495.3, -239.18) * mm});
            skPoint(sketch, "E38.90.50.0", {"position": v(495.3, -245.53) * mm});
            skPoint(sketch, "E38.90.51.0", {"position": v(495.3, -251.88) * mm});
            skPoint(sketch, "E38.90.52.0", {"position": v(495.3, -258.23) * mm});
            skPoint(sketch, "E38.90.53.0", {"position": v(495.3, -264.58) * mm});
            skPoint(sketch, "E38.90.54.0", {"position": v(495.3, -270.93) * mm});
            skPoint(sketch, "E38.90.55.0", {"position": v(495.3, -277.28) * mm});
            skPoint(sketch, "E38.90.56.0", {"position": v(495.3, -283.63) * mm});
            skPoint(sketch, "E38.90.57.0", {"position": v(495.3, -289.98) * mm});
            skPoint(sketch, "E38.90.58.0", {"position": v(495.3, -296.33) * mm});
            skPoint(sketch, "E38.90.59.0", {"position": v(495.3, -302.68) * mm});
            skPoint(sketch, "E38.90.60.0", {"position": v(495.3, -309.03) * mm});
            skPoint(sketch, "E38.90.61.0", {"position": v(495.3, -315.38) * mm});
            skPoint(sketch, "E38.90.62.0", {"position": v(495.3, -321.73) * mm});
            skPoint(sketch, "E38.90.63.0", {"position": v(495.3, -328.08) * mm});
            skPoint(sketch, "E38.90.64.0", {"position": v(495.3, -334.43) * mm});
            skPoint(sketch, "E38.90.65.0", {"position": v(495.3, -340.78) * mm});
            skPoint(sketch, "E38.90.66.0", {"position": v(495.3, -347.13) * mm});
            skPoint(sketch, "E38.90.67.0", {"position": v(495.3, -353.48) * mm});
            skPoint(sketch, "E38.90.68.0", {"position": v(495.3, -359.83) * mm});
            skPoint(sketch, "E38.90.69.0", {"position": v(495.3, -366.18) * mm});
            skPoint(sketch, "E38.90.70.0", {"position": v(495.3, -372.53) * mm});
            skPoint(sketch, "E38.90.71.0", {"position": v(495.3, -378.88) * mm});
            skPoint(sketch, "E38.90.72.0", {"position": v(495.3, -385.23) * mm});
            skPoint(sketch, "E38.90.73.0", {"position": v(495.3, -391.58) * mm});
            skPoint(sketch, "E38.90.74.0", {"position": v(495.3, -397.93) * mm});
            skPoint(sketch, "E38.90.75.0", {"position": v(495.3, -404.28) * mm});
            skPoint(sketch, "E38.90.76.0", {"position": v(495.3, -410.63) * mm});
            skPoint(sketch, "E38.90.77.0", {"position": v(495.3, -416.98) * mm});
            skPoint(sketch, "E38.90.78.0", {"position": v(495.3, -423.33) * mm});
            skPoint(sketch, "E38.90.79.0", {"position": v(495.3, -429.68) * mm});
            skPoint(sketch, "E38.90.80.0", {"position": v(495.3, -436.03) * mm});
            skPoint(sketch, "E38.90.81.0", {"position": v(495.3, -442.38) * mm});
            skPoint(sketch, "E38.90.82.0", {"position": v(495.3, -448.73) * mm});
            skPoint(sketch, "E38.90.83.0", {"position": v(495.3, -455.08) * mm});
            skPoint(sketch, "E38.90.84.0", {"position": v(495.3, -461.43) * mm});
            skPoint(sketch, "E38.90.85.0", {"position": v(495.3, -467.78) * mm});
            skPoint(sketch, "E38.90.86.0", {"position": v(495.3, -474.13) * mm});
            skPoint(sketch, "E38.90.87.0", {"position": v(495.3, -480.48) * mm});
            skPoint(sketch, "E38.90.88.0", {"position": v(495.3, -486.83) * mm});
            skPoint(sketch, "E38.90.89.0", {"position": v(495.3, -493.18) * mm});
            skPoint(sketch, "E38.90.90.0", {"position": v(495.3, -499.53) * mm});
            skPoint(sketch, "E38.90.91.0", {"position": v(495.3, -505.88) * mm});
            skPoint(sketch, "E38.90.92.0", {"position": v(495.3, -512.23) * mm});
            skPoint(sketch, "E38.90.93.0", {"position": v(495.3, -518.58) * mm});
            skPoint(sketch, "E38.90.94.0", {"position": v(495.3, -524.93) * mm});
            skPoint(sketch, "E38.90.95.0", {"position": v(495.3, -531.28) * mm});
            skPoint(sketch, "E38.90.96.0", {"position": v(495.3, -537.63) * mm});
            skPoint(sketch, "E38.90.97.0", {"position": v(495.3, -543.98) * mm});
            skPoint(sketch, "E38.90.98.0", {"position": v(495.3, -550.33) * mm});
            skPoint(sketch, "E38.90.99.0", {"position": v(495.3, -556.68) * mm});
            skPoint(sketch, "E38.91.0.0", {"position": v(501.65, 71.97) * mm});
            skPoint(sketch, "E38.91.1.0", {"position": v(501.65, 65.62) * mm});
            skPoint(sketch, "E38.91.2.0", {"position": v(501.65, 59.27) * mm});
            skPoint(sketch, "E38.91.3.0", {"position": v(501.65, 52.92) * mm});
            skPoint(sketch, "E38.91.4.0", {"position": v(501.65, 46.57) * mm});
            skPoint(sketch, "E38.91.5.0", {"position": v(501.65, 40.22) * mm});
            skPoint(sketch, "E38.91.6.0", {"position": v(501.65, 33.87) * mm});
            skPoint(sketch, "E38.91.7.0", {"position": v(501.65, 27.52) * mm});
            skPoint(sketch, "E38.91.8.0", {"position": v(501.65, 21.17) * mm});
            skPoint(sketch, "E38.91.9.0", {"position": v(501.65, 14.82) * mm});
            skPoint(sketch, "E38.91.10.0", {"position": v(501.65, 8.47) * mm});
            skPoint(sketch, "E38.91.11.0", {"position": v(501.65, 2.12) * mm});
            skPoint(sketch, "E38.91.12.0", {"position": v(501.65, -4.23) * mm});
            skPoint(sketch, "E38.91.13.0", {"position": v(501.65, -10.58) * mm});
            skPoint(sketch, "E38.91.14.0", {"position": v(501.65, -16.93) * mm});
            skPoint(sketch, "E38.91.15.0", {"position": v(501.65, -23.28) * mm});
            skPoint(sketch, "E38.91.16.0", {"position": v(501.65, -29.63) * mm});
            skPoint(sketch, "E38.91.17.0", {"position": v(501.65, -35.98) * mm});
            skPoint(sketch, "E38.91.18.0", {"position": v(501.65, -42.33) * mm});
            skPoint(sketch, "E38.91.19.0", {"position": v(501.65, -48.68) * mm});
            skPoint(sketch, "E38.91.20.0", {"position": v(501.65, -55.03) * mm});
            skPoint(sketch, "E38.91.21.0", {"position": v(501.65, -61.38) * mm});
            skPoint(sketch, "E38.91.22.0", {"position": v(501.65, -67.73) * mm});
            skPoint(sketch, "E38.91.23.0", {"position": v(501.65, -74.08) * mm});
            skPoint(sketch, "E38.91.24.0", {"position": v(501.65, -80.43) * mm});
            skPoint(sketch, "E38.91.25.0", {"position": v(501.65, -86.78) * mm});
            skPoint(sketch, "E38.91.26.0", {"position": v(501.65, -93.13) * mm});
            skPoint(sketch, "E38.91.27.0", {"position": v(501.65, -99.48) * mm});
            skPoint(sketch, "E38.91.28.0", {"position": v(501.65, -105.83) * mm});
            skPoint(sketch, "E38.91.29.0", {"position": v(501.65, -112.18) * mm});
            skPoint(sketch, "E38.91.30.0", {"position": v(501.65, -118.53) * mm});
            skPoint(sketch, "E38.91.31.0", {"position": v(501.65, -124.88) * mm});
            skPoint(sketch, "E38.91.32.0", {"position": v(501.65, -131.23) * mm});
            skPoint(sketch, "E38.91.33.0", {"position": v(501.65, -137.58) * mm});
            skPoint(sketch, "E38.91.34.0", {"position": v(501.65, -143.93) * mm});
            skPoint(sketch, "E38.91.35.0", {"position": v(501.65, -150.28) * mm});
            skPoint(sketch, "E38.91.36.0", {"position": v(501.65, -156.63) * mm});
            skPoint(sketch, "E38.91.37.0", {"position": v(501.65, -162.98) * mm});
            skPoint(sketch, "E38.91.38.0", {"position": v(501.65, -169.33) * mm});
            skPoint(sketch, "E38.91.39.0", {"position": v(501.65, -175.68) * mm});
            skPoint(sketch, "E38.91.40.0", {"position": v(501.65, -182.03) * mm});
            skPoint(sketch, "E38.91.41.0", {"position": v(501.65, -188.38) * mm});
            skPoint(sketch, "E38.91.42.0", {"position": v(501.65, -194.73) * mm});
            skPoint(sketch, "E38.91.43.0", {"position": v(501.65, -201.08) * mm});
            skPoint(sketch, "E38.91.44.0", {"position": v(501.65, -207.43) * mm});
            skPoint(sketch, "E38.91.45.0", {"position": v(501.65, -213.78) * mm});
            skPoint(sketch, "E38.91.46.0", {"position": v(501.65, -220.13) * mm});
            skPoint(sketch, "E38.91.47.0", {"position": v(501.65, -226.48) * mm});
            skPoint(sketch, "E38.91.48.0", {"position": v(501.65, -232.83) * mm});
            skPoint(sketch, "E38.91.49.0", {"position": v(501.65, -239.18) * mm});
            skPoint(sketch, "E38.91.50.0", {"position": v(501.65, -245.53) * mm});
            skPoint(sketch, "E38.91.51.0", {"position": v(501.65, -251.88) * mm});
            skPoint(sketch, "E38.91.52.0", {"position": v(501.65, -258.23) * mm});
            skPoint(sketch, "E38.91.53.0", {"position": v(501.65, -264.58) * mm});
            skPoint(sketch, "E38.91.54.0", {"position": v(501.65, -270.93) * mm});
            skPoint(sketch, "E38.91.55.0", {"position": v(501.65, -277.28) * mm});
            skPoint(sketch, "E38.91.56.0", {"position": v(501.65, -283.63) * mm});
            skPoint(sketch, "E38.91.57.0", {"position": v(501.65, -289.98) * mm});
            skPoint(sketch, "E38.91.58.0", {"position": v(501.65, -296.33) * mm});
            skPoint(sketch, "E38.91.59.0", {"position": v(501.65, -302.68) * mm});
            skPoint(sketch, "E38.91.60.0", {"position": v(501.65, -309.03) * mm});
            skPoint(sketch, "E38.91.61.0", {"position": v(501.65, -315.38) * mm});
            skPoint(sketch, "E38.91.62.0", {"position": v(501.65, -321.73) * mm});
            skPoint(sketch, "E38.91.63.0", {"position": v(501.65, -328.08) * mm});
            skPoint(sketch, "E38.91.64.0", {"position": v(501.65, -334.43) * mm});
            skPoint(sketch, "E38.91.65.0", {"position": v(501.65, -340.78) * mm});
            skPoint(sketch, "E38.91.66.0", {"position": v(501.65, -347.13) * mm});
            skPoint(sketch, "E38.91.67.0", {"position": v(501.65, -353.48) * mm});
            skPoint(sketch, "E38.91.68.0", {"position": v(501.65, -359.83) * mm});
            skPoint(sketch, "E38.91.69.0", {"position": v(501.65, -366.18) * mm});
            skPoint(sketch, "E38.91.70.0", {"position": v(501.65, -372.53) * mm});
            skPoint(sketch, "E38.91.71.0", {"position": v(501.65, -378.88) * mm});
            skPoint(sketch, "E38.91.72.0", {"position": v(501.65, -385.23) * mm});
            skPoint(sketch, "E38.91.73.0", {"position": v(501.65, -391.58) * mm});
            skPoint(sketch, "E38.91.74.0", {"position": v(501.65, -397.93) * mm});
            skPoint(sketch, "E38.91.75.0", {"position": v(501.65, -404.28) * mm});
            skPoint(sketch, "E38.91.76.0", {"position": v(501.65, -410.63) * mm});
            skPoint(sketch, "E38.91.77.0", {"position": v(501.65, -416.98) * mm});
            skPoint(sketch, "E38.91.78.0", {"position": v(501.65, -423.33) * mm});
            skPoint(sketch, "E38.91.79.0", {"position": v(501.65, -429.68) * mm});
            skPoint(sketch, "E38.91.80.0", {"position": v(501.65, -436.03) * mm});
            skPoint(sketch, "E38.91.81.0", {"position": v(501.65, -442.38) * mm});
            skPoint(sketch, "E38.91.82.0", {"position": v(501.65, -448.73) * mm});
            skPoint(sketch, "E38.91.83.0", {"position": v(501.65, -455.08) * mm});
            skPoint(sketch, "E38.91.84.0", {"position": v(501.65, -461.43) * mm});
            skPoint(sketch, "E38.91.85.0", {"position": v(501.65, -467.78) * mm});
            skPoint(sketch, "E38.91.86.0", {"position": v(501.65, -474.13) * mm});
            skPoint(sketch, "E38.91.87.0", {"position": v(501.65, -480.48) * mm});
            skPoint(sketch, "E38.91.88.0", {"position": v(501.65, -486.83) * mm});
            skPoint(sketch, "E38.91.89.0", {"position": v(501.65, -493.18) * mm});
            skPoint(sketch, "E38.91.90.0", {"position": v(501.65, -499.53) * mm});
            skPoint(sketch, "E38.91.91.0", {"position": v(501.65, -505.88) * mm});
            skPoint(sketch, "E38.91.92.0", {"position": v(501.65, -512.23) * mm});
            skPoint(sketch, "E38.91.93.0", {"position": v(501.65, -518.58) * mm});
            skPoint(sketch, "E38.91.94.0", {"position": v(501.65, -524.93) * mm});
            skPoint(sketch, "E38.91.95.0", {"position": v(501.65, -531.28) * mm});
            skPoint(sketch, "E38.91.96.0", {"position": v(501.65, -537.63) * mm});
            skPoint(sketch, "E38.91.97.0", {"position": v(501.65, -543.98) * mm});
            skPoint(sketch, "E38.91.98.0", {"position": v(501.65, -550.33) * mm});
            skPoint(sketch, "E38.91.99.0", {"position": v(501.65, -556.68) * mm});
            skPoint(sketch, "E38.92.0.0", {"position": v(508, 71.97) * mm});
            skPoint(sketch, "E38.92.1.0", {"position": v(508, 65.62) * mm});
            skPoint(sketch, "E38.92.2.0", {"position": v(508, 59.27) * mm});
            skPoint(sketch, "E38.92.3.0", {"position": v(508, 52.92) * mm});
            skPoint(sketch, "E38.92.4.0", {"position": v(508, 46.57) * mm});
            skPoint(sketch, "E38.92.5.0", {"position": v(508, 40.22) * mm});
            skPoint(sketch, "E38.92.6.0", {"position": v(508, 33.87) * mm});
            skPoint(sketch, "E38.92.7.0", {"position": v(508, 27.52) * mm});
            skPoint(sketch, "E38.92.8.0", {"position": v(508, 21.17) * mm});
            skPoint(sketch, "E38.92.9.0", {"position": v(508, 14.82) * mm});
            skPoint(sketch, "E38.92.10.0", {"position": v(508, 8.47) * mm});
            skPoint(sketch, "E38.92.11.0", {"position": v(508, 2.12) * mm});
            skPoint(sketch, "E38.92.12.0", {"position": v(508, -4.23) * mm});
            skPoint(sketch, "E38.92.13.0", {"position": v(508, -10.58) * mm});
            skPoint(sketch, "E38.92.14.0", {"position": v(508, -16.93) * mm});
            skPoint(sketch, "E38.92.15.0", {"position": v(508, -23.28) * mm});
            skPoint(sketch, "E38.92.16.0", {"position": v(508, -29.63) * mm});
            skPoint(sketch, "E38.92.17.0", {"position": v(508, -35.98) * mm});
            skPoint(sketch, "E38.92.18.0", {"position": v(508, -42.33) * mm});
            skPoint(sketch, "E38.92.19.0", {"position": v(508, -48.68) * mm});
            skPoint(sketch, "E38.92.20.0", {"position": v(508, -55.03) * mm});
            skPoint(sketch, "E38.92.21.0", {"position": v(508, -61.38) * mm});
            skPoint(sketch, "E38.92.22.0", {"position": v(508, -67.73) * mm});
            skPoint(sketch, "E38.92.23.0", {"position": v(508, -74.08) * mm});
            skPoint(sketch, "E38.92.24.0", {"position": v(508, -80.43) * mm});
            skPoint(sketch, "E38.92.25.0", {"position": v(508, -86.78) * mm});
            skPoint(sketch, "E38.92.26.0", {"position": v(508, -93.13) * mm});
            skPoint(sketch, "E38.92.27.0", {"position": v(508, -99.48) * mm});
            skPoint(sketch, "E38.92.28.0", {"position": v(508, -105.83) * mm});
            skPoint(sketch, "E38.92.29.0", {"position": v(508, -112.18) * mm});
            skPoint(sketch, "E38.92.30.0", {"position": v(508, -118.53) * mm});
            skPoint(sketch, "E38.92.31.0", {"position": v(508, -124.88) * mm});
            skPoint(sketch, "E38.92.32.0", {"position": v(508, -131.23) * mm});
            skPoint(sketch, "E38.92.33.0", {"position": v(508, -137.58) * mm});
            skPoint(sketch, "E38.92.34.0", {"position": v(508, -143.93) * mm});
            skPoint(sketch, "E38.92.35.0", {"position": v(508, -150.28) * mm});
            skPoint(sketch, "E38.92.36.0", {"position": v(508, -156.63) * mm});
            skPoint(sketch, "E38.92.37.0", {"position": v(508, -162.98) * mm});
            skPoint(sketch, "E38.92.38.0", {"position": v(508, -169.33) * mm});
            skPoint(sketch, "E38.92.39.0", {"position": v(508, -175.68) * mm});
            skPoint(sketch, "E38.92.40.0", {"position": v(508, -182.03) * mm});
            skPoint(sketch, "E38.92.41.0", {"position": v(508, -188.38) * mm});
            skPoint(sketch, "E38.92.42.0", {"position": v(508, -194.73) * mm});
            skPoint(sketch, "E38.92.43.0", {"position": v(508, -201.08) * mm});
            skPoint(sketch, "E38.92.44.0", {"position": v(508, -207.43) * mm});
            skPoint(sketch, "E38.92.45.0", {"position": v(508, -213.78) * mm});
            skPoint(sketch, "E38.92.46.0", {"position": v(508, -220.13) * mm});
            skPoint(sketch, "E38.92.47.0", {"position": v(508, -226.48) * mm});
            skPoint(sketch, "E38.92.48.0", {"position": v(508, -232.83) * mm});
            skPoint(sketch, "E38.92.49.0", {"position": v(508, -239.18) * mm});
            skPoint(sketch, "E38.92.50.0", {"position": v(508, -245.53) * mm});
            skPoint(sketch, "E38.92.51.0", {"position": v(508, -251.88) * mm});
            skPoint(sketch, "E38.92.52.0", {"position": v(508, -258.23) * mm});
            skPoint(sketch, "E38.92.53.0", {"position": v(508, -264.58) * mm});
            skPoint(sketch, "E38.92.54.0", {"position": v(508, -270.93) * mm});
            skPoint(sketch, "E38.92.55.0", {"position": v(508, -277.28) * mm});
            skPoint(sketch, "E38.92.56.0", {"position": v(508, -283.63) * mm});
            skPoint(sketch, "E38.92.57.0", {"position": v(508, -289.98) * mm});
            skPoint(sketch, "E38.92.58.0", {"position": v(508, -296.33) * mm});
            skPoint(sketch, "E38.92.59.0", {"position": v(508, -302.68) * mm});
            skPoint(sketch, "E38.92.60.0", {"position": v(508, -309.03) * mm});
            skPoint(sketch, "E38.92.61.0", {"position": v(508, -315.38) * mm});
            skPoint(sketch, "E38.92.62.0", {"position": v(508, -321.73) * mm});
            skPoint(sketch, "E38.92.63.0", {"position": v(508, -328.08) * mm});
            skPoint(sketch, "E38.92.64.0", {"position": v(508, -334.43) * mm});
            skPoint(sketch, "E38.92.65.0", {"position": v(508, -340.78) * mm});
            skPoint(sketch, "E38.92.66.0", {"position": v(508, -347.13) * mm});
            skPoint(sketch, "E38.92.67.0", {"position": v(508, -353.48) * mm});
            skPoint(sketch, "E38.92.68.0", {"position": v(508, -359.83) * mm});
            skPoint(sketch, "E38.92.69.0", {"position": v(508, -366.18) * mm});
            skPoint(sketch, "E38.92.70.0", {"position": v(508, -372.53) * mm});
            skPoint(sketch, "E38.92.71.0", {"position": v(508, -378.88) * mm});
            skPoint(sketch, "E38.92.72.0", {"position": v(508, -385.23) * mm});
            skPoint(sketch, "E38.92.73.0", {"position": v(508, -391.58) * mm});
            skPoint(sketch, "E38.92.74.0", {"position": v(508, -397.93) * mm});
            skPoint(sketch, "E38.92.75.0", {"position": v(508, -404.28) * mm});
            skPoint(sketch, "E38.92.76.0", {"position": v(508, -410.63) * mm});
            skPoint(sketch, "E38.92.77.0", {"position": v(508, -416.98) * mm});
            skPoint(sketch, "E38.92.78.0", {"position": v(508, -423.33) * mm});
            skPoint(sketch, "E38.92.79.0", {"position": v(508, -429.68) * mm});
            skPoint(sketch, "E38.92.80.0", {"position": v(508, -436.03) * mm});
            skPoint(sketch, "E38.92.81.0", {"position": v(508, -442.38) * mm});
            skPoint(sketch, "E38.92.82.0", {"position": v(508, -448.73) * mm});
            skPoint(sketch, "E38.92.83.0", {"position": v(508, -455.08) * mm});
            skPoint(sketch, "E38.92.84.0", {"position": v(508, -461.43) * mm});
            skPoint(sketch, "E38.92.85.0", {"position": v(508, -467.78) * mm});
            skPoint(sketch, "E38.92.86.0", {"position": v(508, -474.13) * mm});
            skPoint(sketch, "E38.92.87.0", {"position": v(508, -480.48) * mm});
            skPoint(sketch, "E38.92.88.0", {"position": v(508, -486.83) * mm});
            skPoint(sketch, "E38.92.89.0", {"position": v(508, -493.18) * mm});
            skPoint(sketch, "E38.92.90.0", {"position": v(508, -499.53) * mm});
            skPoint(sketch, "E38.92.91.0", {"position": v(508, -505.88) * mm});
            skPoint(sketch, "E38.92.92.0", {"position": v(508, -512.23) * mm});
            skPoint(sketch, "E38.92.93.0", {"position": v(508, -518.58) * mm});
            skPoint(sketch, "E38.92.94.0", {"position": v(508, -524.93) * mm});
            skPoint(sketch, "E38.92.95.0", {"position": v(508, -531.28) * mm});
            skPoint(sketch, "E38.92.96.0", {"position": v(508, -537.63) * mm});
            skPoint(sketch, "E38.92.97.0", {"position": v(508, -543.98) * mm});
            skPoint(sketch, "E38.92.98.0", {"position": v(508, -550.33) * mm});
            skPoint(sketch, "E38.92.99.0", {"position": v(508, -556.68) * mm});
            skPoint(sketch, "E38.93.0.0", {"position": v(514.35, 71.97) * mm});
            skPoint(sketch, "E38.93.1.0", {"position": v(514.35, 65.62) * mm});
            skPoint(sketch, "E38.93.2.0", {"position": v(514.35, 59.27) * mm});
            skPoint(sketch, "E38.93.3.0", {"position": v(514.35, 52.92) * mm});
            skPoint(sketch, "E38.93.4.0", {"position": v(514.35, 46.57) * mm});
            skPoint(sketch, "E38.93.5.0", {"position": v(514.35, 40.22) * mm});
            skPoint(sketch, "E38.93.6.0", {"position": v(514.35, 33.87) * mm});
            skPoint(sketch, "E38.93.7.0", {"position": v(514.35, 27.52) * mm});
            skPoint(sketch, "E38.93.8.0", {"position": v(514.35, 21.17) * mm});
            skPoint(sketch, "E38.93.9.0", {"position": v(514.35, 14.82) * mm});
            skPoint(sketch, "E38.93.10.0", {"position": v(514.35, 8.47) * mm});
            skPoint(sketch, "E38.93.11.0", {"position": v(514.35, 2.12) * mm});
            skPoint(sketch, "E38.93.12.0", {"position": v(514.35, -4.23) * mm});
            skPoint(sketch, "E38.93.13.0", {"position": v(514.35, -10.58) * mm});
            skPoint(sketch, "E38.93.14.0", {"position": v(514.35, -16.93) * mm});
            skPoint(sketch, "E38.93.15.0", {"position": v(514.35, -23.28) * mm});
            skPoint(sketch, "E38.93.16.0", {"position": v(514.35, -29.63) * mm});
            skPoint(sketch, "E38.93.17.0", {"position": v(514.35, -35.98) * mm});
            skPoint(sketch, "E38.93.18.0", {"position": v(514.35, -42.33) * mm});
            skPoint(sketch, "E38.93.19.0", {"position": v(514.35, -48.68) * mm});
            skPoint(sketch, "E38.93.20.0", {"position": v(514.35, -55.03) * mm});
            skPoint(sketch, "E38.93.21.0", {"position": v(514.35, -61.38) * mm});
            skPoint(sketch, "E38.93.22.0", {"position": v(514.35, -67.73) * mm});
            skPoint(sketch, "E38.93.23.0", {"position": v(514.35, -74.08) * mm});
            skPoint(sketch, "E38.93.24.0", {"position": v(514.35, -80.43) * mm});
            skPoint(sketch, "E38.93.25.0", {"position": v(514.35, -86.78) * mm});
            skPoint(sketch, "E38.93.26.0", {"position": v(514.35, -93.13) * mm});
            skPoint(sketch, "E38.93.27.0", {"position": v(514.35, -99.48) * mm});
            skPoint(sketch, "E38.93.28.0", {"position": v(514.35, -105.83) * mm});
            skPoint(sketch, "E38.93.29.0", {"position": v(514.35, -112.18) * mm});
            skPoint(sketch, "E38.93.30.0", {"position": v(514.35, -118.53) * mm});
            skPoint(sketch, "E38.93.31.0", {"position": v(514.35, -124.88) * mm});
            skPoint(sketch, "E38.93.32.0", {"position": v(514.35, -131.23) * mm});
            skPoint(sketch, "E38.93.33.0", {"position": v(514.35, -137.58) * mm});
            skPoint(sketch, "E38.93.34.0", {"position": v(514.35, -143.93) * mm});
            skPoint(sketch, "E38.93.35.0", {"position": v(514.35, -150.28) * mm});
            skPoint(sketch, "E38.93.36.0", {"position": v(514.35, -156.63) * mm});
            skPoint(sketch, "E38.93.37.0", {"position": v(514.35, -162.98) * mm});
            skPoint(sketch, "E38.93.38.0", {"position": v(514.35, -169.33) * mm});
            skPoint(sketch, "E38.93.39.0", {"position": v(514.35, -175.68) * mm});
            skPoint(sketch, "E38.93.40.0", {"position": v(514.35, -182.03) * mm});
            skPoint(sketch, "E38.93.41.0", {"position": v(514.35, -188.38) * mm});
            skPoint(sketch, "E38.93.42.0", {"position": v(514.35, -194.73) * mm});
            skPoint(sketch, "E38.93.43.0", {"position": v(514.35, -201.08) * mm});
            skPoint(sketch, "E38.93.44.0", {"position": v(514.35, -207.43) * mm});
            skPoint(sketch, "E38.93.45.0", {"position": v(514.35, -213.78) * mm});
            skPoint(sketch, "E38.93.46.0", {"position": v(514.35, -220.13) * mm});
            skPoint(sketch, "E38.93.47.0", {"position": v(514.35, -226.48) * mm});
            skPoint(sketch, "E38.93.48.0", {"position": v(514.35, -232.83) * mm});
            skPoint(sketch, "E38.93.49.0", {"position": v(514.35, -239.18) * mm});
            skPoint(sketch, "E38.93.50.0", {"position": v(514.35, -245.53) * mm});
            skPoint(sketch, "E38.93.51.0", {"position": v(514.35, -251.88) * mm});
            skPoint(sketch, "E38.93.52.0", {"position": v(514.35, -258.23) * mm});
            skPoint(sketch, "E38.93.53.0", {"position": v(514.35, -264.58) * mm});
            skPoint(sketch, "E38.93.54.0", {"position": v(514.35, -270.93) * mm});
            skPoint(sketch, "E38.93.55.0", {"position": v(514.35, -277.28) * mm});
            skPoint(sketch, "E38.93.56.0", {"position": v(514.35, -283.63) * mm});
            skPoint(sketch, "E38.93.57.0", {"position": v(514.35, -289.98) * mm});
            skPoint(sketch, "E38.93.58.0", {"position": v(514.35, -296.33) * mm});
            skPoint(sketch, "E38.93.59.0", {"position": v(514.35, -302.68) * mm});
            skPoint(sketch, "E38.93.60.0", {"position": v(514.35, -309.03) * mm});
            skPoint(sketch, "E38.93.61.0", {"position": v(514.35, -315.38) * mm});
            skPoint(sketch, "E38.93.62.0", {"position": v(514.35, -321.73) * mm});
            skPoint(sketch, "E38.93.63.0", {"position": v(514.35, -328.08) * mm});
            skPoint(sketch, "E38.93.64.0", {"position": v(514.35, -334.43) * mm});
            skPoint(sketch, "E38.93.65.0", {"position": v(514.35, -340.78) * mm});
            skPoint(sketch, "E38.93.66.0", {"position": v(514.35, -347.13) * mm});
            skPoint(sketch, "E38.93.67.0", {"position": v(514.35, -353.48) * mm});
            skPoint(sketch, "E38.93.68.0", {"position": v(514.35, -359.83) * mm});
            skPoint(sketch, "E38.93.69.0", {"position": v(514.35, -366.18) * mm});
            skPoint(sketch, "E38.93.70.0", {"position": v(514.35, -372.53) * mm});
            skPoint(sketch, "E38.93.71.0", {"position": v(514.35, -378.88) * mm});
            skPoint(sketch, "E38.93.72.0", {"position": v(514.35, -385.23) * mm});
            skPoint(sketch, "E38.93.73.0", {"position": v(514.35, -391.58) * mm});
            skPoint(sketch, "E38.93.74.0", {"position": v(514.35, -397.93) * mm});
            skPoint(sketch, "E38.93.75.0", {"position": v(514.35, -404.28) * mm});
            skPoint(sketch, "E38.93.76.0", {"position": v(514.35, -410.63) * mm});
            skPoint(sketch, "E38.93.77.0", {"position": v(514.35, -416.98) * mm});
            skPoint(sketch, "E38.93.78.0", {"position": v(514.35, -423.33) * mm});
            skPoint(sketch, "E38.93.79.0", {"position": v(514.35, -429.68) * mm});
            skPoint(sketch, "E38.93.80.0", {"position": v(514.35, -436.03) * mm});
            skPoint(sketch, "E38.93.81.0", {"position": v(514.35, -442.38) * mm});
            skPoint(sketch, "E38.93.82.0", {"position": v(514.35, -448.73) * mm});
            skPoint(sketch, "E38.93.83.0", {"position": v(514.35, -455.08) * mm});
            skPoint(sketch, "E38.93.84.0", {"position": v(514.35, -461.43) * mm});
            skPoint(sketch, "E38.93.85.0", {"position": v(514.35, -467.78) * mm});
            skPoint(sketch, "E38.93.86.0", {"position": v(514.35, -474.13) * mm});
            skPoint(sketch, "E38.93.87.0", {"position": v(514.35, -480.48) * mm});
            skPoint(sketch, "E38.93.88.0", {"position": v(514.35, -486.83) * mm});
            skPoint(sketch, "E38.93.89.0", {"position": v(514.35, -493.18) * mm});
            skPoint(sketch, "E38.93.90.0", {"position": v(514.35, -499.53) * mm});
            skPoint(sketch, "E38.93.91.0", {"position": v(514.35, -505.88) * mm});
            skPoint(sketch, "E38.93.92.0", {"position": v(514.35, -512.23) * mm});
            skPoint(sketch, "E38.93.93.0", {"position": v(514.35, -518.58) * mm});
            skPoint(sketch, "E38.93.94.0", {"position": v(514.35, -524.93) * mm});
            skPoint(sketch, "E38.93.95.0", {"position": v(514.35, -531.28) * mm});
            skPoint(sketch, "E38.93.96.0", {"position": v(514.35, -537.63) * mm});
            skPoint(sketch, "E38.93.97.0", {"position": v(514.35, -543.98) * mm});
            skPoint(sketch, "E38.93.98.0", {"position": v(514.35, -550.33) * mm});
            skPoint(sketch, "E38.93.99.0", {"position": v(514.35, -556.68) * mm});
            skPoint(sketch, "E38.94.0.0", {"position": v(520.7, 71.97) * mm});
            skPoint(sketch, "E38.94.1.0", {"position": v(520.7, 65.62) * mm});
            skPoint(sketch, "E38.94.2.0", {"position": v(520.7, 59.27) * mm});
            skPoint(sketch, "E38.94.3.0", {"position": v(520.7, 52.92) * mm});
            skPoint(sketch, "E38.94.4.0", {"position": v(520.7, 46.57) * mm});
            skPoint(sketch, "E38.94.5.0", {"position": v(520.7, 40.22) * mm});
            skPoint(sketch, "E38.94.6.0", {"position": v(520.7, 33.87) * mm});
            skPoint(sketch, "E38.94.7.0", {"position": v(520.7, 27.52) * mm});
            skPoint(sketch, "E38.94.8.0", {"position": v(520.7, 21.17) * mm});
            skPoint(sketch, "E38.94.9.0", {"position": v(520.7, 14.82) * mm});
            skPoint(sketch, "E38.94.10.0", {"position": v(520.7, 8.47) * mm});
            skPoint(sketch, "E38.94.11.0", {"position": v(520.7, 2.12) * mm});
            skPoint(sketch, "E38.94.12.0", {"position": v(520.7, -4.23) * mm});
            skPoint(sketch, "E38.94.13.0", {"position": v(520.7, -10.58) * mm});
            skPoint(sketch, "E38.94.14.0", {"position": v(520.7, -16.93) * mm});
            skPoint(sketch, "E38.94.15.0", {"position": v(520.7, -23.28) * mm});
            skPoint(sketch, "E38.94.16.0", {"position": v(520.7, -29.63) * mm});
            skPoint(sketch, "E38.94.17.0", {"position": v(520.7, -35.98) * mm});
            skPoint(sketch, "E38.94.18.0", {"position": v(520.7, -42.33) * mm});
            skPoint(sketch, "E38.94.19.0", {"position": v(520.7, -48.68) * mm});
            skPoint(sketch, "E38.94.20.0", {"position": v(520.7, -55.03) * mm});
            skPoint(sketch, "E38.94.21.0", {"position": v(520.7, -61.38) * mm});
            skPoint(sketch, "E38.94.22.0", {"position": v(520.7, -67.73) * mm});
            skPoint(sketch, "E38.94.23.0", {"position": v(520.7, -74.08) * mm});
            skPoint(sketch, "E38.94.24.0", {"position": v(520.7, -80.43) * mm});
            skPoint(sketch, "E38.94.25.0", {"position": v(520.7, -86.78) * mm});
            skPoint(sketch, "E38.94.26.0", {"position": v(520.7, -93.13) * mm});
            skPoint(sketch, "E38.94.27.0", {"position": v(520.7, -99.48) * mm});
            skPoint(sketch, "E38.94.28.0", {"position": v(520.7, -105.83) * mm});
            skPoint(sketch, "E38.94.29.0", {"position": v(520.7, -112.18) * mm});
            skPoint(sketch, "E38.94.30.0", {"position": v(520.7, -118.53) * mm});
            skPoint(sketch, "E38.94.31.0", {"position": v(520.7, -124.88) * mm});
            skPoint(sketch, "E38.94.32.0", {"position": v(520.7, -131.23) * mm});
            skPoint(sketch, "E38.94.33.0", {"position": v(520.7, -137.58) * mm});
            skPoint(sketch, "E38.94.34.0", {"position": v(520.7, -143.93) * mm});
            skPoint(sketch, "E38.94.35.0", {"position": v(520.7, -150.28) * mm});
            skPoint(sketch, "E38.94.36.0", {"position": v(520.7, -156.63) * mm});
            skPoint(sketch, "E38.94.37.0", {"position": v(520.7, -162.98) * mm});
            skPoint(sketch, "E38.94.38.0", {"position": v(520.7, -169.33) * mm});
            skPoint(sketch, "E38.94.39.0", {"position": v(520.7, -175.68) * mm});
            skPoint(sketch, "E38.94.40.0", {"position": v(520.7, -182.03) * mm});
            skPoint(sketch, "E38.94.41.0", {"position": v(520.7, -188.38) * mm});
            skPoint(sketch, "E38.94.42.0", {"position": v(520.7, -194.73) * mm});
            skPoint(sketch, "E38.94.43.0", {"position": v(520.7, -201.08) * mm});
            skPoint(sketch, "E38.94.44.0", {"position": v(520.7, -207.43) * mm});
            skPoint(sketch, "E38.94.45.0", {"position": v(520.7, -213.78) * mm});
            skPoint(sketch, "E38.94.46.0", {"position": v(520.7, -220.13) * mm});
            skPoint(sketch, "E38.94.47.0", {"position": v(520.7, -226.48) * mm});
            skPoint(sketch, "E38.94.48.0", {"position": v(520.7, -232.83) * mm});
            skPoint(sketch, "E38.94.49.0", {"position": v(520.7, -239.18) * mm});
            skPoint(sketch, "E38.94.50.0", {"position": v(520.7, -245.53) * mm});
            skPoint(sketch, "E38.94.51.0", {"position": v(520.7, -251.88) * mm});
            skPoint(sketch, "E38.94.52.0", {"position": v(520.7, -258.23) * mm});
            skPoint(sketch, "E38.94.53.0", {"position": v(520.7, -264.58) * mm});
            skPoint(sketch, "E38.94.54.0", {"position": v(520.7, -270.93) * mm});
            skPoint(sketch, "E38.94.55.0", {"position": v(520.7, -277.28) * mm});
            skPoint(sketch, "E38.94.56.0", {"position": v(520.7, -283.63) * mm});
            skPoint(sketch, "E38.94.57.0", {"position": v(520.7, -289.98) * mm});
            skPoint(sketch, "E38.94.58.0", {"position": v(520.7, -296.33) * mm});
            skPoint(sketch, "E38.94.59.0", {"position": v(520.7, -302.68) * mm});
            skPoint(sketch, "E38.94.60.0", {"position": v(520.7, -309.03) * mm});
            skPoint(sketch, "E38.94.61.0", {"position": v(520.7, -315.38) * mm});
            skPoint(sketch, "E38.94.62.0", {"position": v(520.7, -321.73) * mm});
            skPoint(sketch, "E38.94.63.0", {"position": v(520.7, -328.08) * mm});
            skPoint(sketch, "E38.94.64.0", {"position": v(520.7, -334.43) * mm});
            skPoint(sketch, "E38.94.65.0", {"position": v(520.7, -340.78) * mm});
            skPoint(sketch, "E38.94.66.0", {"position": v(520.7, -347.13) * mm});
            skPoint(sketch, "E38.94.67.0", {"position": v(520.7, -353.48) * mm});
            skPoint(sketch, "E38.94.68.0", {"position": v(520.7, -359.83) * mm});
            skPoint(sketch, "E38.94.69.0", {"position": v(520.7, -366.18) * mm});
            skPoint(sketch, "E38.94.70.0", {"position": v(520.7, -372.53) * mm});
            skPoint(sketch, "E38.94.71.0", {"position": v(520.7, -378.88) * mm});
            skPoint(sketch, "E38.94.72.0", {"position": v(520.7, -385.23) * mm});
            skPoint(sketch, "E38.94.73.0", {"position": v(520.7, -391.58) * mm});
            skPoint(sketch, "E38.94.74.0", {"position": v(520.7, -397.93) * mm});
            skPoint(sketch, "E38.94.75.0", {"position": v(520.7, -404.28) * mm});
            skPoint(sketch, "E38.94.76.0", {"position": v(520.7, -410.63) * mm});
            skPoint(sketch, "E38.94.77.0", {"position": v(520.7, -416.98) * mm});
            skPoint(sketch, "E38.94.78.0", {"position": v(520.7, -423.33) * mm});
            skPoint(sketch, "E38.94.79.0", {"position": v(520.7, -429.68) * mm});
            skPoint(sketch, "E38.94.80.0", {"position": v(520.7, -436.03) * mm});
            skPoint(sketch, "E38.94.81.0", {"position": v(520.7, -442.38) * mm});
            skPoint(sketch, "E38.94.82.0", {"position": v(520.7, -448.73) * mm});
            skPoint(sketch, "E38.94.83.0", {"position": v(520.7, -455.08) * mm});
            skPoint(sketch, "E38.94.84.0", {"position": v(520.7, -461.43) * mm});
            skPoint(sketch, "E38.94.85.0", {"position": v(520.7, -467.78) * mm});
            skPoint(sketch, "E38.94.86.0", {"position": v(520.7, -474.13) * mm});
            skPoint(sketch, "E38.94.87.0", {"position": v(520.7, -480.48) * mm});
            skPoint(sketch, "E38.94.88.0", {"position": v(520.7, -486.83) * mm});
            skPoint(sketch, "E38.94.89.0", {"position": v(520.7, -493.18) * mm});
            skPoint(sketch, "E38.94.90.0", {"position": v(520.7, -499.53) * mm});
            skPoint(sketch, "E38.94.91.0", {"position": v(520.7, -505.88) * mm});
            skPoint(sketch, "E38.94.92.0", {"position": v(520.7, -512.23) * mm});
            skPoint(sketch, "E38.94.93.0", {"position": v(520.7, -518.58) * mm});
            skPoint(sketch, "E38.94.94.0", {"position": v(520.7, -524.93) * mm});
            skPoint(sketch, "E38.94.95.0", {"position": v(520.7, -531.28) * mm});
            skPoint(sketch, "E38.94.96.0", {"position": v(520.7, -537.63) * mm});
            skPoint(sketch, "E38.94.97.0", {"position": v(520.7, -543.98) * mm});
            skPoint(sketch, "E38.94.98.0", {"position": v(520.7, -550.33) * mm});
            skPoint(sketch, "E38.94.99.0", {"position": v(520.7, -556.68) * mm});
            skPoint(sketch, "E38.95.0.0", {"position": v(527.05, 71.97) * mm});
            skPoint(sketch, "E38.95.1.0", {"position": v(527.05, 65.62) * mm});
            skPoint(sketch, "E38.95.2.0", {"position": v(527.05, 59.27) * mm});
            skPoint(sketch, "E38.95.3.0", {"position": v(527.05, 52.92) * mm});
            skPoint(sketch, "E38.95.4.0", {"position": v(527.05, 46.57) * mm});
            skPoint(sketch, "E38.95.5.0", {"position": v(527.05, 40.22) * mm});
            skPoint(sketch, "E38.95.6.0", {"position": v(527.05, 33.87) * mm});
            skPoint(sketch, "E38.95.7.0", {"position": v(527.05, 27.52) * mm});
            skPoint(sketch, "E38.95.8.0", {"position": v(527.05, 21.17) * mm});
            skPoint(sketch, "E38.95.9.0", {"position": v(527.05, 14.82) * mm});
            skPoint(sketch, "E38.95.10.0", {"position": v(527.05, 8.47) * mm});
            skPoint(sketch, "E38.95.11.0", {"position": v(527.05, 2.12) * mm});
            skPoint(sketch, "E38.95.12.0", {"position": v(527.05, -4.23) * mm});
            skPoint(sketch, "E38.95.13.0", {"position": v(527.05, -10.58) * mm});
            skPoint(sketch, "E38.95.14.0", {"position": v(527.05, -16.93) * mm});
            skPoint(sketch, "E38.95.15.0", {"position": v(527.05, -23.28) * mm});
            skPoint(sketch, "E38.95.16.0", {"position": v(527.05, -29.63) * mm});
            skPoint(sketch, "E38.95.17.0", {"position": v(527.05, -35.98) * mm});
            skPoint(sketch, "E38.95.18.0", {"position": v(527.05, -42.33) * mm});
            skPoint(sketch, "E38.95.19.0", {"position": v(527.05, -48.68) * mm});
            skPoint(sketch, "E38.95.20.0", {"position": v(527.05, -55.03) * mm});
            skPoint(sketch, "E38.95.21.0", {"position": v(527.05, -61.38) * mm});
            skPoint(sketch, "E38.95.22.0", {"position": v(527.05, -67.73) * mm});
            skPoint(sketch, "E38.95.23.0", {"position": v(527.05, -74.08) * mm});
            skPoint(sketch, "E38.95.24.0", {"position": v(527.05, -80.43) * mm});
            skPoint(sketch, "E38.95.25.0", {"position": v(527.05, -86.78) * mm});
            skPoint(sketch, "E38.95.26.0", {"position": v(527.05, -93.13) * mm});
            skPoint(sketch, "E38.95.27.0", {"position": v(527.05, -99.48) * mm});
            skPoint(sketch, "E38.95.28.0", {"position": v(527.05, -105.83) * mm});
            skPoint(sketch, "E38.95.29.0", {"position": v(527.05, -112.18) * mm});
            skPoint(sketch, "E38.95.30.0", {"position": v(527.05, -118.53) * mm});
            skPoint(sketch, "E38.95.31.0", {"position": v(527.05, -124.88) * mm});
            skPoint(sketch, "E38.95.32.0", {"position": v(527.05, -131.23) * mm});
            skPoint(sketch, "E38.95.33.0", {"position": v(527.05, -137.58) * mm});
            skPoint(sketch, "E38.95.34.0", {"position": v(527.05, -143.93) * mm});
            skPoint(sketch, "E38.95.35.0", {"position": v(527.05, -150.28) * mm});
            skPoint(sketch, "E38.95.36.0", {"position": v(527.05, -156.63) * mm});
            skPoint(sketch, "E38.95.37.0", {"position": v(527.05, -162.98) * mm});
            skPoint(sketch, "E38.95.38.0", {"position": v(527.05, -169.33) * mm});
            skPoint(sketch, "E38.95.39.0", {"position": v(527.05, -175.68) * mm});
            skPoint(sketch, "E38.95.40.0", {"position": v(527.05, -182.03) * mm});
            skPoint(sketch, "E38.95.41.0", {"position": v(527.05, -188.38) * mm});
            skPoint(sketch, "E38.95.42.0", {"position": v(527.05, -194.73) * mm});
            skPoint(sketch, "E38.95.43.0", {"position": v(527.05, -201.08) * mm});
            skPoint(sketch, "E38.95.44.0", {"position": v(527.05, -207.43) * mm});
            skPoint(sketch, "E38.95.45.0", {"position": v(527.05, -213.78) * mm});
            skPoint(sketch, "E38.95.46.0", {"position": v(527.05, -220.13) * mm});
            skPoint(sketch, "E38.95.47.0", {"position": v(527.05, -226.48) * mm});
            skPoint(sketch, "E38.95.48.0", {"position": v(527.05, -232.83) * mm});
            skPoint(sketch, "E38.95.49.0", {"position": v(527.05, -239.18) * mm});
            skPoint(sketch, "E38.95.50.0", {"position": v(527.05, -245.53) * mm});
            skPoint(sketch, "E38.95.51.0", {"position": v(527.05, -251.88) * mm});
            skPoint(sketch, "E38.95.52.0", {"position": v(527.05, -258.23) * mm});
            skPoint(sketch, "E38.95.53.0", {"position": v(527.05, -264.58) * mm});
            skPoint(sketch, "E38.95.54.0", {"position": v(527.05, -270.93) * mm});
            skPoint(sketch, "E38.95.55.0", {"position": v(527.05, -277.28) * mm});
            skPoint(sketch, "E38.95.56.0", {"position": v(527.05, -283.63) * mm});
            skPoint(sketch, "E38.95.57.0", {"position": v(527.05, -289.98) * mm});
            skPoint(sketch, "E38.95.58.0", {"position": v(527.05, -296.33) * mm});
            skPoint(sketch, "E38.95.59.0", {"position": v(527.05, -302.68) * mm});
            skPoint(sketch, "E38.95.60.0", {"position": v(527.05, -309.03) * mm});
            skPoint(sketch, "E38.95.61.0", {"position": v(527.05, -315.38) * mm});
            skPoint(sketch, "E38.95.62.0", {"position": v(527.05, -321.73) * mm});
            skPoint(sketch, "E38.95.63.0", {"position": v(527.05, -328.08) * mm});
            skPoint(sketch, "E38.95.64.0", {"position": v(527.05, -334.43) * mm});
            skPoint(sketch, "E38.95.65.0", {"position": v(527.05, -340.78) * mm});
            skPoint(sketch, "E38.95.66.0", {"position": v(527.05, -347.13) * mm});
            skPoint(sketch, "E38.95.67.0", {"position": v(527.05, -353.48) * mm});
            skPoint(sketch, "E38.95.68.0", {"position": v(527.05, -359.83) * mm});
            skPoint(sketch, "E38.95.69.0", {"position": v(527.05, -366.18) * mm});
            skPoint(sketch, "E38.95.70.0", {"position": v(527.05, -372.53) * mm});
            skPoint(sketch, "E38.95.71.0", {"position": v(527.05, -378.88) * mm});
            skPoint(sketch, "E38.95.72.0", {"position": v(527.05, -385.23) * mm});
            skPoint(sketch, "E38.95.73.0", {"position": v(527.05, -391.58) * mm});
            skPoint(sketch, "E38.95.74.0", {"position": v(527.05, -397.93) * mm});
            skPoint(sketch, "E38.95.75.0", {"position": v(527.05, -404.28) * mm});
            skPoint(sketch, "E38.95.76.0", {"position": v(527.05, -410.63) * mm});
            skPoint(sketch, "E38.95.77.0", {"position": v(527.05, -416.98) * mm});
            skPoint(sketch, "E38.95.78.0", {"position": v(527.05, -423.33) * mm});
            skPoint(sketch, "E38.95.79.0", {"position": v(527.05, -429.68) * mm});
            skPoint(sketch, "E38.95.80.0", {"position": v(527.05, -436.03) * mm});
            skPoint(sketch, "E38.95.81.0", {"position": v(527.05, -442.38) * mm});
            skPoint(sketch, "E38.95.82.0", {"position": v(527.05, -448.73) * mm});
            skPoint(sketch, "E38.95.83.0", {"position": v(527.05, -455.08) * mm});
            skPoint(sketch, "E38.95.84.0", {"position": v(527.05, -461.43) * mm});
            skPoint(sketch, "E38.95.85.0", {"position": v(527.05, -467.78) * mm});
            skPoint(sketch, "E38.95.86.0", {"position": v(527.05, -474.13) * mm});
            skPoint(sketch, "E38.95.87.0", {"position": v(527.05, -480.48) * mm});
            skPoint(sketch, "E38.95.88.0", {"position": v(527.05, -486.83) * mm});
            skPoint(sketch, "E38.95.89.0", {"position": v(527.05, -493.18) * mm});
            skPoint(sketch, "E38.95.90.0", {"position": v(527.05, -499.53) * mm});
            skPoint(sketch, "E38.95.91.0", {"position": v(527.05, -505.88) * mm});
            skPoint(sketch, "E38.95.92.0", {"position": v(527.05, -512.23) * mm});
            skPoint(sketch, "E38.95.93.0", {"position": v(527.05, -518.58) * mm});
            skPoint(sketch, "E38.95.94.0", {"position": v(527.05, -524.93) * mm});
            skPoint(sketch, "E38.95.95.0", {"position": v(527.05, -531.28) * mm});
            skPoint(sketch, "E38.95.96.0", {"position": v(527.05, -537.63) * mm});
            skPoint(sketch, "E38.95.97.0", {"position": v(527.05, -543.98) * mm});
            skPoint(sketch, "E38.95.98.0", {"position": v(527.05, -550.33) * mm});
            skPoint(sketch, "E38.95.99.0", {"position": v(527.05, -556.68) * mm});
            skPoint(sketch, "E38.96.0.0", {"position": v(533.4, 71.97) * mm});
            skPoint(sketch, "E38.96.1.0", {"position": v(533.4, 65.62) * mm});
            skPoint(sketch, "E38.96.2.0", {"position": v(533.4, 59.27) * mm});
            skPoint(sketch, "E38.96.3.0", {"position": v(533.4, 52.92) * mm});
            skPoint(sketch, "E38.96.4.0", {"position": v(533.4, 46.57) * mm});
            skPoint(sketch, "E38.96.5.0", {"position": v(533.4, 40.22) * mm});
            skPoint(sketch, "E38.96.6.0", {"position": v(533.4, 33.87) * mm});
            skPoint(sketch, "E38.96.7.0", {"position": v(533.4, 27.52) * mm});
            skPoint(sketch, "E38.96.8.0", {"position": v(533.4, 21.17) * mm});
            skPoint(sketch, "E38.96.9.0", {"position": v(533.4, 14.82) * mm});
            skPoint(sketch, "E38.96.10.0", {"position": v(533.4, 8.47) * mm});
            skPoint(sketch, "E38.96.11.0", {"position": v(533.4, 2.12) * mm});
            skPoint(sketch, "E38.96.12.0", {"position": v(533.4, -4.23) * mm});
            skPoint(sketch, "E38.96.13.0", {"position": v(533.4, -10.58) * mm});
            skPoint(sketch, "E38.96.14.0", {"position": v(533.4, -16.93) * mm});
            skPoint(sketch, "E38.96.15.0", {"position": v(533.4, -23.28) * mm});
            skPoint(sketch, "E38.96.16.0", {"position": v(533.4, -29.63) * mm});
            skPoint(sketch, "E38.96.17.0", {"position": v(533.4, -35.98) * mm});
            skPoint(sketch, "E38.96.18.0", {"position": v(533.4, -42.33) * mm});
            skPoint(sketch, "E38.96.19.0", {"position": v(533.4, -48.68) * mm});
            skPoint(sketch, "E38.96.20.0", {"position": v(533.4, -55.03) * mm});
            skPoint(sketch, "E38.96.21.0", {"position": v(533.4, -61.38) * mm});
            skPoint(sketch, "E38.96.22.0", {"position": v(533.4, -67.73) * mm});
            skPoint(sketch, "E38.96.23.0", {"position": v(533.4, -74.08) * mm});
            skPoint(sketch, "E38.96.24.0", {"position": v(533.4, -80.43) * mm});
            skPoint(sketch, "E38.96.25.0", {"position": v(533.4, -86.78) * mm});
            skPoint(sketch, "E38.96.26.0", {"position": v(533.4, -93.13) * mm});
            skPoint(sketch, "E38.96.27.0", {"position": v(533.4, -99.48) * mm});
            skPoint(sketch, "E38.96.28.0", {"position": v(533.4, -105.83) * mm});
            skPoint(sketch, "E38.96.29.0", {"position": v(533.4, -112.18) * mm});
            skPoint(sketch, "E38.96.30.0", {"position": v(533.4, -118.53) * mm});
            skPoint(sketch, "E38.96.31.0", {"position": v(533.4, -124.88) * mm});
            skPoint(sketch, "E38.96.32.0", {"position": v(533.4, -131.23) * mm});
            skPoint(sketch, "E38.96.33.0", {"position": v(533.4, -137.58) * mm});
            skPoint(sketch, "E38.96.34.0", {"position": v(533.4, -143.93) * mm});
            skPoint(sketch, "E38.96.35.0", {"position": v(533.4, -150.28) * mm});
            skPoint(sketch, "E38.96.36.0", {"position": v(533.4, -156.63) * mm});
            skPoint(sketch, "E38.96.37.0", {"position": v(533.4, -162.98) * mm});
            skPoint(sketch, "E38.96.38.0", {"position": v(533.4, -169.33) * mm});
            skPoint(sketch, "E38.96.39.0", {"position": v(533.4, -175.68) * mm});
            skPoint(sketch, "E38.96.40.0", {"position": v(533.4, -182.03) * mm});
            skPoint(sketch, "E38.96.41.0", {"position": v(533.4, -188.38) * mm});
            skPoint(sketch, "E38.96.42.0", {"position": v(533.4, -194.73) * mm});
            skPoint(sketch, "E38.96.43.0", {"position": v(533.4, -201.08) * mm});
            skPoint(sketch, "E38.96.44.0", {"position": v(533.4, -207.43) * mm});
            skPoint(sketch, "E38.96.45.0", {"position": v(533.4, -213.78) * mm});
            skPoint(sketch, "E38.96.46.0", {"position": v(533.4, -220.13) * mm});
            skPoint(sketch, "E38.96.47.0", {"position": v(533.4, -226.48) * mm});
            skPoint(sketch, "E38.96.48.0", {"position": v(533.4, -232.83) * mm});
            skPoint(sketch, "E38.96.49.0", {"position": v(533.4, -239.18) * mm});
            skPoint(sketch, "E38.96.50.0", {"position": v(533.4, -245.53) * mm});
            skPoint(sketch, "E38.96.51.0", {"position": v(533.4, -251.88) * mm});
            skPoint(sketch, "E38.96.52.0", {"position": v(533.4, -258.23) * mm});
            skPoint(sketch, "E38.96.53.0", {"position": v(533.4, -264.58) * mm});
            skPoint(sketch, "E38.96.54.0", {"position": v(533.4, -270.93) * mm});
            skPoint(sketch, "E38.96.55.0", {"position": v(533.4, -277.28) * mm});
            skPoint(sketch, "E38.96.56.0", {"position": v(533.4, -283.63) * mm});
            skPoint(sketch, "E38.96.57.0", {"position": v(533.4, -289.98) * mm});
            skPoint(sketch, "E38.96.58.0", {"position": v(533.4, -296.33) * mm});
            skPoint(sketch, "E38.96.59.0", {"position": v(533.4, -302.68) * mm});
            skPoint(sketch, "E38.96.60.0", {"position": v(533.4, -309.03) * mm});
            skPoint(sketch, "E38.96.61.0", {"position": v(533.4, -315.38) * mm});
            skPoint(sketch, "E38.96.62.0", {"position": v(533.4, -321.73) * mm});
            skPoint(sketch, "E38.96.63.0", {"position": v(533.4, -328.08) * mm});
            skPoint(sketch, "E38.96.64.0", {"position": v(533.4, -334.43) * mm});
            skPoint(sketch, "E38.96.65.0", {"position": v(533.4, -340.78) * mm});
            skPoint(sketch, "E38.96.66.0", {"position": v(533.4, -347.13) * mm});
            skPoint(sketch, "E38.96.67.0", {"position": v(533.4, -353.48) * mm});
            skPoint(sketch, "E38.96.68.0", {"position": v(533.4, -359.83) * mm});
            skPoint(sketch, "E38.96.69.0", {"position": v(533.4, -366.18) * mm});
            skPoint(sketch, "E38.96.70.0", {"position": v(533.4, -372.53) * mm});
            skPoint(sketch, "E38.96.71.0", {"position": v(533.4, -378.88) * mm});
            skPoint(sketch, "E38.96.72.0", {"position": v(533.4, -385.23) * mm});
            skPoint(sketch, "E38.96.73.0", {"position": v(533.4, -391.58) * mm});
            skPoint(sketch, "E38.96.74.0", {"position": v(533.4, -397.93) * mm});
            skPoint(sketch, "E38.96.75.0", {"position": v(533.4, -404.28) * mm});
            skPoint(sketch, "E38.96.76.0", {"position": v(533.4, -410.63) * mm});
            skPoint(sketch, "E38.96.77.0", {"position": v(533.4, -416.98) * mm});
            skPoint(sketch, "E38.96.78.0", {"position": v(533.4, -423.33) * mm});
            skPoint(sketch, "E38.96.79.0", {"position": v(533.4, -429.68) * mm});
            skPoint(sketch, "E38.96.80.0", {"position": v(533.4, -436.03) * mm});
            skPoint(sketch, "E38.96.81.0", {"position": v(533.4, -442.38) * mm});
            skPoint(sketch, "E38.96.82.0", {"position": v(533.4, -448.73) * mm});
            skPoint(sketch, "E38.96.83.0", {"position": v(533.4, -455.08) * mm});
            skPoint(sketch, "E38.96.84.0", {"position": v(533.4, -461.43) * mm});
            skPoint(sketch, "E38.96.85.0", {"position": v(533.4, -467.78) * mm});
            skPoint(sketch, "E38.96.86.0", {"position": v(533.4, -474.13) * mm});
            skPoint(sketch, "E38.96.87.0", {"position": v(533.4, -480.48) * mm});
            skPoint(sketch, "E38.96.88.0", {"position": v(533.4, -486.83) * mm});
            skPoint(sketch, "E38.96.89.0", {"position": v(533.4, -493.18) * mm});
            skPoint(sketch, "E38.96.90.0", {"position": v(533.4, -499.53) * mm});
            skPoint(sketch, "E38.96.91.0", {"position": v(533.4, -505.88) * mm});
            skPoint(sketch, "E38.96.92.0", {"position": v(533.4, -512.23) * mm});
            skPoint(sketch, "E38.96.93.0", {"position": v(533.4, -518.58) * mm});
            skPoint(sketch, "E38.96.94.0", {"position": v(533.4, -524.93) * mm});
            skPoint(sketch, "E38.96.95.0", {"position": v(533.4, -531.28) * mm});
            skPoint(sketch, "E38.96.96.0", {"position": v(533.4, -537.63) * mm});
            skPoint(sketch, "E38.96.97.0", {"position": v(533.4, -543.98) * mm});
            skPoint(sketch, "E38.96.98.0", {"position": v(533.4, -550.33) * mm});
            skPoint(sketch, "E38.96.99.0", {"position": v(533.4, -556.68) * mm});
            skPoint(sketch, "E38.97.0.0", {"position": v(539.75, 71.97) * mm});
            skPoint(sketch, "E38.97.1.0", {"position": v(539.75, 65.62) * mm});
            skPoint(sketch, "E38.97.2.0", {"position": v(539.75, 59.27) * mm});
            skPoint(sketch, "E38.97.3.0", {"position": v(539.75, 52.92) * mm});
            skPoint(sketch, "E38.97.4.0", {"position": v(539.75, 46.57) * mm});
            skPoint(sketch, "E38.97.5.0", {"position": v(539.75, 40.22) * mm});
            skPoint(sketch, "E38.97.6.0", {"position": v(539.75, 33.87) * mm});
            skPoint(sketch, "E38.97.7.0", {"position": v(539.75, 27.52) * mm});
            skPoint(sketch, "E38.97.8.0", {"position": v(539.75, 21.17) * mm});
            skPoint(sketch, "E38.97.9.0", {"position": v(539.75, 14.82) * mm});
            skPoint(sketch, "E38.97.10.0", {"position": v(539.75, 8.47) * mm});
            skPoint(sketch, "E38.97.11.0", {"position": v(539.75, 2.12) * mm});
            skPoint(sketch, "E38.97.12.0", {"position": v(539.75, -4.23) * mm});
            skPoint(sketch, "E38.97.13.0", {"position": v(539.75, -10.58) * mm});
            skPoint(sketch, "E38.97.14.0", {"position": v(539.75, -16.93) * mm});
            skPoint(sketch, "E38.97.15.0", {"position": v(539.75, -23.28) * mm});
            skPoint(sketch, "E38.97.16.0", {"position": v(539.75, -29.63) * mm});
            skPoint(sketch, "E38.97.17.0", {"position": v(539.75, -35.98) * mm});
            skPoint(sketch, "E38.97.18.0", {"position": v(539.75, -42.33) * mm});
            skPoint(sketch, "E38.97.19.0", {"position": v(539.75, -48.68) * mm});
            skPoint(sketch, "E38.97.20.0", {"position": v(539.75, -55.03) * mm});
            skPoint(sketch, "E38.97.21.0", {"position": v(539.75, -61.38) * mm});
            skPoint(sketch, "E38.97.22.0", {"position": v(539.75, -67.73) * mm});
            skPoint(sketch, "E38.97.23.0", {"position": v(539.75, -74.08) * mm});
            skPoint(sketch, "E38.97.24.0", {"position": v(539.75, -80.43) * mm});
            skPoint(sketch, "E38.97.25.0", {"position": v(539.75, -86.78) * mm});
            skPoint(sketch, "E38.97.26.0", {"position": v(539.75, -93.13) * mm});
            skPoint(sketch, "E38.97.27.0", {"position": v(539.75, -99.48) * mm});
            skPoint(sketch, "E38.97.28.0", {"position": v(539.75, -105.83) * mm});
            skPoint(sketch, "E38.97.29.0", {"position": v(539.75, -112.18) * mm});
            skPoint(sketch, "E38.97.30.0", {"position": v(539.75, -118.53) * mm});
            skPoint(sketch, "E38.97.31.0", {"position": v(539.75, -124.88) * mm});
            skPoint(sketch, "E38.97.32.0", {"position": v(539.75, -131.23) * mm});
            skPoint(sketch, "E38.97.33.0", {"position": v(539.75, -137.58) * mm});
            skPoint(sketch, "E38.97.34.0", {"position": v(539.75, -143.93) * mm});
            skPoint(sketch, "E38.97.35.0", {"position": v(539.75, -150.28) * mm});
            skPoint(sketch, "E38.97.36.0", {"position": v(539.75, -156.63) * mm});
            skPoint(sketch, "E38.97.37.0", {"position": v(539.75, -162.98) * mm});
            skPoint(sketch, "E38.97.38.0", {"position": v(539.75, -169.33) * mm});
            skPoint(sketch, "E38.97.39.0", {"position": v(539.75, -175.68) * mm});
            skPoint(sketch, "E38.97.40.0", {"position": v(539.75, -182.03) * mm});
            skPoint(sketch, "E38.97.41.0", {"position": v(539.75, -188.38) * mm});
            skPoint(sketch, "E38.97.42.0", {"position": v(539.75, -194.73) * mm});
            skPoint(sketch, "E38.97.43.0", {"position": v(539.75, -201.08) * mm});
            skPoint(sketch, "E38.97.44.0", {"position": v(539.75, -207.43) * mm});
            skPoint(sketch, "E38.97.45.0", {"position": v(539.75, -213.78) * mm});
            skPoint(sketch, "E38.97.46.0", {"position": v(539.75, -220.13) * mm});
            skPoint(sketch, "E38.97.47.0", {"position": v(539.75, -226.48) * mm});
            skPoint(sketch, "E38.97.48.0", {"position": v(539.75, -232.83) * mm});
            skPoint(sketch, "E38.97.49.0", {"position": v(539.75, -239.18) * mm});
            skPoint(sketch, "E38.97.50.0", {"position": v(539.75, -245.53) * mm});
            skPoint(sketch, "E38.97.51.0", {"position": v(539.75, -251.88) * mm});
            skPoint(sketch, "E38.97.52.0", {"position": v(539.75, -258.23) * mm});
            skPoint(sketch, "E38.97.53.0", {"position": v(539.75, -264.58) * mm});
            skPoint(sketch, "E38.97.54.0", {"position": v(539.75, -270.93) * mm});
            skPoint(sketch, "E38.97.55.0", {"position": v(539.75, -277.28) * mm});
            skPoint(sketch, "E38.97.56.0", {"position": v(539.75, -283.63) * mm});
            skPoint(sketch, "E38.97.57.0", {"position": v(539.75, -289.98) * mm});
            skPoint(sketch, "E38.97.58.0", {"position": v(539.75, -296.33) * mm});
            skPoint(sketch, "E38.97.59.0", {"position": v(539.75, -302.68) * mm});
            skPoint(sketch, "E38.97.60.0", {"position": v(539.75, -309.03) * mm});
            skPoint(sketch, "E38.97.61.0", {"position": v(539.75, -315.38) * mm});
            skPoint(sketch, "E38.97.62.0", {"position": v(539.75, -321.73) * mm});
            skPoint(sketch, "E38.97.63.0", {"position": v(539.75, -328.08) * mm});
            skPoint(sketch, "E38.97.64.0", {"position": v(539.75, -334.43) * mm});
            skPoint(sketch, "E38.97.65.0", {"position": v(539.75, -340.78) * mm});
            skPoint(sketch, "E38.97.66.0", {"position": v(539.75, -347.13) * mm});
            skPoint(sketch, "E38.97.67.0", {"position": v(539.75, -353.48) * mm});
            skPoint(sketch, "E38.97.68.0", {"position": v(539.75, -359.83) * mm});
            skPoint(sketch, "E38.97.69.0", {"position": v(539.75, -366.18) * mm});
            skPoint(sketch, "E38.97.70.0", {"position": v(539.75, -372.53) * mm});
            skPoint(sketch, "E38.97.71.0", {"position": v(539.75, -378.88) * mm});
            skPoint(sketch, "E38.97.72.0", {"position": v(539.75, -385.23) * mm});
            skPoint(sketch, "E38.97.73.0", {"position": v(539.75, -391.58) * mm});
            skPoint(sketch, "E38.97.74.0", {"position": v(539.75, -397.93) * mm});
            skPoint(sketch, "E38.97.75.0", {"position": v(539.75, -404.28) * mm});
            skPoint(sketch, "E38.97.76.0", {"position": v(539.75, -410.63) * mm});
            skPoint(sketch, "E38.97.77.0", {"position": v(539.75, -416.98) * mm});
            skPoint(sketch, "E38.97.78.0", {"position": v(539.75, -423.33) * mm});
            skPoint(sketch, "E38.97.79.0", {"position": v(539.75, -429.68) * mm});
            skPoint(sketch, "E38.97.80.0", {"position": v(539.75, -436.03) * mm});
            skPoint(sketch, "E38.97.81.0", {"position": v(539.75, -442.38) * mm});
            skPoint(sketch, "E38.97.82.0", {"position": v(539.75, -448.73) * mm});
            skPoint(sketch, "E38.97.83.0", {"position": v(539.75, -455.08) * mm});
            skPoint(sketch, "E38.97.84.0", {"position": v(539.75, -461.43) * mm});
            skPoint(sketch, "E38.97.85.0", {"position": v(539.75, -467.78) * mm});
            skPoint(sketch, "E38.97.86.0", {"position": v(539.75, -474.13) * mm});
            skPoint(sketch, "E38.97.87.0", {"position": v(539.75, -480.48) * mm});
            skPoint(sketch, "E38.97.88.0", {"position": v(539.75, -486.83) * mm});
            skPoint(sketch, "E38.97.89.0", {"position": v(539.75, -493.18) * mm});
            skPoint(sketch, "E38.97.90.0", {"position": v(539.75, -499.53) * mm});
            skPoint(sketch, "E38.97.91.0", {"position": v(539.75, -505.88) * mm});
            skPoint(sketch, "E38.97.92.0", {"position": v(539.75, -512.23) * mm});
            skPoint(sketch, "E38.97.93.0", {"position": v(539.75, -518.58) * mm});
            skPoint(sketch, "E38.97.94.0", {"position": v(539.75, -524.93) * mm});
            skPoint(sketch, "E38.97.95.0", {"position": v(539.75, -531.28) * mm});
            skPoint(sketch, "E38.97.96.0", {"position": v(539.75, -537.63) * mm});
            skPoint(sketch, "E38.97.97.0", {"position": v(539.75, -543.98) * mm});
            skPoint(sketch, "E38.97.98.0", {"position": v(539.75, -550.33) * mm});
            skPoint(sketch, "E38.97.99.0", {"position": v(539.75, -556.68) * mm});
            skPoint(sketch, "E38.98.0.0", {"position": v(546.1, 71.97) * mm});
            skPoint(sketch, "E38.98.1.0", {"position": v(546.1, 65.62) * mm});
            skPoint(sketch, "E38.98.2.0", {"position": v(546.1, 59.27) * mm});
            skPoint(sketch, "E38.98.3.0", {"position": v(546.1, 52.92) * mm});
            skPoint(sketch, "E38.98.4.0", {"position": v(546.1, 46.57) * mm});
            skPoint(sketch, "E38.98.5.0", {"position": v(546.1, 40.22) * mm});
            skPoint(sketch, "E38.98.6.0", {"position": v(546.1, 33.87) * mm});
            skPoint(sketch, "E38.98.7.0", {"position": v(546.1, 27.52) * mm});
            skPoint(sketch, "E38.98.8.0", {"position": v(546.1, 21.17) * mm});
            skPoint(sketch, "E38.98.9.0", {"position": v(546.1, 14.82) * mm});
            skPoint(sketch, "E38.98.10.0", {"position": v(546.1, 8.47) * mm});
            skPoint(sketch, "E38.98.11.0", {"position": v(546.1, 2.12) * mm});
            skPoint(sketch, "E38.98.12.0", {"position": v(546.1, -4.23) * mm});
            skPoint(sketch, "E38.98.13.0", {"position": v(546.1, -10.58) * mm});
            skPoint(sketch, "E38.98.14.0", {"position": v(546.1, -16.93) * mm});
            skPoint(sketch, "E38.98.15.0", {"position": v(546.1, -23.28) * mm});
            skPoint(sketch, "E38.98.16.0", {"position": v(546.1, -29.63) * mm});
            skPoint(sketch, "E38.98.17.0", {"position": v(546.1, -35.98) * mm});
            skPoint(sketch, "E38.98.18.0", {"position": v(546.1, -42.33) * mm});
            skPoint(sketch, "E38.98.19.0", {"position": v(546.1, -48.68) * mm});
            skPoint(sketch, "E38.98.20.0", {"position": v(546.1, -55.03) * mm});
            skPoint(sketch, "E38.98.21.0", {"position": v(546.1, -61.38) * mm});
            skPoint(sketch, "E38.98.22.0", {"position": v(546.1, -67.73) * mm});
            skPoint(sketch, "E38.98.23.0", {"position": v(546.1, -74.08) * mm});
            skPoint(sketch, "E38.98.24.0", {"position": v(546.1, -80.43) * mm});
            skPoint(sketch, "E38.98.25.0", {"position": v(546.1, -86.78) * mm});
            skPoint(sketch, "E38.98.26.0", {"position": v(546.1, -93.13) * mm});
            skPoint(sketch, "E38.98.27.0", {"position": v(546.1, -99.48) * mm});
            skPoint(sketch, "E38.98.28.0", {"position": v(546.1, -105.83) * mm});
            skPoint(sketch, "E38.98.29.0", {"position": v(546.1, -112.18) * mm});
            skPoint(sketch, "E38.98.30.0", {"position": v(546.1, -118.53) * mm});
            skPoint(sketch, "E38.98.31.0", {"position": v(546.1, -124.88) * mm});
            skPoint(sketch, "E38.98.32.0", {"position": v(546.1, -131.23) * mm});
            skPoint(sketch, "E38.98.33.0", {"position": v(546.1, -137.58) * mm});
            skPoint(sketch, "E38.98.34.0", {"position": v(546.1, -143.93) * mm});
            skPoint(sketch, "E38.98.35.0", {"position": v(546.1, -150.28) * mm});
            skPoint(sketch, "E38.98.36.0", {"position": v(546.1, -156.63) * mm});
            skPoint(sketch, "E38.98.37.0", {"position": v(546.1, -162.98) * mm});
            skPoint(sketch, "E38.98.38.0", {"position": v(546.1, -169.33) * mm});
            skPoint(sketch, "E38.98.39.0", {"position": v(546.1, -175.68) * mm});
            skPoint(sketch, "E38.98.40.0", {"position": v(546.1, -182.03) * mm});
            skPoint(sketch, "E38.98.41.0", {"position": v(546.1, -188.38) * mm});
            skPoint(sketch, "E38.98.42.0", {"position": v(546.1, -194.73) * mm});
            skPoint(sketch, "E38.98.43.0", {"position": v(546.1, -201.08) * mm});
            skPoint(sketch, "E38.98.44.0", {"position": v(546.1, -207.43) * mm});
            skPoint(sketch, "E38.98.45.0", {"position": v(546.1, -213.78) * mm});
            skPoint(sketch, "E38.98.46.0", {"position": v(546.1, -220.13) * mm});
            skPoint(sketch, "E38.98.47.0", {"position": v(546.1, -226.48) * mm});
            skPoint(sketch, "E38.98.48.0", {"position": v(546.1, -232.83) * mm});
            skPoint(sketch, "E38.98.49.0", {"position": v(546.1, -239.18) * mm});
            skPoint(sketch, "E38.98.50.0", {"position": v(546.1, -245.53) * mm});
            skPoint(sketch, "E38.98.51.0", {"position": v(546.1, -251.88) * mm});
            skPoint(sketch, "E38.98.52.0", {"position": v(546.1, -258.23) * mm});
            skPoint(sketch, "E38.98.53.0", {"position": v(546.1, -264.58) * mm});
            skPoint(sketch, "E38.98.54.0", {"position": v(546.1, -270.93) * mm});
            skPoint(sketch, "E38.98.55.0", {"position": v(546.1, -277.28) * mm});
            skPoint(sketch, "E38.98.56.0", {"position": v(546.1, -283.63) * mm});
            skPoint(sketch, "E38.98.57.0", {"position": v(546.1, -289.98) * mm});
            skPoint(sketch, "E38.98.58.0", {"position": v(546.1, -296.33) * mm});
            skPoint(sketch, "E38.98.59.0", {"position": v(546.1, -302.68) * mm});
            skPoint(sketch, "E38.98.60.0", {"position": v(546.1, -309.03) * mm});
            skPoint(sketch, "E38.98.61.0", {"position": v(546.1, -315.38) * mm});
            skPoint(sketch, "E38.98.62.0", {"position": v(546.1, -321.73) * mm});
            skPoint(sketch, "E38.98.63.0", {"position": v(546.1, -328.08) * mm});
            skPoint(sketch, "E38.98.64.0", {"position": v(546.1, -334.43) * mm});
            skPoint(sketch, "E38.98.65.0", {"position": v(546.1, -340.78) * mm});
            skPoint(sketch, "E38.98.66.0", {"position": v(546.1, -347.13) * mm});
            skPoint(sketch, "E38.98.67.0", {"position": v(546.1, -353.48) * mm});
            skPoint(sketch, "E38.98.68.0", {"position": v(546.1, -359.83) * mm});
            skPoint(sketch, "E38.98.69.0", {"position": v(546.1, -366.18) * mm});
            skPoint(sketch, "E38.98.70.0", {"position": v(546.1, -372.53) * mm});
            skPoint(sketch, "E38.98.71.0", {"position": v(546.1, -378.88) * mm});
            skPoint(sketch, "E38.98.72.0", {"position": v(546.1, -385.23) * mm});
            skPoint(sketch, "E38.98.73.0", {"position": v(546.1, -391.58) * mm});
            skPoint(sketch, "E38.98.74.0", {"position": v(546.1, -397.93) * mm});
            skPoint(sketch, "E38.98.75.0", {"position": v(546.1, -404.28) * mm});
            skPoint(sketch, "E38.98.76.0", {"position": v(546.1, -410.63) * mm});
            skPoint(sketch, "E38.98.77.0", {"position": v(546.1, -416.98) * mm});
            skPoint(sketch, "E38.98.78.0", {"position": v(546.1, -423.33) * mm});
            skPoint(sketch, "E38.98.79.0", {"position": v(546.1, -429.68) * mm});
            skPoint(sketch, "E38.98.80.0", {"position": v(546.1, -436.03) * mm});
            skPoint(sketch, "E38.98.81.0", {"position": v(546.1, -442.38) * mm});
            skPoint(sketch, "E38.98.82.0", {"position": v(546.1, -448.73) * mm});
            skPoint(sketch, "E38.98.83.0", {"position": v(546.1, -455.08) * mm});
            skPoint(sketch, "E38.98.84.0", {"position": v(546.1, -461.43) * mm});
            skPoint(sketch, "E38.98.85.0", {"position": v(546.1, -467.78) * mm});
            skPoint(sketch, "E38.98.86.0", {"position": v(546.1, -474.13) * mm});
            skPoint(sketch, "E38.98.87.0", {"position": v(546.1, -480.48) * mm});
            skPoint(sketch, "E38.98.88.0", {"position": v(546.1, -486.83) * mm});
            skPoint(sketch, "E38.98.89.0", {"position": v(546.1, -493.18) * mm});
            skPoint(sketch, "E38.98.90.0", {"position": v(546.1, -499.53) * mm});
            skPoint(sketch, "E38.98.91.0", {"position": v(546.1, -505.88) * mm});
            skPoint(sketch, "E38.98.92.0", {"position": v(546.1, -512.23) * mm});
            skPoint(sketch, "E38.98.93.0", {"position": v(546.1, -518.58) * mm});
            skPoint(sketch, "E38.98.94.0", {"position": v(546.1, -524.93) * mm});
            skPoint(sketch, "E38.98.95.0", {"position": v(546.1, -531.28) * mm});
            skPoint(sketch, "E38.98.96.0", {"position": v(546.1, -537.63) * mm});
            skPoint(sketch, "E38.98.97.0", {"position": v(546.1, -543.98) * mm});
            skPoint(sketch, "E38.98.98.0", {"position": v(546.1, -550.33) * mm});
            skPoint(sketch, "E38.98.99.0", {"position": v(546.1, -556.68) * mm});
            skPoint(sketch, "E38.99.0.0", {"position": v(552.45, 71.97) * mm});
            skPoint(sketch, "E38.99.1.0", {"position": v(552.45, 65.62) * mm});
            skPoint(sketch, "E38.99.2.0", {"position": v(552.45, 59.27) * mm});
            skPoint(sketch, "E38.99.3.0", {"position": v(552.45, 52.92) * mm});
            skPoint(sketch, "E38.99.4.0", {"position": v(552.45, 46.57) * mm});
            skPoint(sketch, "E38.99.5.0", {"position": v(552.45, 40.22) * mm});
            skPoint(sketch, "E38.99.6.0", {"position": v(552.45, 33.87) * mm});
            skPoint(sketch, "E38.99.7.0", {"position": v(552.45, 27.52) * mm});
            skPoint(sketch, "E38.99.8.0", {"position": v(552.45, 21.17) * mm});
            skPoint(sketch, "E38.99.9.0", {"position": v(552.45, 14.82) * mm});
            skPoint(sketch, "E38.99.10.0", {"position": v(552.45, 8.47) * mm});
            skPoint(sketch, "E38.99.11.0", {"position": v(552.45, 2.12) * mm});
            skPoint(sketch, "E38.99.12.0", {"position": v(552.45, -4.23) * mm});
            skPoint(sketch, "E38.99.13.0", {"position": v(552.45, -10.58) * mm});
            skPoint(sketch, "E38.99.14.0", {"position": v(552.45, -16.93) * mm});
            skPoint(sketch, "E38.99.15.0", {"position": v(552.45, -23.28) * mm});
            skPoint(sketch, "E38.99.16.0", {"position": v(552.45, -29.63) * mm});
            skPoint(sketch, "E38.99.17.0", {"position": v(552.45, -35.98) * mm});
            skPoint(sketch, "E38.99.18.0", {"position": v(552.45, -42.33) * mm});
            skPoint(sketch, "E38.99.19.0", {"position": v(552.45, -48.68) * mm});
            skPoint(sketch, "E38.99.20.0", {"position": v(552.45, -55.03) * mm});
            skPoint(sketch, "E38.99.21.0", {"position": v(552.45, -61.38) * mm});
            skPoint(sketch, "E38.99.22.0", {"position": v(552.45, -67.73) * mm});
            skPoint(sketch, "E38.99.23.0", {"position": v(552.45, -74.08) * mm});
            skPoint(sketch, "E38.99.24.0", {"position": v(552.45, -80.43) * mm});
            skPoint(sketch, "E38.99.25.0", {"position": v(552.45, -86.78) * mm});
            skPoint(sketch, "E38.99.26.0", {"position": v(552.45, -93.13) * mm});
            skPoint(sketch, "E38.99.27.0", {"position": v(552.45, -99.48) * mm});
            skPoint(sketch, "E38.99.28.0", {"position": v(552.45, -105.83) * mm});
            skPoint(sketch, "E38.99.29.0", {"position": v(552.45, -112.18) * mm});
            skPoint(sketch, "E38.99.30.0", {"position": v(552.45, -118.53) * mm});
            skPoint(sketch, "E38.99.31.0", {"position": v(552.45, -124.88) * mm});
            skPoint(sketch, "E38.99.32.0", {"position": v(552.45, -131.23) * mm});
            skPoint(sketch, "E38.99.33.0", {"position": v(552.45, -137.58) * mm});
            skPoint(sketch, "E38.99.34.0", {"position": v(552.45, -143.93) * mm});
            skPoint(sketch, "E38.99.35.0", {"position": v(552.45, -150.28) * mm});
            skPoint(sketch, "E38.99.36.0", {"position": v(552.45, -156.63) * mm});
            skPoint(sketch, "E38.99.37.0", {"position": v(552.45, -162.98) * mm});
            skPoint(sketch, "E38.99.38.0", {"position": v(552.45, -169.33) * mm});
            skPoint(sketch, "E38.99.39.0", {"position": v(552.45, -175.68) * mm});
            skPoint(sketch, "E38.99.40.0", {"position": v(552.45, -182.03) * mm});
            skPoint(sketch, "E38.99.41.0", {"position": v(552.45, -188.38) * mm});
            skPoint(sketch, "E38.99.42.0", {"position": v(552.45, -194.73) * mm});
            skPoint(sketch, "E38.99.43.0", {"position": v(552.45, -201.08) * mm});
            skPoint(sketch, "E38.99.44.0", {"position": v(552.45, -207.43) * mm});
            skPoint(sketch, "E38.99.45.0", {"position": v(552.45, -213.78) * mm});
            skPoint(sketch, "E38.99.46.0", {"position": v(552.45, -220.13) * mm});
            skPoint(sketch, "E38.99.47.0", {"position": v(552.45, -226.48) * mm});
            skPoint(sketch, "E38.99.48.0", {"position": v(552.45, -232.83) * mm});
            skPoint(sketch, "E38.99.49.0", {"position": v(552.45, -239.18) * mm});
            skPoint(sketch, "E38.99.50.0", {"position": v(552.45, -245.53) * mm});
            skPoint(sketch, "E38.99.51.0", {"position": v(552.45, -251.88) * mm});
            skPoint(sketch, "E38.99.52.0", {"position": v(552.45, -258.23) * mm});
            skPoint(sketch, "E38.99.53.0", {"position": v(552.45, -264.58) * mm});
            skPoint(sketch, "E38.99.54.0", {"position": v(552.45, -270.93) * mm});
            skPoint(sketch, "E38.99.55.0", {"position": v(552.45, -277.28) * mm});
            skPoint(sketch, "E38.99.56.0", {"position": v(552.45, -283.63) * mm});
            skPoint(sketch, "E38.99.57.0", {"position": v(552.45, -289.98) * mm});
            skPoint(sketch, "E38.99.58.0", {"position": v(552.45, -296.33) * mm});
            skPoint(sketch, "E38.99.59.0", {"position": v(552.45, -302.68) * mm});
            skPoint(sketch, "E38.99.60.0", {"position": v(552.45, -309.03) * mm});
            skPoint(sketch, "E38.99.61.0", {"position": v(552.45, -315.38) * mm});
            skPoint(sketch, "E38.99.62.0", {"position": v(552.45, -321.73) * mm});
            skPoint(sketch, "E38.99.63.0", {"position": v(552.45, -328.08) * mm});
            skPoint(sketch, "E38.99.64.0", {"position": v(552.45, -334.43) * mm});
            skPoint(sketch, "E38.99.65.0", {"position": v(552.45, -340.78) * mm});
            skPoint(sketch, "E38.99.66.0", {"position": v(552.45, -347.13) * mm});
            skPoint(sketch, "E38.99.67.0", {"position": v(552.45, -353.48) * mm});
            skPoint(sketch, "E38.99.68.0", {"position": v(552.45, -359.83) * mm});
            skPoint(sketch, "E38.99.69.0", {"position": v(552.45, -366.18) * mm});
            skPoint(sketch, "E38.99.70.0", {"position": v(552.45, -372.53) * mm});
            skPoint(sketch, "E38.99.71.0", {"position": v(552.45, -378.88) * mm});
            skPoint(sketch, "E38.99.72.0", {"position": v(552.45, -385.23) * mm});
            skPoint(sketch, "E38.99.73.0", {"position": v(552.45, -391.58) * mm});
            skPoint(sketch, "E38.99.74.0", {"position": v(552.45, -397.93) * mm});
            skPoint(sketch, "E38.99.75.0", {"position": v(552.45, -404.28) * mm});
            skPoint(sketch, "E38.99.76.0", {"position": v(552.45, -410.63) * mm});
            skPoint(sketch, "E38.99.77.0", {"position": v(552.45, -416.98) * mm});
            skPoint(sketch, "E38.99.78.0", {"position": v(552.45, -423.33) * mm});
            skPoint(sketch, "E38.99.79.0", {"position": v(552.45, -429.68) * mm});
            skPoint(sketch, "E38.99.80.0", {"position": v(552.45, -436.03) * mm});
            skPoint(sketch, "E38.99.81.0", {"position": v(552.45, -442.38) * mm});
            skPoint(sketch, "E38.99.82.0", {"position": v(552.45, -448.73) * mm});
            skPoint(sketch, "E38.99.83.0", {"position": v(552.45, -455.08) * mm});
            skPoint(sketch, "E38.99.84.0", {"position": v(552.45, -461.43) * mm});
            skPoint(sketch, "E38.99.85.0", {"position": v(552.45, -467.78) * mm});
            skPoint(sketch, "E38.99.86.0", {"position": v(552.45, -474.13) * mm});
            skPoint(sketch, "E38.99.87.0", {"position": v(552.45, -480.48) * mm});
            skPoint(sketch, "E38.99.88.0", {"position": v(552.45, -486.83) * mm});
            skPoint(sketch, "E38.99.89.0", {"position": v(552.45, -493.18) * mm});
            skPoint(sketch, "E38.99.90.0", {"position": v(552.45, -499.53) * mm});
            skPoint(sketch, "E38.99.91.0", {"position": v(552.45, -505.88) * mm});
            skPoint(sketch, "E38.99.92.0", {"position": v(552.45, -512.23) * mm});
            skPoint(sketch, "E38.99.93.0", {"position": v(552.45, -518.58) * mm});
            skPoint(sketch, "E38.99.94.0", {"position": v(552.45, -524.93) * mm});
            skPoint(sketch, "E38.99.95.0", {"position": v(552.45, -531.28) * mm});
            skPoint(sketch, "E38.99.96.0", {"position": v(552.45, -537.63) * mm});
            skPoint(sketch, "E38.99.97.0", {"position": v(552.45, -543.98) * mm});
            skPoint(sketch, "E38.99.98.0", {"position": v(552.45, -550.33) * mm});
            skPoint(sketch, "E38.99.99.0", {"position": v(552.45, -556.68) * mm});
            skLineSegment(sketch, "E38.direction1", {"start": v(-76.2, 71.97) * mm, "end": v(-69.85, 71.97) * mm, "construction": true});
            skLineSegment(sketch, "E38.direction2", {"start": v(-76.2, 71.97) * mm, "end": v(-76.2, 65.62) * mm, "construction": true});
            skSolve(sketch);
        }
        {
            var Q0;
            Q0=qCreatedBy(makeId("Top.planeOp"),FACE);
            var sketch = newSketch(context, id + "F2", { "sketchPlane" : qUnion([Q0])});
            skCircle(sketch, "E39", {"center": v(-63.5, 59.27) * mm, "radius": 12.7 * mm});
            skCircle(sketch, "E40", {"center": v(-38.1, 59.27) * mm, "radius": 11.9 * mm});
            skCircle(sketch, "E41", {"center": v(-12.7, 59.27) * mm, "radius": 11.11 * mm});
            skCircle(sketch, "E42", {"center": v(12.7, 59.27) * mm, "radius": 10.32 * mm});
            skCircle(sketch, "E43", {"center": v(38.1, 59.27) * mm, "radius": 9.53 * mm});
            skCircle(sketch, "E44", {"center": v(63.5, 59.27) * mm, "radius": 9.13 * mm});
            skCircle(sketch, "E45", {"center": v(63.5, 33.87) * mm, "radius": 8.73 * mm});
            skCircle(sketch, "E46", {"center": v(44.45, 33.87) * mm, "radius": 8.33 * mm});
            skCircle(sketch, "E47", {"center": v(25.4, 33.87) * mm, "radius": 7.94 * mm});
            skCircle(sketch, "E48", {"center": v(6.35, 33.87) * mm, "radius": 7.54 * mm});
            skCircle(sketch, "E49", {"center": v(-12.7, 33.87) * mm, "radius": 7.14 * mm});
            skCircle(sketch, "E50", {"center": v(-31.75, 33.87) * mm, "radius": 6.75 * mm});
            skCircle(sketch, "E51", {"center": v(-50.8, 33.87) * mm, "radius": 6.35 * mm});
            skCircle(sketch, "E52", {"center": v(-69.85, 33.87) * mm, "radius": 5.95 * mm});
            skCircle(sketch, "E53", {"center": v(-69.85, 14.82) * mm, "radius": 5.56 * mm});
            skCircle(sketch, "E54", {"center": v(-57.15, 14.82) * mm, "radius": 5.16 * mm});
            skCircle(sketch, "E55", {"center": v(-44.45, 14.82) * mm, "radius": 4.76 * mm});
            skCircle(sketch, "E56", {"center": v(-31.75, 14.82) * mm, "radius": 4.37 * mm});
            skCircle(sketch, "E57", {"center": v(-19.05, 14.82) * mm, "radius": 4.17 * mm});
            skCircle(sketch, "E58", {"center": v(-6.35, 14.82) * mm, "radius": 3.97 * mm});
            skCircle(sketch, "E59", {"center": v(6.35, 14.82) * mm, "radius": 3.77 * mm});
            skCircle(sketch, "E60", {"center": v(19.05, 14.82) * mm, "radius": 3.57 * mm});
            skCircle(sketch, "E61", {"center": v(31.75, 14.82) * mm, "radius": 3.37 * mm});
            skCircle(sketch, "E62", {"center": v(44.45, 14.82) * mm, "radius": 3.18 * mm});
            skCircle(sketch, "E63", {"center": v(57.15, 14.82) * mm, "radius": 2.98 * mm});
            skCircle(sketch, "E64", {"center": v(69.85, 14.82) * mm, "radius": 2.78 * mm});
            skCircle(sketch, "E65", {"center": v(-69.85, -4.23) * mm, "radius": 2.58 * mm});
            skCircle(sketch, "E66", {"center": v(-57.15, -4.23) * mm, "radius": 2.38 * mm});
            skCircle(sketch, "E67", {"center": v(-44.45, -4.23) * mm, "radius": 2.18 * mm});
            skCircle(sketch, "E68", {"center": v(-31.75, -4.23) * mm, "radius": 1.98 * mm});
            skCircle(sketch, "E69", {"center": v(-19.05, -4.23) * mm, "radius": 1.79 * mm});
            skCircle(sketch, "E70", {"center": v(-6.35, -4.23) * mm, "radius": 1.59 * mm});
            skCircle(sketch, "E71", {"center": v(0, -4.23) * mm, "radius": 1.39 * mm});
            skCircle(sketch, "E72", {"center": v(6.35, -4.23) * mm, "radius": 1.2 * mm});
            skCircle(sketch, "E73", {"center": v(12.7, -4.23) * mm, "radius": 1 * mm});
            skCircle(sketch, "E74", {"center": v(19.05, -4.23) * mm, "radius": 0.8 * mm});
            skSolve(sketch);
        }
        {
            var Q0;
            Q0=qSketchRegion(id+"F2",true);
            extrude(context, id + "F3", {"entities" : qUnion([Q0]), "endBound" : BoundingType.SYMMETRIC, "depth" : 25.4 * mm});
        }
    });
